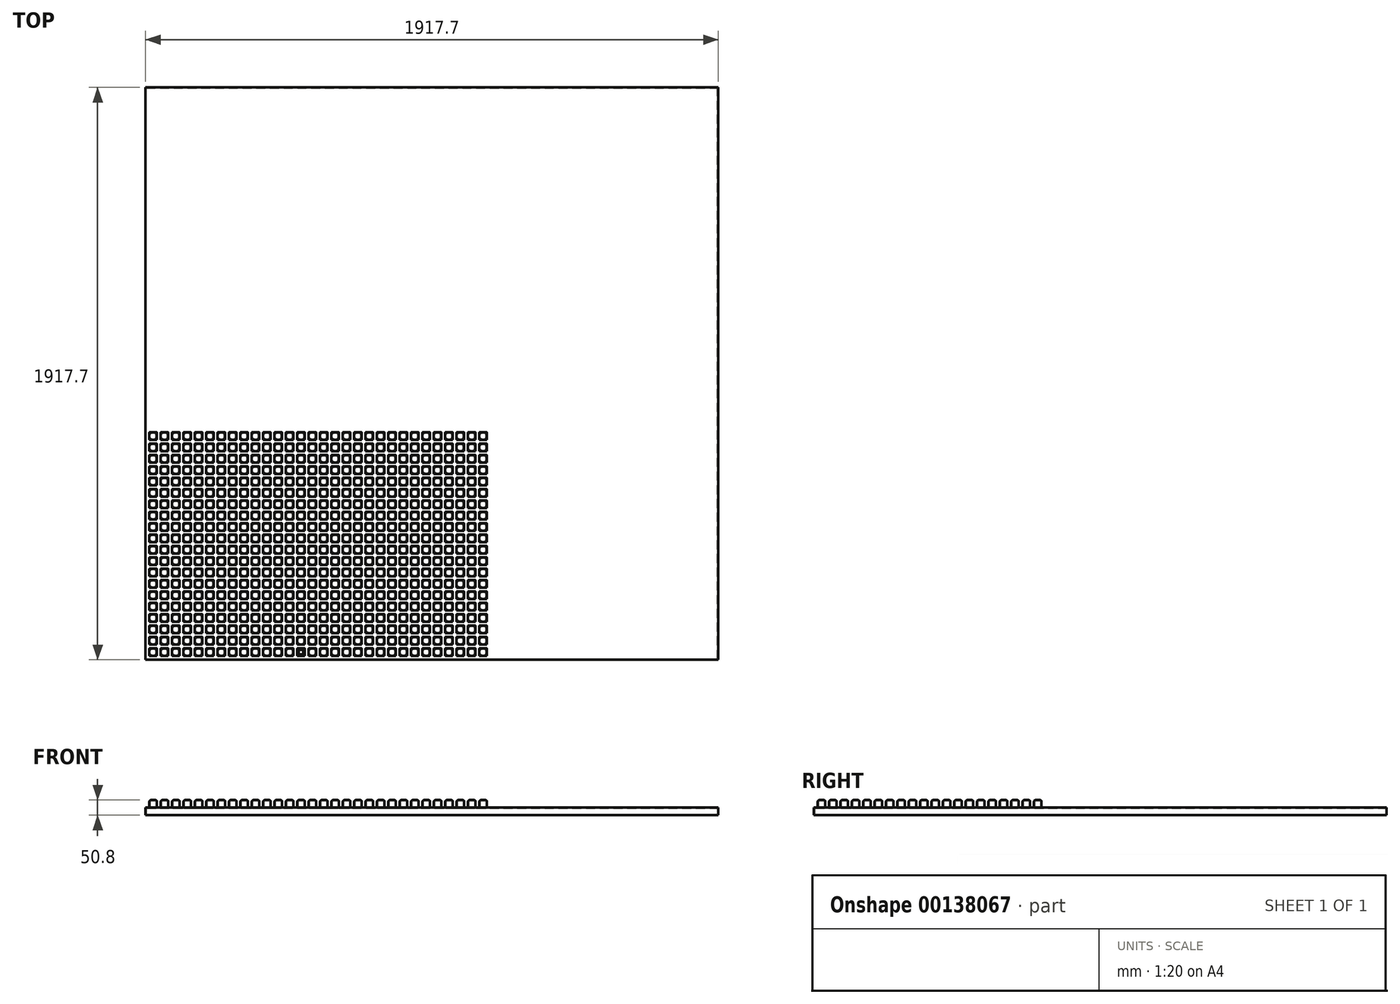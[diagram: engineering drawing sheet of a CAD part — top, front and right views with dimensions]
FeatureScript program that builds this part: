
annotation { "Feature Type Name" : "Feature", "Feature Type Description" : "" }
export const myFeature = defineFeature(function(context is Context, id is Id, definition is map)
    precondition{}
    {
        {
            var Q0;
            Q0=qCreatedBy(makeId("Top.planeOp"),FACE);
            var sketch = newSketch(context, id + "F0", { "sketchPlane" : qUnion([Q0])});
            skLineSegment(sketch, "E0.bottom", {"start": v(0, 0) * mm, "end": v(1917.7, 0) * mm});
            skLineSegment(sketch, "E0.top", {"start": v(0, 1917.7) * mm, "end": v(1917.7, 1917.7) * mm});
            skLineSegment(sketch, "E0.left", {"start": v(0, 0) * mm, "end": v(0, 1917.7) * mm});
            skLineSegment(sketch, "E0.right", {"start": v(1917.7, 0) * mm, "end": v(1917.7, 1917.7) * mm});
            skSolve(sketch);
        }
        {
            var Q0;
            Q0=makeQuery(id+"F0.imprint","IMPRINT",FACE,{"disambiguationData":[TD([[makeQuery(id+"F0.imprint","IMPRINT",EDGE,{"derivedFrom":sQuery(id+"F0.wireOp",EDGE,"E0.bottom")}),1.0]])]});
            extrude(context, id + "F1", {"entities" : qUnion([Q0]), "depth" : 25.4 * mm});
        }
        {
            var Q0;
            Q0=makeQuery(id+"F1.opExtrude","CAP_FACE",FACE,{"disambiguationData":[OSD([sQuery(id+"F0.wireOp",EDGE,"E0.bottom"),sQuery(id+"F0.wireOp",EDGE,"E0.top"),sQuery(id+"F0.wireOp",EDGE,"E0.left"),sQuery(id+"F0.wireOp",EDGE,"E0.right")])],"isStart":false});
            var sketch = newSketch(context, id + "F2", { "sketchPlane" : qUnion([Q0])});
            skLineSegment(sketch, "E1.bottom", {"start": v(12.7, 12.7) * mm, "end": v(38.1, 12.7) * mm});
            skLineSegment(sketch, "E1.top", {"start": v(12.7, 38.1) * mm, "end": v(38.1, 38.1) * mm});
            skLineSegment(sketch, "E1.left", {"start": v(12.7, 12.7) * mm, "end": v(12.7, 38.1) * mm});
            skLineSegment(sketch, "E1.right", {"start": v(38.1, 12.7) * mm, "end": v(38.1, 38.1) * mm});
            skLineSegment(sketch, "E2.0.1.0", {"start": v(38.1, 50.8) * mm, "end": v(38.1, 76.2) * mm});
            skLineSegment(sketch, "E2.0.1.1", {"start": v(12.7, 76.2) * mm, "end": v(38.1, 76.2) * mm});
            skLineSegment(sketch, "E2.0.1.2", {"start": v(12.7, 50.8) * mm, "end": v(38.1, 50.8) * mm});
            skLineSegment(sketch, "E2.0.1.3", {"start": v(12.7, 50.8) * mm, "end": v(12.7, 76.2) * mm});
            skLineSegment(sketch, "E2.0.2.0", {"start": v(38.1, 88.9) * mm, "end": v(38.1, 114.3) * mm});
            skLineSegment(sketch, "E2.0.2.1", {"start": v(12.7, 114.3) * mm, "end": v(38.1, 114.3) * mm});
            skLineSegment(sketch, "E2.0.2.2", {"start": v(12.7, 88.9) * mm, "end": v(38.1, 88.9) * mm});
            skLineSegment(sketch, "E2.0.2.3", {"start": v(12.7, 88.9) * mm, "end": v(12.7, 114.3) * mm});
            skLineSegment(sketch, "E2.0.3.0", {"start": v(38.1, 127) * mm, "end": v(38.1, 152.4) * mm});
            skLineSegment(sketch, "E2.0.3.1", {"start": v(12.7, 152.4) * mm, "end": v(38.1, 152.4) * mm});
            skLineSegment(sketch, "E2.0.3.2", {"start": v(12.7, 127) * mm, "end": v(38.1, 127) * mm});
            skLineSegment(sketch, "E2.0.3.3", {"start": v(12.7, 127) * mm, "end": v(12.7, 152.4) * mm});
            skLineSegment(sketch, "E2.0.4.0", {"start": v(38.1, 165.1) * mm, "end": v(38.1, 190.5) * mm});
            skLineSegment(sketch, "E2.0.4.1", {"start": v(12.7, 190.5) * mm, "end": v(38.1, 190.5) * mm});
            skLineSegment(sketch, "E2.0.4.2", {"start": v(12.7, 165.1) * mm, "end": v(38.1, 165.1) * mm});
            skLineSegment(sketch, "E2.0.4.3", {"start": v(12.7, 165.1) * mm, "end": v(12.7, 190.5) * mm});
            skLineSegment(sketch, "E2.0.5.0", {"start": v(38.1, 203.2) * mm, "end": v(38.1, 228.6) * mm});
            skLineSegment(sketch, "E2.0.5.1", {"start": v(12.7, 228.6) * mm, "end": v(38.1, 228.6) * mm});
            skLineSegment(sketch, "E2.0.5.2", {"start": v(12.7, 203.2) * mm, "end": v(38.1, 203.2) * mm});
            skLineSegment(sketch, "E2.0.5.3", {"start": v(12.7, 203.2) * mm, "end": v(12.7, 228.6) * mm});
            skLineSegment(sketch, "E2.0.6.0", {"start": v(38.1, 241.3) * mm, "end": v(38.1, 266.7) * mm});
            skLineSegment(sketch, "E2.0.6.1", {"start": v(12.7, 266.7) * mm, "end": v(38.1, 266.7) * mm});
            skLineSegment(sketch, "E2.0.6.2", {"start": v(12.7, 241.3) * mm, "end": v(38.1, 241.3) * mm});
            skLineSegment(sketch, "E2.0.6.3", {"start": v(12.7, 241.3) * mm, "end": v(12.7, 266.7) * mm});
            skLineSegment(sketch, "E2.0.7.0", {"start": v(38.1, 279.4) * mm, "end": v(38.1, 304.8) * mm});
            skLineSegment(sketch, "E2.0.7.1", {"start": v(12.7, 304.8) * mm, "end": v(38.1, 304.8) * mm});
            skLineSegment(sketch, "E2.0.7.2", {"start": v(12.7, 279.4) * mm, "end": v(38.1, 279.4) * mm});
            skLineSegment(sketch, "E2.0.7.3", {"start": v(12.7, 279.4) * mm, "end": v(12.7, 304.8) * mm});
            skLineSegment(sketch, "E2.0.8.0", {"start": v(38.1, 317.5) * mm, "end": v(38.1, 342.9) * mm});
            skLineSegment(sketch, "E2.0.8.1", {"start": v(12.7, 342.9) * mm, "end": v(38.1, 342.9) * mm});
            skLineSegment(sketch, "E2.0.8.2", {"start": v(12.7, 317.5) * mm, "end": v(38.1, 317.5) * mm});
            skLineSegment(sketch, "E2.0.8.3", {"start": v(12.7, 317.5) * mm, "end": v(12.7, 342.9) * mm});
            skLineSegment(sketch, "E2.0.9.0", {"start": v(38.1, 355.6) * mm, "end": v(38.1, 381) * mm});
            skLineSegment(sketch, "E2.0.9.1", {"start": v(12.7, 381) * mm, "end": v(38.1, 381) * mm});
            skLineSegment(sketch, "E2.0.9.2", {"start": v(12.7, 355.6) * mm, "end": v(38.1, 355.6) * mm});
            skLineSegment(sketch, "E2.0.9.3", {"start": v(12.7, 355.6) * mm, "end": v(12.7, 381) * mm});
            skLineSegment(sketch, "E2.0.10.0", {"start": v(38.1, 393.7) * mm, "end": v(38.1, 419.1) * mm});
            skLineSegment(sketch, "E2.0.10.1", {"start": v(12.7, 419.1) * mm, "end": v(38.1, 419.1) * mm});
            skLineSegment(sketch, "E2.0.10.2", {"start": v(12.7, 393.7) * mm, "end": v(38.1, 393.7) * mm});
            skLineSegment(sketch, "E2.0.10.3", {"start": v(12.7, 393.7) * mm, "end": v(12.7, 419.1) * mm});
            skLineSegment(sketch, "E2.0.11.0", {"start": v(38.1, 431.8) * mm, "end": v(38.1, 457.2) * mm});
            skLineSegment(sketch, "E2.0.11.1", {"start": v(12.7, 457.2) * mm, "end": v(38.1, 457.2) * mm});
            skLineSegment(sketch, "E2.0.11.2", {"start": v(12.7, 431.8) * mm, "end": v(38.1, 431.8) * mm});
            skLineSegment(sketch, "E2.0.11.3", {"start": v(12.7, 431.8) * mm, "end": v(12.7, 457.2) * mm});
            skLineSegment(sketch, "E2.0.12.0", {"start": v(38.1, 469.9) * mm, "end": v(38.1, 495.3) * mm});
            skLineSegment(sketch, "E2.0.12.1", {"start": v(12.7, 495.3) * mm, "end": v(38.1, 495.3) * mm});
            skLineSegment(sketch, "E2.0.12.2", {"start": v(12.7, 469.9) * mm, "end": v(38.1, 469.9) * mm});
            skLineSegment(sketch, "E2.0.12.3", {"start": v(12.7, 469.9) * mm, "end": v(12.7, 495.3) * mm});
            skLineSegment(sketch, "E2.0.13.0", {"start": v(38.1, 508) * mm, "end": v(38.1, 533.4) * mm});
            skLineSegment(sketch, "E2.0.13.1", {"start": v(12.7, 533.4) * mm, "end": v(38.1, 533.4) * mm});
            skLineSegment(sketch, "E2.0.13.2", {"start": v(12.7, 508) * mm, "end": v(38.1, 508) * mm});
            skLineSegment(sketch, "E2.0.13.3", {"start": v(12.7, 508) * mm, "end": v(12.7, 533.4) * mm});
            skLineSegment(sketch, "E2.0.14.0", {"start": v(38.1, 546.1) * mm, "end": v(38.1, 571.5) * mm});
            skLineSegment(sketch, "E2.0.14.1", {"start": v(12.7, 571.5) * mm, "end": v(38.1, 571.5) * mm});
            skLineSegment(sketch, "E2.0.14.2", {"start": v(12.7, 546.1) * mm, "end": v(38.1, 546.1) * mm});
            skLineSegment(sketch, "E2.0.14.3", {"start": v(12.7, 546.1) * mm, "end": v(12.7, 571.5) * mm});
            skLineSegment(sketch, "E2.0.15.0", {"start": v(38.1, 584.2) * mm, "end": v(38.1, 609.6) * mm});
            skLineSegment(sketch, "E2.0.15.1", {"start": v(12.7, 609.6) * mm, "end": v(38.1, 609.6) * mm});
            skLineSegment(sketch, "E2.0.15.2", {"start": v(12.7, 584.2) * mm, "end": v(38.1, 584.2) * mm});
            skLineSegment(sketch, "E2.0.15.3", {"start": v(12.7, 584.2) * mm, "end": v(12.7, 609.6) * mm});
            skLineSegment(sketch, "E2.0.16.0", {"start": v(38.1, 622.3) * mm, "end": v(38.1, 647.7) * mm});
            skLineSegment(sketch, "E2.0.16.1", {"start": v(12.7, 647.7) * mm, "end": v(38.1, 647.7) * mm});
            skLineSegment(sketch, "E2.0.16.2", {"start": v(12.7, 622.3) * mm, "end": v(38.1, 622.3) * mm});
            skLineSegment(sketch, "E2.0.16.3", {"start": v(12.7, 622.3) * mm, "end": v(12.7, 647.7) * mm});
            skLineSegment(sketch, "E2.0.17.0", {"start": v(38.1, 660.4) * mm, "end": v(38.1, 685.8) * mm});
            skLineSegment(sketch, "E2.0.17.1", {"start": v(12.7, 685.8) * mm, "end": v(38.1, 685.8) * mm});
            skLineSegment(sketch, "E2.0.17.2", {"start": v(12.7, 660.4) * mm, "end": v(38.1, 660.4) * mm});
            skLineSegment(sketch, "E2.0.17.3", {"start": v(12.7, 660.4) * mm, "end": v(12.7, 685.8) * mm});
            skLineSegment(sketch, "E2.0.18.0", {"start": v(38.1, 698.5) * mm, "end": v(38.1, 723.9) * mm});
            skLineSegment(sketch, "E2.0.18.1", {"start": v(12.7, 723.9) * mm, "end": v(38.1, 723.9) * mm});
            skLineSegment(sketch, "E2.0.18.2", {"start": v(12.7, 698.5) * mm, "end": v(38.1, 698.5) * mm});
            skLineSegment(sketch, "E2.0.18.3", {"start": v(12.7, 698.5) * mm, "end": v(12.7, 723.9) * mm});
            skLineSegment(sketch, "E2.0.19.0", {"start": v(38.1, 736.6) * mm, "end": v(38.1, 762) * mm});
            skLineSegment(sketch, "E2.0.19.1", {"start": v(12.7, 762) * mm, "end": v(38.1, 762) * mm});
            skLineSegment(sketch, "E2.0.19.2", {"start": v(12.7, 736.6) * mm, "end": v(38.1, 736.6) * mm});
            skLineSegment(sketch, "E2.0.19.3", {"start": v(12.7, 736.6) * mm, "end": v(12.7, 762) * mm});
            skLineSegment(sketch, "E2.1.0.0", {"start": v(76.2, 12.7) * mm, "end": v(76.2, 38.1) * mm});
            skLineSegment(sketch, "E2.1.0.1", {"start": v(50.8, 38.1) * mm, "end": v(76.2, 38.1) * mm});
            skLineSegment(sketch, "E2.1.0.2", {"start": v(50.8, 12.7) * mm, "end": v(76.2, 12.7) * mm});
            skLineSegment(sketch, "E2.1.0.3", {"start": v(50.8, 12.7) * mm, "end": v(50.8, 38.1) * mm});
            skLineSegment(sketch, "E2.1.1.0", {"start": v(76.2, 50.8) * mm, "end": v(76.2, 76.2) * mm});
            skLineSegment(sketch, "E2.1.1.1", {"start": v(50.8, 76.2) * mm, "end": v(76.2, 76.2) * mm});
            skLineSegment(sketch, "E2.1.1.2", {"start": v(50.8, 50.8) * mm, "end": v(76.2, 50.8) * mm});
            skLineSegment(sketch, "E2.1.1.3", {"start": v(50.8, 50.8) * mm, "end": v(50.8, 76.2) * mm});
            skLineSegment(sketch, "E2.1.2.0", {"start": v(76.2, 88.9) * mm, "end": v(76.2, 114.3) * mm});
            skLineSegment(sketch, "E2.1.2.1", {"start": v(50.8, 114.3) * mm, "end": v(76.2, 114.3) * mm});
            skLineSegment(sketch, "E2.1.2.2", {"start": v(50.8, 88.9) * mm, "end": v(76.2, 88.9) * mm});
            skLineSegment(sketch, "E2.1.2.3", {"start": v(50.8, 88.9) * mm, "end": v(50.8, 114.3) * mm});
            skLineSegment(sketch, "E2.1.3.0", {"start": v(76.2, 127) * mm, "end": v(76.2, 152.4) * mm});
            skLineSegment(sketch, "E2.1.3.1", {"start": v(50.8, 152.4) * mm, "end": v(76.2, 152.4) * mm});
            skLineSegment(sketch, "E2.1.3.2", {"start": v(50.8, 127) * mm, "end": v(76.2, 127) * mm});
            skLineSegment(sketch, "E2.1.3.3", {"start": v(50.8, 127) * mm, "end": v(50.8, 152.4) * mm});
            skLineSegment(sketch, "E2.1.4.0", {"start": v(76.2, 165.1) * mm, "end": v(76.2, 190.5) * mm});
            skLineSegment(sketch, "E2.1.4.1", {"start": v(50.8, 190.5) * mm, "end": v(76.2, 190.5) * mm});
            skLineSegment(sketch, "E2.1.4.2", {"start": v(50.8, 165.1) * mm, "end": v(76.2, 165.1) * mm});
            skLineSegment(sketch, "E2.1.4.3", {"start": v(50.8, 165.1) * mm, "end": v(50.8, 190.5) * mm});
            skLineSegment(sketch, "E2.1.5.0", {"start": v(76.2, 203.2) * mm, "end": v(76.2, 228.6) * mm});
            skLineSegment(sketch, "E2.1.5.1", {"start": v(50.8, 228.6) * mm, "end": v(76.2, 228.6) * mm});
            skLineSegment(sketch, "E2.1.5.2", {"start": v(50.8, 203.2) * mm, "end": v(76.2, 203.2) * mm});
            skLineSegment(sketch, "E2.1.5.3", {"start": v(50.8, 203.2) * mm, "end": v(50.8, 228.6) * mm});
            skLineSegment(sketch, "E2.1.6.0", {"start": v(76.2, 241.3) * mm, "end": v(76.2, 266.7) * mm});
            skLineSegment(sketch, "E2.1.6.1", {"start": v(50.8, 266.7) * mm, "end": v(76.2, 266.7) * mm});
            skLineSegment(sketch, "E2.1.6.2", {"start": v(50.8, 241.3) * mm, "end": v(76.2, 241.3) * mm});
            skLineSegment(sketch, "E2.1.6.3", {"start": v(50.8, 241.3) * mm, "end": v(50.8, 266.7) * mm});
            skLineSegment(sketch, "E2.1.7.0", {"start": v(76.2, 279.4) * mm, "end": v(76.2, 304.8) * mm});
            skLineSegment(sketch, "E2.1.7.1", {"start": v(50.8, 304.8) * mm, "end": v(76.2, 304.8) * mm});
            skLineSegment(sketch, "E2.1.7.2", {"start": v(50.8, 279.4) * mm, "end": v(76.2, 279.4) * mm});
            skLineSegment(sketch, "E2.1.7.3", {"start": v(50.8, 279.4) * mm, "end": v(50.8, 304.8) * mm});
            skLineSegment(sketch, "E2.1.8.0", {"start": v(76.2, 317.5) * mm, "end": v(76.2, 342.9) * mm});
            skLineSegment(sketch, "E2.1.8.1", {"start": v(50.8, 342.9) * mm, "end": v(76.2, 342.9) * mm});
            skLineSegment(sketch, "E2.1.8.2", {"start": v(50.8, 317.5) * mm, "end": v(76.2, 317.5) * mm});
            skLineSegment(sketch, "E2.1.8.3", {"start": v(50.8, 317.5) * mm, "end": v(50.8, 342.9) * mm});
            skLineSegment(sketch, "E2.1.9.0", {"start": v(76.2, 355.6) * mm, "end": v(76.2, 381) * mm});
            skLineSegment(sketch, "E2.1.9.1", {"start": v(50.8, 381) * mm, "end": v(76.2, 381) * mm});
            skLineSegment(sketch, "E2.1.9.2", {"start": v(50.8, 355.6) * mm, "end": v(76.2, 355.6) * mm});
            skLineSegment(sketch, "E2.1.9.3", {"start": v(50.8, 355.6) * mm, "end": v(50.8, 381) * mm});
            skLineSegment(sketch, "E2.1.10.0", {"start": v(76.2, 393.7) * mm, "end": v(76.2, 419.1) * mm});
            skLineSegment(sketch, "E2.1.10.1", {"start": v(50.8, 419.1) * mm, "end": v(76.2, 419.1) * mm});
            skLineSegment(sketch, "E2.1.10.2", {"start": v(50.8, 393.7) * mm, "end": v(76.2, 393.7) * mm});
            skLineSegment(sketch, "E2.1.10.3", {"start": v(50.8, 393.7) * mm, "end": v(50.8, 419.1) * mm});
            skLineSegment(sketch, "E2.1.11.0", {"start": v(76.2, 431.8) * mm, "end": v(76.2, 457.2) * mm});
            skLineSegment(sketch, "E2.1.11.1", {"start": v(50.8, 457.2) * mm, "end": v(76.2, 457.2) * mm});
            skLineSegment(sketch, "E2.1.11.2", {"start": v(50.8, 431.8) * mm, "end": v(76.2, 431.8) * mm});
            skLineSegment(sketch, "E2.1.11.3", {"start": v(50.8, 431.8) * mm, "end": v(50.8, 457.2) * mm});
            skLineSegment(sketch, "E2.1.12.0", {"start": v(76.2, 469.9) * mm, "end": v(76.2, 495.3) * mm});
            skLineSegment(sketch, "E2.1.12.1", {"start": v(50.8, 495.3) * mm, "end": v(76.2, 495.3) * mm});
            skLineSegment(sketch, "E2.1.12.2", {"start": v(50.8, 469.9) * mm, "end": v(76.2, 469.9) * mm});
            skLineSegment(sketch, "E2.1.12.3", {"start": v(50.8, 469.9) * mm, "end": v(50.8, 495.3) * mm});
            skLineSegment(sketch, "E2.1.13.0", {"start": v(76.2, 508) * mm, "end": v(76.2, 533.4) * mm});
            skLineSegment(sketch, "E2.1.13.1", {"start": v(50.8, 533.4) * mm, "end": v(76.2, 533.4) * mm});
            skLineSegment(sketch, "E2.1.13.2", {"start": v(50.8, 508) * mm, "end": v(76.2, 508) * mm});
            skLineSegment(sketch, "E2.1.13.3", {"start": v(50.8, 508) * mm, "end": v(50.8, 533.4) * mm});
            skLineSegment(sketch, "E2.1.14.0", {"start": v(76.2, 546.1) * mm, "end": v(76.2, 571.5) * mm});
            skLineSegment(sketch, "E2.1.14.1", {"start": v(50.8, 571.5) * mm, "end": v(76.2, 571.5) * mm});
            skLineSegment(sketch, "E2.1.14.2", {"start": v(50.8, 546.1) * mm, "end": v(76.2, 546.1) * mm});
            skLineSegment(sketch, "E2.1.14.3", {"start": v(50.8, 546.1) * mm, "end": v(50.8, 571.5) * mm});
            skLineSegment(sketch, "E2.1.15.0", {"start": v(76.2, 584.2) * mm, "end": v(76.2, 609.6) * mm});
            skLineSegment(sketch, "E2.1.15.1", {"start": v(50.8, 609.6) * mm, "end": v(76.2, 609.6) * mm});
            skLineSegment(sketch, "E2.1.15.2", {"start": v(50.8, 584.2) * mm, "end": v(76.2, 584.2) * mm});
            skLineSegment(sketch, "E2.1.15.3", {"start": v(50.8, 584.2) * mm, "end": v(50.8, 609.6) * mm});
            skLineSegment(sketch, "E2.1.16.0", {"start": v(76.2, 622.3) * mm, "end": v(76.2, 647.7) * mm});
            skLineSegment(sketch, "E2.1.16.1", {"start": v(50.8, 647.7) * mm, "end": v(76.2, 647.7) * mm});
            skLineSegment(sketch, "E2.1.16.2", {"start": v(50.8, 622.3) * mm, "end": v(76.2, 622.3) * mm});
            skLineSegment(sketch, "E2.1.16.3", {"start": v(50.8, 622.3) * mm, "end": v(50.8, 647.7) * mm});
            skLineSegment(sketch, "E2.1.17.0", {"start": v(76.2, 660.4) * mm, "end": v(76.2, 685.8) * mm});
            skLineSegment(sketch, "E2.1.17.1", {"start": v(50.8, 685.8) * mm, "end": v(76.2, 685.8) * mm});
            skLineSegment(sketch, "E2.1.17.2", {"start": v(50.8, 660.4) * mm, "end": v(76.2, 660.4) * mm});
            skLineSegment(sketch, "E2.1.17.3", {"start": v(50.8, 660.4) * mm, "end": v(50.8, 685.8) * mm});
            skLineSegment(sketch, "E2.1.18.0", {"start": v(76.2, 698.5) * mm, "end": v(76.2, 723.9) * mm});
            skLineSegment(sketch, "E2.1.18.1", {"start": v(50.8, 723.9) * mm, "end": v(76.2, 723.9) * mm});
            skLineSegment(sketch, "E2.1.18.2", {"start": v(50.8, 698.5) * mm, "end": v(76.2, 698.5) * mm});
            skLineSegment(sketch, "E2.1.18.3", {"start": v(50.8, 698.5) * mm, "end": v(50.8, 723.9) * mm});
            skLineSegment(sketch, "E2.1.19.0", {"start": v(76.2, 736.6) * mm, "end": v(76.2, 762) * mm});
            skLineSegment(sketch, "E2.1.19.1", {"start": v(50.8, 762) * mm, "end": v(76.2, 762) * mm});
            skLineSegment(sketch, "E2.1.19.2", {"start": v(50.8, 736.6) * mm, "end": v(76.2, 736.6) * mm});
            skLineSegment(sketch, "E2.1.19.3", {"start": v(50.8, 736.6) * mm, "end": v(50.8, 762) * mm});
            skLineSegment(sketch, "E2.2.0.0", {"start": v(114.3, 12.7) * mm, "end": v(114.3, 38.1) * mm});
            skLineSegment(sketch, "E2.2.0.1", {"start": v(88.9, 38.1) * mm, "end": v(114.3, 38.1) * mm});
            skLineSegment(sketch, "E2.2.0.2", {"start": v(88.9, 12.7) * mm, "end": v(114.3, 12.7) * mm});
            skLineSegment(sketch, "E2.2.0.3", {"start": v(88.9, 12.7) * mm, "end": v(88.9, 38.1) * mm});
            skLineSegment(sketch, "E2.2.1.0", {"start": v(114.3, 50.8) * mm, "end": v(114.3, 76.2) * mm});
            skLineSegment(sketch, "E2.2.1.1", {"start": v(88.9, 76.2) * mm, "end": v(114.3, 76.2) * mm});
            skLineSegment(sketch, "E2.2.1.2", {"start": v(88.9, 50.8) * mm, "end": v(114.3, 50.8) * mm});
            skLineSegment(sketch, "E2.2.1.3", {"start": v(88.9, 50.8) * mm, "end": v(88.9, 76.2) * mm});
            skLineSegment(sketch, "E2.2.2.0", {"start": v(114.3, 88.9) * mm, "end": v(114.3, 114.3) * mm});
            skLineSegment(sketch, "E2.2.2.1", {"start": v(88.9, 114.3) * mm, "end": v(114.3, 114.3) * mm});
            skLineSegment(sketch, "E2.2.2.2", {"start": v(88.9, 88.9) * mm, "end": v(114.3, 88.9) * mm});
            skLineSegment(sketch, "E2.2.2.3", {"start": v(88.9, 88.9) * mm, "end": v(88.9, 114.3) * mm});
            skLineSegment(sketch, "E2.2.3.0", {"start": v(114.3, 127) * mm, "end": v(114.3, 152.4) * mm});
            skLineSegment(sketch, "E2.2.3.1", {"start": v(88.9, 152.4) * mm, "end": v(114.3, 152.4) * mm});
            skLineSegment(sketch, "E2.2.3.2", {"start": v(88.9, 127) * mm, "end": v(114.3, 127) * mm});
            skLineSegment(sketch, "E2.2.3.3", {"start": v(88.9, 127) * mm, "end": v(88.9, 152.4) * mm});
            skLineSegment(sketch, "E2.2.4.0", {"start": v(114.3, 165.1) * mm, "end": v(114.3, 190.5) * mm});
            skLineSegment(sketch, "E2.2.4.1", {"start": v(88.9, 190.5) * mm, "end": v(114.3, 190.5) * mm});
            skLineSegment(sketch, "E2.2.4.2", {"start": v(88.9, 165.1) * mm, "end": v(114.3, 165.1) * mm});
            skLineSegment(sketch, "E2.2.4.3", {"start": v(88.9, 165.1) * mm, "end": v(88.9, 190.5) * mm});
            skLineSegment(sketch, "E2.2.5.0", {"start": v(114.3, 203.2) * mm, "end": v(114.3, 228.6) * mm});
            skLineSegment(sketch, "E2.2.5.1", {"start": v(88.9, 228.6) * mm, "end": v(114.3, 228.6) * mm});
            skLineSegment(sketch, "E2.2.5.2", {"start": v(88.9, 203.2) * mm, "end": v(114.3, 203.2) * mm});
            skLineSegment(sketch, "E2.2.5.3", {"start": v(88.9, 203.2) * mm, "end": v(88.9, 228.6) * mm});
            skLineSegment(sketch, "E2.2.6.0", {"start": v(114.3, 241.3) * mm, "end": v(114.3, 266.7) * mm});
            skLineSegment(sketch, "E2.2.6.1", {"start": v(88.9, 266.7) * mm, "end": v(114.3, 266.7) * mm});
            skLineSegment(sketch, "E2.2.6.2", {"start": v(88.9, 241.3) * mm, "end": v(114.3, 241.3) * mm});
            skLineSegment(sketch, "E2.2.6.3", {"start": v(88.9, 241.3) * mm, "end": v(88.9, 266.7) * mm});
            skLineSegment(sketch, "E2.2.7.0", {"start": v(114.3, 279.4) * mm, "end": v(114.3, 304.8) * mm});
            skLineSegment(sketch, "E2.2.7.1", {"start": v(88.9, 304.8) * mm, "end": v(114.3, 304.8) * mm});
            skLineSegment(sketch, "E2.2.7.2", {"start": v(88.9, 279.4) * mm, "end": v(114.3, 279.4) * mm});
            skLineSegment(sketch, "E2.2.7.3", {"start": v(88.9, 279.4) * mm, "end": v(88.9, 304.8) * mm});
            skLineSegment(sketch, "E2.2.8.0", {"start": v(114.3, 317.5) * mm, "end": v(114.3, 342.9) * mm});
            skLineSegment(sketch, "E2.2.8.1", {"start": v(88.9, 342.9) * mm, "end": v(114.3, 342.9) * mm});
            skLineSegment(sketch, "E2.2.8.2", {"start": v(88.9, 317.5) * mm, "end": v(114.3, 317.5) * mm});
            skLineSegment(sketch, "E2.2.8.3", {"start": v(88.9, 317.5) * mm, "end": v(88.9, 342.9) * mm});
            skLineSegment(sketch, "E2.2.9.0", {"start": v(114.3, 355.6) * mm, "end": v(114.3, 381) * mm});
            skLineSegment(sketch, "E2.2.9.1", {"start": v(88.9, 381) * mm, "end": v(114.3, 381) * mm});
            skLineSegment(sketch, "E2.2.9.2", {"start": v(88.9, 355.6) * mm, "end": v(114.3, 355.6) * mm});
            skLineSegment(sketch, "E2.2.9.3", {"start": v(88.9, 355.6) * mm, "end": v(88.9, 381) * mm});
            skLineSegment(sketch, "E2.2.10.0", {"start": v(114.3, 393.7) * mm, "end": v(114.3, 419.1) * mm});
            skLineSegment(sketch, "E2.2.10.1", {"start": v(88.9, 419.1) * mm, "end": v(114.3, 419.1) * mm});
            skLineSegment(sketch, "E2.2.10.2", {"start": v(88.9, 393.7) * mm, "end": v(114.3, 393.7) * mm});
            skLineSegment(sketch, "E2.2.10.3", {"start": v(88.9, 393.7) * mm, "end": v(88.9, 419.1) * mm});
            skLineSegment(sketch, "E2.2.11.0", {"start": v(114.3, 431.8) * mm, "end": v(114.3, 457.2) * mm});
            skLineSegment(sketch, "E2.2.11.1", {"start": v(88.9, 457.2) * mm, "end": v(114.3, 457.2) * mm});
            skLineSegment(sketch, "E2.2.11.2", {"start": v(88.9, 431.8) * mm, "end": v(114.3, 431.8) * mm});
            skLineSegment(sketch, "E2.2.11.3", {"start": v(88.9, 431.8) * mm, "end": v(88.9, 457.2) * mm});
            skLineSegment(sketch, "E2.2.12.0", {"start": v(114.3, 469.9) * mm, "end": v(114.3, 495.3) * mm});
            skLineSegment(sketch, "E2.2.12.1", {"start": v(88.9, 495.3) * mm, "end": v(114.3, 495.3) * mm});
            skLineSegment(sketch, "E2.2.12.2", {"start": v(88.9, 469.9) * mm, "end": v(114.3, 469.9) * mm});
            skLineSegment(sketch, "E2.2.12.3", {"start": v(88.9, 469.9) * mm, "end": v(88.9, 495.3) * mm});
            skLineSegment(sketch, "E2.2.13.0", {"start": v(114.3, 508) * mm, "end": v(114.3, 533.4) * mm});
            skLineSegment(sketch, "E2.2.13.1", {"start": v(88.9, 533.4) * mm, "end": v(114.3, 533.4) * mm});
            skLineSegment(sketch, "E2.2.13.2", {"start": v(88.9, 508) * mm, "end": v(114.3, 508) * mm});
            skLineSegment(sketch, "E2.2.13.3", {"start": v(88.9, 508) * mm, "end": v(88.9, 533.4) * mm});
            skLineSegment(sketch, "E2.2.14.0", {"start": v(114.3, 546.1) * mm, "end": v(114.3, 571.5) * mm});
            skLineSegment(sketch, "E2.2.14.1", {"start": v(88.9, 571.5) * mm, "end": v(114.3, 571.5) * mm});
            skLineSegment(sketch, "E2.2.14.2", {"start": v(88.9, 546.1) * mm, "end": v(114.3, 546.1) * mm});
            skLineSegment(sketch, "E2.2.14.3", {"start": v(88.9, 546.1) * mm, "end": v(88.9, 571.5) * mm});
            skLineSegment(sketch, "E2.2.15.0", {"start": v(114.3, 584.2) * mm, "end": v(114.3, 609.6) * mm});
            skLineSegment(sketch, "E2.2.15.1", {"start": v(88.9, 609.6) * mm, "end": v(114.3, 609.6) * mm});
            skLineSegment(sketch, "E2.2.15.2", {"start": v(88.9, 584.2) * mm, "end": v(114.3, 584.2) * mm});
            skLineSegment(sketch, "E2.2.15.3", {"start": v(88.9, 584.2) * mm, "end": v(88.9, 609.6) * mm});
            skLineSegment(sketch, "E2.2.16.0", {"start": v(114.3, 622.3) * mm, "end": v(114.3, 647.7) * mm});
            skLineSegment(sketch, "E2.2.16.1", {"start": v(88.9, 647.7) * mm, "end": v(114.3, 647.7) * mm});
            skLineSegment(sketch, "E2.2.16.2", {"start": v(88.9, 622.3) * mm, "end": v(114.3, 622.3) * mm});
            skLineSegment(sketch, "E2.2.16.3", {"start": v(88.9, 622.3) * mm, "end": v(88.9, 647.7) * mm});
            skLineSegment(sketch, "E2.2.17.0", {"start": v(114.3, 660.4) * mm, "end": v(114.3, 685.8) * mm});
            skLineSegment(sketch, "E2.2.17.1", {"start": v(88.9, 685.8) * mm, "end": v(114.3, 685.8) * mm});
            skLineSegment(sketch, "E2.2.17.2", {"start": v(88.9, 660.4) * mm, "end": v(114.3, 660.4) * mm});
            skLineSegment(sketch, "E2.2.17.3", {"start": v(88.9, 660.4) * mm, "end": v(88.9, 685.8) * mm});
            skLineSegment(sketch, "E2.2.18.0", {"start": v(114.3, 698.5) * mm, "end": v(114.3, 723.9) * mm});
            skLineSegment(sketch, "E2.2.18.1", {"start": v(88.9, 723.9) * mm, "end": v(114.3, 723.9) * mm});
            skLineSegment(sketch, "E2.2.18.2", {"start": v(88.9, 698.5) * mm, "end": v(114.3, 698.5) * mm});
            skLineSegment(sketch, "E2.2.18.3", {"start": v(88.9, 698.5) * mm, "end": v(88.9, 723.9) * mm});
            skLineSegment(sketch, "E2.2.19.0", {"start": v(114.3, 736.6) * mm, "end": v(114.3, 762) * mm});
            skLineSegment(sketch, "E2.2.19.1", {"start": v(88.9, 762) * mm, "end": v(114.3, 762) * mm});
            skLineSegment(sketch, "E2.2.19.2", {"start": v(88.9, 736.6) * mm, "end": v(114.3, 736.6) * mm});
            skLineSegment(sketch, "E2.2.19.3", {"start": v(88.9, 736.6) * mm, "end": v(88.9, 762) * mm});
            skLineSegment(sketch, "E2.3.0.0", {"start": v(152.4, 12.7) * mm, "end": v(152.4, 38.1) * mm});
            skLineSegment(sketch, "E2.3.0.1", {"start": v(127, 38.1) * mm, "end": v(152.4, 38.1) * mm});
            skLineSegment(sketch, "E2.3.0.2", {"start": v(127, 12.7) * mm, "end": v(152.4, 12.7) * mm});
            skLineSegment(sketch, "E2.3.0.3", {"start": v(127, 12.7) * mm, "end": v(127, 38.1) * mm});
            skLineSegment(sketch, "E2.3.1.0", {"start": v(152.4, 50.8) * mm, "end": v(152.4, 76.2) * mm});
            skLineSegment(sketch, "E2.3.1.1", {"start": v(127, 76.2) * mm, "end": v(152.4, 76.2) * mm});
            skLineSegment(sketch, "E2.3.1.2", {"start": v(127, 50.8) * mm, "end": v(152.4, 50.8) * mm});
            skLineSegment(sketch, "E2.3.1.3", {"start": v(127, 50.8) * mm, "end": v(127, 76.2) * mm});
            skLineSegment(sketch, "E2.3.2.0", {"start": v(152.4, 88.9) * mm, "end": v(152.4, 114.3) * mm});
            skLineSegment(sketch, "E2.3.2.1", {"start": v(127, 114.3) * mm, "end": v(152.4, 114.3) * mm});
            skLineSegment(sketch, "E2.3.2.2", {"start": v(127, 88.9) * mm, "end": v(152.4, 88.9) * mm});
            skLineSegment(sketch, "E2.3.2.3", {"start": v(127, 88.9) * mm, "end": v(127, 114.3) * mm});
            skLineSegment(sketch, "E2.3.3.0", {"start": v(152.4, 127) * mm, "end": v(152.4, 152.4) * mm});
            skLineSegment(sketch, "E2.3.3.1", {"start": v(127, 152.4) * mm, "end": v(152.4, 152.4) * mm});
            skLineSegment(sketch, "E2.3.3.2", {"start": v(127, 127) * mm, "end": v(152.4, 127) * mm});
            skLineSegment(sketch, "E2.3.3.3", {"start": v(127, 127) * mm, "end": v(127, 152.4) * mm});
            skLineSegment(sketch, "E2.3.4.0", {"start": v(152.4, 165.1) * mm, "end": v(152.4, 190.5) * mm});
            skLineSegment(sketch, "E2.3.4.1", {"start": v(127, 190.5) * mm, "end": v(152.4, 190.5) * mm});
            skLineSegment(sketch, "E2.3.4.2", {"start": v(127, 165.1) * mm, "end": v(152.4, 165.1) * mm});
            skLineSegment(sketch, "E2.3.4.3", {"start": v(127, 165.1) * mm, "end": v(127, 190.5) * mm});
            skLineSegment(sketch, "E2.3.5.0", {"start": v(152.4, 203.2) * mm, "end": v(152.4, 228.6) * mm});
            skLineSegment(sketch, "E2.3.5.1", {"start": v(127, 228.6) * mm, "end": v(152.4, 228.6) * mm});
            skLineSegment(sketch, "E2.3.5.2", {"start": v(127, 203.2) * mm, "end": v(152.4, 203.2) * mm});
            skLineSegment(sketch, "E2.3.5.3", {"start": v(127, 203.2) * mm, "end": v(127, 228.6) * mm});
            skLineSegment(sketch, "E2.3.6.0", {"start": v(152.4, 241.3) * mm, "end": v(152.4, 266.7) * mm});
            skLineSegment(sketch, "E2.3.6.1", {"start": v(127, 266.7) * mm, "end": v(152.4, 266.7) * mm});
            skLineSegment(sketch, "E2.3.6.2", {"start": v(127, 241.3) * mm, "end": v(152.4, 241.3) * mm});
            skLineSegment(sketch, "E2.3.6.3", {"start": v(127, 241.3) * mm, "end": v(127, 266.7) * mm});
            skLineSegment(sketch, "E2.3.7.0", {"start": v(152.4, 279.4) * mm, "end": v(152.4, 304.8) * mm});
            skLineSegment(sketch, "E2.3.7.1", {"start": v(127, 304.8) * mm, "end": v(152.4, 304.8) * mm});
            skLineSegment(sketch, "E2.3.7.2", {"start": v(127, 279.4) * mm, "end": v(152.4, 279.4) * mm});
            skLineSegment(sketch, "E2.3.7.3", {"start": v(127, 279.4) * mm, "end": v(127, 304.8) * mm});
            skLineSegment(sketch, "E2.3.8.0", {"start": v(152.4, 317.5) * mm, "end": v(152.4, 342.9) * mm});
            skLineSegment(sketch, "E2.3.8.1", {"start": v(127, 342.9) * mm, "end": v(152.4, 342.9) * mm});
            skLineSegment(sketch, "E2.3.8.2", {"start": v(127, 317.5) * mm, "end": v(152.4, 317.5) * mm});
            skLineSegment(sketch, "E2.3.8.3", {"start": v(127, 317.5) * mm, "end": v(127, 342.9) * mm});
            skLineSegment(sketch, "E2.3.9.0", {"start": v(152.4, 355.6) * mm, "end": v(152.4, 381) * mm});
            skLineSegment(sketch, "E2.3.9.1", {"start": v(127, 381) * mm, "end": v(152.4, 381) * mm});
            skLineSegment(sketch, "E2.3.9.2", {"start": v(127, 355.6) * mm, "end": v(152.4, 355.6) * mm});
            skLineSegment(sketch, "E2.3.9.3", {"start": v(127, 355.6) * mm, "end": v(127, 381) * mm});
            skLineSegment(sketch, "E2.3.10.0", {"start": v(152.4, 393.7) * mm, "end": v(152.4, 419.1) * mm});
            skLineSegment(sketch, "E2.3.10.1", {"start": v(127, 419.1) * mm, "end": v(152.4, 419.1) * mm});
            skLineSegment(sketch, "E2.3.10.2", {"start": v(127, 393.7) * mm, "end": v(152.4, 393.7) * mm});
            skLineSegment(sketch, "E2.3.10.3", {"start": v(127, 393.7) * mm, "end": v(127, 419.1) * mm});
            skLineSegment(sketch, "E2.3.11.0", {"start": v(152.4, 431.8) * mm, "end": v(152.4, 457.2) * mm});
            skLineSegment(sketch, "E2.3.11.1", {"start": v(127, 457.2) * mm, "end": v(152.4, 457.2) * mm});
            skLineSegment(sketch, "E2.3.11.2", {"start": v(127, 431.8) * mm, "end": v(152.4, 431.8) * mm});
            skLineSegment(sketch, "E2.3.11.3", {"start": v(127, 431.8) * mm, "end": v(127, 457.2) * mm});
            skLineSegment(sketch, "E2.3.12.0", {"start": v(152.4, 469.9) * mm, "end": v(152.4, 495.3) * mm});
            skLineSegment(sketch, "E2.3.12.1", {"start": v(127, 495.3) * mm, "end": v(152.4, 495.3) * mm});
            skLineSegment(sketch, "E2.3.12.2", {"start": v(127, 469.9) * mm, "end": v(152.4, 469.9) * mm});
            skLineSegment(sketch, "E2.3.12.3", {"start": v(127, 469.9) * mm, "end": v(127, 495.3) * mm});
            skLineSegment(sketch, "E2.3.13.0", {"start": v(152.4, 508) * mm, "end": v(152.4, 533.4) * mm});
            skLineSegment(sketch, "E2.3.13.1", {"start": v(127, 533.4) * mm, "end": v(152.4, 533.4) * mm});
            skLineSegment(sketch, "E2.3.13.2", {"start": v(127, 508) * mm, "end": v(152.4, 508) * mm});
            skLineSegment(sketch, "E2.3.13.3", {"start": v(127, 508) * mm, "end": v(127, 533.4) * mm});
            skLineSegment(sketch, "E2.3.14.0", {"start": v(152.4, 546.1) * mm, "end": v(152.4, 571.5) * mm});
            skLineSegment(sketch, "E2.3.14.1", {"start": v(127, 571.5) * mm, "end": v(152.4, 571.5) * mm});
            skLineSegment(sketch, "E2.3.14.2", {"start": v(127, 546.1) * mm, "end": v(152.4, 546.1) * mm});
            skLineSegment(sketch, "E2.3.14.3", {"start": v(127, 546.1) * mm, "end": v(127, 571.5) * mm});
            skLineSegment(sketch, "E2.3.15.0", {"start": v(152.4, 584.2) * mm, "end": v(152.4, 609.6) * mm});
            skLineSegment(sketch, "E2.3.15.1", {"start": v(127, 609.6) * mm, "end": v(152.4, 609.6) * mm});
            skLineSegment(sketch, "E2.3.15.2", {"start": v(127, 584.2) * mm, "end": v(152.4, 584.2) * mm});
            skLineSegment(sketch, "E2.3.15.3", {"start": v(127, 584.2) * mm, "end": v(127, 609.6) * mm});
            skLineSegment(sketch, "E2.3.16.0", {"start": v(152.4, 622.3) * mm, "end": v(152.4, 647.7) * mm});
            skLineSegment(sketch, "E2.3.16.1", {"start": v(127, 647.7) * mm, "end": v(152.4, 647.7) * mm});
            skLineSegment(sketch, "E2.3.16.2", {"start": v(127, 622.3) * mm, "end": v(152.4, 622.3) * mm});
            skLineSegment(sketch, "E2.3.16.3", {"start": v(127, 622.3) * mm, "end": v(127, 647.7) * mm});
            skLineSegment(sketch, "E2.3.17.0", {"start": v(152.4, 660.4) * mm, "end": v(152.4, 685.8) * mm});
            skLineSegment(sketch, "E2.3.17.1", {"start": v(127, 685.8) * mm, "end": v(152.4, 685.8) * mm});
            skLineSegment(sketch, "E2.3.17.2", {"start": v(127, 660.4) * mm, "end": v(152.4, 660.4) * mm});
            skLineSegment(sketch, "E2.3.17.3", {"start": v(127, 660.4) * mm, "end": v(127, 685.8) * mm});
            skLineSegment(sketch, "E2.3.18.0", {"start": v(152.4, 698.5) * mm, "end": v(152.4, 723.9) * mm});
            skLineSegment(sketch, "E2.3.18.1", {"start": v(127, 723.9) * mm, "end": v(152.4, 723.9) * mm});
            skLineSegment(sketch, "E2.3.18.2", {"start": v(127, 698.5) * mm, "end": v(152.4, 698.5) * mm});
            skLineSegment(sketch, "E2.3.18.3", {"start": v(127, 698.5) * mm, "end": v(127, 723.9) * mm});
            skLineSegment(sketch, "E2.3.19.0", {"start": v(152.4, 736.6) * mm, "end": v(152.4, 762) * mm});
            skLineSegment(sketch, "E2.3.19.1", {"start": v(127, 762) * mm, "end": v(152.4, 762) * mm});
            skLineSegment(sketch, "E2.3.19.2", {"start": v(127, 736.6) * mm, "end": v(152.4, 736.6) * mm});
            skLineSegment(sketch, "E2.3.19.3", {"start": v(127, 736.6) * mm, "end": v(127, 762) * mm});
            skLineSegment(sketch, "E2.4.0.0", {"start": v(190.5, 12.7) * mm, "end": v(190.5, 38.1) * mm});
            skLineSegment(sketch, "E2.4.0.1", {"start": v(165.1, 38.1) * mm, "end": v(190.5, 38.1) * mm});
            skLineSegment(sketch, "E2.4.0.2", {"start": v(165.1, 12.7) * mm, "end": v(190.5, 12.7) * mm});
            skLineSegment(sketch, "E2.4.0.3", {"start": v(165.1, 12.7) * mm, "end": v(165.1, 38.1) * mm});
            skLineSegment(sketch, "E2.4.1.0", {"start": v(190.5, 50.8) * mm, "end": v(190.5, 76.2) * mm});
            skLineSegment(sketch, "E2.4.1.1", {"start": v(165.1, 76.2) * mm, "end": v(190.5, 76.2) * mm});
            skLineSegment(sketch, "E2.4.1.2", {"start": v(165.1, 50.8) * mm, "end": v(190.5, 50.8) * mm});
            skLineSegment(sketch, "E2.4.1.3", {"start": v(165.1, 50.8) * mm, "end": v(165.1, 76.2) * mm});
            skLineSegment(sketch, "E2.4.2.0", {"start": v(190.5, 88.9) * mm, "end": v(190.5, 114.3) * mm});
            skLineSegment(sketch, "E2.4.2.1", {"start": v(165.1, 114.3) * mm, "end": v(190.5, 114.3) * mm});
            skLineSegment(sketch, "E2.4.2.2", {"start": v(165.1, 88.9) * mm, "end": v(190.5, 88.9) * mm});
            skLineSegment(sketch, "E2.4.2.3", {"start": v(165.1, 88.9) * mm, "end": v(165.1, 114.3) * mm});
            skLineSegment(sketch, "E2.4.3.0", {"start": v(190.5, 127) * mm, "end": v(190.5, 152.4) * mm});
            skLineSegment(sketch, "E2.4.3.1", {"start": v(165.1, 152.4) * mm, "end": v(190.5, 152.4) * mm});
            skLineSegment(sketch, "E2.4.3.2", {"start": v(165.1, 127) * mm, "end": v(190.5, 127) * mm});
            skLineSegment(sketch, "E2.4.3.3", {"start": v(165.1, 127) * mm, "end": v(165.1, 152.4) * mm});
            skLineSegment(sketch, "E2.4.4.0", {"start": v(190.5, 165.1) * mm, "end": v(190.5, 190.5) * mm});
            skLineSegment(sketch, "E2.4.4.1", {"start": v(165.1, 190.5) * mm, "end": v(190.5, 190.5) * mm});
            skLineSegment(sketch, "E2.4.4.2", {"start": v(165.1, 165.1) * mm, "end": v(190.5, 165.1) * mm});
            skLineSegment(sketch, "E2.4.4.3", {"start": v(165.1, 165.1) * mm, "end": v(165.1, 190.5) * mm});
            skLineSegment(sketch, "E2.4.5.0", {"start": v(190.5, 203.2) * mm, "end": v(190.5, 228.6) * mm});
            skLineSegment(sketch, "E2.4.5.1", {"start": v(165.1, 228.6) * mm, "end": v(190.5, 228.6) * mm});
            skLineSegment(sketch, "E2.4.5.2", {"start": v(165.1, 203.2) * mm, "end": v(190.5, 203.2) * mm});
            skLineSegment(sketch, "E2.4.5.3", {"start": v(165.1, 203.2) * mm, "end": v(165.1, 228.6) * mm});
            skLineSegment(sketch, "E2.4.6.0", {"start": v(190.5, 241.3) * mm, "end": v(190.5, 266.7) * mm});
            skLineSegment(sketch, "E2.4.6.1", {"start": v(165.1, 266.7) * mm, "end": v(190.5, 266.7) * mm});
            skLineSegment(sketch, "E2.4.6.2", {"start": v(165.1, 241.3) * mm, "end": v(190.5, 241.3) * mm});
            skLineSegment(sketch, "E2.4.6.3", {"start": v(165.1, 241.3) * mm, "end": v(165.1, 266.7) * mm});
            skLineSegment(sketch, "E2.4.7.0", {"start": v(190.5, 279.4) * mm, "end": v(190.5, 304.8) * mm});
            skLineSegment(sketch, "E2.4.7.1", {"start": v(165.1, 304.8) * mm, "end": v(190.5, 304.8) * mm});
            skLineSegment(sketch, "E2.4.7.2", {"start": v(165.1, 279.4) * mm, "end": v(190.5, 279.4) * mm});
            skLineSegment(sketch, "E2.4.7.3", {"start": v(165.1, 279.4) * mm, "end": v(165.1, 304.8) * mm});
            skLineSegment(sketch, "E2.4.8.0", {"start": v(190.5, 317.5) * mm, "end": v(190.5, 342.9) * mm});
            skLineSegment(sketch, "E2.4.8.1", {"start": v(165.1, 342.9) * mm, "end": v(190.5, 342.9) * mm});
            skLineSegment(sketch, "E2.4.8.2", {"start": v(165.1, 317.5) * mm, "end": v(190.5, 317.5) * mm});
            skLineSegment(sketch, "E2.4.8.3", {"start": v(165.1, 317.5) * mm, "end": v(165.1, 342.9) * mm});
            skLineSegment(sketch, "E2.4.9.0", {"start": v(190.5, 355.6) * mm, "end": v(190.5, 381) * mm});
            skLineSegment(sketch, "E2.4.9.1", {"start": v(165.1, 381) * mm, "end": v(190.5, 381) * mm});
            skLineSegment(sketch, "E2.4.9.2", {"start": v(165.1, 355.6) * mm, "end": v(190.5, 355.6) * mm});
            skLineSegment(sketch, "E2.4.9.3", {"start": v(165.1, 355.6) * mm, "end": v(165.1, 381) * mm});
            skLineSegment(sketch, "E2.4.10.0", {"start": v(190.5, 393.7) * mm, "end": v(190.5, 419.1) * mm});
            skLineSegment(sketch, "E2.4.10.1", {"start": v(165.1, 419.1) * mm, "end": v(190.5, 419.1) * mm});
            skLineSegment(sketch, "E2.4.10.2", {"start": v(165.1, 393.7) * mm, "end": v(190.5, 393.7) * mm});
            skLineSegment(sketch, "E2.4.10.3", {"start": v(165.1, 393.7) * mm, "end": v(165.1, 419.1) * mm});
            skLineSegment(sketch, "E2.4.11.0", {"start": v(190.5, 431.8) * mm, "end": v(190.5, 457.2) * mm});
            skLineSegment(sketch, "E2.4.11.1", {"start": v(165.1, 457.2) * mm, "end": v(190.5, 457.2) * mm});
            skLineSegment(sketch, "E2.4.11.2", {"start": v(165.1, 431.8) * mm, "end": v(190.5, 431.8) * mm});
            skLineSegment(sketch, "E2.4.11.3", {"start": v(165.1, 431.8) * mm, "end": v(165.1, 457.2) * mm});
            skLineSegment(sketch, "E2.4.12.0", {"start": v(190.5, 469.9) * mm, "end": v(190.5, 495.3) * mm});
            skLineSegment(sketch, "E2.4.12.1", {"start": v(165.1, 495.3) * mm, "end": v(190.5, 495.3) * mm});
            skLineSegment(sketch, "E2.4.12.2", {"start": v(165.1, 469.9) * mm, "end": v(190.5, 469.9) * mm});
            skLineSegment(sketch, "E2.4.12.3", {"start": v(165.1, 469.9) * mm, "end": v(165.1, 495.3) * mm});
            skLineSegment(sketch, "E2.4.13.0", {"start": v(190.5, 508) * mm, "end": v(190.5, 533.4) * mm});
            skLineSegment(sketch, "E2.4.13.1", {"start": v(165.1, 533.4) * mm, "end": v(190.5, 533.4) * mm});
            skLineSegment(sketch, "E2.4.13.2", {"start": v(165.1, 508) * mm, "end": v(190.5, 508) * mm});
            skLineSegment(sketch, "E2.4.13.3", {"start": v(165.1, 508) * mm, "end": v(165.1, 533.4) * mm});
            skLineSegment(sketch, "E2.4.14.0", {"start": v(190.5, 546.1) * mm, "end": v(190.5, 571.5) * mm});
            skLineSegment(sketch, "E2.4.14.1", {"start": v(165.1, 571.5) * mm, "end": v(190.5, 571.5) * mm});
            skLineSegment(sketch, "E2.4.14.2", {"start": v(165.1, 546.1) * mm, "end": v(190.5, 546.1) * mm});
            skLineSegment(sketch, "E2.4.14.3", {"start": v(165.1, 546.1) * mm, "end": v(165.1, 571.5) * mm});
            skLineSegment(sketch, "E2.4.15.0", {"start": v(190.5, 584.2) * mm, "end": v(190.5, 609.6) * mm});
            skLineSegment(sketch, "E2.4.15.1", {"start": v(165.1, 609.6) * mm, "end": v(190.5, 609.6) * mm});
            skLineSegment(sketch, "E2.4.15.2", {"start": v(165.1, 584.2) * mm, "end": v(190.5, 584.2) * mm});
            skLineSegment(sketch, "E2.4.15.3", {"start": v(165.1, 584.2) * mm, "end": v(165.1, 609.6) * mm});
            skLineSegment(sketch, "E2.4.16.0", {"start": v(190.5, 622.3) * mm, "end": v(190.5, 647.7) * mm});
            skLineSegment(sketch, "E2.4.16.1", {"start": v(165.1, 647.7) * mm, "end": v(190.5, 647.7) * mm});
            skLineSegment(sketch, "E2.4.16.2", {"start": v(165.1, 622.3) * mm, "end": v(190.5, 622.3) * mm});
            skLineSegment(sketch, "E2.4.16.3", {"start": v(165.1, 622.3) * mm, "end": v(165.1, 647.7) * mm});
            skLineSegment(sketch, "E2.4.17.0", {"start": v(190.5, 660.4) * mm, "end": v(190.5, 685.8) * mm});
            skLineSegment(sketch, "E2.4.17.1", {"start": v(165.1, 685.8) * mm, "end": v(190.5, 685.8) * mm});
            skLineSegment(sketch, "E2.4.17.2", {"start": v(165.1, 660.4) * mm, "end": v(190.5, 660.4) * mm});
            skLineSegment(sketch, "E2.4.17.3", {"start": v(165.1, 660.4) * mm, "end": v(165.1, 685.8) * mm});
            skLineSegment(sketch, "E2.4.18.0", {"start": v(190.5, 698.5) * mm, "end": v(190.5, 723.9) * mm});
            skLineSegment(sketch, "E2.4.18.1", {"start": v(165.1, 723.9) * mm, "end": v(190.5, 723.9) * mm});
            skLineSegment(sketch, "E2.4.18.2", {"start": v(165.1, 698.5) * mm, "end": v(190.5, 698.5) * mm});
            skLineSegment(sketch, "E2.4.18.3", {"start": v(165.1, 698.5) * mm, "end": v(165.1, 723.9) * mm});
            skLineSegment(sketch, "E2.4.19.0", {"start": v(190.5, 736.6) * mm, "end": v(190.5, 762) * mm});
            skLineSegment(sketch, "E2.4.19.1", {"start": v(165.1, 762) * mm, "end": v(190.5, 762) * mm});
            skLineSegment(sketch, "E2.4.19.2", {"start": v(165.1, 736.6) * mm, "end": v(190.5, 736.6) * mm});
            skLineSegment(sketch, "E2.4.19.3", {"start": v(165.1, 736.6) * mm, "end": v(165.1, 762) * mm});
            skLineSegment(sketch, "E2.5.0.0", {"start": v(228.6, 12.7) * mm, "end": v(228.6, 38.1) * mm});
            skLineSegment(sketch, "E2.5.0.1", {"start": v(203.2, 38.1) * mm, "end": v(228.6, 38.1) * mm});
            skLineSegment(sketch, "E2.5.0.2", {"start": v(203.2, 12.7) * mm, "end": v(228.6, 12.7) * mm});
            skLineSegment(sketch, "E2.5.0.3", {"start": v(203.2, 12.7) * mm, "end": v(203.2, 38.1) * mm});
            skLineSegment(sketch, "E2.5.1.0", {"start": v(228.6, 50.8) * mm, "end": v(228.6, 76.2) * mm});
            skLineSegment(sketch, "E2.5.1.1", {"start": v(203.2, 76.2) * mm, "end": v(228.6, 76.2) * mm});
            skLineSegment(sketch, "E2.5.1.2", {"start": v(203.2, 50.8) * mm, "end": v(228.6, 50.8) * mm});
            skLineSegment(sketch, "E2.5.1.3", {"start": v(203.2, 50.8) * mm, "end": v(203.2, 76.2) * mm});
            skLineSegment(sketch, "E2.5.2.0", {"start": v(228.6, 88.9) * mm, "end": v(228.6, 114.3) * mm});
            skLineSegment(sketch, "E2.5.2.1", {"start": v(203.2, 114.3) * mm, "end": v(228.6, 114.3) * mm});
            skLineSegment(sketch, "E2.5.2.2", {"start": v(203.2, 88.9) * mm, "end": v(228.6, 88.9) * mm});
            skLineSegment(sketch, "E2.5.2.3", {"start": v(203.2, 88.9) * mm, "end": v(203.2, 114.3) * mm});
            skLineSegment(sketch, "E2.5.3.0", {"start": v(228.6, 127) * mm, "end": v(228.6, 152.4) * mm});
            skLineSegment(sketch, "E2.5.3.1", {"start": v(203.2, 152.4) * mm, "end": v(228.6, 152.4) * mm});
            skLineSegment(sketch, "E2.5.3.2", {"start": v(203.2, 127) * mm, "end": v(228.6, 127) * mm});
            skLineSegment(sketch, "E2.5.3.3", {"start": v(203.2, 127) * mm, "end": v(203.2, 152.4) * mm});
            skLineSegment(sketch, "E2.5.4.0", {"start": v(228.6, 165.1) * mm, "end": v(228.6, 190.5) * mm});
            skLineSegment(sketch, "E2.5.4.1", {"start": v(203.2, 190.5) * mm, "end": v(228.6, 190.5) * mm});
            skLineSegment(sketch, "E2.5.4.2", {"start": v(203.2, 165.1) * mm, "end": v(228.6, 165.1) * mm});
            skLineSegment(sketch, "E2.5.4.3", {"start": v(203.2, 165.1) * mm, "end": v(203.2, 190.5) * mm});
            skLineSegment(sketch, "E2.5.5.0", {"start": v(228.6, 203.2) * mm, "end": v(228.6, 228.6) * mm});
            skLineSegment(sketch, "E2.5.5.1", {"start": v(203.2, 228.6) * mm, "end": v(228.6, 228.6) * mm});
            skLineSegment(sketch, "E2.5.5.2", {"start": v(203.2, 203.2) * mm, "end": v(228.6, 203.2) * mm});
            skLineSegment(sketch, "E2.5.5.3", {"start": v(203.2, 203.2) * mm, "end": v(203.2, 228.6) * mm});
            skLineSegment(sketch, "E2.5.6.0", {"start": v(228.6, 241.3) * mm, "end": v(228.6, 266.7) * mm});
            skLineSegment(sketch, "E2.5.6.1", {"start": v(203.2, 266.7) * mm, "end": v(228.6, 266.7) * mm});
            skLineSegment(sketch, "E2.5.6.2", {"start": v(203.2, 241.3) * mm, "end": v(228.6, 241.3) * mm});
            skLineSegment(sketch, "E2.5.6.3", {"start": v(203.2, 241.3) * mm, "end": v(203.2, 266.7) * mm});
            skLineSegment(sketch, "E2.5.7.0", {"start": v(228.6, 279.4) * mm, "end": v(228.6, 304.8) * mm});
            skLineSegment(sketch, "E2.5.7.1", {"start": v(203.2, 304.8) * mm, "end": v(228.6, 304.8) * mm});
            skLineSegment(sketch, "E2.5.7.2", {"start": v(203.2, 279.4) * mm, "end": v(228.6, 279.4) * mm});
            skLineSegment(sketch, "E2.5.7.3", {"start": v(203.2, 279.4) * mm, "end": v(203.2, 304.8) * mm});
            skLineSegment(sketch, "E2.5.8.0", {"start": v(228.6, 317.5) * mm, "end": v(228.6, 342.9) * mm});
            skLineSegment(sketch, "E2.5.8.1", {"start": v(203.2, 342.9) * mm, "end": v(228.6, 342.9) * mm});
            skLineSegment(sketch, "E2.5.8.2", {"start": v(203.2, 317.5) * mm, "end": v(228.6, 317.5) * mm});
            skLineSegment(sketch, "E2.5.8.3", {"start": v(203.2, 317.5) * mm, "end": v(203.2, 342.9) * mm});
            skLineSegment(sketch, "E2.5.9.0", {"start": v(228.6, 355.6) * mm, "end": v(228.6, 381) * mm});
            skLineSegment(sketch, "E2.5.9.1", {"start": v(203.2, 381) * mm, "end": v(228.6, 381) * mm});
            skLineSegment(sketch, "E2.5.9.2", {"start": v(203.2, 355.6) * mm, "end": v(228.6, 355.6) * mm});
            skLineSegment(sketch, "E2.5.9.3", {"start": v(203.2, 355.6) * mm, "end": v(203.2, 381) * mm});
            skLineSegment(sketch, "E2.5.10.0", {"start": v(228.6, 393.7) * mm, "end": v(228.6, 419.1) * mm});
            skLineSegment(sketch, "E2.5.10.1", {"start": v(203.2, 419.1) * mm, "end": v(228.6, 419.1) * mm});
            skLineSegment(sketch, "E2.5.10.2", {"start": v(203.2, 393.7) * mm, "end": v(228.6, 393.7) * mm});
            skLineSegment(sketch, "E2.5.10.3", {"start": v(203.2, 393.7) * mm, "end": v(203.2, 419.1) * mm});
            skLineSegment(sketch, "E2.5.11.0", {"start": v(228.6, 431.8) * mm, "end": v(228.6, 457.2) * mm});
            skLineSegment(sketch, "E2.5.11.1", {"start": v(203.2, 457.2) * mm, "end": v(228.6, 457.2) * mm});
            skLineSegment(sketch, "E2.5.11.2", {"start": v(203.2, 431.8) * mm, "end": v(228.6, 431.8) * mm});
            skLineSegment(sketch, "E2.5.11.3", {"start": v(203.2, 431.8) * mm, "end": v(203.2, 457.2) * mm});
            skLineSegment(sketch, "E2.5.12.0", {"start": v(228.6, 469.9) * mm, "end": v(228.6, 495.3) * mm});
            skLineSegment(sketch, "E2.5.12.1", {"start": v(203.2, 495.3) * mm, "end": v(228.6, 495.3) * mm});
            skLineSegment(sketch, "E2.5.12.2", {"start": v(203.2, 469.9) * mm, "end": v(228.6, 469.9) * mm});
            skLineSegment(sketch, "E2.5.12.3", {"start": v(203.2, 469.9) * mm, "end": v(203.2, 495.3) * mm});
            skLineSegment(sketch, "E2.5.13.0", {"start": v(228.6, 508) * mm, "end": v(228.6, 533.4) * mm});
            skLineSegment(sketch, "E2.5.13.1", {"start": v(203.2, 533.4) * mm, "end": v(228.6, 533.4) * mm});
            skLineSegment(sketch, "E2.5.13.2", {"start": v(203.2, 508) * mm, "end": v(228.6, 508) * mm});
            skLineSegment(sketch, "E2.5.13.3", {"start": v(203.2, 508) * mm, "end": v(203.2, 533.4) * mm});
            skLineSegment(sketch, "E2.5.14.0", {"start": v(228.6, 546.1) * mm, "end": v(228.6, 571.5) * mm});
            skLineSegment(sketch, "E2.5.14.1", {"start": v(203.2, 571.5) * mm, "end": v(228.6, 571.5) * mm});
            skLineSegment(sketch, "E2.5.14.2", {"start": v(203.2, 546.1) * mm, "end": v(228.6, 546.1) * mm});
            skLineSegment(sketch, "E2.5.14.3", {"start": v(203.2, 546.1) * mm, "end": v(203.2, 571.5) * mm});
            skLineSegment(sketch, "E2.5.15.0", {"start": v(228.6, 584.2) * mm, "end": v(228.6, 609.6) * mm});
            skLineSegment(sketch, "E2.5.15.1", {"start": v(203.2, 609.6) * mm, "end": v(228.6, 609.6) * mm});
            skLineSegment(sketch, "E2.5.15.2", {"start": v(203.2, 584.2) * mm, "end": v(228.6, 584.2) * mm});
            skLineSegment(sketch, "E2.5.15.3", {"start": v(203.2, 584.2) * mm, "end": v(203.2, 609.6) * mm});
            skLineSegment(sketch, "E2.5.16.0", {"start": v(228.6, 622.3) * mm, "end": v(228.6, 647.7) * mm});
            skLineSegment(sketch, "E2.5.16.1", {"start": v(203.2, 647.7) * mm, "end": v(228.6, 647.7) * mm});
            skLineSegment(sketch, "E2.5.16.2", {"start": v(203.2, 622.3) * mm, "end": v(228.6, 622.3) * mm});
            skLineSegment(sketch, "E2.5.16.3", {"start": v(203.2, 622.3) * mm, "end": v(203.2, 647.7) * mm});
            skLineSegment(sketch, "E2.5.17.0", {"start": v(228.6, 660.4) * mm, "end": v(228.6, 685.8) * mm});
            skLineSegment(sketch, "E2.5.17.1", {"start": v(203.2, 685.8) * mm, "end": v(228.6, 685.8) * mm});
            skLineSegment(sketch, "E2.5.17.2", {"start": v(203.2, 660.4) * mm, "end": v(228.6, 660.4) * mm});
            skLineSegment(sketch, "E2.5.17.3", {"start": v(203.2, 660.4) * mm, "end": v(203.2, 685.8) * mm});
            skLineSegment(sketch, "E2.5.18.0", {"start": v(228.6, 698.5) * mm, "end": v(228.6, 723.9) * mm});
            skLineSegment(sketch, "E2.5.18.1", {"start": v(203.2, 723.9) * mm, "end": v(228.6, 723.9) * mm});
            skLineSegment(sketch, "E2.5.18.2", {"start": v(203.2, 698.5) * mm, "end": v(228.6, 698.5) * mm});
            skLineSegment(sketch, "E2.5.18.3", {"start": v(203.2, 698.5) * mm, "end": v(203.2, 723.9) * mm});
            skLineSegment(sketch, "E2.5.19.0", {"start": v(228.6, 736.6) * mm, "end": v(228.6, 762) * mm});
            skLineSegment(sketch, "E2.5.19.1", {"start": v(203.2, 762) * mm, "end": v(228.6, 762) * mm});
            skLineSegment(sketch, "E2.5.19.2", {"start": v(203.2, 736.6) * mm, "end": v(228.6, 736.6) * mm});
            skLineSegment(sketch, "E2.5.19.3", {"start": v(203.2, 736.6) * mm, "end": v(203.2, 762) * mm});
            skLineSegment(sketch, "E2.6.0.0", {"start": v(266.7, 12.7) * mm, "end": v(266.7, 38.1) * mm});
            skLineSegment(sketch, "E2.6.0.1", {"start": v(241.3, 38.1) * mm, "end": v(266.7, 38.1) * mm});
            skLineSegment(sketch, "E2.6.0.2", {"start": v(241.3, 12.7) * mm, "end": v(266.7, 12.7) * mm});
            skLineSegment(sketch, "E2.6.0.3", {"start": v(241.3, 12.7) * mm, "end": v(241.3, 38.1) * mm});
            skLineSegment(sketch, "E2.6.1.0", {"start": v(266.7, 50.8) * mm, "end": v(266.7, 76.2) * mm});
            skLineSegment(sketch, "E2.6.1.1", {"start": v(241.3, 76.2) * mm, "end": v(266.7, 76.2) * mm});
            skLineSegment(sketch, "E2.6.1.2", {"start": v(241.3, 50.8) * mm, "end": v(266.7, 50.8) * mm});
            skLineSegment(sketch, "E2.6.1.3", {"start": v(241.3, 50.8) * mm, "end": v(241.3, 76.2) * mm});
            skLineSegment(sketch, "E2.6.2.0", {"start": v(266.7, 88.9) * mm, "end": v(266.7, 114.3) * mm});
            skLineSegment(sketch, "E2.6.2.1", {"start": v(241.3, 114.3) * mm, "end": v(266.7, 114.3) * mm});
            skLineSegment(sketch, "E2.6.2.2", {"start": v(241.3, 88.9) * mm, "end": v(266.7, 88.9) * mm});
            skLineSegment(sketch, "E2.6.2.3", {"start": v(241.3, 88.9) * mm, "end": v(241.3, 114.3) * mm});
            skLineSegment(sketch, "E2.6.3.0", {"start": v(266.7, 127) * mm, "end": v(266.7, 152.4) * mm});
            skLineSegment(sketch, "E2.6.3.1", {"start": v(241.3, 152.4) * mm, "end": v(266.7, 152.4) * mm});
            skLineSegment(sketch, "E2.6.3.2", {"start": v(241.3, 127) * mm, "end": v(266.7, 127) * mm});
            skLineSegment(sketch, "E2.6.3.3", {"start": v(241.3, 127) * mm, "end": v(241.3, 152.4) * mm});
            skLineSegment(sketch, "E2.6.4.0", {"start": v(266.7, 165.1) * mm, "end": v(266.7, 190.5) * mm});
            skLineSegment(sketch, "E2.6.4.1", {"start": v(241.3, 190.5) * mm, "end": v(266.7, 190.5) * mm});
            skLineSegment(sketch, "E2.6.4.2", {"start": v(241.3, 165.1) * mm, "end": v(266.7, 165.1) * mm});
            skLineSegment(sketch, "E2.6.4.3", {"start": v(241.3, 165.1) * mm, "end": v(241.3, 190.5) * mm});
            skLineSegment(sketch, "E2.6.5.0", {"start": v(266.7, 203.2) * mm, "end": v(266.7, 228.6) * mm});
            skLineSegment(sketch, "E2.6.5.1", {"start": v(241.3, 228.6) * mm, "end": v(266.7, 228.6) * mm});
            skLineSegment(sketch, "E2.6.5.2", {"start": v(241.3, 203.2) * mm, "end": v(266.7, 203.2) * mm});
            skLineSegment(sketch, "E2.6.5.3", {"start": v(241.3, 203.2) * mm, "end": v(241.3, 228.6) * mm});
            skLineSegment(sketch, "E2.6.6.0", {"start": v(266.7, 241.3) * mm, "end": v(266.7, 266.7) * mm});
            skLineSegment(sketch, "E2.6.6.1", {"start": v(241.3, 266.7) * mm, "end": v(266.7, 266.7) * mm});
            skLineSegment(sketch, "E2.6.6.2", {"start": v(241.3, 241.3) * mm, "end": v(266.7, 241.3) * mm});
            skLineSegment(sketch, "E2.6.6.3", {"start": v(241.3, 241.3) * mm, "end": v(241.3, 266.7) * mm});
            skLineSegment(sketch, "E2.6.7.0", {"start": v(266.7, 279.4) * mm, "end": v(266.7, 304.8) * mm});
            skLineSegment(sketch, "E2.6.7.1", {"start": v(241.3, 304.8) * mm, "end": v(266.7, 304.8) * mm});
            skLineSegment(sketch, "E2.6.7.2", {"start": v(241.3, 279.4) * mm, "end": v(266.7, 279.4) * mm});
            skLineSegment(sketch, "E2.6.7.3", {"start": v(241.3, 279.4) * mm, "end": v(241.3, 304.8) * mm});
            skLineSegment(sketch, "E2.6.8.0", {"start": v(266.7, 317.5) * mm, "end": v(266.7, 342.9) * mm});
            skLineSegment(sketch, "E2.6.8.1", {"start": v(241.3, 342.9) * mm, "end": v(266.7, 342.9) * mm});
            skLineSegment(sketch, "E2.6.8.2", {"start": v(241.3, 317.5) * mm, "end": v(266.7, 317.5) * mm});
            skLineSegment(sketch, "E2.6.8.3", {"start": v(241.3, 317.5) * mm, "end": v(241.3, 342.9) * mm});
            skLineSegment(sketch, "E2.6.9.0", {"start": v(266.7, 355.6) * mm, "end": v(266.7, 381) * mm});
            skLineSegment(sketch, "E2.6.9.1", {"start": v(241.3, 381) * mm, "end": v(266.7, 381) * mm});
            skLineSegment(sketch, "E2.6.9.2", {"start": v(241.3, 355.6) * mm, "end": v(266.7, 355.6) * mm});
            skLineSegment(sketch, "E2.6.9.3", {"start": v(241.3, 355.6) * mm, "end": v(241.3, 381) * mm});
            skLineSegment(sketch, "E2.6.10.0", {"start": v(266.7, 393.7) * mm, "end": v(266.7, 419.1) * mm});
            skLineSegment(sketch, "E2.6.10.1", {"start": v(241.3, 419.1) * mm, "end": v(266.7, 419.1) * mm});
            skLineSegment(sketch, "E2.6.10.2", {"start": v(241.3, 393.7) * mm, "end": v(266.7, 393.7) * mm});
            skLineSegment(sketch, "E2.6.10.3", {"start": v(241.3, 393.7) * mm, "end": v(241.3, 419.1) * mm});
            skLineSegment(sketch, "E2.6.11.0", {"start": v(266.7, 431.8) * mm, "end": v(266.7, 457.2) * mm});
            skLineSegment(sketch, "E2.6.11.1", {"start": v(241.3, 457.2) * mm, "end": v(266.7, 457.2) * mm});
            skLineSegment(sketch, "E2.6.11.2", {"start": v(241.3, 431.8) * mm, "end": v(266.7, 431.8) * mm});
            skLineSegment(sketch, "E2.6.11.3", {"start": v(241.3, 431.8) * mm, "end": v(241.3, 457.2) * mm});
            skLineSegment(sketch, "E2.6.12.0", {"start": v(266.7, 469.9) * mm, "end": v(266.7, 495.3) * mm});
            skLineSegment(sketch, "E2.6.12.1", {"start": v(241.3, 495.3) * mm, "end": v(266.7, 495.3) * mm});
            skLineSegment(sketch, "E2.6.12.2", {"start": v(241.3, 469.9) * mm, "end": v(266.7, 469.9) * mm});
            skLineSegment(sketch, "E2.6.12.3", {"start": v(241.3, 469.9) * mm, "end": v(241.3, 495.3) * mm});
            skLineSegment(sketch, "E2.6.13.0", {"start": v(266.7, 508) * mm, "end": v(266.7, 533.4) * mm});
            skLineSegment(sketch, "E2.6.13.1", {"start": v(241.3, 533.4) * mm, "end": v(266.7, 533.4) * mm});
            skLineSegment(sketch, "E2.6.13.2", {"start": v(241.3, 508) * mm, "end": v(266.7, 508) * mm});
            skLineSegment(sketch, "E2.6.13.3", {"start": v(241.3, 508) * mm, "end": v(241.3, 533.4) * mm});
            skLineSegment(sketch, "E2.6.14.0", {"start": v(266.7, 546.1) * mm, "end": v(266.7, 571.5) * mm});
            skLineSegment(sketch, "E2.6.14.1", {"start": v(241.3, 571.5) * mm, "end": v(266.7, 571.5) * mm});
            skLineSegment(sketch, "E2.6.14.2", {"start": v(241.3, 546.1) * mm, "end": v(266.7, 546.1) * mm});
            skLineSegment(sketch, "E2.6.14.3", {"start": v(241.3, 546.1) * mm, "end": v(241.3, 571.5) * mm});
            skLineSegment(sketch, "E2.6.15.0", {"start": v(266.7, 584.2) * mm, "end": v(266.7, 609.6) * mm});
            skLineSegment(sketch, "E2.6.15.1", {"start": v(241.3, 609.6) * mm, "end": v(266.7, 609.6) * mm});
            skLineSegment(sketch, "E2.6.15.2", {"start": v(241.3, 584.2) * mm, "end": v(266.7, 584.2) * mm});
            skLineSegment(sketch, "E2.6.15.3", {"start": v(241.3, 584.2) * mm, "end": v(241.3, 609.6) * mm});
            skLineSegment(sketch, "E2.6.16.0", {"start": v(266.7, 622.3) * mm, "end": v(266.7, 647.7) * mm});
            skLineSegment(sketch, "E2.6.16.1", {"start": v(241.3, 647.7) * mm, "end": v(266.7, 647.7) * mm});
            skLineSegment(sketch, "E2.6.16.2", {"start": v(241.3, 622.3) * mm, "end": v(266.7, 622.3) * mm});
            skLineSegment(sketch, "E2.6.16.3", {"start": v(241.3, 622.3) * mm, "end": v(241.3, 647.7) * mm});
            skLineSegment(sketch, "E2.6.17.0", {"start": v(266.7, 660.4) * mm, "end": v(266.7, 685.8) * mm});
            skLineSegment(sketch, "E2.6.17.1", {"start": v(241.3, 685.8) * mm, "end": v(266.7, 685.8) * mm});
            skLineSegment(sketch, "E2.6.17.2", {"start": v(241.3, 660.4) * mm, "end": v(266.7, 660.4) * mm});
            skLineSegment(sketch, "E2.6.17.3", {"start": v(241.3, 660.4) * mm, "end": v(241.3, 685.8) * mm});
            skLineSegment(sketch, "E2.6.18.0", {"start": v(266.7, 698.5) * mm, "end": v(266.7, 723.9) * mm});
            skLineSegment(sketch, "E2.6.18.1", {"start": v(241.3, 723.9) * mm, "end": v(266.7, 723.9) * mm});
            skLineSegment(sketch, "E2.6.18.2", {"start": v(241.3, 698.5) * mm, "end": v(266.7, 698.5) * mm});
            skLineSegment(sketch, "E2.6.18.3", {"start": v(241.3, 698.5) * mm, "end": v(241.3, 723.9) * mm});
            skLineSegment(sketch, "E2.6.19.0", {"start": v(266.7, 736.6) * mm, "end": v(266.7, 762) * mm});
            skLineSegment(sketch, "E2.6.19.1", {"start": v(241.3, 762) * mm, "end": v(266.7, 762) * mm});
            skLineSegment(sketch, "E2.6.19.2", {"start": v(241.3, 736.6) * mm, "end": v(266.7, 736.6) * mm});
            skLineSegment(sketch, "E2.6.19.3", {"start": v(241.3, 736.6) * mm, "end": v(241.3, 762) * mm});
            skLineSegment(sketch, "E2.7.0.0", {"start": v(304.8, 12.7) * mm, "end": v(304.8, 38.1) * mm});
            skLineSegment(sketch, "E2.7.0.1", {"start": v(279.4, 38.1) * mm, "end": v(304.8, 38.1) * mm});
            skLineSegment(sketch, "E2.7.0.2", {"start": v(279.4, 12.7) * mm, "end": v(304.8, 12.7) * mm});
            skLineSegment(sketch, "E2.7.0.3", {"start": v(279.4, 12.7) * mm, "end": v(279.4, 38.1) * mm});
            skLineSegment(sketch, "E2.7.1.0", {"start": v(304.8, 50.8) * mm, "end": v(304.8, 76.2) * mm});
            skLineSegment(sketch, "E2.7.1.1", {"start": v(279.4, 76.2) * mm, "end": v(304.8, 76.2) * mm});
            skLineSegment(sketch, "E2.7.1.2", {"start": v(279.4, 50.8) * mm, "end": v(304.8, 50.8) * mm});
            skLineSegment(sketch, "E2.7.1.3", {"start": v(279.4, 50.8) * mm, "end": v(279.4, 76.2) * mm});
            skLineSegment(sketch, "E2.7.2.0", {"start": v(304.8, 88.9) * mm, "end": v(304.8, 114.3) * mm});
            skLineSegment(sketch, "E2.7.2.1", {"start": v(279.4, 114.3) * mm, "end": v(304.8, 114.3) * mm});
            skLineSegment(sketch, "E2.7.2.2", {"start": v(279.4, 88.9) * mm, "end": v(304.8, 88.9) * mm});
            skLineSegment(sketch, "E2.7.2.3", {"start": v(279.4, 88.9) * mm, "end": v(279.4, 114.3) * mm});
            skLineSegment(sketch, "E2.7.3.0", {"start": v(304.8, 127) * mm, "end": v(304.8, 152.4) * mm});
            skLineSegment(sketch, "E2.7.3.1", {"start": v(279.4, 152.4) * mm, "end": v(304.8, 152.4) * mm});
            skLineSegment(sketch, "E2.7.3.2", {"start": v(279.4, 127) * mm, "end": v(304.8, 127) * mm});
            skLineSegment(sketch, "E2.7.3.3", {"start": v(279.4, 127) * mm, "end": v(279.4, 152.4) * mm});
            skLineSegment(sketch, "E2.7.4.0", {"start": v(304.8, 165.1) * mm, "end": v(304.8, 190.5) * mm});
            skLineSegment(sketch, "E2.7.4.1", {"start": v(279.4, 190.5) * mm, "end": v(304.8, 190.5) * mm});
            skLineSegment(sketch, "E2.7.4.2", {"start": v(279.4, 165.1) * mm, "end": v(304.8, 165.1) * mm});
            skLineSegment(sketch, "E2.7.4.3", {"start": v(279.4, 165.1) * mm, "end": v(279.4, 190.5) * mm});
            skLineSegment(sketch, "E2.7.5.0", {"start": v(304.8, 203.2) * mm, "end": v(304.8, 228.6) * mm});
            skLineSegment(sketch, "E2.7.5.1", {"start": v(279.4, 228.6) * mm, "end": v(304.8, 228.6) * mm});
            skLineSegment(sketch, "E2.7.5.2", {"start": v(279.4, 203.2) * mm, "end": v(304.8, 203.2) * mm});
            skLineSegment(sketch, "E2.7.5.3", {"start": v(279.4, 203.2) * mm, "end": v(279.4, 228.6) * mm});
            skLineSegment(sketch, "E2.7.6.0", {"start": v(304.8, 241.3) * mm, "end": v(304.8, 266.7) * mm});
            skLineSegment(sketch, "E2.7.6.1", {"start": v(279.4, 266.7) * mm, "end": v(304.8, 266.7) * mm});
            skLineSegment(sketch, "E2.7.6.2", {"start": v(279.4, 241.3) * mm, "end": v(304.8, 241.3) * mm});
            skLineSegment(sketch, "E2.7.6.3", {"start": v(279.4, 241.3) * mm, "end": v(279.4, 266.7) * mm});
            skLineSegment(sketch, "E2.7.7.0", {"start": v(304.8, 279.4) * mm, "end": v(304.8, 304.8) * mm});
            skLineSegment(sketch, "E2.7.7.1", {"start": v(279.4, 304.8) * mm, "end": v(304.8, 304.8) * mm});
            skLineSegment(sketch, "E2.7.7.2", {"start": v(279.4, 279.4) * mm, "end": v(304.8, 279.4) * mm});
            skLineSegment(sketch, "E2.7.7.3", {"start": v(279.4, 279.4) * mm, "end": v(279.4, 304.8) * mm});
            skLineSegment(sketch, "E2.7.8.0", {"start": v(304.8, 317.5) * mm, "end": v(304.8, 342.9) * mm});
            skLineSegment(sketch, "E2.7.8.1", {"start": v(279.4, 342.9) * mm, "end": v(304.8, 342.9) * mm});
            skLineSegment(sketch, "E2.7.8.2", {"start": v(279.4, 317.5) * mm, "end": v(304.8, 317.5) * mm});
            skLineSegment(sketch, "E2.7.8.3", {"start": v(279.4, 317.5) * mm, "end": v(279.4, 342.9) * mm});
            skLineSegment(sketch, "E2.7.9.0", {"start": v(304.8, 355.6) * mm, "end": v(304.8, 381) * mm});
            skLineSegment(sketch, "E2.7.9.1", {"start": v(279.4, 381) * mm, "end": v(304.8, 381) * mm});
            skLineSegment(sketch, "E2.7.9.2", {"start": v(279.4, 355.6) * mm, "end": v(304.8, 355.6) * mm});
            skLineSegment(sketch, "E2.7.9.3", {"start": v(279.4, 355.6) * mm, "end": v(279.4, 381) * mm});
            skLineSegment(sketch, "E2.7.10.0", {"start": v(304.8, 393.7) * mm, "end": v(304.8, 419.1) * mm});
            skLineSegment(sketch, "E2.7.10.1", {"start": v(279.4, 419.1) * mm, "end": v(304.8, 419.1) * mm});
            skLineSegment(sketch, "E2.7.10.2", {"start": v(279.4, 393.7) * mm, "end": v(304.8, 393.7) * mm});
            skLineSegment(sketch, "E2.7.10.3", {"start": v(279.4, 393.7) * mm, "end": v(279.4, 419.1) * mm});
            skLineSegment(sketch, "E2.7.11.0", {"start": v(304.8, 431.8) * mm, "end": v(304.8, 457.2) * mm});
            skLineSegment(sketch, "E2.7.11.1", {"start": v(279.4, 457.2) * mm, "end": v(304.8, 457.2) * mm});
            skLineSegment(sketch, "E2.7.11.2", {"start": v(279.4, 431.8) * mm, "end": v(304.8, 431.8) * mm});
            skLineSegment(sketch, "E2.7.11.3", {"start": v(279.4, 431.8) * mm, "end": v(279.4, 457.2) * mm});
            skLineSegment(sketch, "E2.7.12.0", {"start": v(304.8, 469.9) * mm, "end": v(304.8, 495.3) * mm});
            skLineSegment(sketch, "E2.7.12.1", {"start": v(279.4, 495.3) * mm, "end": v(304.8, 495.3) * mm});
            skLineSegment(sketch, "E2.7.12.2", {"start": v(279.4, 469.9) * mm, "end": v(304.8, 469.9) * mm});
            skLineSegment(sketch, "E2.7.12.3", {"start": v(279.4, 469.9) * mm, "end": v(279.4, 495.3) * mm});
            skLineSegment(sketch, "E2.7.13.0", {"start": v(304.8, 508) * mm, "end": v(304.8, 533.4) * mm});
            skLineSegment(sketch, "E2.7.13.1", {"start": v(279.4, 533.4) * mm, "end": v(304.8, 533.4) * mm});
            skLineSegment(sketch, "E2.7.13.2", {"start": v(279.4, 508) * mm, "end": v(304.8, 508) * mm});
            skLineSegment(sketch, "E2.7.13.3", {"start": v(279.4, 508) * mm, "end": v(279.4, 533.4) * mm});
            skLineSegment(sketch, "E2.7.14.0", {"start": v(304.8, 546.1) * mm, "end": v(304.8, 571.5) * mm});
            skLineSegment(sketch, "E2.7.14.1", {"start": v(279.4, 571.5) * mm, "end": v(304.8, 571.5) * mm});
            skLineSegment(sketch, "E2.7.14.2", {"start": v(279.4, 546.1) * mm, "end": v(304.8, 546.1) * mm});
            skLineSegment(sketch, "E2.7.14.3", {"start": v(279.4, 546.1) * mm, "end": v(279.4, 571.5) * mm});
            skLineSegment(sketch, "E2.7.15.0", {"start": v(304.8, 584.2) * mm, "end": v(304.8, 609.6) * mm});
            skLineSegment(sketch, "E2.7.15.1", {"start": v(279.4, 609.6) * mm, "end": v(304.8, 609.6) * mm});
            skLineSegment(sketch, "E2.7.15.2", {"start": v(279.4, 584.2) * mm, "end": v(304.8, 584.2) * mm});
            skLineSegment(sketch, "E2.7.15.3", {"start": v(279.4, 584.2) * mm, "end": v(279.4, 609.6) * mm});
            skLineSegment(sketch, "E2.7.16.0", {"start": v(304.8, 622.3) * mm, "end": v(304.8, 647.7) * mm});
            skLineSegment(sketch, "E2.7.16.1", {"start": v(279.4, 647.7) * mm, "end": v(304.8, 647.7) * mm});
            skLineSegment(sketch, "E2.7.16.2", {"start": v(279.4, 622.3) * mm, "end": v(304.8, 622.3) * mm});
            skLineSegment(sketch, "E2.7.16.3", {"start": v(279.4, 622.3) * mm, "end": v(279.4, 647.7) * mm});
            skLineSegment(sketch, "E2.7.17.0", {"start": v(304.8, 660.4) * mm, "end": v(304.8, 685.8) * mm});
            skLineSegment(sketch, "E2.7.17.1", {"start": v(279.4, 685.8) * mm, "end": v(304.8, 685.8) * mm});
            skLineSegment(sketch, "E2.7.17.2", {"start": v(279.4, 660.4) * mm, "end": v(304.8, 660.4) * mm});
            skLineSegment(sketch, "E2.7.17.3", {"start": v(279.4, 660.4) * mm, "end": v(279.4, 685.8) * mm});
            skLineSegment(sketch, "E2.7.18.0", {"start": v(304.8, 698.5) * mm, "end": v(304.8, 723.9) * mm});
            skLineSegment(sketch, "E2.7.18.1", {"start": v(279.4, 723.9) * mm, "end": v(304.8, 723.9) * mm});
            skLineSegment(sketch, "E2.7.18.2", {"start": v(279.4, 698.5) * mm, "end": v(304.8, 698.5) * mm});
            skLineSegment(sketch, "E2.7.18.3", {"start": v(279.4, 698.5) * mm, "end": v(279.4, 723.9) * mm});
            skLineSegment(sketch, "E2.7.19.0", {"start": v(304.8, 736.6) * mm, "end": v(304.8, 762) * mm});
            skLineSegment(sketch, "E2.7.19.1", {"start": v(279.4, 762) * mm, "end": v(304.8, 762) * mm});
            skLineSegment(sketch, "E2.7.19.2", {"start": v(279.4, 736.6) * mm, "end": v(304.8, 736.6) * mm});
            skLineSegment(sketch, "E2.7.19.3", {"start": v(279.4, 736.6) * mm, "end": v(279.4, 762) * mm});
            skLineSegment(sketch, "E2.8.0.0", {"start": v(342.9, 12.7) * mm, "end": v(342.9, 38.1) * mm});
            skLineSegment(sketch, "E2.8.0.1", {"start": v(317.5, 38.1) * mm, "end": v(342.9, 38.1) * mm});
            skLineSegment(sketch, "E2.8.0.2", {"start": v(317.5, 12.7) * mm, "end": v(342.9, 12.7) * mm});
            skLineSegment(sketch, "E2.8.0.3", {"start": v(317.5, 12.7) * mm, "end": v(317.5, 38.1) * mm});
            skLineSegment(sketch, "E2.8.1.0", {"start": v(342.9, 50.8) * mm, "end": v(342.9, 76.2) * mm});
            skLineSegment(sketch, "E2.8.1.1", {"start": v(317.5, 76.2) * mm, "end": v(342.9, 76.2) * mm});
            skLineSegment(sketch, "E2.8.1.2", {"start": v(317.5, 50.8) * mm, "end": v(342.9, 50.8) * mm});
            skLineSegment(sketch, "E2.8.1.3", {"start": v(317.5, 50.8) * mm, "end": v(317.5, 76.2) * mm});
            skLineSegment(sketch, "E2.8.2.0", {"start": v(342.9, 88.9) * mm, "end": v(342.9, 114.3) * mm});
            skLineSegment(sketch, "E2.8.2.1", {"start": v(317.5, 114.3) * mm, "end": v(342.9, 114.3) * mm});
            skLineSegment(sketch, "E2.8.2.2", {"start": v(317.5, 88.9) * mm, "end": v(342.9, 88.9) * mm});
            skLineSegment(sketch, "E2.8.2.3", {"start": v(317.5, 88.9) * mm, "end": v(317.5, 114.3) * mm});
            skLineSegment(sketch, "E2.8.3.0", {"start": v(342.9, 127) * mm, "end": v(342.9, 152.4) * mm});
            skLineSegment(sketch, "E2.8.3.1", {"start": v(317.5, 152.4) * mm, "end": v(342.9, 152.4) * mm});
            skLineSegment(sketch, "E2.8.3.2", {"start": v(317.5, 127) * mm, "end": v(342.9, 127) * mm});
            skLineSegment(sketch, "E2.8.3.3", {"start": v(317.5, 127) * mm, "end": v(317.5, 152.4) * mm});
            skLineSegment(sketch, "E2.8.4.0", {"start": v(342.9, 165.1) * mm, "end": v(342.9, 190.5) * mm});
            skLineSegment(sketch, "E2.8.4.1", {"start": v(317.5, 190.5) * mm, "end": v(342.9, 190.5) * mm});
            skLineSegment(sketch, "E2.8.4.2", {"start": v(317.5, 165.1) * mm, "end": v(342.9, 165.1) * mm});
            skLineSegment(sketch, "E2.8.4.3", {"start": v(317.5, 165.1) * mm, "end": v(317.5, 190.5) * mm});
            skLineSegment(sketch, "E2.8.5.0", {"start": v(342.9, 203.2) * mm, "end": v(342.9, 228.6) * mm});
            skLineSegment(sketch, "E2.8.5.1", {"start": v(317.5, 228.6) * mm, "end": v(342.9, 228.6) * mm});
            skLineSegment(sketch, "E2.8.5.2", {"start": v(317.5, 203.2) * mm, "end": v(342.9, 203.2) * mm});
            skLineSegment(sketch, "E2.8.5.3", {"start": v(317.5, 203.2) * mm, "end": v(317.5, 228.6) * mm});
            skLineSegment(sketch, "E2.8.6.0", {"start": v(342.9, 241.3) * mm, "end": v(342.9, 266.7) * mm});
            skLineSegment(sketch, "E2.8.6.1", {"start": v(317.5, 266.7) * mm, "end": v(342.9, 266.7) * mm});
            skLineSegment(sketch, "E2.8.6.2", {"start": v(317.5, 241.3) * mm, "end": v(342.9, 241.3) * mm});
            skLineSegment(sketch, "E2.8.6.3", {"start": v(317.5, 241.3) * mm, "end": v(317.5, 266.7) * mm});
            skLineSegment(sketch, "E2.8.7.0", {"start": v(342.9, 279.4) * mm, "end": v(342.9, 304.8) * mm});
            skLineSegment(sketch, "E2.8.7.1", {"start": v(317.5, 304.8) * mm, "end": v(342.9, 304.8) * mm});
            skLineSegment(sketch, "E2.8.7.2", {"start": v(317.5, 279.4) * mm, "end": v(342.9, 279.4) * mm});
            skLineSegment(sketch, "E2.8.7.3", {"start": v(317.5, 279.4) * mm, "end": v(317.5, 304.8) * mm});
            skLineSegment(sketch, "E2.8.8.0", {"start": v(342.9, 317.5) * mm, "end": v(342.9, 342.9) * mm});
            skLineSegment(sketch, "E2.8.8.1", {"start": v(317.5, 342.9) * mm, "end": v(342.9, 342.9) * mm});
            skLineSegment(sketch, "E2.8.8.2", {"start": v(317.5, 317.5) * mm, "end": v(342.9, 317.5) * mm});
            skLineSegment(sketch, "E2.8.8.3", {"start": v(317.5, 317.5) * mm, "end": v(317.5, 342.9) * mm});
            skLineSegment(sketch, "E2.8.9.0", {"start": v(342.9, 355.6) * mm, "end": v(342.9, 381) * mm});
            skLineSegment(sketch, "E2.8.9.1", {"start": v(317.5, 381) * mm, "end": v(342.9, 381) * mm});
            skLineSegment(sketch, "E2.8.9.2", {"start": v(317.5, 355.6) * mm, "end": v(342.9, 355.6) * mm});
            skLineSegment(sketch, "E2.8.9.3", {"start": v(317.5, 355.6) * mm, "end": v(317.5, 381) * mm});
            skLineSegment(sketch, "E2.8.10.0", {"start": v(342.9, 393.7) * mm, "end": v(342.9, 419.1) * mm});
            skLineSegment(sketch, "E2.8.10.1", {"start": v(317.5, 419.1) * mm, "end": v(342.9, 419.1) * mm});
            skLineSegment(sketch, "E2.8.10.2", {"start": v(317.5, 393.7) * mm, "end": v(342.9, 393.7) * mm});
            skLineSegment(sketch, "E2.8.10.3", {"start": v(317.5, 393.7) * mm, "end": v(317.5, 419.1) * mm});
            skLineSegment(sketch, "E2.8.11.0", {"start": v(342.9, 431.8) * mm, "end": v(342.9, 457.2) * mm});
            skLineSegment(sketch, "E2.8.11.1", {"start": v(317.5, 457.2) * mm, "end": v(342.9, 457.2) * mm});
            skLineSegment(sketch, "E2.8.11.2", {"start": v(317.5, 431.8) * mm, "end": v(342.9, 431.8) * mm});
            skLineSegment(sketch, "E2.8.11.3", {"start": v(317.5, 431.8) * mm, "end": v(317.5, 457.2) * mm});
            skLineSegment(sketch, "E2.8.12.0", {"start": v(342.9, 469.9) * mm, "end": v(342.9, 495.3) * mm});
            skLineSegment(sketch, "E2.8.12.1", {"start": v(317.5, 495.3) * mm, "end": v(342.9, 495.3) * mm});
            skLineSegment(sketch, "E2.8.12.2", {"start": v(317.5, 469.9) * mm, "end": v(342.9, 469.9) * mm});
            skLineSegment(sketch, "E2.8.12.3", {"start": v(317.5, 469.9) * mm, "end": v(317.5, 495.3) * mm});
            skLineSegment(sketch, "E2.8.13.0", {"start": v(342.9, 508) * mm, "end": v(342.9, 533.4) * mm});
            skLineSegment(sketch, "E2.8.13.1", {"start": v(317.5, 533.4) * mm, "end": v(342.9, 533.4) * mm});
            skLineSegment(sketch, "E2.8.13.2", {"start": v(317.5, 508) * mm, "end": v(342.9, 508) * mm});
            skLineSegment(sketch, "E2.8.13.3", {"start": v(317.5, 508) * mm, "end": v(317.5, 533.4) * mm});
            skLineSegment(sketch, "E2.8.14.0", {"start": v(342.9, 546.1) * mm, "end": v(342.9, 571.5) * mm});
            skLineSegment(sketch, "E2.8.14.1", {"start": v(317.5, 571.5) * mm, "end": v(342.9, 571.5) * mm});
            skLineSegment(sketch, "E2.8.14.2", {"start": v(317.5, 546.1) * mm, "end": v(342.9, 546.1) * mm});
            skLineSegment(sketch, "E2.8.14.3", {"start": v(317.5, 546.1) * mm, "end": v(317.5, 571.5) * mm});
            skLineSegment(sketch, "E2.8.15.0", {"start": v(342.9, 584.2) * mm, "end": v(342.9, 609.6) * mm});
            skLineSegment(sketch, "E2.8.15.1", {"start": v(317.5, 609.6) * mm, "end": v(342.9, 609.6) * mm});
            skLineSegment(sketch, "E2.8.15.2", {"start": v(317.5, 584.2) * mm, "end": v(342.9, 584.2) * mm});
            skLineSegment(sketch, "E2.8.15.3", {"start": v(317.5, 584.2) * mm, "end": v(317.5, 609.6) * mm});
            skLineSegment(sketch, "E2.8.16.0", {"start": v(342.9, 622.3) * mm, "end": v(342.9, 647.7) * mm});
            skLineSegment(sketch, "E2.8.16.1", {"start": v(317.5, 647.7) * mm, "end": v(342.9, 647.7) * mm});
            skLineSegment(sketch, "E2.8.16.2", {"start": v(317.5, 622.3) * mm, "end": v(342.9, 622.3) * mm});
            skLineSegment(sketch, "E2.8.16.3", {"start": v(317.5, 622.3) * mm, "end": v(317.5, 647.7) * mm});
            skLineSegment(sketch, "E2.8.17.0", {"start": v(342.9, 660.4) * mm, "end": v(342.9, 685.8) * mm});
            skLineSegment(sketch, "E2.8.17.1", {"start": v(317.5, 685.8) * mm, "end": v(342.9, 685.8) * mm});
            skLineSegment(sketch, "E2.8.17.2", {"start": v(317.5, 660.4) * mm, "end": v(342.9, 660.4) * mm});
            skLineSegment(sketch, "E2.8.17.3", {"start": v(317.5, 660.4) * mm, "end": v(317.5, 685.8) * mm});
            skLineSegment(sketch, "E2.8.18.0", {"start": v(342.9, 698.5) * mm, "end": v(342.9, 723.9) * mm});
            skLineSegment(sketch, "E2.8.18.1", {"start": v(317.5, 723.9) * mm, "end": v(342.9, 723.9) * mm});
            skLineSegment(sketch, "E2.8.18.2", {"start": v(317.5, 698.5) * mm, "end": v(342.9, 698.5) * mm});
            skLineSegment(sketch, "E2.8.18.3", {"start": v(317.5, 698.5) * mm, "end": v(317.5, 723.9) * mm});
            skLineSegment(sketch, "E2.8.19.0", {"start": v(342.9, 736.6) * mm, "end": v(342.9, 762) * mm});
            skLineSegment(sketch, "E2.8.19.1", {"start": v(317.5, 762) * mm, "end": v(342.9, 762) * mm});
            skLineSegment(sketch, "E2.8.19.2", {"start": v(317.5, 736.6) * mm, "end": v(342.9, 736.6) * mm});
            skLineSegment(sketch, "E2.8.19.3", {"start": v(317.5, 736.6) * mm, "end": v(317.5, 762) * mm});
            skLineSegment(sketch, "E2.9.0.0", {"start": v(381, 12.7) * mm, "end": v(381, 38.1) * mm});
            skLineSegment(sketch, "E2.9.0.1", {"start": v(355.6, 38.1) * mm, "end": v(381, 38.1) * mm});
            skLineSegment(sketch, "E2.9.0.2", {"start": v(355.6, 12.7) * mm, "end": v(381, 12.7) * mm});
            skLineSegment(sketch, "E2.9.0.3", {"start": v(355.6, 12.7) * mm, "end": v(355.6, 38.1) * mm});
            skLineSegment(sketch, "E2.9.1.0", {"start": v(381, 50.8) * mm, "end": v(381, 76.2) * mm});
            skLineSegment(sketch, "E2.9.1.1", {"start": v(355.6, 76.2) * mm, "end": v(381, 76.2) * mm});
            skLineSegment(sketch, "E2.9.1.2", {"start": v(355.6, 50.8) * mm, "end": v(381, 50.8) * mm});
            skLineSegment(sketch, "E2.9.1.3", {"start": v(355.6, 50.8) * mm, "end": v(355.6, 76.2) * mm});
            skLineSegment(sketch, "E2.9.2.0", {"start": v(381, 88.9) * mm, "end": v(381, 114.3) * mm});
            skLineSegment(sketch, "E2.9.2.1", {"start": v(355.6, 114.3) * mm, "end": v(381, 114.3) * mm});
            skLineSegment(sketch, "E2.9.2.2", {"start": v(355.6, 88.9) * mm, "end": v(381, 88.9) * mm});
            skLineSegment(sketch, "E2.9.2.3", {"start": v(355.6, 88.9) * mm, "end": v(355.6, 114.3) * mm});
            skLineSegment(sketch, "E2.9.3.0", {"start": v(381, 127) * mm, "end": v(381, 152.4) * mm});
            skLineSegment(sketch, "E2.9.3.1", {"start": v(355.6, 152.4) * mm, "end": v(381, 152.4) * mm});
            skLineSegment(sketch, "E2.9.3.2", {"start": v(355.6, 127) * mm, "end": v(381, 127) * mm});
            skLineSegment(sketch, "E2.9.3.3", {"start": v(355.6, 127) * mm, "end": v(355.6, 152.4) * mm});
            skLineSegment(sketch, "E2.9.4.0", {"start": v(381, 165.1) * mm, "end": v(381, 190.5) * mm});
            skLineSegment(sketch, "E2.9.4.1", {"start": v(355.6, 190.5) * mm, "end": v(381, 190.5) * mm});
            skLineSegment(sketch, "E2.9.4.2", {"start": v(355.6, 165.1) * mm, "end": v(381, 165.1) * mm});
            skLineSegment(sketch, "E2.9.4.3", {"start": v(355.6, 165.1) * mm, "end": v(355.6, 190.5) * mm});
            skLineSegment(sketch, "E2.9.5.0", {"start": v(381, 203.2) * mm, "end": v(381, 228.6) * mm});
            skLineSegment(sketch, "E2.9.5.1", {"start": v(355.6, 228.6) * mm, "end": v(381, 228.6) * mm});
            skLineSegment(sketch, "E2.9.5.2", {"start": v(355.6, 203.2) * mm, "end": v(381, 203.2) * mm});
            skLineSegment(sketch, "E2.9.5.3", {"start": v(355.6, 203.2) * mm, "end": v(355.6, 228.6) * mm});
            skLineSegment(sketch, "E2.9.6.0", {"start": v(381, 241.3) * mm, "end": v(381, 266.7) * mm});
            skLineSegment(sketch, "E2.9.6.1", {"start": v(355.6, 266.7) * mm, "end": v(381, 266.7) * mm});
            skLineSegment(sketch, "E2.9.6.2", {"start": v(355.6, 241.3) * mm, "end": v(381, 241.3) * mm});
            skLineSegment(sketch, "E2.9.6.3", {"start": v(355.6, 241.3) * mm, "end": v(355.6, 266.7) * mm});
            skLineSegment(sketch, "E2.9.7.0", {"start": v(381, 279.4) * mm, "end": v(381, 304.8) * mm});
            skLineSegment(sketch, "E2.9.7.1", {"start": v(355.6, 304.8) * mm, "end": v(381, 304.8) * mm});
            skLineSegment(sketch, "E2.9.7.2", {"start": v(355.6, 279.4) * mm, "end": v(381, 279.4) * mm});
            skLineSegment(sketch, "E2.9.7.3", {"start": v(355.6, 279.4) * mm, "end": v(355.6, 304.8) * mm});
            skLineSegment(sketch, "E2.9.8.0", {"start": v(381, 317.5) * mm, "end": v(381, 342.9) * mm});
            skLineSegment(sketch, "E2.9.8.1", {"start": v(355.6, 342.9) * mm, "end": v(381, 342.9) * mm});
            skLineSegment(sketch, "E2.9.8.2", {"start": v(355.6, 317.5) * mm, "end": v(381, 317.5) * mm});
            skLineSegment(sketch, "E2.9.8.3", {"start": v(355.6, 317.5) * mm, "end": v(355.6, 342.9) * mm});
            skLineSegment(sketch, "E2.9.9.0", {"start": v(381, 355.6) * mm, "end": v(381, 381) * mm});
            skLineSegment(sketch, "E2.9.9.1", {"start": v(355.6, 381) * mm, "end": v(381, 381) * mm});
            skLineSegment(sketch, "E2.9.9.2", {"start": v(355.6, 355.6) * mm, "end": v(381, 355.6) * mm});
            skLineSegment(sketch, "E2.9.9.3", {"start": v(355.6, 355.6) * mm, "end": v(355.6, 381) * mm});
            skLineSegment(sketch, "E2.9.10.0", {"start": v(381, 393.7) * mm, "end": v(381, 419.1) * mm});
            skLineSegment(sketch, "E2.9.10.1", {"start": v(355.6, 419.1) * mm, "end": v(381, 419.1) * mm});
            skLineSegment(sketch, "E2.9.10.2", {"start": v(355.6, 393.7) * mm, "end": v(381, 393.7) * mm});
            skLineSegment(sketch, "E2.9.10.3", {"start": v(355.6, 393.7) * mm, "end": v(355.6, 419.1) * mm});
            skLineSegment(sketch, "E2.9.11.0", {"start": v(381, 431.8) * mm, "end": v(381, 457.2) * mm});
            skLineSegment(sketch, "E2.9.11.1", {"start": v(355.6, 457.2) * mm, "end": v(381, 457.2) * mm});
            skLineSegment(sketch, "E2.9.11.2", {"start": v(355.6, 431.8) * mm, "end": v(381, 431.8) * mm});
            skLineSegment(sketch, "E2.9.11.3", {"start": v(355.6, 431.8) * mm, "end": v(355.6, 457.2) * mm});
            skLineSegment(sketch, "E2.9.12.0", {"start": v(381, 469.9) * mm, "end": v(381, 495.3) * mm});
            skLineSegment(sketch, "E2.9.12.1", {"start": v(355.6, 495.3) * mm, "end": v(381, 495.3) * mm});
            skLineSegment(sketch, "E2.9.12.2", {"start": v(355.6, 469.9) * mm, "end": v(381, 469.9) * mm});
            skLineSegment(sketch, "E2.9.12.3", {"start": v(355.6, 469.9) * mm, "end": v(355.6, 495.3) * mm});
            skLineSegment(sketch, "E2.9.13.0", {"start": v(381, 508) * mm, "end": v(381, 533.4) * mm});
            skLineSegment(sketch, "E2.9.13.1", {"start": v(355.6, 533.4) * mm, "end": v(381, 533.4) * mm});
            skLineSegment(sketch, "E2.9.13.2", {"start": v(355.6, 508) * mm, "end": v(381, 508) * mm});
            skLineSegment(sketch, "E2.9.13.3", {"start": v(355.6, 508) * mm, "end": v(355.6, 533.4) * mm});
            skLineSegment(sketch, "E2.9.14.0", {"start": v(381, 546.1) * mm, "end": v(381, 571.5) * mm});
            skLineSegment(sketch, "E2.9.14.1", {"start": v(355.6, 571.5) * mm, "end": v(381, 571.5) * mm});
            skLineSegment(sketch, "E2.9.14.2", {"start": v(355.6, 546.1) * mm, "end": v(381, 546.1) * mm});
            skLineSegment(sketch, "E2.9.14.3", {"start": v(355.6, 546.1) * mm, "end": v(355.6, 571.5) * mm});
            skLineSegment(sketch, "E2.9.15.0", {"start": v(381, 584.2) * mm, "end": v(381, 609.6) * mm});
            skLineSegment(sketch, "E2.9.15.1", {"start": v(355.6, 609.6) * mm, "end": v(381, 609.6) * mm});
            skLineSegment(sketch, "E2.9.15.2", {"start": v(355.6, 584.2) * mm, "end": v(381, 584.2) * mm});
            skLineSegment(sketch, "E2.9.15.3", {"start": v(355.6, 584.2) * mm, "end": v(355.6, 609.6) * mm});
            skLineSegment(sketch, "E2.9.16.0", {"start": v(381, 622.3) * mm, "end": v(381, 647.7) * mm});
            skLineSegment(sketch, "E2.9.16.1", {"start": v(355.6, 647.7) * mm, "end": v(381, 647.7) * mm});
            skLineSegment(sketch, "E2.9.16.2", {"start": v(355.6, 622.3) * mm, "end": v(381, 622.3) * mm});
            skLineSegment(sketch, "E2.9.16.3", {"start": v(355.6, 622.3) * mm, "end": v(355.6, 647.7) * mm});
            skLineSegment(sketch, "E2.9.17.0", {"start": v(381, 660.4) * mm, "end": v(381, 685.8) * mm});
            skLineSegment(sketch, "E2.9.17.1", {"start": v(355.6, 685.8) * mm, "end": v(381, 685.8) * mm});
            skLineSegment(sketch, "E2.9.17.2", {"start": v(355.6, 660.4) * mm, "end": v(381, 660.4) * mm});
            skLineSegment(sketch, "E2.9.17.3", {"start": v(355.6, 660.4) * mm, "end": v(355.6, 685.8) * mm});
            skLineSegment(sketch, "E2.9.18.0", {"start": v(381, 698.5) * mm, "end": v(381, 723.9) * mm});
            skLineSegment(sketch, "E2.9.18.1", {"start": v(355.6, 723.9) * mm, "end": v(381, 723.9) * mm});
            skLineSegment(sketch, "E2.9.18.2", {"start": v(355.6, 698.5) * mm, "end": v(381, 698.5) * mm});
            skLineSegment(sketch, "E2.9.18.3", {"start": v(355.6, 698.5) * mm, "end": v(355.6, 723.9) * mm});
            skLineSegment(sketch, "E2.9.19.0", {"start": v(381, 736.6) * mm, "end": v(381, 762) * mm});
            skLineSegment(sketch, "E2.9.19.1", {"start": v(355.6, 762) * mm, "end": v(381, 762) * mm});
            skLineSegment(sketch, "E2.9.19.2", {"start": v(355.6, 736.6) * mm, "end": v(381, 736.6) * mm});
            skLineSegment(sketch, "E2.9.19.3", {"start": v(355.6, 736.6) * mm, "end": v(355.6, 762) * mm});
            skLineSegment(sketch, "E2.10.0.0", {"start": v(419.1, 12.7) * mm, "end": v(419.1, 38.1) * mm});
            skLineSegment(sketch, "E2.10.0.1", {"start": v(393.7, 38.1) * mm, "end": v(419.1, 38.1) * mm});
            skLineSegment(sketch, "E2.10.0.2", {"start": v(393.7, 12.7) * mm, "end": v(419.1, 12.7) * mm});
            skLineSegment(sketch, "E2.10.0.3", {"start": v(393.7, 12.7) * mm, "end": v(393.7, 38.1) * mm});
            skLineSegment(sketch, "E2.10.1.0", {"start": v(419.1, 50.8) * mm, "end": v(419.1, 76.2) * mm});
            skLineSegment(sketch, "E2.10.1.1", {"start": v(393.7, 76.2) * mm, "end": v(419.1, 76.2) * mm});
            skLineSegment(sketch, "E2.10.1.2", {"start": v(393.7, 50.8) * mm, "end": v(419.1, 50.8) * mm});
            skLineSegment(sketch, "E2.10.1.3", {"start": v(393.7, 50.8) * mm, "end": v(393.7, 76.2) * mm});
            skLineSegment(sketch, "E2.10.2.0", {"start": v(419.1, 88.9) * mm, "end": v(419.1, 114.3) * mm});
            skLineSegment(sketch, "E2.10.2.1", {"start": v(393.7, 114.3) * mm, "end": v(419.1, 114.3) * mm});
            skLineSegment(sketch, "E2.10.2.2", {"start": v(393.7, 88.9) * mm, "end": v(419.1, 88.9) * mm});
            skLineSegment(sketch, "E2.10.2.3", {"start": v(393.7, 88.9) * mm, "end": v(393.7, 114.3) * mm});
            skLineSegment(sketch, "E2.10.3.0", {"start": v(419.1, 127) * mm, "end": v(419.1, 152.4) * mm});
            skLineSegment(sketch, "E2.10.3.1", {"start": v(393.7, 152.4) * mm, "end": v(419.1, 152.4) * mm});
            skLineSegment(sketch, "E2.10.3.2", {"start": v(393.7, 127) * mm, "end": v(419.1, 127) * mm});
            skLineSegment(sketch, "E2.10.3.3", {"start": v(393.7, 127) * mm, "end": v(393.7, 152.4) * mm});
            skLineSegment(sketch, "E2.10.4.0", {"start": v(419.1, 165.1) * mm, "end": v(419.1, 190.5) * mm});
            skLineSegment(sketch, "E2.10.4.1", {"start": v(393.7, 190.5) * mm, "end": v(419.1, 190.5) * mm});
            skLineSegment(sketch, "E2.10.4.2", {"start": v(393.7, 165.1) * mm, "end": v(419.1, 165.1) * mm});
            skLineSegment(sketch, "E2.10.4.3", {"start": v(393.7, 165.1) * mm, "end": v(393.7, 190.5) * mm});
            skLineSegment(sketch, "E2.10.5.0", {"start": v(419.1, 203.2) * mm, "end": v(419.1, 228.6) * mm});
            skLineSegment(sketch, "E2.10.5.1", {"start": v(393.7, 228.6) * mm, "end": v(419.1, 228.6) * mm});
            skLineSegment(sketch, "E2.10.5.2", {"start": v(393.7, 203.2) * mm, "end": v(419.1, 203.2) * mm});
            skLineSegment(sketch, "E2.10.5.3", {"start": v(393.7, 203.2) * mm, "end": v(393.7, 228.6) * mm});
            skLineSegment(sketch, "E2.10.6.0", {"start": v(419.1, 241.3) * mm, "end": v(419.1, 266.7) * mm});
            skLineSegment(sketch, "E2.10.6.1", {"start": v(393.7, 266.7) * mm, "end": v(419.1, 266.7) * mm});
            skLineSegment(sketch, "E2.10.6.2", {"start": v(393.7, 241.3) * mm, "end": v(419.1, 241.3) * mm});
            skLineSegment(sketch, "E2.10.6.3", {"start": v(393.7, 241.3) * mm, "end": v(393.7, 266.7) * mm});
            skLineSegment(sketch, "E2.10.7.0", {"start": v(419.1, 279.4) * mm, "end": v(419.1, 304.8) * mm});
            skLineSegment(sketch, "E2.10.7.1", {"start": v(393.7, 304.8) * mm, "end": v(419.1, 304.8) * mm});
            skLineSegment(sketch, "E2.10.7.2", {"start": v(393.7, 279.4) * mm, "end": v(419.1, 279.4) * mm});
            skLineSegment(sketch, "E2.10.7.3", {"start": v(393.7, 279.4) * mm, "end": v(393.7, 304.8) * mm});
            skLineSegment(sketch, "E2.10.8.0", {"start": v(419.1, 317.5) * mm, "end": v(419.1, 342.9) * mm});
            skLineSegment(sketch, "E2.10.8.1", {"start": v(393.7, 342.9) * mm, "end": v(419.1, 342.9) * mm});
            skLineSegment(sketch, "E2.10.8.2", {"start": v(393.7, 317.5) * mm, "end": v(419.1, 317.5) * mm});
            skLineSegment(sketch, "E2.10.8.3", {"start": v(393.7, 317.5) * mm, "end": v(393.7, 342.9) * mm});
            skLineSegment(sketch, "E2.10.9.0", {"start": v(419.1, 355.6) * mm, "end": v(419.1, 381) * mm});
            skLineSegment(sketch, "E2.10.9.1", {"start": v(393.7, 381) * mm, "end": v(419.1, 381) * mm});
            skLineSegment(sketch, "E2.10.9.2", {"start": v(393.7, 355.6) * mm, "end": v(419.1, 355.6) * mm});
            skLineSegment(sketch, "E2.10.9.3", {"start": v(393.7, 355.6) * mm, "end": v(393.7, 381) * mm});
            skLineSegment(sketch, "E2.10.10.0", {"start": v(419.1, 393.7) * mm, "end": v(419.1, 419.1) * mm});
            skLineSegment(sketch, "E2.10.10.1", {"start": v(393.7, 419.1) * mm, "end": v(419.1, 419.1) * mm});
            skLineSegment(sketch, "E2.10.10.2", {"start": v(393.7, 393.7) * mm, "end": v(419.1, 393.7) * mm});
            skLineSegment(sketch, "E2.10.10.3", {"start": v(393.7, 393.7) * mm, "end": v(393.7, 419.1) * mm});
            skLineSegment(sketch, "E2.10.11.0", {"start": v(419.1, 431.8) * mm, "end": v(419.1, 457.2) * mm});
            skLineSegment(sketch, "E2.10.11.1", {"start": v(393.7, 457.2) * mm, "end": v(419.1, 457.2) * mm});
            skLineSegment(sketch, "E2.10.11.2", {"start": v(393.7, 431.8) * mm, "end": v(419.1, 431.8) * mm});
            skLineSegment(sketch, "E2.10.11.3", {"start": v(393.7, 431.8) * mm, "end": v(393.7, 457.2) * mm});
            skLineSegment(sketch, "E2.10.12.0", {"start": v(419.1, 469.9) * mm, "end": v(419.1, 495.3) * mm});
            skLineSegment(sketch, "E2.10.12.1", {"start": v(393.7, 495.3) * mm, "end": v(419.1, 495.3) * mm});
            skLineSegment(sketch, "E2.10.12.2", {"start": v(393.7, 469.9) * mm, "end": v(419.1, 469.9) * mm});
            skLineSegment(sketch, "E2.10.12.3", {"start": v(393.7, 469.9) * mm, "end": v(393.7, 495.3) * mm});
            skLineSegment(sketch, "E2.10.13.0", {"start": v(419.1, 508) * mm, "end": v(419.1, 533.4) * mm});
            skLineSegment(sketch, "E2.10.13.1", {"start": v(393.7, 533.4) * mm, "end": v(419.1, 533.4) * mm});
            skLineSegment(sketch, "E2.10.13.2", {"start": v(393.7, 508) * mm, "end": v(419.1, 508) * mm});
            skLineSegment(sketch, "E2.10.13.3", {"start": v(393.7, 508) * mm, "end": v(393.7, 533.4) * mm});
            skLineSegment(sketch, "E2.10.14.0", {"start": v(419.1, 546.1) * mm, "end": v(419.1, 571.5) * mm});
            skLineSegment(sketch, "E2.10.14.1", {"start": v(393.7, 571.5) * mm, "end": v(419.1, 571.5) * mm});
            skLineSegment(sketch, "E2.10.14.2", {"start": v(393.7, 546.1) * mm, "end": v(419.1, 546.1) * mm});
            skLineSegment(sketch, "E2.10.14.3", {"start": v(393.7, 546.1) * mm, "end": v(393.7, 571.5) * mm});
            skLineSegment(sketch, "E2.10.15.0", {"start": v(419.1, 584.2) * mm, "end": v(419.1, 609.6) * mm});
            skLineSegment(sketch, "E2.10.15.1", {"start": v(393.7, 609.6) * mm, "end": v(419.1, 609.6) * mm});
            skLineSegment(sketch, "E2.10.15.2", {"start": v(393.7, 584.2) * mm, "end": v(419.1, 584.2) * mm});
            skLineSegment(sketch, "E2.10.15.3", {"start": v(393.7, 584.2) * mm, "end": v(393.7, 609.6) * mm});
            skLineSegment(sketch, "E2.10.16.0", {"start": v(419.1, 622.3) * mm, "end": v(419.1, 647.7) * mm});
            skLineSegment(sketch, "E2.10.16.1", {"start": v(393.7, 647.7) * mm, "end": v(419.1, 647.7) * mm});
            skLineSegment(sketch, "E2.10.16.2", {"start": v(393.7, 622.3) * mm, "end": v(419.1, 622.3) * mm});
            skLineSegment(sketch, "E2.10.16.3", {"start": v(393.7, 622.3) * mm, "end": v(393.7, 647.7) * mm});
            skLineSegment(sketch, "E2.10.17.0", {"start": v(419.1, 660.4) * mm, "end": v(419.1, 685.8) * mm});
            skLineSegment(sketch, "E2.10.17.1", {"start": v(393.7, 685.8) * mm, "end": v(419.1, 685.8) * mm});
            skLineSegment(sketch, "E2.10.17.2", {"start": v(393.7, 660.4) * mm, "end": v(419.1, 660.4) * mm});
            skLineSegment(sketch, "E2.10.17.3", {"start": v(393.7, 660.4) * mm, "end": v(393.7, 685.8) * mm});
            skLineSegment(sketch, "E2.10.18.0", {"start": v(419.1, 698.5) * mm, "end": v(419.1, 723.9) * mm});
            skLineSegment(sketch, "E2.10.18.1", {"start": v(393.7, 723.9) * mm, "end": v(419.1, 723.9) * mm});
            skLineSegment(sketch, "E2.10.18.2", {"start": v(393.7, 698.5) * mm, "end": v(419.1, 698.5) * mm});
            skLineSegment(sketch, "E2.10.18.3", {"start": v(393.7, 698.5) * mm, "end": v(393.7, 723.9) * mm});
            skLineSegment(sketch, "E2.10.19.0", {"start": v(419.1, 736.6) * mm, "end": v(419.1, 762) * mm});
            skLineSegment(sketch, "E2.10.19.1", {"start": v(393.7, 762) * mm, "end": v(419.1, 762) * mm});
            skLineSegment(sketch, "E2.10.19.2", {"start": v(393.7, 736.6) * mm, "end": v(419.1, 736.6) * mm});
            skLineSegment(sketch, "E2.10.19.3", {"start": v(393.7, 736.6) * mm, "end": v(393.7, 762) * mm});
            skLineSegment(sketch, "E2.11.0.0", {"start": v(457.2, 12.7) * mm, "end": v(457.2, 38.1) * mm});
            skLineSegment(sketch, "E2.11.0.1", {"start": v(431.8, 38.1) * mm, "end": v(457.2, 38.1) * mm});
            skLineSegment(sketch, "E2.11.0.2", {"start": v(431.8, 12.7) * mm, "end": v(457.2, 12.7) * mm});
            skLineSegment(sketch, "E2.11.0.3", {"start": v(431.8, 12.7) * mm, "end": v(431.8, 38.1) * mm});
            skLineSegment(sketch, "E2.11.1.0", {"start": v(457.2, 50.8) * mm, "end": v(457.2, 76.2) * mm});
            skLineSegment(sketch, "E2.11.1.1", {"start": v(431.8, 76.2) * mm, "end": v(457.2, 76.2) * mm});
            skLineSegment(sketch, "E2.11.1.2", {"start": v(431.8, 50.8) * mm, "end": v(457.2, 50.8) * mm});
            skLineSegment(sketch, "E2.11.1.3", {"start": v(431.8, 50.8) * mm, "end": v(431.8, 76.2) * mm});
            skLineSegment(sketch, "E2.11.2.0", {"start": v(457.2, 88.9) * mm, "end": v(457.2, 114.3) * mm});
            skLineSegment(sketch, "E2.11.2.1", {"start": v(431.8, 114.3) * mm, "end": v(457.2, 114.3) * mm});
            skLineSegment(sketch, "E2.11.2.2", {"start": v(431.8, 88.9) * mm, "end": v(457.2, 88.9) * mm});
            skLineSegment(sketch, "E2.11.2.3", {"start": v(431.8, 88.9) * mm, "end": v(431.8, 114.3) * mm});
            skLineSegment(sketch, "E2.11.3.0", {"start": v(457.2, 127) * mm, "end": v(457.2, 152.4) * mm});
            skLineSegment(sketch, "E2.11.3.1", {"start": v(431.8, 152.4) * mm, "end": v(457.2, 152.4) * mm});
            skLineSegment(sketch, "E2.11.3.2", {"start": v(431.8, 127) * mm, "end": v(457.2, 127) * mm});
            skLineSegment(sketch, "E2.11.3.3", {"start": v(431.8, 127) * mm, "end": v(431.8, 152.4) * mm});
            skLineSegment(sketch, "E2.11.4.0", {"start": v(457.2, 165.1) * mm, "end": v(457.2, 190.5) * mm});
            skLineSegment(sketch, "E2.11.4.1", {"start": v(431.8, 190.5) * mm, "end": v(457.2, 190.5) * mm});
            skLineSegment(sketch, "E2.11.4.2", {"start": v(431.8, 165.1) * mm, "end": v(457.2, 165.1) * mm});
            skLineSegment(sketch, "E2.11.4.3", {"start": v(431.8, 165.1) * mm, "end": v(431.8, 190.5) * mm});
            skLineSegment(sketch, "E2.11.5.0", {"start": v(457.2, 203.2) * mm, "end": v(457.2, 228.6) * mm});
            skLineSegment(sketch, "E2.11.5.1", {"start": v(431.8, 228.6) * mm, "end": v(457.2, 228.6) * mm});
            skLineSegment(sketch, "E2.11.5.2", {"start": v(431.8, 203.2) * mm, "end": v(457.2, 203.2) * mm});
            skLineSegment(sketch, "E2.11.5.3", {"start": v(431.8, 203.2) * mm, "end": v(431.8, 228.6) * mm});
            skLineSegment(sketch, "E2.11.6.0", {"start": v(457.2, 241.3) * mm, "end": v(457.2, 266.7) * mm});
            skLineSegment(sketch, "E2.11.6.1", {"start": v(431.8, 266.7) * mm, "end": v(457.2, 266.7) * mm});
            skLineSegment(sketch, "E2.11.6.2", {"start": v(431.8, 241.3) * mm, "end": v(457.2, 241.3) * mm});
            skLineSegment(sketch, "E2.11.6.3", {"start": v(431.8, 241.3) * mm, "end": v(431.8, 266.7) * mm});
            skLineSegment(sketch, "E2.11.7.0", {"start": v(457.2, 279.4) * mm, "end": v(457.2, 304.8) * mm});
            skLineSegment(sketch, "E2.11.7.1", {"start": v(431.8, 304.8) * mm, "end": v(457.2, 304.8) * mm});
            skLineSegment(sketch, "E2.11.7.2", {"start": v(431.8, 279.4) * mm, "end": v(457.2, 279.4) * mm});
            skLineSegment(sketch, "E2.11.7.3", {"start": v(431.8, 279.4) * mm, "end": v(431.8, 304.8) * mm});
            skLineSegment(sketch, "E2.11.8.0", {"start": v(457.2, 317.5) * mm, "end": v(457.2, 342.9) * mm});
            skLineSegment(sketch, "E2.11.8.1", {"start": v(431.8, 342.9) * mm, "end": v(457.2, 342.9) * mm});
            skLineSegment(sketch, "E2.11.8.2", {"start": v(431.8, 317.5) * mm, "end": v(457.2, 317.5) * mm});
            skLineSegment(sketch, "E2.11.8.3", {"start": v(431.8, 317.5) * mm, "end": v(431.8, 342.9) * mm});
            skLineSegment(sketch, "E2.11.9.0", {"start": v(457.2, 355.6) * mm, "end": v(457.2, 381) * mm});
            skLineSegment(sketch, "E2.11.9.1", {"start": v(431.8, 381) * mm, "end": v(457.2, 381) * mm});
            skLineSegment(sketch, "E2.11.9.2", {"start": v(431.8, 355.6) * mm, "end": v(457.2, 355.6) * mm});
            skLineSegment(sketch, "E2.11.9.3", {"start": v(431.8, 355.6) * mm, "end": v(431.8, 381) * mm});
            skLineSegment(sketch, "E2.11.10.0", {"start": v(457.2, 393.7) * mm, "end": v(457.2, 419.1) * mm});
            skLineSegment(sketch, "E2.11.10.1", {"start": v(431.8, 419.1) * mm, "end": v(457.2, 419.1) * mm});
            skLineSegment(sketch, "E2.11.10.2", {"start": v(431.8, 393.7) * mm, "end": v(457.2, 393.7) * mm});
            skLineSegment(sketch, "E2.11.10.3", {"start": v(431.8, 393.7) * mm, "end": v(431.8, 419.1) * mm});
            skLineSegment(sketch, "E2.11.11.0", {"start": v(457.2, 431.8) * mm, "end": v(457.2, 457.2) * mm});
            skLineSegment(sketch, "E2.11.11.1", {"start": v(431.8, 457.2) * mm, "end": v(457.2, 457.2) * mm});
            skLineSegment(sketch, "E2.11.11.2", {"start": v(431.8, 431.8) * mm, "end": v(457.2, 431.8) * mm});
            skLineSegment(sketch, "E2.11.11.3", {"start": v(431.8, 431.8) * mm, "end": v(431.8, 457.2) * mm});
            skLineSegment(sketch, "E2.11.12.0", {"start": v(457.2, 469.9) * mm, "end": v(457.2, 495.3) * mm});
            skLineSegment(sketch, "E2.11.12.1", {"start": v(431.8, 495.3) * mm, "end": v(457.2, 495.3) * mm});
            skLineSegment(sketch, "E2.11.12.2", {"start": v(431.8, 469.9) * mm, "end": v(457.2, 469.9) * mm});
            skLineSegment(sketch, "E2.11.12.3", {"start": v(431.8, 469.9) * mm, "end": v(431.8, 495.3) * mm});
            skLineSegment(sketch, "E2.11.13.0", {"start": v(457.2, 508) * mm, "end": v(457.2, 533.4) * mm});
            skLineSegment(sketch, "E2.11.13.1", {"start": v(431.8, 533.4) * mm, "end": v(457.2, 533.4) * mm});
            skLineSegment(sketch, "E2.11.13.2", {"start": v(431.8, 508) * mm, "end": v(457.2, 508) * mm});
            skLineSegment(sketch, "E2.11.13.3", {"start": v(431.8, 508) * mm, "end": v(431.8, 533.4) * mm});
            skLineSegment(sketch, "E2.11.14.0", {"start": v(457.2, 546.1) * mm, "end": v(457.2, 571.5) * mm});
            skLineSegment(sketch, "E2.11.14.1", {"start": v(431.8, 571.5) * mm, "end": v(457.2, 571.5) * mm});
            skLineSegment(sketch, "E2.11.14.2", {"start": v(431.8, 546.1) * mm, "end": v(457.2, 546.1) * mm});
            skLineSegment(sketch, "E2.11.14.3", {"start": v(431.8, 546.1) * mm, "end": v(431.8, 571.5) * mm});
            skLineSegment(sketch, "E2.11.15.0", {"start": v(457.2, 584.2) * mm, "end": v(457.2, 609.6) * mm});
            skLineSegment(sketch, "E2.11.15.1", {"start": v(431.8, 609.6) * mm, "end": v(457.2, 609.6) * mm});
            skLineSegment(sketch, "E2.11.15.2", {"start": v(431.8, 584.2) * mm, "end": v(457.2, 584.2) * mm});
            skLineSegment(sketch, "E2.11.15.3", {"start": v(431.8, 584.2) * mm, "end": v(431.8, 609.6) * mm});
            skLineSegment(sketch, "E2.11.16.0", {"start": v(457.2, 622.3) * mm, "end": v(457.2, 647.7) * mm});
            skLineSegment(sketch, "E2.11.16.1", {"start": v(431.8, 647.7) * mm, "end": v(457.2, 647.7) * mm});
            skLineSegment(sketch, "E2.11.16.2", {"start": v(431.8, 622.3) * mm, "end": v(457.2, 622.3) * mm});
            skLineSegment(sketch, "E2.11.16.3", {"start": v(431.8, 622.3) * mm, "end": v(431.8, 647.7) * mm});
            skLineSegment(sketch, "E2.11.17.0", {"start": v(457.2, 660.4) * mm, "end": v(457.2, 685.8) * mm});
            skLineSegment(sketch, "E2.11.17.1", {"start": v(431.8, 685.8) * mm, "end": v(457.2, 685.8) * mm});
            skLineSegment(sketch, "E2.11.17.2", {"start": v(431.8, 660.4) * mm, "end": v(457.2, 660.4) * mm});
            skLineSegment(sketch, "E2.11.17.3", {"start": v(431.8, 660.4) * mm, "end": v(431.8, 685.8) * mm});
            skLineSegment(sketch, "E2.11.18.0", {"start": v(457.2, 698.5) * mm, "end": v(457.2, 723.9) * mm});
            skLineSegment(sketch, "E2.11.18.1", {"start": v(431.8, 723.9) * mm, "end": v(457.2, 723.9) * mm});
            skLineSegment(sketch, "E2.11.18.2", {"start": v(431.8, 698.5) * mm, "end": v(457.2, 698.5) * mm});
            skLineSegment(sketch, "E2.11.18.3", {"start": v(431.8, 698.5) * mm, "end": v(431.8, 723.9) * mm});
            skLineSegment(sketch, "E2.11.19.0", {"start": v(457.2, 736.6) * mm, "end": v(457.2, 762) * mm});
            skLineSegment(sketch, "E2.11.19.1", {"start": v(431.8, 762) * mm, "end": v(457.2, 762) * mm});
            skLineSegment(sketch, "E2.11.19.2", {"start": v(431.8, 736.6) * mm, "end": v(457.2, 736.6) * mm});
            skLineSegment(sketch, "E2.11.19.3", {"start": v(431.8, 736.6) * mm, "end": v(431.8, 762) * mm});
            skLineSegment(sketch, "E2.12.0.0", {"start": v(495.3, 12.7) * mm, "end": v(495.3, 38.1) * mm});
            skLineSegment(sketch, "E2.12.0.1", {"start": v(469.9, 38.1) * mm, "end": v(495.3, 38.1) * mm});
            skLineSegment(sketch, "E2.12.0.2", {"start": v(469.9, 12.7) * mm, "end": v(495.3, 12.7) * mm});
            skLineSegment(sketch, "E2.12.0.3", {"start": v(469.9, 12.7) * mm, "end": v(469.9, 38.1) * mm});
            skLineSegment(sketch, "E2.12.1.0", {"start": v(495.3, 50.8) * mm, "end": v(495.3, 76.2) * mm});
            skLineSegment(sketch, "E2.12.1.1", {"start": v(469.9, 76.2) * mm, "end": v(495.3, 76.2) * mm});
            skLineSegment(sketch, "E2.12.1.2", {"start": v(469.9, 50.8) * mm, "end": v(495.3, 50.8) * mm});
            skLineSegment(sketch, "E2.12.1.3", {"start": v(469.9, 50.8) * mm, "end": v(469.9, 76.2) * mm});
            skLineSegment(sketch, "E2.12.2.0", {"start": v(495.3, 88.9) * mm, "end": v(495.3, 114.3) * mm});
            skLineSegment(sketch, "E2.12.2.1", {"start": v(469.9, 114.3) * mm, "end": v(495.3, 114.3) * mm});
            skLineSegment(sketch, "E2.12.2.2", {"start": v(469.9, 88.9) * mm, "end": v(495.3, 88.9) * mm});
            skLineSegment(sketch, "E2.12.2.3", {"start": v(469.9, 88.9) * mm, "end": v(469.9, 114.3) * mm});
            skLineSegment(sketch, "E2.12.3.0", {"start": v(495.3, 127) * mm, "end": v(495.3, 152.4) * mm});
            skLineSegment(sketch, "E2.12.3.1", {"start": v(469.9, 152.4) * mm, "end": v(495.3, 152.4) * mm});
            skLineSegment(sketch, "E2.12.3.2", {"start": v(469.9, 127) * mm, "end": v(495.3, 127) * mm});
            skLineSegment(sketch, "E2.12.3.3", {"start": v(469.9, 127) * mm, "end": v(469.9, 152.4) * mm});
            skLineSegment(sketch, "E2.12.4.0", {"start": v(495.3, 165.1) * mm, "end": v(495.3, 190.5) * mm});
            skLineSegment(sketch, "E2.12.4.1", {"start": v(469.9, 190.5) * mm, "end": v(495.3, 190.5) * mm});
            skLineSegment(sketch, "E2.12.4.2", {"start": v(469.9, 165.1) * mm, "end": v(495.3, 165.1) * mm});
            skLineSegment(sketch, "E2.12.4.3", {"start": v(469.9, 165.1) * mm, "end": v(469.9, 190.5) * mm});
            skLineSegment(sketch, "E2.12.5.0", {"start": v(495.3, 203.2) * mm, "end": v(495.3, 228.6) * mm});
            skLineSegment(sketch, "E2.12.5.1", {"start": v(469.9, 228.6) * mm, "end": v(495.3, 228.6) * mm});
            skLineSegment(sketch, "E2.12.5.2", {"start": v(469.9, 203.2) * mm, "end": v(495.3, 203.2) * mm});
            skLineSegment(sketch, "E2.12.5.3", {"start": v(469.9, 203.2) * mm, "end": v(469.9, 228.6) * mm});
            skLineSegment(sketch, "E2.12.6.0", {"start": v(495.3, 241.3) * mm, "end": v(495.3, 266.7) * mm});
            skLineSegment(sketch, "E2.12.6.1", {"start": v(469.9, 266.7) * mm, "end": v(495.3, 266.7) * mm});
            skLineSegment(sketch, "E2.12.6.2", {"start": v(469.9, 241.3) * mm, "end": v(495.3, 241.3) * mm});
            skLineSegment(sketch, "E2.12.6.3", {"start": v(469.9, 241.3) * mm, "end": v(469.9, 266.7) * mm});
            skLineSegment(sketch, "E2.12.7.0", {"start": v(495.3, 279.4) * mm, "end": v(495.3, 304.8) * mm});
            skLineSegment(sketch, "E2.12.7.1", {"start": v(469.9, 304.8) * mm, "end": v(495.3, 304.8) * mm});
            skLineSegment(sketch, "E2.12.7.2", {"start": v(469.9, 279.4) * mm, "end": v(495.3, 279.4) * mm});
            skLineSegment(sketch, "E2.12.7.3", {"start": v(469.9, 279.4) * mm, "end": v(469.9, 304.8) * mm});
            skLineSegment(sketch, "E2.12.8.0", {"start": v(495.3, 317.5) * mm, "end": v(495.3, 342.9) * mm});
            skLineSegment(sketch, "E2.12.8.1", {"start": v(469.9, 342.9) * mm, "end": v(495.3, 342.9) * mm});
            skLineSegment(sketch, "E2.12.8.2", {"start": v(469.9, 317.5) * mm, "end": v(495.3, 317.5) * mm});
            skLineSegment(sketch, "E2.12.8.3", {"start": v(469.9, 317.5) * mm, "end": v(469.9, 342.9) * mm});
            skLineSegment(sketch, "E2.12.9.0", {"start": v(495.3, 355.6) * mm, "end": v(495.3, 381) * mm});
            skLineSegment(sketch, "E2.12.9.1", {"start": v(469.9, 381) * mm, "end": v(495.3, 381) * mm});
            skLineSegment(sketch, "E2.12.9.2", {"start": v(469.9, 355.6) * mm, "end": v(495.3, 355.6) * mm});
            skLineSegment(sketch, "E2.12.9.3", {"start": v(469.9, 355.6) * mm, "end": v(469.9, 381) * mm});
            skLineSegment(sketch, "E2.12.10.0", {"start": v(495.3, 393.7) * mm, "end": v(495.3, 419.1) * mm});
            skLineSegment(sketch, "E2.12.10.1", {"start": v(469.9, 419.1) * mm, "end": v(495.3, 419.1) * mm});
            skLineSegment(sketch, "E2.12.10.2", {"start": v(469.9, 393.7) * mm, "end": v(495.3, 393.7) * mm});
            skLineSegment(sketch, "E2.12.10.3", {"start": v(469.9, 393.7) * mm, "end": v(469.9, 419.1) * mm});
            skLineSegment(sketch, "E2.12.11.0", {"start": v(495.3, 431.8) * mm, "end": v(495.3, 457.2) * mm});
            skLineSegment(sketch, "E2.12.11.1", {"start": v(469.9, 457.2) * mm, "end": v(495.3, 457.2) * mm});
            skLineSegment(sketch, "E2.12.11.2", {"start": v(469.9, 431.8) * mm, "end": v(495.3, 431.8) * mm});
            skLineSegment(sketch, "E2.12.11.3", {"start": v(469.9, 431.8) * mm, "end": v(469.9, 457.2) * mm});
            skLineSegment(sketch, "E2.12.12.0", {"start": v(495.3, 469.9) * mm, "end": v(495.3, 495.3) * mm});
            skLineSegment(sketch, "E2.12.12.1", {"start": v(469.9, 495.3) * mm, "end": v(495.3, 495.3) * mm});
            skLineSegment(sketch, "E2.12.12.2", {"start": v(469.9, 469.9) * mm, "end": v(495.3, 469.9) * mm});
            skLineSegment(sketch, "E2.12.12.3", {"start": v(469.9, 469.9) * mm, "end": v(469.9, 495.3) * mm});
            skLineSegment(sketch, "E2.12.13.0", {"start": v(495.3, 508) * mm, "end": v(495.3, 533.4) * mm});
            skLineSegment(sketch, "E2.12.13.1", {"start": v(469.9, 533.4) * mm, "end": v(495.3, 533.4) * mm});
            skLineSegment(sketch, "E2.12.13.2", {"start": v(469.9, 508) * mm, "end": v(495.3, 508) * mm});
            skLineSegment(sketch, "E2.12.13.3", {"start": v(469.9, 508) * mm, "end": v(469.9, 533.4) * mm});
            skLineSegment(sketch, "E2.12.14.0", {"start": v(495.3, 546.1) * mm, "end": v(495.3, 571.5) * mm});
            skLineSegment(sketch, "E2.12.14.1", {"start": v(469.9, 571.5) * mm, "end": v(495.3, 571.5) * mm});
            skLineSegment(sketch, "E2.12.14.2", {"start": v(469.9, 546.1) * mm, "end": v(495.3, 546.1) * mm});
            skLineSegment(sketch, "E2.12.14.3", {"start": v(469.9, 546.1) * mm, "end": v(469.9, 571.5) * mm});
            skLineSegment(sketch, "E2.12.15.0", {"start": v(495.3, 584.2) * mm, "end": v(495.3, 609.6) * mm});
            skLineSegment(sketch, "E2.12.15.1", {"start": v(469.9, 609.6) * mm, "end": v(495.3, 609.6) * mm});
            skLineSegment(sketch, "E2.12.15.2", {"start": v(469.9, 584.2) * mm, "end": v(495.3, 584.2) * mm});
            skLineSegment(sketch, "E2.12.15.3", {"start": v(469.9, 584.2) * mm, "end": v(469.9, 609.6) * mm});
            skLineSegment(sketch, "E2.12.16.0", {"start": v(495.3, 622.3) * mm, "end": v(495.3, 647.7) * mm});
            skLineSegment(sketch, "E2.12.16.1", {"start": v(469.9, 647.7) * mm, "end": v(495.3, 647.7) * mm});
            skLineSegment(sketch, "E2.12.16.2", {"start": v(469.9, 622.3) * mm, "end": v(495.3, 622.3) * mm});
            skLineSegment(sketch, "E2.12.16.3", {"start": v(469.9, 622.3) * mm, "end": v(469.9, 647.7) * mm});
            skLineSegment(sketch, "E2.12.17.0", {"start": v(495.3, 660.4) * mm, "end": v(495.3, 685.8) * mm});
            skLineSegment(sketch, "E2.12.17.1", {"start": v(469.9, 685.8) * mm, "end": v(495.3, 685.8) * mm});
            skLineSegment(sketch, "E2.12.17.2", {"start": v(469.9, 660.4) * mm, "end": v(495.3, 660.4) * mm});
            skLineSegment(sketch, "E2.12.17.3", {"start": v(469.9, 660.4) * mm, "end": v(469.9, 685.8) * mm});
            skLineSegment(sketch, "E2.12.18.0", {"start": v(495.3, 698.5) * mm, "end": v(495.3, 723.9) * mm});
            skLineSegment(sketch, "E2.12.18.1", {"start": v(469.9, 723.9) * mm, "end": v(495.3, 723.9) * mm});
            skLineSegment(sketch, "E2.12.18.2", {"start": v(469.9, 698.5) * mm, "end": v(495.3, 698.5) * mm});
            skLineSegment(sketch, "E2.12.18.3", {"start": v(469.9, 698.5) * mm, "end": v(469.9, 723.9) * mm});
            skLineSegment(sketch, "E2.12.19.0", {"start": v(495.3, 736.6) * mm, "end": v(495.3, 762) * mm});
            skLineSegment(sketch, "E2.12.19.1", {"start": v(469.9, 762) * mm, "end": v(495.3, 762) * mm});
            skLineSegment(sketch, "E2.12.19.2", {"start": v(469.9, 736.6) * mm, "end": v(495.3, 736.6) * mm});
            skLineSegment(sketch, "E2.12.19.3", {"start": v(469.9, 736.6) * mm, "end": v(469.9, 762) * mm});
            skLineSegment(sketch, "E2.13.0.0", {"start": v(533.4, 12.7) * mm, "end": v(533.4, 38.1) * mm});
            skLineSegment(sketch, "E2.13.0.1", {"start": v(508, 38.1) * mm, "end": v(533.4, 38.1) * mm});
            skLineSegment(sketch, "E2.13.0.2", {"start": v(508, 12.7) * mm, "end": v(533.4, 12.7) * mm});
            skLineSegment(sketch, "E2.13.0.3", {"start": v(508, 12.7) * mm, "end": v(508, 38.1) * mm});
            skLineSegment(sketch, "E2.13.1.0", {"start": v(533.4, 50.8) * mm, "end": v(533.4, 76.2) * mm});
            skLineSegment(sketch, "E2.13.1.1", {"start": v(508, 76.2) * mm, "end": v(533.4, 76.2) * mm});
            skLineSegment(sketch, "E2.13.1.2", {"start": v(508, 50.8) * mm, "end": v(533.4, 50.8) * mm});
            skLineSegment(sketch, "E2.13.1.3", {"start": v(508, 50.8) * mm, "end": v(508, 76.2) * mm});
            skLineSegment(sketch, "E2.13.2.0", {"start": v(533.4, 88.9) * mm, "end": v(533.4, 114.3) * mm});
            skLineSegment(sketch, "E2.13.2.1", {"start": v(508, 114.3) * mm, "end": v(533.4, 114.3) * mm});
            skLineSegment(sketch, "E2.13.2.2", {"start": v(508, 88.9) * mm, "end": v(533.4, 88.9) * mm});
            skLineSegment(sketch, "E2.13.2.3", {"start": v(508, 88.9) * mm, "end": v(508, 114.3) * mm});
            skLineSegment(sketch, "E2.13.3.0", {"start": v(533.4, 127) * mm, "end": v(533.4, 152.4) * mm});
            skLineSegment(sketch, "E2.13.3.1", {"start": v(508, 152.4) * mm, "end": v(533.4, 152.4) * mm});
            skLineSegment(sketch, "E2.13.3.2", {"start": v(508, 127) * mm, "end": v(533.4, 127) * mm});
            skLineSegment(sketch, "E2.13.3.3", {"start": v(508, 127) * mm, "end": v(508, 152.4) * mm});
            skLineSegment(sketch, "E2.13.4.0", {"start": v(533.4, 165.1) * mm, "end": v(533.4, 190.5) * mm});
            skLineSegment(sketch, "E2.13.4.1", {"start": v(508, 190.5) * mm, "end": v(533.4, 190.5) * mm});
            skLineSegment(sketch, "E2.13.4.2", {"start": v(508, 165.1) * mm, "end": v(533.4, 165.1) * mm});
            skLineSegment(sketch, "E2.13.4.3", {"start": v(508, 165.1) * mm, "end": v(508, 190.5) * mm});
            skLineSegment(sketch, "E2.13.5.0", {"start": v(533.4, 203.2) * mm, "end": v(533.4, 228.6) * mm});
            skLineSegment(sketch, "E2.13.5.1", {"start": v(508, 228.6) * mm, "end": v(533.4, 228.6) * mm});
            skLineSegment(sketch, "E2.13.5.2", {"start": v(508, 203.2) * mm, "end": v(533.4, 203.2) * mm});
            skLineSegment(sketch, "E2.13.5.3", {"start": v(508, 203.2) * mm, "end": v(508, 228.6) * mm});
            skLineSegment(sketch, "E2.13.6.0", {"start": v(533.4, 241.3) * mm, "end": v(533.4, 266.7) * mm});
            skLineSegment(sketch, "E2.13.6.1", {"start": v(508, 266.7) * mm, "end": v(533.4, 266.7) * mm});
            skLineSegment(sketch, "E2.13.6.2", {"start": v(508, 241.3) * mm, "end": v(533.4, 241.3) * mm});
            skLineSegment(sketch, "E2.13.6.3", {"start": v(508, 241.3) * mm, "end": v(508, 266.7) * mm});
            skLineSegment(sketch, "E2.13.7.0", {"start": v(533.4, 279.4) * mm, "end": v(533.4, 304.8) * mm});
            skLineSegment(sketch, "E2.13.7.1", {"start": v(508, 304.8) * mm, "end": v(533.4, 304.8) * mm});
            skLineSegment(sketch, "E2.13.7.2", {"start": v(508, 279.4) * mm, "end": v(533.4, 279.4) * mm});
            skLineSegment(sketch, "E2.13.7.3", {"start": v(508, 279.4) * mm, "end": v(508, 304.8) * mm});
            skLineSegment(sketch, "E2.13.8.0", {"start": v(533.4, 317.5) * mm, "end": v(533.4, 342.9) * mm});
            skLineSegment(sketch, "E2.13.8.1", {"start": v(508, 342.9) * mm, "end": v(533.4, 342.9) * mm});
            skLineSegment(sketch, "E2.13.8.2", {"start": v(508, 317.5) * mm, "end": v(533.4, 317.5) * mm});
            skLineSegment(sketch, "E2.13.8.3", {"start": v(508, 317.5) * mm, "end": v(508, 342.9) * mm});
            skLineSegment(sketch, "E2.13.9.0", {"start": v(533.4, 355.6) * mm, "end": v(533.4, 381) * mm});
            skLineSegment(sketch, "E2.13.9.1", {"start": v(508, 381) * mm, "end": v(533.4, 381) * mm});
            skLineSegment(sketch, "E2.13.9.2", {"start": v(508, 355.6) * mm, "end": v(533.4, 355.6) * mm});
            skLineSegment(sketch, "E2.13.9.3", {"start": v(508, 355.6) * mm, "end": v(508, 381) * mm});
            skLineSegment(sketch, "E2.13.10.0", {"start": v(533.4, 393.7) * mm, "end": v(533.4, 419.1) * mm});
            skLineSegment(sketch, "E2.13.10.1", {"start": v(508, 419.1) * mm, "end": v(533.4, 419.1) * mm});
            skLineSegment(sketch, "E2.13.10.2", {"start": v(508, 393.7) * mm, "end": v(533.4, 393.7) * mm});
            skLineSegment(sketch, "E2.13.10.3", {"start": v(508, 393.7) * mm, "end": v(508, 419.1) * mm});
            skLineSegment(sketch, "E2.13.11.0", {"start": v(533.4, 431.8) * mm, "end": v(533.4, 457.2) * mm});
            skLineSegment(sketch, "E2.13.11.1", {"start": v(508, 457.2) * mm, "end": v(533.4, 457.2) * mm});
            skLineSegment(sketch, "E2.13.11.2", {"start": v(508, 431.8) * mm, "end": v(533.4, 431.8) * mm});
            skLineSegment(sketch, "E2.13.11.3", {"start": v(508, 431.8) * mm, "end": v(508, 457.2) * mm});
            skLineSegment(sketch, "E2.13.12.0", {"start": v(533.4, 469.9) * mm, "end": v(533.4, 495.3) * mm});
            skLineSegment(sketch, "E2.13.12.1", {"start": v(508, 495.3) * mm, "end": v(533.4, 495.3) * mm});
            skLineSegment(sketch, "E2.13.12.2", {"start": v(508, 469.9) * mm, "end": v(533.4, 469.9) * mm});
            skLineSegment(sketch, "E2.13.12.3", {"start": v(508, 469.9) * mm, "end": v(508, 495.3) * mm});
            skLineSegment(sketch, "E2.13.13.0", {"start": v(533.4, 508) * mm, "end": v(533.4, 533.4) * mm});
            skLineSegment(sketch, "E2.13.13.1", {"start": v(508, 533.4) * mm, "end": v(533.4, 533.4) * mm});
            skLineSegment(sketch, "E2.13.13.2", {"start": v(508, 508) * mm, "end": v(533.4, 508) * mm});
            skLineSegment(sketch, "E2.13.13.3", {"start": v(508, 508) * mm, "end": v(508, 533.4) * mm});
            skLineSegment(sketch, "E2.13.14.0", {"start": v(533.4, 546.1) * mm, "end": v(533.4, 571.5) * mm});
            skLineSegment(sketch, "E2.13.14.1", {"start": v(508, 571.5) * mm, "end": v(533.4, 571.5) * mm});
            skLineSegment(sketch, "E2.13.14.2", {"start": v(508, 546.1) * mm, "end": v(533.4, 546.1) * mm});
            skLineSegment(sketch, "E2.13.14.3", {"start": v(508, 546.1) * mm, "end": v(508, 571.5) * mm});
            skLineSegment(sketch, "E2.13.15.0", {"start": v(533.4, 584.2) * mm, "end": v(533.4, 609.6) * mm});
            skLineSegment(sketch, "E2.13.15.1", {"start": v(508, 609.6) * mm, "end": v(533.4, 609.6) * mm});
            skLineSegment(sketch, "E2.13.15.2", {"start": v(508, 584.2) * mm, "end": v(533.4, 584.2) * mm});
            skLineSegment(sketch, "E2.13.15.3", {"start": v(508, 584.2) * mm, "end": v(508, 609.6) * mm});
            skLineSegment(sketch, "E2.13.16.0", {"start": v(533.4, 622.3) * mm, "end": v(533.4, 647.7) * mm});
            skLineSegment(sketch, "E2.13.16.1", {"start": v(508, 647.7) * mm, "end": v(533.4, 647.7) * mm});
            skLineSegment(sketch, "E2.13.16.2", {"start": v(508, 622.3) * mm, "end": v(533.4, 622.3) * mm});
            skLineSegment(sketch, "E2.13.16.3", {"start": v(508, 622.3) * mm, "end": v(508, 647.7) * mm});
            skLineSegment(sketch, "E2.13.17.0", {"start": v(533.4, 660.4) * mm, "end": v(533.4, 685.8) * mm});
            skLineSegment(sketch, "E2.13.17.1", {"start": v(508, 685.8) * mm, "end": v(533.4, 685.8) * mm});
            skLineSegment(sketch, "E2.13.17.2", {"start": v(508, 660.4) * mm, "end": v(533.4, 660.4) * mm});
            skLineSegment(sketch, "E2.13.17.3", {"start": v(508, 660.4) * mm, "end": v(508, 685.8) * mm});
            skLineSegment(sketch, "E2.13.18.0", {"start": v(533.4, 698.5) * mm, "end": v(533.4, 723.9) * mm});
            skLineSegment(sketch, "E2.13.18.1", {"start": v(508, 723.9) * mm, "end": v(533.4, 723.9) * mm});
            skLineSegment(sketch, "E2.13.18.2", {"start": v(508, 698.5) * mm, "end": v(533.4, 698.5) * mm});
            skLineSegment(sketch, "E2.13.18.3", {"start": v(508, 698.5) * mm, "end": v(508, 723.9) * mm});
            skLineSegment(sketch, "E2.13.19.0", {"start": v(533.4, 736.6) * mm, "end": v(533.4, 762) * mm});
            skLineSegment(sketch, "E2.13.19.1", {"start": v(508, 762) * mm, "end": v(533.4, 762) * mm});
            skLineSegment(sketch, "E2.13.19.2", {"start": v(508, 736.6) * mm, "end": v(533.4, 736.6) * mm});
            skLineSegment(sketch, "E2.13.19.3", {"start": v(508, 736.6) * mm, "end": v(508, 762) * mm});
            skLineSegment(sketch, "E2.14.0.0", {"start": v(571.5, 12.7) * mm, "end": v(571.5, 38.1) * mm});
            skLineSegment(sketch, "E2.14.0.1", {"start": v(546.1, 38.1) * mm, "end": v(571.5, 38.1) * mm});
            skLineSegment(sketch, "E2.14.0.2", {"start": v(546.1, 12.7) * mm, "end": v(571.5, 12.7) * mm});
            skLineSegment(sketch, "E2.14.0.3", {"start": v(546.1, 12.7) * mm, "end": v(546.1, 38.1) * mm});
            skLineSegment(sketch, "E2.14.1.0", {"start": v(571.5, 50.8) * mm, "end": v(571.5, 76.2) * mm});
            skLineSegment(sketch, "E2.14.1.1", {"start": v(546.1, 76.2) * mm, "end": v(571.5, 76.2) * mm});
            skLineSegment(sketch, "E2.14.1.2", {"start": v(546.1, 50.8) * mm, "end": v(571.5, 50.8) * mm});
            skLineSegment(sketch, "E2.14.1.3", {"start": v(546.1, 50.8) * mm, "end": v(546.1, 76.2) * mm});
            skLineSegment(sketch, "E2.14.2.0", {"start": v(571.5, 88.9) * mm, "end": v(571.5, 114.3) * mm});
            skLineSegment(sketch, "E2.14.2.1", {"start": v(546.1, 114.3) * mm, "end": v(571.5, 114.3) * mm});
            skLineSegment(sketch, "E2.14.2.2", {"start": v(546.1, 88.9) * mm, "end": v(571.5, 88.9) * mm});
            skLineSegment(sketch, "E2.14.2.3", {"start": v(546.1, 88.9) * mm, "end": v(546.1, 114.3) * mm});
            skLineSegment(sketch, "E2.14.3.0", {"start": v(571.5, 127) * mm, "end": v(571.5, 152.4) * mm});
            skLineSegment(sketch, "E2.14.3.1", {"start": v(546.1, 152.4) * mm, "end": v(571.5, 152.4) * mm});
            skLineSegment(sketch, "E2.14.3.2", {"start": v(546.1, 127) * mm, "end": v(571.5, 127) * mm});
            skLineSegment(sketch, "E2.14.3.3", {"start": v(546.1, 127) * mm, "end": v(546.1, 152.4) * mm});
            skLineSegment(sketch, "E2.14.4.0", {"start": v(571.5, 165.1) * mm, "end": v(571.5, 190.5) * mm});
            skLineSegment(sketch, "E2.14.4.1", {"start": v(546.1, 190.5) * mm, "end": v(571.5, 190.5) * mm});
            skLineSegment(sketch, "E2.14.4.2", {"start": v(546.1, 165.1) * mm, "end": v(571.5, 165.1) * mm});
            skLineSegment(sketch, "E2.14.4.3", {"start": v(546.1, 165.1) * mm, "end": v(546.1, 190.5) * mm});
            skLineSegment(sketch, "E2.14.5.0", {"start": v(571.5, 203.2) * mm, "end": v(571.5, 228.6) * mm});
            skLineSegment(sketch, "E2.14.5.1", {"start": v(546.1, 228.6) * mm, "end": v(571.5, 228.6) * mm});
            skLineSegment(sketch, "E2.14.5.2", {"start": v(546.1, 203.2) * mm, "end": v(571.5, 203.2) * mm});
            skLineSegment(sketch, "E2.14.5.3", {"start": v(546.1, 203.2) * mm, "end": v(546.1, 228.6) * mm});
            skLineSegment(sketch, "E2.14.6.0", {"start": v(571.5, 241.3) * mm, "end": v(571.5, 266.7) * mm});
            skLineSegment(sketch, "E2.14.6.1", {"start": v(546.1, 266.7) * mm, "end": v(571.5, 266.7) * mm});
            skLineSegment(sketch, "E2.14.6.2", {"start": v(546.1, 241.3) * mm, "end": v(571.5, 241.3) * mm});
            skLineSegment(sketch, "E2.14.6.3", {"start": v(546.1, 241.3) * mm, "end": v(546.1, 266.7) * mm});
            skLineSegment(sketch, "E2.14.7.0", {"start": v(571.5, 279.4) * mm, "end": v(571.5, 304.8) * mm});
            skLineSegment(sketch, "E2.14.7.1", {"start": v(546.1, 304.8) * mm, "end": v(571.5, 304.8) * mm});
            skLineSegment(sketch, "E2.14.7.2", {"start": v(546.1, 279.4) * mm, "end": v(571.5, 279.4) * mm});
            skLineSegment(sketch, "E2.14.7.3", {"start": v(546.1, 279.4) * mm, "end": v(546.1, 304.8) * mm});
            skLineSegment(sketch, "E2.14.8.0", {"start": v(571.5, 317.5) * mm, "end": v(571.5, 342.9) * mm});
            skLineSegment(sketch, "E2.14.8.1", {"start": v(546.1, 342.9) * mm, "end": v(571.5, 342.9) * mm});
            skLineSegment(sketch, "E2.14.8.2", {"start": v(546.1, 317.5) * mm, "end": v(571.5, 317.5) * mm});
            skLineSegment(sketch, "E2.14.8.3", {"start": v(546.1, 317.5) * mm, "end": v(546.1, 342.9) * mm});
            skLineSegment(sketch, "E2.14.9.0", {"start": v(571.5, 355.6) * mm, "end": v(571.5, 381) * mm});
            skLineSegment(sketch, "E2.14.9.1", {"start": v(546.1, 381) * mm, "end": v(571.5, 381) * mm});
            skLineSegment(sketch, "E2.14.9.2", {"start": v(546.1, 355.6) * mm, "end": v(571.5, 355.6) * mm});
            skLineSegment(sketch, "E2.14.9.3", {"start": v(546.1, 355.6) * mm, "end": v(546.1, 381) * mm});
            skLineSegment(sketch, "E2.14.10.0", {"start": v(571.5, 393.7) * mm, "end": v(571.5, 419.1) * mm});
            skLineSegment(sketch, "E2.14.10.1", {"start": v(546.1, 419.1) * mm, "end": v(571.5, 419.1) * mm});
            skLineSegment(sketch, "E2.14.10.2", {"start": v(546.1, 393.7) * mm, "end": v(571.5, 393.7) * mm});
            skLineSegment(sketch, "E2.14.10.3", {"start": v(546.1, 393.7) * mm, "end": v(546.1, 419.1) * mm});
            skLineSegment(sketch, "E2.14.11.0", {"start": v(571.5, 431.8) * mm, "end": v(571.5, 457.2) * mm});
            skLineSegment(sketch, "E2.14.11.1", {"start": v(546.1, 457.2) * mm, "end": v(571.5, 457.2) * mm});
            skLineSegment(sketch, "E2.14.11.2", {"start": v(546.1, 431.8) * mm, "end": v(571.5, 431.8) * mm});
            skLineSegment(sketch, "E2.14.11.3", {"start": v(546.1, 431.8) * mm, "end": v(546.1, 457.2) * mm});
            skLineSegment(sketch, "E2.14.12.0", {"start": v(571.5, 469.9) * mm, "end": v(571.5, 495.3) * mm});
            skLineSegment(sketch, "E2.14.12.1", {"start": v(546.1, 495.3) * mm, "end": v(571.5, 495.3) * mm});
            skLineSegment(sketch, "E2.14.12.2", {"start": v(546.1, 469.9) * mm, "end": v(571.5, 469.9) * mm});
            skLineSegment(sketch, "E2.14.12.3", {"start": v(546.1, 469.9) * mm, "end": v(546.1, 495.3) * mm});
            skLineSegment(sketch, "E2.14.13.0", {"start": v(571.5, 508) * mm, "end": v(571.5, 533.4) * mm});
            skLineSegment(sketch, "E2.14.13.1", {"start": v(546.1, 533.4) * mm, "end": v(571.5, 533.4) * mm});
            skLineSegment(sketch, "E2.14.13.2", {"start": v(546.1, 508) * mm, "end": v(571.5, 508) * mm});
            skLineSegment(sketch, "E2.14.13.3", {"start": v(546.1, 508) * mm, "end": v(546.1, 533.4) * mm});
            skLineSegment(sketch, "E2.14.14.0", {"start": v(571.5, 546.1) * mm, "end": v(571.5, 571.5) * mm});
            skLineSegment(sketch, "E2.14.14.1", {"start": v(546.1, 571.5) * mm, "end": v(571.5, 571.5) * mm});
            skLineSegment(sketch, "E2.14.14.2", {"start": v(546.1, 546.1) * mm, "end": v(571.5, 546.1) * mm});
            skLineSegment(sketch, "E2.14.14.3", {"start": v(546.1, 546.1) * mm, "end": v(546.1, 571.5) * mm});
            skLineSegment(sketch, "E2.14.15.0", {"start": v(571.5, 584.2) * mm, "end": v(571.5, 609.6) * mm});
            skLineSegment(sketch, "E2.14.15.1", {"start": v(546.1, 609.6) * mm, "end": v(571.5, 609.6) * mm});
            skLineSegment(sketch, "E2.14.15.2", {"start": v(546.1, 584.2) * mm, "end": v(571.5, 584.2) * mm});
            skLineSegment(sketch, "E2.14.15.3", {"start": v(546.1, 584.2) * mm, "end": v(546.1, 609.6) * mm});
            skLineSegment(sketch, "E2.14.16.0", {"start": v(571.5, 622.3) * mm, "end": v(571.5, 647.7) * mm});
            skLineSegment(sketch, "E2.14.16.1", {"start": v(546.1, 647.7) * mm, "end": v(571.5, 647.7) * mm});
            skLineSegment(sketch, "E2.14.16.2", {"start": v(546.1, 622.3) * mm, "end": v(571.5, 622.3) * mm});
            skLineSegment(sketch, "E2.14.16.3", {"start": v(546.1, 622.3) * mm, "end": v(546.1, 647.7) * mm});
            skLineSegment(sketch, "E2.14.17.0", {"start": v(571.5, 660.4) * mm, "end": v(571.5, 685.8) * mm});
            skLineSegment(sketch, "E2.14.17.1", {"start": v(546.1, 685.8) * mm, "end": v(571.5, 685.8) * mm});
            skLineSegment(sketch, "E2.14.17.2", {"start": v(546.1, 660.4) * mm, "end": v(571.5, 660.4) * mm});
            skLineSegment(sketch, "E2.14.17.3", {"start": v(546.1, 660.4) * mm, "end": v(546.1, 685.8) * mm});
            skLineSegment(sketch, "E2.14.18.0", {"start": v(571.5, 698.5) * mm, "end": v(571.5, 723.9) * mm});
            skLineSegment(sketch, "E2.14.18.1", {"start": v(546.1, 723.9) * mm, "end": v(571.5, 723.9) * mm});
            skLineSegment(sketch, "E2.14.18.2", {"start": v(546.1, 698.5) * mm, "end": v(571.5, 698.5) * mm});
            skLineSegment(sketch, "E2.14.18.3", {"start": v(546.1, 698.5) * mm, "end": v(546.1, 723.9) * mm});
            skLineSegment(sketch, "E2.14.19.0", {"start": v(571.5, 736.6) * mm, "end": v(571.5, 762) * mm});
            skLineSegment(sketch, "E2.14.19.1", {"start": v(546.1, 762) * mm, "end": v(571.5, 762) * mm});
            skLineSegment(sketch, "E2.14.19.2", {"start": v(546.1, 736.6) * mm, "end": v(571.5, 736.6) * mm});
            skLineSegment(sketch, "E2.14.19.3", {"start": v(546.1, 736.6) * mm, "end": v(546.1, 762) * mm});
            skLineSegment(sketch, "E2.15.0.0", {"start": v(609.6, 12.7) * mm, "end": v(609.6, 38.1) * mm});
            skLineSegment(sketch, "E2.15.0.1", {"start": v(584.2, 38.1) * mm, "end": v(609.6, 38.1) * mm});
            skLineSegment(sketch, "E2.15.0.2", {"start": v(584.2, 12.7) * mm, "end": v(609.6, 12.7) * mm});
            skLineSegment(sketch, "E2.15.0.3", {"start": v(584.2, 12.7) * mm, "end": v(584.2, 38.1) * mm});
            skLineSegment(sketch, "E2.15.1.0", {"start": v(609.6, 50.8) * mm, "end": v(609.6, 76.2) * mm});
            skLineSegment(sketch, "E2.15.1.1", {"start": v(584.2, 76.2) * mm, "end": v(609.6, 76.2) * mm});
            skLineSegment(sketch, "E2.15.1.2", {"start": v(584.2, 50.8) * mm, "end": v(609.6, 50.8) * mm});
            skLineSegment(sketch, "E2.15.1.3", {"start": v(584.2, 50.8) * mm, "end": v(584.2, 76.2) * mm});
            skLineSegment(sketch, "E2.15.2.0", {"start": v(609.6, 88.9) * mm, "end": v(609.6, 114.3) * mm});
            skLineSegment(sketch, "E2.15.2.1", {"start": v(584.2, 114.3) * mm, "end": v(609.6, 114.3) * mm});
            skLineSegment(sketch, "E2.15.2.2", {"start": v(584.2, 88.9) * mm, "end": v(609.6, 88.9) * mm});
            skLineSegment(sketch, "E2.15.2.3", {"start": v(584.2, 88.9) * mm, "end": v(584.2, 114.3) * mm});
            skLineSegment(sketch, "E2.15.3.0", {"start": v(609.6, 127) * mm, "end": v(609.6, 152.4) * mm});
            skLineSegment(sketch, "E2.15.3.1", {"start": v(584.2, 152.4) * mm, "end": v(609.6, 152.4) * mm});
            skLineSegment(sketch, "E2.15.3.2", {"start": v(584.2, 127) * mm, "end": v(609.6, 127) * mm});
            skLineSegment(sketch, "E2.15.3.3", {"start": v(584.2, 127) * mm, "end": v(584.2, 152.4) * mm});
            skLineSegment(sketch, "E2.15.4.0", {"start": v(609.6, 165.1) * mm, "end": v(609.6, 190.5) * mm});
            skLineSegment(sketch, "E2.15.4.1", {"start": v(584.2, 190.5) * mm, "end": v(609.6, 190.5) * mm});
            skLineSegment(sketch, "E2.15.4.2", {"start": v(584.2, 165.1) * mm, "end": v(609.6, 165.1) * mm});
            skLineSegment(sketch, "E2.15.4.3", {"start": v(584.2, 165.1) * mm, "end": v(584.2, 190.5) * mm});
            skLineSegment(sketch, "E2.15.5.0", {"start": v(609.6, 203.2) * mm, "end": v(609.6, 228.6) * mm});
            skLineSegment(sketch, "E2.15.5.1", {"start": v(584.2, 228.6) * mm, "end": v(609.6, 228.6) * mm});
            skLineSegment(sketch, "E2.15.5.2", {"start": v(584.2, 203.2) * mm, "end": v(609.6, 203.2) * mm});
            skLineSegment(sketch, "E2.15.5.3", {"start": v(584.2, 203.2) * mm, "end": v(584.2, 228.6) * mm});
            skLineSegment(sketch, "E2.15.6.0", {"start": v(609.6, 241.3) * mm, "end": v(609.6, 266.7) * mm});
            skLineSegment(sketch, "E2.15.6.1", {"start": v(584.2, 266.7) * mm, "end": v(609.6, 266.7) * mm});
            skLineSegment(sketch, "E2.15.6.2", {"start": v(584.2, 241.3) * mm, "end": v(609.6, 241.3) * mm});
            skLineSegment(sketch, "E2.15.6.3", {"start": v(584.2, 241.3) * mm, "end": v(584.2, 266.7) * mm});
            skLineSegment(sketch, "E2.15.7.0", {"start": v(609.6, 279.4) * mm, "end": v(609.6, 304.8) * mm});
            skLineSegment(sketch, "E2.15.7.1", {"start": v(584.2, 304.8) * mm, "end": v(609.6, 304.8) * mm});
            skLineSegment(sketch, "E2.15.7.2", {"start": v(584.2, 279.4) * mm, "end": v(609.6, 279.4) * mm});
            skLineSegment(sketch, "E2.15.7.3", {"start": v(584.2, 279.4) * mm, "end": v(584.2, 304.8) * mm});
            skLineSegment(sketch, "E2.15.8.0", {"start": v(609.6, 317.5) * mm, "end": v(609.6, 342.9) * mm});
            skLineSegment(sketch, "E2.15.8.1", {"start": v(584.2, 342.9) * mm, "end": v(609.6, 342.9) * mm});
            skLineSegment(sketch, "E2.15.8.2", {"start": v(584.2, 317.5) * mm, "end": v(609.6, 317.5) * mm});
            skLineSegment(sketch, "E2.15.8.3", {"start": v(584.2, 317.5) * mm, "end": v(584.2, 342.9) * mm});
            skLineSegment(sketch, "E2.15.9.0", {"start": v(609.6, 355.6) * mm, "end": v(609.6, 381) * mm});
            skLineSegment(sketch, "E2.15.9.1", {"start": v(584.2, 381) * mm, "end": v(609.6, 381) * mm});
            skLineSegment(sketch, "E2.15.9.2", {"start": v(584.2, 355.6) * mm, "end": v(609.6, 355.6) * mm});
            skLineSegment(sketch, "E2.15.9.3", {"start": v(584.2, 355.6) * mm, "end": v(584.2, 381) * mm});
            skLineSegment(sketch, "E2.15.10.0", {"start": v(609.6, 393.7) * mm, "end": v(609.6, 419.1) * mm});
            skLineSegment(sketch, "E2.15.10.1", {"start": v(584.2, 419.1) * mm, "end": v(609.6, 419.1) * mm});
            skLineSegment(sketch, "E2.15.10.2", {"start": v(584.2, 393.7) * mm, "end": v(609.6, 393.7) * mm});
            skLineSegment(sketch, "E2.15.10.3", {"start": v(584.2, 393.7) * mm, "end": v(584.2, 419.1) * mm});
            skLineSegment(sketch, "E2.15.11.0", {"start": v(609.6, 431.8) * mm, "end": v(609.6, 457.2) * mm});
            skLineSegment(sketch, "E2.15.11.1", {"start": v(584.2, 457.2) * mm, "end": v(609.6, 457.2) * mm});
            skLineSegment(sketch, "E2.15.11.2", {"start": v(584.2, 431.8) * mm, "end": v(609.6, 431.8) * mm});
            skLineSegment(sketch, "E2.15.11.3", {"start": v(584.2, 431.8) * mm, "end": v(584.2, 457.2) * mm});
            skLineSegment(sketch, "E2.15.12.0", {"start": v(609.6, 469.9) * mm, "end": v(609.6, 495.3) * mm});
            skLineSegment(sketch, "E2.15.12.1", {"start": v(584.2, 495.3) * mm, "end": v(609.6, 495.3) * mm});
            skLineSegment(sketch, "E2.15.12.2", {"start": v(584.2, 469.9) * mm, "end": v(609.6, 469.9) * mm});
            skLineSegment(sketch, "E2.15.12.3", {"start": v(584.2, 469.9) * mm, "end": v(584.2, 495.3) * mm});
            skLineSegment(sketch, "E2.15.13.0", {"start": v(609.6, 508) * mm, "end": v(609.6, 533.4) * mm});
            skLineSegment(sketch, "E2.15.13.1", {"start": v(584.2, 533.4) * mm, "end": v(609.6, 533.4) * mm});
            skLineSegment(sketch, "E2.15.13.2", {"start": v(584.2, 508) * mm, "end": v(609.6, 508) * mm});
            skLineSegment(sketch, "E2.15.13.3", {"start": v(584.2, 508) * mm, "end": v(584.2, 533.4) * mm});
            skLineSegment(sketch, "E2.15.14.0", {"start": v(609.6, 546.1) * mm, "end": v(609.6, 571.5) * mm});
            skLineSegment(sketch, "E2.15.14.1", {"start": v(584.2, 571.5) * mm, "end": v(609.6, 571.5) * mm});
            skLineSegment(sketch, "E2.15.14.2", {"start": v(584.2, 546.1) * mm, "end": v(609.6, 546.1) * mm});
            skLineSegment(sketch, "E2.15.14.3", {"start": v(584.2, 546.1) * mm, "end": v(584.2, 571.5) * mm});
            skLineSegment(sketch, "E2.15.15.0", {"start": v(609.6, 584.2) * mm, "end": v(609.6, 609.6) * mm});
            skLineSegment(sketch, "E2.15.15.1", {"start": v(584.2, 609.6) * mm, "end": v(609.6, 609.6) * mm});
            skLineSegment(sketch, "E2.15.15.2", {"start": v(584.2, 584.2) * mm, "end": v(609.6, 584.2) * mm});
            skLineSegment(sketch, "E2.15.15.3", {"start": v(584.2, 584.2) * mm, "end": v(584.2, 609.6) * mm});
            skLineSegment(sketch, "E2.15.16.0", {"start": v(609.6, 622.3) * mm, "end": v(609.6, 647.7) * mm});
            skLineSegment(sketch, "E2.15.16.1", {"start": v(584.2, 647.7) * mm, "end": v(609.6, 647.7) * mm});
            skLineSegment(sketch, "E2.15.16.2", {"start": v(584.2, 622.3) * mm, "end": v(609.6, 622.3) * mm});
            skLineSegment(sketch, "E2.15.16.3", {"start": v(584.2, 622.3) * mm, "end": v(584.2, 647.7) * mm});
            skLineSegment(sketch, "E2.15.17.0", {"start": v(609.6, 660.4) * mm, "end": v(609.6, 685.8) * mm});
            skLineSegment(sketch, "E2.15.17.1", {"start": v(584.2, 685.8) * mm, "end": v(609.6, 685.8) * mm});
            skLineSegment(sketch, "E2.15.17.2", {"start": v(584.2, 660.4) * mm, "end": v(609.6, 660.4) * mm});
            skLineSegment(sketch, "E2.15.17.3", {"start": v(584.2, 660.4) * mm, "end": v(584.2, 685.8) * mm});
            skLineSegment(sketch, "E2.15.18.0", {"start": v(609.6, 698.5) * mm, "end": v(609.6, 723.9) * mm});
            skLineSegment(sketch, "E2.15.18.1", {"start": v(584.2, 723.9) * mm, "end": v(609.6, 723.9) * mm});
            skLineSegment(sketch, "E2.15.18.2", {"start": v(584.2, 698.5) * mm, "end": v(609.6, 698.5) * mm});
            skLineSegment(sketch, "E2.15.18.3", {"start": v(584.2, 698.5) * mm, "end": v(584.2, 723.9) * mm});
            skLineSegment(sketch, "E2.15.19.0", {"start": v(609.6, 736.6) * mm, "end": v(609.6, 762) * mm});
            skLineSegment(sketch, "E2.15.19.1", {"start": v(584.2, 762) * mm, "end": v(609.6, 762) * mm});
            skLineSegment(sketch, "E2.15.19.2", {"start": v(584.2, 736.6) * mm, "end": v(609.6, 736.6) * mm});
            skLineSegment(sketch, "E2.15.19.3", {"start": v(584.2, 736.6) * mm, "end": v(584.2, 762) * mm});
            skLineSegment(sketch, "E2.16.0.0", {"start": v(647.7, 12.7) * mm, "end": v(647.7, 38.1) * mm});
            skLineSegment(sketch, "E2.16.0.1", {"start": v(622.3, 38.1) * mm, "end": v(647.7, 38.1) * mm});
            skLineSegment(sketch, "E2.16.0.2", {"start": v(622.3, 12.7) * mm, "end": v(647.7, 12.7) * mm});
            skLineSegment(sketch, "E2.16.0.3", {"start": v(622.3, 12.7) * mm, "end": v(622.3, 38.1) * mm});
            skLineSegment(sketch, "E2.16.1.0", {"start": v(647.7, 50.8) * mm, "end": v(647.7, 76.2) * mm});
            skLineSegment(sketch, "E2.16.1.1", {"start": v(622.3, 76.2) * mm, "end": v(647.7, 76.2) * mm});
            skLineSegment(sketch, "E2.16.1.2", {"start": v(622.3, 50.8) * mm, "end": v(647.7, 50.8) * mm});
            skLineSegment(sketch, "E2.16.1.3", {"start": v(622.3, 50.8) * mm, "end": v(622.3, 76.2) * mm});
            skLineSegment(sketch, "E2.16.2.0", {"start": v(647.7, 88.9) * mm, "end": v(647.7, 114.3) * mm});
            skLineSegment(sketch, "E2.16.2.1", {"start": v(622.3, 114.3) * mm, "end": v(647.7, 114.3) * mm});
            skLineSegment(sketch, "E2.16.2.2", {"start": v(622.3, 88.9) * mm, "end": v(647.7, 88.9) * mm});
            skLineSegment(sketch, "E2.16.2.3", {"start": v(622.3, 88.9) * mm, "end": v(622.3, 114.3) * mm});
            skLineSegment(sketch, "E2.16.3.0", {"start": v(647.7, 127) * mm, "end": v(647.7, 152.4) * mm});
            skLineSegment(sketch, "E2.16.3.1", {"start": v(622.3, 152.4) * mm, "end": v(647.7, 152.4) * mm});
            skLineSegment(sketch, "E2.16.3.2", {"start": v(622.3, 127) * mm, "end": v(647.7, 127) * mm});
            skLineSegment(sketch, "E2.16.3.3", {"start": v(622.3, 127) * mm, "end": v(622.3, 152.4) * mm});
            skLineSegment(sketch, "E2.16.4.0", {"start": v(647.7, 165.1) * mm, "end": v(647.7, 190.5) * mm});
            skLineSegment(sketch, "E2.16.4.1", {"start": v(622.3, 190.5) * mm, "end": v(647.7, 190.5) * mm});
            skLineSegment(sketch, "E2.16.4.2", {"start": v(622.3, 165.1) * mm, "end": v(647.7, 165.1) * mm});
            skLineSegment(sketch, "E2.16.4.3", {"start": v(622.3, 165.1) * mm, "end": v(622.3, 190.5) * mm});
            skLineSegment(sketch, "E2.16.5.0", {"start": v(647.7, 203.2) * mm, "end": v(647.7, 228.6) * mm});
            skLineSegment(sketch, "E2.16.5.1", {"start": v(622.3, 228.6) * mm, "end": v(647.7, 228.6) * mm});
            skLineSegment(sketch, "E2.16.5.2", {"start": v(622.3, 203.2) * mm, "end": v(647.7, 203.2) * mm});
            skLineSegment(sketch, "E2.16.5.3", {"start": v(622.3, 203.2) * mm, "end": v(622.3, 228.6) * mm});
            skLineSegment(sketch, "E2.16.6.0", {"start": v(647.7, 241.3) * mm, "end": v(647.7, 266.7) * mm});
            skLineSegment(sketch, "E2.16.6.1", {"start": v(622.3, 266.7) * mm, "end": v(647.7, 266.7) * mm});
            skLineSegment(sketch, "E2.16.6.2", {"start": v(622.3, 241.3) * mm, "end": v(647.7, 241.3) * mm});
            skLineSegment(sketch, "E2.16.6.3", {"start": v(622.3, 241.3) * mm, "end": v(622.3, 266.7) * mm});
            skLineSegment(sketch, "E2.16.7.0", {"start": v(647.7, 279.4) * mm, "end": v(647.7, 304.8) * mm});
            skLineSegment(sketch, "E2.16.7.1", {"start": v(622.3, 304.8) * mm, "end": v(647.7, 304.8) * mm});
            skLineSegment(sketch, "E2.16.7.2", {"start": v(622.3, 279.4) * mm, "end": v(647.7, 279.4) * mm});
            skLineSegment(sketch, "E2.16.7.3", {"start": v(622.3, 279.4) * mm, "end": v(622.3, 304.8) * mm});
            skLineSegment(sketch, "E2.16.8.0", {"start": v(647.7, 317.5) * mm, "end": v(647.7, 342.9) * mm});
            skLineSegment(sketch, "E2.16.8.1", {"start": v(622.3, 342.9) * mm, "end": v(647.7, 342.9) * mm});
            skLineSegment(sketch, "E2.16.8.2", {"start": v(622.3, 317.5) * mm, "end": v(647.7, 317.5) * mm});
            skLineSegment(sketch, "E2.16.8.3", {"start": v(622.3, 317.5) * mm, "end": v(622.3, 342.9) * mm});
            skLineSegment(sketch, "E2.16.9.0", {"start": v(647.7, 355.6) * mm, "end": v(647.7, 381) * mm});
            skLineSegment(sketch, "E2.16.9.1", {"start": v(622.3, 381) * mm, "end": v(647.7, 381) * mm});
            skLineSegment(sketch, "E2.16.9.2", {"start": v(622.3, 355.6) * mm, "end": v(647.7, 355.6) * mm});
            skLineSegment(sketch, "E2.16.9.3", {"start": v(622.3, 355.6) * mm, "end": v(622.3, 381) * mm});
            skLineSegment(sketch, "E2.16.10.0", {"start": v(647.7, 393.7) * mm, "end": v(647.7, 419.1) * mm});
            skLineSegment(sketch, "E2.16.10.1", {"start": v(622.3, 419.1) * mm, "end": v(647.7, 419.1) * mm});
            skLineSegment(sketch, "E2.16.10.2", {"start": v(622.3, 393.7) * mm, "end": v(647.7, 393.7) * mm});
            skLineSegment(sketch, "E2.16.10.3", {"start": v(622.3, 393.7) * mm, "end": v(622.3, 419.1) * mm});
            skLineSegment(sketch, "E2.16.11.0", {"start": v(647.7, 431.8) * mm, "end": v(647.7, 457.2) * mm});
            skLineSegment(sketch, "E2.16.11.1", {"start": v(622.3, 457.2) * mm, "end": v(647.7, 457.2) * mm});
            skLineSegment(sketch, "E2.16.11.2", {"start": v(622.3, 431.8) * mm, "end": v(647.7, 431.8) * mm});
            skLineSegment(sketch, "E2.16.11.3", {"start": v(622.3, 431.8) * mm, "end": v(622.3, 457.2) * mm});
            skLineSegment(sketch, "E2.16.12.0", {"start": v(647.7, 469.9) * mm, "end": v(647.7, 495.3) * mm});
            skLineSegment(sketch, "E2.16.12.1", {"start": v(622.3, 495.3) * mm, "end": v(647.7, 495.3) * mm});
            skLineSegment(sketch, "E2.16.12.2", {"start": v(622.3, 469.9) * mm, "end": v(647.7, 469.9) * mm});
            skLineSegment(sketch, "E2.16.12.3", {"start": v(622.3, 469.9) * mm, "end": v(622.3, 495.3) * mm});
            skLineSegment(sketch, "E2.16.13.0", {"start": v(647.7, 508) * mm, "end": v(647.7, 533.4) * mm});
            skLineSegment(sketch, "E2.16.13.1", {"start": v(622.3, 533.4) * mm, "end": v(647.7, 533.4) * mm});
            skLineSegment(sketch, "E2.16.13.2", {"start": v(622.3, 508) * mm, "end": v(647.7, 508) * mm});
            skLineSegment(sketch, "E2.16.13.3", {"start": v(622.3, 508) * mm, "end": v(622.3, 533.4) * mm});
            skLineSegment(sketch, "E2.16.14.0", {"start": v(647.7, 546.1) * mm, "end": v(647.7, 571.5) * mm});
            skLineSegment(sketch, "E2.16.14.1", {"start": v(622.3, 571.5) * mm, "end": v(647.7, 571.5) * mm});
            skLineSegment(sketch, "E2.16.14.2", {"start": v(622.3, 546.1) * mm, "end": v(647.7, 546.1) * mm});
            skLineSegment(sketch, "E2.16.14.3", {"start": v(622.3, 546.1) * mm, "end": v(622.3, 571.5) * mm});
            skLineSegment(sketch, "E2.16.15.0", {"start": v(647.7, 584.2) * mm, "end": v(647.7, 609.6) * mm});
            skLineSegment(sketch, "E2.16.15.1", {"start": v(622.3, 609.6) * mm, "end": v(647.7, 609.6) * mm});
            skLineSegment(sketch, "E2.16.15.2", {"start": v(622.3, 584.2) * mm, "end": v(647.7, 584.2) * mm});
            skLineSegment(sketch, "E2.16.15.3", {"start": v(622.3, 584.2) * mm, "end": v(622.3, 609.6) * mm});
            skLineSegment(sketch, "E2.16.16.0", {"start": v(647.7, 622.3) * mm, "end": v(647.7, 647.7) * mm});
            skLineSegment(sketch, "E2.16.16.1", {"start": v(622.3, 647.7) * mm, "end": v(647.7, 647.7) * mm});
            skLineSegment(sketch, "E2.16.16.2", {"start": v(622.3, 622.3) * mm, "end": v(647.7, 622.3) * mm});
            skLineSegment(sketch, "E2.16.16.3", {"start": v(622.3, 622.3) * mm, "end": v(622.3, 647.7) * mm});
            skLineSegment(sketch, "E2.16.17.0", {"start": v(647.7, 660.4) * mm, "end": v(647.7, 685.8) * mm});
            skLineSegment(sketch, "E2.16.17.1", {"start": v(622.3, 685.8) * mm, "end": v(647.7, 685.8) * mm});
            skLineSegment(sketch, "E2.16.17.2", {"start": v(622.3, 660.4) * mm, "end": v(647.7, 660.4) * mm});
            skLineSegment(sketch, "E2.16.17.3", {"start": v(622.3, 660.4) * mm, "end": v(622.3, 685.8) * mm});
            skLineSegment(sketch, "E2.16.18.0", {"start": v(647.7, 698.5) * mm, "end": v(647.7, 723.9) * mm});
            skLineSegment(sketch, "E2.16.18.1", {"start": v(622.3, 723.9) * mm, "end": v(647.7, 723.9) * mm});
            skLineSegment(sketch, "E2.16.18.2", {"start": v(622.3, 698.5) * mm, "end": v(647.7, 698.5) * mm});
            skLineSegment(sketch, "E2.16.18.3", {"start": v(622.3, 698.5) * mm, "end": v(622.3, 723.9) * mm});
            skLineSegment(sketch, "E2.16.19.0", {"start": v(647.7, 736.6) * mm, "end": v(647.7, 762) * mm});
            skLineSegment(sketch, "E2.16.19.1", {"start": v(622.3, 762) * mm, "end": v(647.7, 762) * mm});
            skLineSegment(sketch, "E2.16.19.2", {"start": v(622.3, 736.6) * mm, "end": v(647.7, 736.6) * mm});
            skLineSegment(sketch, "E2.16.19.3", {"start": v(622.3, 736.6) * mm, "end": v(622.3, 762) * mm});
            skLineSegment(sketch, "E2.17.0.0", {"start": v(685.8, 12.7) * mm, "end": v(685.8, 38.1) * mm});
            skLineSegment(sketch, "E2.17.0.1", {"start": v(660.4, 38.1) * mm, "end": v(685.8, 38.1) * mm});
            skLineSegment(sketch, "E2.17.0.2", {"start": v(660.4, 12.7) * mm, "end": v(685.8, 12.7) * mm});
            skLineSegment(sketch, "E2.17.0.3", {"start": v(660.4, 12.7) * mm, "end": v(660.4, 38.1) * mm});
            skLineSegment(sketch, "E2.17.1.0", {"start": v(685.8, 50.8) * mm, "end": v(685.8, 76.2) * mm});
            skLineSegment(sketch, "E2.17.1.1", {"start": v(660.4, 76.2) * mm, "end": v(685.8, 76.2) * mm});
            skLineSegment(sketch, "E2.17.1.2", {"start": v(660.4, 50.8) * mm, "end": v(685.8, 50.8) * mm});
            skLineSegment(sketch, "E2.17.1.3", {"start": v(660.4, 50.8) * mm, "end": v(660.4, 76.2) * mm});
            skLineSegment(sketch, "E2.17.2.0", {"start": v(685.8, 88.9) * mm, "end": v(685.8, 114.3) * mm});
            skLineSegment(sketch, "E2.17.2.1", {"start": v(660.4, 114.3) * mm, "end": v(685.8, 114.3) * mm});
            skLineSegment(sketch, "E2.17.2.2", {"start": v(660.4, 88.9) * mm, "end": v(685.8, 88.9) * mm});
            skLineSegment(sketch, "E2.17.2.3", {"start": v(660.4, 88.9) * mm, "end": v(660.4, 114.3) * mm});
            skLineSegment(sketch, "E2.17.3.0", {"start": v(685.8, 127) * mm, "end": v(685.8, 152.4) * mm});
            skLineSegment(sketch, "E2.17.3.1", {"start": v(660.4, 152.4) * mm, "end": v(685.8, 152.4) * mm});
            skLineSegment(sketch, "E2.17.3.2", {"start": v(660.4, 127) * mm, "end": v(685.8, 127) * mm});
            skLineSegment(sketch, "E2.17.3.3", {"start": v(660.4, 127) * mm, "end": v(660.4, 152.4) * mm});
            skLineSegment(sketch, "E2.17.4.0", {"start": v(685.8, 165.1) * mm, "end": v(685.8, 190.5) * mm});
            skLineSegment(sketch, "E2.17.4.1", {"start": v(660.4, 190.5) * mm, "end": v(685.8, 190.5) * mm});
            skLineSegment(sketch, "E2.17.4.2", {"start": v(660.4, 165.1) * mm, "end": v(685.8, 165.1) * mm});
            skLineSegment(sketch, "E2.17.4.3", {"start": v(660.4, 165.1) * mm, "end": v(660.4, 190.5) * mm});
            skLineSegment(sketch, "E2.17.5.0", {"start": v(685.8, 203.2) * mm, "end": v(685.8, 228.6) * mm});
            skLineSegment(sketch, "E2.17.5.1", {"start": v(660.4, 228.6) * mm, "end": v(685.8, 228.6) * mm});
            skLineSegment(sketch, "E2.17.5.2", {"start": v(660.4, 203.2) * mm, "end": v(685.8, 203.2) * mm});
            skLineSegment(sketch, "E2.17.5.3", {"start": v(660.4, 203.2) * mm, "end": v(660.4, 228.6) * mm});
            skLineSegment(sketch, "E2.17.6.0", {"start": v(685.8, 241.3) * mm, "end": v(685.8, 266.7) * mm});
            skLineSegment(sketch, "E2.17.6.1", {"start": v(660.4, 266.7) * mm, "end": v(685.8, 266.7) * mm});
            skLineSegment(sketch, "E2.17.6.2", {"start": v(660.4, 241.3) * mm, "end": v(685.8, 241.3) * mm});
            skLineSegment(sketch, "E2.17.6.3", {"start": v(660.4, 241.3) * mm, "end": v(660.4, 266.7) * mm});
            skLineSegment(sketch, "E2.17.7.0", {"start": v(685.8, 279.4) * mm, "end": v(685.8, 304.8) * mm});
            skLineSegment(sketch, "E2.17.7.1", {"start": v(660.4, 304.8) * mm, "end": v(685.8, 304.8) * mm});
            skLineSegment(sketch, "E2.17.7.2", {"start": v(660.4, 279.4) * mm, "end": v(685.8, 279.4) * mm});
            skLineSegment(sketch, "E2.17.7.3", {"start": v(660.4, 279.4) * mm, "end": v(660.4, 304.8) * mm});
            skLineSegment(sketch, "E2.17.8.0", {"start": v(685.8, 317.5) * mm, "end": v(685.8, 342.9) * mm});
            skLineSegment(sketch, "E2.17.8.1", {"start": v(660.4, 342.9) * mm, "end": v(685.8, 342.9) * mm});
            skLineSegment(sketch, "E2.17.8.2", {"start": v(660.4, 317.5) * mm, "end": v(685.8, 317.5) * mm});
            skLineSegment(sketch, "E2.17.8.3", {"start": v(660.4, 317.5) * mm, "end": v(660.4, 342.9) * mm});
            skLineSegment(sketch, "E2.17.9.0", {"start": v(685.8, 355.6) * mm, "end": v(685.8, 381) * mm});
            skLineSegment(sketch, "E2.17.9.1", {"start": v(660.4, 381) * mm, "end": v(685.8, 381) * mm});
            skLineSegment(sketch, "E2.17.9.2", {"start": v(660.4, 355.6) * mm, "end": v(685.8, 355.6) * mm});
            skLineSegment(sketch, "E2.17.9.3", {"start": v(660.4, 355.6) * mm, "end": v(660.4, 381) * mm});
            skLineSegment(sketch, "E2.17.10.0", {"start": v(685.8, 393.7) * mm, "end": v(685.8, 419.1) * mm});
            skLineSegment(sketch, "E2.17.10.1", {"start": v(660.4, 419.1) * mm, "end": v(685.8, 419.1) * mm});
            skLineSegment(sketch, "E2.17.10.2", {"start": v(660.4, 393.7) * mm, "end": v(685.8, 393.7) * mm});
            skLineSegment(sketch, "E2.17.10.3", {"start": v(660.4, 393.7) * mm, "end": v(660.4, 419.1) * mm});
            skLineSegment(sketch, "E2.17.11.0", {"start": v(685.8, 431.8) * mm, "end": v(685.8, 457.2) * mm});
            skLineSegment(sketch, "E2.17.11.1", {"start": v(660.4, 457.2) * mm, "end": v(685.8, 457.2) * mm});
            skLineSegment(sketch, "E2.17.11.2", {"start": v(660.4, 431.8) * mm, "end": v(685.8, 431.8) * mm});
            skLineSegment(sketch, "E2.17.11.3", {"start": v(660.4, 431.8) * mm, "end": v(660.4, 457.2) * mm});
            skLineSegment(sketch, "E2.17.12.0", {"start": v(685.8, 469.9) * mm, "end": v(685.8, 495.3) * mm});
            skLineSegment(sketch, "E2.17.12.1", {"start": v(660.4, 495.3) * mm, "end": v(685.8, 495.3) * mm});
            skLineSegment(sketch, "E2.17.12.2", {"start": v(660.4, 469.9) * mm, "end": v(685.8, 469.9) * mm});
            skLineSegment(sketch, "E2.17.12.3", {"start": v(660.4, 469.9) * mm, "end": v(660.4, 495.3) * mm});
            skLineSegment(sketch, "E2.17.13.0", {"start": v(685.8, 508) * mm, "end": v(685.8, 533.4) * mm});
            skLineSegment(sketch, "E2.17.13.1", {"start": v(660.4, 533.4) * mm, "end": v(685.8, 533.4) * mm});
            skLineSegment(sketch, "E2.17.13.2", {"start": v(660.4, 508) * mm, "end": v(685.8, 508) * mm});
            skLineSegment(sketch, "E2.17.13.3", {"start": v(660.4, 508) * mm, "end": v(660.4, 533.4) * mm});
            skLineSegment(sketch, "E2.17.14.0", {"start": v(685.8, 546.1) * mm, "end": v(685.8, 571.5) * mm});
            skLineSegment(sketch, "E2.17.14.1", {"start": v(660.4, 571.5) * mm, "end": v(685.8, 571.5) * mm});
            skLineSegment(sketch, "E2.17.14.2", {"start": v(660.4, 546.1) * mm, "end": v(685.8, 546.1) * mm});
            skLineSegment(sketch, "E2.17.14.3", {"start": v(660.4, 546.1) * mm, "end": v(660.4, 571.5) * mm});
            skLineSegment(sketch, "E2.17.15.0", {"start": v(685.8, 584.2) * mm, "end": v(685.8, 609.6) * mm});
            skLineSegment(sketch, "E2.17.15.1", {"start": v(660.4, 609.6) * mm, "end": v(685.8, 609.6) * mm});
            skLineSegment(sketch, "E2.17.15.2", {"start": v(660.4, 584.2) * mm, "end": v(685.8, 584.2) * mm});
            skLineSegment(sketch, "E2.17.15.3", {"start": v(660.4, 584.2) * mm, "end": v(660.4, 609.6) * mm});
            skLineSegment(sketch, "E2.17.16.0", {"start": v(685.8, 622.3) * mm, "end": v(685.8, 647.7) * mm});
            skLineSegment(sketch, "E2.17.16.1", {"start": v(660.4, 647.7) * mm, "end": v(685.8, 647.7) * mm});
            skLineSegment(sketch, "E2.17.16.2", {"start": v(660.4, 622.3) * mm, "end": v(685.8, 622.3) * mm});
            skLineSegment(sketch, "E2.17.16.3", {"start": v(660.4, 622.3) * mm, "end": v(660.4, 647.7) * mm});
            skLineSegment(sketch, "E2.17.17.0", {"start": v(685.8, 660.4) * mm, "end": v(685.8, 685.8) * mm});
            skLineSegment(sketch, "E2.17.17.1", {"start": v(660.4, 685.8) * mm, "end": v(685.8, 685.8) * mm});
            skLineSegment(sketch, "E2.17.17.2", {"start": v(660.4, 660.4) * mm, "end": v(685.8, 660.4) * mm});
            skLineSegment(sketch, "E2.17.17.3", {"start": v(660.4, 660.4) * mm, "end": v(660.4, 685.8) * mm});
            skLineSegment(sketch, "E2.17.18.0", {"start": v(685.8, 698.5) * mm, "end": v(685.8, 723.9) * mm});
            skLineSegment(sketch, "E2.17.18.1", {"start": v(660.4, 723.9) * mm, "end": v(685.8, 723.9) * mm});
            skLineSegment(sketch, "E2.17.18.2", {"start": v(660.4, 698.5) * mm, "end": v(685.8, 698.5) * mm});
            skLineSegment(sketch, "E2.17.18.3", {"start": v(660.4, 698.5) * mm, "end": v(660.4, 723.9) * mm});
            skLineSegment(sketch, "E2.17.19.0", {"start": v(685.8, 736.6) * mm, "end": v(685.8, 762) * mm});
            skLineSegment(sketch, "E2.17.19.1", {"start": v(660.4, 762) * mm, "end": v(685.8, 762) * mm});
            skLineSegment(sketch, "E2.17.19.2", {"start": v(660.4, 736.6) * mm, "end": v(685.8, 736.6) * mm});
            skLineSegment(sketch, "E2.17.19.3", {"start": v(660.4, 736.6) * mm, "end": v(660.4, 762) * mm});
            skLineSegment(sketch, "E2.18.0.0", {"start": v(723.9, 12.7) * mm, "end": v(723.9, 38.1) * mm});
            skLineSegment(sketch, "E2.18.0.1", {"start": v(698.5, 38.1) * mm, "end": v(723.9, 38.1) * mm});
            skLineSegment(sketch, "E2.18.0.2", {"start": v(698.5, 12.7) * mm, "end": v(723.9, 12.7) * mm});
            skLineSegment(sketch, "E2.18.0.3", {"start": v(698.5, 12.7) * mm, "end": v(698.5, 38.1) * mm});
            skLineSegment(sketch, "E2.18.1.0", {"start": v(723.9, 50.8) * mm, "end": v(723.9, 76.2) * mm});
            skLineSegment(sketch, "E2.18.1.1", {"start": v(698.5, 76.2) * mm, "end": v(723.9, 76.2) * mm});
            skLineSegment(sketch, "E2.18.1.2", {"start": v(698.5, 50.8) * mm, "end": v(723.9, 50.8) * mm});
            skLineSegment(sketch, "E2.18.1.3", {"start": v(698.5, 50.8) * mm, "end": v(698.5, 76.2) * mm});
            skLineSegment(sketch, "E2.18.2.0", {"start": v(723.9, 88.9) * mm, "end": v(723.9, 114.3) * mm});
            skLineSegment(sketch, "E2.18.2.1", {"start": v(698.5, 114.3) * mm, "end": v(723.9, 114.3) * mm});
            skLineSegment(sketch, "E2.18.2.2", {"start": v(698.5, 88.9) * mm, "end": v(723.9, 88.9) * mm});
            skLineSegment(sketch, "E2.18.2.3", {"start": v(698.5, 88.9) * mm, "end": v(698.5, 114.3) * mm});
            skLineSegment(sketch, "E2.18.3.0", {"start": v(723.9, 127) * mm, "end": v(723.9, 152.4) * mm});
            skLineSegment(sketch, "E2.18.3.1", {"start": v(698.5, 152.4) * mm, "end": v(723.9, 152.4) * mm});
            skLineSegment(sketch, "E2.18.3.2", {"start": v(698.5, 127) * mm, "end": v(723.9, 127) * mm});
            skLineSegment(sketch, "E2.18.3.3", {"start": v(698.5, 127) * mm, "end": v(698.5, 152.4) * mm});
            skLineSegment(sketch, "E2.18.4.0", {"start": v(723.9, 165.1) * mm, "end": v(723.9, 190.5) * mm});
            skLineSegment(sketch, "E2.18.4.1", {"start": v(698.5, 190.5) * mm, "end": v(723.9, 190.5) * mm});
            skLineSegment(sketch, "E2.18.4.2", {"start": v(698.5, 165.1) * mm, "end": v(723.9, 165.1) * mm});
            skLineSegment(sketch, "E2.18.4.3", {"start": v(698.5, 165.1) * mm, "end": v(698.5, 190.5) * mm});
            skLineSegment(sketch, "E2.18.5.0", {"start": v(723.9, 203.2) * mm, "end": v(723.9, 228.6) * mm});
            skLineSegment(sketch, "E2.18.5.1", {"start": v(698.5, 228.6) * mm, "end": v(723.9, 228.6) * mm});
            skLineSegment(sketch, "E2.18.5.2", {"start": v(698.5, 203.2) * mm, "end": v(723.9, 203.2) * mm});
            skLineSegment(sketch, "E2.18.5.3", {"start": v(698.5, 203.2) * mm, "end": v(698.5, 228.6) * mm});
            skLineSegment(sketch, "E2.18.6.0", {"start": v(723.9, 241.3) * mm, "end": v(723.9, 266.7) * mm});
            skLineSegment(sketch, "E2.18.6.1", {"start": v(698.5, 266.7) * mm, "end": v(723.9, 266.7) * mm});
            skLineSegment(sketch, "E2.18.6.2", {"start": v(698.5, 241.3) * mm, "end": v(723.9, 241.3) * mm});
            skLineSegment(sketch, "E2.18.6.3", {"start": v(698.5, 241.3) * mm, "end": v(698.5, 266.7) * mm});
            skLineSegment(sketch, "E2.18.7.0", {"start": v(723.9, 279.4) * mm, "end": v(723.9, 304.8) * mm});
            skLineSegment(sketch, "E2.18.7.1", {"start": v(698.5, 304.8) * mm, "end": v(723.9, 304.8) * mm});
            skLineSegment(sketch, "E2.18.7.2", {"start": v(698.5, 279.4) * mm, "end": v(723.9, 279.4) * mm});
            skLineSegment(sketch, "E2.18.7.3", {"start": v(698.5, 279.4) * mm, "end": v(698.5, 304.8) * mm});
            skLineSegment(sketch, "E2.18.8.0", {"start": v(723.9, 317.5) * mm, "end": v(723.9, 342.9) * mm});
            skLineSegment(sketch, "E2.18.8.1", {"start": v(698.5, 342.9) * mm, "end": v(723.9, 342.9) * mm});
            skLineSegment(sketch, "E2.18.8.2", {"start": v(698.5, 317.5) * mm, "end": v(723.9, 317.5) * mm});
            skLineSegment(sketch, "E2.18.8.3", {"start": v(698.5, 317.5) * mm, "end": v(698.5, 342.9) * mm});
            skLineSegment(sketch, "E2.18.9.0", {"start": v(723.9, 355.6) * mm, "end": v(723.9, 381) * mm});
            skLineSegment(sketch, "E2.18.9.1", {"start": v(698.5, 381) * mm, "end": v(723.9, 381) * mm});
            skLineSegment(sketch, "E2.18.9.2", {"start": v(698.5, 355.6) * mm, "end": v(723.9, 355.6) * mm});
            skLineSegment(sketch, "E2.18.9.3", {"start": v(698.5, 355.6) * mm, "end": v(698.5, 381) * mm});
            skLineSegment(sketch, "E2.18.10.0", {"start": v(723.9, 393.7) * mm, "end": v(723.9, 419.1) * mm});
            skLineSegment(sketch, "E2.18.10.1", {"start": v(698.5, 419.1) * mm, "end": v(723.9, 419.1) * mm});
            skLineSegment(sketch, "E2.18.10.2", {"start": v(698.5, 393.7) * mm, "end": v(723.9, 393.7) * mm});
            skLineSegment(sketch, "E2.18.10.3", {"start": v(698.5, 393.7) * mm, "end": v(698.5, 419.1) * mm});
            skLineSegment(sketch, "E2.18.11.0", {"start": v(723.9, 431.8) * mm, "end": v(723.9, 457.2) * mm});
            skLineSegment(sketch, "E2.18.11.1", {"start": v(698.5, 457.2) * mm, "end": v(723.9, 457.2) * mm});
            skLineSegment(sketch, "E2.18.11.2", {"start": v(698.5, 431.8) * mm, "end": v(723.9, 431.8) * mm});
            skLineSegment(sketch, "E2.18.11.3", {"start": v(698.5, 431.8) * mm, "end": v(698.5, 457.2) * mm});
            skLineSegment(sketch, "E2.18.12.0", {"start": v(723.9, 469.9) * mm, "end": v(723.9, 495.3) * mm});
            skLineSegment(sketch, "E2.18.12.1", {"start": v(698.5, 495.3) * mm, "end": v(723.9, 495.3) * mm});
            skLineSegment(sketch, "E2.18.12.2", {"start": v(698.5, 469.9) * mm, "end": v(723.9, 469.9) * mm});
            skLineSegment(sketch, "E2.18.12.3", {"start": v(698.5, 469.9) * mm, "end": v(698.5, 495.3) * mm});
            skLineSegment(sketch, "E2.18.13.0", {"start": v(723.9, 508) * mm, "end": v(723.9, 533.4) * mm});
            skLineSegment(sketch, "E2.18.13.1", {"start": v(698.5, 533.4) * mm, "end": v(723.9, 533.4) * mm});
            skLineSegment(sketch, "E2.18.13.2", {"start": v(698.5, 508) * mm, "end": v(723.9, 508) * mm});
            skLineSegment(sketch, "E2.18.13.3", {"start": v(698.5, 508) * mm, "end": v(698.5, 533.4) * mm});
            skLineSegment(sketch, "E2.18.14.0", {"start": v(723.9, 546.1) * mm, "end": v(723.9, 571.5) * mm});
            skLineSegment(sketch, "E2.18.14.1", {"start": v(698.5, 571.5) * mm, "end": v(723.9, 571.5) * mm});
            skLineSegment(sketch, "E2.18.14.2", {"start": v(698.5, 546.1) * mm, "end": v(723.9, 546.1) * mm});
            skLineSegment(sketch, "E2.18.14.3", {"start": v(698.5, 546.1) * mm, "end": v(698.5, 571.5) * mm});
            skLineSegment(sketch, "E2.18.15.0", {"start": v(723.9, 584.2) * mm, "end": v(723.9, 609.6) * mm});
            skLineSegment(sketch, "E2.18.15.1", {"start": v(698.5, 609.6) * mm, "end": v(723.9, 609.6) * mm});
            skLineSegment(sketch, "E2.18.15.2", {"start": v(698.5, 584.2) * mm, "end": v(723.9, 584.2) * mm});
            skLineSegment(sketch, "E2.18.15.3", {"start": v(698.5, 584.2) * mm, "end": v(698.5, 609.6) * mm});
            skLineSegment(sketch, "E2.18.16.0", {"start": v(723.9, 622.3) * mm, "end": v(723.9, 647.7) * mm});
            skLineSegment(sketch, "E2.18.16.1", {"start": v(698.5, 647.7) * mm, "end": v(723.9, 647.7) * mm});
            skLineSegment(sketch, "E2.18.16.2", {"start": v(698.5, 622.3) * mm, "end": v(723.9, 622.3) * mm});
            skLineSegment(sketch, "E2.18.16.3", {"start": v(698.5, 622.3) * mm, "end": v(698.5, 647.7) * mm});
            skLineSegment(sketch, "E2.18.17.0", {"start": v(723.9, 660.4) * mm, "end": v(723.9, 685.8) * mm});
            skLineSegment(sketch, "E2.18.17.1", {"start": v(698.5, 685.8) * mm, "end": v(723.9, 685.8) * mm});
            skLineSegment(sketch, "E2.18.17.2", {"start": v(698.5, 660.4) * mm, "end": v(723.9, 660.4) * mm});
            skLineSegment(sketch, "E2.18.17.3", {"start": v(698.5, 660.4) * mm, "end": v(698.5, 685.8) * mm});
            skLineSegment(sketch, "E2.18.18.0", {"start": v(723.9, 698.5) * mm, "end": v(723.9, 723.9) * mm});
            skLineSegment(sketch, "E2.18.18.1", {"start": v(698.5, 723.9) * mm, "end": v(723.9, 723.9) * mm});
            skLineSegment(sketch, "E2.18.18.2", {"start": v(698.5, 698.5) * mm, "end": v(723.9, 698.5) * mm});
            skLineSegment(sketch, "E2.18.18.3", {"start": v(698.5, 698.5) * mm, "end": v(698.5, 723.9) * mm});
            skLineSegment(sketch, "E2.18.19.0", {"start": v(723.9, 736.6) * mm, "end": v(723.9, 762) * mm});
            skLineSegment(sketch, "E2.18.19.1", {"start": v(698.5, 762) * mm, "end": v(723.9, 762) * mm});
            skLineSegment(sketch, "E2.18.19.2", {"start": v(698.5, 736.6) * mm, "end": v(723.9, 736.6) * mm});
            skLineSegment(sketch, "E2.18.19.3", {"start": v(698.5, 736.6) * mm, "end": v(698.5, 762) * mm});
            skLineSegment(sketch, "E2.19.0.0", {"start": v(762, 12.7) * mm, "end": v(762, 38.1) * mm});
            skLineSegment(sketch, "E2.19.0.1", {"start": v(736.6, 38.1) * mm, "end": v(762, 38.1) * mm});
            skLineSegment(sketch, "E2.19.0.2", {"start": v(736.6, 12.7) * mm, "end": v(762, 12.7) * mm});
            skLineSegment(sketch, "E2.19.0.3", {"start": v(736.6, 12.7) * mm, "end": v(736.6, 38.1) * mm});
            skLineSegment(sketch, "E2.19.1.0", {"start": v(762, 50.8) * mm, "end": v(762, 76.2) * mm});
            skLineSegment(sketch, "E2.19.1.1", {"start": v(736.6, 76.2) * mm, "end": v(762, 76.2) * mm});
            skLineSegment(sketch, "E2.19.1.2", {"start": v(736.6, 50.8) * mm, "end": v(762, 50.8) * mm});
            skLineSegment(sketch, "E2.19.1.3", {"start": v(736.6, 50.8) * mm, "end": v(736.6, 76.2) * mm});
            skLineSegment(sketch, "E2.19.2.0", {"start": v(762, 88.9) * mm, "end": v(762, 114.3) * mm});
            skLineSegment(sketch, "E2.19.2.1", {"start": v(736.6, 114.3) * mm, "end": v(762, 114.3) * mm});
            skLineSegment(sketch, "E2.19.2.2", {"start": v(736.6, 88.9) * mm, "end": v(762, 88.9) * mm});
            skLineSegment(sketch, "E2.19.2.3", {"start": v(736.6, 88.9) * mm, "end": v(736.6, 114.3) * mm});
            skLineSegment(sketch, "E2.19.3.0", {"start": v(762, 127) * mm, "end": v(762, 152.4) * mm});
            skLineSegment(sketch, "E2.19.3.1", {"start": v(736.6, 152.4) * mm, "end": v(762, 152.4) * mm});
            skLineSegment(sketch, "E2.19.3.2", {"start": v(736.6, 127) * mm, "end": v(762, 127) * mm});
            skLineSegment(sketch, "E2.19.3.3", {"start": v(736.6, 127) * mm, "end": v(736.6, 152.4) * mm});
            skLineSegment(sketch, "E2.19.4.0", {"start": v(762, 165.1) * mm, "end": v(762, 190.5) * mm});
            skLineSegment(sketch, "E2.19.4.1", {"start": v(736.6, 190.5) * mm, "end": v(762, 190.5) * mm});
            skLineSegment(sketch, "E2.19.4.2", {"start": v(736.6, 165.1) * mm, "end": v(762, 165.1) * mm});
            skLineSegment(sketch, "E2.19.4.3", {"start": v(736.6, 165.1) * mm, "end": v(736.6, 190.5) * mm});
            skLineSegment(sketch, "E2.19.5.0", {"start": v(762, 203.2) * mm, "end": v(762, 228.6) * mm});
            skLineSegment(sketch, "E2.19.5.1", {"start": v(736.6, 228.6) * mm, "end": v(762, 228.6) * mm});
            skLineSegment(sketch, "E2.19.5.2", {"start": v(736.6, 203.2) * mm, "end": v(762, 203.2) * mm});
            skLineSegment(sketch, "E2.19.5.3", {"start": v(736.6, 203.2) * mm, "end": v(736.6, 228.6) * mm});
            skLineSegment(sketch, "E2.19.6.0", {"start": v(762, 241.3) * mm, "end": v(762, 266.7) * mm});
            skLineSegment(sketch, "E2.19.6.1", {"start": v(736.6, 266.7) * mm, "end": v(762, 266.7) * mm});
            skLineSegment(sketch, "E2.19.6.2", {"start": v(736.6, 241.3) * mm, "end": v(762, 241.3) * mm});
            skLineSegment(sketch, "E2.19.6.3", {"start": v(736.6, 241.3) * mm, "end": v(736.6, 266.7) * mm});
            skLineSegment(sketch, "E2.19.7.0", {"start": v(762, 279.4) * mm, "end": v(762, 304.8) * mm});
            skLineSegment(sketch, "E2.19.7.1", {"start": v(736.6, 304.8) * mm, "end": v(762, 304.8) * mm});
            skLineSegment(sketch, "E2.19.7.2", {"start": v(736.6, 279.4) * mm, "end": v(762, 279.4) * mm});
            skLineSegment(sketch, "E2.19.7.3", {"start": v(736.6, 279.4) * mm, "end": v(736.6, 304.8) * mm});
            skLineSegment(sketch, "E2.19.8.0", {"start": v(762, 317.5) * mm, "end": v(762, 342.9) * mm});
            skLineSegment(sketch, "E2.19.8.1", {"start": v(736.6, 342.9) * mm, "end": v(762, 342.9) * mm});
            skLineSegment(sketch, "E2.19.8.2", {"start": v(736.6, 317.5) * mm, "end": v(762, 317.5) * mm});
            skLineSegment(sketch, "E2.19.8.3", {"start": v(736.6, 317.5) * mm, "end": v(736.6, 342.9) * mm});
            skLineSegment(sketch, "E2.19.9.0", {"start": v(762, 355.6) * mm, "end": v(762, 381) * mm});
            skLineSegment(sketch, "E2.19.9.1", {"start": v(736.6, 381) * mm, "end": v(762, 381) * mm});
            skLineSegment(sketch, "E2.19.9.2", {"start": v(736.6, 355.6) * mm, "end": v(762, 355.6) * mm});
            skLineSegment(sketch, "E2.19.9.3", {"start": v(736.6, 355.6) * mm, "end": v(736.6, 381) * mm});
            skLineSegment(sketch, "E2.19.10.0", {"start": v(762, 393.7) * mm, "end": v(762, 419.1) * mm});
            skLineSegment(sketch, "E2.19.10.1", {"start": v(736.6, 419.1) * mm, "end": v(762, 419.1) * mm});
            skLineSegment(sketch, "E2.19.10.2", {"start": v(736.6, 393.7) * mm, "end": v(762, 393.7) * mm});
            skLineSegment(sketch, "E2.19.10.3", {"start": v(736.6, 393.7) * mm, "end": v(736.6, 419.1) * mm});
            skLineSegment(sketch, "E2.19.11.0", {"start": v(762, 431.8) * mm, "end": v(762, 457.2) * mm});
            skLineSegment(sketch, "E2.19.11.1", {"start": v(736.6, 457.2) * mm, "end": v(762, 457.2) * mm});
            skLineSegment(sketch, "E2.19.11.2", {"start": v(736.6, 431.8) * mm, "end": v(762, 431.8) * mm});
            skLineSegment(sketch, "E2.19.11.3", {"start": v(736.6, 431.8) * mm, "end": v(736.6, 457.2) * mm});
            skLineSegment(sketch, "E2.19.12.0", {"start": v(762, 469.9) * mm, "end": v(762, 495.3) * mm});
            skLineSegment(sketch, "E2.19.12.1", {"start": v(736.6, 495.3) * mm, "end": v(762, 495.3) * mm});
            skLineSegment(sketch, "E2.19.12.2", {"start": v(736.6, 469.9) * mm, "end": v(762, 469.9) * mm});
            skLineSegment(sketch, "E2.19.12.3", {"start": v(736.6, 469.9) * mm, "end": v(736.6, 495.3) * mm});
            skLineSegment(sketch, "E2.19.13.0", {"start": v(762, 508) * mm, "end": v(762, 533.4) * mm});
            skLineSegment(sketch, "E2.19.13.1", {"start": v(736.6, 533.4) * mm, "end": v(762, 533.4) * mm});
            skLineSegment(sketch, "E2.19.13.2", {"start": v(736.6, 508) * mm, "end": v(762, 508) * mm});
            skLineSegment(sketch, "E2.19.13.3", {"start": v(736.6, 508) * mm, "end": v(736.6, 533.4) * mm});
            skLineSegment(sketch, "E2.19.14.0", {"start": v(762, 546.1) * mm, "end": v(762, 571.5) * mm});
            skLineSegment(sketch, "E2.19.14.1", {"start": v(736.6, 571.5) * mm, "end": v(762, 571.5) * mm});
            skLineSegment(sketch, "E2.19.14.2", {"start": v(736.6, 546.1) * mm, "end": v(762, 546.1) * mm});
            skLineSegment(sketch, "E2.19.14.3", {"start": v(736.6, 546.1) * mm, "end": v(736.6, 571.5) * mm});
            skLineSegment(sketch, "E2.19.15.0", {"start": v(762, 584.2) * mm, "end": v(762, 609.6) * mm});
            skLineSegment(sketch, "E2.19.15.1", {"start": v(736.6, 609.6) * mm, "end": v(762, 609.6) * mm});
            skLineSegment(sketch, "E2.19.15.2", {"start": v(736.6, 584.2) * mm, "end": v(762, 584.2) * mm});
            skLineSegment(sketch, "E2.19.15.3", {"start": v(736.6, 584.2) * mm, "end": v(736.6, 609.6) * mm});
            skLineSegment(sketch, "E2.19.16.0", {"start": v(762, 622.3) * mm, "end": v(762, 647.7) * mm});
            skLineSegment(sketch, "E2.19.16.1", {"start": v(736.6, 647.7) * mm, "end": v(762, 647.7) * mm});
            skLineSegment(sketch, "E2.19.16.2", {"start": v(736.6, 622.3) * mm, "end": v(762, 622.3) * mm});
            skLineSegment(sketch, "E2.19.16.3", {"start": v(736.6, 622.3) * mm, "end": v(736.6, 647.7) * mm});
            skLineSegment(sketch, "E2.19.17.0", {"start": v(762, 660.4) * mm, "end": v(762, 685.8) * mm});
            skLineSegment(sketch, "E2.19.17.1", {"start": v(736.6, 685.8) * mm, "end": v(762, 685.8) * mm});
            skLineSegment(sketch, "E2.19.17.2", {"start": v(736.6, 660.4) * mm, "end": v(762, 660.4) * mm});
            skLineSegment(sketch, "E2.19.17.3", {"start": v(736.6, 660.4) * mm, "end": v(736.6, 685.8) * mm});
            skLineSegment(sketch, "E2.19.18.0", {"start": v(762, 698.5) * mm, "end": v(762, 723.9) * mm});
            skLineSegment(sketch, "E2.19.18.1", {"start": v(736.6, 723.9) * mm, "end": v(762, 723.9) * mm});
            skLineSegment(sketch, "E2.19.18.2", {"start": v(736.6, 698.5) * mm, "end": v(762, 698.5) * mm});
            skLineSegment(sketch, "E2.19.18.3", {"start": v(736.6, 698.5) * mm, "end": v(736.6, 723.9) * mm});
            skLineSegment(sketch, "E2.19.19.0", {"start": v(762, 736.6) * mm, "end": v(762, 762) * mm});
            skLineSegment(sketch, "E2.19.19.1", {"start": v(736.6, 762) * mm, "end": v(762, 762) * mm});
            skLineSegment(sketch, "E2.19.19.2", {"start": v(736.6, 736.6) * mm, "end": v(762, 736.6) * mm});
            skLineSegment(sketch, "E2.19.19.3", {"start": v(736.6, 736.6) * mm, "end": v(736.6, 762) * mm});
            skLineSegment(sketch, "E2.direction1", {"start": v(12.7, 12.7) * mm, "end": v(50.8, 12.7) * mm, "construction": true});
            skLineSegment(sketch, "E2.direction2", {"start": v(12.7, 12.7) * mm, "end": v(12.7, 50.8) * mm, "construction": true});
            skLineSegment(sketch, "E3.0.20.0", {"start": v(800.1, 12.7) * mm, "end": v(800.1, 38.1) * mm});
            skLineSegment(sketch, "E3.3.20.0", {"start": v(774.7, 38.1) * mm, "end": v(800.1, 38.1) * mm});
            skLineSegment(sketch, "E3.6.20.0", {"start": v(774.7, 12.7) * mm, "end": v(800.1, 12.7) * mm});
            skLineSegment(sketch, "E3.9.20.0", {"start": v(774.7, 12.7) * mm, "end": v(774.7, 38.1) * mm});
            skLineSegment(sketch, "E3.0.20.1", {"start": v(800.1, 50.8) * mm, "end": v(800.1, 76.2) * mm});
            skLineSegment(sketch, "E3.3.20.1", {"start": v(774.7, 76.2) * mm, "end": v(800.1, 76.2) * mm});
            skLineSegment(sketch, "E3.6.20.1", {"start": v(774.7, 50.8) * mm, "end": v(800.1, 50.8) * mm});
            skLineSegment(sketch, "E3.9.20.1", {"start": v(774.7, 50.8) * mm, "end": v(774.7, 76.2) * mm});
            skLineSegment(sketch, "E3.0.20.2", {"start": v(800.1, 88.9) * mm, "end": v(800.1, 114.3) * mm});
            skLineSegment(sketch, "E3.3.20.2", {"start": v(774.7, 114.3) * mm, "end": v(800.1, 114.3) * mm});
            skLineSegment(sketch, "E3.6.20.2", {"start": v(774.7, 88.9) * mm, "end": v(800.1, 88.9) * mm});
            skLineSegment(sketch, "E3.9.20.2", {"start": v(774.7, 88.9) * mm, "end": v(774.7, 114.3) * mm});
            skLineSegment(sketch, "E3.0.20.3", {"start": v(800.1, 127) * mm, "end": v(800.1, 152.4) * mm});
            skLineSegment(sketch, "E3.3.20.3", {"start": v(774.7, 152.4) * mm, "end": v(800.1, 152.4) * mm});
            skLineSegment(sketch, "E3.6.20.3", {"start": v(774.7, 127) * mm, "end": v(800.1, 127) * mm});
            skLineSegment(sketch, "E3.9.20.3", {"start": v(774.7, 127) * mm, "end": v(774.7, 152.4) * mm});
            skLineSegment(sketch, "E3.0.20.4", {"start": v(800.1, 165.1) * mm, "end": v(800.1, 190.5) * mm});
            skLineSegment(sketch, "E3.3.20.4", {"start": v(774.7, 190.5) * mm, "end": v(800.1, 190.5) * mm});
            skLineSegment(sketch, "E3.6.20.4", {"start": v(774.7, 165.1) * mm, "end": v(800.1, 165.1) * mm});
            skLineSegment(sketch, "E3.9.20.4", {"start": v(774.7, 165.1) * mm, "end": v(774.7, 190.5) * mm});
            skLineSegment(sketch, "E3.0.20.5", {"start": v(800.1, 203.2) * mm, "end": v(800.1, 228.6) * mm});
            skLineSegment(sketch, "E3.3.20.5", {"start": v(774.7, 228.6) * mm, "end": v(800.1, 228.6) * mm});
            skLineSegment(sketch, "E3.6.20.5", {"start": v(774.7, 203.2) * mm, "end": v(800.1, 203.2) * mm});
            skLineSegment(sketch, "E3.9.20.5", {"start": v(774.7, 203.2) * mm, "end": v(774.7, 228.6) * mm});
            skLineSegment(sketch, "E3.0.20.6", {"start": v(800.1, 241.3) * mm, "end": v(800.1, 266.7) * mm});
            skLineSegment(sketch, "E3.3.20.6", {"start": v(774.7, 266.7) * mm, "end": v(800.1, 266.7) * mm});
            skLineSegment(sketch, "E3.6.20.6", {"start": v(774.7, 241.3) * mm, "end": v(800.1, 241.3) * mm});
            skLineSegment(sketch, "E3.9.20.6", {"start": v(774.7, 241.3) * mm, "end": v(774.7, 266.7) * mm});
            skLineSegment(sketch, "E3.0.20.7", {"start": v(800.1, 279.4) * mm, "end": v(800.1, 304.8) * mm});
            skLineSegment(sketch, "E3.3.20.7", {"start": v(774.7, 304.8) * mm, "end": v(800.1, 304.8) * mm});
            skLineSegment(sketch, "E3.6.20.7", {"start": v(774.7, 279.4) * mm, "end": v(800.1, 279.4) * mm});
            skLineSegment(sketch, "E3.9.20.7", {"start": v(774.7, 279.4) * mm, "end": v(774.7, 304.8) * mm});
            skLineSegment(sketch, "E3.0.20.8", {"start": v(800.1, 317.5) * mm, "end": v(800.1, 342.9) * mm});
            skLineSegment(sketch, "E3.3.20.8", {"start": v(774.7, 342.9) * mm, "end": v(800.1, 342.9) * mm});
            skLineSegment(sketch, "E3.6.20.8", {"start": v(774.7, 317.5) * mm, "end": v(800.1, 317.5) * mm});
            skLineSegment(sketch, "E3.9.20.8", {"start": v(774.7, 317.5) * mm, "end": v(774.7, 342.9) * mm});
            skLineSegment(sketch, "E3.0.20.9", {"start": v(800.1, 355.6) * mm, "end": v(800.1, 381) * mm});
            skLineSegment(sketch, "E3.3.20.9", {"start": v(774.7, 381) * mm, "end": v(800.1, 381) * mm});
            skLineSegment(sketch, "E3.6.20.9", {"start": v(774.7, 355.6) * mm, "end": v(800.1, 355.6) * mm});
            skLineSegment(sketch, "E3.9.20.9", {"start": v(774.7, 355.6) * mm, "end": v(774.7, 381) * mm});
            skLineSegment(sketch, "E3.0.20.10", {"start": v(800.1, 393.7) * mm, "end": v(800.1, 419.1) * mm});
            skLineSegment(sketch, "E3.3.20.10", {"start": v(774.7, 419.1) * mm, "end": v(800.1, 419.1) * mm});
            skLineSegment(sketch, "E3.6.20.10", {"start": v(774.7, 393.7) * mm, "end": v(800.1, 393.7) * mm});
            skLineSegment(sketch, "E3.9.20.10", {"start": v(774.7, 393.7) * mm, "end": v(774.7, 419.1) * mm});
            skLineSegment(sketch, "E3.0.20.11", {"start": v(800.1, 431.8) * mm, "end": v(800.1, 457.2) * mm});
            skLineSegment(sketch, "E3.3.20.11", {"start": v(774.7, 457.2) * mm, "end": v(800.1, 457.2) * mm});
            skLineSegment(sketch, "E3.6.20.11", {"start": v(774.7, 431.8) * mm, "end": v(800.1, 431.8) * mm});
            skLineSegment(sketch, "E3.9.20.11", {"start": v(774.7, 431.8) * mm, "end": v(774.7, 457.2) * mm});
            skLineSegment(sketch, "E3.0.20.12", {"start": v(800.1, 469.9) * mm, "end": v(800.1, 495.3) * mm});
            skLineSegment(sketch, "E3.3.20.12", {"start": v(774.7, 495.3) * mm, "end": v(800.1, 495.3) * mm});
            skLineSegment(sketch, "E3.6.20.12", {"start": v(774.7, 469.9) * mm, "end": v(800.1, 469.9) * mm});
            skLineSegment(sketch, "E3.9.20.12", {"start": v(774.7, 469.9) * mm, "end": v(774.7, 495.3) * mm});
            skLineSegment(sketch, "E3.0.20.13", {"start": v(800.1, 508) * mm, "end": v(800.1, 533.4) * mm});
            skLineSegment(sketch, "E3.3.20.13", {"start": v(774.7, 533.4) * mm, "end": v(800.1, 533.4) * mm});
            skLineSegment(sketch, "E3.6.20.13", {"start": v(774.7, 508) * mm, "end": v(800.1, 508) * mm});
            skLineSegment(sketch, "E3.9.20.13", {"start": v(774.7, 508) * mm, "end": v(774.7, 533.4) * mm});
            skLineSegment(sketch, "E3.0.20.14", {"start": v(800.1, 546.1) * mm, "end": v(800.1, 571.5) * mm});
            skLineSegment(sketch, "E3.3.20.14", {"start": v(774.7, 571.5) * mm, "end": v(800.1, 571.5) * mm});
            skLineSegment(sketch, "E3.6.20.14", {"start": v(774.7, 546.1) * mm, "end": v(800.1, 546.1) * mm});
            skLineSegment(sketch, "E3.9.20.14", {"start": v(774.7, 546.1) * mm, "end": v(774.7, 571.5) * mm});
            skLineSegment(sketch, "E3.0.20.15", {"start": v(800.1, 584.2) * mm, "end": v(800.1, 609.6) * mm});
            skLineSegment(sketch, "E3.3.20.15", {"start": v(774.7, 609.6) * mm, "end": v(800.1, 609.6) * mm});
            skLineSegment(sketch, "E3.6.20.15", {"start": v(774.7, 584.2) * mm, "end": v(800.1, 584.2) * mm});
            skLineSegment(sketch, "E3.9.20.15", {"start": v(774.7, 584.2) * mm, "end": v(774.7, 609.6) * mm});
            skLineSegment(sketch, "E3.0.20.16", {"start": v(800.1, 622.3) * mm, "end": v(800.1, 647.7) * mm});
            skLineSegment(sketch, "E3.3.20.16", {"start": v(774.7, 647.7) * mm, "end": v(800.1, 647.7) * mm});
            skLineSegment(sketch, "E3.6.20.16", {"start": v(774.7, 622.3) * mm, "end": v(800.1, 622.3) * mm});
            skLineSegment(sketch, "E3.9.20.16", {"start": v(774.7, 622.3) * mm, "end": v(774.7, 647.7) * mm});
            skLineSegment(sketch, "E3.0.20.17", {"start": v(800.1, 660.4) * mm, "end": v(800.1, 685.8) * mm});
            skLineSegment(sketch, "E3.3.20.17", {"start": v(774.7, 685.8) * mm, "end": v(800.1, 685.8) * mm});
            skLineSegment(sketch, "E3.6.20.17", {"start": v(774.7, 660.4) * mm, "end": v(800.1, 660.4) * mm});
            skLineSegment(sketch, "E3.9.20.17", {"start": v(774.7, 660.4) * mm, "end": v(774.7, 685.8) * mm});
            skLineSegment(sketch, "E3.0.20.18", {"start": v(800.1, 698.5) * mm, "end": v(800.1, 723.9) * mm});
            skLineSegment(sketch, "E3.3.20.18", {"start": v(774.7, 723.9) * mm, "end": v(800.1, 723.9) * mm});
            skLineSegment(sketch, "E3.6.20.18", {"start": v(774.7, 698.5) * mm, "end": v(800.1, 698.5) * mm});
            skLineSegment(sketch, "E3.9.20.18", {"start": v(774.7, 698.5) * mm, "end": v(774.7, 723.9) * mm});
            skLineSegment(sketch, "E3.0.20.19", {"start": v(800.1, 736.6) * mm, "end": v(800.1, 762) * mm});
            skLineSegment(sketch, "E3.3.20.19", {"start": v(774.7, 762) * mm, "end": v(800.1, 762) * mm});
            skLineSegment(sketch, "E3.6.20.19", {"start": v(774.7, 736.6) * mm, "end": v(800.1, 736.6) * mm});
            skLineSegment(sketch, "E3.9.20.19", {"start": v(774.7, 736.6) * mm, "end": v(774.7, 762) * mm});
            skLineSegment(sketch, "E3.0.21.0", {"start": v(838.2, 12.7) * mm, "end": v(838.2, 38.1) * mm});
            skLineSegment(sketch, "E3.3.21.0", {"start": v(812.8, 38.1) * mm, "end": v(838.2, 38.1) * mm});
            skLineSegment(sketch, "E3.6.21.0", {"start": v(812.8, 12.7) * mm, "end": v(838.2, 12.7) * mm});
            skLineSegment(sketch, "E3.9.21.0", {"start": v(812.8, 12.7) * mm, "end": v(812.8, 38.1) * mm});
            skLineSegment(sketch, "E3.0.21.1", {"start": v(838.2, 50.8) * mm, "end": v(838.2, 76.2) * mm});
            skLineSegment(sketch, "E3.3.21.1", {"start": v(812.8, 76.2) * mm, "end": v(838.2, 76.2) * mm});
            skLineSegment(sketch, "E3.6.21.1", {"start": v(812.8, 50.8) * mm, "end": v(838.2, 50.8) * mm});
            skLineSegment(sketch, "E3.9.21.1", {"start": v(812.8, 50.8) * mm, "end": v(812.8, 76.2) * mm});
            skLineSegment(sketch, "E3.0.21.2", {"start": v(838.2, 88.9) * mm, "end": v(838.2, 114.3) * mm});
            skLineSegment(sketch, "E3.3.21.2", {"start": v(812.8, 114.3) * mm, "end": v(838.2, 114.3) * mm});
            skLineSegment(sketch, "E3.6.21.2", {"start": v(812.8, 88.9) * mm, "end": v(838.2, 88.9) * mm});
            skLineSegment(sketch, "E3.9.21.2", {"start": v(812.8, 88.9) * mm, "end": v(812.8, 114.3) * mm});
            skLineSegment(sketch, "E3.0.21.3", {"start": v(838.2, 127) * mm, "end": v(838.2, 152.4) * mm});
            skLineSegment(sketch, "E3.3.21.3", {"start": v(812.8, 152.4) * mm, "end": v(838.2, 152.4) * mm});
            skLineSegment(sketch, "E3.6.21.3", {"start": v(812.8, 127) * mm, "end": v(838.2, 127) * mm});
            skLineSegment(sketch, "E3.9.21.3", {"start": v(812.8, 127) * mm, "end": v(812.8, 152.4) * mm});
            skLineSegment(sketch, "E3.0.21.4", {"start": v(838.2, 165.1) * mm, "end": v(838.2, 190.5) * mm});
            skLineSegment(sketch, "E3.3.21.4", {"start": v(812.8, 190.5) * mm, "end": v(838.2, 190.5) * mm});
            skLineSegment(sketch, "E3.6.21.4", {"start": v(812.8, 165.1) * mm, "end": v(838.2, 165.1) * mm});
            skLineSegment(sketch, "E3.9.21.4", {"start": v(812.8, 165.1) * mm, "end": v(812.8, 190.5) * mm});
            skLineSegment(sketch, "E3.0.21.5", {"start": v(838.2, 203.2) * mm, "end": v(838.2, 228.6) * mm});
            skLineSegment(sketch, "E3.3.21.5", {"start": v(812.8, 228.6) * mm, "end": v(838.2, 228.6) * mm});
            skLineSegment(sketch, "E3.6.21.5", {"start": v(812.8, 203.2) * mm, "end": v(838.2, 203.2) * mm});
            skLineSegment(sketch, "E3.9.21.5", {"start": v(812.8, 203.2) * mm, "end": v(812.8, 228.6) * mm});
            skLineSegment(sketch, "E3.0.21.6", {"start": v(838.2, 241.3) * mm, "end": v(838.2, 266.7) * mm});
            skLineSegment(sketch, "E3.3.21.6", {"start": v(812.8, 266.7) * mm, "end": v(838.2, 266.7) * mm});
            skLineSegment(sketch, "E3.6.21.6", {"start": v(812.8, 241.3) * mm, "end": v(838.2, 241.3) * mm});
            skLineSegment(sketch, "E3.9.21.6", {"start": v(812.8, 241.3) * mm, "end": v(812.8, 266.7) * mm});
            skLineSegment(sketch, "E3.0.21.7", {"start": v(838.2, 279.4) * mm, "end": v(838.2, 304.8) * mm});
            skLineSegment(sketch, "E3.3.21.7", {"start": v(812.8, 304.8) * mm, "end": v(838.2, 304.8) * mm});
            skLineSegment(sketch, "E3.6.21.7", {"start": v(812.8, 279.4) * mm, "end": v(838.2, 279.4) * mm});
            skLineSegment(sketch, "E3.9.21.7", {"start": v(812.8, 279.4) * mm, "end": v(812.8, 304.8) * mm});
            skLineSegment(sketch, "E3.0.21.8", {"start": v(838.2, 317.5) * mm, "end": v(838.2, 342.9) * mm});
            skLineSegment(sketch, "E3.3.21.8", {"start": v(812.8, 342.9) * mm, "end": v(838.2, 342.9) * mm});
            skLineSegment(sketch, "E3.6.21.8", {"start": v(812.8, 317.5) * mm, "end": v(838.2, 317.5) * mm});
            skLineSegment(sketch, "E3.9.21.8", {"start": v(812.8, 317.5) * mm, "end": v(812.8, 342.9) * mm});
            skLineSegment(sketch, "E3.0.21.9", {"start": v(838.2, 355.6) * mm, "end": v(838.2, 381) * mm});
            skLineSegment(sketch, "E3.3.21.9", {"start": v(812.8, 381) * mm, "end": v(838.2, 381) * mm});
            skLineSegment(sketch, "E3.6.21.9", {"start": v(812.8, 355.6) * mm, "end": v(838.2, 355.6) * mm});
            skLineSegment(sketch, "E3.9.21.9", {"start": v(812.8, 355.6) * mm, "end": v(812.8, 381) * mm});
            skLineSegment(sketch, "E3.0.21.10", {"start": v(838.2, 393.7) * mm, "end": v(838.2, 419.1) * mm});
            skLineSegment(sketch, "E3.3.21.10", {"start": v(812.8, 419.1) * mm, "end": v(838.2, 419.1) * mm});
            skLineSegment(sketch, "E3.6.21.10", {"start": v(812.8, 393.7) * mm, "end": v(838.2, 393.7) * mm});
            skLineSegment(sketch, "E3.9.21.10", {"start": v(812.8, 393.7) * mm, "end": v(812.8, 419.1) * mm});
            skLineSegment(sketch, "E3.0.21.11", {"start": v(838.2, 431.8) * mm, "end": v(838.2, 457.2) * mm});
            skLineSegment(sketch, "E3.3.21.11", {"start": v(812.8, 457.2) * mm, "end": v(838.2, 457.2) * mm});
            skLineSegment(sketch, "E3.6.21.11", {"start": v(812.8, 431.8) * mm, "end": v(838.2, 431.8) * mm});
            skLineSegment(sketch, "E3.9.21.11", {"start": v(812.8, 431.8) * mm, "end": v(812.8, 457.2) * mm});
            skLineSegment(sketch, "E3.0.21.12", {"start": v(838.2, 469.9) * mm, "end": v(838.2, 495.3) * mm});
            skLineSegment(sketch, "E3.3.21.12", {"start": v(812.8, 495.3) * mm, "end": v(838.2, 495.3) * mm});
            skLineSegment(sketch, "E3.6.21.12", {"start": v(812.8, 469.9) * mm, "end": v(838.2, 469.9) * mm});
            skLineSegment(sketch, "E3.9.21.12", {"start": v(812.8, 469.9) * mm, "end": v(812.8, 495.3) * mm});
            skLineSegment(sketch, "E3.0.21.13", {"start": v(838.2, 508) * mm, "end": v(838.2, 533.4) * mm});
            skLineSegment(sketch, "E3.3.21.13", {"start": v(812.8, 533.4) * mm, "end": v(838.2, 533.4) * mm});
            skLineSegment(sketch, "E3.6.21.13", {"start": v(812.8, 508) * mm, "end": v(838.2, 508) * mm});
            skLineSegment(sketch, "E3.9.21.13", {"start": v(812.8, 508) * mm, "end": v(812.8, 533.4) * mm});
            skLineSegment(sketch, "E3.0.21.14", {"start": v(838.2, 546.1) * mm, "end": v(838.2, 571.5) * mm});
            skLineSegment(sketch, "E3.3.21.14", {"start": v(812.8, 571.5) * mm, "end": v(838.2, 571.5) * mm});
            skLineSegment(sketch, "E3.6.21.14", {"start": v(812.8, 546.1) * mm, "end": v(838.2, 546.1) * mm});
            skLineSegment(sketch, "E3.9.21.14", {"start": v(812.8, 546.1) * mm, "end": v(812.8, 571.5) * mm});
            skLineSegment(sketch, "E3.0.21.15", {"start": v(838.2, 584.2) * mm, "end": v(838.2, 609.6) * mm});
            skLineSegment(sketch, "E3.3.21.15", {"start": v(812.8, 609.6) * mm, "end": v(838.2, 609.6) * mm});
            skLineSegment(sketch, "E3.6.21.15", {"start": v(812.8, 584.2) * mm, "end": v(838.2, 584.2) * mm});
            skLineSegment(sketch, "E3.9.21.15", {"start": v(812.8, 584.2) * mm, "end": v(812.8, 609.6) * mm});
            skLineSegment(sketch, "E3.0.21.16", {"start": v(838.2, 622.3) * mm, "end": v(838.2, 647.7) * mm});
            skLineSegment(sketch, "E3.3.21.16", {"start": v(812.8, 647.7) * mm, "end": v(838.2, 647.7) * mm});
            skLineSegment(sketch, "E3.6.21.16", {"start": v(812.8, 622.3) * mm, "end": v(838.2, 622.3) * mm});
            skLineSegment(sketch, "E3.9.21.16", {"start": v(812.8, 622.3) * mm, "end": v(812.8, 647.7) * mm});
            skLineSegment(sketch, "E3.0.21.17", {"start": v(838.2, 660.4) * mm, "end": v(838.2, 685.8) * mm});
            skLineSegment(sketch, "E3.3.21.17", {"start": v(812.8, 685.8) * mm, "end": v(838.2, 685.8) * mm});
            skLineSegment(sketch, "E3.6.21.17", {"start": v(812.8, 660.4) * mm, "end": v(838.2, 660.4) * mm});
            skLineSegment(sketch, "E3.9.21.17", {"start": v(812.8, 660.4) * mm, "end": v(812.8, 685.8) * mm});
            skLineSegment(sketch, "E3.0.21.18", {"start": v(838.2, 698.5) * mm, "end": v(838.2, 723.9) * mm});
            skLineSegment(sketch, "E3.3.21.18", {"start": v(812.8, 723.9) * mm, "end": v(838.2, 723.9) * mm});
            skLineSegment(sketch, "E3.6.21.18", {"start": v(812.8, 698.5) * mm, "end": v(838.2, 698.5) * mm});
            skLineSegment(sketch, "E3.9.21.18", {"start": v(812.8, 698.5) * mm, "end": v(812.8, 723.9) * mm});
            skLineSegment(sketch, "E3.0.21.19", {"start": v(838.2, 736.6) * mm, "end": v(838.2, 762) * mm});
            skLineSegment(sketch, "E3.3.21.19", {"start": v(812.8, 762) * mm, "end": v(838.2, 762) * mm});
            skLineSegment(sketch, "E3.6.21.19", {"start": v(812.8, 736.6) * mm, "end": v(838.2, 736.6) * mm});
            skLineSegment(sketch, "E3.9.21.19", {"start": v(812.8, 736.6) * mm, "end": v(812.8, 762) * mm});
            skLineSegment(sketch, "E3.0.22.0", {"start": v(876.3, 12.7) * mm, "end": v(876.3, 38.1) * mm});
            skLineSegment(sketch, "E3.3.22.0", {"start": v(850.9, 38.1) * mm, "end": v(876.3, 38.1) * mm});
            skLineSegment(sketch, "E3.6.22.0", {"start": v(850.9, 12.7) * mm, "end": v(876.3, 12.7) * mm});
            skLineSegment(sketch, "E3.9.22.0", {"start": v(850.9, 12.7) * mm, "end": v(850.9, 38.1) * mm});
            skLineSegment(sketch, "E3.0.22.1", {"start": v(876.3, 50.8) * mm, "end": v(876.3, 76.2) * mm});
            skLineSegment(sketch, "E3.3.22.1", {"start": v(850.9, 76.2) * mm, "end": v(876.3, 76.2) * mm});
            skLineSegment(sketch, "E3.6.22.1", {"start": v(850.9, 50.8) * mm, "end": v(876.3, 50.8) * mm});
            skLineSegment(sketch, "E3.9.22.1", {"start": v(850.9, 50.8) * mm, "end": v(850.9, 76.2) * mm});
            skLineSegment(sketch, "E3.0.22.2", {"start": v(876.3, 88.9) * mm, "end": v(876.3, 114.3) * mm});
            skLineSegment(sketch, "E3.3.22.2", {"start": v(850.9, 114.3) * mm, "end": v(876.3, 114.3) * mm});
            skLineSegment(sketch, "E3.6.22.2", {"start": v(850.9, 88.9) * mm, "end": v(876.3, 88.9) * mm});
            skLineSegment(sketch, "E3.9.22.2", {"start": v(850.9, 88.9) * mm, "end": v(850.9, 114.3) * mm});
            skLineSegment(sketch, "E3.0.22.3", {"start": v(876.3, 127) * mm, "end": v(876.3, 152.4) * mm});
            skLineSegment(sketch, "E3.3.22.3", {"start": v(850.9, 152.4) * mm, "end": v(876.3, 152.4) * mm});
            skLineSegment(sketch, "E3.6.22.3", {"start": v(850.9, 127) * mm, "end": v(876.3, 127) * mm});
            skLineSegment(sketch, "E3.9.22.3", {"start": v(850.9, 127) * mm, "end": v(850.9, 152.4) * mm});
            skLineSegment(sketch, "E3.0.22.4", {"start": v(876.3, 165.1) * mm, "end": v(876.3, 190.5) * mm});
            skLineSegment(sketch, "E3.3.22.4", {"start": v(850.9, 190.5) * mm, "end": v(876.3, 190.5) * mm});
            skLineSegment(sketch, "E3.6.22.4", {"start": v(850.9, 165.1) * mm, "end": v(876.3, 165.1) * mm});
            skLineSegment(sketch, "E3.9.22.4", {"start": v(850.9, 165.1) * mm, "end": v(850.9, 190.5) * mm});
            skLineSegment(sketch, "E3.0.22.5", {"start": v(876.3, 203.2) * mm, "end": v(876.3, 228.6) * mm});
            skLineSegment(sketch, "E3.3.22.5", {"start": v(850.9, 228.6) * mm, "end": v(876.3, 228.6) * mm});
            skLineSegment(sketch, "E3.6.22.5", {"start": v(850.9, 203.2) * mm, "end": v(876.3, 203.2) * mm});
            skLineSegment(sketch, "E3.9.22.5", {"start": v(850.9, 203.2) * mm, "end": v(850.9, 228.6) * mm});
            skLineSegment(sketch, "E3.0.22.6", {"start": v(876.3, 241.3) * mm, "end": v(876.3, 266.7) * mm});
            skLineSegment(sketch, "E3.3.22.6", {"start": v(850.9, 266.7) * mm, "end": v(876.3, 266.7) * mm});
            skLineSegment(sketch, "E3.6.22.6", {"start": v(850.9, 241.3) * mm, "end": v(876.3, 241.3) * mm});
            skLineSegment(sketch, "E3.9.22.6", {"start": v(850.9, 241.3) * mm, "end": v(850.9, 266.7) * mm});
            skLineSegment(sketch, "E3.0.22.7", {"start": v(876.3, 279.4) * mm, "end": v(876.3, 304.8) * mm});
            skLineSegment(sketch, "E3.3.22.7", {"start": v(850.9, 304.8) * mm, "end": v(876.3, 304.8) * mm});
            skLineSegment(sketch, "E3.6.22.7", {"start": v(850.9, 279.4) * mm, "end": v(876.3, 279.4) * mm});
            skLineSegment(sketch, "E3.9.22.7", {"start": v(850.9, 279.4) * mm, "end": v(850.9, 304.8) * mm});
            skLineSegment(sketch, "E3.0.22.8", {"start": v(876.3, 317.5) * mm, "end": v(876.3, 342.9) * mm});
            skLineSegment(sketch, "E3.3.22.8", {"start": v(850.9, 342.9) * mm, "end": v(876.3, 342.9) * mm});
            skLineSegment(sketch, "E3.6.22.8", {"start": v(850.9, 317.5) * mm, "end": v(876.3, 317.5) * mm});
            skLineSegment(sketch, "E3.9.22.8", {"start": v(850.9, 317.5) * mm, "end": v(850.9, 342.9) * mm});
            skLineSegment(sketch, "E3.0.22.9", {"start": v(876.3, 355.6) * mm, "end": v(876.3, 381) * mm});
            skLineSegment(sketch, "E3.3.22.9", {"start": v(850.9, 381) * mm, "end": v(876.3, 381) * mm});
            skLineSegment(sketch, "E3.6.22.9", {"start": v(850.9, 355.6) * mm, "end": v(876.3, 355.6) * mm});
            skLineSegment(sketch, "E3.9.22.9", {"start": v(850.9, 355.6) * mm, "end": v(850.9, 381) * mm});
            skLineSegment(sketch, "E3.0.22.10", {"start": v(876.3, 393.7) * mm, "end": v(876.3, 419.1) * mm});
            skLineSegment(sketch, "E3.3.22.10", {"start": v(850.9, 419.1) * mm, "end": v(876.3, 419.1) * mm});
            skLineSegment(sketch, "E3.6.22.10", {"start": v(850.9, 393.7) * mm, "end": v(876.3, 393.7) * mm});
            skLineSegment(sketch, "E3.9.22.10", {"start": v(850.9, 393.7) * mm, "end": v(850.9, 419.1) * mm});
            skLineSegment(sketch, "E3.0.22.11", {"start": v(876.3, 431.8) * mm, "end": v(876.3, 457.2) * mm});
            skLineSegment(sketch, "E3.3.22.11", {"start": v(850.9, 457.2) * mm, "end": v(876.3, 457.2) * mm});
            skLineSegment(sketch, "E3.6.22.11", {"start": v(850.9, 431.8) * mm, "end": v(876.3, 431.8) * mm});
            skLineSegment(sketch, "E3.9.22.11", {"start": v(850.9, 431.8) * mm, "end": v(850.9, 457.2) * mm});
            skLineSegment(sketch, "E3.0.22.12", {"start": v(876.3, 469.9) * mm, "end": v(876.3, 495.3) * mm});
            skLineSegment(sketch, "E3.3.22.12", {"start": v(850.9, 495.3) * mm, "end": v(876.3, 495.3) * mm});
            skLineSegment(sketch, "E3.6.22.12", {"start": v(850.9, 469.9) * mm, "end": v(876.3, 469.9) * mm});
            skLineSegment(sketch, "E3.9.22.12", {"start": v(850.9, 469.9) * mm, "end": v(850.9, 495.3) * mm});
            skLineSegment(sketch, "E3.0.22.13", {"start": v(876.3, 508) * mm, "end": v(876.3, 533.4) * mm});
            skLineSegment(sketch, "E3.3.22.13", {"start": v(850.9, 533.4) * mm, "end": v(876.3, 533.4) * mm});
            skLineSegment(sketch, "E3.6.22.13", {"start": v(850.9, 508) * mm, "end": v(876.3, 508) * mm});
            skLineSegment(sketch, "E3.9.22.13", {"start": v(850.9, 508) * mm, "end": v(850.9, 533.4) * mm});
            skLineSegment(sketch, "E3.0.22.14", {"start": v(876.3, 546.1) * mm, "end": v(876.3, 571.5) * mm});
            skLineSegment(sketch, "E3.3.22.14", {"start": v(850.9, 571.5) * mm, "end": v(876.3, 571.5) * mm});
            skLineSegment(sketch, "E3.6.22.14", {"start": v(850.9, 546.1) * mm, "end": v(876.3, 546.1) * mm});
            skLineSegment(sketch, "E3.9.22.14", {"start": v(850.9, 546.1) * mm, "end": v(850.9, 571.5) * mm});
            skLineSegment(sketch, "E3.0.22.15", {"start": v(876.3, 584.2) * mm, "end": v(876.3, 609.6) * mm});
            skLineSegment(sketch, "E3.3.22.15", {"start": v(850.9, 609.6) * mm, "end": v(876.3, 609.6) * mm});
            skLineSegment(sketch, "E3.6.22.15", {"start": v(850.9, 584.2) * mm, "end": v(876.3, 584.2) * mm});
            skLineSegment(sketch, "E3.9.22.15", {"start": v(850.9, 584.2) * mm, "end": v(850.9, 609.6) * mm});
            skLineSegment(sketch, "E3.0.22.16", {"start": v(876.3, 622.3) * mm, "end": v(876.3, 647.7) * mm});
            skLineSegment(sketch, "E3.3.22.16", {"start": v(850.9, 647.7) * mm, "end": v(876.3, 647.7) * mm});
            skLineSegment(sketch, "E3.6.22.16", {"start": v(850.9, 622.3) * mm, "end": v(876.3, 622.3) * mm});
            skLineSegment(sketch, "E3.9.22.16", {"start": v(850.9, 622.3) * mm, "end": v(850.9, 647.7) * mm});
            skLineSegment(sketch, "E3.0.22.17", {"start": v(876.3, 660.4) * mm, "end": v(876.3, 685.8) * mm});
            skLineSegment(sketch, "E3.3.22.17", {"start": v(850.9, 685.8) * mm, "end": v(876.3, 685.8) * mm});
            skLineSegment(sketch, "E3.6.22.17", {"start": v(850.9, 660.4) * mm, "end": v(876.3, 660.4) * mm});
            skLineSegment(sketch, "E3.9.22.17", {"start": v(850.9, 660.4) * mm, "end": v(850.9, 685.8) * mm});
            skLineSegment(sketch, "E3.0.22.18", {"start": v(876.3, 698.5) * mm, "end": v(876.3, 723.9) * mm});
            skLineSegment(sketch, "E3.3.22.18", {"start": v(850.9, 723.9) * mm, "end": v(876.3, 723.9) * mm});
            skLineSegment(sketch, "E3.6.22.18", {"start": v(850.9, 698.5) * mm, "end": v(876.3, 698.5) * mm});
            skLineSegment(sketch, "E3.9.22.18", {"start": v(850.9, 698.5) * mm, "end": v(850.9, 723.9) * mm});
            skLineSegment(sketch, "E3.0.22.19", {"start": v(876.3, 736.6) * mm, "end": v(876.3, 762) * mm});
            skLineSegment(sketch, "E3.3.22.19", {"start": v(850.9, 762) * mm, "end": v(876.3, 762) * mm});
            skLineSegment(sketch, "E3.6.22.19", {"start": v(850.9, 736.6) * mm, "end": v(876.3, 736.6) * mm});
            skLineSegment(sketch, "E3.9.22.19", {"start": v(850.9, 736.6) * mm, "end": v(850.9, 762) * mm});
            skLineSegment(sketch, "E3.0.23.0", {"start": v(914.4, 12.7) * mm, "end": v(914.4, 38.1) * mm});
            skLineSegment(sketch, "E3.3.23.0", {"start": v(889, 38.1) * mm, "end": v(914.4, 38.1) * mm});
            skLineSegment(sketch, "E3.6.23.0", {"start": v(889, 12.7) * mm, "end": v(914.4, 12.7) * mm});
            skLineSegment(sketch, "E3.9.23.0", {"start": v(889, 12.7) * mm, "end": v(889, 38.1) * mm});
            skLineSegment(sketch, "E3.0.23.1", {"start": v(914.4, 50.8) * mm, "end": v(914.4, 76.2) * mm});
            skLineSegment(sketch, "E3.3.23.1", {"start": v(889, 76.2) * mm, "end": v(914.4, 76.2) * mm});
            skLineSegment(sketch, "E3.6.23.1", {"start": v(889, 50.8) * mm, "end": v(914.4, 50.8) * mm});
            skLineSegment(sketch, "E3.9.23.1", {"start": v(889, 50.8) * mm, "end": v(889, 76.2) * mm});
            skLineSegment(sketch, "E3.0.23.2", {"start": v(914.4, 88.9) * mm, "end": v(914.4, 114.3) * mm});
            skLineSegment(sketch, "E3.3.23.2", {"start": v(889, 114.3) * mm, "end": v(914.4, 114.3) * mm});
            skLineSegment(sketch, "E3.6.23.2", {"start": v(889, 88.9) * mm, "end": v(914.4, 88.9) * mm});
            skLineSegment(sketch, "E3.9.23.2", {"start": v(889, 88.9) * mm, "end": v(889, 114.3) * mm});
            skLineSegment(sketch, "E3.0.23.3", {"start": v(914.4, 127) * mm, "end": v(914.4, 152.4) * mm});
            skLineSegment(sketch, "E3.3.23.3", {"start": v(889, 152.4) * mm, "end": v(914.4, 152.4) * mm});
            skLineSegment(sketch, "E3.6.23.3", {"start": v(889, 127) * mm, "end": v(914.4, 127) * mm});
            skLineSegment(sketch, "E3.9.23.3", {"start": v(889, 127) * mm, "end": v(889, 152.4) * mm});
            skLineSegment(sketch, "E3.0.23.4", {"start": v(914.4, 165.1) * mm, "end": v(914.4, 190.5) * mm});
            skLineSegment(sketch, "E3.3.23.4", {"start": v(889, 190.5) * mm, "end": v(914.4, 190.5) * mm});
            skLineSegment(sketch, "E3.6.23.4", {"start": v(889, 165.1) * mm, "end": v(914.4, 165.1) * mm});
            skLineSegment(sketch, "E3.9.23.4", {"start": v(889, 165.1) * mm, "end": v(889, 190.5) * mm});
            skLineSegment(sketch, "E3.0.23.5", {"start": v(914.4, 203.2) * mm, "end": v(914.4, 228.6) * mm});
            skLineSegment(sketch, "E3.3.23.5", {"start": v(889, 228.6) * mm, "end": v(914.4, 228.6) * mm});
            skLineSegment(sketch, "E3.6.23.5", {"start": v(889, 203.2) * mm, "end": v(914.4, 203.2) * mm});
            skLineSegment(sketch, "E3.9.23.5", {"start": v(889, 203.2) * mm, "end": v(889, 228.6) * mm});
            skLineSegment(sketch, "E3.0.23.6", {"start": v(914.4, 241.3) * mm, "end": v(914.4, 266.7) * mm});
            skLineSegment(sketch, "E3.3.23.6", {"start": v(889, 266.7) * mm, "end": v(914.4, 266.7) * mm});
            skLineSegment(sketch, "E3.6.23.6", {"start": v(889, 241.3) * mm, "end": v(914.4, 241.3) * mm});
            skLineSegment(sketch, "E3.9.23.6", {"start": v(889, 241.3) * mm, "end": v(889, 266.7) * mm});
            skLineSegment(sketch, "E3.0.23.7", {"start": v(914.4, 279.4) * mm, "end": v(914.4, 304.8) * mm});
            skLineSegment(sketch, "E3.3.23.7", {"start": v(889, 304.8) * mm, "end": v(914.4, 304.8) * mm});
            skLineSegment(sketch, "E3.6.23.7", {"start": v(889, 279.4) * mm, "end": v(914.4, 279.4) * mm});
            skLineSegment(sketch, "E3.9.23.7", {"start": v(889, 279.4) * mm, "end": v(889, 304.8) * mm});
            skLineSegment(sketch, "E3.0.23.8", {"start": v(914.4, 317.5) * mm, "end": v(914.4, 342.9) * mm});
            skLineSegment(sketch, "E3.3.23.8", {"start": v(889, 342.9) * mm, "end": v(914.4, 342.9) * mm});
            skLineSegment(sketch, "E3.6.23.8", {"start": v(889, 317.5) * mm, "end": v(914.4, 317.5) * mm});
            skLineSegment(sketch, "E3.9.23.8", {"start": v(889, 317.5) * mm, "end": v(889, 342.9) * mm});
            skLineSegment(sketch, "E3.0.23.9", {"start": v(914.4, 355.6) * mm, "end": v(914.4, 381) * mm});
            skLineSegment(sketch, "E3.3.23.9", {"start": v(889, 381) * mm, "end": v(914.4, 381) * mm});
            skLineSegment(sketch, "E3.6.23.9", {"start": v(889, 355.6) * mm, "end": v(914.4, 355.6) * mm});
            skLineSegment(sketch, "E3.9.23.9", {"start": v(889, 355.6) * mm, "end": v(889, 381) * mm});
            skLineSegment(sketch, "E3.0.23.10", {"start": v(914.4, 393.7) * mm, "end": v(914.4, 419.1) * mm});
            skLineSegment(sketch, "E3.3.23.10", {"start": v(889, 419.1) * mm, "end": v(914.4, 419.1) * mm});
            skLineSegment(sketch, "E3.6.23.10", {"start": v(889, 393.7) * mm, "end": v(914.4, 393.7) * mm});
            skLineSegment(sketch, "E3.9.23.10", {"start": v(889, 393.7) * mm, "end": v(889, 419.1) * mm});
            skLineSegment(sketch, "E3.0.23.11", {"start": v(914.4, 431.8) * mm, "end": v(914.4, 457.2) * mm});
            skLineSegment(sketch, "E3.3.23.11", {"start": v(889, 457.2) * mm, "end": v(914.4, 457.2) * mm});
            skLineSegment(sketch, "E3.6.23.11", {"start": v(889, 431.8) * mm, "end": v(914.4, 431.8) * mm});
            skLineSegment(sketch, "E3.9.23.11", {"start": v(889, 431.8) * mm, "end": v(889, 457.2) * mm});
            skLineSegment(sketch, "E3.0.23.12", {"start": v(914.4, 469.9) * mm, "end": v(914.4, 495.3) * mm});
            skLineSegment(sketch, "E3.3.23.12", {"start": v(889, 495.3) * mm, "end": v(914.4, 495.3) * mm});
            skLineSegment(sketch, "E3.6.23.12", {"start": v(889, 469.9) * mm, "end": v(914.4, 469.9) * mm});
            skLineSegment(sketch, "E3.9.23.12", {"start": v(889, 469.9) * mm, "end": v(889, 495.3) * mm});
            skLineSegment(sketch, "E3.0.23.13", {"start": v(914.4, 508) * mm, "end": v(914.4, 533.4) * mm});
            skLineSegment(sketch, "E3.3.23.13", {"start": v(889, 533.4) * mm, "end": v(914.4, 533.4) * mm});
            skLineSegment(sketch, "E3.6.23.13", {"start": v(889, 508) * mm, "end": v(914.4, 508) * mm});
            skLineSegment(sketch, "E3.9.23.13", {"start": v(889, 508) * mm, "end": v(889, 533.4) * mm});
            skLineSegment(sketch, "E3.0.23.14", {"start": v(914.4, 546.1) * mm, "end": v(914.4, 571.5) * mm});
            skLineSegment(sketch, "E3.3.23.14", {"start": v(889, 571.5) * mm, "end": v(914.4, 571.5) * mm});
            skLineSegment(sketch, "E3.6.23.14", {"start": v(889, 546.1) * mm, "end": v(914.4, 546.1) * mm});
            skLineSegment(sketch, "E3.9.23.14", {"start": v(889, 546.1) * mm, "end": v(889, 571.5) * mm});
            skLineSegment(sketch, "E3.0.23.15", {"start": v(914.4, 584.2) * mm, "end": v(914.4, 609.6) * mm});
            skLineSegment(sketch, "E3.3.23.15", {"start": v(889, 609.6) * mm, "end": v(914.4, 609.6) * mm});
            skLineSegment(sketch, "E3.6.23.15", {"start": v(889, 584.2) * mm, "end": v(914.4, 584.2) * mm});
            skLineSegment(sketch, "E3.9.23.15", {"start": v(889, 584.2) * mm, "end": v(889, 609.6) * mm});
            skLineSegment(sketch, "E3.0.23.16", {"start": v(914.4, 622.3) * mm, "end": v(914.4, 647.7) * mm});
            skLineSegment(sketch, "E3.3.23.16", {"start": v(889, 647.7) * mm, "end": v(914.4, 647.7) * mm});
            skLineSegment(sketch, "E3.6.23.16", {"start": v(889, 622.3) * mm, "end": v(914.4, 622.3) * mm});
            skLineSegment(sketch, "E3.9.23.16", {"start": v(889, 622.3) * mm, "end": v(889, 647.7) * mm});
            skLineSegment(sketch, "E3.0.23.17", {"start": v(914.4, 660.4) * mm, "end": v(914.4, 685.8) * mm});
            skLineSegment(sketch, "E3.3.23.17", {"start": v(889, 685.8) * mm, "end": v(914.4, 685.8) * mm});
            skLineSegment(sketch, "E3.6.23.17", {"start": v(889, 660.4) * mm, "end": v(914.4, 660.4) * mm});
            skLineSegment(sketch, "E3.9.23.17", {"start": v(889, 660.4) * mm, "end": v(889, 685.8) * mm});
            skLineSegment(sketch, "E3.0.23.18", {"start": v(914.4, 698.5) * mm, "end": v(914.4, 723.9) * mm});
            skLineSegment(sketch, "E3.3.23.18", {"start": v(889, 723.9) * mm, "end": v(914.4, 723.9) * mm});
            skLineSegment(sketch, "E3.6.23.18", {"start": v(889, 698.5) * mm, "end": v(914.4, 698.5) * mm});
            skLineSegment(sketch, "E3.9.23.18", {"start": v(889, 698.5) * mm, "end": v(889, 723.9) * mm});
            skLineSegment(sketch, "E3.0.23.19", {"start": v(914.4, 736.6) * mm, "end": v(914.4, 762) * mm});
            skLineSegment(sketch, "E3.3.23.19", {"start": v(889, 762) * mm, "end": v(914.4, 762) * mm});
            skLineSegment(sketch, "E3.6.23.19", {"start": v(889, 736.6) * mm, "end": v(914.4, 736.6) * mm});
            skLineSegment(sketch, "E3.9.23.19", {"start": v(889, 736.6) * mm, "end": v(889, 762) * mm});
            skLineSegment(sketch, "E3.0.24.0", {"start": v(952.5, 12.7) * mm, "end": v(952.5, 38.1) * mm});
            skLineSegment(sketch, "E3.3.24.0", {"start": v(927.1, 38.1) * mm, "end": v(952.5, 38.1) * mm});
            skLineSegment(sketch, "E3.6.24.0", {"start": v(927.1, 12.7) * mm, "end": v(952.5, 12.7) * mm});
            skLineSegment(sketch, "E3.9.24.0", {"start": v(927.1, 12.7) * mm, "end": v(927.1, 38.1) * mm});
            skLineSegment(sketch, "E3.0.24.1", {"start": v(952.5, 50.8) * mm, "end": v(952.5, 76.2) * mm});
            skLineSegment(sketch, "E3.3.24.1", {"start": v(927.1, 76.2) * mm, "end": v(952.5, 76.2) * mm});
            skLineSegment(sketch, "E3.6.24.1", {"start": v(927.1, 50.8) * mm, "end": v(952.5, 50.8) * mm});
            skLineSegment(sketch, "E3.9.24.1", {"start": v(927.1, 50.8) * mm, "end": v(927.1, 76.2) * mm});
            skLineSegment(sketch, "E3.0.24.2", {"start": v(952.5, 88.9) * mm, "end": v(952.5, 114.3) * mm});
            skLineSegment(sketch, "E3.3.24.2", {"start": v(927.1, 114.3) * mm, "end": v(952.5, 114.3) * mm});
            skLineSegment(sketch, "E3.6.24.2", {"start": v(927.1, 88.9) * mm, "end": v(952.5, 88.9) * mm});
            skLineSegment(sketch, "E3.9.24.2", {"start": v(927.1, 88.9) * mm, "end": v(927.1, 114.3) * mm});
            skLineSegment(sketch, "E3.0.24.3", {"start": v(952.5, 127) * mm, "end": v(952.5, 152.4) * mm});
            skLineSegment(sketch, "E3.3.24.3", {"start": v(927.1, 152.4) * mm, "end": v(952.5, 152.4) * mm});
            skLineSegment(sketch, "E3.6.24.3", {"start": v(927.1, 127) * mm, "end": v(952.5, 127) * mm});
            skLineSegment(sketch, "E3.9.24.3", {"start": v(927.1, 127) * mm, "end": v(927.1, 152.4) * mm});
            skLineSegment(sketch, "E3.0.24.4", {"start": v(952.5, 165.1) * mm, "end": v(952.5, 190.5) * mm});
            skLineSegment(sketch, "E3.3.24.4", {"start": v(927.1, 190.5) * mm, "end": v(952.5, 190.5) * mm});
            skLineSegment(sketch, "E3.6.24.4", {"start": v(927.1, 165.1) * mm, "end": v(952.5, 165.1) * mm});
            skLineSegment(sketch, "E3.9.24.4", {"start": v(927.1, 165.1) * mm, "end": v(927.1, 190.5) * mm});
            skLineSegment(sketch, "E3.0.24.5", {"start": v(952.5, 203.2) * mm, "end": v(952.5, 228.6) * mm});
            skLineSegment(sketch, "E3.3.24.5", {"start": v(927.1, 228.6) * mm, "end": v(952.5, 228.6) * mm});
            skLineSegment(sketch, "E3.6.24.5", {"start": v(927.1, 203.2) * mm, "end": v(952.5, 203.2) * mm});
            skLineSegment(sketch, "E3.9.24.5", {"start": v(927.1, 203.2) * mm, "end": v(927.1, 228.6) * mm});
            skLineSegment(sketch, "E3.0.24.6", {"start": v(952.5, 241.3) * mm, "end": v(952.5, 266.7) * mm});
            skLineSegment(sketch, "E3.3.24.6", {"start": v(927.1, 266.7) * mm, "end": v(952.5, 266.7) * mm});
            skLineSegment(sketch, "E3.6.24.6", {"start": v(927.1, 241.3) * mm, "end": v(952.5, 241.3) * mm});
            skLineSegment(sketch, "E3.9.24.6", {"start": v(927.1, 241.3) * mm, "end": v(927.1, 266.7) * mm});
            skLineSegment(sketch, "E3.0.24.7", {"start": v(952.5, 279.4) * mm, "end": v(952.5, 304.8) * mm});
            skLineSegment(sketch, "E3.3.24.7", {"start": v(927.1, 304.8) * mm, "end": v(952.5, 304.8) * mm});
            skLineSegment(sketch, "E3.6.24.7", {"start": v(927.1, 279.4) * mm, "end": v(952.5, 279.4) * mm});
            skLineSegment(sketch, "E3.9.24.7", {"start": v(927.1, 279.4) * mm, "end": v(927.1, 304.8) * mm});
            skLineSegment(sketch, "E3.0.24.8", {"start": v(952.5, 317.5) * mm, "end": v(952.5, 342.9) * mm});
            skLineSegment(sketch, "E3.3.24.8", {"start": v(927.1, 342.9) * mm, "end": v(952.5, 342.9) * mm});
            skLineSegment(sketch, "E3.6.24.8", {"start": v(927.1, 317.5) * mm, "end": v(952.5, 317.5) * mm});
            skLineSegment(sketch, "E3.9.24.8", {"start": v(927.1, 317.5) * mm, "end": v(927.1, 342.9) * mm});
            skLineSegment(sketch, "E3.0.24.9", {"start": v(952.5, 355.6) * mm, "end": v(952.5, 381) * mm});
            skLineSegment(sketch, "E3.3.24.9", {"start": v(927.1, 381) * mm, "end": v(952.5, 381) * mm});
            skLineSegment(sketch, "E3.6.24.9", {"start": v(927.1, 355.6) * mm, "end": v(952.5, 355.6) * mm});
            skLineSegment(sketch, "E3.9.24.9", {"start": v(927.1, 355.6) * mm, "end": v(927.1, 381) * mm});
            skLineSegment(sketch, "E3.0.24.10", {"start": v(952.5, 393.7) * mm, "end": v(952.5, 419.1) * mm});
            skLineSegment(sketch, "E3.3.24.10", {"start": v(927.1, 419.1) * mm, "end": v(952.5, 419.1) * mm});
            skLineSegment(sketch, "E3.6.24.10", {"start": v(927.1, 393.7) * mm, "end": v(952.5, 393.7) * mm});
            skLineSegment(sketch, "E3.9.24.10", {"start": v(927.1, 393.7) * mm, "end": v(927.1, 419.1) * mm});
            skLineSegment(sketch, "E3.0.24.11", {"start": v(952.5, 431.8) * mm, "end": v(952.5, 457.2) * mm});
            skLineSegment(sketch, "E3.3.24.11", {"start": v(927.1, 457.2) * mm, "end": v(952.5, 457.2) * mm});
            skLineSegment(sketch, "E3.6.24.11", {"start": v(927.1, 431.8) * mm, "end": v(952.5, 431.8) * mm});
            skLineSegment(sketch, "E3.9.24.11", {"start": v(927.1, 431.8) * mm, "end": v(927.1, 457.2) * mm});
            skLineSegment(sketch, "E3.0.24.12", {"start": v(952.5, 469.9) * mm, "end": v(952.5, 495.3) * mm});
            skLineSegment(sketch, "E3.3.24.12", {"start": v(927.1, 495.3) * mm, "end": v(952.5, 495.3) * mm});
            skLineSegment(sketch, "E3.6.24.12", {"start": v(927.1, 469.9) * mm, "end": v(952.5, 469.9) * mm});
            skLineSegment(sketch, "E3.9.24.12", {"start": v(927.1, 469.9) * mm, "end": v(927.1, 495.3) * mm});
            skLineSegment(sketch, "E3.0.24.13", {"start": v(952.5, 508) * mm, "end": v(952.5, 533.4) * mm});
            skLineSegment(sketch, "E3.3.24.13", {"start": v(927.1, 533.4) * mm, "end": v(952.5, 533.4) * mm});
            skLineSegment(sketch, "E3.6.24.13", {"start": v(927.1, 508) * mm, "end": v(952.5, 508) * mm});
            skLineSegment(sketch, "E3.9.24.13", {"start": v(927.1, 508) * mm, "end": v(927.1, 533.4) * mm});
            skLineSegment(sketch, "E3.0.24.14", {"start": v(952.5, 546.1) * mm, "end": v(952.5, 571.5) * mm});
            skLineSegment(sketch, "E3.3.24.14", {"start": v(927.1, 571.5) * mm, "end": v(952.5, 571.5) * mm});
            skLineSegment(sketch, "E3.6.24.14", {"start": v(927.1, 546.1) * mm, "end": v(952.5, 546.1) * mm});
            skLineSegment(sketch, "E3.9.24.14", {"start": v(927.1, 546.1) * mm, "end": v(927.1, 571.5) * mm});
            skLineSegment(sketch, "E3.0.24.15", {"start": v(952.5, 584.2) * mm, "end": v(952.5, 609.6) * mm});
            skLineSegment(sketch, "E3.3.24.15", {"start": v(927.1, 609.6) * mm, "end": v(952.5, 609.6) * mm});
            skLineSegment(sketch, "E3.6.24.15", {"start": v(927.1, 584.2) * mm, "end": v(952.5, 584.2) * mm});
            skLineSegment(sketch, "E3.9.24.15", {"start": v(927.1, 584.2) * mm, "end": v(927.1, 609.6) * mm});
            skLineSegment(sketch, "E3.0.24.16", {"start": v(952.5, 622.3) * mm, "end": v(952.5, 647.7) * mm});
            skLineSegment(sketch, "E3.3.24.16", {"start": v(927.1, 647.7) * mm, "end": v(952.5, 647.7) * mm});
            skLineSegment(sketch, "E3.6.24.16", {"start": v(927.1, 622.3) * mm, "end": v(952.5, 622.3) * mm});
            skLineSegment(sketch, "E3.9.24.16", {"start": v(927.1, 622.3) * mm, "end": v(927.1, 647.7) * mm});
            skLineSegment(sketch, "E3.0.24.17", {"start": v(952.5, 660.4) * mm, "end": v(952.5, 685.8) * mm});
            skLineSegment(sketch, "E3.3.24.17", {"start": v(927.1, 685.8) * mm, "end": v(952.5, 685.8) * mm});
            skLineSegment(sketch, "E3.6.24.17", {"start": v(927.1, 660.4) * mm, "end": v(952.5, 660.4) * mm});
            skLineSegment(sketch, "E3.9.24.17", {"start": v(927.1, 660.4) * mm, "end": v(927.1, 685.8) * mm});
            skLineSegment(sketch, "E3.0.24.18", {"start": v(952.5, 698.5) * mm, "end": v(952.5, 723.9) * mm});
            skLineSegment(sketch, "E3.3.24.18", {"start": v(927.1, 723.9) * mm, "end": v(952.5, 723.9) * mm});
            skLineSegment(sketch, "E3.6.24.18", {"start": v(927.1, 698.5) * mm, "end": v(952.5, 698.5) * mm});
            skLineSegment(sketch, "E3.9.24.18", {"start": v(927.1, 698.5) * mm, "end": v(927.1, 723.9) * mm});
            skLineSegment(sketch, "E3.0.24.19", {"start": v(952.5, 736.6) * mm, "end": v(952.5, 762) * mm});
            skLineSegment(sketch, "E3.3.24.19", {"start": v(927.1, 762) * mm, "end": v(952.5, 762) * mm});
            skLineSegment(sketch, "E3.6.24.19", {"start": v(927.1, 736.6) * mm, "end": v(952.5, 736.6) * mm});
            skLineSegment(sketch, "E3.9.24.19", {"start": v(927.1, 736.6) * mm, "end": v(927.1, 762) * mm});
            skLineSegment(sketch, "E3.0.25.0", {"start": v(990.6, 12.7) * mm, "end": v(990.6, 38.1) * mm});
            skLineSegment(sketch, "E3.3.25.0", {"start": v(965.2, 38.1) * mm, "end": v(990.6, 38.1) * mm});
            skLineSegment(sketch, "E3.6.25.0", {"start": v(965.2, 12.7) * mm, "end": v(990.6, 12.7) * mm});
            skLineSegment(sketch, "E3.9.25.0", {"start": v(965.2, 12.7) * mm, "end": v(965.2, 38.1) * mm});
            skLineSegment(sketch, "E3.0.25.1", {"start": v(990.6, 50.8) * mm, "end": v(990.6, 76.2) * mm});
            skLineSegment(sketch, "E3.3.25.1", {"start": v(965.2, 76.2) * mm, "end": v(990.6, 76.2) * mm});
            skLineSegment(sketch, "E3.6.25.1", {"start": v(965.2, 50.8) * mm, "end": v(990.6, 50.8) * mm});
            skLineSegment(sketch, "E3.9.25.1", {"start": v(965.2, 50.8) * mm, "end": v(965.2, 76.2) * mm});
            skLineSegment(sketch, "E3.0.25.2", {"start": v(990.6, 88.9) * mm, "end": v(990.6, 114.3) * mm});
            skLineSegment(sketch, "E3.3.25.2", {"start": v(965.2, 114.3) * mm, "end": v(990.6, 114.3) * mm});
            skLineSegment(sketch, "E3.6.25.2", {"start": v(965.2, 88.9) * mm, "end": v(990.6, 88.9) * mm});
            skLineSegment(sketch, "E3.9.25.2", {"start": v(965.2, 88.9) * mm, "end": v(965.2, 114.3) * mm});
            skLineSegment(sketch, "E3.0.25.3", {"start": v(990.6, 127) * mm, "end": v(990.6, 152.4) * mm});
            skLineSegment(sketch, "E3.3.25.3", {"start": v(965.2, 152.4) * mm, "end": v(990.6, 152.4) * mm});
            skLineSegment(sketch, "E3.6.25.3", {"start": v(965.2, 127) * mm, "end": v(990.6, 127) * mm});
            skLineSegment(sketch, "E3.9.25.3", {"start": v(965.2, 127) * mm, "end": v(965.2, 152.4) * mm});
            skLineSegment(sketch, "E3.0.25.4", {"start": v(990.6, 165.1) * mm, "end": v(990.6, 190.5) * mm});
            skLineSegment(sketch, "E3.3.25.4", {"start": v(965.2, 190.5) * mm, "end": v(990.6, 190.5) * mm});
            skLineSegment(sketch, "E3.6.25.4", {"start": v(965.2, 165.1) * mm, "end": v(990.6, 165.1) * mm});
            skLineSegment(sketch, "E3.9.25.4", {"start": v(965.2, 165.1) * mm, "end": v(965.2, 190.5) * mm});
            skLineSegment(sketch, "E3.0.25.5", {"start": v(990.6, 203.2) * mm, "end": v(990.6, 228.6) * mm});
            skLineSegment(sketch, "E3.3.25.5", {"start": v(965.2, 228.6) * mm, "end": v(990.6, 228.6) * mm});
            skLineSegment(sketch, "E3.6.25.5", {"start": v(965.2, 203.2) * mm, "end": v(990.6, 203.2) * mm});
            skLineSegment(sketch, "E3.9.25.5", {"start": v(965.2, 203.2) * mm, "end": v(965.2, 228.6) * mm});
            skLineSegment(sketch, "E3.0.25.6", {"start": v(990.6, 241.3) * mm, "end": v(990.6, 266.7) * mm});
            skLineSegment(sketch, "E3.3.25.6", {"start": v(965.2, 266.7) * mm, "end": v(990.6, 266.7) * mm});
            skLineSegment(sketch, "E3.6.25.6", {"start": v(965.2, 241.3) * mm, "end": v(990.6, 241.3) * mm});
            skLineSegment(sketch, "E3.9.25.6", {"start": v(965.2, 241.3) * mm, "end": v(965.2, 266.7) * mm});
            skLineSegment(sketch, "E3.0.25.7", {"start": v(990.6, 279.4) * mm, "end": v(990.6, 304.8) * mm});
            skLineSegment(sketch, "E3.3.25.7", {"start": v(965.2, 304.8) * mm, "end": v(990.6, 304.8) * mm});
            skLineSegment(sketch, "E3.6.25.7", {"start": v(965.2, 279.4) * mm, "end": v(990.6, 279.4) * mm});
            skLineSegment(sketch, "E3.9.25.7", {"start": v(965.2, 279.4) * mm, "end": v(965.2, 304.8) * mm});
            skLineSegment(sketch, "E3.0.25.8", {"start": v(990.6, 317.5) * mm, "end": v(990.6, 342.9) * mm});
            skLineSegment(sketch, "E3.3.25.8", {"start": v(965.2, 342.9) * mm, "end": v(990.6, 342.9) * mm});
            skLineSegment(sketch, "E3.6.25.8", {"start": v(965.2, 317.5) * mm, "end": v(990.6, 317.5) * mm});
            skLineSegment(sketch, "E3.9.25.8", {"start": v(965.2, 317.5) * mm, "end": v(965.2, 342.9) * mm});
            skLineSegment(sketch, "E3.0.25.9", {"start": v(990.6, 355.6) * mm, "end": v(990.6, 381) * mm});
            skLineSegment(sketch, "E3.3.25.9", {"start": v(965.2, 381) * mm, "end": v(990.6, 381) * mm});
            skLineSegment(sketch, "E3.6.25.9", {"start": v(965.2, 355.6) * mm, "end": v(990.6, 355.6) * mm});
            skLineSegment(sketch, "E3.9.25.9", {"start": v(965.2, 355.6) * mm, "end": v(965.2, 381) * mm});
            skLineSegment(sketch, "E3.0.25.10", {"start": v(990.6, 393.7) * mm, "end": v(990.6, 419.1) * mm});
            skLineSegment(sketch, "E3.3.25.10", {"start": v(965.2, 419.1) * mm, "end": v(990.6, 419.1) * mm});
            skLineSegment(sketch, "E3.6.25.10", {"start": v(965.2, 393.7) * mm, "end": v(990.6, 393.7) * mm});
            skLineSegment(sketch, "E3.9.25.10", {"start": v(965.2, 393.7) * mm, "end": v(965.2, 419.1) * mm});
            skLineSegment(sketch, "E3.0.25.11", {"start": v(990.6, 431.8) * mm, "end": v(990.6, 457.2) * mm});
            skLineSegment(sketch, "E3.3.25.11", {"start": v(965.2, 457.2) * mm, "end": v(990.6, 457.2) * mm});
            skLineSegment(sketch, "E3.6.25.11", {"start": v(965.2, 431.8) * mm, "end": v(990.6, 431.8) * mm});
            skLineSegment(sketch, "E3.9.25.11", {"start": v(965.2, 431.8) * mm, "end": v(965.2, 457.2) * mm});
            skLineSegment(sketch, "E3.0.25.12", {"start": v(990.6, 469.9) * mm, "end": v(990.6, 495.3) * mm});
            skLineSegment(sketch, "E3.3.25.12", {"start": v(965.2, 495.3) * mm, "end": v(990.6, 495.3) * mm});
            skLineSegment(sketch, "E3.6.25.12", {"start": v(965.2, 469.9) * mm, "end": v(990.6, 469.9) * mm});
            skLineSegment(sketch, "E3.9.25.12", {"start": v(965.2, 469.9) * mm, "end": v(965.2, 495.3) * mm});
            skLineSegment(sketch, "E3.0.25.13", {"start": v(990.6, 508) * mm, "end": v(990.6, 533.4) * mm});
            skLineSegment(sketch, "E3.3.25.13", {"start": v(965.2, 533.4) * mm, "end": v(990.6, 533.4) * mm});
            skLineSegment(sketch, "E3.6.25.13", {"start": v(965.2, 508) * mm, "end": v(990.6, 508) * mm});
            skLineSegment(sketch, "E3.9.25.13", {"start": v(965.2, 508) * mm, "end": v(965.2, 533.4) * mm});
            skLineSegment(sketch, "E3.0.25.14", {"start": v(990.6, 546.1) * mm, "end": v(990.6, 571.5) * mm});
            skLineSegment(sketch, "E3.3.25.14", {"start": v(965.2, 571.5) * mm, "end": v(990.6, 571.5) * mm});
            skLineSegment(sketch, "E3.6.25.14", {"start": v(965.2, 546.1) * mm, "end": v(990.6, 546.1) * mm});
            skLineSegment(sketch, "E3.9.25.14", {"start": v(965.2, 546.1) * mm, "end": v(965.2, 571.5) * mm});
            skLineSegment(sketch, "E3.0.25.15", {"start": v(990.6, 584.2) * mm, "end": v(990.6, 609.6) * mm});
            skLineSegment(sketch, "E3.3.25.15", {"start": v(965.2, 609.6) * mm, "end": v(990.6, 609.6) * mm});
            skLineSegment(sketch, "E3.6.25.15", {"start": v(965.2, 584.2) * mm, "end": v(990.6, 584.2) * mm});
            skLineSegment(sketch, "E3.9.25.15", {"start": v(965.2, 584.2) * mm, "end": v(965.2, 609.6) * mm});
            skLineSegment(sketch, "E3.0.25.16", {"start": v(990.6, 622.3) * mm, "end": v(990.6, 647.7) * mm});
            skLineSegment(sketch, "E3.3.25.16", {"start": v(965.2, 647.7) * mm, "end": v(990.6, 647.7) * mm});
            skLineSegment(sketch, "E3.6.25.16", {"start": v(965.2, 622.3) * mm, "end": v(990.6, 622.3) * mm});
            skLineSegment(sketch, "E3.9.25.16", {"start": v(965.2, 622.3) * mm, "end": v(965.2, 647.7) * mm});
            skLineSegment(sketch, "E3.0.25.17", {"start": v(990.6, 660.4) * mm, "end": v(990.6, 685.8) * mm});
            skLineSegment(sketch, "E3.3.25.17", {"start": v(965.2, 685.8) * mm, "end": v(990.6, 685.8) * mm});
            skLineSegment(sketch, "E3.6.25.17", {"start": v(965.2, 660.4) * mm, "end": v(990.6, 660.4) * mm});
            skLineSegment(sketch, "E3.9.25.17", {"start": v(965.2, 660.4) * mm, "end": v(965.2, 685.8) * mm});
            skLineSegment(sketch, "E3.0.25.18", {"start": v(990.6, 698.5) * mm, "end": v(990.6, 723.9) * mm});
            skLineSegment(sketch, "E3.3.25.18", {"start": v(965.2, 723.9) * mm, "end": v(990.6, 723.9) * mm});
            skLineSegment(sketch, "E3.6.25.18", {"start": v(965.2, 698.5) * mm, "end": v(990.6, 698.5) * mm});
            skLineSegment(sketch, "E3.9.25.18", {"start": v(965.2, 698.5) * mm, "end": v(965.2, 723.9) * mm});
            skLineSegment(sketch, "E3.0.25.19", {"start": v(990.6, 736.6) * mm, "end": v(990.6, 762) * mm});
            skLineSegment(sketch, "E3.3.25.19", {"start": v(965.2, 762) * mm, "end": v(990.6, 762) * mm});
            skLineSegment(sketch, "E3.6.25.19", {"start": v(965.2, 736.6) * mm, "end": v(990.6, 736.6) * mm});
            skLineSegment(sketch, "E3.9.25.19", {"start": v(965.2, 736.6) * mm, "end": v(965.2, 762) * mm});
            skLineSegment(sketch, "E3.0.26.0", {"start": v(1028.7, 12.7) * mm, "end": v(1028.7, 38.1) * mm});
            skLineSegment(sketch, "E3.3.26.0", {"start": v(1003.3, 38.1) * mm, "end": v(1028.7, 38.1) * mm});
            skLineSegment(sketch, "E3.6.26.0", {"start": v(1003.3, 12.7) * mm, "end": v(1028.7, 12.7) * mm});
            skLineSegment(sketch, "E3.9.26.0", {"start": v(1003.3, 12.7) * mm, "end": v(1003.3, 38.1) * mm});
            skLineSegment(sketch, "E3.0.26.1", {"start": v(1028.7, 50.8) * mm, "end": v(1028.7, 76.2) * mm});
            skLineSegment(sketch, "E3.3.26.1", {"start": v(1003.3, 76.2) * mm, "end": v(1028.7, 76.2) * mm});
            skLineSegment(sketch, "E3.6.26.1", {"start": v(1003.3, 50.8) * mm, "end": v(1028.7, 50.8) * mm});
            skLineSegment(sketch, "E3.9.26.1", {"start": v(1003.3, 50.8) * mm, "end": v(1003.3, 76.2) * mm});
            skLineSegment(sketch, "E3.0.26.2", {"start": v(1028.7, 88.9) * mm, "end": v(1028.7, 114.3) * mm});
            skLineSegment(sketch, "E3.3.26.2", {"start": v(1003.3, 114.3) * mm, "end": v(1028.7, 114.3) * mm});
            skLineSegment(sketch, "E3.6.26.2", {"start": v(1003.3, 88.9) * mm, "end": v(1028.7, 88.9) * mm});
            skLineSegment(sketch, "E3.9.26.2", {"start": v(1003.3, 88.9) * mm, "end": v(1003.3, 114.3) * mm});
            skLineSegment(sketch, "E3.0.26.3", {"start": v(1028.7, 127) * mm, "end": v(1028.7, 152.4) * mm});
            skLineSegment(sketch, "E3.3.26.3", {"start": v(1003.3, 152.4) * mm, "end": v(1028.7, 152.4) * mm});
            skLineSegment(sketch, "E3.6.26.3", {"start": v(1003.3, 127) * mm, "end": v(1028.7, 127) * mm});
            skLineSegment(sketch, "E3.9.26.3", {"start": v(1003.3, 127) * mm, "end": v(1003.3, 152.4) * mm});
            skLineSegment(sketch, "E3.0.26.4", {"start": v(1028.7, 165.1) * mm, "end": v(1028.7, 190.5) * mm});
            skLineSegment(sketch, "E3.3.26.4", {"start": v(1003.3, 190.5) * mm, "end": v(1028.7, 190.5) * mm});
            skLineSegment(sketch, "E3.6.26.4", {"start": v(1003.3, 165.1) * mm, "end": v(1028.7, 165.1) * mm});
            skLineSegment(sketch, "E3.9.26.4", {"start": v(1003.3, 165.1) * mm, "end": v(1003.3, 190.5) * mm});
            skLineSegment(sketch, "E3.0.26.5", {"start": v(1028.7, 203.2) * mm, "end": v(1028.7, 228.6) * mm});
            skLineSegment(sketch, "E3.3.26.5", {"start": v(1003.3, 228.6) * mm, "end": v(1028.7, 228.6) * mm});
            skLineSegment(sketch, "E3.6.26.5", {"start": v(1003.3, 203.2) * mm, "end": v(1028.7, 203.2) * mm});
            skLineSegment(sketch, "E3.9.26.5", {"start": v(1003.3, 203.2) * mm, "end": v(1003.3, 228.6) * mm});
            skLineSegment(sketch, "E3.0.26.6", {"start": v(1028.7, 241.3) * mm, "end": v(1028.7, 266.7) * mm});
            skLineSegment(sketch, "E3.3.26.6", {"start": v(1003.3, 266.7) * mm, "end": v(1028.7, 266.7) * mm});
            skLineSegment(sketch, "E3.6.26.6", {"start": v(1003.3, 241.3) * mm, "end": v(1028.7, 241.3) * mm});
            skLineSegment(sketch, "E3.9.26.6", {"start": v(1003.3, 241.3) * mm, "end": v(1003.3, 266.7) * mm});
            skLineSegment(sketch, "E3.0.26.7", {"start": v(1028.7, 279.4) * mm, "end": v(1028.7, 304.8) * mm});
            skLineSegment(sketch, "E3.3.26.7", {"start": v(1003.3, 304.8) * mm, "end": v(1028.7, 304.8) * mm});
            skLineSegment(sketch, "E3.6.26.7", {"start": v(1003.3, 279.4) * mm, "end": v(1028.7, 279.4) * mm});
            skLineSegment(sketch, "E3.9.26.7", {"start": v(1003.3, 279.4) * mm, "end": v(1003.3, 304.8) * mm});
            skLineSegment(sketch, "E3.0.26.8", {"start": v(1028.7, 317.5) * mm, "end": v(1028.7, 342.9) * mm});
            skLineSegment(sketch, "E3.3.26.8", {"start": v(1003.3, 342.9) * mm, "end": v(1028.7, 342.9) * mm});
            skLineSegment(sketch, "E3.6.26.8", {"start": v(1003.3, 317.5) * mm, "end": v(1028.7, 317.5) * mm});
            skLineSegment(sketch, "E3.9.26.8", {"start": v(1003.3, 317.5) * mm, "end": v(1003.3, 342.9) * mm});
            skLineSegment(sketch, "E3.0.26.9", {"start": v(1028.7, 355.6) * mm, "end": v(1028.7, 381) * mm});
            skLineSegment(sketch, "E3.3.26.9", {"start": v(1003.3, 381) * mm, "end": v(1028.7, 381) * mm});
            skLineSegment(sketch, "E3.6.26.9", {"start": v(1003.3, 355.6) * mm, "end": v(1028.7, 355.6) * mm});
            skLineSegment(sketch, "E3.9.26.9", {"start": v(1003.3, 355.6) * mm, "end": v(1003.3, 381) * mm});
            skLineSegment(sketch, "E3.0.26.10", {"start": v(1028.7, 393.7) * mm, "end": v(1028.7, 419.1) * mm});
            skLineSegment(sketch, "E3.3.26.10", {"start": v(1003.3, 419.1) * mm, "end": v(1028.7, 419.1) * mm});
            skLineSegment(sketch, "E3.6.26.10", {"start": v(1003.3, 393.7) * mm, "end": v(1028.7, 393.7) * mm});
            skLineSegment(sketch, "E3.9.26.10", {"start": v(1003.3, 393.7) * mm, "end": v(1003.3, 419.1) * mm});
            skLineSegment(sketch, "E3.0.26.11", {"start": v(1028.7, 431.8) * mm, "end": v(1028.7, 457.2) * mm});
            skLineSegment(sketch, "E3.3.26.11", {"start": v(1003.3, 457.2) * mm, "end": v(1028.7, 457.2) * mm});
            skLineSegment(sketch, "E3.6.26.11", {"start": v(1003.3, 431.8) * mm, "end": v(1028.7, 431.8) * mm});
            skLineSegment(sketch, "E3.9.26.11", {"start": v(1003.3, 431.8) * mm, "end": v(1003.3, 457.2) * mm});
            skLineSegment(sketch, "E3.0.26.12", {"start": v(1028.7, 469.9) * mm, "end": v(1028.7, 495.3) * mm});
            skLineSegment(sketch, "E3.3.26.12", {"start": v(1003.3, 495.3) * mm, "end": v(1028.7, 495.3) * mm});
            skLineSegment(sketch, "E3.6.26.12", {"start": v(1003.3, 469.9) * mm, "end": v(1028.7, 469.9) * mm});
            skLineSegment(sketch, "E3.9.26.12", {"start": v(1003.3, 469.9) * mm, "end": v(1003.3, 495.3) * mm});
            skLineSegment(sketch, "E3.0.26.13", {"start": v(1028.7, 508) * mm, "end": v(1028.7, 533.4) * mm});
            skLineSegment(sketch, "E3.3.26.13", {"start": v(1003.3, 533.4) * mm, "end": v(1028.7, 533.4) * mm});
            skLineSegment(sketch, "E3.6.26.13", {"start": v(1003.3, 508) * mm, "end": v(1028.7, 508) * mm});
            skLineSegment(sketch, "E3.9.26.13", {"start": v(1003.3, 508) * mm, "end": v(1003.3, 533.4) * mm});
            skLineSegment(sketch, "E3.0.26.14", {"start": v(1028.7, 546.1) * mm, "end": v(1028.7, 571.5) * mm});
            skLineSegment(sketch, "E3.3.26.14", {"start": v(1003.3, 571.5) * mm, "end": v(1028.7, 571.5) * mm});
            skLineSegment(sketch, "E3.6.26.14", {"start": v(1003.3, 546.1) * mm, "end": v(1028.7, 546.1) * mm});
            skLineSegment(sketch, "E3.9.26.14", {"start": v(1003.3, 546.1) * mm, "end": v(1003.3, 571.5) * mm});
            skLineSegment(sketch, "E3.0.26.15", {"start": v(1028.7, 584.2) * mm, "end": v(1028.7, 609.6) * mm});
            skLineSegment(sketch, "E3.3.26.15", {"start": v(1003.3, 609.6) * mm, "end": v(1028.7, 609.6) * mm});
            skLineSegment(sketch, "E3.6.26.15", {"start": v(1003.3, 584.2) * mm, "end": v(1028.7, 584.2) * mm});
            skLineSegment(sketch, "E3.9.26.15", {"start": v(1003.3, 584.2) * mm, "end": v(1003.3, 609.6) * mm});
            skLineSegment(sketch, "E3.0.26.16", {"start": v(1028.7, 622.3) * mm, "end": v(1028.7, 647.7) * mm});
            skLineSegment(sketch, "E3.3.26.16", {"start": v(1003.3, 647.7) * mm, "end": v(1028.7, 647.7) * mm});
            skLineSegment(sketch, "E3.6.26.16", {"start": v(1003.3, 622.3) * mm, "end": v(1028.7, 622.3) * mm});
            skLineSegment(sketch, "E3.9.26.16", {"start": v(1003.3, 622.3) * mm, "end": v(1003.3, 647.7) * mm});
            skLineSegment(sketch, "E3.0.26.17", {"start": v(1028.7, 660.4) * mm, "end": v(1028.7, 685.8) * mm});
            skLineSegment(sketch, "E3.3.26.17", {"start": v(1003.3, 685.8) * mm, "end": v(1028.7, 685.8) * mm});
            skLineSegment(sketch, "E3.6.26.17", {"start": v(1003.3, 660.4) * mm, "end": v(1028.7, 660.4) * mm});
            skLineSegment(sketch, "E3.9.26.17", {"start": v(1003.3, 660.4) * mm, "end": v(1003.3, 685.8) * mm});
            skLineSegment(sketch, "E3.0.26.18", {"start": v(1028.7, 698.5) * mm, "end": v(1028.7, 723.9) * mm});
            skLineSegment(sketch, "E3.3.26.18", {"start": v(1003.3, 723.9) * mm, "end": v(1028.7, 723.9) * mm});
            skLineSegment(sketch, "E3.6.26.18", {"start": v(1003.3, 698.5) * mm, "end": v(1028.7, 698.5) * mm});
            skLineSegment(sketch, "E3.9.26.18", {"start": v(1003.3, 698.5) * mm, "end": v(1003.3, 723.9) * mm});
            skLineSegment(sketch, "E3.0.26.19", {"start": v(1028.7, 736.6) * mm, "end": v(1028.7, 762) * mm});
            skLineSegment(sketch, "E3.3.26.19", {"start": v(1003.3, 762) * mm, "end": v(1028.7, 762) * mm});
            skLineSegment(sketch, "E3.6.26.19", {"start": v(1003.3, 736.6) * mm, "end": v(1028.7, 736.6) * mm});
            skLineSegment(sketch, "E3.9.26.19", {"start": v(1003.3, 736.6) * mm, "end": v(1003.3, 762) * mm});
            skLineSegment(sketch, "E3.0.27.0", {"start": v(1066.8, 12.7) * mm, "end": v(1066.8, 38.1) * mm});
            skLineSegment(sketch, "E3.3.27.0", {"start": v(1041.4, 38.1) * mm, "end": v(1066.8, 38.1) * mm});
            skLineSegment(sketch, "E3.6.27.0", {"start": v(1041.4, 12.7) * mm, "end": v(1066.8, 12.7) * mm});
            skLineSegment(sketch, "E3.9.27.0", {"start": v(1041.4, 12.7) * mm, "end": v(1041.4, 38.1) * mm});
            skLineSegment(sketch, "E3.0.27.1", {"start": v(1066.8, 50.8) * mm, "end": v(1066.8, 76.2) * mm});
            skLineSegment(sketch, "E3.3.27.1", {"start": v(1041.4, 76.2) * mm, "end": v(1066.8, 76.2) * mm});
            skLineSegment(sketch, "E3.6.27.1", {"start": v(1041.4, 50.8) * mm, "end": v(1066.8, 50.8) * mm});
            skLineSegment(sketch, "E3.9.27.1", {"start": v(1041.4, 50.8) * mm, "end": v(1041.4, 76.2) * mm});
            skLineSegment(sketch, "E3.0.27.2", {"start": v(1066.8, 88.9) * mm, "end": v(1066.8, 114.3) * mm});
            skLineSegment(sketch, "E3.3.27.2", {"start": v(1041.4, 114.3) * mm, "end": v(1066.8, 114.3) * mm});
            skLineSegment(sketch, "E3.6.27.2", {"start": v(1041.4, 88.9) * mm, "end": v(1066.8, 88.9) * mm});
            skLineSegment(sketch, "E3.9.27.2", {"start": v(1041.4, 88.9) * mm, "end": v(1041.4, 114.3) * mm});
            skLineSegment(sketch, "E3.0.27.3", {"start": v(1066.8, 127) * mm, "end": v(1066.8, 152.4) * mm});
            skLineSegment(sketch, "E3.3.27.3", {"start": v(1041.4, 152.4) * mm, "end": v(1066.8, 152.4) * mm});
            skLineSegment(sketch, "E3.6.27.3", {"start": v(1041.4, 127) * mm, "end": v(1066.8, 127) * mm});
            skLineSegment(sketch, "E3.9.27.3", {"start": v(1041.4, 127) * mm, "end": v(1041.4, 152.4) * mm});
            skLineSegment(sketch, "E3.0.27.4", {"start": v(1066.8, 165.1) * mm, "end": v(1066.8, 190.5) * mm});
            skLineSegment(sketch, "E3.3.27.4", {"start": v(1041.4, 190.5) * mm, "end": v(1066.8, 190.5) * mm});
            skLineSegment(sketch, "E3.6.27.4", {"start": v(1041.4, 165.1) * mm, "end": v(1066.8, 165.1) * mm});
            skLineSegment(sketch, "E3.9.27.4", {"start": v(1041.4, 165.1) * mm, "end": v(1041.4, 190.5) * mm});
            skLineSegment(sketch, "E3.0.27.5", {"start": v(1066.8, 203.2) * mm, "end": v(1066.8, 228.6) * mm});
            skLineSegment(sketch, "E3.3.27.5", {"start": v(1041.4, 228.6) * mm, "end": v(1066.8, 228.6) * mm});
            skLineSegment(sketch, "E3.6.27.5", {"start": v(1041.4, 203.2) * mm, "end": v(1066.8, 203.2) * mm});
            skLineSegment(sketch, "E3.9.27.5", {"start": v(1041.4, 203.2) * mm, "end": v(1041.4, 228.6) * mm});
            skLineSegment(sketch, "E3.0.27.6", {"start": v(1066.8, 241.3) * mm, "end": v(1066.8, 266.7) * mm});
            skLineSegment(sketch, "E3.3.27.6", {"start": v(1041.4, 266.7) * mm, "end": v(1066.8, 266.7) * mm});
            skLineSegment(sketch, "E3.6.27.6", {"start": v(1041.4, 241.3) * mm, "end": v(1066.8, 241.3) * mm});
            skLineSegment(sketch, "E3.9.27.6", {"start": v(1041.4, 241.3) * mm, "end": v(1041.4, 266.7) * mm});
            skLineSegment(sketch, "E3.0.27.7", {"start": v(1066.8, 279.4) * mm, "end": v(1066.8, 304.8) * mm});
            skLineSegment(sketch, "E3.3.27.7", {"start": v(1041.4, 304.8) * mm, "end": v(1066.8, 304.8) * mm});
            skLineSegment(sketch, "E3.6.27.7", {"start": v(1041.4, 279.4) * mm, "end": v(1066.8, 279.4) * mm});
            skLineSegment(sketch, "E3.9.27.7", {"start": v(1041.4, 279.4) * mm, "end": v(1041.4, 304.8) * mm});
            skLineSegment(sketch, "E3.0.27.8", {"start": v(1066.8, 317.5) * mm, "end": v(1066.8, 342.9) * mm});
            skLineSegment(sketch, "E3.3.27.8", {"start": v(1041.4, 342.9) * mm, "end": v(1066.8, 342.9) * mm});
            skLineSegment(sketch, "E3.6.27.8", {"start": v(1041.4, 317.5) * mm, "end": v(1066.8, 317.5) * mm});
            skLineSegment(sketch, "E3.9.27.8", {"start": v(1041.4, 317.5) * mm, "end": v(1041.4, 342.9) * mm});
            skLineSegment(sketch, "E3.0.27.9", {"start": v(1066.8, 355.6) * mm, "end": v(1066.8, 381) * mm});
            skLineSegment(sketch, "E3.3.27.9", {"start": v(1041.4, 381) * mm, "end": v(1066.8, 381) * mm});
            skLineSegment(sketch, "E3.6.27.9", {"start": v(1041.4, 355.6) * mm, "end": v(1066.8, 355.6) * mm});
            skLineSegment(sketch, "E3.9.27.9", {"start": v(1041.4, 355.6) * mm, "end": v(1041.4, 381) * mm});
            skLineSegment(sketch, "E3.0.27.10", {"start": v(1066.8, 393.7) * mm, "end": v(1066.8, 419.1) * mm});
            skLineSegment(sketch, "E3.3.27.10", {"start": v(1041.4, 419.1) * mm, "end": v(1066.8, 419.1) * mm});
            skLineSegment(sketch, "E3.6.27.10", {"start": v(1041.4, 393.7) * mm, "end": v(1066.8, 393.7) * mm});
            skLineSegment(sketch, "E3.9.27.10", {"start": v(1041.4, 393.7) * mm, "end": v(1041.4, 419.1) * mm});
            skLineSegment(sketch, "E3.0.27.11", {"start": v(1066.8, 431.8) * mm, "end": v(1066.8, 457.2) * mm});
            skLineSegment(sketch, "E3.3.27.11", {"start": v(1041.4, 457.2) * mm, "end": v(1066.8, 457.2) * mm});
            skLineSegment(sketch, "E3.6.27.11", {"start": v(1041.4, 431.8) * mm, "end": v(1066.8, 431.8) * mm});
            skLineSegment(sketch, "E3.9.27.11", {"start": v(1041.4, 431.8) * mm, "end": v(1041.4, 457.2) * mm});
            skLineSegment(sketch, "E3.0.27.12", {"start": v(1066.8, 469.9) * mm, "end": v(1066.8, 495.3) * mm});
            skLineSegment(sketch, "E3.3.27.12", {"start": v(1041.4, 495.3) * mm, "end": v(1066.8, 495.3) * mm});
            skLineSegment(sketch, "E3.6.27.12", {"start": v(1041.4, 469.9) * mm, "end": v(1066.8, 469.9) * mm});
            skLineSegment(sketch, "E3.9.27.12", {"start": v(1041.4, 469.9) * mm, "end": v(1041.4, 495.3) * mm});
            skLineSegment(sketch, "E3.0.27.13", {"start": v(1066.8, 508) * mm, "end": v(1066.8, 533.4) * mm});
            skLineSegment(sketch, "E3.3.27.13", {"start": v(1041.4, 533.4) * mm, "end": v(1066.8, 533.4) * mm});
            skLineSegment(sketch, "E3.6.27.13", {"start": v(1041.4, 508) * mm, "end": v(1066.8, 508) * mm});
            skLineSegment(sketch, "E3.9.27.13", {"start": v(1041.4, 508) * mm, "end": v(1041.4, 533.4) * mm});
            skLineSegment(sketch, "E3.0.27.14", {"start": v(1066.8, 546.1) * mm, "end": v(1066.8, 571.5) * mm});
            skLineSegment(sketch, "E3.3.27.14", {"start": v(1041.4, 571.5) * mm, "end": v(1066.8, 571.5) * mm});
            skLineSegment(sketch, "E3.6.27.14", {"start": v(1041.4, 546.1) * mm, "end": v(1066.8, 546.1) * mm});
            skLineSegment(sketch, "E3.9.27.14", {"start": v(1041.4, 546.1) * mm, "end": v(1041.4, 571.5) * mm});
            skLineSegment(sketch, "E3.0.27.15", {"start": v(1066.8, 584.2) * mm, "end": v(1066.8, 609.6) * mm});
            skLineSegment(sketch, "E3.3.27.15", {"start": v(1041.4, 609.6) * mm, "end": v(1066.8, 609.6) * mm});
            skLineSegment(sketch, "E3.6.27.15", {"start": v(1041.4, 584.2) * mm, "end": v(1066.8, 584.2) * mm});
            skLineSegment(sketch, "E3.9.27.15", {"start": v(1041.4, 584.2) * mm, "end": v(1041.4, 609.6) * mm});
            skLineSegment(sketch, "E3.0.27.16", {"start": v(1066.8, 622.3) * mm, "end": v(1066.8, 647.7) * mm});
            skLineSegment(sketch, "E3.3.27.16", {"start": v(1041.4, 647.7) * mm, "end": v(1066.8, 647.7) * mm});
            skLineSegment(sketch, "E3.6.27.16", {"start": v(1041.4, 622.3) * mm, "end": v(1066.8, 622.3) * mm});
            skLineSegment(sketch, "E3.9.27.16", {"start": v(1041.4, 622.3) * mm, "end": v(1041.4, 647.7) * mm});
            skLineSegment(sketch, "E3.0.27.17", {"start": v(1066.8, 660.4) * mm, "end": v(1066.8, 685.8) * mm});
            skLineSegment(sketch, "E3.3.27.17", {"start": v(1041.4, 685.8) * mm, "end": v(1066.8, 685.8) * mm});
            skLineSegment(sketch, "E3.6.27.17", {"start": v(1041.4, 660.4) * mm, "end": v(1066.8, 660.4) * mm});
            skLineSegment(sketch, "E3.9.27.17", {"start": v(1041.4, 660.4) * mm, "end": v(1041.4, 685.8) * mm});
            skLineSegment(sketch, "E3.0.27.18", {"start": v(1066.8, 698.5) * mm, "end": v(1066.8, 723.9) * mm});
            skLineSegment(sketch, "E3.3.27.18", {"start": v(1041.4, 723.9) * mm, "end": v(1066.8, 723.9) * mm});
            skLineSegment(sketch, "E3.6.27.18", {"start": v(1041.4, 698.5) * mm, "end": v(1066.8, 698.5) * mm});
            skLineSegment(sketch, "E3.9.27.18", {"start": v(1041.4, 698.5) * mm, "end": v(1041.4, 723.9) * mm});
            skLineSegment(sketch, "E3.0.27.19", {"start": v(1066.8, 736.6) * mm, "end": v(1066.8, 762) * mm});
            skLineSegment(sketch, "E3.3.27.19", {"start": v(1041.4, 762) * mm, "end": v(1066.8, 762) * mm});
            skLineSegment(sketch, "E3.6.27.19", {"start": v(1041.4, 736.6) * mm, "end": v(1066.8, 736.6) * mm});
            skLineSegment(sketch, "E3.9.27.19", {"start": v(1041.4, 736.6) * mm, "end": v(1041.4, 762) * mm});
            skLineSegment(sketch, "E3.0.28.0", {"start": v(1104.9, 12.7) * mm, "end": v(1104.9, 38.1) * mm});
            skLineSegment(sketch, "E3.3.28.0", {"start": v(1079.5, 38.1) * mm, "end": v(1104.9, 38.1) * mm});
            skLineSegment(sketch, "E3.6.28.0", {"start": v(1079.5, 12.7) * mm, "end": v(1104.9, 12.7) * mm});
            skLineSegment(sketch, "E3.9.28.0", {"start": v(1079.5, 12.7) * mm, "end": v(1079.5, 38.1) * mm});
            skLineSegment(sketch, "E3.0.28.1", {"start": v(1104.9, 50.8) * mm, "end": v(1104.9, 76.2) * mm});
            skLineSegment(sketch, "E3.3.28.1", {"start": v(1079.5, 76.2) * mm, "end": v(1104.9, 76.2) * mm});
            skLineSegment(sketch, "E3.6.28.1", {"start": v(1079.5, 50.8) * mm, "end": v(1104.9, 50.8) * mm});
            skLineSegment(sketch, "E3.9.28.1", {"start": v(1079.5, 50.8) * mm, "end": v(1079.5, 76.2) * mm});
            skLineSegment(sketch, "E3.0.28.2", {"start": v(1104.9, 88.9) * mm, "end": v(1104.9, 114.3) * mm});
            skLineSegment(sketch, "E3.3.28.2", {"start": v(1079.5, 114.3) * mm, "end": v(1104.9, 114.3) * mm});
            skLineSegment(sketch, "E3.6.28.2", {"start": v(1079.5, 88.9) * mm, "end": v(1104.9, 88.9) * mm});
            skLineSegment(sketch, "E3.9.28.2", {"start": v(1079.5, 88.9) * mm, "end": v(1079.5, 114.3) * mm});
            skLineSegment(sketch, "E3.0.28.3", {"start": v(1104.9, 127) * mm, "end": v(1104.9, 152.4) * mm});
            skLineSegment(sketch, "E3.3.28.3", {"start": v(1079.5, 152.4) * mm, "end": v(1104.9, 152.4) * mm});
            skLineSegment(sketch, "E3.6.28.3", {"start": v(1079.5, 127) * mm, "end": v(1104.9, 127) * mm});
            skLineSegment(sketch, "E3.9.28.3", {"start": v(1079.5, 127) * mm, "end": v(1079.5, 152.4) * mm});
            skLineSegment(sketch, "E3.0.28.4", {"start": v(1104.9, 165.1) * mm, "end": v(1104.9, 190.5) * mm});
            skLineSegment(sketch, "E3.3.28.4", {"start": v(1079.5, 190.5) * mm, "end": v(1104.9, 190.5) * mm});
            skLineSegment(sketch, "E3.6.28.4", {"start": v(1079.5, 165.1) * mm, "end": v(1104.9, 165.1) * mm});
            skLineSegment(sketch, "E3.9.28.4", {"start": v(1079.5, 165.1) * mm, "end": v(1079.5, 190.5) * mm});
            skLineSegment(sketch, "E3.0.28.5", {"start": v(1104.9, 203.2) * mm, "end": v(1104.9, 228.6) * mm});
            skLineSegment(sketch, "E3.3.28.5", {"start": v(1079.5, 228.6) * mm, "end": v(1104.9, 228.6) * mm});
            skLineSegment(sketch, "E3.6.28.5", {"start": v(1079.5, 203.2) * mm, "end": v(1104.9, 203.2) * mm});
            skLineSegment(sketch, "E3.9.28.5", {"start": v(1079.5, 203.2) * mm, "end": v(1079.5, 228.6) * mm});
            skLineSegment(sketch, "E3.0.28.6", {"start": v(1104.9, 241.3) * mm, "end": v(1104.9, 266.7) * mm});
            skLineSegment(sketch, "E3.3.28.6", {"start": v(1079.5, 266.7) * mm, "end": v(1104.9, 266.7) * mm});
            skLineSegment(sketch, "E3.6.28.6", {"start": v(1079.5, 241.3) * mm, "end": v(1104.9, 241.3) * mm});
            skLineSegment(sketch, "E3.9.28.6", {"start": v(1079.5, 241.3) * mm, "end": v(1079.5, 266.7) * mm});
            skLineSegment(sketch, "E3.0.28.7", {"start": v(1104.9, 279.4) * mm, "end": v(1104.9, 304.8) * mm});
            skLineSegment(sketch, "E3.3.28.7", {"start": v(1079.5, 304.8) * mm, "end": v(1104.9, 304.8) * mm});
            skLineSegment(sketch, "E3.6.28.7", {"start": v(1079.5, 279.4) * mm, "end": v(1104.9, 279.4) * mm});
            skLineSegment(sketch, "E3.9.28.7", {"start": v(1079.5, 279.4) * mm, "end": v(1079.5, 304.8) * mm});
            skLineSegment(sketch, "E3.0.28.8", {"start": v(1104.9, 317.5) * mm, "end": v(1104.9, 342.9) * mm});
            skLineSegment(sketch, "E3.3.28.8", {"start": v(1079.5, 342.9) * mm, "end": v(1104.9, 342.9) * mm});
            skLineSegment(sketch, "E3.6.28.8", {"start": v(1079.5, 317.5) * mm, "end": v(1104.9, 317.5) * mm});
            skLineSegment(sketch, "E3.9.28.8", {"start": v(1079.5, 317.5) * mm, "end": v(1079.5, 342.9) * mm});
            skLineSegment(sketch, "E3.0.28.9", {"start": v(1104.9, 355.6) * mm, "end": v(1104.9, 381) * mm});
            skLineSegment(sketch, "E3.3.28.9", {"start": v(1079.5, 381) * mm, "end": v(1104.9, 381) * mm});
            skLineSegment(sketch, "E3.6.28.9", {"start": v(1079.5, 355.6) * mm, "end": v(1104.9, 355.6) * mm});
            skLineSegment(sketch, "E3.9.28.9", {"start": v(1079.5, 355.6) * mm, "end": v(1079.5, 381) * mm});
            skLineSegment(sketch, "E3.0.28.10", {"start": v(1104.9, 393.7) * mm, "end": v(1104.9, 419.1) * mm});
            skLineSegment(sketch, "E3.3.28.10", {"start": v(1079.5, 419.1) * mm, "end": v(1104.9, 419.1) * mm});
            skLineSegment(sketch, "E3.6.28.10", {"start": v(1079.5, 393.7) * mm, "end": v(1104.9, 393.7) * mm});
            skLineSegment(sketch, "E3.9.28.10", {"start": v(1079.5, 393.7) * mm, "end": v(1079.5, 419.1) * mm});
            skLineSegment(sketch, "E3.0.28.11", {"start": v(1104.9, 431.8) * mm, "end": v(1104.9, 457.2) * mm});
            skLineSegment(sketch, "E3.3.28.11", {"start": v(1079.5, 457.2) * mm, "end": v(1104.9, 457.2) * mm});
            skLineSegment(sketch, "E3.6.28.11", {"start": v(1079.5, 431.8) * mm, "end": v(1104.9, 431.8) * mm});
            skLineSegment(sketch, "E3.9.28.11", {"start": v(1079.5, 431.8) * mm, "end": v(1079.5, 457.2) * mm});
            skLineSegment(sketch, "E3.0.28.12", {"start": v(1104.9, 469.9) * mm, "end": v(1104.9, 495.3) * mm});
            skLineSegment(sketch, "E3.3.28.12", {"start": v(1079.5, 495.3) * mm, "end": v(1104.9, 495.3) * mm});
            skLineSegment(sketch, "E3.6.28.12", {"start": v(1079.5, 469.9) * mm, "end": v(1104.9, 469.9) * mm});
            skLineSegment(sketch, "E3.9.28.12", {"start": v(1079.5, 469.9) * mm, "end": v(1079.5, 495.3) * mm});
            skLineSegment(sketch, "E3.0.28.13", {"start": v(1104.9, 508) * mm, "end": v(1104.9, 533.4) * mm});
            skLineSegment(sketch, "E3.3.28.13", {"start": v(1079.5, 533.4) * mm, "end": v(1104.9, 533.4) * mm});
            skLineSegment(sketch, "E3.6.28.13", {"start": v(1079.5, 508) * mm, "end": v(1104.9, 508) * mm});
            skLineSegment(sketch, "E3.9.28.13", {"start": v(1079.5, 508) * mm, "end": v(1079.5, 533.4) * mm});
            skLineSegment(sketch, "E3.0.28.14", {"start": v(1104.9, 546.1) * mm, "end": v(1104.9, 571.5) * mm});
            skLineSegment(sketch, "E3.3.28.14", {"start": v(1079.5, 571.5) * mm, "end": v(1104.9, 571.5) * mm});
            skLineSegment(sketch, "E3.6.28.14", {"start": v(1079.5, 546.1) * mm, "end": v(1104.9, 546.1) * mm});
            skLineSegment(sketch, "E3.9.28.14", {"start": v(1079.5, 546.1) * mm, "end": v(1079.5, 571.5) * mm});
            skLineSegment(sketch, "E3.0.28.15", {"start": v(1104.9, 584.2) * mm, "end": v(1104.9, 609.6) * mm});
            skLineSegment(sketch, "E3.3.28.15", {"start": v(1079.5, 609.6) * mm, "end": v(1104.9, 609.6) * mm});
            skLineSegment(sketch, "E3.6.28.15", {"start": v(1079.5, 584.2) * mm, "end": v(1104.9, 584.2) * mm});
            skLineSegment(sketch, "E3.9.28.15", {"start": v(1079.5, 584.2) * mm, "end": v(1079.5, 609.6) * mm});
            skLineSegment(sketch, "E3.0.28.16", {"start": v(1104.9, 622.3) * mm, "end": v(1104.9, 647.7) * mm});
            skLineSegment(sketch, "E3.3.28.16", {"start": v(1079.5, 647.7) * mm, "end": v(1104.9, 647.7) * mm});
            skLineSegment(sketch, "E3.6.28.16", {"start": v(1079.5, 622.3) * mm, "end": v(1104.9, 622.3) * mm});
            skLineSegment(sketch, "E3.9.28.16", {"start": v(1079.5, 622.3) * mm, "end": v(1079.5, 647.7) * mm});
            skLineSegment(sketch, "E3.0.28.17", {"start": v(1104.9, 660.4) * mm, "end": v(1104.9, 685.8) * mm});
            skLineSegment(sketch, "E3.3.28.17", {"start": v(1079.5, 685.8) * mm, "end": v(1104.9, 685.8) * mm});
            skLineSegment(sketch, "E3.6.28.17", {"start": v(1079.5, 660.4) * mm, "end": v(1104.9, 660.4) * mm});
            skLineSegment(sketch, "E3.9.28.17", {"start": v(1079.5, 660.4) * mm, "end": v(1079.5, 685.8) * mm});
            skLineSegment(sketch, "E3.0.28.18", {"start": v(1104.9, 698.5) * mm, "end": v(1104.9, 723.9) * mm});
            skLineSegment(sketch, "E3.3.28.18", {"start": v(1079.5, 723.9) * mm, "end": v(1104.9, 723.9) * mm});
            skLineSegment(sketch, "E3.6.28.18", {"start": v(1079.5, 698.5) * mm, "end": v(1104.9, 698.5) * mm});
            skLineSegment(sketch, "E3.9.28.18", {"start": v(1079.5, 698.5) * mm, "end": v(1079.5, 723.9) * mm});
            skLineSegment(sketch, "E3.0.28.19", {"start": v(1104.9, 736.6) * mm, "end": v(1104.9, 762) * mm});
            skLineSegment(sketch, "E3.3.28.19", {"start": v(1079.5, 762) * mm, "end": v(1104.9, 762) * mm});
            skLineSegment(sketch, "E3.6.28.19", {"start": v(1079.5, 736.6) * mm, "end": v(1104.9, 736.6) * mm});
            skLineSegment(sketch, "E3.9.28.19", {"start": v(1079.5, 736.6) * mm, "end": v(1079.5, 762) * mm});
            skLineSegment(sketch, "E3.0.29.0", {"start": v(1143, 12.7) * mm, "end": v(1143, 38.1) * mm});
            skLineSegment(sketch, "E3.3.29.0", {"start": v(1117.6, 38.1) * mm, "end": v(1143, 38.1) * mm});
            skLineSegment(sketch, "E3.6.29.0", {"start": v(1117.6, 12.7) * mm, "end": v(1143, 12.7) * mm});
            skLineSegment(sketch, "E3.9.29.0", {"start": v(1117.6, 12.7) * mm, "end": v(1117.6, 38.1) * mm});
            skLineSegment(sketch, "E3.0.29.1", {"start": v(1143, 50.8) * mm, "end": v(1143, 76.2) * mm});
            skLineSegment(sketch, "E3.3.29.1", {"start": v(1117.6, 76.2) * mm, "end": v(1143, 76.2) * mm});
            skLineSegment(sketch, "E3.6.29.1", {"start": v(1117.6, 50.8) * mm, "end": v(1143, 50.8) * mm});
            skLineSegment(sketch, "E3.9.29.1", {"start": v(1117.6, 50.8) * mm, "end": v(1117.6, 76.2) * mm});
            skLineSegment(sketch, "E3.0.29.2", {"start": v(1143, 88.9) * mm, "end": v(1143, 114.3) * mm});
            skLineSegment(sketch, "E3.3.29.2", {"start": v(1117.6, 114.3) * mm, "end": v(1143, 114.3) * mm});
            skLineSegment(sketch, "E3.6.29.2", {"start": v(1117.6, 88.9) * mm, "end": v(1143, 88.9) * mm});
            skLineSegment(sketch, "E3.9.29.2", {"start": v(1117.6, 88.9) * mm, "end": v(1117.6, 114.3) * mm});
            skLineSegment(sketch, "E3.0.29.3", {"start": v(1143, 127) * mm, "end": v(1143, 152.4) * mm});
            skLineSegment(sketch, "E3.3.29.3", {"start": v(1117.6, 152.4) * mm, "end": v(1143, 152.4) * mm});
            skLineSegment(sketch, "E3.6.29.3", {"start": v(1117.6, 127) * mm, "end": v(1143, 127) * mm});
            skLineSegment(sketch, "E3.9.29.3", {"start": v(1117.6, 127) * mm, "end": v(1117.6, 152.4) * mm});
            skLineSegment(sketch, "E3.0.29.4", {"start": v(1143, 165.1) * mm, "end": v(1143, 190.5) * mm});
            skLineSegment(sketch, "E3.3.29.4", {"start": v(1117.6, 190.5) * mm, "end": v(1143, 190.5) * mm});
            skLineSegment(sketch, "E3.6.29.4", {"start": v(1117.6, 165.1) * mm, "end": v(1143, 165.1) * mm});
            skLineSegment(sketch, "E3.9.29.4", {"start": v(1117.6, 165.1) * mm, "end": v(1117.6, 190.5) * mm});
            skLineSegment(sketch, "E3.0.29.5", {"start": v(1143, 203.2) * mm, "end": v(1143, 228.6) * mm});
            skLineSegment(sketch, "E3.3.29.5", {"start": v(1117.6, 228.6) * mm, "end": v(1143, 228.6) * mm});
            skLineSegment(sketch, "E3.6.29.5", {"start": v(1117.6, 203.2) * mm, "end": v(1143, 203.2) * mm});
            skLineSegment(sketch, "E3.9.29.5", {"start": v(1117.6, 203.2) * mm, "end": v(1117.6, 228.6) * mm});
            skLineSegment(sketch, "E3.0.29.6", {"start": v(1143, 241.3) * mm, "end": v(1143, 266.7) * mm});
            skLineSegment(sketch, "E3.3.29.6", {"start": v(1117.6, 266.7) * mm, "end": v(1143, 266.7) * mm});
            skLineSegment(sketch, "E3.6.29.6", {"start": v(1117.6, 241.3) * mm, "end": v(1143, 241.3) * mm});
            skLineSegment(sketch, "E3.9.29.6", {"start": v(1117.6, 241.3) * mm, "end": v(1117.6, 266.7) * mm});
            skLineSegment(sketch, "E3.0.29.7", {"start": v(1143, 279.4) * mm, "end": v(1143, 304.8) * mm});
            skLineSegment(sketch, "E3.3.29.7", {"start": v(1117.6, 304.8) * mm, "end": v(1143, 304.8) * mm});
            skLineSegment(sketch, "E3.6.29.7", {"start": v(1117.6, 279.4) * mm, "end": v(1143, 279.4) * mm});
            skLineSegment(sketch, "E3.9.29.7", {"start": v(1117.6, 279.4) * mm, "end": v(1117.6, 304.8) * mm});
            skLineSegment(sketch, "E3.0.29.8", {"start": v(1143, 317.5) * mm, "end": v(1143, 342.9) * mm});
            skLineSegment(sketch, "E3.3.29.8", {"start": v(1117.6, 342.9) * mm, "end": v(1143, 342.9) * mm});
            skLineSegment(sketch, "E3.6.29.8", {"start": v(1117.6, 317.5) * mm, "end": v(1143, 317.5) * mm});
            skLineSegment(sketch, "E3.9.29.8", {"start": v(1117.6, 317.5) * mm, "end": v(1117.6, 342.9) * mm});
            skLineSegment(sketch, "E3.0.29.9", {"start": v(1143, 355.6) * mm, "end": v(1143, 381) * mm});
            skLineSegment(sketch, "E3.3.29.9", {"start": v(1117.6, 381) * mm, "end": v(1143, 381) * mm});
            skLineSegment(sketch, "E3.6.29.9", {"start": v(1117.6, 355.6) * mm, "end": v(1143, 355.6) * mm});
            skLineSegment(sketch, "E3.9.29.9", {"start": v(1117.6, 355.6) * mm, "end": v(1117.6, 381) * mm});
            skLineSegment(sketch, "E3.0.29.10", {"start": v(1143, 393.7) * mm, "end": v(1143, 419.1) * mm});
            skLineSegment(sketch, "E3.3.29.10", {"start": v(1117.6, 419.1) * mm, "end": v(1143, 419.1) * mm});
            skLineSegment(sketch, "E3.6.29.10", {"start": v(1117.6, 393.7) * mm, "end": v(1143, 393.7) * mm});
            skLineSegment(sketch, "E3.9.29.10", {"start": v(1117.6, 393.7) * mm, "end": v(1117.6, 419.1) * mm});
            skLineSegment(sketch, "E3.0.29.11", {"start": v(1143, 431.8) * mm, "end": v(1143, 457.2) * mm});
            skLineSegment(sketch, "E3.3.29.11", {"start": v(1117.6, 457.2) * mm, "end": v(1143, 457.2) * mm});
            skLineSegment(sketch, "E3.6.29.11", {"start": v(1117.6, 431.8) * mm, "end": v(1143, 431.8) * mm});
            skLineSegment(sketch, "E3.9.29.11", {"start": v(1117.6, 431.8) * mm, "end": v(1117.6, 457.2) * mm});
            skLineSegment(sketch, "E3.0.29.12", {"start": v(1143, 469.9) * mm, "end": v(1143, 495.3) * mm});
            skLineSegment(sketch, "E3.3.29.12", {"start": v(1117.6, 495.3) * mm, "end": v(1143, 495.3) * mm});
            skLineSegment(sketch, "E3.6.29.12", {"start": v(1117.6, 469.9) * mm, "end": v(1143, 469.9) * mm});
            skLineSegment(sketch, "E3.9.29.12", {"start": v(1117.6, 469.9) * mm, "end": v(1117.6, 495.3) * mm});
            skLineSegment(sketch, "E3.0.29.13", {"start": v(1143, 508) * mm, "end": v(1143, 533.4) * mm});
            skLineSegment(sketch, "E3.3.29.13", {"start": v(1117.6, 533.4) * mm, "end": v(1143, 533.4) * mm});
            skLineSegment(sketch, "E3.6.29.13", {"start": v(1117.6, 508) * mm, "end": v(1143, 508) * mm});
            skLineSegment(sketch, "E3.9.29.13", {"start": v(1117.6, 508) * mm, "end": v(1117.6, 533.4) * mm});
            skLineSegment(sketch, "E3.0.29.14", {"start": v(1143, 546.1) * mm, "end": v(1143, 571.5) * mm});
            skLineSegment(sketch, "E3.3.29.14", {"start": v(1117.6, 571.5) * mm, "end": v(1143, 571.5) * mm});
            skLineSegment(sketch, "E3.6.29.14", {"start": v(1117.6, 546.1) * mm, "end": v(1143, 546.1) * mm});
            skLineSegment(sketch, "E3.9.29.14", {"start": v(1117.6, 546.1) * mm, "end": v(1117.6, 571.5) * mm});
            skLineSegment(sketch, "E3.0.29.15", {"start": v(1143, 584.2) * mm, "end": v(1143, 609.6) * mm});
            skLineSegment(sketch, "E3.3.29.15", {"start": v(1117.6, 609.6) * mm, "end": v(1143, 609.6) * mm});
            skLineSegment(sketch, "E3.6.29.15", {"start": v(1117.6, 584.2) * mm, "end": v(1143, 584.2) * mm});
            skLineSegment(sketch, "E3.9.29.15", {"start": v(1117.6, 584.2) * mm, "end": v(1117.6, 609.6) * mm});
            skLineSegment(sketch, "E3.0.29.16", {"start": v(1143, 622.3) * mm, "end": v(1143, 647.7) * mm});
            skLineSegment(sketch, "E3.3.29.16", {"start": v(1117.6, 647.7) * mm, "end": v(1143, 647.7) * mm});
            skLineSegment(sketch, "E3.6.29.16", {"start": v(1117.6, 622.3) * mm, "end": v(1143, 622.3) * mm});
            skLineSegment(sketch, "E3.9.29.16", {"start": v(1117.6, 622.3) * mm, "end": v(1117.6, 647.7) * mm});
            skLineSegment(sketch, "E3.0.29.17", {"start": v(1143, 660.4) * mm, "end": v(1143, 685.8) * mm});
            skLineSegment(sketch, "E3.3.29.17", {"start": v(1117.6, 685.8) * mm, "end": v(1143, 685.8) * mm});
            skLineSegment(sketch, "E3.6.29.17", {"start": v(1117.6, 660.4) * mm, "end": v(1143, 660.4) * mm});
            skLineSegment(sketch, "E3.9.29.17", {"start": v(1117.6, 660.4) * mm, "end": v(1117.6, 685.8) * mm});
            skLineSegment(sketch, "E3.0.29.18", {"start": v(1143, 698.5) * mm, "end": v(1143, 723.9) * mm});
            skLineSegment(sketch, "E3.3.29.18", {"start": v(1117.6, 723.9) * mm, "end": v(1143, 723.9) * mm});
            skLineSegment(sketch, "E3.6.29.18", {"start": v(1117.6, 698.5) * mm, "end": v(1143, 698.5) * mm});
            skLineSegment(sketch, "E3.9.29.18", {"start": v(1117.6, 698.5) * mm, "end": v(1117.6, 723.9) * mm});
            skLineSegment(sketch, "E3.0.29.19", {"start": v(1143, 736.6) * mm, "end": v(1143, 762) * mm});
            skLineSegment(sketch, "E3.3.29.19", {"start": v(1117.6, 762) * mm, "end": v(1143, 762) * mm});
            skLineSegment(sketch, "E3.6.29.19", {"start": v(1117.6, 736.6) * mm, "end": v(1143, 736.6) * mm});
            skLineSegment(sketch, "E3.9.29.19", {"start": v(1117.6, 736.6) * mm, "end": v(1117.6, 762) * mm});
            skSolve(sketch);
        }
        {
            var Q0;
            Q0=qSketchRegion(id+"F2",true);
            extrude(context, id + "F3", {"entities" : qUnion([Q0]), "operationType" : NewBodyOperationType.ADD, "depth" : 25.4 * mm});
        }
        {
            var Q0;
            Q0=makeQuery(id+"F3.opExtrude","CAP_EDGE",EDGE,{"disambiguationData":[OSD([sQuery(id+"F2.wireOp",EDGE,"E1.bottom")])],"isStart":false});
            var Q1;
            Q1=makeQuery(id+"F3.opExtrude","CAP_EDGE",EDGE,{"disambiguationData":[OSD([sQuery(id+"F2.wireOp",EDGE,"E2.4.0.3")])],"isStart":false});
            var Q2;
            Q2=makeQuery(id+"F3.opExtrude","CAP_EDGE",EDGE,{"disambiguationData":[OSD([sQuery(id+"F2.wireOp",EDGE,"E2.16.0.3")])],"isStart":false});
            var Q3;
            Q3=makeQuery(id+"F3.opExtrude","CAP_EDGE",EDGE,{"disambiguationData":[OSD([sQuery(id+"F2.wireOp",EDGE,"E2.3.0.3")])],"isStart":false});
            var Q4;
            Q4=makeQuery(id+"F3.opExtrude","CAP_EDGE",EDGE,{"disambiguationData":[OSD([sQuery(id+"F2.wireOp",EDGE,"E1.right")])],"isStart":false});
            var Q5;
            Q5=makeQuery(id+"F3.opExtrude","CAP_EDGE",EDGE,{"disambiguationData":[OSD([sQuery(id+"F2.wireOp",EDGE,"E2.19.0.3")])],"isStart":false});
            var Q6;
            Q6=makeQuery(id+"F3.opExtrude","CAP_EDGE",EDGE,{"disambiguationData":[OSD([sQuery(id+"F2.wireOp",EDGE,"E2.13.0.3")])],"isStart":false});
            var Q7;
            Q7=makeQuery(id+"F3.opExtrude","CAP_EDGE",EDGE,{"disambiguationData":[OSD([sQuery(id+"F2.wireOp",EDGE,"E2.7.0.3")])],"isStart":false});
            var Q8;
            Q8=makeQuery(id+"F3.opExtrude","CAP_EDGE",EDGE,{"disambiguationData":[OSD([sQuery(id+"F2.wireOp",EDGE,"E3.9.26.0")])],"isStart":false});
            var Q9;
            Q9=makeQuery(id+"F3.opExtrude","CAP_EDGE",EDGE,{"disambiguationData":[OSD([sQuery(id+"F2.wireOp",EDGE,"E2.1.0.3")])],"isStart":false});
            var Q10;
            Q10=makeQuery(id+"F3.opExtrude","CAP_EDGE",EDGE,{"disambiguationData":[OSD([sQuery(id+"F2.wireOp",EDGE,"E3.9.20.0")])],"isStart":false});
            var Q11;
            Q11=makeQuery(id+"F3.opExtrude","CAP_EDGE",EDGE,{"disambiguationData":[OSD([sQuery(id+"F2.wireOp",EDGE,"E3.9.27.0")])],"isStart":false});
            var Q12;
            Q12=makeQuery(id+"F3.opExtrude","CAP_EDGE",EDGE,{"disambiguationData":[OSD([sQuery(id+"F2.wireOp",EDGE,"E2.8.0.3")])],"isStart":false});
            var Q13;
            Q13=makeQuery(id+"F3.opExtrude","CAP_EDGE",EDGE,{"disambiguationData":[OSD([sQuery(id+"F2.wireOp",EDGE,"E2.14.0.3")])],"isStart":false});
            var Q14;
            Q14=makeQuery(id+"F3.opExtrude","CAP_EDGE",EDGE,{"disambiguationData":[OSD([sQuery(id+"F2.wireOp",EDGE,"E2.2.0.3")])],"isStart":false});
            var Q15;
            Q15=makeQuery(id+"F3.opExtrude","CAP_EDGE",EDGE,{"disambiguationData":[OSD([sQuery(id+"F2.wireOp",EDGE,"E3.9.21.0")])],"isStart":false});
            var Q16;
            Q16=makeQuery(id+"F3.opExtrude","CAP_EDGE",EDGE,{"disambiguationData":[OSD([sQuery(id+"F2.wireOp",EDGE,"E3.9.28.0")])],"isStart":false});
            var Q17;
            Q17=makeQuery(id+"F3.opExtrude","CAP_EDGE",EDGE,{"disambiguationData":[OSD([sQuery(id+"F2.wireOp",EDGE,"E2.15.0.3")])],"isStart":false});
            var Q18;
            Q18=makeQuery(id+"F3.opExtrude","CAP_EDGE",EDGE,{"disambiguationData":[OSD([sQuery(id+"F2.wireOp",EDGE,"E2.10.0.3")])],"isStart":false});
            var Q19;
            Q19=makeQuery(id+"F3.opExtrude","CAP_EDGE",EDGE,{"disambiguationData":[OSD([sQuery(id+"F2.wireOp",EDGE,"E3.9.29.0")])],"isStart":false});
            var Q20;
            Q20=makeQuery(id+"F3.opExtrude","CAP_EDGE",EDGE,{"disambiguationData":[OSD([sQuery(id+"F2.wireOp",EDGE,"E3.9.23.0")])],"isStart":false});
            var Q21;
            Q21=makeQuery(id+"F3.opExtrude","CAP_EDGE",EDGE,{"disambiguationData":[OSD([sQuery(id+"F2.wireOp",EDGE,"E2.17.0.3")])],"isStart":false});
            var Q22;
            Q22=makeQuery(id+"F3.opExtrude","CAP_EDGE",EDGE,{"disambiguationData":[OSD([sQuery(id+"F2.wireOp",EDGE,"E3.9.24.0")])],"isStart":false});
            var Q23;
            Q23=makeQuery(id+"F3.opExtrude","CAP_EDGE",EDGE,{"disambiguationData":[OSD([sQuery(id+"F2.wireOp",EDGE,"E2.11.0.3")])],"isStart":false});
            var Q24;
            Q24=makeQuery(id+"F3.opExtrude","CAP_EDGE",EDGE,{"disambiguationData":[OSD([sQuery(id+"F2.wireOp",EDGE,"E2.18.0.3")])],"isStart":false});
            var Q25;
            Q25=makeQuery(id+"F3.opExtrude","CAP_EDGE",EDGE,{"disambiguationData":[OSD([sQuery(id+"F2.wireOp",EDGE,"E2.5.0.3")])],"isStart":false});
            var Q26;
            Q26=makeQuery(id+"F3.opExtrude","CAP_EDGE",EDGE,{"disambiguationData":[OSD([sQuery(id+"F2.wireOp",EDGE,"E2.12.0.3")])],"isStart":false});
            var Q27;
            Q27=makeQuery(id+"F3.opExtrude","CAP_EDGE",EDGE,{"disambiguationData":[OSD([sQuery(id+"F2.wireOp",EDGE,"E2.6.0.3")])],"isStart":false});
            var Q28;
            Q28=makeQuery(id+"F3.opExtrude","CAP_EDGE",EDGE,{"disambiguationData":[OSD([sQuery(id+"F2.wireOp",EDGE,"E3.9.25.0")])],"isStart":false});
            var Q29;
            Q29=makeQuery(id+"F3.opExtrude","CAP_EDGE",EDGE,{"disambiguationData":[OSD([sQuery(id+"F2.wireOp",EDGE,"E2.4.0.0")])],"isStart":false});
            var Q30;
            Q30=makeQuery(id+"F3.opExtrude","CAP_EDGE",EDGE,{"disambiguationData":[OSD([sQuery(id+"F2.wireOp",EDGE,"E2.3.0.0")])],"isStart":false});
            var Q31;
            Q31=makeQuery(id+"F3.opExtrude","CAP_EDGE",EDGE,{"disambiguationData":[OSD([sQuery(id+"F2.wireOp",EDGE,"E3.0.29.0")])],"isStart":false});
            var Q32;
            Q32=makeQuery(id+"F3.opExtrude","CAP_EDGE",EDGE,{"disambiguationData":[OSD([sQuery(id+"F2.wireOp",EDGE,"E2.16.0.0")])],"isStart":false});
            var Q33;
            Q33=makeQuery(id+"F3.opExtrude","CAP_EDGE",EDGE,{"disambiguationData":[OSD([sQuery(id+"F2.wireOp",EDGE,"E3.0.23.0")])],"isStart":false});
            var Q34;
            Q34=makeQuery(id+"F3.opExtrude","CAP_EDGE",EDGE,{"disambiguationData":[OSD([sQuery(id+"F2.wireOp",EDGE,"E2.10.0.0")])],"isStart":false});
            var Q35;
            Q35=makeQuery(id+"F3.opExtrude","CAP_EDGE",EDGE,{"disambiguationData":[OSD([sQuery(id+"F2.wireOp",EDGE,"E3.9.22.0")])],"isStart":false});
            var Q36;
            Q36=makeQuery(id+"F3.opExtrude","CAP_EDGE",EDGE,{"disambiguationData":[OSD([sQuery(id+"F2.wireOp",EDGE,"E2.9.0.3")])],"isStart":false});
            var Q37;
            Q37=makeQuery(id+"F3.opExtrude","CAP_EDGE",EDGE,{"disambiguationData":[OSD([sQuery(id+"F2.wireOp",EDGE,"E3.0.26.0")])],"isStart":false});
            var Q38;
            Q38=makeQuery(id+"F3.opExtrude","CAP_EDGE",EDGE,{"disambiguationData":[OSD([sQuery(id+"F2.wireOp",EDGE,"E3.0.20.0")])],"isStart":false});
            var Q39;
            Q39=makeQuery(id+"F3.opExtrude","CAP_EDGE",EDGE,{"disambiguationData":[OSD([sQuery(id+"F2.wireOp",EDGE,"E2.7.0.0")])],"isStart":false});
            var Q40;
            Q40=makeQuery(id+"F3.opExtrude","CAP_EDGE",EDGE,{"disambiguationData":[OSD([sQuery(id+"F2.wireOp",EDGE,"E2.14.0.0")])],"isStart":false});
            var Q41;
            Q41=makeQuery(id+"F3.opExtrude","CAP_EDGE",EDGE,{"disambiguationData":[OSD([sQuery(id+"F2.wireOp",EDGE,"E2.1.0.0")])],"isStart":false});
            var Q42;
            Q42=makeQuery(id+"F3.opExtrude","CAP_EDGE",EDGE,{"disambiguationData":[OSD([sQuery(id+"F2.wireOp",EDGE,"E2.8.0.0")])],"isStart":false});
            var Q43;
            Q43=makeQuery(id+"F3.opExtrude","CAP_EDGE",EDGE,{"disambiguationData":[OSD([sQuery(id+"F2.wireOp",EDGE,"E3.0.27.0")])],"isStart":false});
            var Q44;
            Q44=makeQuery(id+"F3.opExtrude","CAP_EDGE",EDGE,{"disambiguationData":[OSD([sQuery(id+"F2.wireOp",EDGE,"E2.2.0.0")])],"isStart":false});
            var Q45;
            Q45=makeQuery(id+"F3.opExtrude","CAP_EDGE",EDGE,{"disambiguationData":[OSD([sQuery(id+"F2.wireOp",EDGE,"E3.0.21.0")])],"isStart":false});
            var Q46;
            Q46=makeQuery(id+"F3.opExtrude","CAP_EDGE",EDGE,{"disambiguationData":[OSD([sQuery(id+"F2.wireOp",EDGE,"E3.0.28.0")])],"isStart":false});
            var Q47;
            Q47=makeQuery(id+"F3.opExtrude","CAP_EDGE",EDGE,{"disambiguationData":[OSD([sQuery(id+"F2.wireOp",EDGE,"E2.15.0.0")])],"isStart":false});
            var Q48;
            Q48=makeQuery(id+"F3.opExtrude","CAP_EDGE",EDGE,{"disambiguationData":[OSD([sQuery(id+"F2.wireOp",EDGE,"E3.0.22.0")])],"isStart":false});
            var Q49;
            Q49=makeQuery(id+"F3.opExtrude","CAP_EDGE",EDGE,{"disambiguationData":[OSD([sQuery(id+"F2.wireOp",EDGE,"E2.9.0.0")])],"isStart":false});
            var Q50;
            Q50=makeQuery(id+"F3.opExtrude","CAP_EDGE",EDGE,{"disambiguationData":[OSD([sQuery(id+"F2.wireOp",EDGE,"E2.17.0.0")])],"isStart":false});
            var Q51;
            Q51=makeQuery(id+"F3.opExtrude","CAP_EDGE",EDGE,{"disambiguationData":[OSD([sQuery(id+"F2.wireOp",EDGE,"E3.0.24.0")])],"isStart":false});
            var Q52;
            Q52=makeQuery(id+"F3.opExtrude","CAP_EDGE",EDGE,{"disambiguationData":[OSD([sQuery(id+"F2.wireOp",EDGE,"E2.11.0.0")])],"isStart":false});
            var Q53;
            Q53=makeQuery(id+"F3.opExtrude","CAP_EDGE",EDGE,{"disambiguationData":[OSD([sQuery(id+"F2.wireOp",EDGE,"E2.18.0.0")])],"isStart":false});
            var Q54;
            Q54=makeQuery(id+"F3.opExtrude","CAP_EDGE",EDGE,{"disambiguationData":[OSD([sQuery(id+"F2.wireOp",EDGE,"E2.5.0.0")])],"isStart":false});
            var Q55;
            Q55=makeQuery(id+"F3.opExtrude","CAP_EDGE",EDGE,{"disambiguationData":[OSD([sQuery(id+"F2.wireOp",EDGE,"E3.0.25.0")])],"isStart":false});
            var Q56;
            Q56=makeQuery(id+"F3.opExtrude","CAP_EDGE",EDGE,{"disambiguationData":[OSD([sQuery(id+"F2.wireOp",EDGE,"E2.12.0.0")])],"isStart":false});
            var Q57;
            Q57=makeQuery(id+"F3.opExtrude","CAP_EDGE",EDGE,{"disambiguationData":[OSD([sQuery(id+"F2.wireOp",EDGE,"E2.19.0.0")])],"isStart":false});
            var Q58;
            Q58=makeQuery(id+"F3.opExtrude","CAP_EDGE",EDGE,{"disambiguationData":[OSD([sQuery(id+"F2.wireOp",EDGE,"E2.6.0.0")])],"isStart":false});
            var Q59;
            Q59=makeQuery(id+"F3.opExtrude","CAP_EDGE",EDGE,{"disambiguationData":[OSD([sQuery(id+"F2.wireOp",EDGE,"E2.13.0.0")])],"isStart":false});
            var Q60;
            Q60=makeQuery(id+"F3.opExtrude","CAP_EDGE",EDGE,{"disambiguationData":[OSD([sQuery(id+"F2.wireOp",EDGE,"E1.top")])],"isStart":false});
            var Q61;
            Q61=makeQuery(id+"F3.opExtrude","CAP_EDGE",EDGE,{"disambiguationData":[OSD([sQuery(id+"F2.wireOp",EDGE,"E3.6.23.0")])],"isStart":false});
            var Q62;
            Q62=makeQuery(id+"F3.opExtrude","CAP_EDGE",EDGE,{"disambiguationData":[OSD([sQuery(id+"F2.wireOp",EDGE,"E2.17.0.2")])],"isStart":false});
            var Q63;
            Q63=makeQuery(id+"F3.opExtrude","CAP_EDGE",EDGE,{"disambiguationData":[OSD([sQuery(id+"F2.wireOp",EDGE,"E3.6.24.0")])],"isStart":false});
            var Q64;
            Q64=makeQuery(id+"F3.opExtrude","CAP_EDGE",EDGE,{"disambiguationData":[OSD([sQuery(id+"F2.wireOp",EDGE,"E2.11.0.2")])],"isStart":false});
            var Q65;
            Q65=makeQuery(id+"F3.opExtrude","CAP_EDGE",EDGE,{"disambiguationData":[OSD([sQuery(id+"F2.wireOp",EDGE,"E2.18.0.2")])],"isStart":false});
            var Q66;
            Q66=makeQuery(id+"F3.opExtrude","CAP_EDGE",EDGE,{"disambiguationData":[OSD([sQuery(id+"F2.wireOp",EDGE,"E2.5.0.2")])],"isStart":false});
            var Q67;
            Q67=makeQuery(id+"F3.opExtrude","CAP_EDGE",EDGE,{"disambiguationData":[OSD([sQuery(id+"F2.wireOp",EDGE,"E2.12.0.2")])],"isStart":false});
            var Q68;
            Q68=makeQuery(id+"F3.opExtrude","CAP_EDGE",EDGE,{"disambiguationData":[OSD([sQuery(id+"F2.wireOp",EDGE,"E2.6.0.2")])],"isStart":false});
            var Q69;
            Q69=makeQuery(id+"F3.opExtrude","CAP_EDGE",EDGE,{"disambiguationData":[OSD([sQuery(id+"F2.wireOp",EDGE,"E3.6.25.0")])],"isStart":false});
            var Q70;
            Q70=makeQuery(id+"F3.opExtrude","CAP_EDGE",EDGE,{"disambiguationData":[OSD([sQuery(id+"F2.wireOp",EDGE,"E1.left")])],"isStart":false});
            var Q71;
            Q71=makeQuery(id+"F3.opExtrude","CAP_EDGE",EDGE,{"disambiguationData":[OSD([sQuery(id+"F2.wireOp",EDGE,"E2.19.0.2")])],"isStart":false});
            var Q72;
            Q72=makeQuery(id+"F3.opExtrude","CAP_EDGE",EDGE,{"disambiguationData":[OSD([sQuery(id+"F2.wireOp",EDGE,"E2.4.0.2")])],"isStart":false});
            var Q73;
            Q73=makeQuery(id+"F3.opExtrude","CAP_EDGE",EDGE,{"disambiguationData":[OSD([sQuery(id+"F2.wireOp",EDGE,"E2.16.0.2")])],"isStart":false});
            var Q74;
            Q74=makeQuery(id+"F3.opExtrude","CAP_EDGE",EDGE,{"disambiguationData":[OSD([sQuery(id+"F2.wireOp",EDGE,"E2.3.0.2")])],"isStart":false});
            var Q75;
            Q75=makeQuery(id+"F3.opExtrude","CAP_EDGE",EDGE,{"disambiguationData":[OSD([sQuery(id+"F2.wireOp",EDGE,"E2.10.0.2")])],"isStart":false});
            var Q76;
            Q76=makeQuery(id+"F3.opExtrude","CAP_EDGE",EDGE,{"disambiguationData":[OSD([sQuery(id+"F2.wireOp",EDGE,"E3.6.29.0")])],"isStart":false});
            var Q77;
            Q77=makeQuery(id+"F3.opExtrude","CAP_EDGE",EDGE,{"disambiguationData":[OSD([sQuery(id+"F2.wireOp",EDGE,"E2.13.0.2")])],"isStart":false});
            var Q78;
            Q78=makeQuery(id+"F3.opExtrude","CAP_EDGE",EDGE,{"disambiguationData":[OSD([sQuery(id+"F2.wireOp",EDGE,"E3.6.26.0")])],"isStart":false});
            var Q79;
            Q79=makeQuery(id+"F3.opExtrude","CAP_EDGE",EDGE,{"disambiguationData":[OSD([sQuery(id+"F2.wireOp",EDGE,"E3.6.20.0")])],"isStart":false});
            var Q80;
            Q80=makeQuery(id+"F3.opExtrude","CAP_EDGE",EDGE,{"disambiguationData":[OSD([sQuery(id+"F2.wireOp",EDGE,"E2.7.0.2")])],"isStart":false});
            var Q81;
            Q81=makeQuery(id+"F3.opExtrude","CAP_EDGE",EDGE,{"disambiguationData":[OSD([sQuery(id+"F2.wireOp",EDGE,"E2.14.0.2")])],"isStart":false});
            var Q82;
            Q82=makeQuery(id+"F3.opExtrude","CAP_EDGE",EDGE,{"disambiguationData":[OSD([sQuery(id+"F2.wireOp",EDGE,"E2.1.0.2")])],"isStart":false});
            var Q83;
            Q83=makeQuery(id+"F3.opExtrude","CAP_EDGE",EDGE,{"disambiguationData":[OSD([sQuery(id+"F2.wireOp",EDGE,"E2.8.0.2")])],"isStart":false});
            var Q84;
            Q84=makeQuery(id+"F3.opExtrude","CAP_EDGE",EDGE,{"disambiguationData":[OSD([sQuery(id+"F2.wireOp",EDGE,"E3.6.27.0")])],"isStart":false});
            var Q85;
            Q85=makeQuery(id+"F3.opExtrude","CAP_EDGE",EDGE,{"disambiguationData":[OSD([sQuery(id+"F2.wireOp",EDGE,"E2.2.0.2")])],"isStart":false});
            var Q86;
            Q86=makeQuery(id+"F3.opExtrude","CAP_EDGE",EDGE,{"disambiguationData":[OSD([sQuery(id+"F2.wireOp",EDGE,"E3.6.21.0")])],"isStart":false});
            var Q87;
            Q87=makeQuery(id+"F3.opExtrude","CAP_EDGE",EDGE,{"disambiguationData":[OSD([sQuery(id+"F2.wireOp",EDGE,"E3.6.28.0")])],"isStart":false});
            var Q88;
            Q88=makeQuery(id+"F3.opExtrude","CAP_EDGE",EDGE,{"disambiguationData":[OSD([sQuery(id+"F2.wireOp",EDGE,"E2.15.0.2")])],"isStart":false});
            var Q89;
            Q89=makeQuery(id+"F3.opExtrude","CAP_EDGE",EDGE,{"disambiguationData":[OSD([sQuery(id+"F2.wireOp",EDGE,"E3.6.22.0")])],"isStart":false});
            var Q90;
            Q90=makeQuery(id+"F3.opExtrude","CAP_EDGE",EDGE,{"disambiguationData":[OSD([sQuery(id+"F2.wireOp",EDGE,"E2.9.0.2")])],"isStart":false});
            var Q91;
            Q91=makeQuery(id+"F3.opExtrude","CAP_EDGE",EDGE,{"disambiguationData":[OSD([sQuery(id+"F2.wireOp",EDGE,"E2.4.0.1")])],"isStart":false});
            var Q92;
            Q92=makeQuery(id+"F3.opExtrude","CAP_EDGE",EDGE,{"disambiguationData":[OSD([sQuery(id+"F2.wireOp",EDGE,"E2.16.0.1")])],"isStart":false});
            var Q93;
            Q93=makeQuery(id+"F3.opExtrude","CAP_EDGE",EDGE,{"disambiguationData":[OSD([sQuery(id+"F2.wireOp",EDGE,"E2.3.0.1")])],"isStart":false});
            var Q94;
            Q94=makeQuery(id+"F3.opExtrude","CAP_EDGE",EDGE,{"disambiguationData":[OSD([sQuery(id+"F2.wireOp",EDGE,"E3.3.23.0")])],"isStart":false});
            var Q95;
            Q95=makeQuery(id+"F3.opExtrude","CAP_EDGE",EDGE,{"disambiguationData":[OSD([sQuery(id+"F2.wireOp",EDGE,"E3.3.29.0")])],"isStart":false});
            var Q96;
            Q96=makeQuery(id+"F3.opExtrude","CAP_EDGE",EDGE,{"disambiguationData":[OSD([sQuery(id+"F2.wireOp",EDGE,"E2.10.0.1")])],"isStart":false});
            var Q97;
            Q97=makeQuery(id+"F3.opExtrude","CAP_EDGE",EDGE,{"disambiguationData":[OSD([sQuery(id+"F2.wireOp",EDGE,"E2.17.0.1")])],"isStart":false});
            var Q98;
            Q98=makeQuery(id+"F3.opExtrude","CAP_EDGE",EDGE,{"disambiguationData":[OSD([sQuery(id+"F2.wireOp",EDGE,"E3.3.24.0")])],"isStart":false});
            var Q99;
            Q99=makeQuery(id+"F3.opExtrude","CAP_EDGE",EDGE,{"disambiguationData":[OSD([sQuery(id+"F2.wireOp",EDGE,"E2.11.0.1")])],"isStart":false});
            var Q100;
            Q100=makeQuery(id+"F3.opExtrude","CAP_EDGE",EDGE,{"disambiguationData":[OSD([sQuery(id+"F2.wireOp",EDGE,"E2.8.0.1")])],"isStart":false});
            var Q101;
            Q101=makeQuery(id+"F3.opExtrude","CAP_EDGE",EDGE,{"disambiguationData":[OSD([sQuery(id+"F2.wireOp",EDGE,"E3.3.27.0")])],"isStart":false});
            var Q102;
            Q102=makeQuery(id+"F3.opExtrude","CAP_EDGE",EDGE,{"disambiguationData":[OSD([sQuery(id+"F2.wireOp",EDGE,"E2.2.0.1")])],"isStart":false});
            var Q103;
            Q103=makeQuery(id+"F3.opExtrude","CAP_EDGE",EDGE,{"disambiguationData":[OSD([sQuery(id+"F2.wireOp",EDGE,"E3.3.21.0")])],"isStart":false});
            var Q104;
            Q104=makeQuery(id+"F3.opExtrude","CAP_EDGE",EDGE,{"disambiguationData":[OSD([sQuery(id+"F2.wireOp",EDGE,"E3.3.28.0")])],"isStart":false});
            var Q105;
            Q105=makeQuery(id+"F3.opExtrude","CAP_EDGE",EDGE,{"disambiguationData":[OSD([sQuery(id+"F2.wireOp",EDGE,"E2.15.0.1")])],"isStart":false});
            var Q106;
            Q106=makeQuery(id+"F3.opExtrude","CAP_EDGE",EDGE,{"disambiguationData":[OSD([sQuery(id+"F2.wireOp",EDGE,"E3.3.22.0")])],"isStart":false});
            var Q107;
            Q107=makeQuery(id+"F3.opExtrude","CAP_EDGE",EDGE,{"disambiguationData":[OSD([sQuery(id+"F2.wireOp",EDGE,"E2.9.0.1")])],"isStart":false});
            var Q108;
            Q108=makeQuery(id+"F3.opExtrude","CAP_EDGE",EDGE,{"disambiguationData":[OSD([sQuery(id+"F2.wireOp",EDGE,"E2.18.0.1")])],"isStart":false});
            var Q109;
            Q109=makeQuery(id+"F3.opExtrude","CAP_EDGE",EDGE,{"disambiguationData":[OSD([sQuery(id+"F2.wireOp",EDGE,"E2.5.0.1")])],"isStart":false});
            var Q110;
            Q110=makeQuery(id+"F3.opExtrude","CAP_EDGE",EDGE,{"disambiguationData":[OSD([sQuery(id+"F2.wireOp",EDGE,"E2.12.0.1")])],"isStart":false});
            var Q111;
            Q111=makeQuery(id+"F3.opExtrude","CAP_EDGE",EDGE,{"disambiguationData":[OSD([sQuery(id+"F2.wireOp",EDGE,"E2.6.0.1")])],"isStart":false});
            var Q112;
            Q112=makeQuery(id+"F3.opExtrude","CAP_EDGE",EDGE,{"disambiguationData":[OSD([sQuery(id+"F2.wireOp",EDGE,"E3.3.25.0")])],"isStart":false});
            var Q113;
            Q113=makeQuery(id+"F3.opExtrude","CAP_EDGE",EDGE,{"disambiguationData":[OSD([sQuery(id+"F2.wireOp",EDGE,"E2.13.0.1")])],"isStart":false});
            var Q114;
            Q114=makeQuery(id+"F3.opExtrude","CAP_EDGE",EDGE,{"disambiguationData":[OSD([sQuery(id+"F2.wireOp",EDGE,"E2.19.0.1")])],"isStart":false});
            var Q115;
            Q115=makeQuery(id+"F3.opExtrude","CAP_EDGE",EDGE,{"disambiguationData":[OSD([sQuery(id+"F2.wireOp",EDGE,"E3.3.26.0")])],"isStart":false});
            var Q116;
            Q116=makeQuery(id+"F3.opExtrude","CAP_EDGE",EDGE,{"disambiguationData":[OSD([sQuery(id+"F2.wireOp",EDGE,"E3.3.20.0")])],"isStart":false});
            var Q117;
            Q117=makeQuery(id+"F3.opExtrude","CAP_EDGE",EDGE,{"disambiguationData":[OSD([sQuery(id+"F2.wireOp",EDGE,"E2.7.0.1")])],"isStart":false});
            var Q118;
            Q118=makeQuery(id+"F3.opExtrude","CAP_EDGE",EDGE,{"disambiguationData":[OSD([sQuery(id+"F2.wireOp",EDGE,"E2.14.0.1")])],"isStart":false});
            var Q119;
            Q119=makeQuery(id+"F3.opExtrude","CAP_EDGE",EDGE,{"disambiguationData":[OSD([sQuery(id+"F2.wireOp",EDGE,"E2.1.0.1")])],"isStart":false});
            var Q120;
            Q120=makeQuery(id+"F3.opExtrude","CAP_EDGE",EDGE,{"disambiguationData":[OSD([sQuery(id+"F2.wireOp",EDGE,"E2.0.1.0")])],"isStart":false});
            var Q121;
            Q121=makeQuery(id+"F3.opExtrude","CAP_EDGE",EDGE,{"disambiguationData":[OSD([sQuery(id+"F2.wireOp",EDGE,"E2.0.1.2")])],"isStart":false});
            var Q122;
            Q122=makeQuery(id+"F3.opExtrude","CAP_EDGE",EDGE,{"disambiguationData":[OSD([sQuery(id+"F2.wireOp",EDGE,"E2.4.1.0")])],"isStart":false});
            var Q123;
            Q123=makeQuery(id+"F3.opExtrude","CAP_EDGE",EDGE,{"disambiguationData":[OSD([sQuery(id+"F2.wireOp",EDGE,"E2.16.1.0")])],"isStart":false});
            var Q124;
            Q124=makeQuery(id+"F3.opExtrude","CAP_EDGE",EDGE,{"disambiguationData":[OSD([sQuery(id+"F2.wireOp",EDGE,"E2.3.1.0")])],"isStart":false});
            var Q125;
            Q125=makeQuery(id+"F3.opExtrude","CAP_EDGE",EDGE,{"disambiguationData":[OSD([sQuery(id+"F2.wireOp",EDGE,"E2.10.1.0")])],"isStart":false});
            var Q126;
            Q126=makeQuery(id+"F3.opExtrude","CAP_EDGE",EDGE,{"disambiguationData":[OSD([sQuery(id+"F2.wireOp",EDGE,"E3.0.29.1")])],"isStart":false});
            var Q127;
            Q127=makeQuery(id+"F3.opExtrude","CAP_EDGE",EDGE,{"disambiguationData":[OSD([sQuery(id+"F2.wireOp",EDGE,"E3.0.23.1")])],"isStart":false});
            var Q128;
            Q128=makeQuery(id+"F3.opExtrude","CAP_EDGE",EDGE,{"disambiguationData":[OSD([sQuery(id+"F2.wireOp",EDGE,"E2.17.1.0")])],"isStart":false});
            var Q129;
            Q129=makeQuery(id+"F3.opExtrude","CAP_EDGE",EDGE,{"disambiguationData":[OSD([sQuery(id+"F2.wireOp",EDGE,"E2.1.1.0")])],"isStart":false});
            var Q130;
            Q130=makeQuery(id+"F3.opExtrude","CAP_EDGE",EDGE,{"disambiguationData":[OSD([sQuery(id+"F2.wireOp",EDGE,"E3.0.20.1")])],"isStart":false});
            var Q131;
            Q131=makeQuery(id+"F3.opExtrude","CAP_EDGE",EDGE,{"disambiguationData":[OSD([sQuery(id+"F2.wireOp",EDGE,"E3.0.27.1")])],"isStart":false});
            var Q132;
            Q132=makeQuery(id+"F3.opExtrude","CAP_EDGE",EDGE,{"disambiguationData":[OSD([sQuery(id+"F2.wireOp",EDGE,"E2.14.1.0")])],"isStart":false});
            var Q133;
            Q133=makeQuery(id+"F3.opExtrude","CAP_EDGE",EDGE,{"disambiguationData":[OSD([sQuery(id+"F2.wireOp",EDGE,"E3.0.21.1")])],"isStart":false});
            var Q134;
            Q134=makeQuery(id+"F3.opExtrude","CAP_EDGE",EDGE,{"disambiguationData":[OSD([sQuery(id+"F2.wireOp",EDGE,"E2.2.1.0")])],"isStart":false});
            var Q135;
            Q135=makeQuery(id+"F3.opExtrude","CAP_EDGE",EDGE,{"disambiguationData":[OSD([sQuery(id+"F2.wireOp",EDGE,"E2.8.1.0")])],"isStart":false});
            var Q136;
            Q136=makeQuery(id+"F3.opExtrude","CAP_EDGE",EDGE,{"disambiguationData":[OSD([sQuery(id+"F2.wireOp",EDGE,"E3.0.28.1")])],"isStart":false});
            var Q137;
            Q137=makeQuery(id+"F3.opExtrude","CAP_EDGE",EDGE,{"disambiguationData":[OSD([sQuery(id+"F2.wireOp",EDGE,"E2.15.1.0")])],"isStart":false});
            var Q138;
            Q138=makeQuery(id+"F3.opExtrude","CAP_EDGE",EDGE,{"disambiguationData":[OSD([sQuery(id+"F2.wireOp",EDGE,"E3.0.22.1")])],"isStart":false});
            var Q139;
            Q139=makeQuery(id+"F3.opExtrude","CAP_EDGE",EDGE,{"disambiguationData":[OSD([sQuery(id+"F2.wireOp",EDGE,"E2.9.1.0")])],"isStart":false});
            var Q140;
            Q140=makeQuery(id+"F3.opExtrude","CAP_EDGE",EDGE,{"disambiguationData":[OSD([sQuery(id+"F2.wireOp",EDGE,"E3.0.24.1")])],"isStart":false});
            var Q141;
            Q141=makeQuery(id+"F3.opExtrude","CAP_EDGE",EDGE,{"disambiguationData":[OSD([sQuery(id+"F2.wireOp",EDGE,"E2.11.1.0")])],"isStart":false});
            var Q142;
            Q142=makeQuery(id+"F3.opExtrude","CAP_EDGE",EDGE,{"disambiguationData":[OSD([sQuery(id+"F2.wireOp",EDGE,"E2.18.1.0")])],"isStart":false});
            var Q143;
            Q143=makeQuery(id+"F3.opExtrude","CAP_EDGE",EDGE,{"disambiguationData":[OSD([sQuery(id+"F2.wireOp",EDGE,"E2.5.1.0")])],"isStart":false});
            var Q144;
            Q144=makeQuery(id+"F3.opExtrude","CAP_EDGE",EDGE,{"disambiguationData":[OSD([sQuery(id+"F2.wireOp",EDGE,"E2.12.1.0")])],"isStart":false});
            var Q145;
            Q145=makeQuery(id+"F3.opExtrude","CAP_EDGE",EDGE,{"disambiguationData":[OSD([sQuery(id+"F2.wireOp",EDGE,"E2.6.1.0")])],"isStart":false});
            var Q146;
            Q146=makeQuery(id+"F3.opExtrude","CAP_EDGE",EDGE,{"disambiguationData":[OSD([sQuery(id+"F2.wireOp",EDGE,"E3.0.25.1")])],"isStart":false});
            var Q147;
            Q147=makeQuery(id+"F3.opExtrude","CAP_EDGE",EDGE,{"disambiguationData":[OSD([sQuery(id+"F2.wireOp",EDGE,"E2.19.1.0")])],"isStart":false});
            var Q148;
            Q148=makeQuery(id+"F3.opExtrude","CAP_EDGE",EDGE,{"disambiguationData":[OSD([sQuery(id+"F2.wireOp",EDGE,"E2.13.1.0")])],"isStart":false});
            var Q149;
            Q149=makeQuery(id+"F3.opExtrude","CAP_EDGE",EDGE,{"disambiguationData":[OSD([sQuery(id+"F2.wireOp",EDGE,"E2.7.1.0")])],"isStart":false});
            var Q150;
            Q150=makeQuery(id+"F3.opExtrude","CAP_EDGE",EDGE,{"disambiguationData":[OSD([sQuery(id+"F2.wireOp",EDGE,"E3.0.26.1")])],"isStart":false});
            var Q151;
            Q151=makeQuery(id+"F3.opExtrude","CAP_EDGE",EDGE,{"disambiguationData":[OSD([sQuery(id+"F2.wireOp",EDGE,"E2.4.1.2")])],"isStart":false});
            var Q152;
            Q152=makeQuery(id+"F3.opExtrude","CAP_EDGE",EDGE,{"disambiguationData":[OSD([sQuery(id+"F2.wireOp",EDGE,"E2.6.1.2")])],"isStart":false});
            var Q153;
            Q153=makeQuery(id+"F3.opExtrude","CAP_EDGE",EDGE,{"disambiguationData":[OSD([sQuery(id+"F2.wireOp",EDGE,"E3.6.25.1")])],"isStart":false});
            var Q154;
            Q154=makeQuery(id+"F3.opExtrude","CAP_EDGE",EDGE,{"disambiguationData":[OSD([sQuery(id+"F2.wireOp",EDGE,"E2.19.1.2")])],"isStart":false});
            var Q155;
            Q155=makeQuery(id+"F3.opExtrude","CAP_EDGE",EDGE,{"disambiguationData":[OSD([sQuery(id+"F2.wireOp",EDGE,"E2.13.1.2")])],"isStart":false});
            var Q156;
            Q156=makeQuery(id+"F3.opExtrude","CAP_EDGE",EDGE,{"disambiguationData":[OSD([sQuery(id+"F2.wireOp",EDGE,"E2.7.1.2")])],"isStart":false});
            var Q157;
            Q157=makeQuery(id+"F3.opExtrude","CAP_EDGE",EDGE,{"disambiguationData":[OSD([sQuery(id+"F2.wireOp",EDGE,"E3.6.26.1")])],"isStart":false});
            var Q158;
            Q158=makeQuery(id+"F3.opExtrude","CAP_EDGE",EDGE,{"disambiguationData":[OSD([sQuery(id+"F2.wireOp",EDGE,"E2.1.1.2")])],"isStart":false});
            var Q159;
            Q159=makeQuery(id+"F3.opExtrude","CAP_EDGE",EDGE,{"disambiguationData":[OSD([sQuery(id+"F2.wireOp",EDGE,"E3.6.20.1")])],"isStart":false});
            var Q160;
            Q160=makeQuery(id+"F3.opExtrude","CAP_EDGE",EDGE,{"disambiguationData":[OSD([sQuery(id+"F2.wireOp",EDGE,"E3.6.27.1")])],"isStart":false});
            var Q161;
            Q161=makeQuery(id+"F3.opExtrude","CAP_EDGE",EDGE,{"disambiguationData":[OSD([sQuery(id+"F2.wireOp",EDGE,"E2.14.1.2")])],"isStart":false});
            var Q162;
            Q162=makeQuery(id+"F3.opExtrude","CAP_EDGE",EDGE,{"disambiguationData":[OSD([sQuery(id+"F2.wireOp",EDGE,"E3.6.21.1")])],"isStart":false});
            var Q163;
            Q163=makeQuery(id+"F3.opExtrude","CAP_EDGE",EDGE,{"disambiguationData":[OSD([sQuery(id+"F2.wireOp",EDGE,"E2.8.1.2")])],"isStart":false});
            var Q164;
            Q164=makeQuery(id+"F3.opExtrude","CAP_EDGE",EDGE,{"disambiguationData":[OSD([sQuery(id+"F2.wireOp",EDGE,"E2.0.1.1")])],"isStart":false});
            var Q165;
            Q165=makeQuery(id+"F3.opExtrude","CAP_EDGE",EDGE,{"disambiguationData":[OSD([sQuery(id+"F2.wireOp",EDGE,"E2.16.1.2")])],"isStart":false});
            var Q166;
            Q166=makeQuery(id+"F3.opExtrude","CAP_EDGE",EDGE,{"disambiguationData":[OSD([sQuery(id+"F2.wireOp",EDGE,"E2.3.1.2")])],"isStart":false});
            var Q167;
            Q167=makeQuery(id+"F3.opExtrude","CAP_EDGE",EDGE,{"disambiguationData":[OSD([sQuery(id+"F2.wireOp",EDGE,"E2.10.1.2")])],"isStart":false});
            var Q168;
            Q168=makeQuery(id+"F3.opExtrude","CAP_EDGE",EDGE,{"disambiguationData":[OSD([sQuery(id+"F2.wireOp",EDGE,"E3.6.29.1")])],"isStart":false});
            var Q169;
            Q169=makeQuery(id+"F3.opExtrude","CAP_EDGE",EDGE,{"disambiguationData":[OSD([sQuery(id+"F2.wireOp",EDGE,"E3.6.23.1")])],"isStart":false});
            var Q170;
            Q170=makeQuery(id+"F3.opExtrude","CAP_EDGE",EDGE,{"disambiguationData":[OSD([sQuery(id+"F2.wireOp",EDGE,"E2.17.1.2")])],"isStart":false});
            var Q171;
            Q171=makeQuery(id+"F3.opExtrude","CAP_EDGE",EDGE,{"disambiguationData":[OSD([sQuery(id+"F2.wireOp",EDGE,"E3.6.24.1")])],"isStart":false});
            var Q172;
            Q172=makeQuery(id+"F3.opExtrude","CAP_EDGE",EDGE,{"disambiguationData":[OSD([sQuery(id+"F2.wireOp",EDGE,"E2.11.1.2")])],"isStart":false});
            var Q173;
            Q173=makeQuery(id+"F3.opExtrude","CAP_EDGE",EDGE,{"disambiguationData":[OSD([sQuery(id+"F2.wireOp",EDGE,"E2.18.1.2")])],"isStart":false});
            var Q174;
            Q174=makeQuery(id+"F3.opExtrude","CAP_EDGE",EDGE,{"disambiguationData":[OSD([sQuery(id+"F2.wireOp",EDGE,"E2.5.1.2")])],"isStart":false});
            var Q175;
            Q175=makeQuery(id+"F3.opExtrude","CAP_EDGE",EDGE,{"disambiguationData":[OSD([sQuery(id+"F2.wireOp",EDGE,"E2.12.1.2")])],"isStart":false});
            var Q176;
            Q176=makeQuery(id+"F3.opExtrude","CAP_EDGE",EDGE,{"disambiguationData":[OSD([sQuery(id+"F2.wireOp",EDGE,"E2.15.1.2")])],"isStart":false});
            var Q177;
            Q177=makeQuery(id+"F3.opExtrude","CAP_EDGE",EDGE,{"disambiguationData":[OSD([sQuery(id+"F2.wireOp",EDGE,"E2.2.1.2")])],"isStart":false});
            var Q178;
            Q178=makeQuery(id+"F3.opExtrude","CAP_EDGE",EDGE,{"disambiguationData":[OSD([sQuery(id+"F2.wireOp",EDGE,"E3.6.22.1")])],"isStart":false});
            var Q179;
            Q179=makeQuery(id+"F3.opExtrude","CAP_EDGE",EDGE,{"disambiguationData":[OSD([sQuery(id+"F2.wireOp",EDGE,"E3.6.28.1")])],"isStart":false});
            var Q180;
            Q180=makeQuery(id+"F3.opExtrude","CAP_EDGE",EDGE,{"disambiguationData":[OSD([sQuery(id+"F2.wireOp",EDGE,"E2.9.1.2")])],"isStart":false});
            var Q181;
            Q181=makeQuery(id+"F3.opExtrude","CAP_EDGE",EDGE,{"disambiguationData":[OSD([sQuery(id+"F2.wireOp",EDGE,"E2.0.1.3")])],"isStart":false});
            var Q182;
            Q182=makeQuery(id+"F3.opExtrude","CAP_EDGE",EDGE,{"disambiguationData":[OSD([sQuery(id+"F2.wireOp",EDGE,"E2.10.1.1")])],"isStart":false});
            var Q183;
            Q183=makeQuery(id+"F3.opExtrude","CAP_EDGE",EDGE,{"disambiguationData":[OSD([sQuery(id+"F2.wireOp",EDGE,"E3.3.29.1")])],"isStart":false});
            var Q184;
            Q184=makeQuery(id+"F3.opExtrude","CAP_EDGE",EDGE,{"disambiguationData":[OSD([sQuery(id+"F2.wireOp",EDGE,"E3.3.23.1")])],"isStart":false});
            var Q185;
            Q185=makeQuery(id+"F3.opExtrude","CAP_EDGE",EDGE,{"disambiguationData":[OSD([sQuery(id+"F2.wireOp",EDGE,"E2.17.1.1")])],"isStart":false});
            var Q186;
            Q186=makeQuery(id+"F3.opExtrude","CAP_EDGE",EDGE,{"disambiguationData":[OSD([sQuery(id+"F2.wireOp",EDGE,"E3.3.24.1")])],"isStart":false});
            var Q187;
            Q187=makeQuery(id+"F3.opExtrude","CAP_EDGE",EDGE,{"disambiguationData":[OSD([sQuery(id+"F2.wireOp",EDGE,"E2.11.1.1")])],"isStart":false});
            var Q188;
            Q188=makeQuery(id+"F3.opExtrude","CAP_EDGE",EDGE,{"disambiguationData":[OSD([sQuery(id+"F2.wireOp",EDGE,"E2.18.1.1")])],"isStart":false});
            var Q189;
            Q189=makeQuery(id+"F3.opExtrude","CAP_EDGE",EDGE,{"disambiguationData":[OSD([sQuery(id+"F2.wireOp",EDGE,"E2.5.1.1")])],"isStart":false});
            var Q190;
            Q190=makeQuery(id+"F3.opExtrude","CAP_EDGE",EDGE,{"disambiguationData":[OSD([sQuery(id+"F2.wireOp",EDGE,"E2.12.1.1")])],"isStart":false});
            var Q191;
            Q191=makeQuery(id+"F3.opExtrude","CAP_EDGE",EDGE,{"disambiguationData":[OSD([sQuery(id+"F2.wireOp",EDGE,"E2.6.1.1")])],"isStart":false});
            var Q192;
            Q192=makeQuery(id+"F3.opExtrude","CAP_EDGE",EDGE,{"disambiguationData":[OSD([sQuery(id+"F2.wireOp",EDGE,"E3.3.25.1")])],"isStart":false});
            var Q193;
            Q193=makeQuery(id+"F3.opExtrude","CAP_EDGE",EDGE,{"disambiguationData":[OSD([sQuery(id+"F2.wireOp",EDGE,"E2.4.1.1")])],"isStart":false});
            var Q194;
            Q194=makeQuery(id+"F3.opExtrude","CAP_EDGE",EDGE,{"disambiguationData":[OSD([sQuery(id+"F2.wireOp",EDGE,"E2.16.1.1")])],"isStart":false});
            var Q195;
            Q195=makeQuery(id+"F3.opExtrude","CAP_EDGE",EDGE,{"disambiguationData":[OSD([sQuery(id+"F2.wireOp",EDGE,"E2.3.1.1")])],"isStart":false});
            var Q196;
            Q196=makeQuery(id+"F3.opExtrude","CAP_EDGE",EDGE,{"disambiguationData":[OSD([sQuery(id+"F2.wireOp",EDGE,"E2.9.1.1")])],"isStart":false});
            var Q197;
            Q197=makeQuery(id+"F3.opExtrude","CAP_EDGE",EDGE,{"disambiguationData":[OSD([sQuery(id+"F2.wireOp",EDGE,"E3.3.28.1")])],"isStart":false});
            var Q198;
            Q198=makeQuery(id+"F3.opExtrude","CAP_EDGE",EDGE,{"disambiguationData":[OSD([sQuery(id+"F2.wireOp",EDGE,"E3.3.22.1")])],"isStart":false});
            var Q199;
            Q199=makeQuery(id+"F3.opExtrude","CAP_EDGE",EDGE,{"disambiguationData":[OSD([sQuery(id+"F2.wireOp",EDGE,"E2.19.1.1")])],"isStart":false});
            var Q200;
            Q200=makeQuery(id+"F3.opExtrude","CAP_EDGE",EDGE,{"disambiguationData":[OSD([sQuery(id+"F2.wireOp",EDGE,"E2.13.1.1")])],"isStart":false});
            var Q201;
            Q201=makeQuery(id+"F3.opExtrude","CAP_EDGE",EDGE,{"disambiguationData":[OSD([sQuery(id+"F2.wireOp",EDGE,"E2.7.1.1")])],"isStart":false});
            var Q202;
            Q202=makeQuery(id+"F3.opExtrude","CAP_EDGE",EDGE,{"disambiguationData":[OSD([sQuery(id+"F2.wireOp",EDGE,"E3.3.26.1")])],"isStart":false});
            var Q203;
            Q203=makeQuery(id+"F3.opExtrude","CAP_EDGE",EDGE,{"disambiguationData":[OSD([sQuery(id+"F2.wireOp",EDGE,"E2.1.1.1")])],"isStart":false});
            var Q204;
            Q204=makeQuery(id+"F3.opExtrude","CAP_EDGE",EDGE,{"disambiguationData":[OSD([sQuery(id+"F2.wireOp",EDGE,"E3.3.20.1")])],"isStart":false});
            var Q205;
            Q205=makeQuery(id+"F3.opExtrude","CAP_EDGE",EDGE,{"disambiguationData":[OSD([sQuery(id+"F2.wireOp",EDGE,"E3.3.27.1")])],"isStart":false});
            var Q206;
            Q206=makeQuery(id+"F3.opExtrude","CAP_EDGE",EDGE,{"disambiguationData":[OSD([sQuery(id+"F2.wireOp",EDGE,"E2.14.1.1")])],"isStart":false});
            var Q207;
            Q207=makeQuery(id+"F3.opExtrude","CAP_EDGE",EDGE,{"disambiguationData":[OSD([sQuery(id+"F2.wireOp",EDGE,"E3.3.21.1")])],"isStart":false});
            var Q208;
            Q208=makeQuery(id+"F3.opExtrude","CAP_EDGE",EDGE,{"disambiguationData":[OSD([sQuery(id+"F2.wireOp",EDGE,"E2.8.1.1")])],"isStart":false});
            var Q209;
            Q209=makeQuery(id+"F3.opExtrude","CAP_EDGE",EDGE,{"disambiguationData":[OSD([sQuery(id+"F2.wireOp",EDGE,"E2.15.1.1")])],"isStart":false});
            var Q210;
            Q210=makeQuery(id+"F3.opExtrude","CAP_EDGE",EDGE,{"disambiguationData":[OSD([sQuery(id+"F2.wireOp",EDGE,"E2.2.1.1")])],"isStart":false});
            var Q211;
            Q211=makeQuery(id+"F3.opExtrude","CAP_EDGE",EDGE,{"disambiguationData":[OSD([sQuery(id+"F2.wireOp",EDGE,"E2.4.1.3")])],"isStart":false});
            var Q212;
            Q212=makeQuery(id+"F3.opExtrude","CAP_EDGE",EDGE,{"disambiguationData":[OSD([sQuery(id+"F2.wireOp",EDGE,"E2.16.1.3")])],"isStart":false});
            var Q213;
            Q213=makeQuery(id+"F3.opExtrude","CAP_EDGE",EDGE,{"disambiguationData":[OSD([sQuery(id+"F2.wireOp",EDGE,"E2.3.1.3")])],"isStart":false});
            var Q214;
            Q214=makeQuery(id+"F3.opExtrude","CAP_EDGE",EDGE,{"disambiguationData":[OSD([sQuery(id+"F2.wireOp",EDGE,"E2.10.1.3")])],"isStart":false});
            var Q215;
            Q215=makeQuery(id+"F3.opExtrude","CAP_EDGE",EDGE,{"disambiguationData":[OSD([sQuery(id+"F2.wireOp",EDGE,"E3.9.29.1")])],"isStart":false});
            var Q216;
            Q216=makeQuery(id+"F3.opExtrude","CAP_EDGE",EDGE,{"disambiguationData":[OSD([sQuery(id+"F2.wireOp",EDGE,"E3.9.23.1")])],"isStart":false});
            var Q217;
            Q217=makeQuery(id+"F3.opExtrude","CAP_EDGE",EDGE,{"disambiguationData":[OSD([sQuery(id+"F2.wireOp",EDGE,"E2.7.1.3")])],"isStart":false});
            var Q218;
            Q218=makeQuery(id+"F3.opExtrude","CAP_EDGE",EDGE,{"disambiguationData":[OSD([sQuery(id+"F2.wireOp",EDGE,"E3.9.26.1")])],"isStart":false});
            var Q219;
            Q219=makeQuery(id+"F3.opExtrude","CAP_EDGE",EDGE,{"disambiguationData":[OSD([sQuery(id+"F2.wireOp",EDGE,"E2.1.1.3")])],"isStart":false});
            var Q220;
            Q220=makeQuery(id+"F3.opExtrude","CAP_EDGE",EDGE,{"disambiguationData":[OSD([sQuery(id+"F2.wireOp",EDGE,"E3.9.20.1")])],"isStart":false});
            var Q221;
            Q221=makeQuery(id+"F3.opExtrude","CAP_EDGE",EDGE,{"disambiguationData":[OSD([sQuery(id+"F2.wireOp",EDGE,"E3.9.27.1")])],"isStart":false});
            var Q222;
            Q222=makeQuery(id+"F3.opExtrude","CAP_EDGE",EDGE,{"disambiguationData":[OSD([sQuery(id+"F2.wireOp",EDGE,"E2.14.1.3")])],"isStart":false});
            var Q223;
            Q223=makeQuery(id+"F3.opExtrude","CAP_EDGE",EDGE,{"disambiguationData":[OSD([sQuery(id+"F2.wireOp",EDGE,"E3.9.21.1")])],"isStart":false});
            var Q224;
            Q224=makeQuery(id+"F3.opExtrude","CAP_EDGE",EDGE,{"disambiguationData":[OSD([sQuery(id+"F2.wireOp",EDGE,"E2.8.1.3")])],"isStart":false});
            var Q225;
            Q225=makeQuery(id+"F3.opExtrude","CAP_EDGE",EDGE,{"disambiguationData":[OSD([sQuery(id+"F2.wireOp",EDGE,"E2.15.1.3")])],"isStart":false});
            var Q226;
            Q226=makeQuery(id+"F3.opExtrude","CAP_EDGE",EDGE,{"disambiguationData":[OSD([sQuery(id+"F2.wireOp",EDGE,"E2.2.1.3")])],"isStart":false});
            var Q227;
            Q227=makeQuery(id+"F3.opExtrude","CAP_EDGE",EDGE,{"disambiguationData":[OSD([sQuery(id+"F2.wireOp",EDGE,"E2.9.1.3")])],"isStart":false});
            var Q228;
            Q228=makeQuery(id+"F3.opExtrude","CAP_EDGE",EDGE,{"disambiguationData":[OSD([sQuery(id+"F2.wireOp",EDGE,"E3.9.28.1")])],"isStart":false});
            var Q229;
            Q229=makeQuery(id+"F3.opExtrude","CAP_EDGE",EDGE,{"disambiguationData":[OSD([sQuery(id+"F2.wireOp",EDGE,"E3.9.22.1")])],"isStart":false});
            var Q230;
            Q230=makeQuery(id+"F3.opExtrude","CAP_EDGE",EDGE,{"disambiguationData":[OSD([sQuery(id+"F2.wireOp",EDGE,"E2.17.1.3")])],"isStart":false});
            var Q231;
            Q231=makeQuery(id+"F3.opExtrude","CAP_EDGE",EDGE,{"disambiguationData":[OSD([sQuery(id+"F2.wireOp",EDGE,"E3.9.24.1")])],"isStart":false});
            var Q232;
            Q232=makeQuery(id+"F3.opExtrude","CAP_EDGE",EDGE,{"disambiguationData":[OSD([sQuery(id+"F2.wireOp",EDGE,"E2.11.1.3")])],"isStart":false});
            var Q233;
            Q233=makeQuery(id+"F3.opExtrude","CAP_EDGE",EDGE,{"disambiguationData":[OSD([sQuery(id+"F2.wireOp",EDGE,"E2.18.1.3")])],"isStart":false});
            var Q234;
            Q234=makeQuery(id+"F3.opExtrude","CAP_EDGE",EDGE,{"disambiguationData":[OSD([sQuery(id+"F2.wireOp",EDGE,"E2.5.1.3")])],"isStart":false});
            var Q235;
            Q235=makeQuery(id+"F3.opExtrude","CAP_EDGE",EDGE,{"disambiguationData":[OSD([sQuery(id+"F2.wireOp",EDGE,"E2.12.1.3")])],"isStart":false});
            var Q236;
            Q236=makeQuery(id+"F3.opExtrude","CAP_EDGE",EDGE,{"disambiguationData":[OSD([sQuery(id+"F2.wireOp",EDGE,"E2.6.1.3")])],"isStart":false});
            var Q237;
            Q237=makeQuery(id+"F3.opExtrude","CAP_EDGE",EDGE,{"disambiguationData":[OSD([sQuery(id+"F2.wireOp",EDGE,"E3.9.25.1")])],"isStart":false});
            var Q238;
            Q238=makeQuery(id+"F3.opExtrude","CAP_EDGE",EDGE,{"disambiguationData":[OSD([sQuery(id+"F2.wireOp",EDGE,"E2.19.1.3")])],"isStart":false});
            var Q239;
            Q239=makeQuery(id+"F3.opExtrude","CAP_EDGE",EDGE,{"disambiguationData":[OSD([sQuery(id+"F2.wireOp",EDGE,"E2.13.1.3")])],"isStart":false});
            var Q240;
            Q240=makeQuery(id+"F3.opExtrude","CAP_EDGE",EDGE,{"disambiguationData":[OSD([sQuery(id+"F2.wireOp",EDGE,"E2.0.2.3")])],"isStart":false});
            var Q241;
            Q241=makeQuery(id+"F3.opExtrude","CAP_EDGE",EDGE,{"disambiguationData":[OSD([sQuery(id+"F2.wireOp",EDGE,"E2.0.2.0")])],"isStart":false});
            var Q242;
            Q242=makeQuery(id+"F3.opExtrude","CAP_EDGE",EDGE,{"disambiguationData":[OSD([sQuery(id+"F2.wireOp",EDGE,"E2.0.2.2")])],"isStart":false});
            var Q243;
            Q243=makeQuery(id+"F3.opExtrude","CAP_EDGE",EDGE,{"disambiguationData":[OSD([sQuery(id+"F2.wireOp",EDGE,"E2.4.2.3")])],"isStart":false});
            var Q244;
            Q244=makeQuery(id+"F3.opExtrude","CAP_EDGE",EDGE,{"disambiguationData":[OSD([sQuery(id+"F2.wireOp",EDGE,"E2.16.2.3")])],"isStart":false});
            var Q245;
            Q245=makeQuery(id+"F3.opExtrude","CAP_EDGE",EDGE,{"disambiguationData":[OSD([sQuery(id+"F2.wireOp",EDGE,"E2.3.2.3")])],"isStart":false});
            var Q246;
            Q246=makeQuery(id+"F3.opExtrude","CAP_EDGE",EDGE,{"disambiguationData":[OSD([sQuery(id+"F2.wireOp",EDGE,"E2.19.2.3")])],"isStart":false});
            var Q247;
            Q247=makeQuery(id+"F3.opExtrude","CAP_EDGE",EDGE,{"disambiguationData":[OSD([sQuery(id+"F2.wireOp",EDGE,"E2.13.2.3")])],"isStart":false});
            var Q248;
            Q248=makeQuery(id+"F3.opExtrude","CAP_EDGE",EDGE,{"disambiguationData":[OSD([sQuery(id+"F2.wireOp",EDGE,"E2.7.2.3")])],"isStart":false});
            var Q249;
            Q249=makeQuery(id+"F3.opExtrude","CAP_EDGE",EDGE,{"disambiguationData":[OSD([sQuery(id+"F2.wireOp",EDGE,"E3.9.26.2")])],"isStart":false});
            var Q250;
            Q250=makeQuery(id+"F3.opExtrude","CAP_EDGE",EDGE,{"disambiguationData":[OSD([sQuery(id+"F2.wireOp",EDGE,"E2.1.2.3")])],"isStart":false});
            var Q251;
            Q251=makeQuery(id+"F3.opExtrude","CAP_EDGE",EDGE,{"disambiguationData":[OSD([sQuery(id+"F2.wireOp",EDGE,"E3.9.20.2")])],"isStart":false});
            var Q252;
            Q252=makeQuery(id+"F3.opExtrude","CAP_EDGE",EDGE,{"disambiguationData":[OSD([sQuery(id+"F2.wireOp",EDGE,"E3.9.27.2")])],"isStart":false});
            var Q253;
            Q253=makeQuery(id+"F3.opExtrude","CAP_EDGE",EDGE,{"disambiguationData":[OSD([sQuery(id+"F2.wireOp",EDGE,"E2.14.2.3")])],"isStart":false});
            var Q254;
            Q254=makeQuery(id+"F3.opExtrude","CAP_EDGE",EDGE,{"disambiguationData":[OSD([sQuery(id+"F2.wireOp",EDGE,"E3.9.21.2")])],"isStart":false});
            var Q255;
            Q255=makeQuery(id+"F3.opExtrude","CAP_EDGE",EDGE,{"disambiguationData":[OSD([sQuery(id+"F2.wireOp",EDGE,"E2.8.2.3")])],"isStart":false});
            var Q256;
            Q256=makeQuery(id+"F3.opExtrude","CAP_EDGE",EDGE,{"disambiguationData":[OSD([sQuery(id+"F2.wireOp",EDGE,"E2.15.2.3")])],"isStart":false});
            var Q257;
            Q257=makeQuery(id+"F3.opExtrude","CAP_EDGE",EDGE,{"disambiguationData":[OSD([sQuery(id+"F2.wireOp",EDGE,"E2.2.2.3")])],"isStart":false});
            var Q258;
            Q258=makeQuery(id+"F3.opExtrude","CAP_EDGE",EDGE,{"disambiguationData":[OSD([sQuery(id+"F2.wireOp",EDGE,"E2.10.2.3")])],"isStart":false});
            var Q259;
            Q259=makeQuery(id+"F3.opExtrude","CAP_EDGE",EDGE,{"disambiguationData":[OSD([sQuery(id+"F2.wireOp",EDGE,"E3.9.29.2")])],"isStart":false});
            var Q260;
            Q260=makeQuery(id+"F3.opExtrude","CAP_EDGE",EDGE,{"disambiguationData":[OSD([sQuery(id+"F2.wireOp",EDGE,"E3.9.23.2")])],"isStart":false});
            var Q261;
            Q261=makeQuery(id+"F3.opExtrude","CAP_EDGE",EDGE,{"disambiguationData":[OSD([sQuery(id+"F2.wireOp",EDGE,"E2.17.2.3")])],"isStart":false});
            var Q262;
            Q262=makeQuery(id+"F3.opExtrude","CAP_EDGE",EDGE,{"disambiguationData":[OSD([sQuery(id+"F2.wireOp",EDGE,"E2.11.2.3")])],"isStart":false});
            var Q263;
            Q263=makeQuery(id+"F3.opExtrude","CAP_EDGE",EDGE,{"disambiguationData":[OSD([sQuery(id+"F2.wireOp",EDGE,"E2.18.2.3")])],"isStart":false});
            var Q264;
            Q264=makeQuery(id+"F3.opExtrude","CAP_EDGE",EDGE,{"disambiguationData":[OSD([sQuery(id+"F2.wireOp",EDGE,"E3.9.24.2")])],"isStart":false});
            var Q265;
            Q265=makeQuery(id+"F3.opExtrude","CAP_EDGE",EDGE,{"disambiguationData":[OSD([sQuery(id+"F2.wireOp",EDGE,"E2.5.2.3")])],"isStart":false});
            var Q266;
            Q266=makeQuery(id+"F3.opExtrude","CAP_EDGE",EDGE,{"disambiguationData":[OSD([sQuery(id+"F2.wireOp",EDGE,"E2.12.2.3")])],"isStart":false});
            var Q267;
            Q267=makeQuery(id+"F3.opExtrude","CAP_EDGE",EDGE,{"disambiguationData":[OSD([sQuery(id+"F2.wireOp",EDGE,"E2.6.2.3")])],"isStart":false});
            var Q268;
            Q268=makeQuery(id+"F3.opExtrude","CAP_EDGE",EDGE,{"disambiguationData":[OSD([sQuery(id+"F2.wireOp",EDGE,"E3.9.25.2")])],"isStart":false});
            var Q269;
            Q269=makeQuery(id+"F3.opExtrude","CAP_EDGE",EDGE,{"disambiguationData":[OSD([sQuery(id+"F2.wireOp",EDGE,"E2.4.2.0")])],"isStart":false});
            var Q270;
            Q270=makeQuery(id+"F3.opExtrude","CAP_EDGE",EDGE,{"disambiguationData":[OSD([sQuery(id+"F2.wireOp",EDGE,"E2.16.2.0")])],"isStart":false});
            var Q271;
            Q271=makeQuery(id+"F3.opExtrude","CAP_EDGE",EDGE,{"disambiguationData":[OSD([sQuery(id+"F2.wireOp",EDGE,"E2.3.2.0")])],"isStart":false});
            var Q272;
            Q272=makeQuery(id+"F3.opExtrude","CAP_EDGE",EDGE,{"disambiguationData":[OSD([sQuery(id+"F2.wireOp",EDGE,"E2.10.2.0")])],"isStart":false});
            var Q273;
            Q273=makeQuery(id+"F3.opExtrude","CAP_EDGE",EDGE,{"disambiguationData":[OSD([sQuery(id+"F2.wireOp",EDGE,"E3.0.29.2")])],"isStart":false});
            var Q274;
            Q274=makeQuery(id+"F3.opExtrude","CAP_EDGE",EDGE,{"disambiguationData":[OSD([sQuery(id+"F2.wireOp",EDGE,"E2.9.2.3")])],"isStart":false});
            var Q275;
            Q275=makeQuery(id+"F3.opExtrude","CAP_EDGE",EDGE,{"disambiguationData":[OSD([sQuery(id+"F2.wireOp",EDGE,"E3.9.28.2")])],"isStart":false});
            var Q276;
            Q276=makeQuery(id+"F3.opExtrude","CAP_EDGE",EDGE,{"disambiguationData":[OSD([sQuery(id+"F2.wireOp",EDGE,"E3.9.22.2")])],"isStart":false});
            var Q277;
            Q277=makeQuery(id+"F3.opExtrude","CAP_EDGE",EDGE,{"disambiguationData":[OSD([sQuery(id+"F2.wireOp",EDGE,"E2.13.2.0")])],"isStart":false});
            var Q278;
            Q278=makeQuery(id+"F3.opExtrude","CAP_EDGE",EDGE,{"disambiguationData":[OSD([sQuery(id+"F2.wireOp",EDGE,"E2.7.2.0")])],"isStart":false});
            var Q279;
            Q279=makeQuery(id+"F3.opExtrude","CAP_EDGE",EDGE,{"disambiguationData":[OSD([sQuery(id+"F2.wireOp",EDGE,"E3.0.26.2")])],"isStart":false});
            var Q280;
            Q280=makeQuery(id+"F3.opExtrude","CAP_EDGE",EDGE,{"disambiguationData":[OSD([sQuery(id+"F2.wireOp",EDGE,"E2.1.2.0")])],"isStart":false});
            var Q281;
            Q281=makeQuery(id+"F3.opExtrude","CAP_EDGE",EDGE,{"disambiguationData":[OSD([sQuery(id+"F2.wireOp",EDGE,"E3.0.20.2")])],"isStart":false});
            var Q282;
            Q282=makeQuery(id+"F3.opExtrude","CAP_EDGE",EDGE,{"disambiguationData":[OSD([sQuery(id+"F2.wireOp",EDGE,"E3.0.27.2")])],"isStart":false});
            var Q283;
            Q283=makeQuery(id+"F3.opExtrude","CAP_EDGE",EDGE,{"disambiguationData":[OSD([sQuery(id+"F2.wireOp",EDGE,"E2.8.2.0")])],"isStart":false});
            var Q284;
            Q284=makeQuery(id+"F3.opExtrude","CAP_EDGE",EDGE,{"disambiguationData":[OSD([sQuery(id+"F2.wireOp",EDGE,"E2.14.2.0")])],"isStart":false});
            var Q285;
            Q285=makeQuery(id+"F3.opExtrude","CAP_EDGE",EDGE,{"disambiguationData":[OSD([sQuery(id+"F2.wireOp",EDGE,"E2.2.2.0")])],"isStart":false});
            var Q286;
            Q286=makeQuery(id+"F3.opExtrude","CAP_EDGE",EDGE,{"disambiguationData":[OSD([sQuery(id+"F2.wireOp",EDGE,"E3.0.21.2")])],"isStart":false});
            var Q287;
            Q287=makeQuery(id+"F3.opExtrude","CAP_EDGE",EDGE,{"disambiguationData":[OSD([sQuery(id+"F2.wireOp",EDGE,"E3.0.28.2")])],"isStart":false});
            var Q288;
            Q288=makeQuery(id+"F3.opExtrude","CAP_EDGE",EDGE,{"disambiguationData":[OSD([sQuery(id+"F2.wireOp",EDGE,"E2.15.2.0")])],"isStart":false});
            var Q289;
            Q289=makeQuery(id+"F3.opExtrude","CAP_EDGE",EDGE,{"disambiguationData":[OSD([sQuery(id+"F2.wireOp",EDGE,"E3.0.22.2")])],"isStart":false});
            var Q290;
            Q290=makeQuery(id+"F3.opExtrude","CAP_EDGE",EDGE,{"disambiguationData":[OSD([sQuery(id+"F2.wireOp",EDGE,"E2.9.2.0")])],"isStart":false});
            var Q291;
            Q291=makeQuery(id+"F3.opExtrude","CAP_EDGE",EDGE,{"disambiguationData":[OSD([sQuery(id+"F2.wireOp",EDGE,"E3.0.23.2")])],"isStart":false});
            var Q292;
            Q292=makeQuery(id+"F3.opExtrude","CAP_EDGE",EDGE,{"disambiguationData":[OSD([sQuery(id+"F2.wireOp",EDGE,"E2.17.2.0")])],"isStart":false});
            var Q293;
            Q293=makeQuery(id+"F3.opExtrude","CAP_EDGE",EDGE,{"disambiguationData":[OSD([sQuery(id+"F2.wireOp",EDGE,"E3.0.24.2")])],"isStart":false});
            var Q294;
            Q294=makeQuery(id+"F3.opExtrude","CAP_EDGE",EDGE,{"disambiguationData":[OSD([sQuery(id+"F2.wireOp",EDGE,"E2.11.2.0")])],"isStart":false});
            var Q295;
            Q295=makeQuery(id+"F3.opExtrude","CAP_EDGE",EDGE,{"disambiguationData":[OSD([sQuery(id+"F2.wireOp",EDGE,"E2.18.2.0")])],"isStart":false});
            var Q296;
            Q296=makeQuery(id+"F3.opExtrude","CAP_EDGE",EDGE,{"disambiguationData":[OSD([sQuery(id+"F2.wireOp",EDGE,"E2.5.2.0")])],"isStart":false});
            var Q297;
            Q297=makeQuery(id+"F3.opExtrude","CAP_EDGE",EDGE,{"disambiguationData":[OSD([sQuery(id+"F2.wireOp",EDGE,"E2.12.2.0")])],"isStart":false});
            var Q298;
            Q298=makeQuery(id+"F3.opExtrude","CAP_EDGE",EDGE,{"disambiguationData":[OSD([sQuery(id+"F2.wireOp",EDGE,"E2.6.2.0")])],"isStart":false});
            var Q299;
            Q299=makeQuery(id+"F3.opExtrude","CAP_EDGE",EDGE,{"disambiguationData":[OSD([sQuery(id+"F2.wireOp",EDGE,"E3.0.25.2")])],"isStart":false});
            var Q300;
            Q300=makeQuery(id+"F3.opExtrude","CAP_EDGE",EDGE,{"disambiguationData":[OSD([sQuery(id+"F2.wireOp",EDGE,"E2.19.2.0")])],"isStart":false});
            var Q301;
            Q301=makeQuery(id+"F3.opExtrude","CAP_EDGE",EDGE,{"disambiguationData":[OSD([sQuery(id+"F2.wireOp",EDGE,"E2.0.2.1")])],"isStart":false});
            var Q302;
            Q302=makeQuery(id+"F3.opExtrude","CAP_EDGE",EDGE,{"disambiguationData":[OSD([sQuery(id+"F2.wireOp",EDGE,"E3.6.23.2")])],"isStart":false});
            var Q303;
            Q303=makeQuery(id+"F3.opExtrude","CAP_EDGE",EDGE,{"disambiguationData":[OSD([sQuery(id+"F2.wireOp",EDGE,"E2.17.2.2")])],"isStart":false});
            var Q304;
            Q304=makeQuery(id+"F3.opExtrude","CAP_EDGE",EDGE,{"disambiguationData":[OSD([sQuery(id+"F2.wireOp",EDGE,"E3.6.24.2")])],"isStart":false});
            var Q305;
            Q305=makeQuery(id+"F3.opExtrude","CAP_EDGE",EDGE,{"disambiguationData":[OSD([sQuery(id+"F2.wireOp",EDGE,"E2.11.2.2")])],"isStart":false});
            var Q306;
            Q306=makeQuery(id+"F3.opExtrude","CAP_EDGE",EDGE,{"disambiguationData":[OSD([sQuery(id+"F2.wireOp",EDGE,"E2.18.2.2")])],"isStart":false});
            var Q307;
            Q307=makeQuery(id+"F3.opExtrude","CAP_EDGE",EDGE,{"disambiguationData":[OSD([sQuery(id+"F2.wireOp",EDGE,"E2.5.2.2")])],"isStart":false});
            var Q308;
            Q308=makeQuery(id+"F3.opExtrude","CAP_EDGE",EDGE,{"disambiguationData":[OSD([sQuery(id+"F2.wireOp",EDGE,"E2.12.2.2")])],"isStart":false});
            var Q309;
            Q309=makeQuery(id+"F3.opExtrude","CAP_EDGE",EDGE,{"disambiguationData":[OSD([sQuery(id+"F2.wireOp",EDGE,"E2.6.2.2")])],"isStart":false});
            var Q310;
            Q310=makeQuery(id+"F3.opExtrude","CAP_EDGE",EDGE,{"disambiguationData":[OSD([sQuery(id+"F2.wireOp",EDGE,"E3.6.25.2")])],"isStart":false});
            var Q311;
            Q311=makeQuery(id+"F3.opExtrude","CAP_EDGE",EDGE,{"disambiguationData":[OSD([sQuery(id+"F2.wireOp",EDGE,"E2.19.2.2")])],"isStart":false});
            var Q312;
            Q312=makeQuery(id+"F3.opExtrude","CAP_EDGE",EDGE,{"disambiguationData":[OSD([sQuery(id+"F2.wireOp",EDGE,"E2.4.2.2")])],"isStart":false});
            var Q313;
            Q313=makeQuery(id+"F3.opExtrude","CAP_EDGE",EDGE,{"disambiguationData":[OSD([sQuery(id+"F2.wireOp",EDGE,"E2.16.2.2")])],"isStart":false});
            var Q314;
            Q314=makeQuery(id+"F3.opExtrude","CAP_EDGE",EDGE,{"disambiguationData":[OSD([sQuery(id+"F2.wireOp",EDGE,"E2.3.2.2")])],"isStart":false});
            var Q315;
            Q315=makeQuery(id+"F3.opExtrude","CAP_EDGE",EDGE,{"disambiguationData":[OSD([sQuery(id+"F2.wireOp",EDGE,"E2.10.2.2")])],"isStart":false});
            var Q316;
            Q316=makeQuery(id+"F3.opExtrude","CAP_EDGE",EDGE,{"disambiguationData":[OSD([sQuery(id+"F2.wireOp",EDGE,"E3.6.29.2")])],"isStart":false});
            var Q317;
            Q317=makeQuery(id+"F3.opExtrude","CAP_EDGE",EDGE,{"disambiguationData":[OSD([sQuery(id+"F2.wireOp",EDGE,"E3.6.22.2")])],"isStart":false});
            var Q318;
            Q318=makeQuery(id+"F3.opExtrude","CAP_EDGE",EDGE,{"disambiguationData":[OSD([sQuery(id+"F2.wireOp",EDGE,"E2.13.2.2")])],"isStart":false});
            var Q319;
            Q319=makeQuery(id+"F3.opExtrude","CAP_EDGE",EDGE,{"disambiguationData":[OSD([sQuery(id+"F2.wireOp",EDGE,"E2.7.2.2")])],"isStart":false});
            var Q320;
            Q320=makeQuery(id+"F3.opExtrude","CAP_EDGE",EDGE,{"disambiguationData":[OSD([sQuery(id+"F2.wireOp",EDGE,"E3.6.26.2")])],"isStart":false});
            var Q321;
            Q321=makeQuery(id+"F3.opExtrude","CAP_EDGE",EDGE,{"disambiguationData":[OSD([sQuery(id+"F2.wireOp",EDGE,"E2.1.2.2")])],"isStart":false});
            var Q322;
            Q322=makeQuery(id+"F3.opExtrude","CAP_EDGE",EDGE,{"disambiguationData":[OSD([sQuery(id+"F2.wireOp",EDGE,"E3.6.20.2")])],"isStart":false});
            var Q323;
            Q323=makeQuery(id+"F3.opExtrude","CAP_EDGE",EDGE,{"disambiguationData":[OSD([sQuery(id+"F2.wireOp",EDGE,"E3.6.27.2")])],"isStart":false});
            var Q324;
            Q324=makeQuery(id+"F3.opExtrude","CAP_EDGE",EDGE,{"disambiguationData":[OSD([sQuery(id+"F2.wireOp",EDGE,"E2.14.2.2")])],"isStart":false});
            var Q325;
            Q325=makeQuery(id+"F3.opExtrude","CAP_EDGE",EDGE,{"disambiguationData":[OSD([sQuery(id+"F2.wireOp",EDGE,"E3.6.21.2")])],"isStart":false});
            var Q326;
            Q326=makeQuery(id+"F3.opExtrude","CAP_EDGE",EDGE,{"disambiguationData":[OSD([sQuery(id+"F2.wireOp",EDGE,"E2.8.2.2")])],"isStart":false});
            var Q327;
            Q327=makeQuery(id+"F3.opExtrude","CAP_EDGE",EDGE,{"disambiguationData":[OSD([sQuery(id+"F2.wireOp",EDGE,"E2.15.2.2")])],"isStart":false});
            var Q328;
            Q328=makeQuery(id+"F3.opExtrude","CAP_EDGE",EDGE,{"disambiguationData":[OSD([sQuery(id+"F2.wireOp",EDGE,"E2.2.2.2")])],"isStart":false});
            var Q329;
            Q329=makeQuery(id+"F3.opExtrude","CAP_EDGE",EDGE,{"disambiguationData":[OSD([sQuery(id+"F2.wireOp",EDGE,"E2.9.2.2")])],"isStart":false});
            var Q330;
            Q330=makeQuery(id+"F3.opExtrude","CAP_EDGE",EDGE,{"disambiguationData":[OSD([sQuery(id+"F2.wireOp",EDGE,"E3.6.28.2")])],"isStart":false});
            var Q331;
            Q331=makeQuery(id+"F3.opExtrude","CAP_EDGE",EDGE,{"disambiguationData":[OSD([sQuery(id+"F2.wireOp",EDGE,"E2.4.2.1")])],"isStart":false});
            var Q332;
            Q332=makeQuery(id+"F3.opExtrude","CAP_EDGE",EDGE,{"disambiguationData":[OSD([sQuery(id+"F2.wireOp",EDGE,"E2.16.2.1")])],"isStart":false});
            var Q333;
            Q333=makeQuery(id+"F3.opExtrude","CAP_EDGE",EDGE,{"disambiguationData":[OSD([sQuery(id+"F2.wireOp",EDGE,"E2.3.2.1")])],"isStart":false});
            var Q334;
            Q334=makeQuery(id+"F3.opExtrude","CAP_EDGE",EDGE,{"disambiguationData":[OSD([sQuery(id+"F2.wireOp",EDGE,"E2.10.2.1")])],"isStart":false});
            var Q335;
            Q335=makeQuery(id+"F3.opExtrude","CAP_EDGE",EDGE,{"disambiguationData":[OSD([sQuery(id+"F2.wireOp",EDGE,"E3.3.29.2")])],"isStart":false});
            var Q336;
            Q336=makeQuery(id+"F3.opExtrude","CAP_EDGE",EDGE,{"disambiguationData":[OSD([sQuery(id+"F2.wireOp",EDGE,"E3.3.23.2")])],"isStart":false});
            var Q337;
            Q337=makeQuery(id+"F3.opExtrude","CAP_EDGE",EDGE,{"disambiguationData":[OSD([sQuery(id+"F2.wireOp",EDGE,"E2.17.2.1")])],"isStart":false});
            var Q338;
            Q338=makeQuery(id+"F3.opExtrude","CAP_EDGE",EDGE,{"disambiguationData":[OSD([sQuery(id+"F2.wireOp",EDGE,"E3.3.24.2")])],"isStart":false});
            var Q339;
            Q339=makeQuery(id+"F3.opExtrude","CAP_EDGE",EDGE,{"disambiguationData":[OSD([sQuery(id+"F2.wireOp",EDGE,"E2.11.2.1")])],"isStart":false});
            var Q340;
            Q340=makeQuery(id+"F3.opExtrude","CAP_EDGE",EDGE,{"disambiguationData":[OSD([sQuery(id+"F2.wireOp",EDGE,"E3.3.27.2")])],"isStart":false});
            var Q341;
            Q341=makeQuery(id+"F3.opExtrude","CAP_EDGE",EDGE,{"disambiguationData":[OSD([sQuery(id+"F2.wireOp",EDGE,"E2.14.2.1")])],"isStart":false});
            var Q342;
            Q342=makeQuery(id+"F3.opExtrude","CAP_EDGE",EDGE,{"disambiguationData":[OSD([sQuery(id+"F2.wireOp",EDGE,"E3.3.21.2")])],"isStart":false});
            var Q343;
            Q343=makeQuery(id+"F3.opExtrude","CAP_EDGE",EDGE,{"disambiguationData":[OSD([sQuery(id+"F2.wireOp",EDGE,"E2.8.2.1")])],"isStart":false});
            var Q344;
            Q344=makeQuery(id+"F3.opExtrude","CAP_EDGE",EDGE,{"disambiguationData":[OSD([sQuery(id+"F2.wireOp",EDGE,"E2.15.2.1")])],"isStart":false});
            var Q345;
            Q345=makeQuery(id+"F3.opExtrude","CAP_EDGE",EDGE,{"disambiguationData":[OSD([sQuery(id+"F2.wireOp",EDGE,"E2.2.2.1")])],"isStart":false});
            var Q346;
            Q346=makeQuery(id+"F3.opExtrude","CAP_EDGE",EDGE,{"disambiguationData":[OSD([sQuery(id+"F2.wireOp",EDGE,"E3.3.22.2")])],"isStart":false});
            var Q347;
            Q347=makeQuery(id+"F3.opExtrude","CAP_EDGE",EDGE,{"disambiguationData":[OSD([sQuery(id+"F2.wireOp",EDGE,"E3.3.28.2")])],"isStart":false});
            var Q348;
            Q348=makeQuery(id+"F3.opExtrude","CAP_EDGE",EDGE,{"disambiguationData":[OSD([sQuery(id+"F2.wireOp",EDGE,"E2.9.2.1")])],"isStart":false});
            var Q349;
            Q349=makeQuery(id+"F3.opExtrude","CAP_EDGE",EDGE,{"disambiguationData":[OSD([sQuery(id+"F2.wireOp",EDGE,"E2.18.2.1")])],"isStart":false});
            var Q350;
            Q350=makeQuery(id+"F3.opExtrude","CAP_EDGE",EDGE,{"disambiguationData":[OSD([sQuery(id+"F2.wireOp",EDGE,"E2.5.2.1")])],"isStart":false});
            var Q351;
            Q351=makeQuery(id+"F3.opExtrude","CAP_EDGE",EDGE,{"disambiguationData":[OSD([sQuery(id+"F2.wireOp",EDGE,"E2.12.2.1")])],"isStart":false});
            var Q352;
            Q352=makeQuery(id+"F3.opExtrude","CAP_EDGE",EDGE,{"disambiguationData":[OSD([sQuery(id+"F2.wireOp",EDGE,"E2.6.2.1")])],"isStart":false});
            var Q353;
            Q353=makeQuery(id+"F3.opExtrude","CAP_EDGE",EDGE,{"disambiguationData":[OSD([sQuery(id+"F2.wireOp",EDGE,"E3.3.25.2")])],"isStart":false});
            var Q354;
            Q354=makeQuery(id+"F3.opExtrude","CAP_EDGE",EDGE,{"disambiguationData":[OSD([sQuery(id+"F2.wireOp",EDGE,"E2.19.2.1")])],"isStart":false});
            var Q355;
            Q355=makeQuery(id+"F3.opExtrude","CAP_EDGE",EDGE,{"disambiguationData":[OSD([sQuery(id+"F2.wireOp",EDGE,"E2.13.2.1")])],"isStart":false});
            var Q356;
            Q356=makeQuery(id+"F3.opExtrude","CAP_EDGE",EDGE,{"disambiguationData":[OSD([sQuery(id+"F2.wireOp",EDGE,"E2.7.2.1")])],"isStart":false});
            var Q357;
            Q357=makeQuery(id+"F3.opExtrude","CAP_EDGE",EDGE,{"disambiguationData":[OSD([sQuery(id+"F2.wireOp",EDGE,"E3.3.26.2")])],"isStart":false});
            var Q358;
            Q358=makeQuery(id+"F3.opExtrude","CAP_EDGE",EDGE,{"disambiguationData":[OSD([sQuery(id+"F2.wireOp",EDGE,"E2.1.2.1")])],"isStart":false});
            var Q359;
            Q359=makeQuery(id+"F3.opExtrude","CAP_EDGE",EDGE,{"disambiguationData":[OSD([sQuery(id+"F2.wireOp",EDGE,"E3.3.20.2")])],"isStart":false});
            var Q360;
            Q360=makeQuery(id+"F3.opExtrude","CAP_EDGE",EDGE,{"disambiguationData":[OSD([sQuery(id+"F2.wireOp",EDGE,"E2.0.3.0")])],"isStart":false});
            var Q361;
            Q361=makeQuery(id+"F3.opExtrude","CAP_EDGE",EDGE,{"disambiguationData":[OSD([sQuery(id+"F2.wireOp",EDGE,"E2.0.3.2")])],"isStart":false});
            var Q362;
            Q362=makeQuery(id+"F3.opExtrude","CAP_EDGE",EDGE,{"disambiguationData":[OSD([sQuery(id+"F2.wireOp",EDGE,"E2.16.3.0")])],"isStart":false});
            var Q363;
            Q363=makeQuery(id+"F3.opExtrude","CAP_EDGE",EDGE,{"disambiguationData":[OSD([sQuery(id+"F2.wireOp",EDGE,"E2.4.3.0")])],"isStart":false});
            var Q364;
            Q364=makeQuery(id+"F3.opExtrude","CAP_EDGE",EDGE,{"disambiguationData":[OSD([sQuery(id+"F2.wireOp",EDGE,"E2.3.3.0")])],"isStart":false});
            var Q365;
            Q365=makeQuery(id+"F3.opExtrude","CAP_EDGE",EDGE,{"disambiguationData":[OSD([sQuery(id+"F2.wireOp",EDGE,"E2.10.3.0")])],"isStart":false});
            var Q366;
            Q366=makeQuery(id+"F3.opExtrude","CAP_EDGE",EDGE,{"disambiguationData":[OSD([sQuery(id+"F2.wireOp",EDGE,"E3.0.29.3")])],"isStart":false});
            var Q367;
            Q367=makeQuery(id+"F3.opExtrude","CAP_EDGE",EDGE,{"disambiguationData":[OSD([sQuery(id+"F2.wireOp",EDGE,"E3.0.23.3")])],"isStart":false});
            var Q368;
            Q368=makeQuery(id+"F3.opExtrude","CAP_EDGE",EDGE,{"disambiguationData":[OSD([sQuery(id+"F2.wireOp",EDGE,"E2.17.3.0")])],"isStart":false});
            var Q369;
            Q369=makeQuery(id+"F3.opExtrude","CAP_EDGE",EDGE,{"disambiguationData":[OSD([sQuery(id+"F2.wireOp",EDGE,"E2.1.3.0")])],"isStart":false});
            var Q370;
            Q370=makeQuery(id+"F3.opExtrude","CAP_EDGE",EDGE,{"disambiguationData":[OSD([sQuery(id+"F2.wireOp",EDGE,"E3.0.20.3")])],"isStart":false});
            var Q371;
            Q371=makeQuery(id+"F3.opExtrude","CAP_EDGE",EDGE,{"disambiguationData":[OSD([sQuery(id+"F2.wireOp",EDGE,"E3.0.27.3")])],"isStart":false});
            var Q372;
            Q372=makeQuery(id+"F3.opExtrude","CAP_EDGE",EDGE,{"disambiguationData":[OSD([sQuery(id+"F2.wireOp",EDGE,"E2.14.3.0")])],"isStart":false});
            var Q373;
            Q373=makeQuery(id+"F3.opExtrude","CAP_EDGE",EDGE,{"disambiguationData":[OSD([sQuery(id+"F2.wireOp",EDGE,"E3.0.21.3")])],"isStart":false});
            var Q374;
            Q374=makeQuery(id+"F3.opExtrude","CAP_EDGE",EDGE,{"disambiguationData":[OSD([sQuery(id+"F2.wireOp",EDGE,"E2.8.3.0")])],"isStart":false});
            var Q375;
            Q375=makeQuery(id+"F3.opExtrude","CAP_EDGE",EDGE,{"disambiguationData":[OSD([sQuery(id+"F2.wireOp",EDGE,"E2.15.3.0")])],"isStart":false});
            var Q376;
            Q376=makeQuery(id+"F3.opExtrude","CAP_EDGE",EDGE,{"disambiguationData":[OSD([sQuery(id+"F2.wireOp",EDGE,"E2.2.3.0")])],"isStart":false});
            var Q377;
            Q377=makeQuery(id+"F3.opExtrude","CAP_EDGE",EDGE,{"disambiguationData":[OSD([sQuery(id+"F2.wireOp",EDGE,"E2.9.3.0")])],"isStart":false});
            var Q378;
            Q378=makeQuery(id+"F3.opExtrude","CAP_EDGE",EDGE,{"disambiguationData":[OSD([sQuery(id+"F2.wireOp",EDGE,"E3.0.28.3")])],"isStart":false});
            var Q379;
            Q379=makeQuery(id+"F3.opExtrude","CAP_EDGE",EDGE,{"disambiguationData":[OSD([sQuery(id+"F2.wireOp",EDGE,"E3.0.22.3")])],"isStart":false});
            var Q380;
            Q380=makeQuery(id+"F3.opExtrude","CAP_EDGE",EDGE,{"disambiguationData":[OSD([sQuery(id+"F2.wireOp",EDGE,"E2.11.3.0")])],"isStart":false});
            var Q381;
            Q381=makeQuery(id+"F3.opExtrude","CAP_EDGE",EDGE,{"disambiguationData":[OSD([sQuery(id+"F2.wireOp",EDGE,"E2.5.3.0")])],"isStart":false});
            var Q382;
            Q382=makeQuery(id+"F3.opExtrude","CAP_EDGE",EDGE,{"disambiguationData":[OSD([sQuery(id+"F2.wireOp",EDGE,"E3.0.24.3")])],"isStart":false});
            var Q383;
            Q383=makeQuery(id+"F3.opExtrude","CAP_EDGE",EDGE,{"disambiguationData":[OSD([sQuery(id+"F2.wireOp",EDGE,"E2.18.3.0")])],"isStart":false});
            var Q384;
            Q384=makeQuery(id+"F3.opExtrude","CAP_EDGE",EDGE,{"disambiguationData":[OSD([sQuery(id+"F2.wireOp",EDGE,"E3.0.25.3")])],"isStart":false});
            var Q385;
            Q385=makeQuery(id+"F3.opExtrude","CAP_EDGE",EDGE,{"disambiguationData":[OSD([sQuery(id+"F2.wireOp",EDGE,"E2.6.3.0")])],"isStart":false});
            var Q386;
            Q386=makeQuery(id+"F3.opExtrude","CAP_EDGE",EDGE,{"disambiguationData":[OSD([sQuery(id+"F2.wireOp",EDGE,"E2.12.3.0")])],"isStart":false});
            var Q387;
            Q387=makeQuery(id+"F3.opExtrude","CAP_EDGE",EDGE,{"disambiguationData":[OSD([sQuery(id+"F2.wireOp",EDGE,"E2.19.3.0")])],"isStart":false});
            var Q388;
            Q388=makeQuery(id+"F3.opExtrude","CAP_EDGE",EDGE,{"disambiguationData":[OSD([sQuery(id+"F2.wireOp",EDGE,"E2.13.3.0")])],"isStart":false});
            var Q389;
            Q389=makeQuery(id+"F3.opExtrude","CAP_EDGE",EDGE,{"disambiguationData":[OSD([sQuery(id+"F2.wireOp",EDGE,"E2.7.3.0")])],"isStart":false});
            var Q390;
            Q390=makeQuery(id+"F3.opExtrude","CAP_EDGE",EDGE,{"disambiguationData":[OSD([sQuery(id+"F2.wireOp",EDGE,"E3.0.26.3")])],"isStart":false});
            var Q391;
            Q391=makeQuery(id+"F3.opExtrude","CAP_EDGE",EDGE,{"disambiguationData":[OSD([sQuery(id+"F2.wireOp",EDGE,"E3.6.25.3")])],"isStart":false});
            var Q392;
            Q392=makeQuery(id+"F3.opExtrude","CAP_EDGE",EDGE,{"disambiguationData":[OSD([sQuery(id+"F2.wireOp",EDGE,"E2.12.3.2")])],"isStart":false});
            var Q393;
            Q393=makeQuery(id+"F3.opExtrude","CAP_EDGE",EDGE,{"disambiguationData":[OSD([sQuery(id+"F2.wireOp",EDGE,"E2.19.3.2")])],"isStart":false});
            var Q394;
            Q394=makeQuery(id+"F3.opExtrude","CAP_EDGE",EDGE,{"disambiguationData":[OSD([sQuery(id+"F2.wireOp",EDGE,"E2.6.3.2")])],"isStart":false});
            var Q395;
            Q395=makeQuery(id+"F3.opExtrude","CAP_EDGE",EDGE,{"disambiguationData":[OSD([sQuery(id+"F2.wireOp",EDGE,"E2.13.3.2")])],"isStart":false});
            var Q396;
            Q396=makeQuery(id+"F3.opExtrude","CAP_EDGE",EDGE,{"disambiguationData":[OSD([sQuery(id+"F2.wireOp",EDGE,"E2.7.3.2")])],"isStart":false});
            var Q397;
            Q397=makeQuery(id+"F3.opExtrude","CAP_EDGE",EDGE,{"disambiguationData":[OSD([sQuery(id+"F2.wireOp",EDGE,"E3.6.26.3")])],"isStart":false});
            var Q398;
            Q398=makeQuery(id+"F3.opExtrude","CAP_EDGE",EDGE,{"disambiguationData":[OSD([sQuery(id+"F2.wireOp",EDGE,"E2.1.3.2")])],"isStart":false});
            var Q399;
            Q399=makeQuery(id+"F3.opExtrude","CAP_EDGE",EDGE,{"disambiguationData":[OSD([sQuery(id+"F2.wireOp",EDGE,"E3.6.20.3")])],"isStart":false});
            var Q400;
            Q400=makeQuery(id+"F3.opExtrude","CAP_EDGE",EDGE,{"disambiguationData":[OSD([sQuery(id+"F2.wireOp",EDGE,"E3.6.27.3")])],"isStart":false});
            var Q401;
            Q401=makeQuery(id+"F3.opExtrude","CAP_EDGE",EDGE,{"disambiguationData":[OSD([sQuery(id+"F2.wireOp",EDGE,"E2.14.3.2")])],"isStart":false});
            var Q402;
            Q402=makeQuery(id+"F3.opExtrude","CAP_EDGE",EDGE,{"disambiguationData":[OSD([sQuery(id+"F2.wireOp",EDGE,"E3.6.21.3")])],"isStart":false});
            var Q403;
            Q403=makeQuery(id+"F3.opExtrude","CAP_EDGE",EDGE,{"disambiguationData":[OSD([sQuery(id+"F2.wireOp",EDGE,"E2.8.3.2")])],"isStart":false});
            var Q404;
            Q404=makeQuery(id+"F3.opExtrude","CAP_EDGE",EDGE,{"disambiguationData":[OSD([sQuery(id+"F2.wireOp",EDGE,"E2.3.3.2")])],"isStart":false});
            var Q405;
            Q405=makeQuery(id+"F3.opExtrude","CAP_EDGE",EDGE,{"disambiguationData":[OSD([sQuery(id+"F2.wireOp",EDGE,"E2.4.3.2")])],"isStart":false});
            var Q406;
            Q406=makeQuery(id+"F3.opExtrude","CAP_EDGE",EDGE,{"disambiguationData":[OSD([sQuery(id+"F2.wireOp",EDGE,"E3.6.29.3")])],"isStart":false});
            var Q407;
            Q407=makeQuery(id+"F3.opExtrude","CAP_EDGE",EDGE,{"disambiguationData":[OSD([sQuery(id+"F2.wireOp",EDGE,"E2.10.3.2")])],"isStart":false});
            var Q408;
            Q408=makeQuery(id+"F3.opExtrude","CAP_EDGE",EDGE,{"disambiguationData":[OSD([sQuery(id+"F2.wireOp",EDGE,"E2.0.3.1")])],"isStart":false});
            var Q409;
            Q409=makeQuery(id+"F3.opExtrude","CAP_EDGE",EDGE,{"disambiguationData":[OSD([sQuery(id+"F2.wireOp",EDGE,"E2.16.3.2")])],"isStart":false});
            var Q410;
            Q410=makeQuery(id+"F3.opExtrude","CAP_EDGE",EDGE,{"disambiguationData":[OSD([sQuery(id+"F2.wireOp",EDGE,"E3.6.23.3")])],"isStart":false});
            var Q411;
            Q411=makeQuery(id+"F3.opExtrude","CAP_EDGE",EDGE,{"disambiguationData":[OSD([sQuery(id+"F2.wireOp",EDGE,"E2.17.3.2")])],"isStart":false});
            var Q412;
            Q412=makeQuery(id+"F3.opExtrude","CAP_EDGE",EDGE,{"disambiguationData":[OSD([sQuery(id+"F2.wireOp",EDGE,"E2.11.3.2")])],"isStart":false});
            var Q413;
            Q413=makeQuery(id+"F3.opExtrude","CAP_EDGE",EDGE,{"disambiguationData":[OSD([sQuery(id+"F2.wireOp",EDGE,"E2.5.3.2")])],"isStart":false});
            var Q414;
            Q414=makeQuery(id+"F3.opExtrude","CAP_EDGE",EDGE,{"disambiguationData":[OSD([sQuery(id+"F2.wireOp",EDGE,"E3.6.24.3")])],"isStart":false});
            var Q415;
            Q415=makeQuery(id+"F3.opExtrude","CAP_EDGE",EDGE,{"disambiguationData":[OSD([sQuery(id+"F2.wireOp",EDGE,"E2.18.3.2")])],"isStart":false});
            var Q416;
            Q416=makeQuery(id+"F3.opExtrude","CAP_EDGE",EDGE,{"disambiguationData":[OSD([sQuery(id+"F2.wireOp",EDGE,"E2.15.3.2")])],"isStart":false});
            var Q417;
            Q417=makeQuery(id+"F3.opExtrude","CAP_EDGE",EDGE,{"disambiguationData":[OSD([sQuery(id+"F2.wireOp",EDGE,"E2.2.3.2")])],"isStart":false});
            var Q418;
            Q418=makeQuery(id+"F3.opExtrude","CAP_EDGE",EDGE,{"disambiguationData":[OSD([sQuery(id+"F2.wireOp",EDGE,"E2.9.3.2")])],"isStart":false});
            var Q419;
            Q419=makeQuery(id+"F3.opExtrude","CAP_EDGE",EDGE,{"disambiguationData":[OSD([sQuery(id+"F2.wireOp",EDGE,"E3.6.28.3")])],"isStart":false});
            var Q420;
            Q420=makeQuery(id+"F3.opExtrude","CAP_EDGE",EDGE,{"disambiguationData":[OSD([sQuery(id+"F2.wireOp",EDGE,"E3.6.22.3")])],"isStart":false});
            var Q421;
            Q421=makeQuery(id+"F3.opExtrude","CAP_EDGE",EDGE,{"disambiguationData":[OSD([sQuery(id+"F2.wireOp",EDGE,"E2.0.3.3")])],"isStart":false});
            var Q422;
            Q422=makeQuery(id+"F3.opExtrude","CAP_EDGE",EDGE,{"disambiguationData":[OSD([sQuery(id+"F2.wireOp",EDGE,"E3.3.29.3")])],"isStart":false});
            var Q423;
            Q423=makeQuery(id+"F3.opExtrude","CAP_EDGE",EDGE,{"disambiguationData":[OSD([sQuery(id+"F2.wireOp",EDGE,"E2.16.3.1")])],"isStart":false});
            var Q424;
            Q424=makeQuery(id+"F3.opExtrude","CAP_EDGE",EDGE,{"disambiguationData":[OSD([sQuery(id+"F2.wireOp",EDGE,"E3.3.23.3")])],"isStart":false});
            var Q425;
            Q425=makeQuery(id+"F3.opExtrude","CAP_EDGE",EDGE,{"disambiguationData":[OSD([sQuery(id+"F2.wireOp",EDGE,"E2.10.3.1")])],"isStart":false});
            var Q426;
            Q426=makeQuery(id+"F3.opExtrude","CAP_EDGE",EDGE,{"disambiguationData":[OSD([sQuery(id+"F2.wireOp",EDGE,"E2.17.3.1")])],"isStart":false});
            var Q427;
            Q427=makeQuery(id+"F3.opExtrude","CAP_EDGE",EDGE,{"disambiguationData":[OSD([sQuery(id+"F2.wireOp",EDGE,"E2.11.3.1")])],"isStart":false});
            var Q428;
            Q428=makeQuery(id+"F3.opExtrude","CAP_EDGE",EDGE,{"disambiguationData":[OSD([sQuery(id+"F2.wireOp",EDGE,"E2.5.3.1")])],"isStart":false});
            var Q429;
            Q429=makeQuery(id+"F3.opExtrude","CAP_EDGE",EDGE,{"disambiguationData":[OSD([sQuery(id+"F2.wireOp",EDGE,"E3.3.24.3")])],"isStart":false});
            var Q430;
            Q430=makeQuery(id+"F3.opExtrude","CAP_EDGE",EDGE,{"disambiguationData":[OSD([sQuery(id+"F2.wireOp",EDGE,"E2.18.3.1")])],"isStart":false});
            var Q431;
            Q431=makeQuery(id+"F3.opExtrude","CAP_EDGE",EDGE,{"disambiguationData":[OSD([sQuery(id+"F2.wireOp",EDGE,"E3.3.25.3")])],"isStart":false});
            var Q432;
            Q432=makeQuery(id+"F3.opExtrude","CAP_EDGE",EDGE,{"disambiguationData":[OSD([sQuery(id+"F2.wireOp",EDGE,"E2.12.3.1")])],"isStart":false});
            var Q433;
            Q433=makeQuery(id+"F3.opExtrude","CAP_EDGE",EDGE,{"disambiguationData":[OSD([sQuery(id+"F2.wireOp",EDGE,"E2.3.3.1")])],"isStart":false});
            var Q434;
            Q434=makeQuery(id+"F3.opExtrude","CAP_EDGE",EDGE,{"disambiguationData":[OSD([sQuery(id+"F2.wireOp",EDGE,"E2.4.3.1")])],"isStart":false});
            var Q435;
            Q435=makeQuery(id+"F3.opExtrude","CAP_EDGE",EDGE,{"disambiguationData":[OSD([sQuery(id+"F2.wireOp",EDGE,"E2.9.3.1")])],"isStart":false});
            var Q436;
            Q436=makeQuery(id+"F3.opExtrude","CAP_EDGE",EDGE,{"disambiguationData":[OSD([sQuery(id+"F2.wireOp",EDGE,"E3.3.28.3")])],"isStart":false});
            var Q437;
            Q437=makeQuery(id+"F3.opExtrude","CAP_EDGE",EDGE,{"disambiguationData":[OSD([sQuery(id+"F2.wireOp",EDGE,"E3.3.22.3")])],"isStart":false});
            var Q438;
            Q438=makeQuery(id+"F3.opExtrude","CAP_EDGE",EDGE,{"disambiguationData":[OSD([sQuery(id+"F2.wireOp",EDGE,"E2.19.3.1")])],"isStart":false});
            var Q439;
            Q439=makeQuery(id+"F3.opExtrude","CAP_EDGE",EDGE,{"disambiguationData":[OSD([sQuery(id+"F2.wireOp",EDGE,"E2.6.3.1")])],"isStart":false});
            var Q440;
            Q440=makeQuery(id+"F3.opExtrude","CAP_EDGE",EDGE,{"disambiguationData":[OSD([sQuery(id+"F2.wireOp",EDGE,"E2.13.3.1")])],"isStart":false});
            var Q441;
            Q441=makeQuery(id+"F3.opExtrude","CAP_EDGE",EDGE,{"disambiguationData":[OSD([sQuery(id+"F2.wireOp",EDGE,"E2.7.3.1")])],"isStart":false});
            var Q442;
            Q442=makeQuery(id+"F3.opExtrude","CAP_EDGE",EDGE,{"disambiguationData":[OSD([sQuery(id+"F2.wireOp",EDGE,"E3.3.26.3")])],"isStart":false});
            var Q443;
            Q443=makeQuery(id+"F3.opExtrude","CAP_EDGE",EDGE,{"disambiguationData":[OSD([sQuery(id+"F2.wireOp",EDGE,"E2.1.3.1")])],"isStart":false});
            var Q444;
            Q444=makeQuery(id+"F3.opExtrude","CAP_EDGE",EDGE,{"disambiguationData":[OSD([sQuery(id+"F2.wireOp",EDGE,"E3.3.20.3")])],"isStart":false});
            var Q445;
            Q445=makeQuery(id+"F3.opExtrude","CAP_EDGE",EDGE,{"disambiguationData":[OSD([sQuery(id+"F2.wireOp",EDGE,"E3.3.27.3")])],"isStart":false});
            var Q446;
            Q446=makeQuery(id+"F3.opExtrude","CAP_EDGE",EDGE,{"disambiguationData":[OSD([sQuery(id+"F2.wireOp",EDGE,"E2.14.3.1")])],"isStart":false});
            var Q447;
            Q447=makeQuery(id+"F3.opExtrude","CAP_EDGE",EDGE,{"disambiguationData":[OSD([sQuery(id+"F2.wireOp",EDGE,"E3.3.21.3")])],"isStart":false});
            var Q448;
            Q448=makeQuery(id+"F3.opExtrude","CAP_EDGE",EDGE,{"disambiguationData":[OSD([sQuery(id+"F2.wireOp",EDGE,"E2.8.3.1")])],"isStart":false});
            var Q449;
            Q449=makeQuery(id+"F3.opExtrude","CAP_EDGE",EDGE,{"disambiguationData":[OSD([sQuery(id+"F2.wireOp",EDGE,"E2.15.3.1")])],"isStart":false});
            var Q450;
            Q450=makeQuery(id+"F3.opExtrude","CAP_EDGE",EDGE,{"disambiguationData":[OSD([sQuery(id+"F2.wireOp",EDGE,"E2.2.3.1")])],"isStart":false});
            var Q451;
            Q451=makeQuery(id+"F3.opExtrude","CAP_EDGE",EDGE,{"disambiguationData":[OSD([sQuery(id+"F2.wireOp",EDGE,"E2.3.3.3")])],"isStart":false});
            var Q452;
            Q452=makeQuery(id+"F3.opExtrude","CAP_EDGE",EDGE,{"disambiguationData":[OSD([sQuery(id+"F2.wireOp",EDGE,"E2.4.3.3")])],"isStart":false});
            var Q453;
            Q453=makeQuery(id+"F3.opExtrude","CAP_EDGE",EDGE,{"disambiguationData":[OSD([sQuery(id+"F2.wireOp",EDGE,"E3.9.29.3")])],"isStart":false});
            var Q454;
            Q454=makeQuery(id+"F3.opExtrude","CAP_EDGE",EDGE,{"disambiguationData":[OSD([sQuery(id+"F2.wireOp",EDGE,"E2.16.3.3")])],"isStart":false});
            var Q455;
            Q455=makeQuery(id+"F3.opExtrude","CAP_EDGE",EDGE,{"disambiguationData":[OSD([sQuery(id+"F2.wireOp",EDGE,"E3.9.23.3")])],"isStart":false});
            var Q456;
            Q456=makeQuery(id+"F3.opExtrude","CAP_EDGE",EDGE,{"disambiguationData":[OSD([sQuery(id+"F2.wireOp",EDGE,"E2.10.3.3")])],"isStart":false});
            var Q457;
            Q457=makeQuery(id+"F3.opExtrude","CAP_EDGE",EDGE,{"disambiguationData":[OSD([sQuery(id+"F2.wireOp",EDGE,"E2.7.3.3")])],"isStart":false});
            var Q458;
            Q458=makeQuery(id+"F3.opExtrude","CAP_EDGE",EDGE,{"disambiguationData":[OSD([sQuery(id+"F2.wireOp",EDGE,"E3.9.26.3")])],"isStart":false});
            var Q459;
            Q459=makeQuery(id+"F3.opExtrude","CAP_EDGE",EDGE,{"disambiguationData":[OSD([sQuery(id+"F2.wireOp",EDGE,"E2.1.3.3")])],"isStart":false});
            var Q460;
            Q460=makeQuery(id+"F3.opExtrude","CAP_EDGE",EDGE,{"disambiguationData":[OSD([sQuery(id+"F2.wireOp",EDGE,"E3.9.20.3")])],"isStart":false});
            var Q461;
            Q461=makeQuery(id+"F3.opExtrude","CAP_EDGE",EDGE,{"disambiguationData":[OSD([sQuery(id+"F2.wireOp",EDGE,"E3.9.27.3")])],"isStart":false});
            var Q462;
            Q462=makeQuery(id+"F3.opExtrude","CAP_EDGE",EDGE,{"disambiguationData":[OSD([sQuery(id+"F2.wireOp",EDGE,"E2.14.3.3")])],"isStart":false});
            var Q463;
            Q463=makeQuery(id+"F3.opExtrude","CAP_EDGE",EDGE,{"disambiguationData":[OSD([sQuery(id+"F2.wireOp",EDGE,"E3.9.21.3")])],"isStart":false});
            var Q464;
            Q464=makeQuery(id+"F3.opExtrude","CAP_EDGE",EDGE,{"disambiguationData":[OSD([sQuery(id+"F2.wireOp",EDGE,"E2.8.3.3")])],"isStart":false});
            var Q465;
            Q465=makeQuery(id+"F3.opExtrude","CAP_EDGE",EDGE,{"disambiguationData":[OSD([sQuery(id+"F2.wireOp",EDGE,"E2.15.3.3")])],"isStart":false});
            var Q466;
            Q466=makeQuery(id+"F3.opExtrude","CAP_EDGE",EDGE,{"disambiguationData":[OSD([sQuery(id+"F2.wireOp",EDGE,"E2.2.3.3")])],"isStart":false});
            var Q467;
            Q467=makeQuery(id+"F3.opExtrude","CAP_EDGE",EDGE,{"disambiguationData":[OSD([sQuery(id+"F2.wireOp",EDGE,"E2.9.3.3")])],"isStart":false});
            var Q468;
            Q468=makeQuery(id+"F3.opExtrude","CAP_EDGE",EDGE,{"disambiguationData":[OSD([sQuery(id+"F2.wireOp",EDGE,"E3.9.28.3")])],"isStart":false});
            var Q469;
            Q469=makeQuery(id+"F3.opExtrude","CAP_EDGE",EDGE,{"disambiguationData":[OSD([sQuery(id+"F2.wireOp",EDGE,"E3.9.22.3")])],"isStart":false});
            var Q470;
            Q470=makeQuery(id+"F3.opExtrude","CAP_EDGE",EDGE,{"disambiguationData":[OSD([sQuery(id+"F2.wireOp",EDGE,"E2.17.3.3")])],"isStart":false});
            var Q471;
            Q471=makeQuery(id+"F3.opExtrude","CAP_EDGE",EDGE,{"disambiguationData":[OSD([sQuery(id+"F2.wireOp",EDGE,"E2.11.3.3")])],"isStart":false});
            var Q472;
            Q472=makeQuery(id+"F3.opExtrude","CAP_EDGE",EDGE,{"disambiguationData":[OSD([sQuery(id+"F2.wireOp",EDGE,"E2.5.3.3")])],"isStart":false});
            var Q473;
            Q473=makeQuery(id+"F3.opExtrude","CAP_EDGE",EDGE,{"disambiguationData":[OSD([sQuery(id+"F2.wireOp",EDGE,"E3.9.24.3")])],"isStart":false});
            var Q474;
            Q474=makeQuery(id+"F3.opExtrude","CAP_EDGE",EDGE,{"disambiguationData":[OSD([sQuery(id+"F2.wireOp",EDGE,"E2.18.3.3")])],"isStart":false});
            var Q475;
            Q475=makeQuery(id+"F3.opExtrude","CAP_EDGE",EDGE,{"disambiguationData":[OSD([sQuery(id+"F2.wireOp",EDGE,"E3.9.25.3")])],"isStart":false});
            var Q476;
            Q476=makeQuery(id+"F3.opExtrude","CAP_EDGE",EDGE,{"disambiguationData":[OSD([sQuery(id+"F2.wireOp",EDGE,"E2.12.3.3")])],"isStart":false});
            var Q477;
            Q477=makeQuery(id+"F3.opExtrude","CAP_EDGE",EDGE,{"disambiguationData":[OSD([sQuery(id+"F2.wireOp",EDGE,"E2.19.3.3")])],"isStart":false});
            var Q478;
            Q478=makeQuery(id+"F3.opExtrude","CAP_EDGE",EDGE,{"disambiguationData":[OSD([sQuery(id+"F2.wireOp",EDGE,"E2.6.3.3")])],"isStart":false});
            var Q479;
            Q479=makeQuery(id+"F3.opExtrude","CAP_EDGE",EDGE,{"disambiguationData":[OSD([sQuery(id+"F2.wireOp",EDGE,"E2.13.3.3")])],"isStart":false});
            var Q480;
            Q480=makeQuery(id+"F3.opExtrude","CAP_EDGE",EDGE,{"disambiguationData":[OSD([sQuery(id+"F2.wireOp",EDGE,"E2.0.4.3")])],"isStart":false});
            var Q481;
            Q481=makeQuery(id+"F3.opExtrude","CAP_EDGE",EDGE,{"disambiguationData":[OSD([sQuery(id+"F2.wireOp",EDGE,"E2.0.4.0")])],"isStart":false});
            var Q482;
            Q482=makeQuery(id+"F3.opExtrude","CAP_EDGE",EDGE,{"disambiguationData":[OSD([sQuery(id+"F2.wireOp",EDGE,"E2.0.4.2")])],"isStart":false});
            var Q483;
            Q483=makeQuery(id+"F3.opExtrude","CAP_EDGE",EDGE,{"disambiguationData":[OSD([sQuery(id+"F2.wireOp",EDGE,"E3.9.23.4")])],"isStart":false});
            var Q484;
            Q484=makeQuery(id+"F3.opExtrude","CAP_EDGE",EDGE,{"disambiguationData":[OSD([sQuery(id+"F2.wireOp",EDGE,"E2.3.4.3")])],"isStart":false});
            var Q485;
            Q485=makeQuery(id+"F3.opExtrude","CAP_EDGE",EDGE,{"disambiguationData":[OSD([sQuery(id+"F2.wireOp",EDGE,"E3.9.22.4")])],"isStart":false});
            var Q486;
            Q486=makeQuery(id+"F3.opExtrude","CAP_EDGE",EDGE,{"disambiguationData":[OSD([sQuery(id+"F2.wireOp",EDGE,"E2.19.4.3")])],"isStart":false});
            var Q487;
            Q487=makeQuery(id+"F3.opExtrude","CAP_EDGE",EDGE,{"disambiguationData":[OSD([sQuery(id+"F2.wireOp",EDGE,"E2.6.4.3")])],"isStart":false});
            var Q488;
            Q488=makeQuery(id+"F3.opExtrude","CAP_EDGE",EDGE,{"disambiguationData":[OSD([sQuery(id+"F2.wireOp",EDGE,"E3.9.26.4")])],"isStart":false});
            var Q489;
            Q489=makeQuery(id+"F3.opExtrude","CAP_EDGE",EDGE,{"disambiguationData":[OSD([sQuery(id+"F2.wireOp",EDGE,"E2.13.4.3")])],"isStart":false});
            var Q490;
            Q490=makeQuery(id+"F3.opExtrude","CAP_EDGE",EDGE,{"disambiguationData":[OSD([sQuery(id+"F2.wireOp",EDGE,"E3.9.20.4")])],"isStart":false});
            var Q491;
            Q491=makeQuery(id+"F3.opExtrude","CAP_EDGE",EDGE,{"disambiguationData":[OSD([sQuery(id+"F2.wireOp",EDGE,"E2.1.4.3")])],"isStart":false});
            var Q492;
            Q492=makeQuery(id+"F3.opExtrude","CAP_EDGE",EDGE,{"disambiguationData":[OSD([sQuery(id+"F2.wireOp",EDGE,"E2.7.4.3")])],"isStart":false});
            var Q493;
            Q493=makeQuery(id+"F3.opExtrude","CAP_EDGE",EDGE,{"disambiguationData":[OSD([sQuery(id+"F2.wireOp",EDGE,"E3.9.27.4")])],"isStart":false});
            var Q494;
            Q494=makeQuery(id+"F3.opExtrude","CAP_EDGE",EDGE,{"disambiguationData":[OSD([sQuery(id+"F2.wireOp",EDGE,"E2.14.4.3")])],"isStart":false});
            var Q495;
            Q495=makeQuery(id+"F3.opExtrude","CAP_EDGE",EDGE,{"disambiguationData":[OSD([sQuery(id+"F2.wireOp",EDGE,"E3.9.21.4")])],"isStart":false});
            var Q496;
            Q496=makeQuery(id+"F3.opExtrude","CAP_EDGE",EDGE,{"disambiguationData":[OSD([sQuery(id+"F2.wireOp",EDGE,"E2.8.4.3")])],"isStart":false});
            var Q497;
            Q497=makeQuery(id+"F3.opExtrude","CAP_EDGE",EDGE,{"disambiguationData":[OSD([sQuery(id+"F2.wireOp",EDGE,"E2.15.4.3")])],"isStart":false});
            var Q498;
            Q498=makeQuery(id+"F3.opExtrude","CAP_EDGE",EDGE,{"disambiguationData":[OSD([sQuery(id+"F2.wireOp",EDGE,"E2.2.4.3")])],"isStart":false});
            var Q499;
            Q499=makeQuery(id+"F3.opExtrude","CAP_EDGE",EDGE,{"disambiguationData":[OSD([sQuery(id+"F2.wireOp",EDGE,"E3.9.29.4")])],"isStart":false});
            var Q500;
            Q500=makeQuery(id+"F3.opExtrude","CAP_EDGE",EDGE,{"disambiguationData":[OSD([sQuery(id+"F2.wireOp",EDGE,"E2.16.4.3")])],"isStart":false});
            var Q501;
            Q501=makeQuery(id+"F3.opExtrude","CAP_EDGE",EDGE,{"disambiguationData":[OSD([sQuery(id+"F2.wireOp",EDGE,"E2.10.4.3")])],"isStart":false});
            var Q502;
            Q502=makeQuery(id+"F3.opExtrude","CAP_EDGE",EDGE,{"disambiguationData":[OSD([sQuery(id+"F2.wireOp",EDGE,"E2.17.4.3")])],"isStart":false});
            var Q503;
            Q503=makeQuery(id+"F3.opExtrude","CAP_EDGE",EDGE,{"disambiguationData":[OSD([sQuery(id+"F2.wireOp",EDGE,"E2.4.4.3")])],"isStart":false});
            var Q504;
            Q504=makeQuery(id+"F3.opExtrude","CAP_EDGE",EDGE,{"disambiguationData":[OSD([sQuery(id+"F2.wireOp",EDGE,"E2.11.4.3")])],"isStart":false});
            var Q505;
            Q505=makeQuery(id+"F3.opExtrude","CAP_EDGE",EDGE,{"disambiguationData":[OSD([sQuery(id+"F2.wireOp",EDGE,"E2.5.4.3")])],"isStart":false});
            var Q506;
            Q506=makeQuery(id+"F3.opExtrude","CAP_EDGE",EDGE,{"disambiguationData":[OSD([sQuery(id+"F2.wireOp",EDGE,"E3.9.24.4")])],"isStart":false});
            var Q507;
            Q507=makeQuery(id+"F3.opExtrude","CAP_EDGE",EDGE,{"disambiguationData":[OSD([sQuery(id+"F2.wireOp",EDGE,"E2.18.4.3")])],"isStart":false});
            var Q508;
            Q508=makeQuery(id+"F3.opExtrude","CAP_EDGE",EDGE,{"disambiguationData":[OSD([sQuery(id+"F2.wireOp",EDGE,"E3.9.25.4")])],"isStart":false});
            var Q509;
            Q509=makeQuery(id+"F3.opExtrude","CAP_EDGE",EDGE,{"disambiguationData":[OSD([sQuery(id+"F2.wireOp",EDGE,"E2.12.4.3")])],"isStart":false});
            var Q510;
            Q510=makeQuery(id+"F3.opExtrude","CAP_EDGE",EDGE,{"disambiguationData":[OSD([sQuery(id+"F2.wireOp",EDGE,"E3.0.23.4")])],"isStart":false});
            var Q511;
            Q511=makeQuery(id+"F3.opExtrude","CAP_EDGE",EDGE,{"disambiguationData":[OSD([sQuery(id+"F2.wireOp",EDGE,"E3.0.22.4")])],"isStart":false});
            var Q512;
            Q512=makeQuery(id+"F3.opExtrude","CAP_EDGE",EDGE,{"disambiguationData":[OSD([sQuery(id+"F2.wireOp",EDGE,"E2.16.4.0")])],"isStart":false});
            var Q513;
            Q513=makeQuery(id+"F3.opExtrude","CAP_EDGE",EDGE,{"disambiguationData":[OSD([sQuery(id+"F2.wireOp",EDGE,"E2.3.4.0")])],"isStart":false});
            var Q514;
            Q514=makeQuery(id+"F3.opExtrude","CAP_EDGE",EDGE,{"disambiguationData":[OSD([sQuery(id+"F2.wireOp",EDGE,"E2.10.4.0")])],"isStart":false});
            var Q515;
            Q515=makeQuery(id+"F3.opExtrude","CAP_EDGE",EDGE,{"disambiguationData":[OSD([sQuery(id+"F2.wireOp",EDGE,"E3.0.29.4")])],"isStart":false});
            var Q516;
            Q516=makeQuery(id+"F3.opExtrude","CAP_EDGE",EDGE,{"disambiguationData":[OSD([sQuery(id+"F2.wireOp",EDGE,"E2.9.4.3")])],"isStart":false});
            var Q517;
            Q517=makeQuery(id+"F3.opExtrude","CAP_EDGE",EDGE,{"disambiguationData":[OSD([sQuery(id+"F2.wireOp",EDGE,"E3.9.28.4")])],"isStart":false});
            var Q518;
            Q518=makeQuery(id+"F3.opExtrude","CAP_EDGE",EDGE,{"disambiguationData":[OSD([sQuery(id+"F2.wireOp",EDGE,"E2.13.4.0")])],"isStart":false});
            var Q519;
            Q519=makeQuery(id+"F3.opExtrude","CAP_EDGE",EDGE,{"disambiguationData":[OSD([sQuery(id+"F2.wireOp",EDGE,"E2.7.4.0")])],"isStart":false});
            var Q520;
            Q520=makeQuery(id+"F3.opExtrude","CAP_EDGE",EDGE,{"disambiguationData":[OSD([sQuery(id+"F2.wireOp",EDGE,"E3.0.26.4")])],"isStart":false});
            var Q521;
            Q521=makeQuery(id+"F3.opExtrude","CAP_EDGE",EDGE,{"disambiguationData":[OSD([sQuery(id+"F2.wireOp",EDGE,"E2.1.4.0")])],"isStart":false});
            var Q522;
            Q522=makeQuery(id+"F3.opExtrude","CAP_EDGE",EDGE,{"disambiguationData":[OSD([sQuery(id+"F2.wireOp",EDGE,"E3.0.20.4")])],"isStart":false});
            var Q523;
            Q523=makeQuery(id+"F3.opExtrude","CAP_EDGE",EDGE,{"disambiguationData":[OSD([sQuery(id+"F2.wireOp",EDGE,"E3.0.27.4")])],"isStart":false});
            var Q524;
            Q524=makeQuery(id+"F3.opExtrude","CAP_EDGE",EDGE,{"disambiguationData":[OSD([sQuery(id+"F2.wireOp",EDGE,"E2.14.4.0")])],"isStart":false});
            var Q525;
            Q525=makeQuery(id+"F3.opExtrude","CAP_EDGE",EDGE,{"disambiguationData":[OSD([sQuery(id+"F2.wireOp",EDGE,"E3.0.21.4")])],"isStart":false});
            var Q526;
            Q526=makeQuery(id+"F3.opExtrude","CAP_EDGE",EDGE,{"disambiguationData":[OSD([sQuery(id+"F2.wireOp",EDGE,"E2.8.4.0")])],"isStart":false});
            var Q527;
            Q527=makeQuery(id+"F3.opExtrude","CAP_EDGE",EDGE,{"disambiguationData":[OSD([sQuery(id+"F2.wireOp",EDGE,"E2.15.4.0")])],"isStart":false});
            var Q528;
            Q528=makeQuery(id+"F3.opExtrude","CAP_EDGE",EDGE,{"disambiguationData":[OSD([sQuery(id+"F2.wireOp",EDGE,"E2.2.4.0")])],"isStart":false});
            var Q529;
            Q529=makeQuery(id+"F3.opExtrude","CAP_EDGE",EDGE,{"disambiguationData":[OSD([sQuery(id+"F2.wireOp",EDGE,"E2.9.4.0")])],"isStart":false});
            var Q530;
            Q530=makeQuery(id+"F3.opExtrude","CAP_EDGE",EDGE,{"disambiguationData":[OSD([sQuery(id+"F2.wireOp",EDGE,"E3.0.28.4")])],"isStart":false});
            var Q531;
            Q531=makeQuery(id+"F3.opExtrude","CAP_EDGE",EDGE,{"disambiguationData":[OSD([sQuery(id+"F2.wireOp",EDGE,"E2.17.4.0")])],"isStart":false});
            var Q532;
            Q532=makeQuery(id+"F3.opExtrude","CAP_EDGE",EDGE,{"disambiguationData":[OSD([sQuery(id+"F2.wireOp",EDGE,"E2.4.4.0")])],"isStart":false});
            var Q533;
            Q533=makeQuery(id+"F3.opExtrude","CAP_EDGE",EDGE,{"disambiguationData":[OSD([sQuery(id+"F2.wireOp",EDGE,"E2.11.4.0")])],"isStart":false});
            var Q534;
            Q534=makeQuery(id+"F3.opExtrude","CAP_EDGE",EDGE,{"disambiguationData":[OSD([sQuery(id+"F2.wireOp",EDGE,"E2.5.4.0")])],"isStart":false});
            var Q535;
            Q535=makeQuery(id+"F3.opExtrude","CAP_EDGE",EDGE,{"disambiguationData":[OSD([sQuery(id+"F2.wireOp",EDGE,"E3.0.24.4")])],"isStart":false});
            var Q536;
            Q536=makeQuery(id+"F3.opExtrude","CAP_EDGE",EDGE,{"disambiguationData":[OSD([sQuery(id+"F2.wireOp",EDGE,"E2.12.4.0")])],"isStart":false});
            var Q537;
            Q537=makeQuery(id+"F3.opExtrude","CAP_EDGE",EDGE,{"disambiguationData":[OSD([sQuery(id+"F2.wireOp",EDGE,"E2.18.4.0")])],"isStart":false});
            var Q538;
            Q538=makeQuery(id+"F3.opExtrude","CAP_EDGE",EDGE,{"disambiguationData":[OSD([sQuery(id+"F2.wireOp",EDGE,"E2.6.4.0")])],"isStart":false});
            var Q539;
            Q539=makeQuery(id+"F3.opExtrude","CAP_EDGE",EDGE,{"disambiguationData":[OSD([sQuery(id+"F2.wireOp",EDGE,"E3.0.25.4")])],"isStart":false});
            var Q540;
            Q540=makeQuery(id+"F3.opExtrude","CAP_EDGE",EDGE,{"disambiguationData":[OSD([sQuery(id+"F2.wireOp",EDGE,"E2.19.4.0")])],"isStart":false});
            var Q541;
            Q541=makeQuery(id+"F3.opExtrude","CAP_EDGE",EDGE,{"disambiguationData":[OSD([sQuery(id+"F2.wireOp",EDGE,"E2.0.4.1")])],"isStart":false});
            var Q542;
            Q542=makeQuery(id+"F3.opExtrude","CAP_EDGE",EDGE,{"disambiguationData":[OSD([sQuery(id+"F2.wireOp",EDGE,"E2.10.4.2")])],"isStart":false});
            var Q543;
            Q543=makeQuery(id+"F3.opExtrude","CAP_EDGE",EDGE,{"disambiguationData":[OSD([sQuery(id+"F2.wireOp",EDGE,"E2.17.4.2")])],"isStart":false});
            var Q544;
            Q544=makeQuery(id+"F3.opExtrude","CAP_EDGE",EDGE,{"disambiguationData":[OSD([sQuery(id+"F2.wireOp",EDGE,"E2.4.4.2")])],"isStart":false});
            var Q545;
            Q545=makeQuery(id+"F3.opExtrude","CAP_EDGE",EDGE,{"disambiguationData":[OSD([sQuery(id+"F2.wireOp",EDGE,"E2.11.4.2")])],"isStart":false});
            var Q546;
            Q546=makeQuery(id+"F3.opExtrude","CAP_EDGE",EDGE,{"disambiguationData":[OSD([sQuery(id+"F2.wireOp",EDGE,"E2.5.4.2")])],"isStart":false});
            var Q547;
            Q547=makeQuery(id+"F3.opExtrude","CAP_EDGE",EDGE,{"disambiguationData":[OSD([sQuery(id+"F2.wireOp",EDGE,"E3.6.24.4")])],"isStart":false});
            var Q548;
            Q548=makeQuery(id+"F3.opExtrude","CAP_EDGE",EDGE,{"disambiguationData":[OSD([sQuery(id+"F2.wireOp",EDGE,"E2.18.4.2")])],"isStart":false});
            var Q549;
            Q549=makeQuery(id+"F3.opExtrude","CAP_EDGE",EDGE,{"disambiguationData":[OSD([sQuery(id+"F2.wireOp",EDGE,"E3.6.25.4")])],"isStart":false});
            var Q550;
            Q550=makeQuery(id+"F3.opExtrude","CAP_EDGE",EDGE,{"disambiguationData":[OSD([sQuery(id+"F2.wireOp",EDGE,"E2.12.4.2")])],"isStart":false});
            var Q551;
            Q551=makeQuery(id+"F3.opExtrude","CAP_EDGE",EDGE,{"disambiguationData":[OSD([sQuery(id+"F2.wireOp",EDGE,"E2.19.4.2")])],"isStart":false});
            var Q552;
            Q552=makeQuery(id+"F3.opExtrude","CAP_EDGE",EDGE,{"disambiguationData":[OSD([sQuery(id+"F2.wireOp",EDGE,"E2.6.4.2")])],"isStart":false});
            var Q553;
            Q553=makeQuery(id+"F3.opExtrude","CAP_EDGE",EDGE,{"disambiguationData":[OSD([sQuery(id+"F2.wireOp",EDGE,"E3.6.23.4")])],"isStart":false});
            var Q554;
            Q554=makeQuery(id+"F3.opExtrude","CAP_EDGE",EDGE,{"disambiguationData":[OSD([sQuery(id+"F2.wireOp",EDGE,"E2.3.4.2")])],"isStart":false});
            var Q555;
            Q555=makeQuery(id+"F3.opExtrude","CAP_EDGE",EDGE,{"disambiguationData":[OSD([sQuery(id+"F2.wireOp",EDGE,"E3.6.22.4")])],"isStart":false});
            var Q556;
            Q556=makeQuery(id+"F3.opExtrude","CAP_EDGE",EDGE,{"disambiguationData":[OSD([sQuery(id+"F2.wireOp",EDGE,"E3.6.29.4")])],"isStart":false});
            var Q557;
            Q557=makeQuery(id+"F3.opExtrude","CAP_EDGE",EDGE,{"disambiguationData":[OSD([sQuery(id+"F2.wireOp",EDGE,"E2.16.4.2")])],"isStart":false});
            var Q558;
            Q558=makeQuery(id+"F3.opExtrude","CAP_EDGE",EDGE,{"disambiguationData":[OSD([sQuery(id+"F2.wireOp",EDGE,"E2.13.4.2")])],"isStart":false});
            var Q559;
            Q559=makeQuery(id+"F3.opExtrude","CAP_EDGE",EDGE,{"disambiguationData":[OSD([sQuery(id+"F2.wireOp",EDGE,"E2.7.4.2")])],"isStart":false});
            var Q560;
            Q560=makeQuery(id+"F3.opExtrude","CAP_EDGE",EDGE,{"disambiguationData":[OSD([sQuery(id+"F2.wireOp",EDGE,"E3.6.26.4")])],"isStart":false});
            var Q561;
            Q561=makeQuery(id+"F3.opExtrude","CAP_EDGE",EDGE,{"disambiguationData":[OSD([sQuery(id+"F2.wireOp",EDGE,"E2.1.4.2")])],"isStart":false});
            var Q562;
            Q562=makeQuery(id+"F3.opExtrude","CAP_EDGE",EDGE,{"disambiguationData":[OSD([sQuery(id+"F2.wireOp",EDGE,"E3.6.20.4")])],"isStart":false});
            var Q563;
            Q563=makeQuery(id+"F3.opExtrude","CAP_EDGE",EDGE,{"disambiguationData":[OSD([sQuery(id+"F2.wireOp",EDGE,"E3.6.27.4")])],"isStart":false});
            var Q564;
            Q564=makeQuery(id+"F3.opExtrude","CAP_EDGE",EDGE,{"disambiguationData":[OSD([sQuery(id+"F2.wireOp",EDGE,"E2.14.4.2")])],"isStart":false});
            var Q565;
            Q565=makeQuery(id+"F3.opExtrude","CAP_EDGE",EDGE,{"disambiguationData":[OSD([sQuery(id+"F2.wireOp",EDGE,"E3.6.21.4")])],"isStart":false});
            var Q566;
            Q566=makeQuery(id+"F3.opExtrude","CAP_EDGE",EDGE,{"disambiguationData":[OSD([sQuery(id+"F2.wireOp",EDGE,"E2.8.4.2")])],"isStart":false});
            var Q567;
            Q567=makeQuery(id+"F3.opExtrude","CAP_EDGE",EDGE,{"disambiguationData":[OSD([sQuery(id+"F2.wireOp",EDGE,"E2.15.4.2")])],"isStart":false});
            var Q568;
            Q568=makeQuery(id+"F3.opExtrude","CAP_EDGE",EDGE,{"disambiguationData":[OSD([sQuery(id+"F2.wireOp",EDGE,"E2.2.4.2")])],"isStart":false});
            var Q569;
            Q569=makeQuery(id+"F3.opExtrude","CAP_EDGE",EDGE,{"disambiguationData":[OSD([sQuery(id+"F2.wireOp",EDGE,"E2.9.4.2")])],"isStart":false});
            var Q570;
            Q570=makeQuery(id+"F3.opExtrude","CAP_EDGE",EDGE,{"disambiguationData":[OSD([sQuery(id+"F2.wireOp",EDGE,"E3.6.28.4")])],"isStart":false});
            var Q571;
            Q571=makeQuery(id+"F3.opExtrude","CAP_EDGE",EDGE,{"disambiguationData":[OSD([sQuery(id+"F2.wireOp",EDGE,"E3.3.23.4")])],"isStart":false});
            var Q572;
            Q572=makeQuery(id+"F3.opExtrude","CAP_EDGE",EDGE,{"disambiguationData":[OSD([sQuery(id+"F2.wireOp",EDGE,"E2.3.4.1")])],"isStart":false});
            var Q573;
            Q573=makeQuery(id+"F3.opExtrude","CAP_EDGE",EDGE,{"disambiguationData":[OSD([sQuery(id+"F2.wireOp",EDGE,"E3.3.22.4")])],"isStart":false});
            var Q574;
            Q574=makeQuery(id+"F3.opExtrude","CAP_EDGE",EDGE,{"disambiguationData":[OSD([sQuery(id+"F2.wireOp",EDGE,"E3.3.29.4")])],"isStart":false});
            var Q575;
            Q575=makeQuery(id+"F3.opExtrude","CAP_EDGE",EDGE,{"disambiguationData":[OSD([sQuery(id+"F2.wireOp",EDGE,"E2.10.4.1")])],"isStart":false});
            var Q576;
            Q576=makeQuery(id+"F3.opExtrude","CAP_EDGE",EDGE,{"disambiguationData":[OSD([sQuery(id+"F2.wireOp",EDGE,"E2.16.4.1")])],"isStart":false});
            var Q577;
            Q577=makeQuery(id+"F3.opExtrude","CAP_EDGE",EDGE,{"disambiguationData":[OSD([sQuery(id+"F2.wireOp",EDGE,"E2.17.4.1")])],"isStart":false});
            var Q578;
            Q578=makeQuery(id+"F3.opExtrude","CAP_EDGE",EDGE,{"disambiguationData":[OSD([sQuery(id+"F2.wireOp",EDGE,"E2.4.4.1")])],"isStart":false});
            var Q579;
            Q579=makeQuery(id+"F3.opExtrude","CAP_EDGE",EDGE,{"disambiguationData":[OSD([sQuery(id+"F2.wireOp",EDGE,"E2.11.4.1")])],"isStart":false});
            var Q580;
            Q580=makeQuery(id+"F3.opExtrude","CAP_EDGE",EDGE,{"disambiguationData":[OSD([sQuery(id+"F2.wireOp",EDGE,"E3.3.27.4")])],"isStart":false});
            var Q581;
            Q581=makeQuery(id+"F3.opExtrude","CAP_EDGE",EDGE,{"disambiguationData":[OSD([sQuery(id+"F2.wireOp",EDGE,"E2.14.4.1")])],"isStart":false});
            var Q582;
            Q582=makeQuery(id+"F3.opExtrude","CAP_EDGE",EDGE,{"disambiguationData":[OSD([sQuery(id+"F2.wireOp",EDGE,"E3.3.21.4")])],"isStart":false});
            var Q583;
            Q583=makeQuery(id+"F3.opExtrude","CAP_EDGE",EDGE,{"disambiguationData":[OSD([sQuery(id+"F2.wireOp",EDGE,"E2.8.4.1")])],"isStart":false});
            var Q584;
            Q584=makeQuery(id+"F3.opExtrude","CAP_EDGE",EDGE,{"disambiguationData":[OSD([sQuery(id+"F2.wireOp",EDGE,"E2.15.4.1")])],"isStart":false});
            var Q585;
            Q585=makeQuery(id+"F3.opExtrude","CAP_EDGE",EDGE,{"disambiguationData":[OSD([sQuery(id+"F2.wireOp",EDGE,"E2.2.4.1")])],"isStart":false});
            var Q586;
            Q586=makeQuery(id+"F3.opExtrude","CAP_EDGE",EDGE,{"disambiguationData":[OSD([sQuery(id+"F2.wireOp",EDGE,"E2.9.4.1")])],"isStart":false});
            var Q587;
            Q587=makeQuery(id+"F3.opExtrude","CAP_EDGE",EDGE,{"disambiguationData":[OSD([sQuery(id+"F2.wireOp",EDGE,"E3.3.28.4")])],"isStart":false});
            var Q588;
            Q588=makeQuery(id+"F3.opExtrude","CAP_EDGE",EDGE,{"disambiguationData":[OSD([sQuery(id+"F2.wireOp",EDGE,"E2.5.4.1")])],"isStart":false});
            var Q589;
            Q589=makeQuery(id+"F3.opExtrude","CAP_EDGE",EDGE,{"disambiguationData":[OSD([sQuery(id+"F2.wireOp",EDGE,"E3.3.24.4")])],"isStart":false});
            var Q590;
            Q590=makeQuery(id+"F3.opExtrude","CAP_EDGE",EDGE,{"disambiguationData":[OSD([sQuery(id+"F2.wireOp",EDGE,"E2.18.4.1")])],"isStart":false});
            var Q591;
            Q591=makeQuery(id+"F3.opExtrude","CAP_EDGE",EDGE,{"disambiguationData":[OSD([sQuery(id+"F2.wireOp",EDGE,"E3.3.25.4")])],"isStart":false});
            var Q592;
            Q592=makeQuery(id+"F3.opExtrude","CAP_EDGE",EDGE,{"disambiguationData":[OSD([sQuery(id+"F2.wireOp",EDGE,"E2.6.4.1")])],"isStart":false});
            var Q593;
            Q593=makeQuery(id+"F3.opExtrude","CAP_EDGE",EDGE,{"disambiguationData":[OSD([sQuery(id+"F2.wireOp",EDGE,"E2.12.4.1")])],"isStart":false});
            var Q594;
            Q594=makeQuery(id+"F3.opExtrude","CAP_EDGE",EDGE,{"disambiguationData":[OSD([sQuery(id+"F2.wireOp",EDGE,"E2.19.4.1")])],"isStart":false});
            var Q595;
            Q595=makeQuery(id+"F3.opExtrude","CAP_EDGE",EDGE,{"disambiguationData":[OSD([sQuery(id+"F2.wireOp",EDGE,"E2.13.4.1")])],"isStart":false});
            var Q596;
            Q596=makeQuery(id+"F3.opExtrude","CAP_EDGE",EDGE,{"disambiguationData":[OSD([sQuery(id+"F2.wireOp",EDGE,"E2.7.4.1")])],"isStart":false});
            var Q597;
            Q597=makeQuery(id+"F3.opExtrude","CAP_EDGE",EDGE,{"disambiguationData":[OSD([sQuery(id+"F2.wireOp",EDGE,"E3.3.26.4")])],"isStart":false});
            var Q598;
            Q598=makeQuery(id+"F3.opExtrude","CAP_EDGE",EDGE,{"disambiguationData":[OSD([sQuery(id+"F2.wireOp",EDGE,"E2.1.4.1")])],"isStart":false});
            var Q599;
            Q599=makeQuery(id+"F3.opExtrude","CAP_EDGE",EDGE,{"disambiguationData":[OSD([sQuery(id+"F2.wireOp",EDGE,"E3.3.20.4")])],"isStart":false});
            var Q600;
            Q600=makeQuery(id+"F3.opExtrude","CAP_EDGE",EDGE,{"disambiguationData":[OSD([sQuery(id+"F2.wireOp",EDGE,"E2.0.5.0")])],"isStart":false});
            var Q601;
            Q601=makeQuery(id+"F3.opExtrude","CAP_EDGE",EDGE,{"disambiguationData":[OSD([sQuery(id+"F2.wireOp",EDGE,"E2.0.5.2")])],"isStart":false});
            var Q602;
            Q602=makeQuery(id+"F3.opExtrude","CAP_EDGE",EDGE,{"disambiguationData":[OSD([sQuery(id+"F2.wireOp",EDGE,"E3.0.23.5")])],"isStart":false});
            var Q603;
            Q603=makeQuery(id+"F3.opExtrude","CAP_EDGE",EDGE,{"disambiguationData":[OSD([sQuery(id+"F2.wireOp",EDGE,"E2.3.5.0")])],"isStart":false});
            var Q604;
            Q604=makeQuery(id+"F3.opExtrude","CAP_EDGE",EDGE,{"disambiguationData":[OSD([sQuery(id+"F2.wireOp",EDGE,"E3.0.22.5")])],"isStart":false});
            var Q605;
            Q605=makeQuery(id+"F3.opExtrude","CAP_EDGE",EDGE,{"disambiguationData":[OSD([sQuery(id+"F2.wireOp",EDGE,"E3.0.29.5")])],"isStart":false});
            var Q606;
            Q606=makeQuery(id+"F3.opExtrude","CAP_EDGE",EDGE,{"disambiguationData":[OSD([sQuery(id+"F2.wireOp",EDGE,"E2.16.5.0")])],"isStart":false});
            var Q607;
            Q607=makeQuery(id+"F3.opExtrude","CAP_EDGE",EDGE,{"disambiguationData":[OSD([sQuery(id+"F2.wireOp",EDGE,"E2.10.5.0")])],"isStart":false});
            var Q608;
            Q608=makeQuery(id+"F3.opExtrude","CAP_EDGE",EDGE,{"disambiguationData":[OSD([sQuery(id+"F2.wireOp",EDGE,"E2.17.5.0")])],"isStart":false});
            var Q609;
            Q609=makeQuery(id+"F3.opExtrude","CAP_EDGE",EDGE,{"disambiguationData":[OSD([sQuery(id+"F2.wireOp",EDGE,"E2.4.5.0")])],"isStart":false});
            var Q610;
            Q610=makeQuery(id+"F3.opExtrude","CAP_EDGE",EDGE,{"disambiguationData":[OSD([sQuery(id+"F2.wireOp",EDGE,"E3.0.20.5")])],"isStart":false});
            var Q611;
            Q611=makeQuery(id+"F3.opExtrude","CAP_EDGE",EDGE,{"disambiguationData":[OSD([sQuery(id+"F2.wireOp",EDGE,"E2.7.5.0")])],"isStart":false});
            var Q612;
            Q612=makeQuery(id+"F3.opExtrude","CAP_EDGE",EDGE,{"disambiguationData":[OSD([sQuery(id+"F2.wireOp",EDGE,"E2.14.5.0")])],"isStart":false});
            var Q613;
            Q613=makeQuery(id+"F3.opExtrude","CAP_EDGE",EDGE,{"disambiguationData":[OSD([sQuery(id+"F2.wireOp",EDGE,"E2.1.5.0")])],"isStart":false});
            var Q614;
            Q614=makeQuery(id+"F3.opExtrude","CAP_EDGE",EDGE,{"disambiguationData":[OSD([sQuery(id+"F2.wireOp",EDGE,"E2.8.5.0")])],"isStart":false});
            var Q615;
            Q615=makeQuery(id+"F3.opExtrude","CAP_EDGE",EDGE,{"disambiguationData":[OSD([sQuery(id+"F2.wireOp",EDGE,"E3.0.27.5")])],"isStart":false});
            var Q616;
            Q616=makeQuery(id+"F3.opExtrude","CAP_EDGE",EDGE,{"disambiguationData":[OSD([sQuery(id+"F2.wireOp",EDGE,"E2.15.5.0")])],"isStart":false});
            var Q617;
            Q617=makeQuery(id+"F3.opExtrude","CAP_EDGE",EDGE,{"disambiguationData":[OSD([sQuery(id+"F2.wireOp",EDGE,"E3.0.21.5")])],"isStart":false});
            var Q618;
            Q618=makeQuery(id+"F3.opExtrude","CAP_EDGE",EDGE,{"disambiguationData":[OSD([sQuery(id+"F2.wireOp",EDGE,"E2.2.5.0")])],"isStart":false});
            var Q619;
            Q619=makeQuery(id+"F3.opExtrude","CAP_EDGE",EDGE,{"disambiguationData":[OSD([sQuery(id+"F2.wireOp",EDGE,"E2.9.5.0")])],"isStart":false});
            var Q620;
            Q620=makeQuery(id+"F3.opExtrude","CAP_EDGE",EDGE,{"disambiguationData":[OSD([sQuery(id+"F2.wireOp",EDGE,"E3.0.28.5")])],"isStart":false});
            var Q621;
            Q621=makeQuery(id+"F3.opExtrude","CAP_EDGE",EDGE,{"disambiguationData":[OSD([sQuery(id+"F2.wireOp",EDGE,"E2.11.5.0")])],"isStart":false});
            var Q622;
            Q622=makeQuery(id+"F3.opExtrude","CAP_EDGE",EDGE,{"disambiguationData":[OSD([sQuery(id+"F2.wireOp",EDGE,"E2.5.5.0")])],"isStart":false});
            var Q623;
            Q623=makeQuery(id+"F3.opExtrude","CAP_EDGE",EDGE,{"disambiguationData":[OSD([sQuery(id+"F2.wireOp",EDGE,"E3.0.24.5")])],"isStart":false});
            var Q624;
            Q624=makeQuery(id+"F3.opExtrude","CAP_EDGE",EDGE,{"disambiguationData":[OSD([sQuery(id+"F2.wireOp",EDGE,"E2.18.5.0")])],"isStart":false});
            var Q625;
            Q625=makeQuery(id+"F3.opExtrude","CAP_EDGE",EDGE,{"disambiguationData":[OSD([sQuery(id+"F2.wireOp",EDGE,"E3.0.25.5")])],"isStart":false});
            var Q626;
            Q626=makeQuery(id+"F3.opExtrude","CAP_EDGE",EDGE,{"disambiguationData":[OSD([sQuery(id+"F2.wireOp",EDGE,"E2.12.5.0")])],"isStart":false});
            var Q627;
            Q627=makeQuery(id+"F3.opExtrude","CAP_EDGE",EDGE,{"disambiguationData":[OSD([sQuery(id+"F2.wireOp",EDGE,"E2.19.5.0")])],"isStart":false});
            var Q628;
            Q628=makeQuery(id+"F3.opExtrude","CAP_EDGE",EDGE,{"disambiguationData":[OSD([sQuery(id+"F2.wireOp",EDGE,"E2.6.5.0")])],"isStart":false});
            var Q629;
            Q629=makeQuery(id+"F3.opExtrude","CAP_EDGE",EDGE,{"disambiguationData":[OSD([sQuery(id+"F2.wireOp",EDGE,"E3.0.26.5")])],"isStart":false});
            var Q630;
            Q630=makeQuery(id+"F3.opExtrude","CAP_EDGE",EDGE,{"disambiguationData":[OSD([sQuery(id+"F2.wireOp",EDGE,"E2.13.5.0")])],"isStart":false});
            var Q631;
            Q631=makeQuery(id+"F3.opExtrude","CAP_EDGE",EDGE,{"disambiguationData":[OSD([sQuery(id+"F2.wireOp",EDGE,"E3.6.23.5")])],"isStart":false});
            var Q632;
            Q632=makeQuery(id+"F3.opExtrude","CAP_EDGE",EDGE,{"disambiguationData":[OSD([sQuery(id+"F2.wireOp",EDGE,"E3.6.25.5")])],"isStart":false});
            var Q633;
            Q633=makeQuery(id+"F3.opExtrude","CAP_EDGE",EDGE,{"disambiguationData":[OSD([sQuery(id+"F2.wireOp",EDGE,"E2.12.5.2")])],"isStart":false});
            var Q634;
            Q634=makeQuery(id+"F3.opExtrude","CAP_EDGE",EDGE,{"disambiguationData":[OSD([sQuery(id+"F2.wireOp",EDGE,"E2.19.5.2")])],"isStart":false});
            var Q635;
            Q635=makeQuery(id+"F3.opExtrude","CAP_EDGE",EDGE,{"disambiguationData":[OSD([sQuery(id+"F2.wireOp",EDGE,"E2.6.5.2")])],"isStart":false});
            var Q636;
            Q636=makeQuery(id+"F3.opExtrude","CAP_EDGE",EDGE,{"disambiguationData":[OSD([sQuery(id+"F2.wireOp",EDGE,"E3.6.26.5")])],"isStart":false});
            var Q637;
            Q637=makeQuery(id+"F3.opExtrude","CAP_EDGE",EDGE,{"disambiguationData":[OSD([sQuery(id+"F2.wireOp",EDGE,"E2.13.5.2")])],"isStart":false});
            var Q638;
            Q638=makeQuery(id+"F3.opExtrude","CAP_EDGE",EDGE,{"disambiguationData":[OSD([sQuery(id+"F2.wireOp",EDGE,"E3.6.20.5")])],"isStart":false});
            var Q639;
            Q639=makeQuery(id+"F3.opExtrude","CAP_EDGE",EDGE,{"disambiguationData":[OSD([sQuery(id+"F2.wireOp",EDGE,"E2.7.5.2")])],"isStart":false});
            var Q640;
            Q640=makeQuery(id+"F3.opExtrude","CAP_EDGE",EDGE,{"disambiguationData":[OSD([sQuery(id+"F2.wireOp",EDGE,"E2.14.5.2")])],"isStart":false});
            var Q641;
            Q641=makeQuery(id+"F3.opExtrude","CAP_EDGE",EDGE,{"disambiguationData":[OSD([sQuery(id+"F2.wireOp",EDGE,"E2.1.5.2")])],"isStart":false});
            var Q642;
            Q642=makeQuery(id+"F3.opExtrude","CAP_EDGE",EDGE,{"disambiguationData":[OSD([sQuery(id+"F2.wireOp",EDGE,"E2.8.5.2")])],"isStart":false});
            var Q643;
            Q643=makeQuery(id+"F3.opExtrude","CAP_EDGE",EDGE,{"disambiguationData":[OSD([sQuery(id+"F2.wireOp",EDGE,"E3.6.27.5")])],"isStart":false});
            var Q644;
            Q644=makeQuery(id+"F3.opExtrude","CAP_EDGE",EDGE,{"disambiguationData":[OSD([sQuery(id+"F2.wireOp",EDGE,"E2.3.5.2")])],"isStart":false});
            var Q645;
            Q645=makeQuery(id+"F3.opExtrude","CAP_EDGE",EDGE,{"disambiguationData":[OSD([sQuery(id+"F2.wireOp",EDGE,"E3.6.22.5")])],"isStart":false});
            var Q646;
            Q646=makeQuery(id+"F3.opExtrude","CAP_EDGE",EDGE,{"disambiguationData":[OSD([sQuery(id+"F2.wireOp",EDGE,"E3.6.29.5")])],"isStart":false});
            var Q647;
            Q647=makeQuery(id+"F3.opExtrude","CAP_EDGE",EDGE,{"disambiguationData":[OSD([sQuery(id+"F2.wireOp",EDGE,"E2.0.5.1")])],"isStart":false});
            var Q648;
            Q648=makeQuery(id+"F3.opExtrude","CAP_EDGE",EDGE,{"disambiguationData":[OSD([sQuery(id+"F2.wireOp",EDGE,"E2.16.5.2")])],"isStart":false});
            var Q649;
            Q649=makeQuery(id+"F3.opExtrude","CAP_EDGE",EDGE,{"disambiguationData":[OSD([sQuery(id+"F2.wireOp",EDGE,"E2.10.5.2")])],"isStart":false});
            var Q650;
            Q650=makeQuery(id+"F3.opExtrude","CAP_EDGE",EDGE,{"disambiguationData":[OSD([sQuery(id+"F2.wireOp",EDGE,"E2.17.5.2")])],"isStart":false});
            var Q651;
            Q651=makeQuery(id+"F3.opExtrude","CAP_EDGE",EDGE,{"disambiguationData":[OSD([sQuery(id+"F2.wireOp",EDGE,"E2.4.5.2")])],"isStart":false});
            var Q652;
            Q652=makeQuery(id+"F3.opExtrude","CAP_EDGE",EDGE,{"disambiguationData":[OSD([sQuery(id+"F2.wireOp",EDGE,"E2.11.5.2")])],"isStart":false});
            var Q653;
            Q653=makeQuery(id+"F3.opExtrude","CAP_EDGE",EDGE,{"disambiguationData":[OSD([sQuery(id+"F2.wireOp",EDGE,"E2.5.5.2")])],"isStart":false});
            var Q654;
            Q654=makeQuery(id+"F3.opExtrude","CAP_EDGE",EDGE,{"disambiguationData":[OSD([sQuery(id+"F2.wireOp",EDGE,"E3.6.24.5")])],"isStart":false});
            var Q655;
            Q655=makeQuery(id+"F3.opExtrude","CAP_EDGE",EDGE,{"disambiguationData":[OSD([sQuery(id+"F2.wireOp",EDGE,"E2.18.5.2")])],"isStart":false});
            var Q656;
            Q656=makeQuery(id+"F3.opExtrude","CAP_EDGE",EDGE,{"disambiguationData":[OSD([sQuery(id+"F2.wireOp",EDGE,"E2.2.5.2")])],"isStart":false});
            var Q657;
            Q657=makeQuery(id+"F3.opExtrude","CAP_EDGE",EDGE,{"disambiguationData":[OSD([sQuery(id+"F2.wireOp",EDGE,"E3.6.21.5")])],"isStart":false});
            var Q658;
            Q658=makeQuery(id+"F3.opExtrude","CAP_EDGE",EDGE,{"disambiguationData":[OSD([sQuery(id+"F2.wireOp",EDGE,"E3.6.28.5")])],"isStart":false});
            var Q659;
            Q659=makeQuery(id+"F3.opExtrude","CAP_EDGE",EDGE,{"disambiguationData":[OSD([sQuery(id+"F2.wireOp",EDGE,"E2.9.5.2")])],"isStart":false});
            var Q660;
            Q660=makeQuery(id+"F3.opExtrude","CAP_EDGE",EDGE,{"disambiguationData":[OSD([sQuery(id+"F2.wireOp",EDGE,"E2.15.5.2")])],"isStart":false});
            var Q661;
            Q661=makeQuery(id+"F3.opExtrude","CAP_EDGE",EDGE,{"disambiguationData":[OSD([sQuery(id+"F2.wireOp",EDGE,"E2.0.5.3")])],"isStart":false});
            var Q662;
            Q662=makeQuery(id+"F3.opExtrude","CAP_EDGE",EDGE,{"disambiguationData":[OSD([sQuery(id+"F2.wireOp",EDGE,"E3.3.29.5")])],"isStart":false});
            var Q663;
            Q663=makeQuery(id+"F3.opExtrude","CAP_EDGE",EDGE,{"disambiguationData":[OSD([sQuery(id+"F2.wireOp",EDGE,"E2.16.5.1")])],"isStart":false});
            var Q664;
            Q664=makeQuery(id+"F3.opExtrude","CAP_EDGE",EDGE,{"disambiguationData":[OSD([sQuery(id+"F2.wireOp",EDGE,"E2.10.5.1")])],"isStart":false});
            var Q665;
            Q665=makeQuery(id+"F3.opExtrude","CAP_EDGE",EDGE,{"disambiguationData":[OSD([sQuery(id+"F2.wireOp",EDGE,"E2.17.5.1")])],"isStart":false});
            var Q666;
            Q666=makeQuery(id+"F3.opExtrude","CAP_EDGE",EDGE,{"disambiguationData":[OSD([sQuery(id+"F2.wireOp",EDGE,"E2.4.5.1")])],"isStart":false});
            var Q667;
            Q667=makeQuery(id+"F3.opExtrude","CAP_EDGE",EDGE,{"disambiguationData":[OSD([sQuery(id+"F2.wireOp",EDGE,"E2.11.5.1")])],"isStart":false});
            var Q668;
            Q668=makeQuery(id+"F3.opExtrude","CAP_EDGE",EDGE,{"disambiguationData":[OSD([sQuery(id+"F2.wireOp",EDGE,"E2.5.5.1")])],"isStart":false});
            var Q669;
            Q669=makeQuery(id+"F3.opExtrude","CAP_EDGE",EDGE,{"disambiguationData":[OSD([sQuery(id+"F2.wireOp",EDGE,"E3.3.24.5")])],"isStart":false});
            var Q670;
            Q670=makeQuery(id+"F3.opExtrude","CAP_EDGE",EDGE,{"disambiguationData":[OSD([sQuery(id+"F2.wireOp",EDGE,"E2.18.5.1")])],"isStart":false});
            var Q671;
            Q671=makeQuery(id+"F3.opExtrude","CAP_EDGE",EDGE,{"disambiguationData":[OSD([sQuery(id+"F2.wireOp",EDGE,"E3.3.25.5")])],"isStart":false});
            var Q672;
            Q672=makeQuery(id+"F3.opExtrude","CAP_EDGE",EDGE,{"disambiguationData":[OSD([sQuery(id+"F2.wireOp",EDGE,"E2.12.5.1")])],"isStart":false});
            var Q673;
            Q673=makeQuery(id+"F3.opExtrude","CAP_EDGE",EDGE,{"disambiguationData":[OSD([sQuery(id+"F2.wireOp",EDGE,"E3.3.23.5")])],"isStart":false});
            var Q674;
            Q674=makeQuery(id+"F3.opExtrude","CAP_EDGE",EDGE,{"disambiguationData":[OSD([sQuery(id+"F2.wireOp",EDGE,"E2.3.5.1")])],"isStart":false});
            var Q675;
            Q675=makeQuery(id+"F3.opExtrude","CAP_EDGE",EDGE,{"disambiguationData":[OSD([sQuery(id+"F2.wireOp",EDGE,"E3.3.22.5")])],"isStart":false});
            var Q676;
            Q676=makeQuery(id+"F3.opExtrude","CAP_EDGE",EDGE,{"disambiguationData":[OSD([sQuery(id+"F2.wireOp",EDGE,"E3.3.28.5")])],"isStart":false});
            var Q677;
            Q677=makeQuery(id+"F3.opExtrude","CAP_EDGE",EDGE,{"disambiguationData":[OSD([sQuery(id+"F2.wireOp",EDGE,"E2.15.5.1")])],"isStart":false});
            var Q678;
            Q678=makeQuery(id+"F3.opExtrude","CAP_EDGE",EDGE,{"disambiguationData":[OSD([sQuery(id+"F2.wireOp",EDGE,"E2.9.5.1")])],"isStart":false});
            var Q679;
            Q679=makeQuery(id+"F3.opExtrude","CAP_EDGE",EDGE,{"disambiguationData":[OSD([sQuery(id+"F2.wireOp",EDGE,"E2.19.5.1")])],"isStart":false});
            var Q680;
            Q680=makeQuery(id+"F3.opExtrude","CAP_EDGE",EDGE,{"disambiguationData":[OSD([sQuery(id+"F2.wireOp",EDGE,"E2.6.5.1")])],"isStart":false});
            var Q681;
            Q681=makeQuery(id+"F3.opExtrude","CAP_EDGE",EDGE,{"disambiguationData":[OSD([sQuery(id+"F2.wireOp",EDGE,"E3.3.26.5")])],"isStart":false});
            var Q682;
            Q682=makeQuery(id+"F3.opExtrude","CAP_EDGE",EDGE,{"disambiguationData":[OSD([sQuery(id+"F2.wireOp",EDGE,"E2.13.5.1")])],"isStart":false});
            var Q683;
            Q683=makeQuery(id+"F3.opExtrude","CAP_EDGE",EDGE,{"disambiguationData":[OSD([sQuery(id+"F2.wireOp",EDGE,"E3.3.20.5")])],"isStart":false});
            var Q684;
            Q684=makeQuery(id+"F3.opExtrude","CAP_EDGE",EDGE,{"disambiguationData":[OSD([sQuery(id+"F2.wireOp",EDGE,"E2.7.5.1")])],"isStart":false});
            var Q685;
            Q685=makeQuery(id+"F3.opExtrude","CAP_EDGE",EDGE,{"disambiguationData":[OSD([sQuery(id+"F2.wireOp",EDGE,"E2.14.5.1")])],"isStart":false});
            var Q686;
            Q686=makeQuery(id+"F3.opExtrude","CAP_EDGE",EDGE,{"disambiguationData":[OSD([sQuery(id+"F2.wireOp",EDGE,"E2.1.5.1")])],"isStart":false});
            var Q687;
            Q687=makeQuery(id+"F3.opExtrude","CAP_EDGE",EDGE,{"disambiguationData":[OSD([sQuery(id+"F2.wireOp",EDGE,"E2.8.5.1")])],"isStart":false});
            var Q688;
            Q688=makeQuery(id+"F3.opExtrude","CAP_EDGE",EDGE,{"disambiguationData":[OSD([sQuery(id+"F2.wireOp",EDGE,"E3.3.27.5")])],"isStart":false});
            var Q689;
            Q689=makeQuery(id+"F3.opExtrude","CAP_EDGE",EDGE,{"disambiguationData":[OSD([sQuery(id+"F2.wireOp",EDGE,"E2.2.5.1")])],"isStart":false});
            var Q690;
            Q690=makeQuery(id+"F3.opExtrude","CAP_EDGE",EDGE,{"disambiguationData":[OSD([sQuery(id+"F2.wireOp",EDGE,"E3.3.21.5")])],"isStart":false});
            var Q691;
            Q691=makeQuery(id+"F3.opExtrude","CAP_EDGE",EDGE,{"disambiguationData":[OSD([sQuery(id+"F2.wireOp",EDGE,"E3.9.23.5")])],"isStart":false});
            var Q692;
            Q692=makeQuery(id+"F3.opExtrude","CAP_EDGE",EDGE,{"disambiguationData":[OSD([sQuery(id+"F2.wireOp",EDGE,"E2.3.5.3")])],"isStart":false});
            var Q693;
            Q693=makeQuery(id+"F3.opExtrude","CAP_EDGE",EDGE,{"disambiguationData":[OSD([sQuery(id+"F2.wireOp",EDGE,"E3.9.22.5")])],"isStart":false});
            var Q694;
            Q694=makeQuery(id+"F3.opExtrude","CAP_EDGE",EDGE,{"disambiguationData":[OSD([sQuery(id+"F2.wireOp",EDGE,"E3.9.29.5")])],"isStart":false});
            var Q695;
            Q695=makeQuery(id+"F3.opExtrude","CAP_EDGE",EDGE,{"disambiguationData":[OSD([sQuery(id+"F2.wireOp",EDGE,"E2.16.5.3")])],"isStart":false});
            var Q696;
            Q696=makeQuery(id+"F3.opExtrude","CAP_EDGE",EDGE,{"disambiguationData":[OSD([sQuery(id+"F2.wireOp",EDGE,"E2.10.5.3")])],"isStart":false});
            var Q697;
            Q697=makeQuery(id+"F3.opExtrude","CAP_EDGE",EDGE,{"disambiguationData":[OSD([sQuery(id+"F2.wireOp",EDGE,"E3.9.26.5")])],"isStart":false});
            var Q698;
            Q698=makeQuery(id+"F3.opExtrude","CAP_EDGE",EDGE,{"disambiguationData":[OSD([sQuery(id+"F2.wireOp",EDGE,"E2.13.5.3")])],"isStart":false});
            var Q699;
            Q699=makeQuery(id+"F3.opExtrude","CAP_EDGE",EDGE,{"disambiguationData":[OSD([sQuery(id+"F2.wireOp",EDGE,"E3.9.20.5")])],"isStart":false});
            var Q700;
            Q700=makeQuery(id+"F3.opExtrude","CAP_EDGE",EDGE,{"disambiguationData":[OSD([sQuery(id+"F2.wireOp",EDGE,"E2.7.5.3")])],"isStart":false});
            var Q701;
            Q701=makeQuery(id+"F3.opExtrude","CAP_EDGE",EDGE,{"disambiguationData":[OSD([sQuery(id+"F2.wireOp",EDGE,"E2.14.5.3")])],"isStart":false});
            var Q702;
            Q702=makeQuery(id+"F3.opExtrude","CAP_EDGE",EDGE,{"disambiguationData":[OSD([sQuery(id+"F2.wireOp",EDGE,"E2.1.5.3")])],"isStart":false});
            var Q703;
            Q703=makeQuery(id+"F3.opExtrude","CAP_EDGE",EDGE,{"disambiguationData":[OSD([sQuery(id+"F2.wireOp",EDGE,"E2.8.5.3")])],"isStart":false});
            var Q704;
            Q704=makeQuery(id+"F3.opExtrude","CAP_EDGE",EDGE,{"disambiguationData":[OSD([sQuery(id+"F2.wireOp",EDGE,"E3.9.27.5")])],"isStart":false});
            var Q705;
            Q705=makeQuery(id+"F3.opExtrude","CAP_EDGE",EDGE,{"disambiguationData":[OSD([sQuery(id+"F2.wireOp",EDGE,"E2.2.5.3")])],"isStart":false});
            var Q706;
            Q706=makeQuery(id+"F3.opExtrude","CAP_EDGE",EDGE,{"disambiguationData":[OSD([sQuery(id+"F2.wireOp",EDGE,"E3.9.21.5")])],"isStart":false});
            var Q707;
            Q707=makeQuery(id+"F3.opExtrude","CAP_EDGE",EDGE,{"disambiguationData":[OSD([sQuery(id+"F2.wireOp",EDGE,"E3.9.28.5")])],"isStart":false});
            var Q708;
            Q708=makeQuery(id+"F3.opExtrude","CAP_EDGE",EDGE,{"disambiguationData":[OSD([sQuery(id+"F2.wireOp",EDGE,"E2.15.5.3")])],"isStart":false});
            var Q709;
            Q709=makeQuery(id+"F3.opExtrude","CAP_EDGE",EDGE,{"disambiguationData":[OSD([sQuery(id+"F2.wireOp",EDGE,"E2.9.5.3")])],"isStart":false});
            var Q710;
            Q710=makeQuery(id+"F3.opExtrude","CAP_EDGE",EDGE,{"disambiguationData":[OSD([sQuery(id+"F2.wireOp",EDGE,"E2.17.5.3")])],"isStart":false});
            var Q711;
            Q711=makeQuery(id+"F3.opExtrude","CAP_EDGE",EDGE,{"disambiguationData":[OSD([sQuery(id+"F2.wireOp",EDGE,"E2.4.5.3")])],"isStart":false});
            var Q712;
            Q712=makeQuery(id+"F3.opExtrude","CAP_EDGE",EDGE,{"disambiguationData":[OSD([sQuery(id+"F2.wireOp",EDGE,"E2.11.5.3")])],"isStart":false});
            var Q713;
            Q713=makeQuery(id+"F3.opExtrude","CAP_EDGE",EDGE,{"disambiguationData":[OSD([sQuery(id+"F2.wireOp",EDGE,"E2.5.5.3")])],"isStart":false});
            var Q714;
            Q714=makeQuery(id+"F3.opExtrude","CAP_EDGE",EDGE,{"disambiguationData":[OSD([sQuery(id+"F2.wireOp",EDGE,"E3.9.24.5")])],"isStart":false});
            var Q715;
            Q715=makeQuery(id+"F3.opExtrude","CAP_EDGE",EDGE,{"disambiguationData":[OSD([sQuery(id+"F2.wireOp",EDGE,"E2.18.5.3")])],"isStart":false});
            var Q716;
            Q716=makeQuery(id+"F3.opExtrude","CAP_EDGE",EDGE,{"disambiguationData":[OSD([sQuery(id+"F2.wireOp",EDGE,"E3.9.25.5")])],"isStart":false});
            var Q717;
            Q717=makeQuery(id+"F3.opExtrude","CAP_EDGE",EDGE,{"disambiguationData":[OSD([sQuery(id+"F2.wireOp",EDGE,"E2.12.5.3")])],"isStart":false});
            var Q718;
            Q718=makeQuery(id+"F3.opExtrude","CAP_EDGE",EDGE,{"disambiguationData":[OSD([sQuery(id+"F2.wireOp",EDGE,"E2.19.5.3")])],"isStart":false});
            var Q719;
            Q719=makeQuery(id+"F3.opExtrude","CAP_EDGE",EDGE,{"disambiguationData":[OSD([sQuery(id+"F2.wireOp",EDGE,"E2.6.5.3")])],"isStart":false});
            var Q720;
            Q720=makeQuery(id+"F3.opExtrude","CAP_EDGE",EDGE,{"disambiguationData":[OSD([sQuery(id+"F2.wireOp",EDGE,"E2.0.6.3")])],"isStart":false});
            var Q721;
            Q721=makeQuery(id+"F3.opExtrude","CAP_EDGE",EDGE,{"disambiguationData":[OSD([sQuery(id+"F2.wireOp",EDGE,"E2.0.6.0")])],"isStart":false});
            var Q722;
            Q722=makeQuery(id+"F3.opExtrude","CAP_EDGE",EDGE,{"disambiguationData":[OSD([sQuery(id+"F2.wireOp",EDGE,"E2.0.6.2")])],"isStart":false});
            var Q723;
            Q723=makeQuery(id+"F3.opExtrude","CAP_EDGE",EDGE,{"disambiguationData":[OSD([sQuery(id+"F2.wireOp",EDGE,"E3.9.23.6")])],"isStart":false});
            var Q724;
            Q724=makeQuery(id+"F3.opExtrude","CAP_EDGE",EDGE,{"disambiguationData":[OSD([sQuery(id+"F2.wireOp",EDGE,"E2.3.6.3")])],"isStart":false});
            var Q725;
            Q725=makeQuery(id+"F3.opExtrude","CAP_EDGE",EDGE,{"disambiguationData":[OSD([sQuery(id+"F2.wireOp",EDGE,"E3.9.22.6")])],"isStart":false});
            var Q726;
            Q726=makeQuery(id+"F3.opExtrude","CAP_EDGE",EDGE,{"disambiguationData":[OSD([sQuery(id+"F2.wireOp",EDGE,"E2.19.6.3")])],"isStart":false});
            var Q727;
            Q727=makeQuery(id+"F3.opExtrude","CAP_EDGE",EDGE,{"disambiguationData":[OSD([sQuery(id+"F2.wireOp",EDGE,"E2.6.6.3")])],"isStart":false});
            var Q728;
            Q728=makeQuery(id+"F3.opExtrude","CAP_EDGE",EDGE,{"disambiguationData":[OSD([sQuery(id+"F2.wireOp",EDGE,"E3.9.26.6")])],"isStart":false});
            var Q729;
            Q729=makeQuery(id+"F3.opExtrude","CAP_EDGE",EDGE,{"disambiguationData":[OSD([sQuery(id+"F2.wireOp",EDGE,"E2.13.6.3")])],"isStart":false});
            var Q730;
            Q730=makeQuery(id+"F3.opExtrude","CAP_EDGE",EDGE,{"disambiguationData":[OSD([sQuery(id+"F2.wireOp",EDGE,"E3.9.20.6")])],"isStart":false});
            var Q731;
            Q731=makeQuery(id+"F3.opExtrude","CAP_EDGE",EDGE,{"disambiguationData":[OSD([sQuery(id+"F2.wireOp",EDGE,"E2.7.6.3")])],"isStart":false});
            var Q732;
            Q732=makeQuery(id+"F3.opExtrude","CAP_EDGE",EDGE,{"disambiguationData":[OSD([sQuery(id+"F2.wireOp",EDGE,"E2.14.6.3")])],"isStart":false});
            var Q733;
            Q733=makeQuery(id+"F3.opExtrude","CAP_EDGE",EDGE,{"disambiguationData":[OSD([sQuery(id+"F2.wireOp",EDGE,"E2.1.6.3")])],"isStart":false});
            var Q734;
            Q734=makeQuery(id+"F3.opExtrude","CAP_EDGE",EDGE,{"disambiguationData":[OSD([sQuery(id+"F2.wireOp",EDGE,"E2.8.6.3")])],"isStart":false});
            var Q735;
            Q735=makeQuery(id+"F3.opExtrude","CAP_EDGE",EDGE,{"disambiguationData":[OSD([sQuery(id+"F2.wireOp",EDGE,"E3.9.27.6")])],"isStart":false});
            var Q736;
            Q736=makeQuery(id+"F3.opExtrude","CAP_EDGE",EDGE,{"disambiguationData":[OSD([sQuery(id+"F2.wireOp",EDGE,"E2.2.6.3")])],"isStart":false});
            var Q737;
            Q737=makeQuery(id+"F3.opExtrude","CAP_EDGE",EDGE,{"disambiguationData":[OSD([sQuery(id+"F2.wireOp",EDGE,"E3.9.21.6")])],"isStart":false});
            var Q738;
            Q738=makeQuery(id+"F3.opExtrude","CAP_EDGE",EDGE,{"disambiguationData":[OSD([sQuery(id+"F2.wireOp",EDGE,"E3.9.29.6")])],"isStart":false});
            var Q739;
            Q739=makeQuery(id+"F3.opExtrude","CAP_EDGE",EDGE,{"disambiguationData":[OSD([sQuery(id+"F2.wireOp",EDGE,"E2.16.6.3")])],"isStart":false});
            var Q740;
            Q740=makeQuery(id+"F3.opExtrude","CAP_EDGE",EDGE,{"disambiguationData":[OSD([sQuery(id+"F2.wireOp",EDGE,"E2.10.6.3")])],"isStart":false});
            var Q741;
            Q741=makeQuery(id+"F3.opExtrude","CAP_EDGE",EDGE,{"disambiguationData":[OSD([sQuery(id+"F2.wireOp",EDGE,"E2.4.6.3")])],"isStart":false});
            var Q742;
            Q742=makeQuery(id+"F3.opExtrude","CAP_EDGE",EDGE,{"disambiguationData":[OSD([sQuery(id+"F2.wireOp",EDGE,"E2.17.6.3")])],"isStart":false});
            var Q743;
            Q743=makeQuery(id+"F3.opExtrude","CAP_EDGE",EDGE,{"disambiguationData":[OSD([sQuery(id+"F2.wireOp",EDGE,"E3.9.24.6")])],"isStart":false});
            var Q744;
            Q744=makeQuery(id+"F3.opExtrude","CAP_EDGE",EDGE,{"disambiguationData":[OSD([sQuery(id+"F2.wireOp",EDGE,"E2.5.6.3")])],"isStart":false});
            var Q745;
            Q745=makeQuery(id+"F3.opExtrude","CAP_EDGE",EDGE,{"disambiguationData":[OSD([sQuery(id+"F2.wireOp",EDGE,"E2.11.6.3")])],"isStart":false});
            var Q746;
            Q746=makeQuery(id+"F3.opExtrude","CAP_EDGE",EDGE,{"disambiguationData":[OSD([sQuery(id+"F2.wireOp",EDGE,"E2.18.6.3")])],"isStart":false});
            var Q747;
            Q747=makeQuery(id+"F3.opExtrude","CAP_EDGE",EDGE,{"disambiguationData":[OSD([sQuery(id+"F2.wireOp",EDGE,"E3.9.25.6")])],"isStart":false});
            var Q748;
            Q748=makeQuery(id+"F3.opExtrude","CAP_EDGE",EDGE,{"disambiguationData":[OSD([sQuery(id+"F2.wireOp",EDGE,"E2.12.6.3")])],"isStart":false});
            var Q749;
            Q749=makeQuery(id+"F3.opExtrude","CAP_EDGE",EDGE,{"disambiguationData":[OSD([sQuery(id+"F2.wireOp",EDGE,"E3.0.23.6")])],"isStart":false});
            var Q750;
            Q750=makeQuery(id+"F3.opExtrude","CAP_EDGE",EDGE,{"disambiguationData":[OSD([sQuery(id+"F2.wireOp",EDGE,"E2.3.6.0")])],"isStart":false});
            var Q751;
            Q751=makeQuery(id+"F3.opExtrude","CAP_EDGE",EDGE,{"disambiguationData":[OSD([sQuery(id+"F2.wireOp",EDGE,"E3.0.22.6")])],"isStart":false});
            var Q752;
            Q752=makeQuery(id+"F3.opExtrude","CAP_EDGE",EDGE,{"disambiguationData":[OSD([sQuery(id+"F2.wireOp",EDGE,"E3.0.29.6")])],"isStart":false});
            var Q753;
            Q753=makeQuery(id+"F3.opExtrude","CAP_EDGE",EDGE,{"disambiguationData":[OSD([sQuery(id+"F2.wireOp",EDGE,"E2.16.6.0")])],"isStart":false});
            var Q754;
            Q754=makeQuery(id+"F3.opExtrude","CAP_EDGE",EDGE,{"disambiguationData":[OSD([sQuery(id+"F2.wireOp",EDGE,"E3.9.28.6")])],"isStart":false});
            var Q755;
            Q755=makeQuery(id+"F3.opExtrude","CAP_EDGE",EDGE,{"disambiguationData":[OSD([sQuery(id+"F2.wireOp",EDGE,"E2.15.6.3")])],"isStart":false});
            var Q756;
            Q756=makeQuery(id+"F3.opExtrude","CAP_EDGE",EDGE,{"disambiguationData":[OSD([sQuery(id+"F2.wireOp",EDGE,"E2.9.6.3")])],"isStart":false});
            var Q757;
            Q757=makeQuery(id+"F3.opExtrude","CAP_EDGE",EDGE,{"disambiguationData":[OSD([sQuery(id+"F2.wireOp",EDGE,"E3.0.26.6")])],"isStart":false});
            var Q758;
            Q758=makeQuery(id+"F3.opExtrude","CAP_EDGE",EDGE,{"disambiguationData":[OSD([sQuery(id+"F2.wireOp",EDGE,"E2.13.6.0")])],"isStart":false});
            var Q759;
            Q759=makeQuery(id+"F3.opExtrude","CAP_EDGE",EDGE,{"disambiguationData":[OSD([sQuery(id+"F2.wireOp",EDGE,"E3.0.20.6")])],"isStart":false});
            var Q760;
            Q760=makeQuery(id+"F3.opExtrude","CAP_EDGE",EDGE,{"disambiguationData":[OSD([sQuery(id+"F2.wireOp",EDGE,"E2.7.6.0")])],"isStart":false});
            var Q761;
            Q761=makeQuery(id+"F3.opExtrude","CAP_EDGE",EDGE,{"disambiguationData":[OSD([sQuery(id+"F2.wireOp",EDGE,"E2.14.6.0")])],"isStart":false});
            var Q762;
            Q762=makeQuery(id+"F3.opExtrude","CAP_EDGE",EDGE,{"disambiguationData":[OSD([sQuery(id+"F2.wireOp",EDGE,"E2.1.6.0")])],"isStart":false});
            var Q763;
            Q763=makeQuery(id+"F3.opExtrude","CAP_EDGE",EDGE,{"disambiguationData":[OSD([sQuery(id+"F2.wireOp",EDGE,"E3.0.21.6")])],"isStart":false});
            var Q764;
            Q764=makeQuery(id+"F3.opExtrude","CAP_EDGE",EDGE,{"disambiguationData":[OSD([sQuery(id+"F2.wireOp",EDGE,"E3.0.27.6")])],"isStart":false});
            var Q765;
            Q765=makeQuery(id+"F3.opExtrude","CAP_EDGE",EDGE,{"disambiguationData":[OSD([sQuery(id+"F2.wireOp",EDGE,"E2.8.6.0")])],"isStart":false});
            var Q766;
            Q766=makeQuery(id+"F3.opExtrude","CAP_EDGE",EDGE,{"disambiguationData":[OSD([sQuery(id+"F2.wireOp",EDGE,"E2.15.6.0")])],"isStart":false});
            var Q767;
            Q767=makeQuery(id+"F3.opExtrude","CAP_EDGE",EDGE,{"disambiguationData":[OSD([sQuery(id+"F2.wireOp",EDGE,"E2.2.6.0")])],"isStart":false});
            var Q768;
            Q768=makeQuery(id+"F3.opExtrude","CAP_EDGE",EDGE,{"disambiguationData":[OSD([sQuery(id+"F2.wireOp",EDGE,"E2.9.6.0")])],"isStart":false});
            var Q769;
            Q769=makeQuery(id+"F3.opExtrude","CAP_EDGE",EDGE,{"disambiguationData":[OSD([sQuery(id+"F2.wireOp",EDGE,"E3.0.28.6")])],"isStart":false});
            var Q770;
            Q770=makeQuery(id+"F3.opExtrude","CAP_EDGE",EDGE,{"disambiguationData":[OSD([sQuery(id+"F2.wireOp",EDGE,"E2.10.6.0")])],"isStart":false});
            var Q771;
            Q771=makeQuery(id+"F3.opExtrude","CAP_EDGE",EDGE,{"disambiguationData":[OSD([sQuery(id+"F2.wireOp",EDGE,"E2.17.6.0")])],"isStart":false});
            var Q772;
            Q772=makeQuery(id+"F3.opExtrude","CAP_EDGE",EDGE,{"disambiguationData":[OSD([sQuery(id+"F2.wireOp",EDGE,"E2.4.6.0")])],"isStart":false});
            var Q773;
            Q773=makeQuery(id+"F3.opExtrude","CAP_EDGE",EDGE,{"disambiguationData":[OSD([sQuery(id+"F2.wireOp",EDGE,"E2.11.6.0")])],"isStart":false});
            var Q774;
            Q774=makeQuery(id+"F3.opExtrude","CAP_EDGE",EDGE,{"disambiguationData":[OSD([sQuery(id+"F2.wireOp",EDGE,"E2.5.6.0")])],"isStart":false});
            var Q775;
            Q775=makeQuery(id+"F3.opExtrude","CAP_EDGE",EDGE,{"disambiguationData":[OSD([sQuery(id+"F2.wireOp",EDGE,"E3.0.24.6")])],"isStart":false});
            var Q776;
            Q776=makeQuery(id+"F3.opExtrude","CAP_EDGE",EDGE,{"disambiguationData":[OSD([sQuery(id+"F2.wireOp",EDGE,"E2.18.6.0")])],"isStart":false});
            var Q777;
            Q777=makeQuery(id+"F3.opExtrude","CAP_EDGE",EDGE,{"disambiguationData":[OSD([sQuery(id+"F2.wireOp",EDGE,"E3.0.25.6")])],"isStart":false});
            var Q778;
            Q778=makeQuery(id+"F3.opExtrude","CAP_EDGE",EDGE,{"disambiguationData":[OSD([sQuery(id+"F2.wireOp",EDGE,"E2.12.6.0")])],"isStart":false});
            var Q779;
            Q779=makeQuery(id+"F3.opExtrude","CAP_EDGE",EDGE,{"disambiguationData":[OSD([sQuery(id+"F2.wireOp",EDGE,"E2.19.6.0")])],"isStart":false});
            var Q780;
            Q780=makeQuery(id+"F3.opExtrude","CAP_EDGE",EDGE,{"disambiguationData":[OSD([sQuery(id+"F2.wireOp",EDGE,"E2.6.6.0")])],"isStart":false});
            var Q781;
            Q781=makeQuery(id+"F3.opExtrude","CAP_EDGE",EDGE,{"disambiguationData":[OSD([sQuery(id+"F2.wireOp",EDGE,"E2.0.6.1")])],"isStart":false});
            var Q782;
            Q782=makeQuery(id+"F3.opExtrude","CAP_EDGE",EDGE,{"disambiguationData":[OSD([sQuery(id+"F2.wireOp",EDGE,"E2.10.6.2")])],"isStart":false});
            var Q783;
            Q783=makeQuery(id+"F3.opExtrude","CAP_EDGE",EDGE,{"disambiguationData":[OSD([sQuery(id+"F2.wireOp",EDGE,"E2.17.6.2")])],"isStart":false});
            var Q784;
            Q784=makeQuery(id+"F3.opExtrude","CAP_EDGE",EDGE,{"disambiguationData":[OSD([sQuery(id+"F2.wireOp",EDGE,"E2.4.6.2")])],"isStart":false});
            var Q785;
            Q785=makeQuery(id+"F3.opExtrude","CAP_EDGE",EDGE,{"disambiguationData":[OSD([sQuery(id+"F2.wireOp",EDGE,"E2.11.6.2")])],"isStart":false});
            var Q786;
            Q786=makeQuery(id+"F3.opExtrude","CAP_EDGE",EDGE,{"disambiguationData":[OSD([sQuery(id+"F2.wireOp",EDGE,"E2.5.6.2")])],"isStart":false});
            var Q787;
            Q787=makeQuery(id+"F3.opExtrude","CAP_EDGE",EDGE,{"disambiguationData":[OSD([sQuery(id+"F2.wireOp",EDGE,"E3.6.24.6")])],"isStart":false});
            var Q788;
            Q788=makeQuery(id+"F3.opExtrude","CAP_EDGE",EDGE,{"disambiguationData":[OSD([sQuery(id+"F2.wireOp",EDGE,"E2.18.6.2")])],"isStart":false});
            var Q789;
            Q789=makeQuery(id+"F3.opExtrude","CAP_EDGE",EDGE,{"disambiguationData":[OSD([sQuery(id+"F2.wireOp",EDGE,"E3.6.25.6")])],"isStart":false});
            var Q790;
            Q790=makeQuery(id+"F3.opExtrude","CAP_EDGE",EDGE,{"disambiguationData":[OSD([sQuery(id+"F2.wireOp",EDGE,"E2.12.6.2")])],"isStart":false});
            var Q791;
            Q791=makeQuery(id+"F3.opExtrude","CAP_EDGE",EDGE,{"disambiguationData":[OSD([sQuery(id+"F2.wireOp",EDGE,"E2.19.6.2")])],"isStart":false});
            var Q792;
            Q792=makeQuery(id+"F3.opExtrude","CAP_EDGE",EDGE,{"disambiguationData":[OSD([sQuery(id+"F2.wireOp",EDGE,"E2.6.6.2")])],"isStart":false});
            var Q793;
            Q793=makeQuery(id+"F3.opExtrude","CAP_EDGE",EDGE,{"disambiguationData":[OSD([sQuery(id+"F2.wireOp",EDGE,"E3.6.23.6")])],"isStart":false});
            var Q794;
            Q794=makeQuery(id+"F3.opExtrude","CAP_EDGE",EDGE,{"disambiguationData":[OSD([sQuery(id+"F2.wireOp",EDGE,"E2.3.6.2")])],"isStart":false});
            var Q795;
            Q795=makeQuery(id+"F3.opExtrude","CAP_EDGE",EDGE,{"disambiguationData":[OSD([sQuery(id+"F2.wireOp",EDGE,"E3.6.22.6")])],"isStart":false});
            var Q796;
            Q796=makeQuery(id+"F3.opExtrude","CAP_EDGE",EDGE,{"disambiguationData":[OSD([sQuery(id+"F2.wireOp",EDGE,"E3.6.29.6")])],"isStart":false});
            var Q797;
            Q797=makeQuery(id+"F3.opExtrude","CAP_EDGE",EDGE,{"disambiguationData":[OSD([sQuery(id+"F2.wireOp",EDGE,"E2.16.6.2")])],"isStart":false});
            var Q798;
            Q798=makeQuery(id+"F3.opExtrude","CAP_EDGE",EDGE,{"disambiguationData":[OSD([sQuery(id+"F2.wireOp",EDGE,"E2.9.6.2")])],"isStart":false});
            var Q799;
            Q799=makeQuery(id+"F3.opExtrude","CAP_EDGE",EDGE,{"disambiguationData":[OSD([sQuery(id+"F2.wireOp",EDGE,"E3.6.26.6")])],"isStart":false});
            var Q800;
            Q800=makeQuery(id+"F3.opExtrude","CAP_EDGE",EDGE,{"disambiguationData":[OSD([sQuery(id+"F2.wireOp",EDGE,"E2.13.6.2")])],"isStart":false});
            var Q801;
            Q801=makeQuery(id+"F3.opExtrude","CAP_EDGE",EDGE,{"disambiguationData":[OSD([sQuery(id+"F2.wireOp",EDGE,"E3.6.20.6")])],"isStart":false});
            var Q802;
            Q802=makeQuery(id+"F3.opExtrude","CAP_EDGE",EDGE,{"disambiguationData":[OSD([sQuery(id+"F2.wireOp",EDGE,"E2.7.6.2")])],"isStart":false});
            var Q803;
            Q803=makeQuery(id+"F3.opExtrude","CAP_EDGE",EDGE,{"disambiguationData":[OSD([sQuery(id+"F2.wireOp",EDGE,"E2.14.6.2")])],"isStart":false});
            var Q804;
            Q804=makeQuery(id+"F3.opExtrude","CAP_EDGE",EDGE,{"disambiguationData":[OSD([sQuery(id+"F2.wireOp",EDGE,"E2.1.6.2")])],"isStart":false});
            var Q805;
            Q805=makeQuery(id+"F3.opExtrude","CAP_EDGE",EDGE,{"disambiguationData":[OSD([sQuery(id+"F2.wireOp",EDGE,"E2.8.6.2")])],"isStart":false});
            var Q806;
            Q806=makeQuery(id+"F3.opExtrude","CAP_EDGE",EDGE,{"disambiguationData":[OSD([sQuery(id+"F2.wireOp",EDGE,"E3.6.27.6")])],"isStart":false});
            var Q807;
            Q807=makeQuery(id+"F3.opExtrude","CAP_EDGE",EDGE,{"disambiguationData":[OSD([sQuery(id+"F2.wireOp",EDGE,"E2.2.6.2")])],"isStart":false});
            var Q808;
            Q808=makeQuery(id+"F3.opExtrude","CAP_EDGE",EDGE,{"disambiguationData":[OSD([sQuery(id+"F2.wireOp",EDGE,"E3.6.21.6")])],"isStart":false});
            var Q809;
            Q809=makeQuery(id+"F3.opExtrude","CAP_EDGE",EDGE,{"disambiguationData":[OSD([sQuery(id+"F2.wireOp",EDGE,"E3.6.28.6")])],"isStart":false});
            var Q810;
            Q810=makeQuery(id+"F3.opExtrude","CAP_EDGE",EDGE,{"disambiguationData":[OSD([sQuery(id+"F2.wireOp",EDGE,"E2.15.6.2")])],"isStart":false});
            var Q811;
            Q811=makeQuery(id+"F3.opExtrude","CAP_EDGE",EDGE,{"disambiguationData":[OSD([sQuery(id+"F2.wireOp",EDGE,"E3.3.23.6")])],"isStart":false});
            var Q812;
            Q812=makeQuery(id+"F3.opExtrude","CAP_EDGE",EDGE,{"disambiguationData":[OSD([sQuery(id+"F2.wireOp",EDGE,"E2.3.6.1")])],"isStart":false});
            var Q813;
            Q813=makeQuery(id+"F3.opExtrude","CAP_EDGE",EDGE,{"disambiguationData":[OSD([sQuery(id+"F2.wireOp",EDGE,"E3.3.22.6")])],"isStart":false});
            var Q814;
            Q814=makeQuery(id+"F3.opExtrude","CAP_EDGE",EDGE,{"disambiguationData":[OSD([sQuery(id+"F2.wireOp",EDGE,"E3.3.29.6")])],"isStart":false});
            var Q815;
            Q815=makeQuery(id+"F3.opExtrude","CAP_EDGE",EDGE,{"disambiguationData":[OSD([sQuery(id+"F2.wireOp",EDGE,"E2.16.6.1")])],"isStart":false});
            var Q816;
            Q816=makeQuery(id+"F3.opExtrude","CAP_EDGE",EDGE,{"disambiguationData":[OSD([sQuery(id+"F2.wireOp",EDGE,"E2.10.6.1")])],"isStart":false});
            var Q817;
            Q817=makeQuery(id+"F3.opExtrude","CAP_EDGE",EDGE,{"disambiguationData":[OSD([sQuery(id+"F2.wireOp",EDGE,"E2.17.6.1")])],"isStart":false});
            var Q818;
            Q818=makeQuery(id+"F3.opExtrude","CAP_EDGE",EDGE,{"disambiguationData":[OSD([sQuery(id+"F2.wireOp",EDGE,"E2.4.6.1")])],"isStart":false});
            var Q819;
            Q819=makeQuery(id+"F3.opExtrude","CAP_EDGE",EDGE,{"disambiguationData":[OSD([sQuery(id+"F2.wireOp",EDGE,"E2.11.6.1")])],"isStart":false});
            var Q820;
            Q820=makeQuery(id+"F3.opExtrude","CAP_EDGE",EDGE,{"disambiguationData":[OSD([sQuery(id+"F2.wireOp",EDGE,"E2.14.6.1")])],"isStart":false});
            var Q821;
            Q821=makeQuery(id+"F3.opExtrude","CAP_EDGE",EDGE,{"disambiguationData":[OSD([sQuery(id+"F2.wireOp",EDGE,"E2.1.6.1")])],"isStart":false});
            var Q822;
            Q822=makeQuery(id+"F3.opExtrude","CAP_EDGE",EDGE,{"disambiguationData":[OSD([sQuery(id+"F2.wireOp",EDGE,"E2.8.6.1")])],"isStart":false});
            var Q823;
            Q823=makeQuery(id+"F3.opExtrude","CAP_EDGE",EDGE,{"disambiguationData":[OSD([sQuery(id+"F2.wireOp",EDGE,"E3.3.27.6")])],"isStart":false});
            var Q824;
            Q824=makeQuery(id+"F3.opExtrude","CAP_EDGE",EDGE,{"disambiguationData":[OSD([sQuery(id+"F2.wireOp",EDGE,"E2.15.6.1")])],"isStart":false});
            var Q825;
            Q825=makeQuery(id+"F3.opExtrude","CAP_EDGE",EDGE,{"disambiguationData":[OSD([sQuery(id+"F2.wireOp",EDGE,"E3.3.21.6")])],"isStart":false});
            var Q826;
            Q826=makeQuery(id+"F3.opExtrude","CAP_EDGE",EDGE,{"disambiguationData":[OSD([sQuery(id+"F2.wireOp",EDGE,"E2.2.6.1")])],"isStart":false});
            var Q827;
            Q827=makeQuery(id+"F3.opExtrude","CAP_EDGE",EDGE,{"disambiguationData":[OSD([sQuery(id+"F2.wireOp",EDGE,"E2.9.6.1")])],"isStart":false});
            var Q828;
            Q828=makeQuery(id+"F3.opExtrude","CAP_EDGE",EDGE,{"disambiguationData":[OSD([sQuery(id+"F2.wireOp",EDGE,"E3.3.28.6")])],"isStart":false});
            var Q829;
            Q829=makeQuery(id+"F3.opExtrude","CAP_EDGE",EDGE,{"disambiguationData":[OSD([sQuery(id+"F2.wireOp",EDGE,"E2.5.6.1")])],"isStart":false});
            var Q830;
            Q830=makeQuery(id+"F3.opExtrude","CAP_EDGE",EDGE,{"disambiguationData":[OSD([sQuery(id+"F2.wireOp",EDGE,"E3.3.24.6")])],"isStart":false});
            var Q831;
            Q831=makeQuery(id+"F3.opExtrude","CAP_EDGE",EDGE,{"disambiguationData":[OSD([sQuery(id+"F2.wireOp",EDGE,"E2.18.6.1")])],"isStart":false});
            var Q832;
            Q832=makeQuery(id+"F3.opExtrude","CAP_EDGE",EDGE,{"disambiguationData":[OSD([sQuery(id+"F2.wireOp",EDGE,"E3.3.25.6")])],"isStart":false});
            var Q833;
            Q833=makeQuery(id+"F3.opExtrude","CAP_EDGE",EDGE,{"disambiguationData":[OSD([sQuery(id+"F2.wireOp",EDGE,"E2.12.6.1")])],"isStart":false});
            var Q834;
            Q834=makeQuery(id+"F3.opExtrude","CAP_EDGE",EDGE,{"disambiguationData":[OSD([sQuery(id+"F2.wireOp",EDGE,"E2.19.6.1")])],"isStart":false});
            var Q835;
            Q835=makeQuery(id+"F3.opExtrude","CAP_EDGE",EDGE,{"disambiguationData":[OSD([sQuery(id+"F2.wireOp",EDGE,"E2.6.6.1")])],"isStart":false});
            var Q836;
            Q836=makeQuery(id+"F3.opExtrude","CAP_EDGE",EDGE,{"disambiguationData":[OSD([sQuery(id+"F2.wireOp",EDGE,"E3.3.26.6")])],"isStart":false});
            var Q837;
            Q837=makeQuery(id+"F3.opExtrude","CAP_EDGE",EDGE,{"disambiguationData":[OSD([sQuery(id+"F2.wireOp",EDGE,"E2.13.6.1")])],"isStart":false});
            var Q838;
            Q838=makeQuery(id+"F3.opExtrude","CAP_EDGE",EDGE,{"disambiguationData":[OSD([sQuery(id+"F2.wireOp",EDGE,"E3.3.20.6")])],"isStart":false});
            var Q839;
            Q839=makeQuery(id+"F3.opExtrude","CAP_EDGE",EDGE,{"disambiguationData":[OSD([sQuery(id+"F2.wireOp",EDGE,"E2.7.6.1")])],"isStart":false});
            var Q840;
            Q840=makeQuery(id+"F3.opExtrude","CAP_EDGE",EDGE,{"disambiguationData":[OSD([sQuery(id+"F2.wireOp",EDGE,"E2.0.7.0")])],"isStart":false});
            var Q841;
            Q841=makeQuery(id+"F3.opExtrude","CAP_EDGE",EDGE,{"disambiguationData":[OSD([sQuery(id+"F2.wireOp",EDGE,"E2.0.7.2")])],"isStart":false});
            var Q842;
            Q842=makeQuery(id+"F3.opExtrude","CAP_EDGE",EDGE,{"disambiguationData":[OSD([sQuery(id+"F2.wireOp",EDGE,"E3.0.22.7")])],"isStart":false});
            var Q843;
            Q843=makeQuery(id+"F3.opExtrude","CAP_EDGE",EDGE,{"disambiguationData":[OSD([sQuery(id+"F2.wireOp",EDGE,"E2.3.7.0")])],"isStart":false});
            var Q844;
            Q844=makeQuery(id+"F3.opExtrude","CAP_EDGE",EDGE,{"disambiguationData":[OSD([sQuery(id+"F2.wireOp",EDGE,"E3.0.23.7")])],"isStart":false});
            var Q845;
            Q845=makeQuery(id+"F3.opExtrude","CAP_EDGE",EDGE,{"disambiguationData":[OSD([sQuery(id+"F2.wireOp",EDGE,"E3.0.29.7")])],"isStart":false});
            var Q846;
            Q846=makeQuery(id+"F3.opExtrude","CAP_EDGE",EDGE,{"disambiguationData":[OSD([sQuery(id+"F2.wireOp",EDGE,"E2.16.7.0")])],"isStart":false});
            var Q847;
            Q847=makeQuery(id+"F3.opExtrude","CAP_EDGE",EDGE,{"disambiguationData":[OSD([sQuery(id+"F2.wireOp",EDGE,"E2.10.7.0")])],"isStart":false});
            var Q848;
            Q848=makeQuery(id+"F3.opExtrude","CAP_EDGE",EDGE,{"disambiguationData":[OSD([sQuery(id+"F2.wireOp",EDGE,"E2.4.7.0")])],"isStart":false});
            var Q849;
            Q849=makeQuery(id+"F3.opExtrude","CAP_EDGE",EDGE,{"disambiguationData":[OSD([sQuery(id+"F2.wireOp",EDGE,"E3.0.20.7")])],"isStart":false});
            var Q850;
            Q850=makeQuery(id+"F3.opExtrude","CAP_EDGE",EDGE,{"disambiguationData":[OSD([sQuery(id+"F2.wireOp",EDGE,"E2.7.7.0")])],"isStart":false});
            var Q851;
            Q851=makeQuery(id+"F3.opExtrude","CAP_EDGE",EDGE,{"disambiguationData":[OSD([sQuery(id+"F2.wireOp",EDGE,"E2.14.7.0")])],"isStart":false});
            var Q852;
            Q852=makeQuery(id+"F3.opExtrude","CAP_EDGE",EDGE,{"disambiguationData":[OSD([sQuery(id+"F2.wireOp",EDGE,"E2.1.7.0")])],"isStart":false});
            var Q853;
            Q853=makeQuery(id+"F3.opExtrude","CAP_EDGE",EDGE,{"disambiguationData":[OSD([sQuery(id+"F2.wireOp",EDGE,"E2.8.7.0")])],"isStart":false});
            var Q854;
            Q854=makeQuery(id+"F3.opExtrude","CAP_EDGE",EDGE,{"disambiguationData":[OSD([sQuery(id+"F2.wireOp",EDGE,"E3.0.27.7")])],"isStart":false});
            var Q855;
            Q855=makeQuery(id+"F3.opExtrude","CAP_EDGE",EDGE,{"disambiguationData":[OSD([sQuery(id+"F2.wireOp",EDGE,"E2.2.7.0")])],"isStart":false});
            var Q856;
            Q856=makeQuery(id+"F3.opExtrude","CAP_EDGE",EDGE,{"disambiguationData":[OSD([sQuery(id+"F2.wireOp",EDGE,"E3.0.21.7")])],"isStart":false});
            var Q857;
            Q857=makeQuery(id+"F3.opExtrude","CAP_EDGE",EDGE,{"disambiguationData":[OSD([sQuery(id+"F2.wireOp",EDGE,"E3.0.28.7")])],"isStart":false});
            var Q858;
            Q858=makeQuery(id+"F3.opExtrude","CAP_EDGE",EDGE,{"disambiguationData":[OSD([sQuery(id+"F2.wireOp",EDGE,"E2.15.7.0")])],"isStart":false});
            var Q859;
            Q859=makeQuery(id+"F3.opExtrude","CAP_EDGE",EDGE,{"disambiguationData":[OSD([sQuery(id+"F2.wireOp",EDGE,"E2.9.7.0")])],"isStart":false});
            var Q860;
            Q860=makeQuery(id+"F3.opExtrude","CAP_EDGE",EDGE,{"disambiguationData":[OSD([sQuery(id+"F2.wireOp",EDGE,"E2.17.7.0")])],"isStart":false});
            var Q861;
            Q861=makeQuery(id+"F3.opExtrude","CAP_EDGE",EDGE,{"disambiguationData":[OSD([sQuery(id+"F2.wireOp",EDGE,"E3.0.24.7")])],"isStart":false});
            var Q862;
            Q862=makeQuery(id+"F3.opExtrude","CAP_EDGE",EDGE,{"disambiguationData":[OSD([sQuery(id+"F2.wireOp",EDGE,"E2.11.7.0")])],"isStart":false});
            var Q863;
            Q863=makeQuery(id+"F3.opExtrude","CAP_EDGE",EDGE,{"disambiguationData":[OSD([sQuery(id+"F2.wireOp",EDGE,"E2.18.7.0")])],"isStart":false});
            var Q864;
            Q864=makeQuery(id+"F3.opExtrude","CAP_EDGE",EDGE,{"disambiguationData":[OSD([sQuery(id+"F2.wireOp",EDGE,"E2.5.7.0")])],"isStart":false});
            var Q865;
            Q865=makeQuery(id+"F3.opExtrude","CAP_EDGE",EDGE,{"disambiguationData":[OSD([sQuery(id+"F2.wireOp",EDGE,"E2.12.7.0")])],"isStart":false});
            var Q866;
            Q866=makeQuery(id+"F3.opExtrude","CAP_EDGE",EDGE,{"disambiguationData":[OSD([sQuery(id+"F2.wireOp",EDGE,"E2.19.7.0")])],"isStart":false});
            var Q867;
            Q867=makeQuery(id+"F3.opExtrude","CAP_EDGE",EDGE,{"disambiguationData":[OSD([sQuery(id+"F2.wireOp",EDGE,"E3.0.25.7")])],"isStart":false});
            var Q868;
            Q868=makeQuery(id+"F3.opExtrude","CAP_EDGE",EDGE,{"disambiguationData":[OSD([sQuery(id+"F2.wireOp",EDGE,"E2.6.7.0")])],"isStart":false});
            var Q869;
            Q869=makeQuery(id+"F3.opExtrude","CAP_EDGE",EDGE,{"disambiguationData":[OSD([sQuery(id+"F2.wireOp",EDGE,"E3.0.26.7")])],"isStart":false});
            var Q870;
            Q870=makeQuery(id+"F3.opExtrude","CAP_EDGE",EDGE,{"disambiguationData":[OSD([sQuery(id+"F2.wireOp",EDGE,"E2.13.7.0")])],"isStart":false});
            var Q871;
            Q871=makeQuery(id+"F3.opExtrude","CAP_EDGE",EDGE,{"disambiguationData":[OSD([sQuery(id+"F2.wireOp",EDGE,"E2.12.7.2")])],"isStart":false});
            var Q872;
            Q872=makeQuery(id+"F3.opExtrude","CAP_EDGE",EDGE,{"disambiguationData":[OSD([sQuery(id+"F2.wireOp",EDGE,"E2.6.7.2")])],"isStart":false});
            var Q873;
            Q873=makeQuery(id+"F3.opExtrude","CAP_EDGE",EDGE,{"disambiguationData":[OSD([sQuery(id+"F2.wireOp",EDGE,"E3.6.25.7")])],"isStart":false});
            var Q874;
            Q874=makeQuery(id+"F3.opExtrude","CAP_EDGE",EDGE,{"disambiguationData":[OSD([sQuery(id+"F2.wireOp",EDGE,"E2.19.7.2")])],"isStart":false});
            var Q875;
            Q875=makeQuery(id+"F3.opExtrude","CAP_EDGE",EDGE,{"disambiguationData":[OSD([sQuery(id+"F2.wireOp",EDGE,"E3.6.26.7")])],"isStart":false});
            var Q876;
            Q876=makeQuery(id+"F3.opExtrude","CAP_EDGE",EDGE,{"disambiguationData":[OSD([sQuery(id+"F2.wireOp",EDGE,"E2.13.7.2")])],"isStart":false});
            var Q877;
            Q877=makeQuery(id+"F3.opExtrude","CAP_EDGE",EDGE,{"disambiguationData":[OSD([sQuery(id+"F2.wireOp",EDGE,"E3.6.20.7")])],"isStart":false});
            var Q878;
            Q878=makeQuery(id+"F3.opExtrude","CAP_EDGE",EDGE,{"disambiguationData":[OSD([sQuery(id+"F2.wireOp",EDGE,"E2.7.7.2")])],"isStart":false});
            var Q879;
            Q879=makeQuery(id+"F3.opExtrude","CAP_EDGE",EDGE,{"disambiguationData":[OSD([sQuery(id+"F2.wireOp",EDGE,"E2.14.7.2")])],"isStart":false});
            var Q880;
            Q880=makeQuery(id+"F3.opExtrude","CAP_EDGE",EDGE,{"disambiguationData":[OSD([sQuery(id+"F2.wireOp",EDGE,"E2.1.7.2")])],"isStart":false});
            var Q881;
            Q881=makeQuery(id+"F3.opExtrude","CAP_EDGE",EDGE,{"disambiguationData":[OSD([sQuery(id+"F2.wireOp",EDGE,"E2.8.7.2")])],"isStart":false});
            var Q882;
            Q882=makeQuery(id+"F3.opExtrude","CAP_EDGE",EDGE,{"disambiguationData":[OSD([sQuery(id+"F2.wireOp",EDGE,"E3.6.27.7")])],"isStart":false});
            var Q883;
            Q883=makeQuery(id+"F3.opExtrude","CAP_EDGE",EDGE,{"disambiguationData":[OSD([sQuery(id+"F2.wireOp",EDGE,"E3.6.22.7")])],"isStart":false});
            var Q884;
            Q884=makeQuery(id+"F3.opExtrude","CAP_EDGE",EDGE,{"disambiguationData":[OSD([sQuery(id+"F2.wireOp",EDGE,"E3.6.23.7")])],"isStart":false});
            var Q885;
            Q885=makeQuery(id+"F3.opExtrude","CAP_EDGE",EDGE,{"disambiguationData":[OSD([sQuery(id+"F2.wireOp",EDGE,"E2.16.7.2")])],"isStart":false});
            var Q886;
            Q886=makeQuery(id+"F3.opExtrude","CAP_EDGE",EDGE,{"disambiguationData":[OSD([sQuery(id+"F2.wireOp",EDGE,"E2.3.7.2")])],"isStart":false});
            var Q887;
            Q887=makeQuery(id+"F3.opExtrude","CAP_EDGE",EDGE,{"disambiguationData":[OSD([sQuery(id+"F2.wireOp",EDGE,"E2.0.7.1")])],"isStart":false});
            var Q888;
            Q888=makeQuery(id+"F3.opExtrude","CAP_EDGE",EDGE,{"disambiguationData":[OSD([sQuery(id+"F2.wireOp",EDGE,"E3.6.29.7")])],"isStart":false});
            var Q889;
            Q889=makeQuery(id+"F3.opExtrude","CAP_EDGE",EDGE,{"disambiguationData":[OSD([sQuery(id+"F2.wireOp",EDGE,"E2.10.7.2")])],"isStart":false});
            var Q890;
            Q890=makeQuery(id+"F3.opExtrude","CAP_EDGE",EDGE,{"disambiguationData":[OSD([sQuery(id+"F2.wireOp",EDGE,"E2.4.7.2")])],"isStart":false});
            var Q891;
            Q891=makeQuery(id+"F3.opExtrude","CAP_EDGE",EDGE,{"disambiguationData":[OSD([sQuery(id+"F2.wireOp",EDGE,"E2.17.7.2")])],"isStart":false});
            var Q892;
            Q892=makeQuery(id+"F3.opExtrude","CAP_EDGE",EDGE,{"disambiguationData":[OSD([sQuery(id+"F2.wireOp",EDGE,"E3.6.24.7")])],"isStart":false});
            var Q893;
            Q893=makeQuery(id+"F3.opExtrude","CAP_EDGE",EDGE,{"disambiguationData":[OSD([sQuery(id+"F2.wireOp",EDGE,"E2.11.7.2")])],"isStart":false});
            var Q894;
            Q894=makeQuery(id+"F3.opExtrude","CAP_EDGE",EDGE,{"disambiguationData":[OSD([sQuery(id+"F2.wireOp",EDGE,"E2.18.7.2")])],"isStart":false});
            var Q895;
            Q895=makeQuery(id+"F3.opExtrude","CAP_EDGE",EDGE,{"disambiguationData":[OSD([sQuery(id+"F2.wireOp",EDGE,"E2.5.7.2")])],"isStart":false});
            var Q896;
            Q896=makeQuery(id+"F3.opExtrude","CAP_EDGE",EDGE,{"disambiguationData":[OSD([sQuery(id+"F2.wireOp",EDGE,"E2.2.7.2")])],"isStart":false});
            var Q897;
            Q897=makeQuery(id+"F3.opExtrude","CAP_EDGE",EDGE,{"disambiguationData":[OSD([sQuery(id+"F2.wireOp",EDGE,"E3.6.21.7")])],"isStart":false});
            var Q898;
            Q898=makeQuery(id+"F3.opExtrude","CAP_EDGE",EDGE,{"disambiguationData":[OSD([sQuery(id+"F2.wireOp",EDGE,"E3.6.28.7")])],"isStart":false});
            var Q899;
            Q899=makeQuery(id+"F3.opExtrude","CAP_EDGE",EDGE,{"disambiguationData":[OSD([sQuery(id+"F2.wireOp",EDGE,"E2.15.7.2")])],"isStart":false});
            var Q900;
            Q900=makeQuery(id+"F3.opExtrude","CAP_EDGE",EDGE,{"disambiguationData":[OSD([sQuery(id+"F2.wireOp",EDGE,"E2.9.7.2")])],"isStart":false});
            var Q901;
            Q901=makeQuery(id+"F3.opExtrude","CAP_EDGE",EDGE,{"disambiguationData":[OSD([sQuery(id+"F2.wireOp",EDGE,"E2.0.7.3")])],"isStart":false});
            var Q902;
            Q902=makeQuery(id+"F3.opExtrude","CAP_EDGE",EDGE,{"disambiguationData":[OSD([sQuery(id+"F2.wireOp",EDGE,"E2.16.7.1")])],"isStart":false});
            var Q903;
            Q903=makeQuery(id+"F3.opExtrude","CAP_EDGE",EDGE,{"disambiguationData":[OSD([sQuery(id+"F2.wireOp",EDGE,"E2.3.7.1")])],"isStart":false});
            var Q904;
            Q904=makeQuery(id+"F3.opExtrude","CAP_EDGE",EDGE,{"disambiguationData":[OSD([sQuery(id+"F2.wireOp",EDGE,"E2.10.7.1")])],"isStart":false});
            var Q905;
            Q905=makeQuery(id+"F3.opExtrude","CAP_EDGE",EDGE,{"disambiguationData":[OSD([sQuery(id+"F2.wireOp",EDGE,"E3.3.29.7")])],"isStart":false});
            var Q906;
            Q906=makeQuery(id+"F3.opExtrude","CAP_EDGE",EDGE,{"disambiguationData":[OSD([sQuery(id+"F2.wireOp",EDGE,"E2.4.7.1")])],"isStart":false});
            var Q907;
            Q907=makeQuery(id+"F3.opExtrude","CAP_EDGE",EDGE,{"disambiguationData":[OSD([sQuery(id+"F2.wireOp",EDGE,"E2.17.7.1")])],"isStart":false});
            var Q908;
            Q908=makeQuery(id+"F3.opExtrude","CAP_EDGE",EDGE,{"disambiguationData":[OSD([sQuery(id+"F2.wireOp",EDGE,"E3.3.24.7")])],"isStart":false});
            var Q909;
            Q909=makeQuery(id+"F3.opExtrude","CAP_EDGE",EDGE,{"disambiguationData":[OSD([sQuery(id+"F2.wireOp",EDGE,"E2.11.7.1")])],"isStart":false});
            var Q910;
            Q910=makeQuery(id+"F3.opExtrude","CAP_EDGE",EDGE,{"disambiguationData":[OSD([sQuery(id+"F2.wireOp",EDGE,"E2.18.7.1")])],"isStart":false});
            var Q911;
            Q911=makeQuery(id+"F3.opExtrude","CAP_EDGE",EDGE,{"disambiguationData":[OSD([sQuery(id+"F2.wireOp",EDGE,"E2.5.7.1")])],"isStart":false});
            var Q912;
            Q912=makeQuery(id+"F3.opExtrude","CAP_EDGE",EDGE,{"disambiguationData":[OSD([sQuery(id+"F2.wireOp",EDGE,"E2.12.7.1")])],"isStart":false});
            var Q913;
            Q913=makeQuery(id+"F3.opExtrude","CAP_EDGE",EDGE,{"disambiguationData":[OSD([sQuery(id+"F2.wireOp",EDGE,"E3.3.22.7")])],"isStart":false});
            var Q914;
            Q914=makeQuery(id+"F3.opExtrude","CAP_EDGE",EDGE,{"disambiguationData":[OSD([sQuery(id+"F2.wireOp",EDGE,"E3.3.23.7")])],"isStart":false});
            var Q915;
            Q915=makeQuery(id+"F3.opExtrude","CAP_EDGE",EDGE,{"disambiguationData":[OSD([sQuery(id+"F2.wireOp",EDGE,"E3.3.28.7")])],"isStart":false});
            var Q916;
            Q916=makeQuery(id+"F3.opExtrude","CAP_EDGE",EDGE,{"disambiguationData":[OSD([sQuery(id+"F2.wireOp",EDGE,"E2.15.7.1")])],"isStart":false});
            var Q917;
            Q917=makeQuery(id+"F3.opExtrude","CAP_EDGE",EDGE,{"disambiguationData":[OSD([sQuery(id+"F2.wireOp",EDGE,"E2.9.7.1")])],"isStart":false});
            var Q918;
            Q918=makeQuery(id+"F3.opExtrude","CAP_EDGE",EDGE,{"disambiguationData":[OSD([sQuery(id+"F2.wireOp",EDGE,"E2.6.7.1")])],"isStart":false});
            var Q919;
            Q919=makeQuery(id+"F3.opExtrude","CAP_EDGE",EDGE,{"disambiguationData":[OSD([sQuery(id+"F2.wireOp",EDGE,"E3.3.25.7")])],"isStart":false});
            var Q920;
            Q920=makeQuery(id+"F3.opExtrude","CAP_EDGE",EDGE,{"disambiguationData":[OSD([sQuery(id+"F2.wireOp",EDGE,"E2.19.7.1")])],"isStart":false});
            var Q921;
            Q921=makeQuery(id+"F3.opExtrude","CAP_EDGE",EDGE,{"disambiguationData":[OSD([sQuery(id+"F2.wireOp",EDGE,"E3.3.26.7")])],"isStart":false});
            var Q922;
            Q922=makeQuery(id+"F3.opExtrude","CAP_EDGE",EDGE,{"disambiguationData":[OSD([sQuery(id+"F2.wireOp",EDGE,"E2.13.7.1")])],"isStart":false});
            var Q923;
            Q923=makeQuery(id+"F3.opExtrude","CAP_EDGE",EDGE,{"disambiguationData":[OSD([sQuery(id+"F2.wireOp",EDGE,"E3.3.20.7")])],"isStart":false});
            var Q924;
            Q924=makeQuery(id+"F3.opExtrude","CAP_EDGE",EDGE,{"disambiguationData":[OSD([sQuery(id+"F2.wireOp",EDGE,"E2.7.7.1")])],"isStart":false});
            var Q925;
            Q925=makeQuery(id+"F3.opExtrude","CAP_EDGE",EDGE,{"disambiguationData":[OSD([sQuery(id+"F2.wireOp",EDGE,"E2.14.7.1")])],"isStart":false});
            var Q926;
            Q926=makeQuery(id+"F3.opExtrude","CAP_EDGE",EDGE,{"disambiguationData":[OSD([sQuery(id+"F2.wireOp",EDGE,"E2.1.7.1")])],"isStart":false});
            var Q927;
            Q927=makeQuery(id+"F3.opExtrude","CAP_EDGE",EDGE,{"disambiguationData":[OSD([sQuery(id+"F2.wireOp",EDGE,"E2.8.7.1")])],"isStart":false});
            var Q928;
            Q928=makeQuery(id+"F3.opExtrude","CAP_EDGE",EDGE,{"disambiguationData":[OSD([sQuery(id+"F2.wireOp",EDGE,"E3.3.27.7")])],"isStart":false});
            var Q929;
            Q929=makeQuery(id+"F3.opExtrude","CAP_EDGE",EDGE,{"disambiguationData":[OSD([sQuery(id+"F2.wireOp",EDGE,"E2.2.7.1")])],"isStart":false});
            var Q930;
            Q930=makeQuery(id+"F3.opExtrude","CAP_EDGE",EDGE,{"disambiguationData":[OSD([sQuery(id+"F2.wireOp",EDGE,"E3.3.21.7")])],"isStart":false});
            var Q931;
            Q931=makeQuery(id+"F3.opExtrude","CAP_EDGE",EDGE,{"disambiguationData":[OSD([sQuery(id+"F2.wireOp",EDGE,"E3.9.22.7")])],"isStart":false});
            var Q932;
            Q932=makeQuery(id+"F3.opExtrude","CAP_EDGE",EDGE,{"disambiguationData":[OSD([sQuery(id+"F2.wireOp",EDGE,"E3.9.23.7")])],"isStart":false});
            var Q933;
            Q933=makeQuery(id+"F3.opExtrude","CAP_EDGE",EDGE,{"disambiguationData":[OSD([sQuery(id+"F2.wireOp",EDGE,"E2.16.7.3")])],"isStart":false});
            var Q934;
            Q934=makeQuery(id+"F3.opExtrude","CAP_EDGE",EDGE,{"disambiguationData":[OSD([sQuery(id+"F2.wireOp",EDGE,"E2.3.7.3")])],"isStart":false});
            var Q935;
            Q935=makeQuery(id+"F3.opExtrude","CAP_EDGE",EDGE,{"disambiguationData":[OSD([sQuery(id+"F2.wireOp",EDGE,"E2.10.7.3")])],"isStart":false});
            var Q936;
            Q936=makeQuery(id+"F3.opExtrude","CAP_EDGE",EDGE,{"disambiguationData":[OSD([sQuery(id+"F2.wireOp",EDGE,"E3.9.29.7")])],"isStart":false});
            var Q937;
            Q937=makeQuery(id+"F3.opExtrude","CAP_EDGE",EDGE,{"disambiguationData":[OSD([sQuery(id+"F2.wireOp",EDGE,"E3.9.26.7")])],"isStart":false});
            var Q938;
            Q938=makeQuery(id+"F3.opExtrude","CAP_EDGE",EDGE,{"disambiguationData":[OSD([sQuery(id+"F2.wireOp",EDGE,"E2.13.7.3")])],"isStart":false});
            var Q939;
            Q939=makeQuery(id+"F3.opExtrude","CAP_EDGE",EDGE,{"disambiguationData":[OSD([sQuery(id+"F2.wireOp",EDGE,"E3.9.20.7")])],"isStart":false});
            var Q940;
            Q940=makeQuery(id+"F3.opExtrude","CAP_EDGE",EDGE,{"disambiguationData":[OSD([sQuery(id+"F2.wireOp",EDGE,"E2.7.7.3")])],"isStart":false});
            var Q941;
            Q941=makeQuery(id+"F3.opExtrude","CAP_EDGE",EDGE,{"disambiguationData":[OSD([sQuery(id+"F2.wireOp",EDGE,"E2.14.7.3")])],"isStart":false});
            var Q942;
            Q942=makeQuery(id+"F3.opExtrude","CAP_EDGE",EDGE,{"disambiguationData":[OSD([sQuery(id+"F2.wireOp",EDGE,"E2.1.7.3")])],"isStart":false});
            var Q943;
            Q943=makeQuery(id+"F3.opExtrude","CAP_EDGE",EDGE,{"disambiguationData":[OSD([sQuery(id+"F2.wireOp",EDGE,"E2.8.7.3")])],"isStart":false});
            var Q944;
            Q944=makeQuery(id+"F3.opExtrude","CAP_EDGE",EDGE,{"disambiguationData":[OSD([sQuery(id+"F2.wireOp",EDGE,"E3.9.27.7")])],"isStart":false});
            var Q945;
            Q945=makeQuery(id+"F3.opExtrude","CAP_EDGE",EDGE,{"disambiguationData":[OSD([sQuery(id+"F2.wireOp",EDGE,"E2.2.7.3")])],"isStart":false});
            var Q946;
            Q946=makeQuery(id+"F3.opExtrude","CAP_EDGE",EDGE,{"disambiguationData":[OSD([sQuery(id+"F2.wireOp",EDGE,"E3.9.21.7")])],"isStart":false});
            var Q947;
            Q947=makeQuery(id+"F3.opExtrude","CAP_EDGE",EDGE,{"disambiguationData":[OSD([sQuery(id+"F2.wireOp",EDGE,"E3.9.28.7")])],"isStart":false});
            var Q948;
            Q948=makeQuery(id+"F3.opExtrude","CAP_EDGE",EDGE,{"disambiguationData":[OSD([sQuery(id+"F2.wireOp",EDGE,"E2.15.7.3")])],"isStart":false});
            var Q949;
            Q949=makeQuery(id+"F3.opExtrude","CAP_EDGE",EDGE,{"disambiguationData":[OSD([sQuery(id+"F2.wireOp",EDGE,"E2.9.7.3")])],"isStart":false});
            var Q950;
            Q950=makeQuery(id+"F3.opExtrude","CAP_EDGE",EDGE,{"disambiguationData":[OSD([sQuery(id+"F2.wireOp",EDGE,"E2.4.7.3")])],"isStart":false});
            var Q951;
            Q951=makeQuery(id+"F3.opExtrude","CAP_EDGE",EDGE,{"disambiguationData":[OSD([sQuery(id+"F2.wireOp",EDGE,"E2.17.7.3")])],"isStart":false});
            var Q952;
            Q952=makeQuery(id+"F3.opExtrude","CAP_EDGE",EDGE,{"disambiguationData":[OSD([sQuery(id+"F2.wireOp",EDGE,"E3.9.24.7")])],"isStart":false});
            var Q953;
            Q953=makeQuery(id+"F3.opExtrude","CAP_EDGE",EDGE,{"disambiguationData":[OSD([sQuery(id+"F2.wireOp",EDGE,"E2.11.7.3")])],"isStart":false});
            var Q954;
            Q954=makeQuery(id+"F3.opExtrude","CAP_EDGE",EDGE,{"disambiguationData":[OSD([sQuery(id+"F2.wireOp",EDGE,"E2.18.7.3")])],"isStart":false});
            var Q955;
            Q955=makeQuery(id+"F3.opExtrude","CAP_EDGE",EDGE,{"disambiguationData":[OSD([sQuery(id+"F2.wireOp",EDGE,"E2.5.7.3")])],"isStart":false});
            var Q956;
            Q956=makeQuery(id+"F3.opExtrude","CAP_EDGE",EDGE,{"disambiguationData":[OSD([sQuery(id+"F2.wireOp",EDGE,"E2.12.7.3")])],"isStart":false});
            var Q957;
            Q957=makeQuery(id+"F3.opExtrude","CAP_EDGE",EDGE,{"disambiguationData":[OSD([sQuery(id+"F2.wireOp",EDGE,"E2.6.7.3")])],"isStart":false});
            var Q958;
            Q958=makeQuery(id+"F3.opExtrude","CAP_EDGE",EDGE,{"disambiguationData":[OSD([sQuery(id+"F2.wireOp",EDGE,"E3.9.25.7")])],"isStart":false});
            var Q959;
            Q959=makeQuery(id+"F3.opExtrude","CAP_EDGE",EDGE,{"disambiguationData":[OSD([sQuery(id+"F2.wireOp",EDGE,"E2.19.7.3")])],"isStart":false});
            var Q960;
            Q960=makeQuery(id+"F3.opExtrude","CAP_EDGE",EDGE,{"disambiguationData":[OSD([sQuery(id+"F2.wireOp",EDGE,"E2.0.8.3")])],"isStart":false});
            var Q961;
            Q961=makeQuery(id+"F3.opExtrude","CAP_EDGE",EDGE,{"disambiguationData":[OSD([sQuery(id+"F2.wireOp",EDGE,"E2.0.8.0")])],"isStart":false});
            var Q962;
            Q962=makeQuery(id+"F3.opExtrude","CAP_EDGE",EDGE,{"disambiguationData":[OSD([sQuery(id+"F2.wireOp",EDGE,"E2.0.8.2")])],"isStart":false});
            var Q963;
            Q963=makeQuery(id+"F3.opExtrude","CAP_EDGE",EDGE,{"disambiguationData":[OSD([sQuery(id+"F2.wireOp",EDGE,"E2.10.8.3")])],"isStart":false});
            var Q964;
            Q964=makeQuery(id+"F3.opExtrude","CAP_EDGE",EDGE,{"disambiguationData":[OSD([sQuery(id+"F2.wireOp",EDGE,"E3.9.22.8")])],"isStart":false});
            var Q965;
            Q965=makeQuery(id+"F3.opExtrude","CAP_EDGE",EDGE,{"disambiguationData":[OSD([sQuery(id+"F2.wireOp",EDGE,"E2.9.8.3")])],"isStart":false});
            var Q966;
            Q966=makeQuery(id+"F3.opExtrude","CAP_EDGE",EDGE,{"disambiguationData":[OSD([sQuery(id+"F2.wireOp",EDGE,"E2.6.8.3")])],"isStart":false});
            var Q967;
            Q967=makeQuery(id+"F3.opExtrude","CAP_EDGE",EDGE,{"disambiguationData":[OSD([sQuery(id+"F2.wireOp",EDGE,"E3.9.25.8")])],"isStart":false});
            var Q968;
            Q968=makeQuery(id+"F3.opExtrude","CAP_EDGE",EDGE,{"disambiguationData":[OSD([sQuery(id+"F2.wireOp",EDGE,"E2.19.8.3")])],"isStart":false});
            var Q969;
            Q969=makeQuery(id+"F3.opExtrude","CAP_EDGE",EDGE,{"disambiguationData":[OSD([sQuery(id+"F2.wireOp",EDGE,"E2.13.8.3")])],"isStart":false});
            var Q970;
            Q970=makeQuery(id+"F3.opExtrude","CAP_EDGE",EDGE,{"disambiguationData":[OSD([sQuery(id+"F2.wireOp",EDGE,"E2.7.8.3")])],"isStart":false});
            var Q971;
            Q971=makeQuery(id+"F3.opExtrude","CAP_EDGE",EDGE,{"disambiguationData":[OSD([sQuery(id+"F2.wireOp",EDGE,"E3.9.26.8")])],"isStart":false});
            var Q972;
            Q972=makeQuery(id+"F3.opExtrude","CAP_EDGE",EDGE,{"disambiguationData":[OSD([sQuery(id+"F2.wireOp",EDGE,"E2.14.8.3")])],"isStart":false});
            var Q973;
            Q973=makeQuery(id+"F3.opExtrude","CAP_EDGE",EDGE,{"disambiguationData":[OSD([sQuery(id+"F2.wireOp",EDGE,"E3.9.20.8")])],"isStart":false});
            var Q974;
            Q974=makeQuery(id+"F3.opExtrude","CAP_EDGE",EDGE,{"disambiguationData":[OSD([sQuery(id+"F2.wireOp",EDGE,"E2.1.8.3")])],"isStart":false});
            var Q975;
            Q975=makeQuery(id+"F3.opExtrude","CAP_EDGE",EDGE,{"disambiguationData":[OSD([sQuery(id+"F2.wireOp",EDGE,"E2.8.8.3")])],"isStart":false});
            var Q976;
            Q976=makeQuery(id+"F3.opExtrude","CAP_EDGE",EDGE,{"disambiguationData":[OSD([sQuery(id+"F2.wireOp",EDGE,"E3.9.27.8")])],"isStart":false});
            var Q977;
            Q977=makeQuery(id+"F3.opExtrude","CAP_EDGE",EDGE,{"disambiguationData":[OSD([sQuery(id+"F2.wireOp",EDGE,"E2.2.8.3")])],"isStart":false});
            var Q978;
            Q978=makeQuery(id+"F3.opExtrude","CAP_EDGE",EDGE,{"disambiguationData":[OSD([sQuery(id+"F2.wireOp",EDGE,"E3.9.21.8")])],"isStart":false});
            var Q979;
            Q979=makeQuery(id+"F3.opExtrude","CAP_EDGE",EDGE,{"disambiguationData":[OSD([sQuery(id+"F2.wireOp",EDGE,"E2.16.8.3")])],"isStart":false});
            var Q980;
            Q980=makeQuery(id+"F3.opExtrude","CAP_EDGE",EDGE,{"disambiguationData":[OSD([sQuery(id+"F2.wireOp",EDGE,"E2.3.8.3")])],"isStart":false});
            var Q981;
            Q981=makeQuery(id+"F3.opExtrude","CAP_EDGE",EDGE,{"disambiguationData":[OSD([sQuery(id+"F2.wireOp",EDGE,"E3.9.29.8")])],"isStart":false});
            var Q982;
            Q982=makeQuery(id+"F3.opExtrude","CAP_EDGE",EDGE,{"disambiguationData":[OSD([sQuery(id+"F2.wireOp",EDGE,"E2.4.8.3")])],"isStart":false});
            var Q983;
            Q983=makeQuery(id+"F3.opExtrude","CAP_EDGE",EDGE,{"disambiguationData":[OSD([sQuery(id+"F2.wireOp",EDGE,"E3.9.23.8")])],"isStart":false});
            var Q984;
            Q984=makeQuery(id+"F3.opExtrude","CAP_EDGE",EDGE,{"disambiguationData":[OSD([sQuery(id+"F2.wireOp",EDGE,"E2.17.8.3")])],"isStart":false});
            var Q985;
            Q985=makeQuery(id+"F3.opExtrude","CAP_EDGE",EDGE,{"disambiguationData":[OSD([sQuery(id+"F2.wireOp",EDGE,"E3.9.24.8")])],"isStart":false});
            var Q986;
            Q986=makeQuery(id+"F3.opExtrude","CAP_EDGE",EDGE,{"disambiguationData":[OSD([sQuery(id+"F2.wireOp",EDGE,"E2.11.8.3")])],"isStart":false});
            var Q987;
            Q987=makeQuery(id+"F3.opExtrude","CAP_EDGE",EDGE,{"disambiguationData":[OSD([sQuery(id+"F2.wireOp",EDGE,"E2.18.8.3")])],"isStart":false});
            var Q988;
            Q988=makeQuery(id+"F3.opExtrude","CAP_EDGE",EDGE,{"disambiguationData":[OSD([sQuery(id+"F2.wireOp",EDGE,"E2.5.8.3")])],"isStart":false});
            var Q989;
            Q989=makeQuery(id+"F3.opExtrude","CAP_EDGE",EDGE,{"disambiguationData":[OSD([sQuery(id+"F2.wireOp",EDGE,"E2.12.8.3")])],"isStart":false});
            var Q990;
            Q990=makeQuery(id+"F3.opExtrude","CAP_EDGE",EDGE,{"disambiguationData":[OSD([sQuery(id+"F2.wireOp",EDGE,"E2.10.8.0")])],"isStart":false});
            var Q991;
            Q991=makeQuery(id+"F3.opExtrude","CAP_EDGE",EDGE,{"disambiguationData":[OSD([sQuery(id+"F2.wireOp",EDGE,"E2.9.8.0")])],"isStart":false});
            var Q992;
            Q992=makeQuery(id+"F3.opExtrude","CAP_EDGE",EDGE,{"disambiguationData":[OSD([sQuery(id+"F2.wireOp",EDGE,"E2.3.8.0")])],"isStart":false});
            var Q993;
            Q993=makeQuery(id+"F3.opExtrude","CAP_EDGE",EDGE,{"disambiguationData":[OSD([sQuery(id+"F2.wireOp",EDGE,"E3.0.22.8")])],"isStart":false});
            var Q994;
            Q994=makeQuery(id+"F3.opExtrude","CAP_EDGE",EDGE,{"disambiguationData":[OSD([sQuery(id+"F2.wireOp",EDGE,"E3.0.29.8")])],"isStart":false});
            var Q995;
            Q995=makeQuery(id+"F3.opExtrude","CAP_EDGE",EDGE,{"disambiguationData":[OSD([sQuery(id+"F2.wireOp",EDGE,"E2.16.8.0")])],"isStart":false});
            var Q996;
            Q996=makeQuery(id+"F3.opExtrude","CAP_EDGE",EDGE,{"disambiguationData":[OSD([sQuery(id+"F2.wireOp",EDGE,"E3.9.28.8")])],"isStart":false});
            var Q997;
            Q997=makeQuery(id+"F3.opExtrude","CAP_EDGE",EDGE,{"disambiguationData":[OSD([sQuery(id+"F2.wireOp",EDGE,"E2.15.8.3")])],"isStart":false});
            var Q998;
            Q998=makeQuery(id+"F3.opExtrude","CAP_EDGE",EDGE,{"disambiguationData":[OSD([sQuery(id+"F2.wireOp",EDGE,"E3.0.26.8")])],"isStart":false});
            var Q999;
            Q999=makeQuery(id+"F3.opExtrude","CAP_EDGE",EDGE,{"disambiguationData":[OSD([sQuery(id+"F2.wireOp",EDGE,"E2.13.8.0")])],"isStart":false});
            var Q1000;
            Q1000=makeQuery(id+"F3.opExtrude","CAP_EDGE",EDGE,{"disambiguationData":[OSD([sQuery(id+"F2.wireOp",EDGE,"E3.0.20.8")])],"isStart":false});
            var Q1001;
            Q1001=makeQuery(id+"F3.opExtrude","CAP_EDGE",EDGE,{"disambiguationData":[OSD([sQuery(id+"F2.wireOp",EDGE,"E2.7.8.0")])],"isStart":false});
            var Q1002;
            Q1002=makeQuery(id+"F3.opExtrude","CAP_EDGE",EDGE,{"disambiguationData":[OSD([sQuery(id+"F2.wireOp",EDGE,"E2.14.8.0")])],"isStart":false});
            var Q1003;
            Q1003=makeQuery(id+"F3.opExtrude","CAP_EDGE",EDGE,{"disambiguationData":[OSD([sQuery(id+"F2.wireOp",EDGE,"E2.1.8.0")])],"isStart":false});
            var Q1004;
            Q1004=makeQuery(id+"F3.opExtrude","CAP_EDGE",EDGE,{"disambiguationData":[OSD([sQuery(id+"F2.wireOp",EDGE,"E2.8.8.0")])],"isStart":false});
            var Q1005;
            Q1005=makeQuery(id+"F3.opExtrude","CAP_EDGE",EDGE,{"disambiguationData":[OSD([sQuery(id+"F2.wireOp",EDGE,"E3.0.27.8")])],"isStart":false});
            var Q1006;
            Q1006=makeQuery(id+"F3.opExtrude","CAP_EDGE",EDGE,{"disambiguationData":[OSD([sQuery(id+"F2.wireOp",EDGE,"E2.2.8.0")])],"isStart":false});
            var Q1007;
            Q1007=makeQuery(id+"F3.opExtrude","CAP_EDGE",EDGE,{"disambiguationData":[OSD([sQuery(id+"F2.wireOp",EDGE,"E3.0.21.8")])],"isStart":false});
            var Q1008;
            Q1008=makeQuery(id+"F3.opExtrude","CAP_EDGE",EDGE,{"disambiguationData":[OSD([sQuery(id+"F2.wireOp",EDGE,"E3.0.28.8")])],"isStart":false});
            var Q1009;
            Q1009=makeQuery(id+"F3.opExtrude","CAP_EDGE",EDGE,{"disambiguationData":[OSD([sQuery(id+"F2.wireOp",EDGE,"E2.15.8.0")])],"isStart":false});
            var Q1010;
            Q1010=makeQuery(id+"F3.opExtrude","CAP_EDGE",EDGE,{"disambiguationData":[OSD([sQuery(id+"F2.wireOp",EDGE,"E2.4.8.0")])],"isStart":false});
            var Q1011;
            Q1011=makeQuery(id+"F3.opExtrude","CAP_EDGE",EDGE,{"disambiguationData":[OSD([sQuery(id+"F2.wireOp",EDGE,"E3.0.23.8")])],"isStart":false});
            var Q1012;
            Q1012=makeQuery(id+"F3.opExtrude","CAP_EDGE",EDGE,{"disambiguationData":[OSD([sQuery(id+"F2.wireOp",EDGE,"E2.17.8.0")])],"isStart":false});
            var Q1013;
            Q1013=makeQuery(id+"F3.opExtrude","CAP_EDGE",EDGE,{"disambiguationData":[OSD([sQuery(id+"F2.wireOp",EDGE,"E3.0.24.8")])],"isStart":false});
            var Q1014;
            Q1014=makeQuery(id+"F3.opExtrude","CAP_EDGE",EDGE,{"disambiguationData":[OSD([sQuery(id+"F2.wireOp",EDGE,"E2.5.8.0")])],"isStart":false});
            var Q1015;
            Q1015=makeQuery(id+"F3.opExtrude","CAP_EDGE",EDGE,{"disambiguationData":[OSD([sQuery(id+"F2.wireOp",EDGE,"E2.11.8.0")])],"isStart":false});
            var Q1016;
            Q1016=makeQuery(id+"F3.opExtrude","CAP_EDGE",EDGE,{"disambiguationData":[OSD([sQuery(id+"F2.wireOp",EDGE,"E2.18.8.0")])],"isStart":false});
            var Q1017;
            Q1017=makeQuery(id+"F3.opExtrude","CAP_EDGE",EDGE,{"disambiguationData":[OSD([sQuery(id+"F2.wireOp",EDGE,"E3.0.25.8")])],"isStart":false});
            var Q1018;
            Q1018=makeQuery(id+"F3.opExtrude","CAP_EDGE",EDGE,{"disambiguationData":[OSD([sQuery(id+"F2.wireOp",EDGE,"E2.12.8.0")])],"isStart":false});
            var Q1019;
            Q1019=makeQuery(id+"F3.opExtrude","CAP_EDGE",EDGE,{"disambiguationData":[OSD([sQuery(id+"F2.wireOp",EDGE,"E2.19.8.0")])],"isStart":false});
            var Q1020;
            Q1020=makeQuery(id+"F3.opExtrude","CAP_EDGE",EDGE,{"disambiguationData":[OSD([sQuery(id+"F2.wireOp",EDGE,"E2.6.8.0")])],"isStart":false});
            var Q1021;
            Q1021=makeQuery(id+"F3.opExtrude","CAP_EDGE",EDGE,{"disambiguationData":[OSD([sQuery(id+"F2.wireOp",EDGE,"E2.0.8.1")])],"isStart":false});
            var Q1022;
            Q1022=makeQuery(id+"F3.opExtrude","CAP_EDGE",EDGE,{"disambiguationData":[OSD([sQuery(id+"F2.wireOp",EDGE,"E3.6.29.8")])],"isStart":false});
            var Q1023;
            Q1023=makeQuery(id+"F3.opExtrude","CAP_EDGE",EDGE,{"disambiguationData":[OSD([sQuery(id+"F2.wireOp",EDGE,"E2.4.8.2")])],"isStart":false});
            var Q1024;
            Q1024=makeQuery(id+"F3.opExtrude","CAP_EDGE",EDGE,{"disambiguationData":[OSD([sQuery(id+"F2.wireOp",EDGE,"E3.6.23.8")])],"isStart":false});
            var Q1025;
            Q1025=makeQuery(id+"F3.opExtrude","CAP_EDGE",EDGE,{"disambiguationData":[OSD([sQuery(id+"F2.wireOp",EDGE,"E2.17.8.2")])],"isStart":false});
            var Q1026;
            Q1026=makeQuery(id+"F3.opExtrude","CAP_EDGE",EDGE,{"disambiguationData":[OSD([sQuery(id+"F2.wireOp",EDGE,"E3.6.24.8")])],"isStart":false});
            var Q1027;
            Q1027=makeQuery(id+"F3.opExtrude","CAP_EDGE",EDGE,{"disambiguationData":[OSD([sQuery(id+"F2.wireOp",EDGE,"E2.11.8.2")])],"isStart":false});
            var Q1028;
            Q1028=makeQuery(id+"F3.opExtrude","CAP_EDGE",EDGE,{"disambiguationData":[OSD([sQuery(id+"F2.wireOp",EDGE,"E2.18.8.2")])],"isStart":false});
            var Q1029;
            Q1029=makeQuery(id+"F3.opExtrude","CAP_EDGE",EDGE,{"disambiguationData":[OSD([sQuery(id+"F2.wireOp",EDGE,"E2.5.8.2")])],"isStart":false});
            var Q1030;
            Q1030=makeQuery(id+"F3.opExtrude","CAP_EDGE",EDGE,{"disambiguationData":[OSD([sQuery(id+"F2.wireOp",EDGE,"E2.12.8.2")])],"isStart":false});
            var Q1031;
            Q1031=makeQuery(id+"F3.opExtrude","CAP_EDGE",EDGE,{"disambiguationData":[OSD([sQuery(id+"F2.wireOp",EDGE,"E2.6.8.2")])],"isStart":false});
            var Q1032;
            Q1032=makeQuery(id+"F3.opExtrude","CAP_EDGE",EDGE,{"disambiguationData":[OSD([sQuery(id+"F2.wireOp",EDGE,"E3.6.25.8")])],"isStart":false});
            var Q1033;
            Q1033=makeQuery(id+"F3.opExtrude","CAP_EDGE",EDGE,{"disambiguationData":[OSD([sQuery(id+"F2.wireOp",EDGE,"E2.10.8.2")])],"isStart":false});
            var Q1034;
            Q1034=makeQuery(id+"F3.opExtrude","CAP_EDGE",EDGE,{"disambiguationData":[OSD([sQuery(id+"F2.wireOp",EDGE,"E3.6.22.8")])],"isStart":false});
            var Q1035;
            Q1035=makeQuery(id+"F3.opExtrude","CAP_EDGE",EDGE,{"disambiguationData":[OSD([sQuery(id+"F2.wireOp",EDGE,"E2.9.8.2")])],"isStart":false});
            var Q1036;
            Q1036=makeQuery(id+"F3.opExtrude","CAP_EDGE",EDGE,{"disambiguationData":[OSD([sQuery(id+"F2.wireOp",EDGE,"E2.16.8.2")])],"isStart":false});
            var Q1037;
            Q1037=makeQuery(id+"F3.opExtrude","CAP_EDGE",EDGE,{"disambiguationData":[OSD([sQuery(id+"F2.wireOp",EDGE,"E2.3.8.2")])],"isStart":false});
            var Q1038;
            Q1038=makeQuery(id+"F3.opExtrude","CAP_EDGE",EDGE,{"disambiguationData":[OSD([sQuery(id+"F2.wireOp",EDGE,"E2.19.8.2")])],"isStart":false});
            var Q1039;
            Q1039=makeQuery(id+"F3.opExtrude","CAP_EDGE",EDGE,{"disambiguationData":[OSD([sQuery(id+"F2.wireOp",EDGE,"E3.6.26.8")])],"isStart":false});
            var Q1040;
            Q1040=makeQuery(id+"F3.opExtrude","CAP_EDGE",EDGE,{"disambiguationData":[OSD([sQuery(id+"F2.wireOp",EDGE,"E2.13.8.2")])],"isStart":false});
            var Q1041;
            Q1041=makeQuery(id+"F3.opExtrude","CAP_EDGE",EDGE,{"disambiguationData":[OSD([sQuery(id+"F2.wireOp",EDGE,"E3.6.20.8")])],"isStart":false});
            var Q1042;
            Q1042=makeQuery(id+"F3.opExtrude","CAP_EDGE",EDGE,{"disambiguationData":[OSD([sQuery(id+"F2.wireOp",EDGE,"E2.7.8.2")])],"isStart":false});
            var Q1043;
            Q1043=makeQuery(id+"F3.opExtrude","CAP_EDGE",EDGE,{"disambiguationData":[OSD([sQuery(id+"F2.wireOp",EDGE,"E2.14.8.2")])],"isStart":false});
            var Q1044;
            Q1044=makeQuery(id+"F3.opExtrude","CAP_EDGE",EDGE,{"disambiguationData":[OSD([sQuery(id+"F2.wireOp",EDGE,"E2.1.8.2")])],"isStart":false});
            var Q1045;
            Q1045=makeQuery(id+"F3.opExtrude","CAP_EDGE",EDGE,{"disambiguationData":[OSD([sQuery(id+"F2.wireOp",EDGE,"E2.8.8.2")])],"isStart":false});
            var Q1046;
            Q1046=makeQuery(id+"F3.opExtrude","CAP_EDGE",EDGE,{"disambiguationData":[OSD([sQuery(id+"F2.wireOp",EDGE,"E3.6.27.8")])],"isStart":false});
            var Q1047;
            Q1047=makeQuery(id+"F3.opExtrude","CAP_EDGE",EDGE,{"disambiguationData":[OSD([sQuery(id+"F2.wireOp",EDGE,"E2.2.8.2")])],"isStart":false});
            var Q1048;
            Q1048=makeQuery(id+"F3.opExtrude","CAP_EDGE",EDGE,{"disambiguationData":[OSD([sQuery(id+"F2.wireOp",EDGE,"E3.6.21.8")])],"isStart":false});
            var Q1049;
            Q1049=makeQuery(id+"F3.opExtrude","CAP_EDGE",EDGE,{"disambiguationData":[OSD([sQuery(id+"F2.wireOp",EDGE,"E3.6.28.8")])],"isStart":false});
            var Q1050;
            Q1050=makeQuery(id+"F3.opExtrude","CAP_EDGE",EDGE,{"disambiguationData":[OSD([sQuery(id+"F2.wireOp",EDGE,"E2.15.8.2")])],"isStart":false});
            var Q1051;
            Q1051=makeQuery(id+"F3.opExtrude","CAP_EDGE",EDGE,{"disambiguationData":[OSD([sQuery(id+"F2.wireOp",EDGE,"E2.10.8.1")])],"isStart":false});
            var Q1052;
            Q1052=makeQuery(id+"F3.opExtrude","CAP_EDGE",EDGE,{"disambiguationData":[OSD([sQuery(id+"F2.wireOp",EDGE,"E3.3.22.8")])],"isStart":false});
            var Q1053;
            Q1053=makeQuery(id+"F3.opExtrude","CAP_EDGE",EDGE,{"disambiguationData":[OSD([sQuery(id+"F2.wireOp",EDGE,"E2.3.8.1")])],"isStart":false});
            var Q1054;
            Q1054=makeQuery(id+"F3.opExtrude","CAP_EDGE",EDGE,{"disambiguationData":[OSD([sQuery(id+"F2.wireOp",EDGE,"E2.9.8.1")])],"isStart":false});
            var Q1055;
            Q1055=makeQuery(id+"F3.opExtrude","CAP_EDGE",EDGE,{"disambiguationData":[OSD([sQuery(id+"F2.wireOp",EDGE,"E3.3.29.8")])],"isStart":false});
            var Q1056;
            Q1056=makeQuery(id+"F3.opExtrude","CAP_EDGE",EDGE,{"disambiguationData":[OSD([sQuery(id+"F2.wireOp",EDGE,"E2.16.8.1")])],"isStart":false});
            var Q1057;
            Q1057=makeQuery(id+"F3.opExtrude","CAP_EDGE",EDGE,{"disambiguationData":[OSD([sQuery(id+"F2.wireOp",EDGE,"E2.4.8.1")])],"isStart":false});
            var Q1058;
            Q1058=makeQuery(id+"F3.opExtrude","CAP_EDGE",EDGE,{"disambiguationData":[OSD([sQuery(id+"F2.wireOp",EDGE,"E3.3.23.8")])],"isStart":false});
            var Q1059;
            Q1059=makeQuery(id+"F3.opExtrude","CAP_EDGE",EDGE,{"disambiguationData":[OSD([sQuery(id+"F2.wireOp",EDGE,"E2.17.8.1")])],"isStart":false});
            var Q1060;
            Q1060=makeQuery(id+"F3.opExtrude","CAP_EDGE",EDGE,{"disambiguationData":[OSD([sQuery(id+"F2.wireOp",EDGE,"E2.14.8.1")])],"isStart":false});
            var Q1061;
            Q1061=makeQuery(id+"F3.opExtrude","CAP_EDGE",EDGE,{"disambiguationData":[OSD([sQuery(id+"F2.wireOp",EDGE,"E2.1.8.1")])],"isStart":false});
            var Q1062;
            Q1062=makeQuery(id+"F3.opExtrude","CAP_EDGE",EDGE,{"disambiguationData":[OSD([sQuery(id+"F2.wireOp",EDGE,"E2.8.8.1")])],"isStart":false});
            var Q1063;
            Q1063=makeQuery(id+"F3.opExtrude","CAP_EDGE",EDGE,{"disambiguationData":[OSD([sQuery(id+"F2.wireOp",EDGE,"E3.3.27.8")])],"isStart":false});
            var Q1064;
            Q1064=makeQuery(id+"F3.opExtrude","CAP_EDGE",EDGE,{"disambiguationData":[OSD([sQuery(id+"F2.wireOp",EDGE,"E2.2.8.1")])],"isStart":false});
            var Q1065;
            Q1065=makeQuery(id+"F3.opExtrude","CAP_EDGE",EDGE,{"disambiguationData":[OSD([sQuery(id+"F2.wireOp",EDGE,"E3.3.21.8")])],"isStart":false});
            var Q1066;
            Q1066=makeQuery(id+"F3.opExtrude","CAP_EDGE",EDGE,{"disambiguationData":[OSD([sQuery(id+"F2.wireOp",EDGE,"E3.3.28.8")])],"isStart":false});
            var Q1067;
            Q1067=makeQuery(id+"F3.opExtrude","CAP_EDGE",EDGE,{"disambiguationData":[OSD([sQuery(id+"F2.wireOp",EDGE,"E2.15.8.1")])],"isStart":false});
            var Q1068;
            Q1068=makeQuery(id+"F3.opExtrude","CAP_EDGE",EDGE,{"disambiguationData":[OSD([sQuery(id+"F2.wireOp",EDGE,"E3.3.24.8")])],"isStart":false});
            var Q1069;
            Q1069=makeQuery(id+"F3.opExtrude","CAP_EDGE",EDGE,{"disambiguationData":[OSD([sQuery(id+"F2.wireOp",EDGE,"E2.11.8.1")])],"isStart":false});
            var Q1070;
            Q1070=makeQuery(id+"F3.opExtrude","CAP_EDGE",EDGE,{"disambiguationData":[OSD([sQuery(id+"F2.wireOp",EDGE,"E2.18.8.1")])],"isStart":false});
            var Q1071;
            Q1071=makeQuery(id+"F3.opExtrude","CAP_EDGE",EDGE,{"disambiguationData":[OSD([sQuery(id+"F2.wireOp",EDGE,"E2.5.8.1")])],"isStart":false});
            var Q1072;
            Q1072=makeQuery(id+"F3.opExtrude","CAP_EDGE",EDGE,{"disambiguationData":[OSD([sQuery(id+"F2.wireOp",EDGE,"E2.12.8.1")])],"isStart":false});
            var Q1073;
            Q1073=makeQuery(id+"F3.opExtrude","CAP_EDGE",EDGE,{"disambiguationData":[OSD([sQuery(id+"F2.wireOp",EDGE,"E2.19.8.1")])],"isStart":false});
            var Q1074;
            Q1074=makeQuery(id+"F3.opExtrude","CAP_EDGE",EDGE,{"disambiguationData":[OSD([sQuery(id+"F2.wireOp",EDGE,"E3.3.25.8")])],"isStart":false});
            var Q1075;
            Q1075=makeQuery(id+"F3.opExtrude","CAP_EDGE",EDGE,{"disambiguationData":[OSD([sQuery(id+"F2.wireOp",EDGE,"E2.6.8.1")])],"isStart":false});
            var Q1076;
            Q1076=makeQuery(id+"F3.opExtrude","CAP_EDGE",EDGE,{"disambiguationData":[OSD([sQuery(id+"F2.wireOp",EDGE,"E3.3.26.8")])],"isStart":false});
            var Q1077;
            Q1077=makeQuery(id+"F3.opExtrude","CAP_EDGE",EDGE,{"disambiguationData":[OSD([sQuery(id+"F2.wireOp",EDGE,"E2.13.8.1")])],"isStart":false});
            var Q1078;
            Q1078=makeQuery(id+"F3.opExtrude","CAP_EDGE",EDGE,{"disambiguationData":[OSD([sQuery(id+"F2.wireOp",EDGE,"E3.3.20.8")])],"isStart":false});
            var Q1079;
            Q1079=makeQuery(id+"F3.opExtrude","CAP_EDGE",EDGE,{"disambiguationData":[OSD([sQuery(id+"F2.wireOp",EDGE,"E2.7.8.1")])],"isStart":false});
            var Q1080;
            Q1080=makeQuery(id+"F3.opExtrude","CAP_EDGE",EDGE,{"disambiguationData":[OSD([sQuery(id+"F2.wireOp",EDGE,"E2.0.9.0")])],"isStart":false});
            var Q1081;
            Q1081=makeQuery(id+"F3.opExtrude","CAP_EDGE",EDGE,{"disambiguationData":[OSD([sQuery(id+"F2.wireOp",EDGE,"E2.0.9.2")])],"isStart":false});
            var Q1082;
            Q1082=makeQuery(id+"F3.opExtrude","CAP_EDGE",EDGE,{"disambiguationData":[OSD([sQuery(id+"F2.wireOp",EDGE,"E2.10.9.0")])],"isStart":false});
            var Q1083;
            Q1083=makeQuery(id+"F3.opExtrude","CAP_EDGE",EDGE,{"disambiguationData":[OSD([sQuery(id+"F2.wireOp",EDGE,"E3.0.22.9")])],"isStart":false});
            var Q1084;
            Q1084=makeQuery(id+"F3.opExtrude","CAP_EDGE",EDGE,{"disambiguationData":[OSD([sQuery(id+"F2.wireOp",EDGE,"E2.9.9.0")])],"isStart":false});
            var Q1085;
            Q1085=makeQuery(id+"F3.opExtrude","CAP_EDGE",EDGE,{"disambiguationData":[OSD([sQuery(id+"F2.wireOp",EDGE,"E2.16.9.0")])],"isStart":false});
            var Q1086;
            Q1086=makeQuery(id+"F3.opExtrude","CAP_EDGE",EDGE,{"disambiguationData":[OSD([sQuery(id+"F2.wireOp",EDGE,"E2.3.9.0")])],"isStart":false});
            var Q1087;
            Q1087=makeQuery(id+"F3.opExtrude","CAP_EDGE",EDGE,{"disambiguationData":[OSD([sQuery(id+"F2.wireOp",EDGE,"E3.0.29.9")])],"isStart":false});
            var Q1088;
            Q1088=makeQuery(id+"F3.opExtrude","CAP_EDGE",EDGE,{"disambiguationData":[OSD([sQuery(id+"F2.wireOp",EDGE,"E2.4.9.0")])],"isStart":false});
            var Q1089;
            Q1089=makeQuery(id+"F3.opExtrude","CAP_EDGE",EDGE,{"disambiguationData":[OSD([sQuery(id+"F2.wireOp",EDGE,"E3.0.23.9")])],"isStart":false});
            var Q1090;
            Q1090=makeQuery(id+"F3.opExtrude","CAP_EDGE",EDGE,{"disambiguationData":[OSD([sQuery(id+"F2.wireOp",EDGE,"E2.7.9.0")])],"isStart":false});
            var Q1091;
            Q1091=makeQuery(id+"F3.opExtrude","CAP_EDGE",EDGE,{"disambiguationData":[OSD([sQuery(id+"F2.wireOp",EDGE,"E3.0.26.9")])],"isStart":false});
            var Q1092;
            Q1092=makeQuery(id+"F3.opExtrude","CAP_EDGE",EDGE,{"disambiguationData":[OSD([sQuery(id+"F2.wireOp",EDGE,"E2.1.9.0")])],"isStart":false});
            var Q1093;
            Q1093=makeQuery(id+"F3.opExtrude","CAP_EDGE",EDGE,{"disambiguationData":[OSD([sQuery(id+"F2.wireOp",EDGE,"E3.0.20.9")])],"isStart":false});
            var Q1094;
            Q1094=makeQuery(id+"F3.opExtrude","CAP_EDGE",EDGE,{"disambiguationData":[OSD([sQuery(id+"F2.wireOp",EDGE,"E3.0.27.9")])],"isStart":false});
            var Q1095;
            Q1095=makeQuery(id+"F3.opExtrude","CAP_EDGE",EDGE,{"disambiguationData":[OSD([sQuery(id+"F2.wireOp",EDGE,"E2.14.9.0")])],"isStart":false});
            var Q1096;
            Q1096=makeQuery(id+"F3.opExtrude","CAP_EDGE",EDGE,{"disambiguationData":[OSD([sQuery(id+"F2.wireOp",EDGE,"E3.0.21.9")])],"isStart":false});
            var Q1097;
            Q1097=makeQuery(id+"F3.opExtrude","CAP_EDGE",EDGE,{"disambiguationData":[OSD([sQuery(id+"F2.wireOp",EDGE,"E2.2.9.0")])],"isStart":false});
            var Q1098;
            Q1098=makeQuery(id+"F3.opExtrude","CAP_EDGE",EDGE,{"disambiguationData":[OSD([sQuery(id+"F2.wireOp",EDGE,"E2.8.9.0")])],"isStart":false});
            var Q1099;
            Q1099=makeQuery(id+"F3.opExtrude","CAP_EDGE",EDGE,{"disambiguationData":[OSD([sQuery(id+"F2.wireOp",EDGE,"E3.0.28.9")])],"isStart":false});
            var Q1100;
            Q1100=makeQuery(id+"F3.opExtrude","CAP_EDGE",EDGE,{"disambiguationData":[OSD([sQuery(id+"F2.wireOp",EDGE,"E2.15.9.0")])],"isStart":false});
            var Q1101;
            Q1101=makeQuery(id+"F3.opExtrude","CAP_EDGE",EDGE,{"disambiguationData":[OSD([sQuery(id+"F2.wireOp",EDGE,"E2.17.9.0")])],"isStart":false});
            var Q1102;
            Q1102=makeQuery(id+"F3.opExtrude","CAP_EDGE",EDGE,{"disambiguationData":[OSD([sQuery(id+"F2.wireOp",EDGE,"E3.0.24.9")])],"isStart":false});
            var Q1103;
            Q1103=makeQuery(id+"F3.opExtrude","CAP_EDGE",EDGE,{"disambiguationData":[OSD([sQuery(id+"F2.wireOp",EDGE,"E2.11.9.0")])],"isStart":false});
            var Q1104;
            Q1104=makeQuery(id+"F3.opExtrude","CAP_EDGE",EDGE,{"disambiguationData":[OSD([sQuery(id+"F2.wireOp",EDGE,"E2.18.9.0")])],"isStart":false});
            var Q1105;
            Q1105=makeQuery(id+"F3.opExtrude","CAP_EDGE",EDGE,{"disambiguationData":[OSD([sQuery(id+"F2.wireOp",EDGE,"E2.5.9.0")])],"isStart":false});
            var Q1106;
            Q1106=makeQuery(id+"F3.opExtrude","CAP_EDGE",EDGE,{"disambiguationData":[OSD([sQuery(id+"F2.wireOp",EDGE,"E2.12.9.0")])],"isStart":false});
            var Q1107;
            Q1107=makeQuery(id+"F3.opExtrude","CAP_EDGE",EDGE,{"disambiguationData":[OSD([sQuery(id+"F2.wireOp",EDGE,"E2.6.9.0")])],"isStart":false});
            var Q1108;
            Q1108=makeQuery(id+"F3.opExtrude","CAP_EDGE",EDGE,{"disambiguationData":[OSD([sQuery(id+"F2.wireOp",EDGE,"E3.0.25.9")])],"isStart":false});
            var Q1109;
            Q1109=makeQuery(id+"F3.opExtrude","CAP_EDGE",EDGE,{"disambiguationData":[OSD([sQuery(id+"F2.wireOp",EDGE,"E2.19.9.0")])],"isStart":false});
            var Q1110;
            Q1110=makeQuery(id+"F3.opExtrude","CAP_EDGE",EDGE,{"disambiguationData":[OSD([sQuery(id+"F2.wireOp",EDGE,"E2.13.9.0")])],"isStart":false});
            var Q1111;
            Q1111=makeQuery(id+"F3.opExtrude","CAP_EDGE",EDGE,{"disambiguationData":[OSD([sQuery(id+"F2.wireOp",EDGE,"E2.10.9.2")])],"isStart":false});
            var Q1112;
            Q1112=makeQuery(id+"F3.opExtrude","CAP_EDGE",EDGE,{"disambiguationData":[OSD([sQuery(id+"F2.wireOp",EDGE,"E2.12.9.2")])],"isStart":false});
            var Q1113;
            Q1113=makeQuery(id+"F3.opExtrude","CAP_EDGE",EDGE,{"disambiguationData":[OSD([sQuery(id+"F2.wireOp",EDGE,"E2.6.9.2")])],"isStart":false});
            var Q1114;
            Q1114=makeQuery(id+"F3.opExtrude","CAP_EDGE",EDGE,{"disambiguationData":[OSD([sQuery(id+"F2.wireOp",EDGE,"E3.6.25.9")])],"isStart":false});
            var Q1115;
            Q1115=makeQuery(id+"F3.opExtrude","CAP_EDGE",EDGE,{"disambiguationData":[OSD([sQuery(id+"F2.wireOp",EDGE,"E2.19.9.2")])],"isStart":false});
            var Q1116;
            Q1116=makeQuery(id+"F3.opExtrude","CAP_EDGE",EDGE,{"disambiguationData":[OSD([sQuery(id+"F2.wireOp",EDGE,"E2.13.9.2")])],"isStart":false});
            var Q1117;
            Q1117=makeQuery(id+"F3.opExtrude","CAP_EDGE",EDGE,{"disambiguationData":[OSD([sQuery(id+"F2.wireOp",EDGE,"E2.7.9.2")])],"isStart":false});
            var Q1118;
            Q1118=makeQuery(id+"F3.opExtrude","CAP_EDGE",EDGE,{"disambiguationData":[OSD([sQuery(id+"F2.wireOp",EDGE,"E3.6.26.9")])],"isStart":false});
            var Q1119;
            Q1119=makeQuery(id+"F3.opExtrude","CAP_EDGE",EDGE,{"disambiguationData":[OSD([sQuery(id+"F2.wireOp",EDGE,"E2.1.9.2")])],"isStart":false});
            var Q1120;
            Q1120=makeQuery(id+"F3.opExtrude","CAP_EDGE",EDGE,{"disambiguationData":[OSD([sQuery(id+"F2.wireOp",EDGE,"E3.6.20.9")])],"isStart":false});
            var Q1121;
            Q1121=makeQuery(id+"F3.opExtrude","CAP_EDGE",EDGE,{"disambiguationData":[OSD([sQuery(id+"F2.wireOp",EDGE,"E3.6.27.9")])],"isStart":false});
            var Q1122;
            Q1122=makeQuery(id+"F3.opExtrude","CAP_EDGE",EDGE,{"disambiguationData":[OSD([sQuery(id+"F2.wireOp",EDGE,"E2.14.9.2")])],"isStart":false});
            var Q1123;
            Q1123=makeQuery(id+"F3.opExtrude","CAP_EDGE",EDGE,{"disambiguationData":[OSD([sQuery(id+"F2.wireOp",EDGE,"E3.6.22.9")])],"isStart":false});
            var Q1124;
            Q1124=makeQuery(id+"F3.opExtrude","CAP_EDGE",EDGE,{"disambiguationData":[OSD([sQuery(id+"F2.wireOp",EDGE,"E2.9.9.2")])],"isStart":false});
            var Q1125;
            Q1125=makeQuery(id+"F3.opExtrude","CAP_EDGE",EDGE,{"disambiguationData":[OSD([sQuery(id+"F2.wireOp",EDGE,"E2.16.9.2")])],"isStart":false});
            var Q1126;
            Q1126=makeQuery(id+"F3.opExtrude","CAP_EDGE",EDGE,{"disambiguationData":[OSD([sQuery(id+"F2.wireOp",EDGE,"E2.3.9.2")])],"isStart":false});
            var Q1127;
            Q1127=makeQuery(id+"F3.opExtrude","CAP_EDGE",EDGE,{"disambiguationData":[OSD([sQuery(id+"F2.wireOp",EDGE,"E3.6.29.9")])],"isStart":false});
            var Q1128;
            Q1128=makeQuery(id+"F3.opExtrude","CAP_EDGE",EDGE,{"disambiguationData":[OSD([sQuery(id+"F2.wireOp",EDGE,"E2.0.9.1")])],"isStart":false});
            var Q1129;
            Q1129=makeQuery(id+"F3.opExtrude","CAP_EDGE",EDGE,{"disambiguationData":[OSD([sQuery(id+"F2.wireOp",EDGE,"E2.4.9.2")])],"isStart":false});
            var Q1130;
            Q1130=makeQuery(id+"F3.opExtrude","CAP_EDGE",EDGE,{"disambiguationData":[OSD([sQuery(id+"F2.wireOp",EDGE,"E3.6.23.9")])],"isStart":false});
            var Q1131;
            Q1131=makeQuery(id+"F3.opExtrude","CAP_EDGE",EDGE,{"disambiguationData":[OSD([sQuery(id+"F2.wireOp",EDGE,"E2.17.9.2")])],"isStart":false});
            var Q1132;
            Q1132=makeQuery(id+"F3.opExtrude","CAP_EDGE",EDGE,{"disambiguationData":[OSD([sQuery(id+"F2.wireOp",EDGE,"E3.6.24.9")])],"isStart":false});
            var Q1133;
            Q1133=makeQuery(id+"F3.opExtrude","CAP_EDGE",EDGE,{"disambiguationData":[OSD([sQuery(id+"F2.wireOp",EDGE,"E2.11.9.2")])],"isStart":false});
            var Q1134;
            Q1134=makeQuery(id+"F3.opExtrude","CAP_EDGE",EDGE,{"disambiguationData":[OSD([sQuery(id+"F2.wireOp",EDGE,"E2.18.9.2")])],"isStart":false});
            var Q1135;
            Q1135=makeQuery(id+"F3.opExtrude","CAP_EDGE",EDGE,{"disambiguationData":[OSD([sQuery(id+"F2.wireOp",EDGE,"E2.5.9.2")])],"isStart":false});
            var Q1136;
            Q1136=makeQuery(id+"F3.opExtrude","CAP_EDGE",EDGE,{"disambiguationData":[OSD([sQuery(id+"F2.wireOp",EDGE,"E3.6.21.9")])],"isStart":false});
            var Q1137;
            Q1137=makeQuery(id+"F3.opExtrude","CAP_EDGE",EDGE,{"disambiguationData":[OSD([sQuery(id+"F2.wireOp",EDGE,"E2.8.9.2")])],"isStart":false});
            var Q1138;
            Q1138=makeQuery(id+"F3.opExtrude","CAP_EDGE",EDGE,{"disambiguationData":[OSD([sQuery(id+"F2.wireOp",EDGE,"E2.15.9.2")])],"isStart":false});
            var Q1139;
            Q1139=makeQuery(id+"F3.opExtrude","CAP_EDGE",EDGE,{"disambiguationData":[OSD([sQuery(id+"F2.wireOp",EDGE,"E2.2.9.2")])],"isStart":false});
            var Q1140;
            Q1140=makeQuery(id+"F3.opExtrude","CAP_EDGE",EDGE,{"disambiguationData":[OSD([sQuery(id+"F2.wireOp",EDGE,"E3.6.28.9")])],"isStart":false});
            var Q1141;
            Q1141=makeQuery(id+"F3.opExtrude","CAP_EDGE",EDGE,{"disambiguationData":[OSD([sQuery(id+"F2.wireOp",EDGE,"E2.0.9.3")])],"isStart":false});
            var Q1142;
            Q1142=makeQuery(id+"F3.opExtrude","CAP_EDGE",EDGE,{"disambiguationData":[OSD([sQuery(id+"F2.wireOp",EDGE,"E2.16.9.1")])],"isStart":false});
            var Q1143;
            Q1143=makeQuery(id+"F3.opExtrude","CAP_EDGE",EDGE,{"disambiguationData":[OSD([sQuery(id+"F2.wireOp",EDGE,"E2.3.9.1")])],"isStart":false});
            var Q1144;
            Q1144=makeQuery(id+"F3.opExtrude","CAP_EDGE",EDGE,{"disambiguationData":[OSD([sQuery(id+"F2.wireOp",EDGE,"E3.3.29.9")])],"isStart":false});
            var Q1145;
            Q1145=makeQuery(id+"F3.opExtrude","CAP_EDGE",EDGE,{"disambiguationData":[OSD([sQuery(id+"F2.wireOp",EDGE,"E2.4.9.1")])],"isStart":false});
            var Q1146;
            Q1146=makeQuery(id+"F3.opExtrude","CAP_EDGE",EDGE,{"disambiguationData":[OSD([sQuery(id+"F2.wireOp",EDGE,"E3.3.23.9")])],"isStart":false});
            var Q1147;
            Q1147=makeQuery(id+"F3.opExtrude","CAP_EDGE",EDGE,{"disambiguationData":[OSD([sQuery(id+"F2.wireOp",EDGE,"E2.17.9.1")])],"isStart":false});
            var Q1148;
            Q1148=makeQuery(id+"F3.opExtrude","CAP_EDGE",EDGE,{"disambiguationData":[OSD([sQuery(id+"F2.wireOp",EDGE,"E3.3.24.9")])],"isStart":false});
            var Q1149;
            Q1149=makeQuery(id+"F3.opExtrude","CAP_EDGE",EDGE,{"disambiguationData":[OSD([sQuery(id+"F2.wireOp",EDGE,"E2.11.9.1")])],"isStart":false});
            var Q1150;
            Q1150=makeQuery(id+"F3.opExtrude","CAP_EDGE",EDGE,{"disambiguationData":[OSD([sQuery(id+"F2.wireOp",EDGE,"E2.18.9.1")])],"isStart":false});
            var Q1151;
            Q1151=makeQuery(id+"F3.opExtrude","CAP_EDGE",EDGE,{"disambiguationData":[OSD([sQuery(id+"F2.wireOp",EDGE,"E2.5.9.1")])],"isStart":false});
            var Q1152;
            Q1152=makeQuery(id+"F3.opExtrude","CAP_EDGE",EDGE,{"disambiguationData":[OSD([sQuery(id+"F2.wireOp",EDGE,"E2.12.9.1")])],"isStart":false});
            var Q1153;
            Q1153=makeQuery(id+"F3.opExtrude","CAP_EDGE",EDGE,{"disambiguationData":[OSD([sQuery(id+"F2.wireOp",EDGE,"E2.10.9.1")])],"isStart":false});
            var Q1154;
            Q1154=makeQuery(id+"F3.opExtrude","CAP_EDGE",EDGE,{"disambiguationData":[OSD([sQuery(id+"F2.wireOp",EDGE,"E3.3.22.9")])],"isStart":false});
            var Q1155;
            Q1155=makeQuery(id+"F3.opExtrude","CAP_EDGE",EDGE,{"disambiguationData":[OSD([sQuery(id+"F2.wireOp",EDGE,"E2.9.9.1")])],"isStart":false});
            var Q1156;
            Q1156=makeQuery(id+"F3.opExtrude","CAP_EDGE",EDGE,{"disambiguationData":[OSD([sQuery(id+"F2.wireOp",EDGE,"E2.15.9.1")])],"isStart":false});
            var Q1157;
            Q1157=makeQuery(id+"F3.opExtrude","CAP_EDGE",EDGE,{"disambiguationData":[OSD([sQuery(id+"F2.wireOp",EDGE,"E2.2.9.1")])],"isStart":false});
            var Q1158;
            Q1158=makeQuery(id+"F3.opExtrude","CAP_EDGE",EDGE,{"disambiguationData":[OSD([sQuery(id+"F2.wireOp",EDGE,"E3.3.28.9")])],"isStart":false});
            var Q1159;
            Q1159=makeQuery(id+"F3.opExtrude","CAP_EDGE",EDGE,{"disambiguationData":[OSD([sQuery(id+"F2.wireOp",EDGE,"E2.6.9.1")])],"isStart":false});
            var Q1160;
            Q1160=makeQuery(id+"F3.opExtrude","CAP_EDGE",EDGE,{"disambiguationData":[OSD([sQuery(id+"F2.wireOp",EDGE,"E3.3.25.9")])],"isStart":false});
            var Q1161;
            Q1161=makeQuery(id+"F3.opExtrude","CAP_EDGE",EDGE,{"disambiguationData":[OSD([sQuery(id+"F2.wireOp",EDGE,"E2.19.9.1")])],"isStart":false});
            var Q1162;
            Q1162=makeQuery(id+"F3.opExtrude","CAP_EDGE",EDGE,{"disambiguationData":[OSD([sQuery(id+"F2.wireOp",EDGE,"E2.13.9.1")])],"isStart":false});
            var Q1163;
            Q1163=makeQuery(id+"F3.opExtrude","CAP_EDGE",EDGE,{"disambiguationData":[OSD([sQuery(id+"F2.wireOp",EDGE,"E2.7.9.1")])],"isStart":false});
            var Q1164;
            Q1164=makeQuery(id+"F3.opExtrude","CAP_EDGE",EDGE,{"disambiguationData":[OSD([sQuery(id+"F2.wireOp",EDGE,"E3.3.26.9")])],"isStart":false});
            var Q1165;
            Q1165=makeQuery(id+"F3.opExtrude","CAP_EDGE",EDGE,{"disambiguationData":[OSD([sQuery(id+"F2.wireOp",EDGE,"E2.1.9.1")])],"isStart":false});
            var Q1166;
            Q1166=makeQuery(id+"F3.opExtrude","CAP_EDGE",EDGE,{"disambiguationData":[OSD([sQuery(id+"F2.wireOp",EDGE,"E3.3.20.9")])],"isStart":false});
            var Q1167;
            Q1167=makeQuery(id+"F3.opExtrude","CAP_EDGE",EDGE,{"disambiguationData":[OSD([sQuery(id+"F2.wireOp",EDGE,"E3.3.27.9")])],"isStart":false});
            var Q1168;
            Q1168=makeQuery(id+"F3.opExtrude","CAP_EDGE",EDGE,{"disambiguationData":[OSD([sQuery(id+"F2.wireOp",EDGE,"E2.14.9.1")])],"isStart":false});
            var Q1169;
            Q1169=makeQuery(id+"F3.opExtrude","CAP_EDGE",EDGE,{"disambiguationData":[OSD([sQuery(id+"F2.wireOp",EDGE,"E3.3.21.9")])],"isStart":false});
            var Q1170;
            Q1170=makeQuery(id+"F3.opExtrude","CAP_EDGE",EDGE,{"disambiguationData":[OSD([sQuery(id+"F2.wireOp",EDGE,"E2.8.9.1")])],"isStart":false});
            var Q1171;
            Q1171=makeQuery(id+"F3.opExtrude","CAP_EDGE",EDGE,{"disambiguationData":[OSD([sQuery(id+"F2.wireOp",EDGE,"E2.10.9.3")])],"isStart":false});
            var Q1172;
            Q1172=makeQuery(id+"F3.opExtrude","CAP_EDGE",EDGE,{"disambiguationData":[OSD([sQuery(id+"F2.wireOp",EDGE,"E3.9.22.9")])],"isStart":false});
            var Q1173;
            Q1173=makeQuery(id+"F3.opExtrude","CAP_EDGE",EDGE,{"disambiguationData":[OSD([sQuery(id+"F2.wireOp",EDGE,"E2.9.9.3")])],"isStart":false});
            var Q1174;
            Q1174=makeQuery(id+"F3.opExtrude","CAP_EDGE",EDGE,{"disambiguationData":[OSD([sQuery(id+"F2.wireOp",EDGE,"E2.16.9.3")])],"isStart":false});
            var Q1175;
            Q1175=makeQuery(id+"F3.opExtrude","CAP_EDGE",EDGE,{"disambiguationData":[OSD([sQuery(id+"F2.wireOp",EDGE,"E2.3.9.3")])],"isStart":false});
            var Q1176;
            Q1176=makeQuery(id+"F3.opExtrude","CAP_EDGE",EDGE,{"disambiguationData":[OSD([sQuery(id+"F2.wireOp",EDGE,"E3.9.29.9")])],"isStart":false});
            var Q1177;
            Q1177=makeQuery(id+"F3.opExtrude","CAP_EDGE",EDGE,{"disambiguationData":[OSD([sQuery(id+"F2.wireOp",EDGE,"E2.13.9.3")])],"isStart":false});
            var Q1178;
            Q1178=makeQuery(id+"F3.opExtrude","CAP_EDGE",EDGE,{"disambiguationData":[OSD([sQuery(id+"F2.wireOp",EDGE,"E2.7.9.3")])],"isStart":false});
            var Q1179;
            Q1179=makeQuery(id+"F3.opExtrude","CAP_EDGE",EDGE,{"disambiguationData":[OSD([sQuery(id+"F2.wireOp",EDGE,"E3.9.26.9")])],"isStart":false});
            var Q1180;
            Q1180=makeQuery(id+"F3.opExtrude","CAP_EDGE",EDGE,{"disambiguationData":[OSD([sQuery(id+"F2.wireOp",EDGE,"E2.1.9.3")])],"isStart":false});
            var Q1181;
            Q1181=makeQuery(id+"F3.opExtrude","CAP_EDGE",EDGE,{"disambiguationData":[OSD([sQuery(id+"F2.wireOp",EDGE,"E3.9.20.9")])],"isStart":false});
            var Q1182;
            Q1182=makeQuery(id+"F3.opExtrude","CAP_EDGE",EDGE,{"disambiguationData":[OSD([sQuery(id+"F2.wireOp",EDGE,"E3.9.27.9")])],"isStart":false});
            var Q1183;
            Q1183=makeQuery(id+"F3.opExtrude","CAP_EDGE",EDGE,{"disambiguationData":[OSD([sQuery(id+"F2.wireOp",EDGE,"E2.14.9.3")])],"isStart":false});
            var Q1184;
            Q1184=makeQuery(id+"F3.opExtrude","CAP_EDGE",EDGE,{"disambiguationData":[OSD([sQuery(id+"F2.wireOp",EDGE,"E3.9.21.9")])],"isStart":false});
            var Q1185;
            Q1185=makeQuery(id+"F3.opExtrude","CAP_EDGE",EDGE,{"disambiguationData":[OSD([sQuery(id+"F2.wireOp",EDGE,"E2.8.9.3")])],"isStart":false});
            var Q1186;
            Q1186=makeQuery(id+"F3.opExtrude","CAP_EDGE",EDGE,{"disambiguationData":[OSD([sQuery(id+"F2.wireOp",EDGE,"E2.15.9.3")])],"isStart":false});
            var Q1187;
            Q1187=makeQuery(id+"F3.opExtrude","CAP_EDGE",EDGE,{"disambiguationData":[OSD([sQuery(id+"F2.wireOp",EDGE,"E2.2.9.3")])],"isStart":false});
            var Q1188;
            Q1188=makeQuery(id+"F3.opExtrude","CAP_EDGE",EDGE,{"disambiguationData":[OSD([sQuery(id+"F2.wireOp",EDGE,"E3.9.28.9")])],"isStart":false});
            var Q1189;
            Q1189=makeQuery(id+"F3.opExtrude","CAP_EDGE",EDGE,{"disambiguationData":[OSD([sQuery(id+"F2.wireOp",EDGE,"E3.9.23.9")])],"isStart":false});
            var Q1190;
            Q1190=makeQuery(id+"F3.opExtrude","CAP_EDGE",EDGE,{"disambiguationData":[OSD([sQuery(id+"F2.wireOp",EDGE,"E2.4.9.3")])],"isStart":false});
            var Q1191;
            Q1191=makeQuery(id+"F3.opExtrude","CAP_EDGE",EDGE,{"disambiguationData":[OSD([sQuery(id+"F2.wireOp",EDGE,"E2.17.9.3")])],"isStart":false});
            var Q1192;
            Q1192=makeQuery(id+"F3.opExtrude","CAP_EDGE",EDGE,{"disambiguationData":[OSD([sQuery(id+"F2.wireOp",EDGE,"E3.9.24.9")])],"isStart":false});
            var Q1193;
            Q1193=makeQuery(id+"F3.opExtrude","CAP_EDGE",EDGE,{"disambiguationData":[OSD([sQuery(id+"F2.wireOp",EDGE,"E2.11.9.3")])],"isStart":false});
            var Q1194;
            Q1194=makeQuery(id+"F3.opExtrude","CAP_EDGE",EDGE,{"disambiguationData":[OSD([sQuery(id+"F2.wireOp",EDGE,"E2.18.9.3")])],"isStart":false});
            var Q1195;
            Q1195=makeQuery(id+"F3.opExtrude","CAP_EDGE",EDGE,{"disambiguationData":[OSD([sQuery(id+"F2.wireOp",EDGE,"E2.5.9.3")])],"isStart":false});
            var Q1196;
            Q1196=makeQuery(id+"F3.opExtrude","CAP_EDGE",EDGE,{"disambiguationData":[OSD([sQuery(id+"F2.wireOp",EDGE,"E2.12.9.3")])],"isStart":false});
            var Q1197;
            Q1197=makeQuery(id+"F3.opExtrude","CAP_EDGE",EDGE,{"disambiguationData":[OSD([sQuery(id+"F2.wireOp",EDGE,"E2.6.9.3")])],"isStart":false});
            var Q1198;
            Q1198=makeQuery(id+"F3.opExtrude","CAP_EDGE",EDGE,{"disambiguationData":[OSD([sQuery(id+"F2.wireOp",EDGE,"E3.9.25.9")])],"isStart":false});
            var Q1199;
            Q1199=makeQuery(id+"F3.opExtrude","CAP_EDGE",EDGE,{"disambiguationData":[OSD([sQuery(id+"F2.wireOp",EDGE,"E2.19.9.3")])],"isStart":false});
            var Q1200;
            Q1200=makeQuery(id+"F3.opExtrude","CAP_EDGE",EDGE,{"disambiguationData":[OSD([sQuery(id+"F2.wireOp",EDGE,"E2.0.10.3")])],"isStart":false});
            var Q1201;
            Q1201=makeQuery(id+"F3.opExtrude","CAP_EDGE",EDGE,{"disambiguationData":[OSD([sQuery(id+"F2.wireOp",EDGE,"E2.0.10.0")])],"isStart":false});
            var Q1202;
            Q1202=makeQuery(id+"F3.opExtrude","CAP_EDGE",EDGE,{"disambiguationData":[OSD([sQuery(id+"F2.wireOp",EDGE,"E2.0.10.2")])],"isStart":false});
            var Q1203;
            Q1203=makeQuery(id+"F3.opExtrude","CAP_EDGE",EDGE,{"disambiguationData":[OSD([sQuery(id+"F2.wireOp",EDGE,"E2.10.10.3")])],"isStart":false});
            var Q1204;
            Q1204=makeQuery(id+"F3.opExtrude","CAP_EDGE",EDGE,{"disambiguationData":[OSD([sQuery(id+"F2.wireOp",EDGE,"E3.9.22.10")])],"isStart":false});
            var Q1205;
            Q1205=makeQuery(id+"F3.opExtrude","CAP_EDGE",EDGE,{"disambiguationData":[OSD([sQuery(id+"F2.wireOp",EDGE,"E2.9.10.3")])],"isStart":false});
            var Q1206;
            Q1206=makeQuery(id+"F3.opExtrude","CAP_EDGE",EDGE,{"disambiguationData":[OSD([sQuery(id+"F2.wireOp",EDGE,"E2.6.10.3")])],"isStart":false});
            var Q1207;
            Q1207=makeQuery(id+"F3.opExtrude","CAP_EDGE",EDGE,{"disambiguationData":[OSD([sQuery(id+"F2.wireOp",EDGE,"E3.9.25.10")])],"isStart":false});
            var Q1208;
            Q1208=makeQuery(id+"F3.opExtrude","CAP_EDGE",EDGE,{"disambiguationData":[OSD([sQuery(id+"F2.wireOp",EDGE,"E2.19.10.3")])],"isStart":false});
            var Q1209;
            Q1209=makeQuery(id+"F3.opExtrude","CAP_EDGE",EDGE,{"disambiguationData":[OSD([sQuery(id+"F2.wireOp",EDGE,"E2.13.10.3")])],"isStart":false});
            var Q1210;
            Q1210=makeQuery(id+"F3.opExtrude","CAP_EDGE",EDGE,{"disambiguationData":[OSD([sQuery(id+"F2.wireOp",EDGE,"E2.7.10.3")])],"isStart":false});
            var Q1211;
            Q1211=makeQuery(id+"F3.opExtrude","CAP_EDGE",EDGE,{"disambiguationData":[OSD([sQuery(id+"F2.wireOp",EDGE,"E3.9.26.10")])],"isStart":false});
            var Q1212;
            Q1212=makeQuery(id+"F3.opExtrude","CAP_EDGE",EDGE,{"disambiguationData":[OSD([sQuery(id+"F2.wireOp",EDGE,"E2.1.10.3")])],"isStart":false});
            var Q1213;
            Q1213=makeQuery(id+"F3.opExtrude","CAP_EDGE",EDGE,{"disambiguationData":[OSD([sQuery(id+"F2.wireOp",EDGE,"E3.9.20.10")])],"isStart":false});
            var Q1214;
            Q1214=makeQuery(id+"F3.opExtrude","CAP_EDGE",EDGE,{"disambiguationData":[OSD([sQuery(id+"F2.wireOp",EDGE,"E3.9.27.10")])],"isStart":false});
            var Q1215;
            Q1215=makeQuery(id+"F3.opExtrude","CAP_EDGE",EDGE,{"disambiguationData":[OSD([sQuery(id+"F2.wireOp",EDGE,"E2.14.10.3")])],"isStart":false});
            var Q1216;
            Q1216=makeQuery(id+"F3.opExtrude","CAP_EDGE",EDGE,{"disambiguationData":[OSD([sQuery(id+"F2.wireOp",EDGE,"E3.9.21.10")])],"isStart":false});
            var Q1217;
            Q1217=makeQuery(id+"F3.opExtrude","CAP_EDGE",EDGE,{"disambiguationData":[OSD([sQuery(id+"F2.wireOp",EDGE,"E2.8.10.3")])],"isStart":false});
            var Q1218;
            Q1218=makeQuery(id+"F3.opExtrude","CAP_EDGE",EDGE,{"disambiguationData":[OSD([sQuery(id+"F2.wireOp",EDGE,"E2.16.10.3")])],"isStart":false});
            var Q1219;
            Q1219=makeQuery(id+"F3.opExtrude","CAP_EDGE",EDGE,{"disambiguationData":[OSD([sQuery(id+"F2.wireOp",EDGE,"E2.3.10.3")])],"isStart":false});
            var Q1220;
            Q1220=makeQuery(id+"F3.opExtrude","CAP_EDGE",EDGE,{"disambiguationData":[OSD([sQuery(id+"F2.wireOp",EDGE,"E3.9.29.10")])],"isStart":false});
            var Q1221;
            Q1221=makeQuery(id+"F3.opExtrude","CAP_EDGE",EDGE,{"disambiguationData":[OSD([sQuery(id+"F2.wireOp",EDGE,"E3.9.23.10")])],"isStart":false});
            var Q1222;
            Q1222=makeQuery(id+"F3.opExtrude","CAP_EDGE",EDGE,{"disambiguationData":[OSD([sQuery(id+"F2.wireOp",EDGE,"E2.17.10.3")])],"isStart":false});
            var Q1223;
            Q1223=makeQuery(id+"F3.opExtrude","CAP_EDGE",EDGE,{"disambiguationData":[OSD([sQuery(id+"F2.wireOp",EDGE,"E2.4.10.3")])],"isStart":false});
            var Q1224;
            Q1224=makeQuery(id+"F3.opExtrude","CAP_EDGE",EDGE,{"disambiguationData":[OSD([sQuery(id+"F2.wireOp",EDGE,"E2.11.10.3")])],"isStart":false});
            var Q1225;
            Q1225=makeQuery(id+"F3.opExtrude","CAP_EDGE",EDGE,{"disambiguationData":[OSD([sQuery(id+"F2.wireOp",EDGE,"E2.18.10.3")])],"isStart":false});
            var Q1226;
            Q1226=makeQuery(id+"F3.opExtrude","CAP_EDGE",EDGE,{"disambiguationData":[OSD([sQuery(id+"F2.wireOp",EDGE,"E3.9.24.10")])],"isStart":false});
            var Q1227;
            Q1227=makeQuery(id+"F3.opExtrude","CAP_EDGE",EDGE,{"disambiguationData":[OSD([sQuery(id+"F2.wireOp",EDGE,"E2.5.10.3")])],"isStart":false});
            var Q1228;
            Q1228=makeQuery(id+"F3.opExtrude","CAP_EDGE",EDGE,{"disambiguationData":[OSD([sQuery(id+"F2.wireOp",EDGE,"E2.12.10.3")])],"isStart":false});
            var Q1229;
            Q1229=makeQuery(id+"F3.opExtrude","CAP_EDGE",EDGE,{"disambiguationData":[OSD([sQuery(id+"F2.wireOp",EDGE,"E2.10.10.0")])],"isStart":false});
            var Q1230;
            Q1230=makeQuery(id+"F3.opExtrude","CAP_EDGE",EDGE,{"disambiguationData":[OSD([sQuery(id+"F2.wireOp",EDGE,"E3.0.22.10")])],"isStart":false});
            var Q1231;
            Q1231=makeQuery(id+"F3.opExtrude","CAP_EDGE",EDGE,{"disambiguationData":[OSD([sQuery(id+"F2.wireOp",EDGE,"E2.9.10.0")])],"isStart":false});
            var Q1232;
            Q1232=makeQuery(id+"F3.opExtrude","CAP_EDGE",EDGE,{"disambiguationData":[OSD([sQuery(id+"F2.wireOp",EDGE,"E2.16.10.0")])],"isStart":false});
            var Q1233;
            Q1233=makeQuery(id+"F3.opExtrude","CAP_EDGE",EDGE,{"disambiguationData":[OSD([sQuery(id+"F2.wireOp",EDGE,"E2.3.10.0")])],"isStart":false});
            var Q1234;
            Q1234=makeQuery(id+"F3.opExtrude","CAP_EDGE",EDGE,{"disambiguationData":[OSD([sQuery(id+"F2.wireOp",EDGE,"E2.15.10.3")])],"isStart":false});
            var Q1235;
            Q1235=makeQuery(id+"F3.opExtrude","CAP_EDGE",EDGE,{"disambiguationData":[OSD([sQuery(id+"F2.wireOp",EDGE,"E2.2.10.3")])],"isStart":false});
            var Q1236;
            Q1236=makeQuery(id+"F3.opExtrude","CAP_EDGE",EDGE,{"disambiguationData":[OSD([sQuery(id+"F2.wireOp",EDGE,"E3.9.28.10")])],"isStart":false});
            var Q1237;
            Q1237=makeQuery(id+"F3.opExtrude","CAP_EDGE",EDGE,{"disambiguationData":[OSD([sQuery(id+"F2.wireOp",EDGE,"E2.19.10.0")])],"isStart":false});
            var Q1238;
            Q1238=makeQuery(id+"F3.opExtrude","CAP_EDGE",EDGE,{"disambiguationData":[OSD([sQuery(id+"F2.wireOp",EDGE,"E2.13.10.0")])],"isStart":false});
            var Q1239;
            Q1239=makeQuery(id+"F3.opExtrude","CAP_EDGE",EDGE,{"disambiguationData":[OSD([sQuery(id+"F2.wireOp",EDGE,"E2.7.10.0")])],"isStart":false});
            var Q1240;
            Q1240=makeQuery(id+"F3.opExtrude","CAP_EDGE",EDGE,{"disambiguationData":[OSD([sQuery(id+"F2.wireOp",EDGE,"E3.0.26.10")])],"isStart":false});
            var Q1241;
            Q1241=makeQuery(id+"F3.opExtrude","CAP_EDGE",EDGE,{"disambiguationData":[OSD([sQuery(id+"F2.wireOp",EDGE,"E2.14.10.0")])],"isStart":false});
            var Q1242;
            Q1242=makeQuery(id+"F3.opExtrude","CAP_EDGE",EDGE,{"disambiguationData":[OSD([sQuery(id+"F2.wireOp",EDGE,"E3.0.20.10")])],"isStart":false});
            var Q1243;
            Q1243=makeQuery(id+"F3.opExtrude","CAP_EDGE",EDGE,{"disambiguationData":[OSD([sQuery(id+"F2.wireOp",EDGE,"E2.1.10.0")])],"isStart":false});
            var Q1244;
            Q1244=makeQuery(id+"F3.opExtrude","CAP_EDGE",EDGE,{"disambiguationData":[OSD([sQuery(id+"F2.wireOp",EDGE,"E2.8.10.0")])],"isStart":false});
            var Q1245;
            Q1245=makeQuery(id+"F3.opExtrude","CAP_EDGE",EDGE,{"disambiguationData":[OSD([sQuery(id+"F2.wireOp",EDGE,"E3.0.27.10")])],"isStart":false});
            var Q1246;
            Q1246=makeQuery(id+"F3.opExtrude","CAP_EDGE",EDGE,{"disambiguationData":[OSD([sQuery(id+"F2.wireOp",EDGE,"E2.2.10.0")])],"isStart":false});
            var Q1247;
            Q1247=makeQuery(id+"F3.opExtrude","CAP_EDGE",EDGE,{"disambiguationData":[OSD([sQuery(id+"F2.wireOp",EDGE,"E3.0.21.10")])],"isStart":false});
            var Q1248;
            Q1248=makeQuery(id+"F3.opExtrude","CAP_EDGE",EDGE,{"disambiguationData":[OSD([sQuery(id+"F2.wireOp",EDGE,"E3.0.28.10")])],"isStart":false});
            var Q1249;
            Q1249=makeQuery(id+"F3.opExtrude","CAP_EDGE",EDGE,{"disambiguationData":[OSD([sQuery(id+"F2.wireOp",EDGE,"E2.15.10.0")])],"isStart":false});
            var Q1250;
            Q1250=makeQuery(id+"F3.opExtrude","CAP_EDGE",EDGE,{"disambiguationData":[OSD([sQuery(id+"F2.wireOp",EDGE,"E3.0.29.10")])],"isStart":false});
            var Q1251;
            Q1251=makeQuery(id+"F3.opExtrude","CAP_EDGE",EDGE,{"disambiguationData":[OSD([sQuery(id+"F2.wireOp",EDGE,"E2.4.10.0")])],"isStart":false});
            var Q1252;
            Q1252=makeQuery(id+"F3.opExtrude","CAP_EDGE",EDGE,{"disambiguationData":[OSD([sQuery(id+"F2.wireOp",EDGE,"E3.0.23.10")])],"isStart":false});
            var Q1253;
            Q1253=makeQuery(id+"F3.opExtrude","CAP_EDGE",EDGE,{"disambiguationData":[OSD([sQuery(id+"F2.wireOp",EDGE,"E2.17.10.0")])],"isStart":false});
            var Q1254;
            Q1254=makeQuery(id+"F3.opExtrude","CAP_EDGE",EDGE,{"disambiguationData":[OSD([sQuery(id+"F2.wireOp",EDGE,"E3.0.24.10")])],"isStart":false});
            var Q1255;
            Q1255=makeQuery(id+"F3.opExtrude","CAP_EDGE",EDGE,{"disambiguationData":[OSD([sQuery(id+"F2.wireOp",EDGE,"E2.11.10.0")])],"isStart":false});
            var Q1256;
            Q1256=makeQuery(id+"F3.opExtrude","CAP_EDGE",EDGE,{"disambiguationData":[OSD([sQuery(id+"F2.wireOp",EDGE,"E2.18.10.0")])],"isStart":false});
            var Q1257;
            Q1257=makeQuery(id+"F3.opExtrude","CAP_EDGE",EDGE,{"disambiguationData":[OSD([sQuery(id+"F2.wireOp",EDGE,"E2.5.10.0")])],"isStart":false});
            var Q1258;
            Q1258=makeQuery(id+"F3.opExtrude","CAP_EDGE",EDGE,{"disambiguationData":[OSD([sQuery(id+"F2.wireOp",EDGE,"E2.12.10.0")])],"isStart":false});
            var Q1259;
            Q1259=makeQuery(id+"F3.opExtrude","CAP_EDGE",EDGE,{"disambiguationData":[OSD([sQuery(id+"F2.wireOp",EDGE,"E2.6.10.0")])],"isStart":false});
            var Q1260;
            Q1260=makeQuery(id+"F3.opExtrude","CAP_EDGE",EDGE,{"disambiguationData":[OSD([sQuery(id+"F2.wireOp",EDGE,"E3.0.25.10")])],"isStart":false});
            var Q1261;
            Q1261=makeQuery(id+"F3.opExtrude","CAP_EDGE",EDGE,{"disambiguationData":[OSD([sQuery(id+"F2.wireOp",EDGE,"E2.0.10.1")])],"isStart":false});
            var Q1262;
            Q1262=makeQuery(id+"F3.opExtrude","CAP_EDGE",EDGE,{"disambiguationData":[OSD([sQuery(id+"F2.wireOp",EDGE,"E3.6.29.10")])],"isStart":false});
            var Q1263;
            Q1263=makeQuery(id+"F3.opExtrude","CAP_EDGE",EDGE,{"disambiguationData":[OSD([sQuery(id+"F2.wireOp",EDGE,"E2.4.10.2")])],"isStart":false});
            var Q1264;
            Q1264=makeQuery(id+"F3.opExtrude","CAP_EDGE",EDGE,{"disambiguationData":[OSD([sQuery(id+"F2.wireOp",EDGE,"E3.6.23.10")])],"isStart":false});
            var Q1265;
            Q1265=makeQuery(id+"F3.opExtrude","CAP_EDGE",EDGE,{"disambiguationData":[OSD([sQuery(id+"F2.wireOp",EDGE,"E2.17.10.2")])],"isStart":false});
            var Q1266;
            Q1266=makeQuery(id+"F3.opExtrude","CAP_EDGE",EDGE,{"disambiguationData":[OSD([sQuery(id+"F2.wireOp",EDGE,"E3.6.24.10")])],"isStart":false});
            var Q1267;
            Q1267=makeQuery(id+"F3.opExtrude","CAP_EDGE",EDGE,{"disambiguationData":[OSD([sQuery(id+"F2.wireOp",EDGE,"E2.11.10.2")])],"isStart":false});
            var Q1268;
            Q1268=makeQuery(id+"F3.opExtrude","CAP_EDGE",EDGE,{"disambiguationData":[OSD([sQuery(id+"F2.wireOp",EDGE,"E2.18.10.2")])],"isStart":false});
            var Q1269;
            Q1269=makeQuery(id+"F3.opExtrude","CAP_EDGE",EDGE,{"disambiguationData":[OSD([sQuery(id+"F2.wireOp",EDGE,"E2.5.10.2")])],"isStart":false});
            var Q1270;
            Q1270=makeQuery(id+"F3.opExtrude","CAP_EDGE",EDGE,{"disambiguationData":[OSD([sQuery(id+"F2.wireOp",EDGE,"E2.12.10.2")])],"isStart":false});
            var Q1271;
            Q1271=makeQuery(id+"F3.opExtrude","CAP_EDGE",EDGE,{"disambiguationData":[OSD([sQuery(id+"F2.wireOp",EDGE,"E2.6.10.2")])],"isStart":false});
            var Q1272;
            Q1272=makeQuery(id+"F3.opExtrude","CAP_EDGE",EDGE,{"disambiguationData":[OSD([sQuery(id+"F2.wireOp",EDGE,"E3.6.25.10")])],"isStart":false});
            var Q1273;
            Q1273=makeQuery(id+"F3.opExtrude","CAP_EDGE",EDGE,{"disambiguationData":[OSD([sQuery(id+"F2.wireOp",EDGE,"E2.10.10.2")])],"isStart":false});
            var Q1274;
            Q1274=makeQuery(id+"F3.opExtrude","CAP_EDGE",EDGE,{"disambiguationData":[OSD([sQuery(id+"F2.wireOp",EDGE,"E3.6.22.10")])],"isStart":false});
            var Q1275;
            Q1275=makeQuery(id+"F3.opExtrude","CAP_EDGE",EDGE,{"disambiguationData":[OSD([sQuery(id+"F2.wireOp",EDGE,"E2.9.10.2")])],"isStart":false});
            var Q1276;
            Q1276=makeQuery(id+"F3.opExtrude","CAP_EDGE",EDGE,{"disambiguationData":[OSD([sQuery(id+"F2.wireOp",EDGE,"E2.16.10.2")])],"isStart":false});
            var Q1277;
            Q1277=makeQuery(id+"F3.opExtrude","CAP_EDGE",EDGE,{"disambiguationData":[OSD([sQuery(id+"F2.wireOp",EDGE,"E2.3.10.2")])],"isStart":false});
            var Q1278;
            Q1278=makeQuery(id+"F3.opExtrude","CAP_EDGE",EDGE,{"disambiguationData":[OSD([sQuery(id+"F2.wireOp",EDGE,"E3.6.28.10")])],"isStart":false});
            var Q1279;
            Q1279=makeQuery(id+"F3.opExtrude","CAP_EDGE",EDGE,{"disambiguationData":[OSD([sQuery(id+"F2.wireOp",EDGE,"E2.19.10.2")])],"isStart":false});
            var Q1280;
            Q1280=makeQuery(id+"F3.opExtrude","CAP_EDGE",EDGE,{"disambiguationData":[OSD([sQuery(id+"F2.wireOp",EDGE,"E2.13.10.2")])],"isStart":false});
            var Q1281;
            Q1281=makeQuery(id+"F3.opExtrude","CAP_EDGE",EDGE,{"disambiguationData":[OSD([sQuery(id+"F2.wireOp",EDGE,"E2.7.10.2")])],"isStart":false});
            var Q1282;
            Q1282=makeQuery(id+"F3.opExtrude","CAP_EDGE",EDGE,{"disambiguationData":[OSD([sQuery(id+"F2.wireOp",EDGE,"E3.6.26.10")])],"isStart":false});
            var Q1283;
            Q1283=makeQuery(id+"F3.opExtrude","CAP_EDGE",EDGE,{"disambiguationData":[OSD([sQuery(id+"F2.wireOp",EDGE,"E2.1.10.2")])],"isStart":false});
            var Q1284;
            Q1284=makeQuery(id+"F3.opExtrude","CAP_EDGE",EDGE,{"disambiguationData":[OSD([sQuery(id+"F2.wireOp",EDGE,"E3.6.20.10")])],"isStart":false});
            var Q1285;
            Q1285=makeQuery(id+"F3.opExtrude","CAP_EDGE",EDGE,{"disambiguationData":[OSD([sQuery(id+"F2.wireOp",EDGE,"E3.6.27.10")])],"isStart":false});
            var Q1286;
            Q1286=makeQuery(id+"F3.opExtrude","CAP_EDGE",EDGE,{"disambiguationData":[OSD([sQuery(id+"F2.wireOp",EDGE,"E2.14.10.2")])],"isStart":false});
            var Q1287;
            Q1287=makeQuery(id+"F3.opExtrude","CAP_EDGE",EDGE,{"disambiguationData":[OSD([sQuery(id+"F2.wireOp",EDGE,"E3.6.21.10")])],"isStart":false});
            var Q1288;
            Q1288=makeQuery(id+"F3.opExtrude","CAP_EDGE",EDGE,{"disambiguationData":[OSD([sQuery(id+"F2.wireOp",EDGE,"E2.8.10.2")])],"isStart":false});
            var Q1289;
            Q1289=makeQuery(id+"F3.opExtrude","CAP_EDGE",EDGE,{"disambiguationData":[OSD([sQuery(id+"F2.wireOp",EDGE,"E2.15.10.2")])],"isStart":false});
            var Q1290;
            Q1290=makeQuery(id+"F3.opExtrude","CAP_EDGE",EDGE,{"disambiguationData":[OSD([sQuery(id+"F2.wireOp",EDGE,"E2.2.10.2")])],"isStart":false});
            var Q1291;
            Q1291=makeQuery(id+"F3.opExtrude","CAP_EDGE",EDGE,{"disambiguationData":[OSD([sQuery(id+"F2.wireOp",EDGE,"E2.10.10.1")])],"isStart":false});
            var Q1292;
            Q1292=makeQuery(id+"F3.opExtrude","CAP_EDGE",EDGE,{"disambiguationData":[OSD([sQuery(id+"F2.wireOp",EDGE,"E3.3.22.10")])],"isStart":false});
            var Q1293;
            Q1293=makeQuery(id+"F3.opExtrude","CAP_EDGE",EDGE,{"disambiguationData":[OSD([sQuery(id+"F2.wireOp",EDGE,"E2.9.10.1")])],"isStart":false});
            var Q1294;
            Q1294=makeQuery(id+"F3.opExtrude","CAP_EDGE",EDGE,{"disambiguationData":[OSD([sQuery(id+"F2.wireOp",EDGE,"E2.16.10.1")])],"isStart":false});
            var Q1295;
            Q1295=makeQuery(id+"F3.opExtrude","CAP_EDGE",EDGE,{"disambiguationData":[OSD([sQuery(id+"F2.wireOp",EDGE,"E2.3.10.1")])],"isStart":false});
            var Q1296;
            Q1296=makeQuery(id+"F3.opExtrude","CAP_EDGE",EDGE,{"disambiguationData":[OSD([sQuery(id+"F2.wireOp",EDGE,"E3.3.29.10")])],"isStart":false});
            var Q1297;
            Q1297=makeQuery(id+"F3.opExtrude","CAP_EDGE",EDGE,{"disambiguationData":[OSD([sQuery(id+"F2.wireOp",EDGE,"E2.4.10.1")])],"isStart":false});
            var Q1298;
            Q1298=makeQuery(id+"F3.opExtrude","CAP_EDGE",EDGE,{"disambiguationData":[OSD([sQuery(id+"F2.wireOp",EDGE,"E3.3.23.10")])],"isStart":false});
            var Q1299;
            Q1299=makeQuery(id+"F3.opExtrude","CAP_EDGE",EDGE,{"disambiguationData":[OSD([sQuery(id+"F2.wireOp",EDGE,"E2.17.10.1")])],"isStart":false});
            var Q1300;
            Q1300=makeQuery(id+"F3.opExtrude","CAP_EDGE",EDGE,{"disambiguationData":[OSD([sQuery(id+"F2.wireOp",EDGE,"E2.1.10.1")])],"isStart":false});
            var Q1301;
            Q1301=makeQuery(id+"F3.opExtrude","CAP_EDGE",EDGE,{"disambiguationData":[OSD([sQuery(id+"F2.wireOp",EDGE,"E3.3.20.10")])],"isStart":false});
            var Q1302;
            Q1302=makeQuery(id+"F3.opExtrude","CAP_EDGE",EDGE,{"disambiguationData":[OSD([sQuery(id+"F2.wireOp",EDGE,"E3.3.27.10")])],"isStart":false});
            var Q1303;
            Q1303=makeQuery(id+"F3.opExtrude","CAP_EDGE",EDGE,{"disambiguationData":[OSD([sQuery(id+"F2.wireOp",EDGE,"E2.14.10.1")])],"isStart":false});
            var Q1304;
            Q1304=makeQuery(id+"F3.opExtrude","CAP_EDGE",EDGE,{"disambiguationData":[OSD([sQuery(id+"F2.wireOp",EDGE,"E3.3.21.10")])],"isStart":false});
            var Q1305;
            Q1305=makeQuery(id+"F3.opExtrude","CAP_EDGE",EDGE,{"disambiguationData":[OSD([sQuery(id+"F2.wireOp",EDGE,"E2.2.10.1")])],"isStart":false});
            var Q1306;
            Q1306=makeQuery(id+"F3.opExtrude","CAP_EDGE",EDGE,{"disambiguationData":[OSD([sQuery(id+"F2.wireOp",EDGE,"E2.8.10.1")])],"isStart":false});
            var Q1307;
            Q1307=makeQuery(id+"F3.opExtrude","CAP_EDGE",EDGE,{"disambiguationData":[OSD([sQuery(id+"F2.wireOp",EDGE,"E3.3.28.10")])],"isStart":false});
            var Q1308;
            Q1308=makeQuery(id+"F3.opExtrude","CAP_EDGE",EDGE,{"disambiguationData":[OSD([sQuery(id+"F2.wireOp",EDGE,"E2.15.10.1")])],"isStart":false});
            var Q1309;
            Q1309=makeQuery(id+"F3.opExtrude","CAP_EDGE",EDGE,{"disambiguationData":[OSD([sQuery(id+"F2.wireOp",EDGE,"E3.3.24.10")])],"isStart":false});
            var Q1310;
            Q1310=makeQuery(id+"F3.opExtrude","CAP_EDGE",EDGE,{"disambiguationData":[OSD([sQuery(id+"F2.wireOp",EDGE,"E2.11.10.1")])],"isStart":false});
            var Q1311;
            Q1311=makeQuery(id+"F3.opExtrude","CAP_EDGE",EDGE,{"disambiguationData":[OSD([sQuery(id+"F2.wireOp",EDGE,"E2.18.10.1")])],"isStart":false});
            var Q1312;
            Q1312=makeQuery(id+"F3.opExtrude","CAP_EDGE",EDGE,{"disambiguationData":[OSD([sQuery(id+"F2.wireOp",EDGE,"E2.5.10.1")])],"isStart":false});
            var Q1313;
            Q1313=makeQuery(id+"F3.opExtrude","CAP_EDGE",EDGE,{"disambiguationData":[OSD([sQuery(id+"F2.wireOp",EDGE,"E2.12.10.1")])],"isStart":false});
            var Q1314;
            Q1314=makeQuery(id+"F3.opExtrude","CAP_EDGE",EDGE,{"disambiguationData":[OSD([sQuery(id+"F2.wireOp",EDGE,"E2.6.10.1")])],"isStart":false});
            var Q1315;
            Q1315=makeQuery(id+"F3.opExtrude","CAP_EDGE",EDGE,{"disambiguationData":[OSD([sQuery(id+"F2.wireOp",EDGE,"E3.3.25.10")])],"isStart":false});
            var Q1316;
            Q1316=makeQuery(id+"F3.opExtrude","CAP_EDGE",EDGE,{"disambiguationData":[OSD([sQuery(id+"F2.wireOp",EDGE,"E2.19.10.1")])],"isStart":false});
            var Q1317;
            Q1317=makeQuery(id+"F3.opExtrude","CAP_EDGE",EDGE,{"disambiguationData":[OSD([sQuery(id+"F2.wireOp",EDGE,"E2.13.10.1")])],"isStart":false});
            var Q1318;
            Q1318=makeQuery(id+"F3.opExtrude","CAP_EDGE",EDGE,{"disambiguationData":[OSD([sQuery(id+"F2.wireOp",EDGE,"E2.7.10.1")])],"isStart":false});
            var Q1319;
            Q1319=makeQuery(id+"F3.opExtrude","CAP_EDGE",EDGE,{"disambiguationData":[OSD([sQuery(id+"F2.wireOp",EDGE,"E3.3.26.10")])],"isStart":false});
            var Q1320;
            Q1320=makeQuery(id+"F3.opExtrude","CAP_EDGE",EDGE,{"disambiguationData":[OSD([sQuery(id+"F2.wireOp",EDGE,"E2.0.11.0")])],"isStart":false});
            var Q1321;
            Q1321=makeQuery(id+"F3.opExtrude","CAP_EDGE",EDGE,{"disambiguationData":[OSD([sQuery(id+"F2.wireOp",EDGE,"E2.0.11.2")])],"isStart":false});
            var Q1322;
            Q1322=makeQuery(id+"F3.opExtrude","CAP_EDGE",EDGE,{"disambiguationData":[OSD([sQuery(id+"F2.wireOp",EDGE,"E2.9.11.0")])],"isStart":false});
            var Q1323;
            Q1323=makeQuery(id+"F3.opExtrude","CAP_EDGE",EDGE,{"disambiguationData":[OSD([sQuery(id+"F2.wireOp",EDGE,"E2.10.11.0")])],"isStart":false});
            var Q1324;
            Q1324=makeQuery(id+"F3.opExtrude","CAP_EDGE",EDGE,{"disambiguationData":[OSD([sQuery(id+"F2.wireOp",EDGE,"E2.16.11.0")])],"isStart":false});
            var Q1325;
            Q1325=makeQuery(id+"F3.opExtrude","CAP_EDGE",EDGE,{"disambiguationData":[OSD([sQuery(id+"F2.wireOp",EDGE,"E3.0.22.11")])],"isStart":false});
            var Q1326;
            Q1326=makeQuery(id+"F3.opExtrude","CAP_EDGE",EDGE,{"disambiguationData":[OSD([sQuery(id+"F2.wireOp",EDGE,"E2.3.11.0")])],"isStart":false});
            var Q1327;
            Q1327=makeQuery(id+"F3.opExtrude","CAP_EDGE",EDGE,{"disambiguationData":[OSD([sQuery(id+"F2.wireOp",EDGE,"E3.0.29.11")])],"isStart":false});
            var Q1328;
            Q1328=makeQuery(id+"F3.opExtrude","CAP_EDGE",EDGE,{"disambiguationData":[OSD([sQuery(id+"F2.wireOp",EDGE,"E3.0.23.11")])],"isStart":false});
            var Q1329;
            Q1329=makeQuery(id+"F3.opExtrude","CAP_EDGE",EDGE,{"disambiguationData":[OSD([sQuery(id+"F2.wireOp",EDGE,"E2.7.11.0")])],"isStart":false});
            var Q1330;
            Q1330=makeQuery(id+"F3.opExtrude","CAP_EDGE",EDGE,{"disambiguationData":[OSD([sQuery(id+"F2.wireOp",EDGE,"E3.0.26.11")])],"isStart":false});
            var Q1331;
            Q1331=makeQuery(id+"F3.opExtrude","CAP_EDGE",EDGE,{"disambiguationData":[OSD([sQuery(id+"F2.wireOp",EDGE,"E2.1.11.0")])],"isStart":false});
            var Q1332;
            Q1332=makeQuery(id+"F3.opExtrude","CAP_EDGE",EDGE,{"disambiguationData":[OSD([sQuery(id+"F2.wireOp",EDGE,"E3.0.20.11")])],"isStart":false});
            var Q1333;
            Q1333=makeQuery(id+"F3.opExtrude","CAP_EDGE",EDGE,{"disambiguationData":[OSD([sQuery(id+"F2.wireOp",EDGE,"E3.0.27.11")])],"isStart":false});
            var Q1334;
            Q1334=makeQuery(id+"F3.opExtrude","CAP_EDGE",EDGE,{"disambiguationData":[OSD([sQuery(id+"F2.wireOp",EDGE,"E2.14.11.0")])],"isStart":false});
            var Q1335;
            Q1335=makeQuery(id+"F3.opExtrude","CAP_EDGE",EDGE,{"disambiguationData":[OSD([sQuery(id+"F2.wireOp",EDGE,"E3.0.21.11")])],"isStart":false});
            var Q1336;
            Q1336=makeQuery(id+"F3.opExtrude","CAP_EDGE",EDGE,{"disambiguationData":[OSD([sQuery(id+"F2.wireOp",EDGE,"E2.8.11.0")])],"isStart":false});
            var Q1337;
            Q1337=makeQuery(id+"F3.opExtrude","CAP_EDGE",EDGE,{"disambiguationData":[OSD([sQuery(id+"F2.wireOp",EDGE,"E2.15.11.0")])],"isStart":false});
            var Q1338;
            Q1338=makeQuery(id+"F3.opExtrude","CAP_EDGE",EDGE,{"disambiguationData":[OSD([sQuery(id+"F2.wireOp",EDGE,"E2.2.11.0")])],"isStart":false});
            var Q1339;
            Q1339=makeQuery(id+"F3.opExtrude","CAP_EDGE",EDGE,{"disambiguationData":[OSD([sQuery(id+"F2.wireOp",EDGE,"E3.0.28.11")])],"isStart":false});
            var Q1340;
            Q1340=makeQuery(id+"F3.opExtrude","CAP_EDGE",EDGE,{"disambiguationData":[OSD([sQuery(id+"F2.wireOp",EDGE,"E2.17.11.0")])],"isStart":false});
            var Q1341;
            Q1341=makeQuery(id+"F3.opExtrude","CAP_EDGE",EDGE,{"disambiguationData":[OSD([sQuery(id+"F2.wireOp",EDGE,"E2.4.11.0")])],"isStart":false});
            var Q1342;
            Q1342=makeQuery(id+"F3.opExtrude","CAP_EDGE",EDGE,{"disambiguationData":[OSD([sQuery(id+"F2.wireOp",EDGE,"E2.11.11.0")])],"isStart":false});
            var Q1343;
            Q1343=makeQuery(id+"F3.opExtrude","CAP_EDGE",EDGE,{"disambiguationData":[OSD([sQuery(id+"F2.wireOp",EDGE,"E2.5.11.0")])],"isStart":false});
            var Q1344;
            Q1344=makeQuery(id+"F3.opExtrude","CAP_EDGE",EDGE,{"disambiguationData":[OSD([sQuery(id+"F2.wireOp",EDGE,"E3.0.24.11")])],"isStart":false});
            var Q1345;
            Q1345=makeQuery(id+"F3.opExtrude","CAP_EDGE",EDGE,{"disambiguationData":[OSD([sQuery(id+"F2.wireOp",EDGE,"E2.12.11.0")])],"isStart":false});
            var Q1346;
            Q1346=makeQuery(id+"F3.opExtrude","CAP_EDGE",EDGE,{"disambiguationData":[OSD([sQuery(id+"F2.wireOp",EDGE,"E2.18.11.0")])],"isStart":false});
            var Q1347;
            Q1347=makeQuery(id+"F3.opExtrude","CAP_EDGE",EDGE,{"disambiguationData":[OSD([sQuery(id+"F2.wireOp",EDGE,"E2.6.11.0")])],"isStart":false});
            var Q1348;
            Q1348=makeQuery(id+"F3.opExtrude","CAP_EDGE",EDGE,{"disambiguationData":[OSD([sQuery(id+"F2.wireOp",EDGE,"E3.0.25.11")])],"isStart":false});
            var Q1349;
            Q1349=makeQuery(id+"F3.opExtrude","CAP_EDGE",EDGE,{"disambiguationData":[OSD([sQuery(id+"F2.wireOp",EDGE,"E2.19.11.0")])],"isStart":false});
            var Q1350;
            Q1350=makeQuery(id+"F3.opExtrude","CAP_EDGE",EDGE,{"disambiguationData":[OSD([sQuery(id+"F2.wireOp",EDGE,"E2.13.11.0")])],"isStart":false});
            var Q1351;
            Q1351=makeQuery(id+"F3.opExtrude","CAP_EDGE",EDGE,{"disambiguationData":[OSD([sQuery(id+"F2.wireOp",EDGE,"E2.18.11.2")])],"isStart":false});
            var Q1352;
            Q1352=makeQuery(id+"F3.opExtrude","CAP_EDGE",EDGE,{"disambiguationData":[OSD([sQuery(id+"F2.wireOp",EDGE,"E3.6.25.11")])],"isStart":false});
            var Q1353;
            Q1353=makeQuery(id+"F3.opExtrude","CAP_EDGE",EDGE,{"disambiguationData":[OSD([sQuery(id+"F2.wireOp",EDGE,"E2.6.11.2")])],"isStart":false});
            var Q1354;
            Q1354=makeQuery(id+"F3.opExtrude","CAP_EDGE",EDGE,{"disambiguationData":[OSD([sQuery(id+"F2.wireOp",EDGE,"E2.12.11.2")])],"isStart":false});
            var Q1355;
            Q1355=makeQuery(id+"F3.opExtrude","CAP_EDGE",EDGE,{"disambiguationData":[OSD([sQuery(id+"F2.wireOp",EDGE,"E2.19.11.2")])],"isStart":false});
            var Q1356;
            Q1356=makeQuery(id+"F3.opExtrude","CAP_EDGE",EDGE,{"disambiguationData":[OSD([sQuery(id+"F2.wireOp",EDGE,"E2.13.11.2")])],"isStart":false});
            var Q1357;
            Q1357=makeQuery(id+"F3.opExtrude","CAP_EDGE",EDGE,{"disambiguationData":[OSD([sQuery(id+"F2.wireOp",EDGE,"E2.7.11.2")])],"isStart":false});
            var Q1358;
            Q1358=makeQuery(id+"F3.opExtrude","CAP_EDGE",EDGE,{"disambiguationData":[OSD([sQuery(id+"F2.wireOp",EDGE,"E3.6.26.11")])],"isStart":false});
            var Q1359;
            Q1359=makeQuery(id+"F3.opExtrude","CAP_EDGE",EDGE,{"disambiguationData":[OSD([sQuery(id+"F2.wireOp",EDGE,"E2.1.11.2")])],"isStart":false});
            var Q1360;
            Q1360=makeQuery(id+"F3.opExtrude","CAP_EDGE",EDGE,{"disambiguationData":[OSD([sQuery(id+"F2.wireOp",EDGE,"E3.6.20.11")])],"isStart":false});
            var Q1361;
            Q1361=makeQuery(id+"F3.opExtrude","CAP_EDGE",EDGE,{"disambiguationData":[OSD([sQuery(id+"F2.wireOp",EDGE,"E3.6.27.11")])],"isStart":false});
            var Q1362;
            Q1362=makeQuery(id+"F3.opExtrude","CAP_EDGE",EDGE,{"disambiguationData":[OSD([sQuery(id+"F2.wireOp",EDGE,"E2.14.11.2")])],"isStart":false});
            var Q1363;
            Q1363=makeQuery(id+"F3.opExtrude","CAP_EDGE",EDGE,{"disambiguationData":[OSD([sQuery(id+"F2.wireOp",EDGE,"E2.9.11.2")])],"isStart":false});
            var Q1364;
            Q1364=makeQuery(id+"F3.opExtrude","CAP_EDGE",EDGE,{"disambiguationData":[OSD([sQuery(id+"F2.wireOp",EDGE,"E2.10.11.2")])],"isStart":false});
            var Q1365;
            Q1365=makeQuery(id+"F3.opExtrude","CAP_EDGE",EDGE,{"disambiguationData":[OSD([sQuery(id+"F2.wireOp",EDGE,"E2.3.11.2")])],"isStart":false});
            var Q1366;
            Q1366=makeQuery(id+"F3.opExtrude","CAP_EDGE",EDGE,{"disambiguationData":[OSD([sQuery(id+"F2.wireOp",EDGE,"E3.6.22.11")])],"isStart":false});
            var Q1367;
            Q1367=makeQuery(id+"F3.opExtrude","CAP_EDGE",EDGE,{"disambiguationData":[OSD([sQuery(id+"F2.wireOp",EDGE,"E3.6.29.11")])],"isStart":false});
            var Q1368;
            Q1368=makeQuery(id+"F3.opExtrude","CAP_EDGE",EDGE,{"disambiguationData":[OSD([sQuery(id+"F2.wireOp",EDGE,"E2.16.11.2")])],"isStart":false});
            var Q1369;
            Q1369=makeQuery(id+"F3.opExtrude","CAP_EDGE",EDGE,{"disambiguationData":[OSD([sQuery(id+"F2.wireOp",EDGE,"E2.0.11.1")])],"isStart":false});
            var Q1370;
            Q1370=makeQuery(id+"F3.opExtrude","CAP_EDGE",EDGE,{"disambiguationData":[OSD([sQuery(id+"F2.wireOp",EDGE,"E3.6.23.11")])],"isStart":false});
            var Q1371;
            Q1371=makeQuery(id+"F3.opExtrude","CAP_EDGE",EDGE,{"disambiguationData":[OSD([sQuery(id+"F2.wireOp",EDGE,"E2.17.11.2")])],"isStart":false});
            var Q1372;
            Q1372=makeQuery(id+"F3.opExtrude","CAP_EDGE",EDGE,{"disambiguationData":[OSD([sQuery(id+"F2.wireOp",EDGE,"E2.4.11.2")])],"isStart":false});
            var Q1373;
            Q1373=makeQuery(id+"F3.opExtrude","CAP_EDGE",EDGE,{"disambiguationData":[OSD([sQuery(id+"F2.wireOp",EDGE,"E2.11.11.2")])],"isStart":false});
            var Q1374;
            Q1374=makeQuery(id+"F3.opExtrude","CAP_EDGE",EDGE,{"disambiguationData":[OSD([sQuery(id+"F2.wireOp",EDGE,"E2.5.11.2")])],"isStart":false});
            var Q1375;
            Q1375=makeQuery(id+"F3.opExtrude","CAP_EDGE",EDGE,{"disambiguationData":[OSD([sQuery(id+"F2.wireOp",EDGE,"E3.6.24.11")])],"isStart":false});
            var Q1376;
            Q1376=makeQuery(id+"F3.opExtrude","CAP_EDGE",EDGE,{"disambiguationData":[OSD([sQuery(id+"F2.wireOp",EDGE,"E3.6.21.11")])],"isStart":false});
            var Q1377;
            Q1377=makeQuery(id+"F3.opExtrude","CAP_EDGE",EDGE,{"disambiguationData":[OSD([sQuery(id+"F2.wireOp",EDGE,"E2.8.11.2")])],"isStart":false});
            var Q1378;
            Q1378=makeQuery(id+"F3.opExtrude","CAP_EDGE",EDGE,{"disambiguationData":[OSD([sQuery(id+"F2.wireOp",EDGE,"E2.15.11.2")])],"isStart":false});
            var Q1379;
            Q1379=makeQuery(id+"F3.opExtrude","CAP_EDGE",EDGE,{"disambiguationData":[OSD([sQuery(id+"F2.wireOp",EDGE,"E2.2.11.2")])],"isStart":false});
            var Q1380;
            Q1380=makeQuery(id+"F3.opExtrude","CAP_EDGE",EDGE,{"disambiguationData":[OSD([sQuery(id+"F2.wireOp",EDGE,"E3.6.28.11")])],"isStart":false});
            var Q1381;
            Q1381=makeQuery(id+"F3.opExtrude","CAP_EDGE",EDGE,{"disambiguationData":[OSD([sQuery(id+"F2.wireOp",EDGE,"E2.0.11.3")])],"isStart":false});
            var Q1382;
            Q1382=makeQuery(id+"F3.opExtrude","CAP_EDGE",EDGE,{"disambiguationData":[OSD([sQuery(id+"F2.wireOp",EDGE,"E2.3.11.1")])],"isStart":false});
            var Q1383;
            Q1383=makeQuery(id+"F3.opExtrude","CAP_EDGE",EDGE,{"disambiguationData":[OSD([sQuery(id+"F2.wireOp",EDGE,"E3.3.22.11")])],"isStart":false});
            var Q1384;
            Q1384=makeQuery(id+"F3.opExtrude","CAP_EDGE",EDGE,{"disambiguationData":[OSD([sQuery(id+"F2.wireOp",EDGE,"E3.3.29.11")])],"isStart":false});
            var Q1385;
            Q1385=makeQuery(id+"F3.opExtrude","CAP_EDGE",EDGE,{"disambiguationData":[OSD([sQuery(id+"F2.wireOp",EDGE,"E2.16.11.1")])],"isStart":false});
            var Q1386;
            Q1386=makeQuery(id+"F3.opExtrude","CAP_EDGE",EDGE,{"disambiguationData":[OSD([sQuery(id+"F2.wireOp",EDGE,"E3.3.23.11")])],"isStart":false});
            var Q1387;
            Q1387=makeQuery(id+"F3.opExtrude","CAP_EDGE",EDGE,{"disambiguationData":[OSD([sQuery(id+"F2.wireOp",EDGE,"E2.17.11.1")])],"isStart":false});
            var Q1388;
            Q1388=makeQuery(id+"F3.opExtrude","CAP_EDGE",EDGE,{"disambiguationData":[OSD([sQuery(id+"F2.wireOp",EDGE,"E2.4.11.1")])],"isStart":false});
            var Q1389;
            Q1389=makeQuery(id+"F3.opExtrude","CAP_EDGE",EDGE,{"disambiguationData":[OSD([sQuery(id+"F2.wireOp",EDGE,"E2.11.11.1")])],"isStart":false});
            var Q1390;
            Q1390=makeQuery(id+"F3.opExtrude","CAP_EDGE",EDGE,{"disambiguationData":[OSD([sQuery(id+"F2.wireOp",EDGE,"E2.5.11.1")])],"isStart":false});
            var Q1391;
            Q1391=makeQuery(id+"F3.opExtrude","CAP_EDGE",EDGE,{"disambiguationData":[OSD([sQuery(id+"F2.wireOp",EDGE,"E3.3.24.11")])],"isStart":false});
            var Q1392;
            Q1392=makeQuery(id+"F3.opExtrude","CAP_EDGE",EDGE,{"disambiguationData":[OSD([sQuery(id+"F2.wireOp",EDGE,"E2.18.11.1")])],"isStart":false});
            var Q1393;
            Q1393=makeQuery(id+"F3.opExtrude","CAP_EDGE",EDGE,{"disambiguationData":[OSD([sQuery(id+"F2.wireOp",EDGE,"E2.9.11.1")])],"isStart":false});
            var Q1394;
            Q1394=makeQuery(id+"F3.opExtrude","CAP_EDGE",EDGE,{"disambiguationData":[OSD([sQuery(id+"F2.wireOp",EDGE,"E2.10.11.1")])],"isStart":false});
            var Q1395;
            Q1395=makeQuery(id+"F3.opExtrude","CAP_EDGE",EDGE,{"disambiguationData":[OSD([sQuery(id+"F2.wireOp",EDGE,"E2.15.11.1")])],"isStart":false});
            var Q1396;
            Q1396=makeQuery(id+"F3.opExtrude","CAP_EDGE",EDGE,{"disambiguationData":[OSD([sQuery(id+"F2.wireOp",EDGE,"E2.2.11.1")])],"isStart":false});
            var Q1397;
            Q1397=makeQuery(id+"F3.opExtrude","CAP_EDGE",EDGE,{"disambiguationData":[OSD([sQuery(id+"F2.wireOp",EDGE,"E3.3.28.11")])],"isStart":false});
            var Q1398;
            Q1398=makeQuery(id+"F3.opExtrude","CAP_EDGE",EDGE,{"disambiguationData":[OSD([sQuery(id+"F2.wireOp",EDGE,"E3.3.25.11")])],"isStart":false});
            var Q1399;
            Q1399=makeQuery(id+"F3.opExtrude","CAP_EDGE",EDGE,{"disambiguationData":[OSD([sQuery(id+"F2.wireOp",EDGE,"E2.12.11.1")])],"isStart":false});
            var Q1400;
            Q1400=makeQuery(id+"F3.opExtrude","CAP_EDGE",EDGE,{"disambiguationData":[OSD([sQuery(id+"F2.wireOp",EDGE,"E2.19.11.1")])],"isStart":false});
            var Q1401;
            Q1401=makeQuery(id+"F3.opExtrude","CAP_EDGE",EDGE,{"disambiguationData":[OSD([sQuery(id+"F2.wireOp",EDGE,"E2.6.11.1")])],"isStart":false});
            var Q1402;
            Q1402=makeQuery(id+"F3.opExtrude","CAP_EDGE",EDGE,{"disambiguationData":[OSD([sQuery(id+"F2.wireOp",EDGE,"E2.13.11.1")])],"isStart":false});
            var Q1403;
            Q1403=makeQuery(id+"F3.opExtrude","CAP_EDGE",EDGE,{"disambiguationData":[OSD([sQuery(id+"F2.wireOp",EDGE,"E2.7.11.1")])],"isStart":false});
            var Q1404;
            Q1404=makeQuery(id+"F3.opExtrude","CAP_EDGE",EDGE,{"disambiguationData":[OSD([sQuery(id+"F2.wireOp",EDGE,"E3.3.26.11")])],"isStart":false});
            var Q1405;
            Q1405=makeQuery(id+"F3.opExtrude","CAP_EDGE",EDGE,{"disambiguationData":[OSD([sQuery(id+"F2.wireOp",EDGE,"E2.1.11.1")])],"isStart":false});
            var Q1406;
            Q1406=makeQuery(id+"F3.opExtrude","CAP_EDGE",EDGE,{"disambiguationData":[OSD([sQuery(id+"F2.wireOp",EDGE,"E3.3.20.11")])],"isStart":false});
            var Q1407;
            Q1407=makeQuery(id+"F3.opExtrude","CAP_EDGE",EDGE,{"disambiguationData":[OSD([sQuery(id+"F2.wireOp",EDGE,"E3.3.27.11")])],"isStart":false});
            var Q1408;
            Q1408=makeQuery(id+"F3.opExtrude","CAP_EDGE",EDGE,{"disambiguationData":[OSD([sQuery(id+"F2.wireOp",EDGE,"E2.14.11.1")])],"isStart":false});
            var Q1409;
            Q1409=makeQuery(id+"F3.opExtrude","CAP_EDGE",EDGE,{"disambiguationData":[OSD([sQuery(id+"F2.wireOp",EDGE,"E3.3.21.11")])],"isStart":false});
            var Q1410;
            Q1410=makeQuery(id+"F3.opExtrude","CAP_EDGE",EDGE,{"disambiguationData":[OSD([sQuery(id+"F2.wireOp",EDGE,"E2.8.11.1")])],"isStart":false});
            var Q1411;
            Q1411=makeQuery(id+"F3.opExtrude","CAP_EDGE",EDGE,{"disambiguationData":[OSD([sQuery(id+"F2.wireOp",EDGE,"E2.9.11.3")])],"isStart":false});
            var Q1412;
            Q1412=makeQuery(id+"F3.opExtrude","CAP_EDGE",EDGE,{"disambiguationData":[OSD([sQuery(id+"F2.wireOp",EDGE,"E2.10.11.3")])],"isStart":false});
            var Q1413;
            Q1413=makeQuery(id+"F3.opExtrude","CAP_EDGE",EDGE,{"disambiguationData":[OSD([sQuery(id+"F2.wireOp",EDGE,"E2.3.11.3")])],"isStart":false});
            var Q1414;
            Q1414=makeQuery(id+"F3.opExtrude","CAP_EDGE",EDGE,{"disambiguationData":[OSD([sQuery(id+"F2.wireOp",EDGE,"E3.9.22.11")])],"isStart":false});
            var Q1415;
            Q1415=makeQuery(id+"F3.opExtrude","CAP_EDGE",EDGE,{"disambiguationData":[OSD([sQuery(id+"F2.wireOp",EDGE,"E3.9.29.11")])],"isStart":false});
            var Q1416;
            Q1416=makeQuery(id+"F3.opExtrude","CAP_EDGE",EDGE,{"disambiguationData":[OSD([sQuery(id+"F2.wireOp",EDGE,"E2.16.11.3")])],"isStart":false});
            var Q1417;
            Q1417=makeQuery(id+"F3.opExtrude","CAP_EDGE",EDGE,{"disambiguationData":[OSD([sQuery(id+"F2.wireOp",EDGE,"E2.13.11.3")])],"isStart":false});
            var Q1418;
            Q1418=makeQuery(id+"F3.opExtrude","CAP_EDGE",EDGE,{"disambiguationData":[OSD([sQuery(id+"F2.wireOp",EDGE,"E2.7.11.3")])],"isStart":false});
            var Q1419;
            Q1419=makeQuery(id+"F3.opExtrude","CAP_EDGE",EDGE,{"disambiguationData":[OSD([sQuery(id+"F2.wireOp",EDGE,"E3.9.26.11")])],"isStart":false});
            var Q1420;
            Q1420=makeQuery(id+"F3.opExtrude","CAP_EDGE",EDGE,{"disambiguationData":[OSD([sQuery(id+"F2.wireOp",EDGE,"E2.1.11.3")])],"isStart":false});
            var Q1421;
            Q1421=makeQuery(id+"F3.opExtrude","CAP_EDGE",EDGE,{"disambiguationData":[OSD([sQuery(id+"F2.wireOp",EDGE,"E3.9.20.11")])],"isStart":false});
            var Q1422;
            Q1422=makeQuery(id+"F3.opExtrude","CAP_EDGE",EDGE,{"disambiguationData":[OSD([sQuery(id+"F2.wireOp",EDGE,"E3.9.27.11")])],"isStart":false});
            var Q1423;
            Q1423=makeQuery(id+"F3.opExtrude","CAP_EDGE",EDGE,{"disambiguationData":[OSD([sQuery(id+"F2.wireOp",EDGE,"E2.14.11.3")])],"isStart":false});
            var Q1424;
            Q1424=makeQuery(id+"F3.opExtrude","CAP_EDGE",EDGE,{"disambiguationData":[OSD([sQuery(id+"F2.wireOp",EDGE,"E3.9.21.11")])],"isStart":false});
            var Q1425;
            Q1425=makeQuery(id+"F3.opExtrude","CAP_EDGE",EDGE,{"disambiguationData":[OSD([sQuery(id+"F2.wireOp",EDGE,"E2.8.11.3")])],"isStart":false});
            var Q1426;
            Q1426=makeQuery(id+"F3.opExtrude","CAP_EDGE",EDGE,{"disambiguationData":[OSD([sQuery(id+"F2.wireOp",EDGE,"E2.15.11.3")])],"isStart":false});
            var Q1427;
            Q1427=makeQuery(id+"F3.opExtrude","CAP_EDGE",EDGE,{"disambiguationData":[OSD([sQuery(id+"F2.wireOp",EDGE,"E2.2.11.3")])],"isStart":false});
            var Q1428;
            Q1428=makeQuery(id+"F3.opExtrude","CAP_EDGE",EDGE,{"disambiguationData":[OSD([sQuery(id+"F2.wireOp",EDGE,"E3.9.28.11")])],"isStart":false});
            var Q1429;
            Q1429=makeQuery(id+"F3.opExtrude","CAP_EDGE",EDGE,{"disambiguationData":[OSD([sQuery(id+"F2.wireOp",EDGE,"E3.9.23.11")])],"isStart":false});
            var Q1430;
            Q1430=makeQuery(id+"F3.opExtrude","CAP_EDGE",EDGE,{"disambiguationData":[OSD([sQuery(id+"F2.wireOp",EDGE,"E2.17.11.3")])],"isStart":false});
            var Q1431;
            Q1431=makeQuery(id+"F3.opExtrude","CAP_EDGE",EDGE,{"disambiguationData":[OSD([sQuery(id+"F2.wireOp",EDGE,"E2.4.11.3")])],"isStart":false});
            var Q1432;
            Q1432=makeQuery(id+"F3.opExtrude","CAP_EDGE",EDGE,{"disambiguationData":[OSD([sQuery(id+"F2.wireOp",EDGE,"E2.11.11.3")])],"isStart":false});
            var Q1433;
            Q1433=makeQuery(id+"F3.opExtrude","CAP_EDGE",EDGE,{"disambiguationData":[OSD([sQuery(id+"F2.wireOp",EDGE,"E2.5.11.3")])],"isStart":false});
            var Q1434;
            Q1434=makeQuery(id+"F3.opExtrude","CAP_EDGE",EDGE,{"disambiguationData":[OSD([sQuery(id+"F2.wireOp",EDGE,"E3.9.24.11")])],"isStart":false});
            var Q1435;
            Q1435=makeQuery(id+"F3.opExtrude","CAP_EDGE",EDGE,{"disambiguationData":[OSD([sQuery(id+"F2.wireOp",EDGE,"E2.18.11.3")])],"isStart":false});
            var Q1436;
            Q1436=makeQuery(id+"F3.opExtrude","CAP_EDGE",EDGE,{"disambiguationData":[OSD([sQuery(id+"F2.wireOp",EDGE,"E3.9.25.11")])],"isStart":false});
            var Q1437;
            Q1437=makeQuery(id+"F3.opExtrude","CAP_EDGE",EDGE,{"disambiguationData":[OSD([sQuery(id+"F2.wireOp",EDGE,"E2.12.11.3")])],"isStart":false});
            var Q1438;
            Q1438=makeQuery(id+"F3.opExtrude","CAP_EDGE",EDGE,{"disambiguationData":[OSD([sQuery(id+"F2.wireOp",EDGE,"E2.19.11.3")])],"isStart":false});
            var Q1439;
            Q1439=makeQuery(id+"F3.opExtrude","CAP_EDGE",EDGE,{"disambiguationData":[OSD([sQuery(id+"F2.wireOp",EDGE,"E2.6.11.3")])],"isStart":false});
            var Q1440;
            Q1440=makeQuery(id+"F3.opExtrude","CAP_EDGE",EDGE,{"disambiguationData":[OSD([sQuery(id+"F2.wireOp",EDGE,"E2.0.12.3")])],"isStart":false});
            var Q1441;
            Q1441=makeQuery(id+"F3.opExtrude","CAP_EDGE",EDGE,{"disambiguationData":[OSD([sQuery(id+"F2.wireOp",EDGE,"E2.0.12.0")])],"isStart":false});
            var Q1442;
            Q1442=makeQuery(id+"F3.opExtrude","CAP_EDGE",EDGE,{"disambiguationData":[OSD([sQuery(id+"F2.wireOp",EDGE,"E2.0.12.2")])],"isStart":false});
            var Q1443;
            Q1443=makeQuery(id+"F3.opExtrude","CAP_EDGE",EDGE,{"disambiguationData":[OSD([sQuery(id+"F2.wireOp",EDGE,"E3.9.29.12")])],"isStart":false});
            var Q1444;
            Q1444=makeQuery(id+"F3.opExtrude","CAP_EDGE",EDGE,{"disambiguationData":[OSD([sQuery(id+"F2.wireOp",EDGE,"E2.9.12.3")])],"isStart":false});
            var Q1445;
            Q1445=makeQuery(id+"F3.opExtrude","CAP_EDGE",EDGE,{"disambiguationData":[OSD([sQuery(id+"F2.wireOp",EDGE,"E3.9.28.12")])],"isStart":false});
            var Q1446;
            Q1446=makeQuery(id+"F3.opExtrude","CAP_EDGE",EDGE,{"disambiguationData":[OSD([sQuery(id+"F2.wireOp",EDGE,"E3.9.25.12")])],"isStart":false});
            var Q1447;
            Q1447=makeQuery(id+"F3.opExtrude","CAP_EDGE",EDGE,{"disambiguationData":[OSD([sQuery(id+"F2.wireOp",EDGE,"E2.12.12.3")])],"isStart":false});
            var Q1448;
            Q1448=makeQuery(id+"F3.opExtrude","CAP_EDGE",EDGE,{"disambiguationData":[OSD([sQuery(id+"F2.wireOp",EDGE,"E2.6.12.3")])],"isStart":false});
            var Q1449;
            Q1449=makeQuery(id+"F3.opExtrude","CAP_EDGE",EDGE,{"disambiguationData":[OSD([sQuery(id+"F2.wireOp",EDGE,"E2.19.12.3")])],"isStart":false});
            var Q1450;
            Q1450=makeQuery(id+"F3.opExtrude","CAP_EDGE",EDGE,{"disambiguationData":[OSD([sQuery(id+"F2.wireOp",EDGE,"E3.9.26.12")])],"isStart":false});
            var Q1451;
            Q1451=makeQuery(id+"F3.opExtrude","CAP_EDGE",EDGE,{"disambiguationData":[OSD([sQuery(id+"F2.wireOp",EDGE,"E2.13.12.3")])],"isStart":false});
            var Q1452;
            Q1452=makeQuery(id+"F3.opExtrude","CAP_EDGE",EDGE,{"disambiguationData":[OSD([sQuery(id+"F2.wireOp",EDGE,"E3.9.20.12")])],"isStart":false});
            var Q1453;
            Q1453=makeQuery(id+"F3.opExtrude","CAP_EDGE",EDGE,{"disambiguationData":[OSD([sQuery(id+"F2.wireOp",EDGE,"E2.1.12.3")])],"isStart":false});
            var Q1454;
            Q1454=makeQuery(id+"F3.opExtrude","CAP_EDGE",EDGE,{"disambiguationData":[OSD([sQuery(id+"F2.wireOp",EDGE,"E2.7.12.3")])],"isStart":false});
            var Q1455;
            Q1455=makeQuery(id+"F3.opExtrude","CAP_EDGE",EDGE,{"disambiguationData":[OSD([sQuery(id+"F2.wireOp",EDGE,"E3.9.27.12")])],"isStart":false});
            var Q1456;
            Q1456=makeQuery(id+"F3.opExtrude","CAP_EDGE",EDGE,{"disambiguationData":[OSD([sQuery(id+"F2.wireOp",EDGE,"E2.14.12.3")])],"isStart":false});
            var Q1457;
            Q1457=makeQuery(id+"F3.opExtrude","CAP_EDGE",EDGE,{"disambiguationData":[OSD([sQuery(id+"F2.wireOp",EDGE,"E3.9.21.12")])],"isStart":false});
            var Q1458;
            Q1458=makeQuery(id+"F3.opExtrude","CAP_EDGE",EDGE,{"disambiguationData":[OSD([sQuery(id+"F2.wireOp",EDGE,"E2.8.12.3")])],"isStart":false});
            var Q1459;
            Q1459=makeQuery(id+"F3.opExtrude","CAP_EDGE",EDGE,{"disambiguationData":[OSD([sQuery(id+"F2.wireOp",EDGE,"E2.3.12.3")])],"isStart":false});
            var Q1460;
            Q1460=makeQuery(id+"F3.opExtrude","CAP_EDGE",EDGE,{"disambiguationData":[OSD([sQuery(id+"F2.wireOp",EDGE,"E3.9.22.12")])],"isStart":false});
            var Q1461;
            Q1461=makeQuery(id+"F3.opExtrude","CAP_EDGE",EDGE,{"disambiguationData":[OSD([sQuery(id+"F2.wireOp",EDGE,"E2.16.12.3")])],"isStart":false});
            var Q1462;
            Q1462=makeQuery(id+"F3.opExtrude","CAP_EDGE",EDGE,{"disambiguationData":[OSD([sQuery(id+"F2.wireOp",EDGE,"E3.9.23.12")])],"isStart":false});
            var Q1463;
            Q1463=makeQuery(id+"F3.opExtrude","CAP_EDGE",EDGE,{"disambiguationData":[OSD([sQuery(id+"F2.wireOp",EDGE,"E2.10.12.3")])],"isStart":false});
            var Q1464;
            Q1464=makeQuery(id+"F3.opExtrude","CAP_EDGE",EDGE,{"disambiguationData":[OSD([sQuery(id+"F2.wireOp",EDGE,"E2.17.12.3")])],"isStart":false});
            var Q1465;
            Q1465=makeQuery(id+"F3.opExtrude","CAP_EDGE",EDGE,{"disambiguationData":[OSD([sQuery(id+"F2.wireOp",EDGE,"E2.4.12.3")])],"isStart":false});
            var Q1466;
            Q1466=makeQuery(id+"F3.opExtrude","CAP_EDGE",EDGE,{"disambiguationData":[OSD([sQuery(id+"F2.wireOp",EDGE,"E2.11.12.3")])],"isStart":false});
            var Q1467;
            Q1467=makeQuery(id+"F3.opExtrude","CAP_EDGE",EDGE,{"disambiguationData":[OSD([sQuery(id+"F2.wireOp",EDGE,"E2.5.12.3")])],"isStart":false});
            var Q1468;
            Q1468=makeQuery(id+"F3.opExtrude","CAP_EDGE",EDGE,{"disambiguationData":[OSD([sQuery(id+"F2.wireOp",EDGE,"E3.9.24.12")])],"isStart":false});
            var Q1469;
            Q1469=makeQuery(id+"F3.opExtrude","CAP_EDGE",EDGE,{"disambiguationData":[OSD([sQuery(id+"F2.wireOp",EDGE,"E2.18.12.3")])],"isStart":false});
            var Q1470;
            Q1470=makeQuery(id+"F3.opExtrude","CAP_EDGE",EDGE,{"disambiguationData":[OSD([sQuery(id+"F2.wireOp",EDGE,"E3.0.29.12")])],"isStart":false});
            var Q1471;
            Q1471=makeQuery(id+"F3.opExtrude","CAP_EDGE",EDGE,{"disambiguationData":[OSD([sQuery(id+"F2.wireOp",EDGE,"E3.0.28.12")])],"isStart":false});
            var Q1472;
            Q1472=makeQuery(id+"F3.opExtrude","CAP_EDGE",EDGE,{"disambiguationData":[OSD([sQuery(id+"F2.wireOp",EDGE,"E3.0.22.12")])],"isStart":false});
            var Q1473;
            Q1473=makeQuery(id+"F3.opExtrude","CAP_EDGE",EDGE,{"disambiguationData":[OSD([sQuery(id+"F2.wireOp",EDGE,"E2.9.12.0")])],"isStart":false});
            var Q1474;
            Q1474=makeQuery(id+"F3.opExtrude","CAP_EDGE",EDGE,{"disambiguationData":[OSD([sQuery(id+"F2.wireOp",EDGE,"E2.16.12.0")])],"isStart":false});
            var Q1475;
            Q1475=makeQuery(id+"F3.opExtrude","CAP_EDGE",EDGE,{"disambiguationData":[OSD([sQuery(id+"F2.wireOp",EDGE,"E2.3.12.0")])],"isStart":false});
            var Q1476;
            Q1476=makeQuery(id+"F3.opExtrude","CAP_EDGE",EDGE,{"disambiguationData":[OSD([sQuery(id+"F2.wireOp",EDGE,"E2.15.12.3")])],"isStart":false});
            var Q1477;
            Q1477=makeQuery(id+"F3.opExtrude","CAP_EDGE",EDGE,{"disambiguationData":[OSD([sQuery(id+"F2.wireOp",EDGE,"E2.2.12.3")])],"isStart":false});
            var Q1478;
            Q1478=makeQuery(id+"F3.opExtrude","CAP_EDGE",EDGE,{"disambiguationData":[OSD([sQuery(id+"F2.wireOp",EDGE,"E2.19.12.0")])],"isStart":false});
            var Q1479;
            Q1479=makeQuery(id+"F3.opExtrude","CAP_EDGE",EDGE,{"disambiguationData":[OSD([sQuery(id+"F2.wireOp",EDGE,"E2.13.12.0")])],"isStart":false});
            var Q1480;
            Q1480=makeQuery(id+"F3.opExtrude","CAP_EDGE",EDGE,{"disambiguationData":[OSD([sQuery(id+"F2.wireOp",EDGE,"E2.7.12.0")])],"isStart":false});
            var Q1481;
            Q1481=makeQuery(id+"F3.opExtrude","CAP_EDGE",EDGE,{"disambiguationData":[OSD([sQuery(id+"F2.wireOp",EDGE,"E3.0.26.12")])],"isStart":false});
            var Q1482;
            Q1482=makeQuery(id+"F3.opExtrude","CAP_EDGE",EDGE,{"disambiguationData":[OSD([sQuery(id+"F2.wireOp",EDGE,"E2.1.12.0")])],"isStart":false});
            var Q1483;
            Q1483=makeQuery(id+"F3.opExtrude","CAP_EDGE",EDGE,{"disambiguationData":[OSD([sQuery(id+"F2.wireOp",EDGE,"E3.0.20.12")])],"isStart":false});
            var Q1484;
            Q1484=makeQuery(id+"F3.opExtrude","CAP_EDGE",EDGE,{"disambiguationData":[OSD([sQuery(id+"F2.wireOp",EDGE,"E3.0.27.12")])],"isStart":false});
            var Q1485;
            Q1485=makeQuery(id+"F3.opExtrude","CAP_EDGE",EDGE,{"disambiguationData":[OSD([sQuery(id+"F2.wireOp",EDGE,"E2.14.12.0")])],"isStart":false});
            var Q1486;
            Q1486=makeQuery(id+"F3.opExtrude","CAP_EDGE",EDGE,{"disambiguationData":[OSD([sQuery(id+"F2.wireOp",EDGE,"E3.0.21.12")])],"isStart":false});
            var Q1487;
            Q1487=makeQuery(id+"F3.opExtrude","CAP_EDGE",EDGE,{"disambiguationData":[OSD([sQuery(id+"F2.wireOp",EDGE,"E2.8.12.0")])],"isStart":false});
            var Q1488;
            Q1488=makeQuery(id+"F3.opExtrude","CAP_EDGE",EDGE,{"disambiguationData":[OSD([sQuery(id+"F2.wireOp",EDGE,"E2.15.12.0")])],"isStart":false});
            var Q1489;
            Q1489=makeQuery(id+"F3.opExtrude","CAP_EDGE",EDGE,{"disambiguationData":[OSD([sQuery(id+"F2.wireOp",EDGE,"E2.2.12.0")])],"isStart":false});
            var Q1490;
            Q1490=makeQuery(id+"F3.opExtrude","CAP_EDGE",EDGE,{"disambiguationData":[OSD([sQuery(id+"F2.wireOp",EDGE,"E3.0.23.12")])],"isStart":false});
            var Q1491;
            Q1491=makeQuery(id+"F3.opExtrude","CAP_EDGE",EDGE,{"disambiguationData":[OSD([sQuery(id+"F2.wireOp",EDGE,"E2.10.12.0")])],"isStart":false});
            var Q1492;
            Q1492=makeQuery(id+"F3.opExtrude","CAP_EDGE",EDGE,{"disambiguationData":[OSD([sQuery(id+"F2.wireOp",EDGE,"E2.17.12.0")])],"isStart":false});
            var Q1493;
            Q1493=makeQuery(id+"F3.opExtrude","CAP_EDGE",EDGE,{"disambiguationData":[OSD([sQuery(id+"F2.wireOp",EDGE,"E2.4.12.0")])],"isStart":false});
            var Q1494;
            Q1494=makeQuery(id+"F3.opExtrude","CAP_EDGE",EDGE,{"disambiguationData":[OSD([sQuery(id+"F2.wireOp",EDGE,"E2.11.12.0")])],"isStart":false});
            var Q1495;
            Q1495=makeQuery(id+"F3.opExtrude","CAP_EDGE",EDGE,{"disambiguationData":[OSD([sQuery(id+"F2.wireOp",EDGE,"E2.18.12.0")])],"isStart":false});
            var Q1496;
            Q1496=makeQuery(id+"F3.opExtrude","CAP_EDGE",EDGE,{"disambiguationData":[OSD([sQuery(id+"F2.wireOp",EDGE,"E3.0.24.12")])],"isStart":false});
            var Q1497;
            Q1497=makeQuery(id+"F3.opExtrude","CAP_EDGE",EDGE,{"disambiguationData":[OSD([sQuery(id+"F2.wireOp",EDGE,"E2.5.12.0")])],"isStart":false});
            var Q1498;
            Q1498=makeQuery(id+"F3.opExtrude","CAP_EDGE",EDGE,{"disambiguationData":[OSD([sQuery(id+"F2.wireOp",EDGE,"E2.12.12.0")])],"isStart":false});
            var Q1499;
            Q1499=makeQuery(id+"F3.opExtrude","CAP_EDGE",EDGE,{"disambiguationData":[OSD([sQuery(id+"F2.wireOp",EDGE,"E2.6.12.0")])],"isStart":false});
            var Q1500;
            Q1500=makeQuery(id+"F3.opExtrude","CAP_EDGE",EDGE,{"disambiguationData":[OSD([sQuery(id+"F2.wireOp",EDGE,"E3.0.25.12")])],"isStart":false});
            var Q1501;
            Q1501=makeQuery(id+"F3.opExtrude","CAP_EDGE",EDGE,{"disambiguationData":[OSD([sQuery(id+"F2.wireOp",EDGE,"E2.0.12.1")])],"isStart":false});
            var Q1502;
            Q1502=makeQuery(id+"F3.opExtrude","CAP_EDGE",EDGE,{"disambiguationData":[OSD([sQuery(id+"F2.wireOp",EDGE,"E2.16.12.2")])],"isStart":false});
            var Q1503;
            Q1503=makeQuery(id+"F3.opExtrude","CAP_EDGE",EDGE,{"disambiguationData":[OSD([sQuery(id+"F2.wireOp",EDGE,"E3.6.23.12")])],"isStart":false});
            var Q1504;
            Q1504=makeQuery(id+"F3.opExtrude","CAP_EDGE",EDGE,{"disambiguationData":[OSD([sQuery(id+"F2.wireOp",EDGE,"E2.10.12.2")])],"isStart":false});
            var Q1505;
            Q1505=makeQuery(id+"F3.opExtrude","CAP_EDGE",EDGE,{"disambiguationData":[OSD([sQuery(id+"F2.wireOp",EDGE,"E2.17.12.2")])],"isStart":false});
            var Q1506;
            Q1506=makeQuery(id+"F3.opExtrude","CAP_EDGE",EDGE,{"disambiguationData":[OSD([sQuery(id+"F2.wireOp",EDGE,"E2.4.12.2")])],"isStart":false});
            var Q1507;
            Q1507=makeQuery(id+"F3.opExtrude","CAP_EDGE",EDGE,{"disambiguationData":[OSD([sQuery(id+"F2.wireOp",EDGE,"E2.11.12.2")])],"isStart":false});
            var Q1508;
            Q1508=makeQuery(id+"F3.opExtrude","CAP_EDGE",EDGE,{"disambiguationData":[OSD([sQuery(id+"F2.wireOp",EDGE,"E2.5.12.2")])],"isStart":false});
            var Q1509;
            Q1509=makeQuery(id+"F3.opExtrude","CAP_EDGE",EDGE,{"disambiguationData":[OSD([sQuery(id+"F2.wireOp",EDGE,"E3.6.24.12")])],"isStart":false});
            var Q1510;
            Q1510=makeQuery(id+"F3.opExtrude","CAP_EDGE",EDGE,{"disambiguationData":[OSD([sQuery(id+"F2.wireOp",EDGE,"E2.18.12.2")])],"isStart":false});
            var Q1511;
            Q1511=makeQuery(id+"F3.opExtrude","CAP_EDGE",EDGE,{"disambiguationData":[OSD([sQuery(id+"F2.wireOp",EDGE,"E3.6.25.12")])],"isStart":false});
            var Q1512;
            Q1512=makeQuery(id+"F3.opExtrude","CAP_EDGE",EDGE,{"disambiguationData":[OSD([sQuery(id+"F2.wireOp",EDGE,"E2.12.12.2")])],"isStart":false});
            var Q1513;
            Q1513=makeQuery(id+"F3.opExtrude","CAP_EDGE",EDGE,{"disambiguationData":[OSD([sQuery(id+"F2.wireOp",EDGE,"E3.6.29.12")])],"isStart":false});
            var Q1514;
            Q1514=makeQuery(id+"F3.opExtrude","CAP_EDGE",EDGE,{"disambiguationData":[OSD([sQuery(id+"F2.wireOp",EDGE,"E2.9.12.2")])],"isStart":false});
            var Q1515;
            Q1515=makeQuery(id+"F3.opExtrude","CAP_EDGE",EDGE,{"disambiguationData":[OSD([sQuery(id+"F2.wireOp",EDGE,"E3.6.28.12")])],"isStart":false});
            var Q1516;
            Q1516=makeQuery(id+"F3.opExtrude","CAP_EDGE",EDGE,{"disambiguationData":[OSD([sQuery(id+"F2.wireOp",EDGE,"E2.3.12.2")])],"isStart":false});
            var Q1517;
            Q1517=makeQuery(id+"F3.opExtrude","CAP_EDGE",EDGE,{"disambiguationData":[OSD([sQuery(id+"F2.wireOp",EDGE,"E3.6.22.12")])],"isStart":false});
            var Q1518;
            Q1518=makeQuery(id+"F3.opExtrude","CAP_EDGE",EDGE,{"disambiguationData":[OSD([sQuery(id+"F2.wireOp",EDGE,"E2.6.12.2")])],"isStart":false});
            var Q1519;
            Q1519=makeQuery(id+"F3.opExtrude","CAP_EDGE",EDGE,{"disambiguationData":[OSD([sQuery(id+"F2.wireOp",EDGE,"E2.19.12.2")])],"isStart":false});
            var Q1520;
            Q1520=makeQuery(id+"F3.opExtrude","CAP_EDGE",EDGE,{"disambiguationData":[OSD([sQuery(id+"F2.wireOp",EDGE,"E2.13.12.2")])],"isStart":false});
            var Q1521;
            Q1521=makeQuery(id+"F3.opExtrude","CAP_EDGE",EDGE,{"disambiguationData":[OSD([sQuery(id+"F2.wireOp",EDGE,"E2.7.12.2")])],"isStart":false});
            var Q1522;
            Q1522=makeQuery(id+"F3.opExtrude","CAP_EDGE",EDGE,{"disambiguationData":[OSD([sQuery(id+"F2.wireOp",EDGE,"E3.6.26.12")])],"isStart":false});
            var Q1523;
            Q1523=makeQuery(id+"F3.opExtrude","CAP_EDGE",EDGE,{"disambiguationData":[OSD([sQuery(id+"F2.wireOp",EDGE,"E2.1.12.2")])],"isStart":false});
            var Q1524;
            Q1524=makeQuery(id+"F3.opExtrude","CAP_EDGE",EDGE,{"disambiguationData":[OSD([sQuery(id+"F2.wireOp",EDGE,"E3.6.20.12")])],"isStart":false});
            var Q1525;
            Q1525=makeQuery(id+"F3.opExtrude","CAP_EDGE",EDGE,{"disambiguationData":[OSD([sQuery(id+"F2.wireOp",EDGE,"E3.6.27.12")])],"isStart":false});
            var Q1526;
            Q1526=makeQuery(id+"F3.opExtrude","CAP_EDGE",EDGE,{"disambiguationData":[OSD([sQuery(id+"F2.wireOp",EDGE,"E2.14.12.2")])],"isStart":false});
            var Q1527;
            Q1527=makeQuery(id+"F3.opExtrude","CAP_EDGE",EDGE,{"disambiguationData":[OSD([sQuery(id+"F2.wireOp",EDGE,"E3.6.21.12")])],"isStart":false});
            var Q1528;
            Q1528=makeQuery(id+"F3.opExtrude","CAP_EDGE",EDGE,{"disambiguationData":[OSD([sQuery(id+"F2.wireOp",EDGE,"E2.8.12.2")])],"isStart":false});
            var Q1529;
            Q1529=makeQuery(id+"F3.opExtrude","CAP_EDGE",EDGE,{"disambiguationData":[OSD([sQuery(id+"F2.wireOp",EDGE,"E2.15.12.2")])],"isStart":false});
            var Q1530;
            Q1530=makeQuery(id+"F3.opExtrude","CAP_EDGE",EDGE,{"disambiguationData":[OSD([sQuery(id+"F2.wireOp",EDGE,"E2.2.12.2")])],"isStart":false});
            var Q1531;
            Q1531=makeQuery(id+"F3.opExtrude","CAP_EDGE",EDGE,{"disambiguationData":[OSD([sQuery(id+"F2.wireOp",EDGE,"E3.3.29.12")])],"isStart":false});
            var Q1532;
            Q1532=makeQuery(id+"F3.opExtrude","CAP_EDGE",EDGE,{"disambiguationData":[OSD([sQuery(id+"F2.wireOp",EDGE,"E2.9.12.1")])],"isStart":false});
            var Q1533;
            Q1533=makeQuery(id+"F3.opExtrude","CAP_EDGE",EDGE,{"disambiguationData":[OSD([sQuery(id+"F2.wireOp",EDGE,"E3.3.28.12")])],"isStart":false});
            var Q1534;
            Q1534=makeQuery(id+"F3.opExtrude","CAP_EDGE",EDGE,{"disambiguationData":[OSD([sQuery(id+"F2.wireOp",EDGE,"E2.16.12.1")])],"isStart":false});
            var Q1535;
            Q1535=makeQuery(id+"F3.opExtrude","CAP_EDGE",EDGE,{"disambiguationData":[OSD([sQuery(id+"F2.wireOp",EDGE,"E3.3.22.12")])],"isStart":false});
            var Q1536;
            Q1536=makeQuery(id+"F3.opExtrude","CAP_EDGE",EDGE,{"disambiguationData":[OSD([sQuery(id+"F2.wireOp",EDGE,"E2.3.12.1")])],"isStart":false});
            var Q1537;
            Q1537=makeQuery(id+"F3.opExtrude","CAP_EDGE",EDGE,{"disambiguationData":[OSD([sQuery(id+"F2.wireOp",EDGE,"E3.3.23.12")])],"isStart":false});
            var Q1538;
            Q1538=makeQuery(id+"F3.opExtrude","CAP_EDGE",EDGE,{"disambiguationData":[OSD([sQuery(id+"F2.wireOp",EDGE,"E2.10.12.1")])],"isStart":false});
            var Q1539;
            Q1539=makeQuery(id+"F3.opExtrude","CAP_EDGE",EDGE,{"disambiguationData":[OSD([sQuery(id+"F2.wireOp",EDGE,"E2.17.12.1")])],"isStart":false});
            var Q1540;
            Q1540=makeQuery(id+"F3.opExtrude","CAP_EDGE",EDGE,{"disambiguationData":[OSD([sQuery(id+"F2.wireOp",EDGE,"E2.4.12.1")])],"isStart":false});
            var Q1541;
            Q1541=makeQuery(id+"F3.opExtrude","CAP_EDGE",EDGE,{"disambiguationData":[OSD([sQuery(id+"F2.wireOp",EDGE,"E2.1.12.1")])],"isStart":false});
            var Q1542;
            Q1542=makeQuery(id+"F3.opExtrude","CAP_EDGE",EDGE,{"disambiguationData":[OSD([sQuery(id+"F2.wireOp",EDGE,"E3.3.20.12")])],"isStart":false});
            var Q1543;
            Q1543=makeQuery(id+"F3.opExtrude","CAP_EDGE",EDGE,{"disambiguationData":[OSD([sQuery(id+"F2.wireOp",EDGE,"E3.3.27.12")])],"isStart":false});
            var Q1544;
            Q1544=makeQuery(id+"F3.opExtrude","CAP_EDGE",EDGE,{"disambiguationData":[OSD([sQuery(id+"F2.wireOp",EDGE,"E2.14.12.1")])],"isStart":false});
            var Q1545;
            Q1545=makeQuery(id+"F3.opExtrude","CAP_EDGE",EDGE,{"disambiguationData":[OSD([sQuery(id+"F2.wireOp",EDGE,"E3.3.21.12")])],"isStart":false});
            var Q1546;
            Q1546=makeQuery(id+"F3.opExtrude","CAP_EDGE",EDGE,{"disambiguationData":[OSD([sQuery(id+"F2.wireOp",EDGE,"E2.8.12.1")])],"isStart":false});
            var Q1547;
            Q1547=makeQuery(id+"F3.opExtrude","CAP_EDGE",EDGE,{"disambiguationData":[OSD([sQuery(id+"F2.wireOp",EDGE,"E2.15.12.1")])],"isStart":false});
            var Q1548;
            Q1548=makeQuery(id+"F3.opExtrude","CAP_EDGE",EDGE,{"disambiguationData":[OSD([sQuery(id+"F2.wireOp",EDGE,"E2.2.12.1")])],"isStart":false});
            var Q1549;
            Q1549=makeQuery(id+"F3.opExtrude","CAP_EDGE",EDGE,{"disambiguationData":[OSD([sQuery(id+"F2.wireOp",EDGE,"E2.11.12.1")])],"isStart":false});
            var Q1550;
            Q1550=makeQuery(id+"F3.opExtrude","CAP_EDGE",EDGE,{"disambiguationData":[OSD([sQuery(id+"F2.wireOp",EDGE,"E2.5.12.1")])],"isStart":false});
            var Q1551;
            Q1551=makeQuery(id+"F3.opExtrude","CAP_EDGE",EDGE,{"disambiguationData":[OSD([sQuery(id+"F2.wireOp",EDGE,"E3.3.24.12")])],"isStart":false});
            var Q1552;
            Q1552=makeQuery(id+"F3.opExtrude","CAP_EDGE",EDGE,{"disambiguationData":[OSD([sQuery(id+"F2.wireOp",EDGE,"E2.12.12.1")])],"isStart":false});
            var Q1553;
            Q1553=makeQuery(id+"F3.opExtrude","CAP_EDGE",EDGE,{"disambiguationData":[OSD([sQuery(id+"F2.wireOp",EDGE,"E2.18.12.1")])],"isStart":false});
            var Q1554;
            Q1554=makeQuery(id+"F3.opExtrude","CAP_EDGE",EDGE,{"disambiguationData":[OSD([sQuery(id+"F2.wireOp",EDGE,"E2.6.12.1")])],"isStart":false});
            var Q1555;
            Q1555=makeQuery(id+"F3.opExtrude","CAP_EDGE",EDGE,{"disambiguationData":[OSD([sQuery(id+"F2.wireOp",EDGE,"E3.3.25.12")])],"isStart":false});
            var Q1556;
            Q1556=makeQuery(id+"F3.opExtrude","CAP_EDGE",EDGE,{"disambiguationData":[OSD([sQuery(id+"F2.wireOp",EDGE,"E2.19.12.1")])],"isStart":false});
            var Q1557;
            Q1557=makeQuery(id+"F3.opExtrude","CAP_EDGE",EDGE,{"disambiguationData":[OSD([sQuery(id+"F2.wireOp",EDGE,"E2.13.12.1")])],"isStart":false});
            var Q1558;
            Q1558=makeQuery(id+"F3.opExtrude","CAP_EDGE",EDGE,{"disambiguationData":[OSD([sQuery(id+"F2.wireOp",EDGE,"E2.7.12.1")])],"isStart":false});
            var Q1559;
            Q1559=makeQuery(id+"F3.opExtrude","CAP_EDGE",EDGE,{"disambiguationData":[OSD([sQuery(id+"F2.wireOp",EDGE,"E3.3.26.12")])],"isStart":false});
            var Q1560;
            Q1560=makeQuery(id+"F3.opExtrude","CAP_EDGE",EDGE,{"disambiguationData":[OSD([sQuery(id+"F2.wireOp",EDGE,"E2.0.13.0")])],"isStart":false});
            var Q1561;
            Q1561=makeQuery(id+"F3.opExtrude","CAP_EDGE",EDGE,{"disambiguationData":[OSD([sQuery(id+"F2.wireOp",EDGE,"E2.0.13.2")])],"isStart":false});
            var Q1562;
            Q1562=makeQuery(id+"F3.opExtrude","CAP_EDGE",EDGE,{"disambiguationData":[OSD([sQuery(id+"F2.wireOp",EDGE,"E3.0.29.13")])],"isStart":false});
            var Q1563;
            Q1563=makeQuery(id+"F3.opExtrude","CAP_EDGE",EDGE,{"disambiguationData":[OSD([sQuery(id+"F2.wireOp",EDGE,"E2.9.13.0")])],"isStart":false});
            var Q1564;
            Q1564=makeQuery(id+"F3.opExtrude","CAP_EDGE",EDGE,{"disambiguationData":[OSD([sQuery(id+"F2.wireOp",EDGE,"E3.0.28.13")])],"isStart":false});
            var Q1565;
            Q1565=makeQuery(id+"F3.opExtrude","CAP_EDGE",EDGE,{"disambiguationData":[OSD([sQuery(id+"F2.wireOp",EDGE,"E2.3.13.0")])],"isStart":false});
            var Q1566;
            Q1566=makeQuery(id+"F3.opExtrude","CAP_EDGE",EDGE,{"disambiguationData":[OSD([sQuery(id+"F2.wireOp",EDGE,"E3.0.22.13")])],"isStart":false});
            var Q1567;
            Q1567=makeQuery(id+"F3.opExtrude","CAP_EDGE",EDGE,{"disambiguationData":[OSD([sQuery(id+"F2.wireOp",EDGE,"E2.16.13.0")])],"isStart":false});
            var Q1568;
            Q1568=makeQuery(id+"F3.opExtrude","CAP_EDGE",EDGE,{"disambiguationData":[OSD([sQuery(id+"F2.wireOp",EDGE,"E3.0.23.13")])],"isStart":false});
            var Q1569;
            Q1569=makeQuery(id+"F3.opExtrude","CAP_EDGE",EDGE,{"disambiguationData":[OSD([sQuery(id+"F2.wireOp",EDGE,"E2.10.13.0")])],"isStart":false});
            var Q1570;
            Q1570=makeQuery(id+"F3.opExtrude","CAP_EDGE",EDGE,{"disambiguationData":[OSD([sQuery(id+"F2.wireOp",EDGE,"E3.0.26.13")])],"isStart":false});
            var Q1571;
            Q1571=makeQuery(id+"F3.opExtrude","CAP_EDGE",EDGE,{"disambiguationData":[OSD([sQuery(id+"F2.wireOp",EDGE,"E2.13.13.0")])],"isStart":false});
            var Q1572;
            Q1572=makeQuery(id+"F3.opExtrude","CAP_EDGE",EDGE,{"disambiguationData":[OSD([sQuery(id+"F2.wireOp",EDGE,"E3.0.20.13")])],"isStart":false});
            var Q1573;
            Q1573=makeQuery(id+"F3.opExtrude","CAP_EDGE",EDGE,{"disambiguationData":[OSD([sQuery(id+"F2.wireOp",EDGE,"E2.7.13.0")])],"isStart":false});
            var Q1574;
            Q1574=makeQuery(id+"F3.opExtrude","CAP_EDGE",EDGE,{"disambiguationData":[OSD([sQuery(id+"F2.wireOp",EDGE,"E2.14.13.0")])],"isStart":false});
            var Q1575;
            Q1575=makeQuery(id+"F3.opExtrude","CAP_EDGE",EDGE,{"disambiguationData":[OSD([sQuery(id+"F2.wireOp",EDGE,"E2.1.13.0")])],"isStart":false});
            var Q1576;
            Q1576=makeQuery(id+"F3.opExtrude","CAP_EDGE",EDGE,{"disambiguationData":[OSD([sQuery(id+"F2.wireOp",EDGE,"E3.0.21.13")])],"isStart":false});
            var Q1577;
            Q1577=makeQuery(id+"F3.opExtrude","CAP_EDGE",EDGE,{"disambiguationData":[OSD([sQuery(id+"F2.wireOp",EDGE,"E3.0.27.13")])],"isStart":false});
            var Q1578;
            Q1578=makeQuery(id+"F3.opExtrude","CAP_EDGE",EDGE,{"disambiguationData":[OSD([sQuery(id+"F2.wireOp",EDGE,"E2.8.13.0")])],"isStart":false});
            var Q1579;
            Q1579=makeQuery(id+"F3.opExtrude","CAP_EDGE",EDGE,{"disambiguationData":[OSD([sQuery(id+"F2.wireOp",EDGE,"E2.15.13.0")])],"isStart":false});
            var Q1580;
            Q1580=makeQuery(id+"F3.opExtrude","CAP_EDGE",EDGE,{"disambiguationData":[OSD([sQuery(id+"F2.wireOp",EDGE,"E2.2.13.0")])],"isStart":false});
            var Q1581;
            Q1581=makeQuery(id+"F3.opExtrude","CAP_EDGE",EDGE,{"disambiguationData":[OSD([sQuery(id+"F2.wireOp",EDGE,"E2.17.13.0")])],"isStart":false});
            var Q1582;
            Q1582=makeQuery(id+"F3.opExtrude","CAP_EDGE",EDGE,{"disambiguationData":[OSD([sQuery(id+"F2.wireOp",EDGE,"E2.4.13.0")])],"isStart":false});
            var Q1583;
            Q1583=makeQuery(id+"F3.opExtrude","CAP_EDGE",EDGE,{"disambiguationData":[OSD([sQuery(id+"F2.wireOp",EDGE,"E2.11.13.0")])],"isStart":false});
            var Q1584;
            Q1584=makeQuery(id+"F3.opExtrude","CAP_EDGE",EDGE,{"disambiguationData":[OSD([sQuery(id+"F2.wireOp",EDGE,"E2.5.13.0")])],"isStart":false});
            var Q1585;
            Q1585=makeQuery(id+"F3.opExtrude","CAP_EDGE",EDGE,{"disambiguationData":[OSD([sQuery(id+"F2.wireOp",EDGE,"E3.0.24.13")])],"isStart":false});
            var Q1586;
            Q1586=makeQuery(id+"F3.opExtrude","CAP_EDGE",EDGE,{"disambiguationData":[OSD([sQuery(id+"F2.wireOp",EDGE,"E2.18.13.0")])],"isStart":false});
            var Q1587;
            Q1587=makeQuery(id+"F3.opExtrude","CAP_EDGE",EDGE,{"disambiguationData":[OSD([sQuery(id+"F2.wireOp",EDGE,"E3.0.25.13")])],"isStart":false});
            var Q1588;
            Q1588=makeQuery(id+"F3.opExtrude","CAP_EDGE",EDGE,{"disambiguationData":[OSD([sQuery(id+"F2.wireOp",EDGE,"E2.12.13.0")])],"isStart":false});
            var Q1589;
            Q1589=makeQuery(id+"F3.opExtrude","CAP_EDGE",EDGE,{"disambiguationData":[OSD([sQuery(id+"F2.wireOp",EDGE,"E2.6.13.0")])],"isStart":false});
            var Q1590;
            Q1590=makeQuery(id+"F3.opExtrude","CAP_EDGE",EDGE,{"disambiguationData":[OSD([sQuery(id+"F2.wireOp",EDGE,"E2.19.13.0")])],"isStart":false});
            var Q1591;
            Q1591=makeQuery(id+"F3.opExtrude","CAP_EDGE",EDGE,{"disambiguationData":[OSD([sQuery(id+"F2.wireOp",EDGE,"E3.6.29.13")])],"isStart":false});
            var Q1592;
            Q1592=makeQuery(id+"F3.opExtrude","CAP_EDGE",EDGE,{"disambiguationData":[OSD([sQuery(id+"F2.wireOp",EDGE,"E2.18.13.2")])],"isStart":false});
            var Q1593;
            Q1593=makeQuery(id+"F3.opExtrude","CAP_EDGE",EDGE,{"disambiguationData":[OSD([sQuery(id+"F2.wireOp",EDGE,"E3.6.25.13")])],"isStart":false});
            var Q1594;
            Q1594=makeQuery(id+"F3.opExtrude","CAP_EDGE",EDGE,{"disambiguationData":[OSD([sQuery(id+"F2.wireOp",EDGE,"E2.12.13.2")])],"isStart":false});
            var Q1595;
            Q1595=makeQuery(id+"F3.opExtrude","CAP_EDGE",EDGE,{"disambiguationData":[OSD([sQuery(id+"F2.wireOp",EDGE,"E2.6.13.2")])],"isStart":false});
            var Q1596;
            Q1596=makeQuery(id+"F3.opExtrude","CAP_EDGE",EDGE,{"disambiguationData":[OSD([sQuery(id+"F2.wireOp",EDGE,"E2.19.13.2")])],"isStart":false});
            var Q1597;
            Q1597=makeQuery(id+"F3.opExtrude","CAP_EDGE",EDGE,{"disambiguationData":[OSD([sQuery(id+"F2.wireOp",EDGE,"E3.6.26.13")])],"isStart":false});
            var Q1598;
            Q1598=makeQuery(id+"F3.opExtrude","CAP_EDGE",EDGE,{"disambiguationData":[OSD([sQuery(id+"F2.wireOp",EDGE,"E2.13.13.2")])],"isStart":false});
            var Q1599;
            Q1599=makeQuery(id+"F3.opExtrude","CAP_EDGE",EDGE,{"disambiguationData":[OSD([sQuery(id+"F2.wireOp",EDGE,"E3.6.20.13")])],"isStart":false});
            var Q1600;
            Q1600=makeQuery(id+"F3.opExtrude","CAP_EDGE",EDGE,{"disambiguationData":[OSD([sQuery(id+"F2.wireOp",EDGE,"E2.7.13.2")])],"isStart":false});
            var Q1601;
            Q1601=makeQuery(id+"F3.opExtrude","CAP_EDGE",EDGE,{"disambiguationData":[OSD([sQuery(id+"F2.wireOp",EDGE,"E2.14.13.2")])],"isStart":false});
            var Q1602;
            Q1602=makeQuery(id+"F3.opExtrude","CAP_EDGE",EDGE,{"disambiguationData":[OSD([sQuery(id+"F2.wireOp",EDGE,"E2.1.13.2")])],"isStart":false});
            var Q1603;
            Q1603=makeQuery(id+"F3.opExtrude","CAP_EDGE",EDGE,{"disambiguationData":[OSD([sQuery(id+"F2.wireOp",EDGE,"E2.9.13.2")])],"isStart":false});
            var Q1604;
            Q1604=makeQuery(id+"F3.opExtrude","CAP_EDGE",EDGE,{"disambiguationData":[OSD([sQuery(id+"F2.wireOp",EDGE,"E3.6.28.13")])],"isStart":false});
            var Q1605;
            Q1605=makeQuery(id+"F3.opExtrude","CAP_EDGE",EDGE,{"disambiguationData":[OSD([sQuery(id+"F2.wireOp",EDGE,"E2.3.13.2")])],"isStart":false});
            var Q1606;
            Q1606=makeQuery(id+"F3.opExtrude","CAP_EDGE",EDGE,{"disambiguationData":[OSD([sQuery(id+"F2.wireOp",EDGE,"E3.6.22.13")])],"isStart":false});
            var Q1607;
            Q1607=makeQuery(id+"F3.opExtrude","CAP_EDGE",EDGE,{"disambiguationData":[OSD([sQuery(id+"F2.wireOp",EDGE,"E2.16.13.2")])],"isStart":false});
            var Q1608;
            Q1608=makeQuery(id+"F3.opExtrude","CAP_EDGE",EDGE,{"disambiguationData":[OSD([sQuery(id+"F2.wireOp",EDGE,"E2.0.13.1")])],"isStart":false});
            var Q1609;
            Q1609=makeQuery(id+"F3.opExtrude","CAP_EDGE",EDGE,{"disambiguationData":[OSD([sQuery(id+"F2.wireOp",EDGE,"E3.6.23.13")])],"isStart":false});
            var Q1610;
            Q1610=makeQuery(id+"F3.opExtrude","CAP_EDGE",EDGE,{"disambiguationData":[OSD([sQuery(id+"F2.wireOp",EDGE,"E2.10.13.2")])],"isStart":false});
            var Q1611;
            Q1611=makeQuery(id+"F3.opExtrude","CAP_EDGE",EDGE,{"disambiguationData":[OSD([sQuery(id+"F2.wireOp",EDGE,"E2.17.13.2")])],"isStart":false});
            var Q1612;
            Q1612=makeQuery(id+"F3.opExtrude","CAP_EDGE",EDGE,{"disambiguationData":[OSD([sQuery(id+"F2.wireOp",EDGE,"E2.4.13.2")])],"isStart":false});
            var Q1613;
            Q1613=makeQuery(id+"F3.opExtrude","CAP_EDGE",EDGE,{"disambiguationData":[OSD([sQuery(id+"F2.wireOp",EDGE,"E2.11.13.2")])],"isStart":false});
            var Q1614;
            Q1614=makeQuery(id+"F3.opExtrude","CAP_EDGE",EDGE,{"disambiguationData":[OSD([sQuery(id+"F2.wireOp",EDGE,"E2.5.13.2")])],"isStart":false});
            var Q1615;
            Q1615=makeQuery(id+"F3.opExtrude","CAP_EDGE",EDGE,{"disambiguationData":[OSD([sQuery(id+"F2.wireOp",EDGE,"E3.6.24.13")])],"isStart":false});
            var Q1616;
            Q1616=makeQuery(id+"F3.opExtrude","CAP_EDGE",EDGE,{"disambiguationData":[OSD([sQuery(id+"F2.wireOp",EDGE,"E2.8.13.2")])],"isStart":false});
            var Q1617;
            Q1617=makeQuery(id+"F3.opExtrude","CAP_EDGE",EDGE,{"disambiguationData":[OSD([sQuery(id+"F2.wireOp",EDGE,"E3.6.27.13")])],"isStart":false});
            var Q1618;
            Q1618=makeQuery(id+"F3.opExtrude","CAP_EDGE",EDGE,{"disambiguationData":[OSD([sQuery(id+"F2.wireOp",EDGE,"E2.15.13.2")])],"isStart":false});
            var Q1619;
            Q1619=makeQuery(id+"F3.opExtrude","CAP_EDGE",EDGE,{"disambiguationData":[OSD([sQuery(id+"F2.wireOp",EDGE,"E3.6.21.13")])],"isStart":false});
            var Q1620;
            Q1620=makeQuery(id+"F3.opExtrude","CAP_EDGE",EDGE,{"disambiguationData":[OSD([sQuery(id+"F2.wireOp",EDGE,"E2.2.13.2")])],"isStart":false});
            var Q1621;
            Q1621=makeQuery(id+"F3.opExtrude","CAP_EDGE",EDGE,{"disambiguationData":[OSD([sQuery(id+"F2.wireOp",EDGE,"E2.0.13.3")])],"isStart":false});
            var Q1622;
            Q1622=makeQuery(id+"F3.opExtrude","CAP_EDGE",EDGE,{"disambiguationData":[OSD([sQuery(id+"F2.wireOp",EDGE,"E2.3.13.1")])],"isStart":false});
            var Q1623;
            Q1623=makeQuery(id+"F3.opExtrude","CAP_EDGE",EDGE,{"disambiguationData":[OSD([sQuery(id+"F2.wireOp",EDGE,"E3.3.22.13")])],"isStart":false});
            var Q1624;
            Q1624=makeQuery(id+"F3.opExtrude","CAP_EDGE",EDGE,{"disambiguationData":[OSD([sQuery(id+"F2.wireOp",EDGE,"E2.16.13.1")])],"isStart":false});
            var Q1625;
            Q1625=makeQuery(id+"F3.opExtrude","CAP_EDGE",EDGE,{"disambiguationData":[OSD([sQuery(id+"F2.wireOp",EDGE,"E3.3.23.13")])],"isStart":false});
            var Q1626;
            Q1626=makeQuery(id+"F3.opExtrude","CAP_EDGE",EDGE,{"disambiguationData":[OSD([sQuery(id+"F2.wireOp",EDGE,"E2.10.13.1")])],"isStart":false});
            var Q1627;
            Q1627=makeQuery(id+"F3.opExtrude","CAP_EDGE",EDGE,{"disambiguationData":[OSD([sQuery(id+"F2.wireOp",EDGE,"E2.17.13.1")])],"isStart":false});
            var Q1628;
            Q1628=makeQuery(id+"F3.opExtrude","CAP_EDGE",EDGE,{"disambiguationData":[OSD([sQuery(id+"F2.wireOp",EDGE,"E2.4.13.1")])],"isStart":false});
            var Q1629;
            Q1629=makeQuery(id+"F3.opExtrude","CAP_EDGE",EDGE,{"disambiguationData":[OSD([sQuery(id+"F2.wireOp",EDGE,"E2.11.13.1")])],"isStart":false});
            var Q1630;
            Q1630=makeQuery(id+"F3.opExtrude","CAP_EDGE",EDGE,{"disambiguationData":[OSD([sQuery(id+"F2.wireOp",EDGE,"E2.5.13.1")])],"isStart":false});
            var Q1631;
            Q1631=makeQuery(id+"F3.opExtrude","CAP_EDGE",EDGE,{"disambiguationData":[OSD([sQuery(id+"F2.wireOp",EDGE,"E3.3.24.13")])],"isStart":false});
            var Q1632;
            Q1632=makeQuery(id+"F3.opExtrude","CAP_EDGE",EDGE,{"disambiguationData":[OSD([sQuery(id+"F2.wireOp",EDGE,"E2.18.13.1")])],"isStart":false});
            var Q1633;
            Q1633=makeQuery(id+"F3.opExtrude","CAP_EDGE",EDGE,{"disambiguationData":[OSD([sQuery(id+"F2.wireOp",EDGE,"E3.3.29.13")])],"isStart":false});
            var Q1634;
            Q1634=makeQuery(id+"F3.opExtrude","CAP_EDGE",EDGE,{"disambiguationData":[OSD([sQuery(id+"F2.wireOp",EDGE,"E2.9.13.1")])],"isStart":false});
            var Q1635;
            Q1635=makeQuery(id+"F3.opExtrude","CAP_EDGE",EDGE,{"disambiguationData":[OSD([sQuery(id+"F2.wireOp",EDGE,"E3.3.28.13")])],"isStart":false});
            var Q1636;
            Q1636=makeQuery(id+"F3.opExtrude","CAP_EDGE",EDGE,{"disambiguationData":[OSD([sQuery(id+"F2.wireOp",EDGE,"E2.2.13.1")])],"isStart":false});
            var Q1637;
            Q1637=makeQuery(id+"F3.opExtrude","CAP_EDGE",EDGE,{"disambiguationData":[OSD([sQuery(id+"F2.wireOp",EDGE,"E3.3.21.13")])],"isStart":false});
            var Q1638;
            Q1638=makeQuery(id+"F3.opExtrude","CAP_EDGE",EDGE,{"disambiguationData":[OSD([sQuery(id+"F2.wireOp",EDGE,"E2.15.13.1")])],"isStart":false});
            var Q1639;
            Q1639=makeQuery(id+"F3.opExtrude","CAP_EDGE",EDGE,{"disambiguationData":[OSD([sQuery(id+"F2.wireOp",EDGE,"E3.3.25.13")])],"isStart":false});
            var Q1640;
            Q1640=makeQuery(id+"F3.opExtrude","CAP_EDGE",EDGE,{"disambiguationData":[OSD([sQuery(id+"F2.wireOp",EDGE,"E2.12.13.1")])],"isStart":false});
            var Q1641;
            Q1641=makeQuery(id+"F3.opExtrude","CAP_EDGE",EDGE,{"disambiguationData":[OSD([sQuery(id+"F2.wireOp",EDGE,"E2.6.13.1")])],"isStart":false});
            var Q1642;
            Q1642=makeQuery(id+"F3.opExtrude","CAP_EDGE",EDGE,{"disambiguationData":[OSD([sQuery(id+"F2.wireOp",EDGE,"E2.19.13.1")])],"isStart":false});
            var Q1643;
            Q1643=makeQuery(id+"F3.opExtrude","CAP_EDGE",EDGE,{"disambiguationData":[OSD([sQuery(id+"F2.wireOp",EDGE,"E3.3.26.13")])],"isStart":false});
            var Q1644;
            Q1644=makeQuery(id+"F3.opExtrude","CAP_EDGE",EDGE,{"disambiguationData":[OSD([sQuery(id+"F2.wireOp",EDGE,"E2.13.13.1")])],"isStart":false});
            var Q1645;
            Q1645=makeQuery(id+"F3.opExtrude","CAP_EDGE",EDGE,{"disambiguationData":[OSD([sQuery(id+"F2.wireOp",EDGE,"E3.3.20.13")])],"isStart":false});
            var Q1646;
            Q1646=makeQuery(id+"F3.opExtrude","CAP_EDGE",EDGE,{"disambiguationData":[OSD([sQuery(id+"F2.wireOp",EDGE,"E2.7.13.1")])],"isStart":false});
            var Q1647;
            Q1647=makeQuery(id+"F3.opExtrude","CAP_EDGE",EDGE,{"disambiguationData":[OSD([sQuery(id+"F2.wireOp",EDGE,"E2.14.13.1")])],"isStart":false});
            var Q1648;
            Q1648=makeQuery(id+"F3.opExtrude","CAP_EDGE",EDGE,{"disambiguationData":[OSD([sQuery(id+"F2.wireOp",EDGE,"E2.1.13.1")])],"isStart":false});
            var Q1649;
            Q1649=makeQuery(id+"F3.opExtrude","CAP_EDGE",EDGE,{"disambiguationData":[OSD([sQuery(id+"F2.wireOp",EDGE,"E2.8.13.1")])],"isStart":false});
            var Q1650;
            Q1650=makeQuery(id+"F3.opExtrude","CAP_EDGE",EDGE,{"disambiguationData":[OSD([sQuery(id+"F2.wireOp",EDGE,"E3.3.27.13")])],"isStart":false});
            var Q1651;
            Q1651=makeQuery(id+"F3.opExtrude","CAP_EDGE",EDGE,{"disambiguationData":[OSD([sQuery(id+"F2.wireOp",EDGE,"E3.9.29.13")])],"isStart":false});
            var Q1652;
            Q1652=makeQuery(id+"F3.opExtrude","CAP_EDGE",EDGE,{"disambiguationData":[OSD([sQuery(id+"F2.wireOp",EDGE,"E2.9.13.3")])],"isStart":false});
            var Q1653;
            Q1653=makeQuery(id+"F3.opExtrude","CAP_EDGE",EDGE,{"disambiguationData":[OSD([sQuery(id+"F2.wireOp",EDGE,"E3.9.28.13")])],"isStart":false});
            var Q1654;
            Q1654=makeQuery(id+"F3.opExtrude","CAP_EDGE",EDGE,{"disambiguationData":[OSD([sQuery(id+"F2.wireOp",EDGE,"E2.3.13.3")])],"isStart":false});
            var Q1655;
            Q1655=makeQuery(id+"F3.opExtrude","CAP_EDGE",EDGE,{"disambiguationData":[OSD([sQuery(id+"F2.wireOp",EDGE,"E3.9.22.13")])],"isStart":false});
            var Q1656;
            Q1656=makeQuery(id+"F3.opExtrude","CAP_EDGE",EDGE,{"disambiguationData":[OSD([sQuery(id+"F2.wireOp",EDGE,"E2.16.13.3")])],"isStart":false});
            var Q1657;
            Q1657=makeQuery(id+"F3.opExtrude","CAP_EDGE",EDGE,{"disambiguationData":[OSD([sQuery(id+"F2.wireOp",EDGE,"E2.19.13.3")])],"isStart":false});
            var Q1658;
            Q1658=makeQuery(id+"F3.opExtrude","CAP_EDGE",EDGE,{"disambiguationData":[OSD([sQuery(id+"F2.wireOp",EDGE,"E3.9.26.13")])],"isStart":false});
            var Q1659;
            Q1659=makeQuery(id+"F3.opExtrude","CAP_EDGE",EDGE,{"disambiguationData":[OSD([sQuery(id+"F2.wireOp",EDGE,"E2.13.13.3")])],"isStart":false});
            var Q1660;
            Q1660=makeQuery(id+"F3.opExtrude","CAP_EDGE",EDGE,{"disambiguationData":[OSD([sQuery(id+"F2.wireOp",EDGE,"E3.9.20.13")])],"isStart":false});
            var Q1661;
            Q1661=makeQuery(id+"F3.opExtrude","CAP_EDGE",EDGE,{"disambiguationData":[OSD([sQuery(id+"F2.wireOp",EDGE,"E2.7.13.3")])],"isStart":false});
            var Q1662;
            Q1662=makeQuery(id+"F3.opExtrude","CAP_EDGE",EDGE,{"disambiguationData":[OSD([sQuery(id+"F2.wireOp",EDGE,"E2.14.13.3")])],"isStart":false});
            var Q1663;
            Q1663=makeQuery(id+"F3.opExtrude","CAP_EDGE",EDGE,{"disambiguationData":[OSD([sQuery(id+"F2.wireOp",EDGE,"E2.1.13.3")])],"isStart":false});
            var Q1664;
            Q1664=makeQuery(id+"F3.opExtrude","CAP_EDGE",EDGE,{"disambiguationData":[OSD([sQuery(id+"F2.wireOp",EDGE,"E2.8.13.3")])],"isStart":false});
            var Q1665;
            Q1665=makeQuery(id+"F3.opExtrude","CAP_EDGE",EDGE,{"disambiguationData":[OSD([sQuery(id+"F2.wireOp",EDGE,"E3.9.27.13")])],"isStart":false});
            var Q1666;
            Q1666=makeQuery(id+"F3.opExtrude","CAP_EDGE",EDGE,{"disambiguationData":[OSD([sQuery(id+"F2.wireOp",EDGE,"E2.2.13.3")])],"isStart":false});
            var Q1667;
            Q1667=makeQuery(id+"F3.opExtrude","CAP_EDGE",EDGE,{"disambiguationData":[OSD([sQuery(id+"F2.wireOp",EDGE,"E3.9.21.13")])],"isStart":false});
            var Q1668;
            Q1668=makeQuery(id+"F3.opExtrude","CAP_EDGE",EDGE,{"disambiguationData":[OSD([sQuery(id+"F2.wireOp",EDGE,"E2.15.13.3")])],"isStart":false});
            var Q1669;
            Q1669=makeQuery(id+"F3.opExtrude","CAP_EDGE",EDGE,{"disambiguationData":[OSD([sQuery(id+"F2.wireOp",EDGE,"E3.9.23.13")])],"isStart":false});
            var Q1670;
            Q1670=makeQuery(id+"F3.opExtrude","CAP_EDGE",EDGE,{"disambiguationData":[OSD([sQuery(id+"F2.wireOp",EDGE,"E2.10.13.3")])],"isStart":false});
            var Q1671;
            Q1671=makeQuery(id+"F3.opExtrude","CAP_EDGE",EDGE,{"disambiguationData":[OSD([sQuery(id+"F2.wireOp",EDGE,"E2.17.13.3")])],"isStart":false});
            var Q1672;
            Q1672=makeQuery(id+"F3.opExtrude","CAP_EDGE",EDGE,{"disambiguationData":[OSD([sQuery(id+"F2.wireOp",EDGE,"E2.4.13.3")])],"isStart":false});
            var Q1673;
            Q1673=makeQuery(id+"F3.opExtrude","CAP_EDGE",EDGE,{"disambiguationData":[OSD([sQuery(id+"F2.wireOp",EDGE,"E2.11.13.3")])],"isStart":false});
            var Q1674;
            Q1674=makeQuery(id+"F3.opExtrude","CAP_EDGE",EDGE,{"disambiguationData":[OSD([sQuery(id+"F2.wireOp",EDGE,"E2.5.13.3")])],"isStart":false});
            var Q1675;
            Q1675=makeQuery(id+"F3.opExtrude","CAP_EDGE",EDGE,{"disambiguationData":[OSD([sQuery(id+"F2.wireOp",EDGE,"E3.9.24.13")])],"isStart":false});
            var Q1676;
            Q1676=makeQuery(id+"F3.opExtrude","CAP_EDGE",EDGE,{"disambiguationData":[OSD([sQuery(id+"F2.wireOp",EDGE,"E2.18.13.3")])],"isStart":false});
            var Q1677;
            Q1677=makeQuery(id+"F3.opExtrude","CAP_EDGE",EDGE,{"disambiguationData":[OSD([sQuery(id+"F2.wireOp",EDGE,"E3.9.25.13")])],"isStart":false});
            var Q1678;
            Q1678=makeQuery(id+"F3.opExtrude","CAP_EDGE",EDGE,{"disambiguationData":[OSD([sQuery(id+"F2.wireOp",EDGE,"E2.12.13.3")])],"isStart":false});
            var Q1679;
            Q1679=makeQuery(id+"F3.opExtrude","CAP_EDGE",EDGE,{"disambiguationData":[OSD([sQuery(id+"F2.wireOp",EDGE,"E2.6.13.3")])],"isStart":false});
            var Q1680;
            Q1680=makeQuery(id+"F3.opExtrude","CAP_EDGE",EDGE,{"disambiguationData":[OSD([sQuery(id+"F2.wireOp",EDGE,"E2.0.14.3")])],"isStart":false});
            var Q1681;
            Q1681=makeQuery(id+"F3.opExtrude","CAP_EDGE",EDGE,{"disambiguationData":[OSD([sQuery(id+"F2.wireOp",EDGE,"E2.0.14.0")])],"isStart":false});
            var Q1682;
            Q1682=makeQuery(id+"F3.opExtrude","CAP_EDGE",EDGE,{"disambiguationData":[OSD([sQuery(id+"F2.wireOp",EDGE,"E2.0.14.2")])],"isStart":false});
            var Q1683;
            Q1683=makeQuery(id+"F3.opExtrude","CAP_EDGE",EDGE,{"disambiguationData":[OSD([sQuery(id+"F2.wireOp",EDGE,"E3.9.29.14")])],"isStart":false});
            var Q1684;
            Q1684=makeQuery(id+"F3.opExtrude","CAP_EDGE",EDGE,{"disambiguationData":[OSD([sQuery(id+"F2.wireOp",EDGE,"E2.9.14.3")])],"isStart":false});
            var Q1685;
            Q1685=makeQuery(id+"F3.opExtrude","CAP_EDGE",EDGE,{"disambiguationData":[OSD([sQuery(id+"F2.wireOp",EDGE,"E3.9.28.14")])],"isStart":false});
            var Q1686;
            Q1686=makeQuery(id+"F3.opExtrude","CAP_EDGE",EDGE,{"disambiguationData":[OSD([sQuery(id+"F2.wireOp",EDGE,"E3.9.25.14")])],"isStart":false});
            var Q1687;
            Q1687=makeQuery(id+"F3.opExtrude","CAP_EDGE",EDGE,{"disambiguationData":[OSD([sQuery(id+"F2.wireOp",EDGE,"E2.12.14.3")])],"isStart":false});
            var Q1688;
            Q1688=makeQuery(id+"F3.opExtrude","CAP_EDGE",EDGE,{"disambiguationData":[OSD([sQuery(id+"F2.wireOp",EDGE,"E2.6.14.3")])],"isStart":false});
            var Q1689;
            Q1689=makeQuery(id+"F3.opExtrude","CAP_EDGE",EDGE,{"disambiguationData":[OSD([sQuery(id+"F2.wireOp",EDGE,"E2.19.14.3")])],"isStart":false});
            var Q1690;
            Q1690=makeQuery(id+"F3.opExtrude","CAP_EDGE",EDGE,{"disambiguationData":[OSD([sQuery(id+"F2.wireOp",EDGE,"E3.9.26.14")])],"isStart":false});
            var Q1691;
            Q1691=makeQuery(id+"F3.opExtrude","CAP_EDGE",EDGE,{"disambiguationData":[OSD([sQuery(id+"F2.wireOp",EDGE,"E2.13.14.3")])],"isStart":false});
            var Q1692;
            Q1692=makeQuery(id+"F3.opExtrude","CAP_EDGE",EDGE,{"disambiguationData":[OSD([sQuery(id+"F2.wireOp",EDGE,"E3.9.20.14")])],"isStart":false});
            var Q1693;
            Q1693=makeQuery(id+"F3.opExtrude","CAP_EDGE",EDGE,{"disambiguationData":[OSD([sQuery(id+"F2.wireOp",EDGE,"E2.7.14.3")])],"isStart":false});
            var Q1694;
            Q1694=makeQuery(id+"F3.opExtrude","CAP_EDGE",EDGE,{"disambiguationData":[OSD([sQuery(id+"F2.wireOp",EDGE,"E2.14.14.3")])],"isStart":false});
            var Q1695;
            Q1695=makeQuery(id+"F3.opExtrude","CAP_EDGE",EDGE,{"disambiguationData":[OSD([sQuery(id+"F2.wireOp",EDGE,"E2.1.14.3")])],"isStart":false});
            var Q1696;
            Q1696=makeQuery(id+"F3.opExtrude","CAP_EDGE",EDGE,{"disambiguationData":[OSD([sQuery(id+"F2.wireOp",EDGE,"E2.8.14.3")])],"isStart":false});
            var Q1697;
            Q1697=makeQuery(id+"F3.opExtrude","CAP_EDGE",EDGE,{"disambiguationData":[OSD([sQuery(id+"F2.wireOp",EDGE,"E3.9.27.14")])],"isStart":false});
            var Q1698;
            Q1698=makeQuery(id+"F3.opExtrude","CAP_EDGE",EDGE,{"disambiguationData":[OSD([sQuery(id+"F2.wireOp",EDGE,"E2.3.14.3")])],"isStart":false});
            var Q1699;
            Q1699=makeQuery(id+"F3.opExtrude","CAP_EDGE",EDGE,{"disambiguationData":[OSD([sQuery(id+"F2.wireOp",EDGE,"E3.9.22.14")])],"isStart":false});
            var Q1700;
            Q1700=makeQuery(id+"F3.opExtrude","CAP_EDGE",EDGE,{"disambiguationData":[OSD([sQuery(id+"F2.wireOp",EDGE,"E2.16.14.3")])],"isStart":false});
            var Q1701;
            Q1701=makeQuery(id+"F3.opExtrude","CAP_EDGE",EDGE,{"disambiguationData":[OSD([sQuery(id+"F2.wireOp",EDGE,"E2.10.14.3")])],"isStart":false});
            var Q1702;
            Q1702=makeQuery(id+"F3.opExtrude","CAP_EDGE",EDGE,{"disambiguationData":[OSD([sQuery(id+"F2.wireOp",EDGE,"E2.4.14.3")])],"isStart":false});
            var Q1703;
            Q1703=makeQuery(id+"F3.opExtrude","CAP_EDGE",EDGE,{"disambiguationData":[OSD([sQuery(id+"F2.wireOp",EDGE,"E3.9.23.14")])],"isStart":false});
            var Q1704;
            Q1704=makeQuery(id+"F3.opExtrude","CAP_EDGE",EDGE,{"disambiguationData":[OSD([sQuery(id+"F2.wireOp",EDGE,"E2.11.14.3")])],"isStart":false});
            var Q1705;
            Q1705=makeQuery(id+"F3.opExtrude","CAP_EDGE",EDGE,{"disambiguationData":[OSD([sQuery(id+"F2.wireOp",EDGE,"E2.17.14.3")])],"isStart":false});
            var Q1706;
            Q1706=makeQuery(id+"F3.opExtrude","CAP_EDGE",EDGE,{"disambiguationData":[OSD([sQuery(id+"F2.wireOp",EDGE,"E2.5.14.3")])],"isStart":false});
            var Q1707;
            Q1707=makeQuery(id+"F3.opExtrude","CAP_EDGE",EDGE,{"disambiguationData":[OSD([sQuery(id+"F2.wireOp",EDGE,"E3.9.24.14")])],"isStart":false});
            var Q1708;
            Q1708=makeQuery(id+"F3.opExtrude","CAP_EDGE",EDGE,{"disambiguationData":[OSD([sQuery(id+"F2.wireOp",EDGE,"E2.18.14.3")])],"isStart":false});
            var Q1709;
            Q1709=makeQuery(id+"F3.opExtrude","CAP_EDGE",EDGE,{"disambiguationData":[OSD([sQuery(id+"F2.wireOp",EDGE,"E3.0.29.14")])],"isStart":false});
            var Q1710;
            Q1710=makeQuery(id+"F3.opExtrude","CAP_EDGE",EDGE,{"disambiguationData":[OSD([sQuery(id+"F2.wireOp",EDGE,"E2.9.14.0")])],"isStart":false});
            var Q1711;
            Q1711=makeQuery(id+"F3.opExtrude","CAP_EDGE",EDGE,{"disambiguationData":[OSD([sQuery(id+"F2.wireOp",EDGE,"E3.0.28.14")])],"isStart":false});
            var Q1712;
            Q1712=makeQuery(id+"F3.opExtrude","CAP_EDGE",EDGE,{"disambiguationData":[OSD([sQuery(id+"F2.wireOp",EDGE,"E2.3.14.0")])],"isStart":false});
            var Q1713;
            Q1713=makeQuery(id+"F3.opExtrude","CAP_EDGE",EDGE,{"disambiguationData":[OSD([sQuery(id+"F2.wireOp",EDGE,"E3.0.22.14")])],"isStart":false});
            var Q1714;
            Q1714=makeQuery(id+"F3.opExtrude","CAP_EDGE",EDGE,{"disambiguationData":[OSD([sQuery(id+"F2.wireOp",EDGE,"E2.2.14.3")])],"isStart":false});
            var Q1715;
            Q1715=makeQuery(id+"F3.opExtrude","CAP_EDGE",EDGE,{"disambiguationData":[OSD([sQuery(id+"F2.wireOp",EDGE,"E3.9.21.14")])],"isStart":false});
            var Q1716;
            Q1716=makeQuery(id+"F3.opExtrude","CAP_EDGE",EDGE,{"disambiguationData":[OSD([sQuery(id+"F2.wireOp",EDGE,"E2.15.14.3")])],"isStart":false});
            var Q1717;
            Q1717=makeQuery(id+"F3.opExtrude","CAP_EDGE",EDGE,{"disambiguationData":[OSD([sQuery(id+"F2.wireOp",EDGE,"E2.6.14.0")])],"isStart":false});
            var Q1718;
            Q1718=makeQuery(id+"F3.opExtrude","CAP_EDGE",EDGE,{"disambiguationData":[OSD([sQuery(id+"F2.wireOp",EDGE,"E2.19.14.0")])],"isStart":false});
            var Q1719;
            Q1719=makeQuery(id+"F3.opExtrude","CAP_EDGE",EDGE,{"disambiguationData":[OSD([sQuery(id+"F2.wireOp",EDGE,"E3.0.26.14")])],"isStart":false});
            var Q1720;
            Q1720=makeQuery(id+"F3.opExtrude","CAP_EDGE",EDGE,{"disambiguationData":[OSD([sQuery(id+"F2.wireOp",EDGE,"E2.13.14.0")])],"isStart":false});
            var Q1721;
            Q1721=makeQuery(id+"F3.opExtrude","CAP_EDGE",EDGE,{"disambiguationData":[OSD([sQuery(id+"F2.wireOp",EDGE,"E3.0.20.14")])],"isStart":false});
            var Q1722;
            Q1722=makeQuery(id+"F3.opExtrude","CAP_EDGE",EDGE,{"disambiguationData":[OSD([sQuery(id+"F2.wireOp",EDGE,"E2.1.14.0")])],"isStart":false});
            var Q1723;
            Q1723=makeQuery(id+"F3.opExtrude","CAP_EDGE",EDGE,{"disambiguationData":[OSD([sQuery(id+"F2.wireOp",EDGE,"E2.7.14.0")])],"isStart":false});
            var Q1724;
            Q1724=makeQuery(id+"F3.opExtrude","CAP_EDGE",EDGE,{"disambiguationData":[OSD([sQuery(id+"F2.wireOp",EDGE,"E3.0.27.14")])],"isStart":false});
            var Q1725;
            Q1725=makeQuery(id+"F3.opExtrude","CAP_EDGE",EDGE,{"disambiguationData":[OSD([sQuery(id+"F2.wireOp",EDGE,"E2.14.14.0")])],"isStart":false});
            var Q1726;
            Q1726=makeQuery(id+"F3.opExtrude","CAP_EDGE",EDGE,{"disambiguationData":[OSD([sQuery(id+"F2.wireOp",EDGE,"E3.0.21.14")])],"isStart":false});
            var Q1727;
            Q1727=makeQuery(id+"F3.opExtrude","CAP_EDGE",EDGE,{"disambiguationData":[OSD([sQuery(id+"F2.wireOp",EDGE,"E2.8.14.0")])],"isStart":false});
            var Q1728;
            Q1728=makeQuery(id+"F3.opExtrude","CAP_EDGE",EDGE,{"disambiguationData":[OSD([sQuery(id+"F2.wireOp",EDGE,"E2.15.14.0")])],"isStart":false});
            var Q1729;
            Q1729=makeQuery(id+"F3.opExtrude","CAP_EDGE",EDGE,{"disambiguationData":[OSD([sQuery(id+"F2.wireOp",EDGE,"E2.2.14.0")])],"isStart":false});
            var Q1730;
            Q1730=makeQuery(id+"F3.opExtrude","CAP_EDGE",EDGE,{"disambiguationData":[OSD([sQuery(id+"F2.wireOp",EDGE,"E2.16.14.0")])],"isStart":false});
            var Q1731;
            Q1731=makeQuery(id+"F3.opExtrude","CAP_EDGE",EDGE,{"disambiguationData":[OSD([sQuery(id+"F2.wireOp",EDGE,"E3.0.23.14")])],"isStart":false});
            var Q1732;
            Q1732=makeQuery(id+"F3.opExtrude","CAP_EDGE",EDGE,{"disambiguationData":[OSD([sQuery(id+"F2.wireOp",EDGE,"E2.10.14.0")])],"isStart":false});
            var Q1733;
            Q1733=makeQuery(id+"F3.opExtrude","CAP_EDGE",EDGE,{"disambiguationData":[OSD([sQuery(id+"F2.wireOp",EDGE,"E2.17.14.0")])],"isStart":false});
            var Q1734;
            Q1734=makeQuery(id+"F3.opExtrude","CAP_EDGE",EDGE,{"disambiguationData":[OSD([sQuery(id+"F2.wireOp",EDGE,"E2.4.14.0")])],"isStart":false});
            var Q1735;
            Q1735=makeQuery(id+"F3.opExtrude","CAP_EDGE",EDGE,{"disambiguationData":[OSD([sQuery(id+"F2.wireOp",EDGE,"E2.11.14.0")])],"isStart":false});
            var Q1736;
            Q1736=makeQuery(id+"F3.opExtrude","CAP_EDGE",EDGE,{"disambiguationData":[OSD([sQuery(id+"F2.wireOp",EDGE,"E2.5.14.0")])],"isStart":false});
            var Q1737;
            Q1737=makeQuery(id+"F3.opExtrude","CAP_EDGE",EDGE,{"disambiguationData":[OSD([sQuery(id+"F2.wireOp",EDGE,"E3.0.24.14")])],"isStart":false});
            var Q1738;
            Q1738=makeQuery(id+"F3.opExtrude","CAP_EDGE",EDGE,{"disambiguationData":[OSD([sQuery(id+"F2.wireOp",EDGE,"E2.18.14.0")])],"isStart":false});
            var Q1739;
            Q1739=makeQuery(id+"F3.opExtrude","CAP_EDGE",EDGE,{"disambiguationData":[OSD([sQuery(id+"F2.wireOp",EDGE,"E3.0.25.14")])],"isStart":false});
            var Q1740;
            Q1740=makeQuery(id+"F3.opExtrude","CAP_EDGE",EDGE,{"disambiguationData":[OSD([sQuery(id+"F2.wireOp",EDGE,"E2.12.14.0")])],"isStart":false});
            var Q1741;
            Q1741=makeQuery(id+"F3.opExtrude","CAP_EDGE",EDGE,{"disambiguationData":[OSD([sQuery(id+"F2.wireOp",EDGE,"E2.0.14.1")])],"isStart":false});
            var Q1742;
            Q1742=makeQuery(id+"F3.opExtrude","CAP_EDGE",EDGE,{"disambiguationData":[OSD([sQuery(id+"F2.wireOp",EDGE,"E2.16.14.2")])],"isStart":false});
            var Q1743;
            Q1743=makeQuery(id+"F3.opExtrude","CAP_EDGE",EDGE,{"disambiguationData":[OSD([sQuery(id+"F2.wireOp",EDGE,"E3.6.23.14")])],"isStart":false});
            var Q1744;
            Q1744=makeQuery(id+"F3.opExtrude","CAP_EDGE",EDGE,{"disambiguationData":[OSD([sQuery(id+"F2.wireOp",EDGE,"E2.10.14.2")])],"isStart":false});
            var Q1745;
            Q1745=makeQuery(id+"F3.opExtrude","CAP_EDGE",EDGE,{"disambiguationData":[OSD([sQuery(id+"F2.wireOp",EDGE,"E2.17.14.2")])],"isStart":false});
            var Q1746;
            Q1746=makeQuery(id+"F3.opExtrude","CAP_EDGE",EDGE,{"disambiguationData":[OSD([sQuery(id+"F2.wireOp",EDGE,"E2.4.14.2")])],"isStart":false});
            var Q1747;
            Q1747=makeQuery(id+"F3.opExtrude","CAP_EDGE",EDGE,{"disambiguationData":[OSD([sQuery(id+"F2.wireOp",EDGE,"E2.11.14.2")])],"isStart":false});
            var Q1748;
            Q1748=makeQuery(id+"F3.opExtrude","CAP_EDGE",EDGE,{"disambiguationData":[OSD([sQuery(id+"F2.wireOp",EDGE,"E2.5.14.2")])],"isStart":false});
            var Q1749;
            Q1749=makeQuery(id+"F3.opExtrude","CAP_EDGE",EDGE,{"disambiguationData":[OSD([sQuery(id+"F2.wireOp",EDGE,"E3.6.24.14")])],"isStart":false});
            var Q1750;
            Q1750=makeQuery(id+"F3.opExtrude","CAP_EDGE",EDGE,{"disambiguationData":[OSD([sQuery(id+"F2.wireOp",EDGE,"E2.18.14.2")])],"isStart":false});
            var Q1751;
            Q1751=makeQuery(id+"F3.opExtrude","CAP_EDGE",EDGE,{"disambiguationData":[OSD([sQuery(id+"F2.wireOp",EDGE,"E3.6.25.14")])],"isStart":false});
            var Q1752;
            Q1752=makeQuery(id+"F3.opExtrude","CAP_EDGE",EDGE,{"disambiguationData":[OSD([sQuery(id+"F2.wireOp",EDGE,"E2.12.14.2")])],"isStart":false});
            var Q1753;
            Q1753=makeQuery(id+"F3.opExtrude","CAP_EDGE",EDGE,{"disambiguationData":[OSD([sQuery(id+"F2.wireOp",EDGE,"E3.6.29.14")])],"isStart":false});
            var Q1754;
            Q1754=makeQuery(id+"F3.opExtrude","CAP_EDGE",EDGE,{"disambiguationData":[OSD([sQuery(id+"F2.wireOp",EDGE,"E2.9.14.2")])],"isStart":false});
            var Q1755;
            Q1755=makeQuery(id+"F3.opExtrude","CAP_EDGE",EDGE,{"disambiguationData":[OSD([sQuery(id+"F2.wireOp",EDGE,"E3.6.28.14")])],"isStart":false});
            var Q1756;
            Q1756=makeQuery(id+"F3.opExtrude","CAP_EDGE",EDGE,{"disambiguationData":[OSD([sQuery(id+"F2.wireOp",EDGE,"E2.3.14.2")])],"isStart":false});
            var Q1757;
            Q1757=makeQuery(id+"F3.opExtrude","CAP_EDGE",EDGE,{"disambiguationData":[OSD([sQuery(id+"F2.wireOp",EDGE,"E3.6.22.14")])],"isStart":false});
            var Q1758;
            Q1758=makeQuery(id+"F3.opExtrude","CAP_EDGE",EDGE,{"disambiguationData":[OSD([sQuery(id+"F2.wireOp",EDGE,"E2.15.14.2")])],"isStart":false});
            var Q1759;
            Q1759=makeQuery(id+"F3.opExtrude","CAP_EDGE",EDGE,{"disambiguationData":[OSD([sQuery(id+"F2.wireOp",EDGE,"E2.6.14.2")])],"isStart":false});
            var Q1760;
            Q1760=makeQuery(id+"F3.opExtrude","CAP_EDGE",EDGE,{"disambiguationData":[OSD([sQuery(id+"F2.wireOp",EDGE,"E2.19.14.2")])],"isStart":false});
            var Q1761;
            Q1761=makeQuery(id+"F3.opExtrude","CAP_EDGE",EDGE,{"disambiguationData":[OSD([sQuery(id+"F2.wireOp",EDGE,"E3.6.26.14")])],"isStart":false});
            var Q1762;
            Q1762=makeQuery(id+"F3.opExtrude","CAP_EDGE",EDGE,{"disambiguationData":[OSD([sQuery(id+"F2.wireOp",EDGE,"E2.13.14.2")])],"isStart":false});
            var Q1763;
            Q1763=makeQuery(id+"F3.opExtrude","CAP_EDGE",EDGE,{"disambiguationData":[OSD([sQuery(id+"F2.wireOp",EDGE,"E3.6.20.14")])],"isStart":false});
            var Q1764;
            Q1764=makeQuery(id+"F3.opExtrude","CAP_EDGE",EDGE,{"disambiguationData":[OSD([sQuery(id+"F2.wireOp",EDGE,"E2.7.14.2")])],"isStart":false});
            var Q1765;
            Q1765=makeQuery(id+"F3.opExtrude","CAP_EDGE",EDGE,{"disambiguationData":[OSD([sQuery(id+"F2.wireOp",EDGE,"E2.14.14.2")])],"isStart":false});
            var Q1766;
            Q1766=makeQuery(id+"F3.opExtrude","CAP_EDGE",EDGE,{"disambiguationData":[OSD([sQuery(id+"F2.wireOp",EDGE,"E2.1.14.2")])],"isStart":false});
            var Q1767;
            Q1767=makeQuery(id+"F3.opExtrude","CAP_EDGE",EDGE,{"disambiguationData":[OSD([sQuery(id+"F2.wireOp",EDGE,"E2.8.14.2")])],"isStart":false});
            var Q1768;
            Q1768=makeQuery(id+"F3.opExtrude","CAP_EDGE",EDGE,{"disambiguationData":[OSD([sQuery(id+"F2.wireOp",EDGE,"E3.6.27.14")])],"isStart":false});
            var Q1769;
            Q1769=makeQuery(id+"F3.opExtrude","CAP_EDGE",EDGE,{"disambiguationData":[OSD([sQuery(id+"F2.wireOp",EDGE,"E2.2.14.2")])],"isStart":false});
            var Q1770;
            Q1770=makeQuery(id+"F3.opExtrude","CAP_EDGE",EDGE,{"disambiguationData":[OSD([sQuery(id+"F2.wireOp",EDGE,"E3.6.21.14")])],"isStart":false});
            var Q1771;
            Q1771=makeQuery(id+"F3.opExtrude","CAP_EDGE",EDGE,{"disambiguationData":[OSD([sQuery(id+"F2.wireOp",EDGE,"E3.3.29.14")])],"isStart":false});
            var Q1772;
            Q1772=makeQuery(id+"F3.opExtrude","CAP_EDGE",EDGE,{"disambiguationData":[OSD([sQuery(id+"F2.wireOp",EDGE,"E2.9.14.1")])],"isStart":false});
            var Q1773;
            Q1773=makeQuery(id+"F3.opExtrude","CAP_EDGE",EDGE,{"disambiguationData":[OSD([sQuery(id+"F2.wireOp",EDGE,"E3.3.28.14")])],"isStart":false});
            var Q1774;
            Q1774=makeQuery(id+"F3.opExtrude","CAP_EDGE",EDGE,{"disambiguationData":[OSD([sQuery(id+"F2.wireOp",EDGE,"E2.3.14.1")])],"isStart":false});
            var Q1775;
            Q1775=makeQuery(id+"F3.opExtrude","CAP_EDGE",EDGE,{"disambiguationData":[OSD([sQuery(id+"F2.wireOp",EDGE,"E3.3.22.14")])],"isStart":false});
            var Q1776;
            Q1776=makeQuery(id+"F3.opExtrude","CAP_EDGE",EDGE,{"disambiguationData":[OSD([sQuery(id+"F2.wireOp",EDGE,"E2.16.14.1")])],"isStart":false});
            var Q1777;
            Q1777=makeQuery(id+"F3.opExtrude","CAP_EDGE",EDGE,{"disambiguationData":[OSD([sQuery(id+"F2.wireOp",EDGE,"E3.3.23.14")])],"isStart":false});
            var Q1778;
            Q1778=makeQuery(id+"F3.opExtrude","CAP_EDGE",EDGE,{"disambiguationData":[OSD([sQuery(id+"F2.wireOp",EDGE,"E2.10.14.1")])],"isStart":false});
            var Q1779;
            Q1779=makeQuery(id+"F3.opExtrude","CAP_EDGE",EDGE,{"disambiguationData":[OSD([sQuery(id+"F2.wireOp",EDGE,"E2.17.14.1")])],"isStart":false});
            var Q1780;
            Q1780=makeQuery(id+"F3.opExtrude","CAP_EDGE",EDGE,{"disambiguationData":[OSD([sQuery(id+"F2.wireOp",EDGE,"E2.4.14.1")])],"isStart":false});
            var Q1781;
            Q1781=makeQuery(id+"F3.opExtrude","CAP_EDGE",EDGE,{"disambiguationData":[OSD([sQuery(id+"F2.wireOp",EDGE,"E3.3.20.14")])],"isStart":false});
            var Q1782;
            Q1782=makeQuery(id+"F3.opExtrude","CAP_EDGE",EDGE,{"disambiguationData":[OSD([sQuery(id+"F2.wireOp",EDGE,"E2.7.14.1")])],"isStart":false});
            var Q1783;
            Q1783=makeQuery(id+"F3.opExtrude","CAP_EDGE",EDGE,{"disambiguationData":[OSD([sQuery(id+"F2.wireOp",EDGE,"E2.14.14.1")])],"isStart":false});
            var Q1784;
            Q1784=makeQuery(id+"F3.opExtrude","CAP_EDGE",EDGE,{"disambiguationData":[OSD([sQuery(id+"F2.wireOp",EDGE,"E2.1.14.1")])],"isStart":false});
            var Q1785;
            Q1785=makeQuery(id+"F3.opExtrude","CAP_EDGE",EDGE,{"disambiguationData":[OSD([sQuery(id+"F2.wireOp",EDGE,"E3.3.21.14")])],"isStart":false});
            var Q1786;
            Q1786=makeQuery(id+"F3.opExtrude","CAP_EDGE",EDGE,{"disambiguationData":[OSD([sQuery(id+"F2.wireOp",EDGE,"E3.3.27.14")])],"isStart":false});
            var Q1787;
            Q1787=makeQuery(id+"F3.opExtrude","CAP_EDGE",EDGE,{"disambiguationData":[OSD([sQuery(id+"F2.wireOp",EDGE,"E2.8.14.1")])],"isStart":false});
            var Q1788;
            Q1788=makeQuery(id+"F3.opExtrude","CAP_EDGE",EDGE,{"disambiguationData":[OSD([sQuery(id+"F2.wireOp",EDGE,"E2.15.14.1")])],"isStart":false});
            var Q1789;
            Q1789=makeQuery(id+"F3.opExtrude","CAP_EDGE",EDGE,{"disambiguationData":[OSD([sQuery(id+"F2.wireOp",EDGE,"E2.2.14.1")])],"isStart":false});
            var Q1790;
            Q1790=makeQuery(id+"F3.opExtrude","CAP_EDGE",EDGE,{"disambiguationData":[OSD([sQuery(id+"F2.wireOp",EDGE,"E2.11.14.1")])],"isStart":false});
            var Q1791;
            Q1791=makeQuery(id+"F3.opExtrude","CAP_EDGE",EDGE,{"disambiguationData":[OSD([sQuery(id+"F2.wireOp",EDGE,"E2.5.14.1")])],"isStart":false});
            var Q1792;
            Q1792=makeQuery(id+"F3.opExtrude","CAP_EDGE",EDGE,{"disambiguationData":[OSD([sQuery(id+"F2.wireOp",EDGE,"E3.3.24.14")])],"isStart":false});
            var Q1793;
            Q1793=makeQuery(id+"F3.opExtrude","CAP_EDGE",EDGE,{"disambiguationData":[OSD([sQuery(id+"F2.wireOp",EDGE,"E2.18.14.1")])],"isStart":false});
            var Q1794;
            Q1794=makeQuery(id+"F3.opExtrude","CAP_EDGE",EDGE,{"disambiguationData":[OSD([sQuery(id+"F2.wireOp",EDGE,"E3.3.25.14")])],"isStart":false});
            var Q1795;
            Q1795=makeQuery(id+"F3.opExtrude","CAP_EDGE",EDGE,{"disambiguationData":[OSD([sQuery(id+"F2.wireOp",EDGE,"E2.12.14.1")])],"isStart":false});
            var Q1796;
            Q1796=makeQuery(id+"F3.opExtrude","CAP_EDGE",EDGE,{"disambiguationData":[OSD([sQuery(id+"F2.wireOp",EDGE,"E2.6.14.1")])],"isStart":false});
            var Q1797;
            Q1797=makeQuery(id+"F3.opExtrude","CAP_EDGE",EDGE,{"disambiguationData":[OSD([sQuery(id+"F2.wireOp",EDGE,"E2.19.14.1")])],"isStart":false});
            var Q1798;
            Q1798=makeQuery(id+"F3.opExtrude","CAP_EDGE",EDGE,{"disambiguationData":[OSD([sQuery(id+"F2.wireOp",EDGE,"E3.3.26.14")])],"isStart":false});
            var Q1799;
            Q1799=makeQuery(id+"F3.opExtrude","CAP_EDGE",EDGE,{"disambiguationData":[OSD([sQuery(id+"F2.wireOp",EDGE,"E2.13.14.1")])],"isStart":false});
            var Q1800;
            Q1800=makeQuery(id+"F3.opExtrude","CAP_EDGE",EDGE,{"disambiguationData":[OSD([sQuery(id+"F2.wireOp",EDGE,"E2.0.15.0")])],"isStart":false});
            var Q1801;
            Q1801=makeQuery(id+"F3.opExtrude","CAP_EDGE",EDGE,{"disambiguationData":[OSD([sQuery(id+"F2.wireOp",EDGE,"E2.0.15.2")])],"isStart":false});
            var Q1802;
            Q1802=makeQuery(id+"F3.opExtrude","CAP_EDGE",EDGE,{"disambiguationData":[OSD([sQuery(id+"F2.wireOp",EDGE,"E3.0.28.15")])],"isStart":false});
            var Q1803;
            Q1803=makeQuery(id+"F3.opExtrude","CAP_EDGE",EDGE,{"disambiguationData":[OSD([sQuery(id+"F2.wireOp",EDGE,"E2.9.15.0")])],"isStart":false});
            var Q1804;
            Q1804=makeQuery(id+"F3.opExtrude","CAP_EDGE",EDGE,{"disambiguationData":[OSD([sQuery(id+"F2.wireOp",EDGE,"E3.0.29.15")])],"isStart":false});
            var Q1805;
            Q1805=makeQuery(id+"F3.opExtrude","CAP_EDGE",EDGE,{"disambiguationData":[OSD([sQuery(id+"F2.wireOp",EDGE,"E2.3.15.0")])],"isStart":false});
            var Q1806;
            Q1806=makeQuery(id+"F3.opExtrude","CAP_EDGE",EDGE,{"disambiguationData":[OSD([sQuery(id+"F2.wireOp",EDGE,"E3.0.22.15")])],"isStart":false});
            var Q1807;
            Q1807=makeQuery(id+"F3.opExtrude","CAP_EDGE",EDGE,{"disambiguationData":[OSD([sQuery(id+"F2.wireOp",EDGE,"E2.16.15.0")])],"isStart":false});
            var Q1808;
            Q1808=makeQuery(id+"F3.opExtrude","CAP_EDGE",EDGE,{"disambiguationData":[OSD([sQuery(id+"F2.wireOp",EDGE,"E2.10.15.0")])],"isStart":false});
            var Q1809;
            Q1809=makeQuery(id+"F3.opExtrude","CAP_EDGE",EDGE,{"disambiguationData":[OSD([sQuery(id+"F2.wireOp",EDGE,"E3.0.26.15")])],"isStart":false});
            var Q1810;
            Q1810=makeQuery(id+"F3.opExtrude","CAP_EDGE",EDGE,{"disambiguationData":[OSD([sQuery(id+"F2.wireOp",EDGE,"E2.13.15.0")])],"isStart":false});
            var Q1811;
            Q1811=makeQuery(id+"F3.opExtrude","CAP_EDGE",EDGE,{"disambiguationData":[OSD([sQuery(id+"F2.wireOp",EDGE,"E3.0.20.15")])],"isStart":false});
            var Q1812;
            Q1812=makeQuery(id+"F3.opExtrude","CAP_EDGE",EDGE,{"disambiguationData":[OSD([sQuery(id+"F2.wireOp",EDGE,"E2.7.15.0")])],"isStart":false});
            var Q1813;
            Q1813=makeQuery(id+"F3.opExtrude","CAP_EDGE",EDGE,{"disambiguationData":[OSD([sQuery(id+"F2.wireOp",EDGE,"E2.14.15.0")])],"isStart":false});
            var Q1814;
            Q1814=makeQuery(id+"F3.opExtrude","CAP_EDGE",EDGE,{"disambiguationData":[OSD([sQuery(id+"F2.wireOp",EDGE,"E2.1.15.0")])],"isStart":false});
            var Q1815;
            Q1815=makeQuery(id+"F3.opExtrude","CAP_EDGE",EDGE,{"disambiguationData":[OSD([sQuery(id+"F2.wireOp",EDGE,"E2.8.15.0")])],"isStart":false});
            var Q1816;
            Q1816=makeQuery(id+"F3.opExtrude","CAP_EDGE",EDGE,{"disambiguationData":[OSD([sQuery(id+"F2.wireOp",EDGE,"E3.0.27.15")])],"isStart":false});
            var Q1817;
            Q1817=makeQuery(id+"F3.opExtrude","CAP_EDGE",EDGE,{"disambiguationData":[OSD([sQuery(id+"F2.wireOp",EDGE,"E2.2.15.0")])],"isStart":false});
            var Q1818;
            Q1818=makeQuery(id+"F3.opExtrude","CAP_EDGE",EDGE,{"disambiguationData":[OSD([sQuery(id+"F2.wireOp",EDGE,"E3.0.21.15")])],"isStart":false});
            var Q1819;
            Q1819=makeQuery(id+"F3.opExtrude","CAP_EDGE",EDGE,{"disambiguationData":[OSD([sQuery(id+"F2.wireOp",EDGE,"E2.15.15.0")])],"isStart":false});
            var Q1820;
            Q1820=makeQuery(id+"F3.opExtrude","CAP_EDGE",EDGE,{"disambiguationData":[OSD([sQuery(id+"F2.wireOp",EDGE,"E2.4.15.0")])],"isStart":false});
            var Q1821;
            Q1821=makeQuery(id+"F3.opExtrude","CAP_EDGE",EDGE,{"disambiguationData":[OSD([sQuery(id+"F2.wireOp",EDGE,"E3.0.23.15")])],"isStart":false});
            var Q1822;
            Q1822=makeQuery(id+"F3.opExtrude","CAP_EDGE",EDGE,{"disambiguationData":[OSD([sQuery(id+"F2.wireOp",EDGE,"E2.17.15.0")])],"isStart":false});
            var Q1823;
            Q1823=makeQuery(id+"F3.opExtrude","CAP_EDGE",EDGE,{"disambiguationData":[OSD([sQuery(id+"F2.wireOp",EDGE,"E3.0.24.15")])],"isStart":false});
            var Q1824;
            Q1824=makeQuery(id+"F3.opExtrude","CAP_EDGE",EDGE,{"disambiguationData":[OSD([sQuery(id+"F2.wireOp",EDGE,"E2.11.15.0")])],"isStart":false});
            var Q1825;
            Q1825=makeQuery(id+"F3.opExtrude","CAP_EDGE",EDGE,{"disambiguationData":[OSD([sQuery(id+"F2.wireOp",EDGE,"E2.18.15.0")])],"isStart":false});
            var Q1826;
            Q1826=makeQuery(id+"F3.opExtrude","CAP_EDGE",EDGE,{"disambiguationData":[OSD([sQuery(id+"F2.wireOp",EDGE,"E2.5.15.0")])],"isStart":false});
            var Q1827;
            Q1827=makeQuery(id+"F3.opExtrude","CAP_EDGE",EDGE,{"disambiguationData":[OSD([sQuery(id+"F2.wireOp",EDGE,"E3.0.25.15")])],"isStart":false});
            var Q1828;
            Q1828=makeQuery(id+"F3.opExtrude","CAP_EDGE",EDGE,{"disambiguationData":[OSD([sQuery(id+"F2.wireOp",EDGE,"E2.12.15.0")])],"isStart":false});
            var Q1829;
            Q1829=makeQuery(id+"F3.opExtrude","CAP_EDGE",EDGE,{"disambiguationData":[OSD([sQuery(id+"F2.wireOp",EDGE,"E2.6.15.0")])],"isStart":false});
            var Q1830;
            Q1830=makeQuery(id+"F3.opExtrude","CAP_EDGE",EDGE,{"disambiguationData":[OSD([sQuery(id+"F2.wireOp",EDGE,"E2.19.15.0")])],"isStart":false});
            var Q1831;
            Q1831=makeQuery(id+"F3.opExtrude","CAP_EDGE",EDGE,{"disambiguationData":[OSD([sQuery(id+"F2.wireOp",EDGE,"E2.18.15.2")])],"isStart":false});
            var Q1832;
            Q1832=makeQuery(id+"F3.opExtrude","CAP_EDGE",EDGE,{"disambiguationData":[OSD([sQuery(id+"F2.wireOp",EDGE,"E2.5.15.2")])],"isStart":false});
            var Q1833;
            Q1833=makeQuery(id+"F3.opExtrude","CAP_EDGE",EDGE,{"disambiguationData":[OSD([sQuery(id+"F2.wireOp",EDGE,"E2.12.15.2")])],"isStart":false});
            var Q1834;
            Q1834=makeQuery(id+"F3.opExtrude","CAP_EDGE",EDGE,{"disambiguationData":[OSD([sQuery(id+"F2.wireOp",EDGE,"E3.6.25.15")])],"isStart":false});
            var Q1835;
            Q1835=makeQuery(id+"F3.opExtrude","CAP_EDGE",EDGE,{"disambiguationData":[OSD([sQuery(id+"F2.wireOp",EDGE,"E2.6.15.2")])],"isStart":false});
            var Q1836;
            Q1836=makeQuery(id+"F3.opExtrude","CAP_EDGE",EDGE,{"disambiguationData":[OSD([sQuery(id+"F2.wireOp",EDGE,"E2.19.15.2")])],"isStart":false});
            var Q1837;
            Q1837=makeQuery(id+"F3.opExtrude","CAP_EDGE",EDGE,{"disambiguationData":[OSD([sQuery(id+"F2.wireOp",EDGE,"E3.6.26.15")])],"isStart":false});
            var Q1838;
            Q1838=makeQuery(id+"F3.opExtrude","CAP_EDGE",EDGE,{"disambiguationData":[OSD([sQuery(id+"F2.wireOp",EDGE,"E2.13.15.2")])],"isStart":false});
            var Q1839;
            Q1839=makeQuery(id+"F3.opExtrude","CAP_EDGE",EDGE,{"disambiguationData":[OSD([sQuery(id+"F2.wireOp",EDGE,"E3.6.20.15")])],"isStart":false});
            var Q1840;
            Q1840=makeQuery(id+"F3.opExtrude","CAP_EDGE",EDGE,{"disambiguationData":[OSD([sQuery(id+"F2.wireOp",EDGE,"E2.7.15.2")])],"isStart":false});
            var Q1841;
            Q1841=makeQuery(id+"F3.opExtrude","CAP_EDGE",EDGE,{"disambiguationData":[OSD([sQuery(id+"F2.wireOp",EDGE,"E2.14.15.2")])],"isStart":false});
            var Q1842;
            Q1842=makeQuery(id+"F3.opExtrude","CAP_EDGE",EDGE,{"disambiguationData":[OSD([sQuery(id+"F2.wireOp",EDGE,"E2.1.15.2")])],"isStart":false});
            var Q1843;
            Q1843=makeQuery(id+"F3.opExtrude","CAP_EDGE",EDGE,{"disambiguationData":[OSD([sQuery(id+"F2.wireOp",EDGE,"E3.6.28.15")])],"isStart":false});
            var Q1844;
            Q1844=makeQuery(id+"F3.opExtrude","CAP_EDGE",EDGE,{"disambiguationData":[OSD([sQuery(id+"F2.wireOp",EDGE,"E3.6.29.15")])],"isStart":false});
            var Q1845;
            Q1845=makeQuery(id+"F3.opExtrude","CAP_EDGE",EDGE,{"disambiguationData":[OSD([sQuery(id+"F2.wireOp",EDGE,"E3.6.22.15")])],"isStart":false});
            var Q1846;
            Q1846=makeQuery(id+"F3.opExtrude","CAP_EDGE",EDGE,{"disambiguationData":[OSD([sQuery(id+"F2.wireOp",EDGE,"E2.3.15.2")])],"isStart":false});
            var Q1847;
            Q1847=makeQuery(id+"F3.opExtrude","CAP_EDGE",EDGE,{"disambiguationData":[OSD([sQuery(id+"F2.wireOp",EDGE,"E2.9.15.2")])],"isStart":false});
            var Q1848;
            Q1848=makeQuery(id+"F3.opExtrude","CAP_EDGE",EDGE,{"disambiguationData":[OSD([sQuery(id+"F2.wireOp",EDGE,"E2.16.15.2")])],"isStart":false});
            var Q1849;
            Q1849=makeQuery(id+"F3.opExtrude","CAP_EDGE",EDGE,{"disambiguationData":[OSD([sQuery(id+"F2.wireOp",EDGE,"E2.0.15.1")])],"isStart":false});
            var Q1850;
            Q1850=makeQuery(id+"F3.opExtrude","CAP_EDGE",EDGE,{"disambiguationData":[OSD([sQuery(id+"F2.wireOp",EDGE,"E2.10.15.2")])],"isStart":false});
            var Q1851;
            Q1851=makeQuery(id+"F3.opExtrude","CAP_EDGE",EDGE,{"disambiguationData":[OSD([sQuery(id+"F2.wireOp",EDGE,"E2.4.15.2")])],"isStart":false});
            var Q1852;
            Q1852=makeQuery(id+"F3.opExtrude","CAP_EDGE",EDGE,{"disambiguationData":[OSD([sQuery(id+"F2.wireOp",EDGE,"E3.6.23.15")])],"isStart":false});
            var Q1853;
            Q1853=makeQuery(id+"F3.opExtrude","CAP_EDGE",EDGE,{"disambiguationData":[OSD([sQuery(id+"F2.wireOp",EDGE,"E2.17.15.2")])],"isStart":false});
            var Q1854;
            Q1854=makeQuery(id+"F3.opExtrude","CAP_EDGE",EDGE,{"disambiguationData":[OSD([sQuery(id+"F2.wireOp",EDGE,"E3.6.24.15")])],"isStart":false});
            var Q1855;
            Q1855=makeQuery(id+"F3.opExtrude","CAP_EDGE",EDGE,{"disambiguationData":[OSD([sQuery(id+"F2.wireOp",EDGE,"E2.11.15.2")])],"isStart":false});
            var Q1856;
            Q1856=makeQuery(id+"F3.opExtrude","CAP_EDGE",EDGE,{"disambiguationData":[OSD([sQuery(id+"F2.wireOp",EDGE,"E2.8.15.2")])],"isStart":false});
            var Q1857;
            Q1857=makeQuery(id+"F3.opExtrude","CAP_EDGE",EDGE,{"disambiguationData":[OSD([sQuery(id+"F2.wireOp",EDGE,"E3.6.27.15")])],"isStart":false});
            var Q1858;
            Q1858=makeQuery(id+"F3.opExtrude","CAP_EDGE",EDGE,{"disambiguationData":[OSD([sQuery(id+"F2.wireOp",EDGE,"E2.2.15.2")])],"isStart":false});
            var Q1859;
            Q1859=makeQuery(id+"F3.opExtrude","CAP_EDGE",EDGE,{"disambiguationData":[OSD([sQuery(id+"F2.wireOp",EDGE,"E3.6.21.15")])],"isStart":false});
            var Q1860;
            Q1860=makeQuery(id+"F3.opExtrude","CAP_EDGE",EDGE,{"disambiguationData":[OSD([sQuery(id+"F2.wireOp",EDGE,"E2.15.15.2")])],"isStart":false});
            var Q1861;
            Q1861=makeQuery(id+"F3.opExtrude","CAP_EDGE",EDGE,{"disambiguationData":[OSD([sQuery(id+"F2.wireOp",EDGE,"E2.0.15.3")])],"isStart":false});
            var Q1862;
            Q1862=makeQuery(id+"F3.opExtrude","CAP_EDGE",EDGE,{"disambiguationData":[OSD([sQuery(id+"F2.wireOp",EDGE,"E3.3.22.15")])],"isStart":false});
            var Q1863;
            Q1863=makeQuery(id+"F3.opExtrude","CAP_EDGE",EDGE,{"disambiguationData":[OSD([sQuery(id+"F2.wireOp",EDGE,"E2.9.15.1")])],"isStart":false});
            var Q1864;
            Q1864=makeQuery(id+"F3.opExtrude","CAP_EDGE",EDGE,{"disambiguationData":[OSD([sQuery(id+"F2.wireOp",EDGE,"E2.16.15.1")])],"isStart":false});
            var Q1865;
            Q1865=makeQuery(id+"F3.opExtrude","CAP_EDGE",EDGE,{"disambiguationData":[OSD([sQuery(id+"F2.wireOp",EDGE,"E2.3.15.1")])],"isStart":false});
            var Q1866;
            Q1866=makeQuery(id+"F3.opExtrude","CAP_EDGE",EDGE,{"disambiguationData":[OSD([sQuery(id+"F2.wireOp",EDGE,"E2.10.15.1")])],"isStart":false});
            var Q1867;
            Q1867=makeQuery(id+"F3.opExtrude","CAP_EDGE",EDGE,{"disambiguationData":[OSD([sQuery(id+"F2.wireOp",EDGE,"E2.4.15.1")])],"isStart":false});
            var Q1868;
            Q1868=makeQuery(id+"F3.opExtrude","CAP_EDGE",EDGE,{"disambiguationData":[OSD([sQuery(id+"F2.wireOp",EDGE,"E3.3.23.15")])],"isStart":false});
            var Q1869;
            Q1869=makeQuery(id+"F3.opExtrude","CAP_EDGE",EDGE,{"disambiguationData":[OSD([sQuery(id+"F2.wireOp",EDGE,"E2.17.15.1")])],"isStart":false});
            var Q1870;
            Q1870=makeQuery(id+"F3.opExtrude","CAP_EDGE",EDGE,{"disambiguationData":[OSD([sQuery(id+"F2.wireOp",EDGE,"E3.3.24.15")])],"isStart":false});
            var Q1871;
            Q1871=makeQuery(id+"F3.opExtrude","CAP_EDGE",EDGE,{"disambiguationData":[OSD([sQuery(id+"F2.wireOp",EDGE,"E2.11.15.1")])],"isStart":false});
            var Q1872;
            Q1872=makeQuery(id+"F3.opExtrude","CAP_EDGE",EDGE,{"disambiguationData":[OSD([sQuery(id+"F2.wireOp",EDGE,"E2.18.15.1")])],"isStart":false});
            var Q1873;
            Q1873=makeQuery(id+"F3.opExtrude","CAP_EDGE",EDGE,{"disambiguationData":[OSD([sQuery(id+"F2.wireOp",EDGE,"E2.5.15.1")])],"isStart":false});
            var Q1874;
            Q1874=makeQuery(id+"F3.opExtrude","CAP_EDGE",EDGE,{"disambiguationData":[OSD([sQuery(id+"F2.wireOp",EDGE,"E3.3.28.15")])],"isStart":false});
            var Q1875;
            Q1875=makeQuery(id+"F3.opExtrude","CAP_EDGE",EDGE,{"disambiguationData":[OSD([sQuery(id+"F2.wireOp",EDGE,"E3.3.29.15")])],"isStart":false});
            var Q1876;
            Q1876=makeQuery(id+"F3.opExtrude","CAP_EDGE",EDGE,{"disambiguationData":[OSD([sQuery(id+"F2.wireOp",EDGE,"E2.2.15.1")])],"isStart":false});
            var Q1877;
            Q1877=makeQuery(id+"F3.opExtrude","CAP_EDGE",EDGE,{"disambiguationData":[OSD([sQuery(id+"F2.wireOp",EDGE,"E3.3.21.15")])],"isStart":false});
            var Q1878;
            Q1878=makeQuery(id+"F3.opExtrude","CAP_EDGE",EDGE,{"disambiguationData":[OSD([sQuery(id+"F2.wireOp",EDGE,"E2.15.15.1")])],"isStart":false});
            var Q1879;
            Q1879=makeQuery(id+"F3.opExtrude","CAP_EDGE",EDGE,{"disambiguationData":[OSD([sQuery(id+"F2.wireOp",EDGE,"E2.12.15.1")])],"isStart":false});
            var Q1880;
            Q1880=makeQuery(id+"F3.opExtrude","CAP_EDGE",EDGE,{"disambiguationData":[OSD([sQuery(id+"F2.wireOp",EDGE,"E3.3.25.15")])],"isStart":false});
            var Q1881;
            Q1881=makeQuery(id+"F3.opExtrude","CAP_EDGE",EDGE,{"disambiguationData":[OSD([sQuery(id+"F2.wireOp",EDGE,"E2.6.15.1")])],"isStart":false});
            var Q1882;
            Q1882=makeQuery(id+"F3.opExtrude","CAP_EDGE",EDGE,{"disambiguationData":[OSD([sQuery(id+"F2.wireOp",EDGE,"E2.19.15.1")])],"isStart":false});
            var Q1883;
            Q1883=makeQuery(id+"F3.opExtrude","CAP_EDGE",EDGE,{"disambiguationData":[OSD([sQuery(id+"F2.wireOp",EDGE,"E3.3.26.15")])],"isStart":false});
            var Q1884;
            Q1884=makeQuery(id+"F3.opExtrude","CAP_EDGE",EDGE,{"disambiguationData":[OSD([sQuery(id+"F2.wireOp",EDGE,"E2.13.15.1")])],"isStart":false});
            var Q1885;
            Q1885=makeQuery(id+"F3.opExtrude","CAP_EDGE",EDGE,{"disambiguationData":[OSD([sQuery(id+"F2.wireOp",EDGE,"E3.3.20.15")])],"isStart":false});
            var Q1886;
            Q1886=makeQuery(id+"F3.opExtrude","CAP_EDGE",EDGE,{"disambiguationData":[OSD([sQuery(id+"F2.wireOp",EDGE,"E2.7.15.1")])],"isStart":false});
            var Q1887;
            Q1887=makeQuery(id+"F3.opExtrude","CAP_EDGE",EDGE,{"disambiguationData":[OSD([sQuery(id+"F2.wireOp",EDGE,"E2.14.15.1")])],"isStart":false});
            var Q1888;
            Q1888=makeQuery(id+"F3.opExtrude","CAP_EDGE",EDGE,{"disambiguationData":[OSD([sQuery(id+"F2.wireOp",EDGE,"E2.1.15.1")])],"isStart":false});
            var Q1889;
            Q1889=makeQuery(id+"F3.opExtrude","CAP_EDGE",EDGE,{"disambiguationData":[OSD([sQuery(id+"F2.wireOp",EDGE,"E2.8.15.1")])],"isStart":false});
            var Q1890;
            Q1890=makeQuery(id+"F3.opExtrude","CAP_EDGE",EDGE,{"disambiguationData":[OSD([sQuery(id+"F2.wireOp",EDGE,"E3.3.27.15")])],"isStart":false});
            var Q1891;
            Q1891=makeQuery(id+"F3.opExtrude","CAP_EDGE",EDGE,{"disambiguationData":[OSD([sQuery(id+"F2.wireOp",EDGE,"E3.9.28.15")])],"isStart":false});
            var Q1892;
            Q1892=makeQuery(id+"F3.opExtrude","CAP_EDGE",EDGE,{"disambiguationData":[OSD([sQuery(id+"F2.wireOp",EDGE,"E3.9.29.15")])],"isStart":false});
            var Q1893;
            Q1893=makeQuery(id+"F3.opExtrude","CAP_EDGE",EDGE,{"disambiguationData":[OSD([sQuery(id+"F2.wireOp",EDGE,"E3.9.22.15")])],"isStart":false});
            var Q1894;
            Q1894=makeQuery(id+"F3.opExtrude","CAP_EDGE",EDGE,{"disambiguationData":[OSD([sQuery(id+"F2.wireOp",EDGE,"E2.9.15.3")])],"isStart":false});
            var Q1895;
            Q1895=makeQuery(id+"F3.opExtrude","CAP_EDGE",EDGE,{"disambiguationData":[OSD([sQuery(id+"F2.wireOp",EDGE,"E2.16.15.3")])],"isStart":false});
            var Q1896;
            Q1896=makeQuery(id+"F3.opExtrude","CAP_EDGE",EDGE,{"disambiguationData":[OSD([sQuery(id+"F2.wireOp",EDGE,"E2.3.15.3")])],"isStart":false});
            var Q1897;
            Q1897=makeQuery(id+"F3.opExtrude","CAP_EDGE",EDGE,{"disambiguationData":[OSD([sQuery(id+"F2.wireOp",EDGE,"E2.19.15.3")])],"isStart":false});
            var Q1898;
            Q1898=makeQuery(id+"F3.opExtrude","CAP_EDGE",EDGE,{"disambiguationData":[OSD([sQuery(id+"F2.wireOp",EDGE,"E3.9.26.15")])],"isStart":false});
            var Q1899;
            Q1899=makeQuery(id+"F3.opExtrude","CAP_EDGE",EDGE,{"disambiguationData":[OSD([sQuery(id+"F2.wireOp",EDGE,"E2.13.15.3")])],"isStart":false});
            var Q1900;
            Q1900=makeQuery(id+"F3.opExtrude","CAP_EDGE",EDGE,{"disambiguationData":[OSD([sQuery(id+"F2.wireOp",EDGE,"E3.9.20.15")])],"isStart":false});
            var Q1901;
            Q1901=makeQuery(id+"F3.opExtrude","CAP_EDGE",EDGE,{"disambiguationData":[OSD([sQuery(id+"F2.wireOp",EDGE,"E2.7.15.3")])],"isStart":false});
            var Q1902;
            Q1902=makeQuery(id+"F3.opExtrude","CAP_EDGE",EDGE,{"disambiguationData":[OSD([sQuery(id+"F2.wireOp",EDGE,"E2.14.15.3")])],"isStart":false});
            var Q1903;
            Q1903=makeQuery(id+"F3.opExtrude","CAP_EDGE",EDGE,{"disambiguationData":[OSD([sQuery(id+"F2.wireOp",EDGE,"E2.1.15.3")])],"isStart":false});
            var Q1904;
            Q1904=makeQuery(id+"F3.opExtrude","CAP_EDGE",EDGE,{"disambiguationData":[OSD([sQuery(id+"F2.wireOp",EDGE,"E2.8.15.3")])],"isStart":false});
            var Q1905;
            Q1905=makeQuery(id+"F3.opExtrude","CAP_EDGE",EDGE,{"disambiguationData":[OSD([sQuery(id+"F2.wireOp",EDGE,"E3.9.27.15")])],"isStart":false});
            var Q1906;
            Q1906=makeQuery(id+"F3.opExtrude","CAP_EDGE",EDGE,{"disambiguationData":[OSD([sQuery(id+"F2.wireOp",EDGE,"E2.2.15.3")])],"isStart":false});
            var Q1907;
            Q1907=makeQuery(id+"F3.opExtrude","CAP_EDGE",EDGE,{"disambiguationData":[OSD([sQuery(id+"F2.wireOp",EDGE,"E3.9.21.15")])],"isStart":false});
            var Q1908;
            Q1908=makeQuery(id+"F3.opExtrude","CAP_EDGE",EDGE,{"disambiguationData":[OSD([sQuery(id+"F2.wireOp",EDGE,"E2.15.15.3")])],"isStart":false});
            var Q1909;
            Q1909=makeQuery(id+"F3.opExtrude","CAP_EDGE",EDGE,{"disambiguationData":[OSD([sQuery(id+"F2.wireOp",EDGE,"E2.10.15.3")])],"isStart":false});
            var Q1910;
            Q1910=makeQuery(id+"F3.opExtrude","CAP_EDGE",EDGE,{"disambiguationData":[OSD([sQuery(id+"F2.wireOp",EDGE,"E2.4.15.3")])],"isStart":false});
            var Q1911;
            Q1911=makeQuery(id+"F3.opExtrude","CAP_EDGE",EDGE,{"disambiguationData":[OSD([sQuery(id+"F2.wireOp",EDGE,"E3.9.23.15")])],"isStart":false});
            var Q1912;
            Q1912=makeQuery(id+"F3.opExtrude","CAP_EDGE",EDGE,{"disambiguationData":[OSD([sQuery(id+"F2.wireOp",EDGE,"E2.17.15.3")])],"isStart":false});
            var Q1913;
            Q1913=makeQuery(id+"F3.opExtrude","CAP_EDGE",EDGE,{"disambiguationData":[OSD([sQuery(id+"F2.wireOp",EDGE,"E3.9.24.15")])],"isStart":false});
            var Q1914;
            Q1914=makeQuery(id+"F3.opExtrude","CAP_EDGE",EDGE,{"disambiguationData":[OSD([sQuery(id+"F2.wireOp",EDGE,"E2.11.15.3")])],"isStart":false});
            var Q1915;
            Q1915=makeQuery(id+"F3.opExtrude","CAP_EDGE",EDGE,{"disambiguationData":[OSD([sQuery(id+"F2.wireOp",EDGE,"E2.18.15.3")])],"isStart":false});
            var Q1916;
            Q1916=makeQuery(id+"F3.opExtrude","CAP_EDGE",EDGE,{"disambiguationData":[OSD([sQuery(id+"F2.wireOp",EDGE,"E2.5.15.3")])],"isStart":false});
            var Q1917;
            Q1917=makeQuery(id+"F3.opExtrude","CAP_EDGE",EDGE,{"disambiguationData":[OSD([sQuery(id+"F2.wireOp",EDGE,"E2.12.15.3")])],"isStart":false});
            var Q1918;
            Q1918=makeQuery(id+"F3.opExtrude","CAP_EDGE",EDGE,{"disambiguationData":[OSD([sQuery(id+"F2.wireOp",EDGE,"E2.6.15.3")])],"isStart":false});
            var Q1919;
            Q1919=makeQuery(id+"F3.opExtrude","CAP_EDGE",EDGE,{"disambiguationData":[OSD([sQuery(id+"F2.wireOp",EDGE,"E3.9.25.15")])],"isStart":false});
            var Q1920;
            Q1920=makeQuery(id+"F3.opExtrude","CAP_EDGE",EDGE,{"disambiguationData":[OSD([sQuery(id+"F2.wireOp",EDGE,"E2.0.16.3")])],"isStart":false});
            var Q1921;
            Q1921=makeQuery(id+"F3.opExtrude","CAP_EDGE",EDGE,{"disambiguationData":[OSD([sQuery(id+"F2.wireOp",EDGE,"E2.0.16.0")])],"isStart":false});
            var Q1922;
            Q1922=makeQuery(id+"F3.opExtrude","CAP_EDGE",EDGE,{"disambiguationData":[OSD([sQuery(id+"F2.wireOp",EDGE,"E2.0.16.2")])],"isStart":false});
            var Q1923;
            Q1923=makeQuery(id+"F3.opExtrude","CAP_EDGE",EDGE,{"disambiguationData":[OSD([sQuery(id+"F2.wireOp",EDGE,"E2.16.16.3")])],"isStart":false});
            var Q1924;
            Q1924=makeQuery(id+"F3.opExtrude","CAP_EDGE",EDGE,{"disambiguationData":[OSD([sQuery(id+"F2.wireOp",EDGE,"E3.9.28.16")])],"isStart":false});
            var Q1925;
            Q1925=makeQuery(id+"F3.opExtrude","CAP_EDGE",EDGE,{"disambiguationData":[OSD([sQuery(id+"F2.wireOp",EDGE,"E2.15.16.3")])],"isStart":false});
            var Q1926;
            Q1926=makeQuery(id+"F3.opExtrude","CAP_EDGE",EDGE,{"disambiguationData":[OSD([sQuery(id+"F2.wireOp",EDGE,"E2.12.16.3")])],"isStart":false});
            var Q1927;
            Q1927=makeQuery(id+"F3.opExtrude","CAP_EDGE",EDGE,{"disambiguationData":[OSD([sQuery(id+"F2.wireOp",EDGE,"E3.9.25.16")])],"isStart":false});
            var Q1928;
            Q1928=makeQuery(id+"F3.opExtrude","CAP_EDGE",EDGE,{"disambiguationData":[OSD([sQuery(id+"F2.wireOp",EDGE,"E2.19.16.3")])],"isStart":false});
            var Q1929;
            Q1929=makeQuery(id+"F3.opExtrude","CAP_EDGE",EDGE,{"disambiguationData":[OSD([sQuery(id+"F2.wireOp",EDGE,"E2.6.16.3")])],"isStart":false});
            var Q1930;
            Q1930=makeQuery(id+"F3.opExtrude","CAP_EDGE",EDGE,{"disambiguationData":[OSD([sQuery(id+"F2.wireOp",EDGE,"E2.13.16.3")])],"isStart":false});
            var Q1931;
            Q1931=makeQuery(id+"F3.opExtrude","CAP_EDGE",EDGE,{"disambiguationData":[OSD([sQuery(id+"F2.wireOp",EDGE,"E3.9.20.16")])],"isStart":false});
            var Q1932;
            Q1932=makeQuery(id+"F3.opExtrude","CAP_EDGE",EDGE,{"disambiguationData":[OSD([sQuery(id+"F2.wireOp",EDGE,"E3.9.26.16")])],"isStart":false});
            var Q1933;
            Q1933=makeQuery(id+"F3.opExtrude","CAP_EDGE",EDGE,{"disambiguationData":[OSD([sQuery(id+"F2.wireOp",EDGE,"E2.7.16.3")])],"isStart":false});
            var Q1934;
            Q1934=makeQuery(id+"F3.opExtrude","CAP_EDGE",EDGE,{"disambiguationData":[OSD([sQuery(id+"F2.wireOp",EDGE,"E2.14.16.3")])],"isStart":false});
            var Q1935;
            Q1935=makeQuery(id+"F3.opExtrude","CAP_EDGE",EDGE,{"disambiguationData":[OSD([sQuery(id+"F2.wireOp",EDGE,"E2.1.16.3")])],"isStart":false});
            var Q1936;
            Q1936=makeQuery(id+"F3.opExtrude","CAP_EDGE",EDGE,{"disambiguationData":[OSD([sQuery(id+"F2.wireOp",EDGE,"E2.8.16.3")])],"isStart":false});
            var Q1937;
            Q1937=makeQuery(id+"F3.opExtrude","CAP_EDGE",EDGE,{"disambiguationData":[OSD([sQuery(id+"F2.wireOp",EDGE,"E3.9.27.16")])],"isStart":false});
            var Q1938;
            Q1938=makeQuery(id+"F3.opExtrude","CAP_EDGE",EDGE,{"disambiguationData":[OSD([sQuery(id+"F2.wireOp",EDGE,"E3.9.22.16")])],"isStart":false});
            var Q1939;
            Q1939=makeQuery(id+"F3.opExtrude","CAP_EDGE",EDGE,{"disambiguationData":[OSD([sQuery(id+"F2.wireOp",EDGE,"E2.9.16.3")])],"isStart":false});
            var Q1940;
            Q1940=makeQuery(id+"F3.opExtrude","CAP_EDGE",EDGE,{"disambiguationData":[OSD([sQuery(id+"F2.wireOp",EDGE,"E2.3.16.3")])],"isStart":false});
            var Q1941;
            Q1941=makeQuery(id+"F3.opExtrude","CAP_EDGE",EDGE,{"disambiguationData":[OSD([sQuery(id+"F2.wireOp",EDGE,"E2.10.16.3")])],"isStart":false});
            var Q1942;
            Q1942=makeQuery(id+"F3.opExtrude","CAP_EDGE",EDGE,{"disambiguationData":[OSD([sQuery(id+"F2.wireOp",EDGE,"E3.9.29.16")])],"isStart":false});
            var Q1943;
            Q1943=makeQuery(id+"F3.opExtrude","CAP_EDGE",EDGE,{"disambiguationData":[OSD([sQuery(id+"F2.wireOp",EDGE,"E2.4.16.3")])],"isStart":false});
            var Q1944;
            Q1944=makeQuery(id+"F3.opExtrude","CAP_EDGE",EDGE,{"disambiguationData":[OSD([sQuery(id+"F2.wireOp",EDGE,"E3.9.23.16")])],"isStart":false});
            var Q1945;
            Q1945=makeQuery(id+"F3.opExtrude","CAP_EDGE",EDGE,{"disambiguationData":[OSD([sQuery(id+"F2.wireOp",EDGE,"E2.17.16.3")])],"isStart":false});
            var Q1946;
            Q1946=makeQuery(id+"F3.opExtrude","CAP_EDGE",EDGE,{"disambiguationData":[OSD([sQuery(id+"F2.wireOp",EDGE,"E3.9.24.16")])],"isStart":false});
            var Q1947;
            Q1947=makeQuery(id+"F3.opExtrude","CAP_EDGE",EDGE,{"disambiguationData":[OSD([sQuery(id+"F2.wireOp",EDGE,"E2.11.16.3")])],"isStart":false});
            var Q1948;
            Q1948=makeQuery(id+"F3.opExtrude","CAP_EDGE",EDGE,{"disambiguationData":[OSD([sQuery(id+"F2.wireOp",EDGE,"E2.18.16.3")])],"isStart":false});
            var Q1949;
            Q1949=makeQuery(id+"F3.opExtrude","CAP_EDGE",EDGE,{"disambiguationData":[OSD([sQuery(id+"F2.wireOp",EDGE,"E2.5.16.3")])],"isStart":false});
            var Q1950;
            Q1950=makeQuery(id+"F3.opExtrude","CAP_EDGE",EDGE,{"disambiguationData":[OSD([sQuery(id+"F2.wireOp",EDGE,"E2.16.16.0")])],"isStart":false});
            var Q1951;
            Q1951=makeQuery(id+"F3.opExtrude","CAP_EDGE",EDGE,{"disambiguationData":[OSD([sQuery(id+"F2.wireOp",EDGE,"E2.15.16.0")])],"isStart":false});
            var Q1952;
            Q1952=makeQuery(id+"F3.opExtrude","CAP_EDGE",EDGE,{"disambiguationData":[OSD([sQuery(id+"F2.wireOp",EDGE,"E2.9.16.0")])],"isStart":false});
            var Q1953;
            Q1953=makeQuery(id+"F3.opExtrude","CAP_EDGE",EDGE,{"disambiguationData":[OSD([sQuery(id+"F2.wireOp",EDGE,"E3.0.28.16")])],"isStart":false});
            var Q1954;
            Q1954=makeQuery(id+"F3.opExtrude","CAP_EDGE",EDGE,{"disambiguationData":[OSD([sQuery(id+"F2.wireOp",EDGE,"E2.3.16.0")])],"isStart":false});
            var Q1955;
            Q1955=makeQuery(id+"F3.opExtrude","CAP_EDGE",EDGE,{"disambiguationData":[OSD([sQuery(id+"F2.wireOp",EDGE,"E3.0.22.16")])],"isStart":false});
            var Q1956;
            Q1956=makeQuery(id+"F3.opExtrude","CAP_EDGE",EDGE,{"disambiguationData":[OSD([sQuery(id+"F2.wireOp",EDGE,"E2.2.16.3")])],"isStart":false});
            var Q1957;
            Q1957=makeQuery(id+"F3.opExtrude","CAP_EDGE",EDGE,{"disambiguationData":[OSD([sQuery(id+"F2.wireOp",EDGE,"E3.9.21.16")])],"isStart":false});
            var Q1958;
            Q1958=makeQuery(id+"F3.opExtrude","CAP_EDGE",EDGE,{"disambiguationData":[OSD([sQuery(id+"F2.wireOp",EDGE,"E2.6.16.0")])],"isStart":false});
            var Q1959;
            Q1959=makeQuery(id+"F3.opExtrude","CAP_EDGE",EDGE,{"disambiguationData":[OSD([sQuery(id+"F2.wireOp",EDGE,"E2.19.16.0")])],"isStart":false});
            var Q1960;
            Q1960=makeQuery(id+"F3.opExtrude","CAP_EDGE",EDGE,{"disambiguationData":[OSD([sQuery(id+"F2.wireOp",EDGE,"E3.0.26.16")])],"isStart":false});
            var Q1961;
            Q1961=makeQuery(id+"F3.opExtrude","CAP_EDGE",EDGE,{"disambiguationData":[OSD([sQuery(id+"F2.wireOp",EDGE,"E2.13.16.0")])],"isStart":false});
            var Q1962;
            Q1962=makeQuery(id+"F3.opExtrude","CAP_EDGE",EDGE,{"disambiguationData":[OSD([sQuery(id+"F2.wireOp",EDGE,"E3.0.20.16")])],"isStart":false});
            var Q1963;
            Q1963=makeQuery(id+"F3.opExtrude","CAP_EDGE",EDGE,{"disambiguationData":[OSD([sQuery(id+"F2.wireOp",EDGE,"E2.7.16.0")])],"isStart":false});
            var Q1964;
            Q1964=makeQuery(id+"F3.opExtrude","CAP_EDGE",EDGE,{"disambiguationData":[OSD([sQuery(id+"F2.wireOp",EDGE,"E2.14.16.0")])],"isStart":false});
            var Q1965;
            Q1965=makeQuery(id+"F3.opExtrude","CAP_EDGE",EDGE,{"disambiguationData":[OSD([sQuery(id+"F2.wireOp",EDGE,"E2.1.16.0")])],"isStart":false});
            var Q1966;
            Q1966=makeQuery(id+"F3.opExtrude","CAP_EDGE",EDGE,{"disambiguationData":[OSD([sQuery(id+"F2.wireOp",EDGE,"E2.8.16.0")])],"isStart":false});
            var Q1967;
            Q1967=makeQuery(id+"F3.opExtrude","CAP_EDGE",EDGE,{"disambiguationData":[OSD([sQuery(id+"F2.wireOp",EDGE,"E3.0.27.16")])],"isStart":false});
            var Q1968;
            Q1968=makeQuery(id+"F3.opExtrude","CAP_EDGE",EDGE,{"disambiguationData":[OSD([sQuery(id+"F2.wireOp",EDGE,"E2.2.16.0")])],"isStart":false});
            var Q1969;
            Q1969=makeQuery(id+"F3.opExtrude","CAP_EDGE",EDGE,{"disambiguationData":[OSD([sQuery(id+"F2.wireOp",EDGE,"E3.0.21.16")])],"isStart":false});
            var Q1970;
            Q1970=makeQuery(id+"F3.opExtrude","CAP_EDGE",EDGE,{"disambiguationData":[OSD([sQuery(id+"F2.wireOp",EDGE,"E2.10.16.0")])],"isStart":false});
            var Q1971;
            Q1971=makeQuery(id+"F3.opExtrude","CAP_EDGE",EDGE,{"disambiguationData":[OSD([sQuery(id+"F2.wireOp",EDGE,"E3.0.29.16")])],"isStart":false});
            var Q1972;
            Q1972=makeQuery(id+"F3.opExtrude","CAP_EDGE",EDGE,{"disambiguationData":[OSD([sQuery(id+"F2.wireOp",EDGE,"E2.4.16.0")])],"isStart":false});
            var Q1973;
            Q1973=makeQuery(id+"F3.opExtrude","CAP_EDGE",EDGE,{"disambiguationData":[OSD([sQuery(id+"F2.wireOp",EDGE,"E3.0.23.16")])],"isStart":false});
            var Q1974;
            Q1974=makeQuery(id+"F3.opExtrude","CAP_EDGE",EDGE,{"disambiguationData":[OSD([sQuery(id+"F2.wireOp",EDGE,"E2.11.16.0")])],"isStart":false});
            var Q1975;
            Q1975=makeQuery(id+"F3.opExtrude","CAP_EDGE",EDGE,{"disambiguationData":[OSD([sQuery(id+"F2.wireOp",EDGE,"E2.17.16.0")])],"isStart":false});
            var Q1976;
            Q1976=makeQuery(id+"F3.opExtrude","CAP_EDGE",EDGE,{"disambiguationData":[OSD([sQuery(id+"F2.wireOp",EDGE,"E2.5.16.0")])],"isStart":false});
            var Q1977;
            Q1977=makeQuery(id+"F3.opExtrude","CAP_EDGE",EDGE,{"disambiguationData":[OSD([sQuery(id+"F2.wireOp",EDGE,"E3.0.24.16")])],"isStart":false});
            var Q1978;
            Q1978=makeQuery(id+"F3.opExtrude","CAP_EDGE",EDGE,{"disambiguationData":[OSD([sQuery(id+"F2.wireOp",EDGE,"E2.18.16.0")])],"isStart":false});
            var Q1979;
            Q1979=makeQuery(id+"F3.opExtrude","CAP_EDGE",EDGE,{"disambiguationData":[OSD([sQuery(id+"F2.wireOp",EDGE,"E3.0.25.16")])],"isStart":false});
            var Q1980;
            Q1980=makeQuery(id+"F3.opExtrude","CAP_EDGE",EDGE,{"disambiguationData":[OSD([sQuery(id+"F2.wireOp",EDGE,"E2.12.16.0")])],"isStart":false});
            var Q1981;
            Q1981=makeQuery(id+"F3.opExtrude","CAP_EDGE",EDGE,{"disambiguationData":[OSD([sQuery(id+"F2.wireOp",EDGE,"E2.0.16.1")])],"isStart":false});
            var Q1982;
            Q1982=makeQuery(id+"F3.opExtrude","CAP_EDGE",EDGE,{"disambiguationData":[OSD([sQuery(id+"F2.wireOp",EDGE,"E2.3.16.2")])],"isStart":false});
            var Q1983;
            Q1983=makeQuery(id+"F3.opExtrude","CAP_EDGE",EDGE,{"disambiguationData":[OSD([sQuery(id+"F2.wireOp",EDGE,"E2.10.16.2")])],"isStart":false});
            var Q1984;
            Q1984=makeQuery(id+"F3.opExtrude","CAP_EDGE",EDGE,{"disambiguationData":[OSD([sQuery(id+"F2.wireOp",EDGE,"E3.6.29.16")])],"isStart":false});
            var Q1985;
            Q1985=makeQuery(id+"F3.opExtrude","CAP_EDGE",EDGE,{"disambiguationData":[OSD([sQuery(id+"F2.wireOp",EDGE,"E2.4.16.2")])],"isStart":false});
            var Q1986;
            Q1986=makeQuery(id+"F3.opExtrude","CAP_EDGE",EDGE,{"disambiguationData":[OSD([sQuery(id+"F2.wireOp",EDGE,"E3.6.23.16")])],"isStart":false});
            var Q1987;
            Q1987=makeQuery(id+"F3.opExtrude","CAP_EDGE",EDGE,{"disambiguationData":[OSD([sQuery(id+"F2.wireOp",EDGE,"E2.17.16.2")])],"isStart":false});
            var Q1988;
            Q1988=makeQuery(id+"F3.opExtrude","CAP_EDGE",EDGE,{"disambiguationData":[OSD([sQuery(id+"F2.wireOp",EDGE,"E3.6.24.16")])],"isStart":false});
            var Q1989;
            Q1989=makeQuery(id+"F3.opExtrude","CAP_EDGE",EDGE,{"disambiguationData":[OSD([sQuery(id+"F2.wireOp",EDGE,"E2.11.16.2")])],"isStart":false});
            var Q1990;
            Q1990=makeQuery(id+"F3.opExtrude","CAP_EDGE",EDGE,{"disambiguationData":[OSD([sQuery(id+"F2.wireOp",EDGE,"E2.18.16.2")])],"isStart":false});
            var Q1991;
            Q1991=makeQuery(id+"F3.opExtrude","CAP_EDGE",EDGE,{"disambiguationData":[OSD([sQuery(id+"F2.wireOp",EDGE,"E2.5.16.2")])],"isStart":false});
            var Q1992;
            Q1992=makeQuery(id+"F3.opExtrude","CAP_EDGE",EDGE,{"disambiguationData":[OSD([sQuery(id+"F2.wireOp",EDGE,"E2.12.16.2")])],"isStart":false});
            var Q1993;
            Q1993=makeQuery(id+"F3.opExtrude","CAP_EDGE",EDGE,{"disambiguationData":[OSD([sQuery(id+"F2.wireOp",EDGE,"E2.16.16.2")])],"isStart":false});
            var Q1994;
            Q1994=makeQuery(id+"F3.opExtrude","CAP_EDGE",EDGE,{"disambiguationData":[OSD([sQuery(id+"F2.wireOp",EDGE,"E3.6.28.16")])],"isStart":false});
            var Q1995;
            Q1995=makeQuery(id+"F3.opExtrude","CAP_EDGE",EDGE,{"disambiguationData":[OSD([sQuery(id+"F2.wireOp",EDGE,"E2.15.16.2")])],"isStart":false});
            var Q1996;
            Q1996=makeQuery(id+"F3.opExtrude","CAP_EDGE",EDGE,{"disambiguationData":[OSD([sQuery(id+"F2.wireOp",EDGE,"E3.6.22.16")])],"isStart":false});
            var Q1997;
            Q1997=makeQuery(id+"F3.opExtrude","CAP_EDGE",EDGE,{"disambiguationData":[OSD([sQuery(id+"F2.wireOp",EDGE,"E2.9.16.2")])],"isStart":false});
            var Q1998;
            Q1998=makeQuery(id+"F3.opExtrude","CAP_EDGE",EDGE,{"disambiguationData":[OSD([sQuery(id+"F2.wireOp",EDGE,"E3.6.25.16")])],"isStart":false});
            var Q1999;
            Q1999=makeQuery(id+"F3.opExtrude","CAP_EDGE",EDGE,{"disambiguationData":[OSD([sQuery(id+"F2.wireOp",EDGE,"E2.6.16.2")])],"isStart":false});
            var Q2000;
            Q2000=makeQuery(id+"F3.opExtrude","CAP_EDGE",EDGE,{"disambiguationData":[OSD([sQuery(id+"F2.wireOp",EDGE,"E2.19.16.2")])],"isStart":false});
            var Q2001;
            Q2001=makeQuery(id+"F3.opExtrude","CAP_EDGE",EDGE,{"disambiguationData":[OSD([sQuery(id+"F2.wireOp",EDGE,"E3.6.26.16")])],"isStart":false});
            var Q2002;
            Q2002=makeQuery(id+"F3.opExtrude","CAP_EDGE",EDGE,{"disambiguationData":[OSD([sQuery(id+"F2.wireOp",EDGE,"E2.13.16.2")])],"isStart":false});
            var Q2003;
            Q2003=makeQuery(id+"F3.opExtrude","CAP_EDGE",EDGE,{"disambiguationData":[OSD([sQuery(id+"F2.wireOp",EDGE,"E3.6.20.16")])],"isStart":false});
            var Q2004;
            Q2004=makeQuery(id+"F3.opExtrude","CAP_EDGE",EDGE,{"disambiguationData":[OSD([sQuery(id+"F2.wireOp",EDGE,"E2.7.16.2")])],"isStart":false});
            var Q2005;
            Q2005=makeQuery(id+"F3.opExtrude","CAP_EDGE",EDGE,{"disambiguationData":[OSD([sQuery(id+"F2.wireOp",EDGE,"E2.14.16.2")])],"isStart":false});
            var Q2006;
            Q2006=makeQuery(id+"F3.opExtrude","CAP_EDGE",EDGE,{"disambiguationData":[OSD([sQuery(id+"F2.wireOp",EDGE,"E2.1.16.2")])],"isStart":false});
            var Q2007;
            Q2007=makeQuery(id+"F3.opExtrude","CAP_EDGE",EDGE,{"disambiguationData":[OSD([sQuery(id+"F2.wireOp",EDGE,"E2.8.16.2")])],"isStart":false});
            var Q2008;
            Q2008=makeQuery(id+"F3.opExtrude","CAP_EDGE",EDGE,{"disambiguationData":[OSD([sQuery(id+"F2.wireOp",EDGE,"E3.6.27.16")])],"isStart":false});
            var Q2009;
            Q2009=makeQuery(id+"F3.opExtrude","CAP_EDGE",EDGE,{"disambiguationData":[OSD([sQuery(id+"F2.wireOp",EDGE,"E2.2.16.2")])],"isStart":false});
            var Q2010;
            Q2010=makeQuery(id+"F3.opExtrude","CAP_EDGE",EDGE,{"disambiguationData":[OSD([sQuery(id+"F2.wireOp",EDGE,"E3.6.21.16")])],"isStart":false});
            var Q2011;
            Q2011=makeQuery(id+"F3.opExtrude","CAP_EDGE",EDGE,{"disambiguationData":[OSD([sQuery(id+"F2.wireOp",EDGE,"E2.16.16.1")])],"isStart":false});
            var Q2012;
            Q2012=makeQuery(id+"F3.opExtrude","CAP_EDGE",EDGE,{"disambiguationData":[OSD([sQuery(id+"F2.wireOp",EDGE,"E3.3.28.16")])],"isStart":false});
            var Q2013;
            Q2013=makeQuery(id+"F3.opExtrude","CAP_EDGE",EDGE,{"disambiguationData":[OSD([sQuery(id+"F2.wireOp",EDGE,"E2.9.16.1")])],"isStart":false});
            var Q2014;
            Q2014=makeQuery(id+"F3.opExtrude","CAP_EDGE",EDGE,{"disambiguationData":[OSD([sQuery(id+"F2.wireOp",EDGE,"E2.15.16.1")])],"isStart":false});
            var Q2015;
            Q2015=makeQuery(id+"F3.opExtrude","CAP_EDGE",EDGE,{"disambiguationData":[OSD([sQuery(id+"F2.wireOp",EDGE,"E2.3.16.1")])],"isStart":false});
            var Q2016;
            Q2016=makeQuery(id+"F3.opExtrude","CAP_EDGE",EDGE,{"disambiguationData":[OSD([sQuery(id+"F2.wireOp",EDGE,"E3.3.22.16")])],"isStart":false});
            var Q2017;
            Q2017=makeQuery(id+"F3.opExtrude","CAP_EDGE",EDGE,{"disambiguationData":[OSD([sQuery(id+"F2.wireOp",EDGE,"E2.10.16.1")])],"isStart":false});
            var Q2018;
            Q2018=makeQuery(id+"F3.opExtrude","CAP_EDGE",EDGE,{"disambiguationData":[OSD([sQuery(id+"F2.wireOp",EDGE,"E3.3.29.16")])],"isStart":false});
            var Q2019;
            Q2019=makeQuery(id+"F3.opExtrude","CAP_EDGE",EDGE,{"disambiguationData":[OSD([sQuery(id+"F2.wireOp",EDGE,"E2.4.16.1")])],"isStart":false});
            var Q2020;
            Q2020=makeQuery(id+"F3.opExtrude","CAP_EDGE",EDGE,{"disambiguationData":[OSD([sQuery(id+"F2.wireOp",EDGE,"E3.3.23.16")])],"isStart":false});
            var Q2021;
            Q2021=makeQuery(id+"F3.opExtrude","CAP_EDGE",EDGE,{"disambiguationData":[OSD([sQuery(id+"F2.wireOp",EDGE,"E3.3.20.16")])],"isStart":false});
            var Q2022;
            Q2022=makeQuery(id+"F3.opExtrude","CAP_EDGE",EDGE,{"disambiguationData":[OSD([sQuery(id+"F2.wireOp",EDGE,"E2.7.16.1")])],"isStart":false});
            var Q2023;
            Q2023=makeQuery(id+"F3.opExtrude","CAP_EDGE",EDGE,{"disambiguationData":[OSD([sQuery(id+"F2.wireOp",EDGE,"E2.14.16.1")])],"isStart":false});
            var Q2024;
            Q2024=makeQuery(id+"F3.opExtrude","CAP_EDGE",EDGE,{"disambiguationData":[OSD([sQuery(id+"F2.wireOp",EDGE,"E2.1.16.1")])],"isStart":false});
            var Q2025;
            Q2025=makeQuery(id+"F3.opExtrude","CAP_EDGE",EDGE,{"disambiguationData":[OSD([sQuery(id+"F2.wireOp",EDGE,"E2.8.16.1")])],"isStart":false});
            var Q2026;
            Q2026=makeQuery(id+"F3.opExtrude","CAP_EDGE",EDGE,{"disambiguationData":[OSD([sQuery(id+"F2.wireOp",EDGE,"E3.3.27.16")])],"isStart":false});
            var Q2027;
            Q2027=makeQuery(id+"F3.opExtrude","CAP_EDGE",EDGE,{"disambiguationData":[OSD([sQuery(id+"F2.wireOp",EDGE,"E2.2.16.1")])],"isStart":false});
            var Q2028;
            Q2028=makeQuery(id+"F3.opExtrude","CAP_EDGE",EDGE,{"disambiguationData":[OSD([sQuery(id+"F2.wireOp",EDGE,"E3.3.21.16")])],"isStart":false});
            var Q2029;
            Q2029=makeQuery(id+"F3.opExtrude","CAP_EDGE",EDGE,{"disambiguationData":[OSD([sQuery(id+"F2.wireOp",EDGE,"E2.17.16.1")])],"isStart":false});
            var Q2030;
            Q2030=makeQuery(id+"F3.opExtrude","CAP_EDGE",EDGE,{"disambiguationData":[OSD([sQuery(id+"F2.wireOp",EDGE,"E3.3.24.16")])],"isStart":false});
            var Q2031;
            Q2031=makeQuery(id+"F3.opExtrude","CAP_EDGE",EDGE,{"disambiguationData":[OSD([sQuery(id+"F2.wireOp",EDGE,"E2.11.16.1")])],"isStart":false});
            var Q2032;
            Q2032=makeQuery(id+"F3.opExtrude","CAP_EDGE",EDGE,{"disambiguationData":[OSD([sQuery(id+"F2.wireOp",EDGE,"E2.18.16.1")])],"isStart":false});
            var Q2033;
            Q2033=makeQuery(id+"F3.opExtrude","CAP_EDGE",EDGE,{"disambiguationData":[OSD([sQuery(id+"F2.wireOp",EDGE,"E2.5.16.1")])],"isStart":false});
            var Q2034;
            Q2034=makeQuery(id+"F3.opExtrude","CAP_EDGE",EDGE,{"disambiguationData":[OSD([sQuery(id+"F2.wireOp",EDGE,"E3.3.25.16")])],"isStart":false});
            var Q2035;
            Q2035=makeQuery(id+"F3.opExtrude","CAP_EDGE",EDGE,{"disambiguationData":[OSD([sQuery(id+"F2.wireOp",EDGE,"E2.12.16.1")])],"isStart":false});
            var Q2036;
            Q2036=makeQuery(id+"F3.opExtrude","CAP_EDGE",EDGE,{"disambiguationData":[OSD([sQuery(id+"F2.wireOp",EDGE,"E2.6.16.1")])],"isStart":false});
            var Q2037;
            Q2037=makeQuery(id+"F3.opExtrude","CAP_EDGE",EDGE,{"disambiguationData":[OSD([sQuery(id+"F2.wireOp",EDGE,"E2.19.16.1")])],"isStart":false});
            var Q2038;
            Q2038=makeQuery(id+"F3.opExtrude","CAP_EDGE",EDGE,{"disambiguationData":[OSD([sQuery(id+"F2.wireOp",EDGE,"E3.3.26.16")])],"isStart":false});
            var Q2039;
            Q2039=makeQuery(id+"F3.opExtrude","CAP_EDGE",EDGE,{"disambiguationData":[OSD([sQuery(id+"F2.wireOp",EDGE,"E2.13.16.1")])],"isStart":false});
            var Q2040;
            Q2040=makeQuery(id+"F3.opExtrude","CAP_EDGE",EDGE,{"disambiguationData":[OSD([sQuery(id+"F2.wireOp",EDGE,"E2.0.17.0")])],"isStart":false});
            var Q2041;
            Q2041=makeQuery(id+"F3.opExtrude","CAP_EDGE",EDGE,{"disambiguationData":[OSD([sQuery(id+"F2.wireOp",EDGE,"E2.0.17.2")])],"isStart":false});
            var Q2042;
            Q2042=makeQuery(id+"F3.opExtrude","CAP_EDGE",EDGE,{"disambiguationData":[OSD([sQuery(id+"F2.wireOp",EDGE,"E2.16.17.0")])],"isStart":false});
            var Q2043;
            Q2043=makeQuery(id+"F3.opExtrude","CAP_EDGE",EDGE,{"disambiguationData":[OSD([sQuery(id+"F2.wireOp",EDGE,"E3.0.28.17")])],"isStart":false});
            var Q2044;
            Q2044=makeQuery(id+"F3.opExtrude","CAP_EDGE",EDGE,{"disambiguationData":[OSD([sQuery(id+"F2.wireOp",EDGE,"E2.15.17.0")])],"isStart":false});
            var Q2045;
            Q2045=makeQuery(id+"F3.opExtrude","CAP_EDGE",EDGE,{"disambiguationData":[OSD([sQuery(id+"F2.wireOp",EDGE,"E3.0.22.17")])],"isStart":false});
            var Q2046;
            Q2046=makeQuery(id+"F3.opExtrude","CAP_EDGE",EDGE,{"disambiguationData":[OSD([sQuery(id+"F2.wireOp",EDGE,"E2.9.17.0")])],"isStart":false});
            var Q2047;
            Q2047=makeQuery(id+"F3.opExtrude","CAP_EDGE",EDGE,{"disambiguationData":[OSD([sQuery(id+"F2.wireOp",EDGE,"E2.3.17.0")])],"isStart":false});
            var Q2048;
            Q2048=makeQuery(id+"F3.opExtrude","CAP_EDGE",EDGE,{"disambiguationData":[OSD([sQuery(id+"F2.wireOp",EDGE,"E2.10.17.0")])],"isStart":false});
            var Q2049;
            Q2049=makeQuery(id+"F3.opExtrude","CAP_EDGE",EDGE,{"disambiguationData":[OSD([sQuery(id+"F2.wireOp",EDGE,"E3.0.29.17")])],"isStart":false});
            var Q2050;
            Q2050=makeQuery(id+"F3.opExtrude","CAP_EDGE",EDGE,{"disambiguationData":[OSD([sQuery(id+"F2.wireOp",EDGE,"E2.13.17.0")])],"isStart":false});
            var Q2051;
            Q2051=makeQuery(id+"F3.opExtrude","CAP_EDGE",EDGE,{"disambiguationData":[OSD([sQuery(id+"F2.wireOp",EDGE,"E2.7.17.0")])],"isStart":false});
            var Q2052;
            Q2052=makeQuery(id+"F3.opExtrude","CAP_EDGE",EDGE,{"disambiguationData":[OSD([sQuery(id+"F2.wireOp",EDGE,"E3.0.26.17")])],"isStart":false});
            var Q2053;
            Q2053=makeQuery(id+"F3.opExtrude","CAP_EDGE",EDGE,{"disambiguationData":[OSD([sQuery(id+"F2.wireOp",EDGE,"E2.1.17.0")])],"isStart":false});
            var Q2054;
            Q2054=makeQuery(id+"F3.opExtrude","CAP_EDGE",EDGE,{"disambiguationData":[OSD([sQuery(id+"F2.wireOp",EDGE,"E3.0.20.17")])],"isStart":false});
            var Q2055;
            Q2055=makeQuery(id+"F3.opExtrude","CAP_EDGE",EDGE,{"disambiguationData":[OSD([sQuery(id+"F2.wireOp",EDGE,"E3.0.27.17")])],"isStart":false});
            var Q2056;
            Q2056=makeQuery(id+"F3.opExtrude","CAP_EDGE",EDGE,{"disambiguationData":[OSD([sQuery(id+"F2.wireOp",EDGE,"E2.8.17.0")])],"isStart":false});
            var Q2057;
            Q2057=makeQuery(id+"F3.opExtrude","CAP_EDGE",EDGE,{"disambiguationData":[OSD([sQuery(id+"F2.wireOp",EDGE,"E2.14.17.0")])],"isStart":false});
            var Q2058;
            Q2058=makeQuery(id+"F3.opExtrude","CAP_EDGE",EDGE,{"disambiguationData":[OSD([sQuery(id+"F2.wireOp",EDGE,"E2.2.17.0")])],"isStart":false});
            var Q2059;
            Q2059=makeQuery(id+"F3.opExtrude","CAP_EDGE",EDGE,{"disambiguationData":[OSD([sQuery(id+"F2.wireOp",EDGE,"E3.0.21.17")])],"isStart":false});
            var Q2060;
            Q2060=makeQuery(id+"F3.opExtrude","CAP_EDGE",EDGE,{"disambiguationData":[OSD([sQuery(id+"F2.wireOp",EDGE,"E2.4.17.0")])],"isStart":false});
            var Q2061;
            Q2061=makeQuery(id+"F3.opExtrude","CAP_EDGE",EDGE,{"disambiguationData":[OSD([sQuery(id+"F2.wireOp",EDGE,"E3.0.23.17")])],"isStart":false});
            var Q2062;
            Q2062=makeQuery(id+"F3.opExtrude","CAP_EDGE",EDGE,{"disambiguationData":[OSD([sQuery(id+"F2.wireOp",EDGE,"E2.17.17.0")])],"isStart":false});
            var Q2063;
            Q2063=makeQuery(id+"F3.opExtrude","CAP_EDGE",EDGE,{"disambiguationData":[OSD([sQuery(id+"F2.wireOp",EDGE,"E3.0.24.17")])],"isStart":false});
            var Q2064;
            Q2064=makeQuery(id+"F3.opExtrude","CAP_EDGE",EDGE,{"disambiguationData":[OSD([sQuery(id+"F2.wireOp",EDGE,"E2.11.17.0")])],"isStart":false});
            var Q2065;
            Q2065=makeQuery(id+"F3.opExtrude","CAP_EDGE",EDGE,{"disambiguationData":[OSD([sQuery(id+"F2.wireOp",EDGE,"E2.18.17.0")])],"isStart":false});
            var Q2066;
            Q2066=makeQuery(id+"F3.opExtrude","CAP_EDGE",EDGE,{"disambiguationData":[OSD([sQuery(id+"F2.wireOp",EDGE,"E2.5.17.0")])],"isStart":false});
            var Q2067;
            Q2067=makeQuery(id+"F3.opExtrude","CAP_EDGE",EDGE,{"disambiguationData":[OSD([sQuery(id+"F2.wireOp",EDGE,"E2.12.17.0")])],"isStart":false});
            var Q2068;
            Q2068=makeQuery(id+"F3.opExtrude","CAP_EDGE",EDGE,{"disambiguationData":[OSD([sQuery(id+"F2.wireOp",EDGE,"E3.0.25.17")])],"isStart":false});
            var Q2069;
            Q2069=makeQuery(id+"F3.opExtrude","CAP_EDGE",EDGE,{"disambiguationData":[OSD([sQuery(id+"F2.wireOp",EDGE,"E2.19.17.0")])],"isStart":false});
            var Q2070;
            Q2070=makeQuery(id+"F3.opExtrude","CAP_EDGE",EDGE,{"disambiguationData":[OSD([sQuery(id+"F2.wireOp",EDGE,"E2.6.17.0")])],"isStart":false});
            var Q2071;
            Q2071=makeQuery(id+"F3.opExtrude","CAP_EDGE",EDGE,{"disambiguationData":[OSD([sQuery(id+"F2.wireOp",EDGE,"E2.16.17.2")])],"isStart":false});
            var Q2072;
            Q2072=makeQuery(id+"F3.opExtrude","CAP_EDGE",EDGE,{"disambiguationData":[OSD([sQuery(id+"F2.wireOp",EDGE,"E2.18.17.2")])],"isStart":false});
            var Q2073;
            Q2073=makeQuery(id+"F3.opExtrude","CAP_EDGE",EDGE,{"disambiguationData":[OSD([sQuery(id+"F2.wireOp",EDGE,"E2.5.17.2")])],"isStart":false});
            var Q2074;
            Q2074=makeQuery(id+"F3.opExtrude","CAP_EDGE",EDGE,{"disambiguationData":[OSD([sQuery(id+"F2.wireOp",EDGE,"E2.12.17.2")])],"isStart":false});
            var Q2075;
            Q2075=makeQuery(id+"F3.opExtrude","CAP_EDGE",EDGE,{"disambiguationData":[OSD([sQuery(id+"F2.wireOp",EDGE,"E3.6.25.17")])],"isStart":false});
            var Q2076;
            Q2076=makeQuery(id+"F3.opExtrude","CAP_EDGE",EDGE,{"disambiguationData":[OSD([sQuery(id+"F2.wireOp",EDGE,"E2.19.17.2")])],"isStart":false});
            var Q2077;
            Q2077=makeQuery(id+"F3.opExtrude","CAP_EDGE",EDGE,{"disambiguationData":[OSD([sQuery(id+"F2.wireOp",EDGE,"E2.6.17.2")])],"isStart":false});
            var Q2078;
            Q2078=makeQuery(id+"F3.opExtrude","CAP_EDGE",EDGE,{"disambiguationData":[OSD([sQuery(id+"F2.wireOp",EDGE,"E2.13.17.2")])],"isStart":false});
            var Q2079;
            Q2079=makeQuery(id+"F3.opExtrude","CAP_EDGE",EDGE,{"disambiguationData":[OSD([sQuery(id+"F2.wireOp",EDGE,"E2.7.17.2")])],"isStart":false});
            var Q2080;
            Q2080=makeQuery(id+"F3.opExtrude","CAP_EDGE",EDGE,{"disambiguationData":[OSD([sQuery(id+"F2.wireOp",EDGE,"E3.6.26.17")])],"isStart":false});
            var Q2081;
            Q2081=makeQuery(id+"F3.opExtrude","CAP_EDGE",EDGE,{"disambiguationData":[OSD([sQuery(id+"F2.wireOp",EDGE,"E2.1.17.2")])],"isStart":false});
            var Q2082;
            Q2082=makeQuery(id+"F3.opExtrude","CAP_EDGE",EDGE,{"disambiguationData":[OSD([sQuery(id+"F2.wireOp",EDGE,"E3.6.20.17")])],"isStart":false});
            var Q2083;
            Q2083=makeQuery(id+"F3.opExtrude","CAP_EDGE",EDGE,{"disambiguationData":[OSD([sQuery(id+"F2.wireOp",EDGE,"E3.6.28.17")])],"isStart":false});
            var Q2084;
            Q2084=makeQuery(id+"F3.opExtrude","CAP_EDGE",EDGE,{"disambiguationData":[OSD([sQuery(id+"F2.wireOp",EDGE,"E2.15.17.2")])],"isStart":false});
            var Q2085;
            Q2085=makeQuery(id+"F3.opExtrude","CAP_EDGE",EDGE,{"disambiguationData":[OSD([sQuery(id+"F2.wireOp",EDGE,"E3.6.22.17")])],"isStart":false});
            var Q2086;
            Q2086=makeQuery(id+"F3.opExtrude","CAP_EDGE",EDGE,{"disambiguationData":[OSD([sQuery(id+"F2.wireOp",EDGE,"E2.9.17.2")])],"isStart":false});
            var Q2087;
            Q2087=makeQuery(id+"F3.opExtrude","CAP_EDGE",EDGE,{"disambiguationData":[OSD([sQuery(id+"F2.wireOp",EDGE,"E2.3.17.2")])],"isStart":false});
            var Q2088;
            Q2088=makeQuery(id+"F3.opExtrude","CAP_EDGE",EDGE,{"disambiguationData":[OSD([sQuery(id+"F2.wireOp",EDGE,"E2.10.17.2")])],"isStart":false});
            var Q2089;
            Q2089=makeQuery(id+"F3.opExtrude","CAP_EDGE",EDGE,{"disambiguationData":[OSD([sQuery(id+"F2.wireOp",EDGE,"E2.0.17.1")])],"isStart":false});
            var Q2090;
            Q2090=makeQuery(id+"F3.opExtrude","CAP_EDGE",EDGE,{"disambiguationData":[OSD([sQuery(id+"F2.wireOp",EDGE,"E3.6.29.17")])],"isStart":false});
            var Q2091;
            Q2091=makeQuery(id+"F3.opExtrude","CAP_EDGE",EDGE,{"disambiguationData":[OSD([sQuery(id+"F2.wireOp",EDGE,"E2.4.17.2")])],"isStart":false});
            var Q2092;
            Q2092=makeQuery(id+"F3.opExtrude","CAP_EDGE",EDGE,{"disambiguationData":[OSD([sQuery(id+"F2.wireOp",EDGE,"E3.6.23.17")])],"isStart":false});
            var Q2093;
            Q2093=makeQuery(id+"F3.opExtrude","CAP_EDGE",EDGE,{"disambiguationData":[OSD([sQuery(id+"F2.wireOp",EDGE,"E2.17.17.2")])],"isStart":false});
            var Q2094;
            Q2094=makeQuery(id+"F3.opExtrude","CAP_EDGE",EDGE,{"disambiguationData":[OSD([sQuery(id+"F2.wireOp",EDGE,"E3.6.24.17")])],"isStart":false});
            var Q2095;
            Q2095=makeQuery(id+"F3.opExtrude","CAP_EDGE",EDGE,{"disambiguationData":[OSD([sQuery(id+"F2.wireOp",EDGE,"E2.11.17.2")])],"isStart":false});
            var Q2096;
            Q2096=makeQuery(id+"F3.opExtrude","CAP_EDGE",EDGE,{"disambiguationData":[OSD([sQuery(id+"F2.wireOp",EDGE,"E3.6.27.17")])],"isStart":false});
            var Q2097;
            Q2097=makeQuery(id+"F3.opExtrude","CAP_EDGE",EDGE,{"disambiguationData":[OSD([sQuery(id+"F2.wireOp",EDGE,"E2.14.17.2")])],"isStart":false});
            var Q2098;
            Q2098=makeQuery(id+"F3.opExtrude","CAP_EDGE",EDGE,{"disambiguationData":[OSD([sQuery(id+"F2.wireOp",EDGE,"E3.6.21.17")])],"isStart":false});
            var Q2099;
            Q2099=makeQuery(id+"F3.opExtrude","CAP_EDGE",EDGE,{"disambiguationData":[OSD([sQuery(id+"F2.wireOp",EDGE,"E2.2.17.2")])],"isStart":false});
            var Q2100;
            Q2100=makeQuery(id+"F3.opExtrude","CAP_EDGE",EDGE,{"disambiguationData":[OSD([sQuery(id+"F2.wireOp",EDGE,"E2.8.17.2")])],"isStart":false});
            var Q2101;
            Q2101=makeQuery(id+"F3.opExtrude","CAP_EDGE",EDGE,{"disambiguationData":[OSD([sQuery(id+"F2.wireOp",EDGE,"E2.0.17.3")])],"isStart":false});
            var Q2102;
            Q2102=makeQuery(id+"F3.opExtrude","CAP_EDGE",EDGE,{"disambiguationData":[OSD([sQuery(id+"F2.wireOp",EDGE,"E3.3.22.17")])],"isStart":false});
            var Q2103;
            Q2103=makeQuery(id+"F3.opExtrude","CAP_EDGE",EDGE,{"disambiguationData":[OSD([sQuery(id+"F2.wireOp",EDGE,"E2.9.17.1")])],"isStart":false});
            var Q2104;
            Q2104=makeQuery(id+"F3.opExtrude","CAP_EDGE",EDGE,{"disambiguationData":[OSD([sQuery(id+"F2.wireOp",EDGE,"E2.3.17.1")])],"isStart":false});
            var Q2105;
            Q2105=makeQuery(id+"F3.opExtrude","CAP_EDGE",EDGE,{"disambiguationData":[OSD([sQuery(id+"F2.wireOp",EDGE,"E2.10.17.1")])],"isStart":false});
            var Q2106;
            Q2106=makeQuery(id+"F3.opExtrude","CAP_EDGE",EDGE,{"disambiguationData":[OSD([sQuery(id+"F2.wireOp",EDGE,"E3.3.29.17")])],"isStart":false});
            var Q2107;
            Q2107=makeQuery(id+"F3.opExtrude","CAP_EDGE",EDGE,{"disambiguationData":[OSD([sQuery(id+"F2.wireOp",EDGE,"E2.4.17.1")])],"isStart":false});
            var Q2108;
            Q2108=makeQuery(id+"F3.opExtrude","CAP_EDGE",EDGE,{"disambiguationData":[OSD([sQuery(id+"F2.wireOp",EDGE,"E3.3.23.17")])],"isStart":false});
            var Q2109;
            Q2109=makeQuery(id+"F3.opExtrude","CAP_EDGE",EDGE,{"disambiguationData":[OSD([sQuery(id+"F2.wireOp",EDGE,"E2.17.17.1")])],"isStart":false});
            var Q2110;
            Q2110=makeQuery(id+"F3.opExtrude","CAP_EDGE",EDGE,{"disambiguationData":[OSD([sQuery(id+"F2.wireOp",EDGE,"E3.3.24.17")])],"isStart":false});
            var Q2111;
            Q2111=makeQuery(id+"F3.opExtrude","CAP_EDGE",EDGE,{"disambiguationData":[OSD([sQuery(id+"F2.wireOp",EDGE,"E2.11.17.1")])],"isStart":false});
            var Q2112;
            Q2112=makeQuery(id+"F3.opExtrude","CAP_EDGE",EDGE,{"disambiguationData":[OSD([sQuery(id+"F2.wireOp",EDGE,"E2.18.17.1")])],"isStart":false});
            var Q2113;
            Q2113=makeQuery(id+"F3.opExtrude","CAP_EDGE",EDGE,{"disambiguationData":[OSD([sQuery(id+"F2.wireOp",EDGE,"E2.5.17.1")])],"isStart":false});
            var Q2114;
            Q2114=makeQuery(id+"F3.opExtrude","CAP_EDGE",EDGE,{"disambiguationData":[OSD([sQuery(id+"F2.wireOp",EDGE,"E2.16.17.1")])],"isStart":false});
            var Q2115;
            Q2115=makeQuery(id+"F3.opExtrude","CAP_EDGE",EDGE,{"disambiguationData":[OSD([sQuery(id+"F2.wireOp",EDGE,"E3.3.28.17")])],"isStart":false});
            var Q2116;
            Q2116=makeQuery(id+"F3.opExtrude","CAP_EDGE",EDGE,{"disambiguationData":[OSD([sQuery(id+"F2.wireOp",EDGE,"E2.15.17.1")])],"isStart":false});
            var Q2117;
            Q2117=makeQuery(id+"F3.opExtrude","CAP_EDGE",EDGE,{"disambiguationData":[OSD([sQuery(id+"F2.wireOp",EDGE,"E3.3.21.17")])],"isStart":false});
            var Q2118;
            Q2118=makeQuery(id+"F3.opExtrude","CAP_EDGE",EDGE,{"disambiguationData":[OSD([sQuery(id+"F2.wireOp",EDGE,"E2.2.17.1")])],"isStart":false});
            var Q2119;
            Q2119=makeQuery(id+"F3.opExtrude","CAP_EDGE",EDGE,{"disambiguationData":[OSD([sQuery(id+"F2.wireOp",EDGE,"E2.8.17.1")])],"isStart":false});
            var Q2120;
            Q2120=makeQuery(id+"F3.opExtrude","CAP_EDGE",EDGE,{"disambiguationData":[OSD([sQuery(id+"F2.wireOp",EDGE,"E2.12.17.1")])],"isStart":false});
            var Q2121;
            Q2121=makeQuery(id+"F3.opExtrude","CAP_EDGE",EDGE,{"disambiguationData":[OSD([sQuery(id+"F2.wireOp",EDGE,"E3.3.25.17")])],"isStart":false});
            var Q2122;
            Q2122=makeQuery(id+"F3.opExtrude","CAP_EDGE",EDGE,{"disambiguationData":[OSD([sQuery(id+"F2.wireOp",EDGE,"E2.19.17.1")])],"isStart":false});
            var Q2123;
            Q2123=makeQuery(id+"F3.opExtrude","CAP_EDGE",EDGE,{"disambiguationData":[OSD([sQuery(id+"F2.wireOp",EDGE,"E2.6.17.1")])],"isStart":false});
            var Q2124;
            Q2124=makeQuery(id+"F3.opExtrude","CAP_EDGE",EDGE,{"disambiguationData":[OSD([sQuery(id+"F2.wireOp",EDGE,"E2.13.17.1")])],"isStart":false});
            var Q2125;
            Q2125=makeQuery(id+"F3.opExtrude","CAP_EDGE",EDGE,{"disambiguationData":[OSD([sQuery(id+"F2.wireOp",EDGE,"E2.7.17.1")])],"isStart":false});
            var Q2126;
            Q2126=makeQuery(id+"F3.opExtrude","CAP_EDGE",EDGE,{"disambiguationData":[OSD([sQuery(id+"F2.wireOp",EDGE,"E3.3.26.17")])],"isStart":false});
            var Q2127;
            Q2127=makeQuery(id+"F3.opExtrude","CAP_EDGE",EDGE,{"disambiguationData":[OSD([sQuery(id+"F2.wireOp",EDGE,"E2.1.17.1")])],"isStart":false});
            var Q2128;
            Q2128=makeQuery(id+"F3.opExtrude","CAP_EDGE",EDGE,{"disambiguationData":[OSD([sQuery(id+"F2.wireOp",EDGE,"E3.3.20.17")])],"isStart":false});
            var Q2129;
            Q2129=makeQuery(id+"F3.opExtrude","CAP_EDGE",EDGE,{"disambiguationData":[OSD([sQuery(id+"F2.wireOp",EDGE,"E3.3.27.17")])],"isStart":false});
            var Q2130;
            Q2130=makeQuery(id+"F3.opExtrude","CAP_EDGE",EDGE,{"disambiguationData":[OSD([sQuery(id+"F2.wireOp",EDGE,"E2.14.17.1")])],"isStart":false});
            var Q2131;
            Q2131=makeQuery(id+"F3.opExtrude","CAP_EDGE",EDGE,{"disambiguationData":[OSD([sQuery(id+"F2.wireOp",EDGE,"E2.16.17.3")])],"isStart":false});
            var Q2132;
            Q2132=makeQuery(id+"F3.opExtrude","CAP_EDGE",EDGE,{"disambiguationData":[OSD([sQuery(id+"F2.wireOp",EDGE,"E3.9.28.17")])],"isStart":false});
            var Q2133;
            Q2133=makeQuery(id+"F3.opExtrude","CAP_EDGE",EDGE,{"disambiguationData":[OSD([sQuery(id+"F2.wireOp",EDGE,"E2.15.17.3")])],"isStart":false});
            var Q2134;
            Q2134=makeQuery(id+"F3.opExtrude","CAP_EDGE",EDGE,{"disambiguationData":[OSD([sQuery(id+"F2.wireOp",EDGE,"E3.9.22.17")])],"isStart":false});
            var Q2135;
            Q2135=makeQuery(id+"F3.opExtrude","CAP_EDGE",EDGE,{"disambiguationData":[OSD([sQuery(id+"F2.wireOp",EDGE,"E2.9.17.3")])],"isStart":false});
            var Q2136;
            Q2136=makeQuery(id+"F3.opExtrude","CAP_EDGE",EDGE,{"disambiguationData":[OSD([sQuery(id+"F2.wireOp",EDGE,"E2.3.17.3")])],"isStart":false});
            var Q2137;
            Q2137=makeQuery(id+"F3.opExtrude","CAP_EDGE",EDGE,{"disambiguationData":[OSD([sQuery(id+"F2.wireOp",EDGE,"E2.19.17.3")])],"isStart":false});
            var Q2138;
            Q2138=makeQuery(id+"F3.opExtrude","CAP_EDGE",EDGE,{"disambiguationData":[OSD([sQuery(id+"F2.wireOp",EDGE,"E2.6.17.3")])],"isStart":false});
            var Q2139;
            Q2139=makeQuery(id+"F3.opExtrude","CAP_EDGE",EDGE,{"disambiguationData":[OSD([sQuery(id+"F2.wireOp",EDGE,"E2.13.17.3")])],"isStart":false});
            var Q2140;
            Q2140=makeQuery(id+"F3.opExtrude","CAP_EDGE",EDGE,{"disambiguationData":[OSD([sQuery(id+"F2.wireOp",EDGE,"E2.7.17.3")])],"isStart":false});
            var Q2141;
            Q2141=makeQuery(id+"F3.opExtrude","CAP_EDGE",EDGE,{"disambiguationData":[OSD([sQuery(id+"F2.wireOp",EDGE,"E3.9.26.17")])],"isStart":false});
            var Q2142;
            Q2142=makeQuery(id+"F3.opExtrude","CAP_EDGE",EDGE,{"disambiguationData":[OSD([sQuery(id+"F2.wireOp",EDGE,"E2.1.17.3")])],"isStart":false});
            var Q2143;
            Q2143=makeQuery(id+"F3.opExtrude","CAP_EDGE",EDGE,{"disambiguationData":[OSD([sQuery(id+"F2.wireOp",EDGE,"E3.9.20.17")])],"isStart":false});
            var Q2144;
            Q2144=makeQuery(id+"F3.opExtrude","CAP_EDGE",EDGE,{"disambiguationData":[OSD([sQuery(id+"F2.wireOp",EDGE,"E3.9.27.17")])],"isStart":false});
            var Q2145;
            Q2145=makeQuery(id+"F3.opExtrude","CAP_EDGE",EDGE,{"disambiguationData":[OSD([sQuery(id+"F2.wireOp",EDGE,"E2.14.17.3")])],"isStart":false});
            var Q2146;
            Q2146=makeQuery(id+"F3.opExtrude","CAP_EDGE",EDGE,{"disambiguationData":[OSD([sQuery(id+"F2.wireOp",EDGE,"E3.9.21.17")])],"isStart":false});
            var Q2147;
            Q2147=makeQuery(id+"F3.opExtrude","CAP_EDGE",EDGE,{"disambiguationData":[OSD([sQuery(id+"F2.wireOp",EDGE,"E2.8.17.3")])],"isStart":false});
            var Q2148;
            Q2148=makeQuery(id+"F3.opExtrude","CAP_EDGE",EDGE,{"disambiguationData":[OSD([sQuery(id+"F2.wireOp",EDGE,"E2.2.17.3")])],"isStart":false});
            var Q2149;
            Q2149=makeQuery(id+"F3.opExtrude","CAP_EDGE",EDGE,{"disambiguationData":[OSD([sQuery(id+"F2.wireOp",EDGE,"E3.9.29.17")])],"isStart":false});
            var Q2150;
            Q2150=makeQuery(id+"F3.opExtrude","CAP_EDGE",EDGE,{"disambiguationData":[OSD([sQuery(id+"F2.wireOp",EDGE,"E2.10.17.3")])],"isStart":false});
            var Q2151;
            Q2151=makeQuery(id+"F3.opExtrude","CAP_EDGE",EDGE,{"disambiguationData":[OSD([sQuery(id+"F2.wireOp",EDGE,"E2.4.17.3")])],"isStart":false});
            var Q2152;
            Q2152=makeQuery(id+"F3.opExtrude","CAP_EDGE",EDGE,{"disambiguationData":[OSD([sQuery(id+"F2.wireOp",EDGE,"E3.9.23.17")])],"isStart":false});
            var Q2153;
            Q2153=makeQuery(id+"F3.opExtrude","CAP_EDGE",EDGE,{"disambiguationData":[OSD([sQuery(id+"F2.wireOp",EDGE,"E2.17.17.3")])],"isStart":false});
            var Q2154;
            Q2154=makeQuery(id+"F3.opExtrude","CAP_EDGE",EDGE,{"disambiguationData":[OSD([sQuery(id+"F2.wireOp",EDGE,"E3.9.24.17")])],"isStart":false});
            var Q2155;
            Q2155=makeQuery(id+"F3.opExtrude","CAP_EDGE",EDGE,{"disambiguationData":[OSD([sQuery(id+"F2.wireOp",EDGE,"E2.11.17.3")])],"isStart":false});
            var Q2156;
            Q2156=makeQuery(id+"F3.opExtrude","CAP_EDGE",EDGE,{"disambiguationData":[OSD([sQuery(id+"F2.wireOp",EDGE,"E2.18.17.3")])],"isStart":false});
            var Q2157;
            Q2157=makeQuery(id+"F3.opExtrude","CAP_EDGE",EDGE,{"disambiguationData":[OSD([sQuery(id+"F2.wireOp",EDGE,"E2.5.17.3")])],"isStart":false});
            var Q2158;
            Q2158=makeQuery(id+"F3.opExtrude","CAP_EDGE",EDGE,{"disambiguationData":[OSD([sQuery(id+"F2.wireOp",EDGE,"E2.12.17.3")])],"isStart":false});
            var Q2159;
            Q2159=makeQuery(id+"F3.opExtrude","CAP_EDGE",EDGE,{"disambiguationData":[OSD([sQuery(id+"F2.wireOp",EDGE,"E3.9.25.17")])],"isStart":false});
            var Q2160;
            Q2160=makeQuery(id+"F3.opExtrude","CAP_EDGE",EDGE,{"disambiguationData":[OSD([sQuery(id+"F2.wireOp",EDGE,"E2.0.18.3")])],"isStart":false});
            var Q2161;
            Q2161=makeQuery(id+"F3.opExtrude","CAP_EDGE",EDGE,{"disambiguationData":[OSD([sQuery(id+"F2.wireOp",EDGE,"E2.0.18.0")])],"isStart":false});
            var Q2162;
            Q2162=makeQuery(id+"F3.opExtrude","CAP_EDGE",EDGE,{"disambiguationData":[OSD([sQuery(id+"F2.wireOp",EDGE,"E2.0.18.2")])],"isStart":false});
            var Q2163;
            Q2163=makeQuery(id+"F3.opExtrude","CAP_EDGE",EDGE,{"disambiguationData":[OSD([sQuery(id+"F2.wireOp",EDGE,"E2.16.18.3")])],"isStart":false});
            var Q2164;
            Q2164=makeQuery(id+"F3.opExtrude","CAP_EDGE",EDGE,{"disambiguationData":[OSD([sQuery(id+"F2.wireOp",EDGE,"E3.9.28.18")])],"isStart":false});
            var Q2165;
            Q2165=makeQuery(id+"F3.opExtrude","CAP_EDGE",EDGE,{"disambiguationData":[OSD([sQuery(id+"F2.wireOp",EDGE,"E2.15.18.3")])],"isStart":false});
            var Q2166;
            Q2166=makeQuery(id+"F3.opExtrude","CAP_EDGE",EDGE,{"disambiguationData":[OSD([sQuery(id+"F2.wireOp",EDGE,"E2.12.18.3")])],"isStart":false});
            var Q2167;
            Q2167=makeQuery(id+"F3.opExtrude","CAP_EDGE",EDGE,{"disambiguationData":[OSD([sQuery(id+"F2.wireOp",EDGE,"E3.9.25.18")])],"isStart":false});
            var Q2168;
            Q2168=makeQuery(id+"F3.opExtrude","CAP_EDGE",EDGE,{"disambiguationData":[OSD([sQuery(id+"F2.wireOp",EDGE,"E2.19.18.3")])],"isStart":false});
            var Q2169;
            Q2169=makeQuery(id+"F3.opExtrude","CAP_EDGE",EDGE,{"disambiguationData":[OSD([sQuery(id+"F2.wireOp",EDGE,"E2.6.18.3")])],"isStart":false});
            var Q2170;
            Q2170=makeQuery(id+"F3.opExtrude","CAP_EDGE",EDGE,{"disambiguationData":[OSD([sQuery(id+"F2.wireOp",EDGE,"E2.13.18.3")])],"isStart":false});
            var Q2171;
            Q2171=makeQuery(id+"F3.opExtrude","CAP_EDGE",EDGE,{"disambiguationData":[OSD([sQuery(id+"F2.wireOp",EDGE,"E2.7.18.3")])],"isStart":false});
            var Q2172;
            Q2172=makeQuery(id+"F3.opExtrude","CAP_EDGE",EDGE,{"disambiguationData":[OSD([sQuery(id+"F2.wireOp",EDGE,"E3.9.26.18")])],"isStart":false});
            var Q2173;
            Q2173=makeQuery(id+"F3.opExtrude","CAP_EDGE",EDGE,{"disambiguationData":[OSD([sQuery(id+"F2.wireOp",EDGE,"E2.1.18.3")])],"isStart":false});
            var Q2174;
            Q2174=makeQuery(id+"F3.opExtrude","CAP_EDGE",EDGE,{"disambiguationData":[OSD([sQuery(id+"F2.wireOp",EDGE,"E3.9.20.18")])],"isStart":false});
            var Q2175;
            Q2175=makeQuery(id+"F3.opExtrude","CAP_EDGE",EDGE,{"disambiguationData":[OSD([sQuery(id+"F2.wireOp",EDGE,"E3.9.27.18")])],"isStart":false});
            var Q2176;
            Q2176=makeQuery(id+"F3.opExtrude","CAP_EDGE",EDGE,{"disambiguationData":[OSD([sQuery(id+"F2.wireOp",EDGE,"E2.14.18.3")])],"isStart":false});
            var Q2177;
            Q2177=makeQuery(id+"F3.opExtrude","CAP_EDGE",EDGE,{"disambiguationData":[OSD([sQuery(id+"F2.wireOp",EDGE,"E3.9.22.18")])],"isStart":false});
            var Q2178;
            Q2178=makeQuery(id+"F3.opExtrude","CAP_EDGE",EDGE,{"disambiguationData":[OSD([sQuery(id+"F2.wireOp",EDGE,"E2.9.18.3")])],"isStart":false});
            var Q2179;
            Q2179=makeQuery(id+"F3.opExtrude","CAP_EDGE",EDGE,{"disambiguationData":[OSD([sQuery(id+"F2.wireOp",EDGE,"E2.3.18.3")])],"isStart":false});
            var Q2180;
            Q2180=makeQuery(id+"F3.opExtrude","CAP_EDGE",EDGE,{"disambiguationData":[OSD([sQuery(id+"F2.wireOp",EDGE,"E3.9.29.18")])],"isStart":false});
            var Q2181;
            Q2181=makeQuery(id+"F3.opExtrude","CAP_EDGE",EDGE,{"disambiguationData":[OSD([sQuery(id+"F2.wireOp",EDGE,"E3.9.23.18")])],"isStart":false});
            var Q2182;
            Q2182=makeQuery(id+"F3.opExtrude","CAP_EDGE",EDGE,{"disambiguationData":[OSD([sQuery(id+"F2.wireOp",EDGE,"E2.10.18.3")])],"isStart":false});
            var Q2183;
            Q2183=makeQuery(id+"F3.opExtrude","CAP_EDGE",EDGE,{"disambiguationData":[OSD([sQuery(id+"F2.wireOp",EDGE,"E2.17.18.3")])],"isStart":false});
            var Q2184;
            Q2184=makeQuery(id+"F3.opExtrude","CAP_EDGE",EDGE,{"disambiguationData":[OSD([sQuery(id+"F2.wireOp",EDGE,"E2.4.18.3")])],"isStart":false});
            var Q2185;
            Q2185=makeQuery(id+"F3.opExtrude","CAP_EDGE",EDGE,{"disambiguationData":[OSD([sQuery(id+"F2.wireOp",EDGE,"E3.9.24.18")])],"isStart":false});
            var Q2186;
            Q2186=makeQuery(id+"F3.opExtrude","CAP_EDGE",EDGE,{"disambiguationData":[OSD([sQuery(id+"F2.wireOp",EDGE,"E2.11.18.3")])],"isStart":false});
            var Q2187;
            Q2187=makeQuery(id+"F3.opExtrude","CAP_EDGE",EDGE,{"disambiguationData":[OSD([sQuery(id+"F2.wireOp",EDGE,"E2.18.18.3")])],"isStart":false});
            var Q2188;
            Q2188=makeQuery(id+"F3.opExtrude","CAP_EDGE",EDGE,{"disambiguationData":[OSD([sQuery(id+"F2.wireOp",EDGE,"E2.5.18.3")])],"isStart":false});
            var Q2189;
            Q2189=makeQuery(id+"F3.opExtrude","CAP_EDGE",EDGE,{"disambiguationData":[OSD([sQuery(id+"F2.wireOp",EDGE,"E2.16.18.0")])],"isStart":false});
            var Q2190;
            Q2190=makeQuery(id+"F3.opExtrude","CAP_EDGE",EDGE,{"disambiguationData":[OSD([sQuery(id+"F2.wireOp",EDGE,"E3.0.28.18")])],"isStart":false});
            var Q2191;
            Q2191=makeQuery(id+"F3.opExtrude","CAP_EDGE",EDGE,{"disambiguationData":[OSD([sQuery(id+"F2.wireOp",EDGE,"E2.15.18.0")])],"isStart":false});
            var Q2192;
            Q2192=makeQuery(id+"F3.opExtrude","CAP_EDGE",EDGE,{"disambiguationData":[OSD([sQuery(id+"F2.wireOp",EDGE,"E3.0.22.18")])],"isStart":false});
            var Q2193;
            Q2193=makeQuery(id+"F3.opExtrude","CAP_EDGE",EDGE,{"disambiguationData":[OSD([sQuery(id+"F2.wireOp",EDGE,"E2.9.18.0")])],"isStart":false});
            var Q2194;
            Q2194=makeQuery(id+"F3.opExtrude","CAP_EDGE",EDGE,{"disambiguationData":[OSD([sQuery(id+"F2.wireOp",EDGE,"E3.9.21.18")])],"isStart":false});
            var Q2195;
            Q2195=makeQuery(id+"F3.opExtrude","CAP_EDGE",EDGE,{"disambiguationData":[OSD([sQuery(id+"F2.wireOp",EDGE,"E2.8.18.3")])],"isStart":false});
            var Q2196;
            Q2196=makeQuery(id+"F3.opExtrude","CAP_EDGE",EDGE,{"disambiguationData":[OSD([sQuery(id+"F2.wireOp",EDGE,"E2.2.18.3")])],"isStart":false});
            var Q2197;
            Q2197=makeQuery(id+"F3.opExtrude","CAP_EDGE",EDGE,{"disambiguationData":[OSD([sQuery(id+"F2.wireOp",EDGE,"E3.0.25.18")])],"isStart":false});
            var Q2198;
            Q2198=makeQuery(id+"F3.opExtrude","CAP_EDGE",EDGE,{"disambiguationData":[OSD([sQuery(id+"F2.wireOp",EDGE,"E2.19.18.0")])],"isStart":false});
            var Q2199;
            Q2199=makeQuery(id+"F3.opExtrude","CAP_EDGE",EDGE,{"disambiguationData":[OSD([sQuery(id+"F2.wireOp",EDGE,"E2.6.18.0")])],"isStart":false});
            var Q2200;
            Q2200=makeQuery(id+"F3.opExtrude","CAP_EDGE",EDGE,{"disambiguationData":[OSD([sQuery(id+"F2.wireOp",EDGE,"E2.13.18.0")])],"isStart":false});
            var Q2201;
            Q2201=makeQuery(id+"F3.opExtrude","CAP_EDGE",EDGE,{"disambiguationData":[OSD([sQuery(id+"F2.wireOp",EDGE,"E3.0.20.18")])],"isStart":false});
            var Q2202;
            Q2202=makeQuery(id+"F3.opExtrude","CAP_EDGE",EDGE,{"disambiguationData":[OSD([sQuery(id+"F2.wireOp",EDGE,"E3.0.26.18")])],"isStart":false});
            var Q2203;
            Q2203=makeQuery(id+"F3.opExtrude","CAP_EDGE",EDGE,{"disambiguationData":[OSD([sQuery(id+"F2.wireOp",EDGE,"E2.7.18.0")])],"isStart":false});
            var Q2204;
            Q2204=makeQuery(id+"F3.opExtrude","CAP_EDGE",EDGE,{"disambiguationData":[OSD([sQuery(id+"F2.wireOp",EDGE,"E2.14.18.0")])],"isStart":false});
            var Q2205;
            Q2205=makeQuery(id+"F3.opExtrude","CAP_EDGE",EDGE,{"disambiguationData":[OSD([sQuery(id+"F2.wireOp",EDGE,"E2.1.18.0")])],"isStart":false});
            var Q2206;
            Q2206=makeQuery(id+"F3.opExtrude","CAP_EDGE",EDGE,{"disambiguationData":[OSD([sQuery(id+"F2.wireOp",EDGE,"E2.8.18.0")])],"isStart":false});
            var Q2207;
            Q2207=makeQuery(id+"F3.opExtrude","CAP_EDGE",EDGE,{"disambiguationData":[OSD([sQuery(id+"F2.wireOp",EDGE,"E3.0.27.18")])],"isStart":false});
            var Q2208;
            Q2208=makeQuery(id+"F3.opExtrude","CAP_EDGE",EDGE,{"disambiguationData":[OSD([sQuery(id+"F2.wireOp",EDGE,"E2.2.18.0")])],"isStart":false});
            var Q2209;
            Q2209=makeQuery(id+"F3.opExtrude","CAP_EDGE",EDGE,{"disambiguationData":[OSD([sQuery(id+"F2.wireOp",EDGE,"E3.0.21.18")])],"isStart":false});
            var Q2210;
            Q2210=makeQuery(id+"F3.opExtrude","CAP_EDGE",EDGE,{"disambiguationData":[OSD([sQuery(id+"F2.wireOp",EDGE,"E2.3.18.0")])],"isStart":false});
            var Q2211;
            Q2211=makeQuery(id+"F3.opExtrude","CAP_EDGE",EDGE,{"disambiguationData":[OSD([sQuery(id+"F2.wireOp",EDGE,"E2.10.18.0")])],"isStart":false});
            var Q2212;
            Q2212=makeQuery(id+"F3.opExtrude","CAP_EDGE",EDGE,{"disambiguationData":[OSD([sQuery(id+"F2.wireOp",EDGE,"E3.0.29.18")])],"isStart":false});
            var Q2213;
            Q2213=makeQuery(id+"F3.opExtrude","CAP_EDGE",EDGE,{"disambiguationData":[OSD([sQuery(id+"F2.wireOp",EDGE,"E2.4.18.0")])],"isStart":false});
            var Q2214;
            Q2214=makeQuery(id+"F3.opExtrude","CAP_EDGE",EDGE,{"disambiguationData":[OSD([sQuery(id+"F2.wireOp",EDGE,"E3.0.23.18")])],"isStart":false});
            var Q2215;
            Q2215=makeQuery(id+"F3.opExtrude","CAP_EDGE",EDGE,{"disambiguationData":[OSD([sQuery(id+"F2.wireOp",EDGE,"E2.17.18.0")])],"isStart":false});
            var Q2216;
            Q2216=makeQuery(id+"F3.opExtrude","CAP_EDGE",EDGE,{"disambiguationData":[OSD([sQuery(id+"F2.wireOp",EDGE,"E3.0.24.18")])],"isStart":false});
            var Q2217;
            Q2217=makeQuery(id+"F3.opExtrude","CAP_EDGE",EDGE,{"disambiguationData":[OSD([sQuery(id+"F2.wireOp",EDGE,"E2.11.18.0")])],"isStart":false});
            var Q2218;
            Q2218=makeQuery(id+"F3.opExtrude","CAP_EDGE",EDGE,{"disambiguationData":[OSD([sQuery(id+"F2.wireOp",EDGE,"E2.18.18.0")])],"isStart":false});
            var Q2219;
            Q2219=makeQuery(id+"F3.opExtrude","CAP_EDGE",EDGE,{"disambiguationData":[OSD([sQuery(id+"F2.wireOp",EDGE,"E2.5.18.0")])],"isStart":false});
            var Q2220;
            Q2220=makeQuery(id+"F3.opExtrude","CAP_EDGE",EDGE,{"disambiguationData":[OSD([sQuery(id+"F2.wireOp",EDGE,"E2.12.18.0")])],"isStart":false});
            var Q2221;
            Q2221=makeQuery(id+"F3.opExtrude","CAP_EDGE",EDGE,{"disambiguationData":[OSD([sQuery(id+"F2.wireOp",EDGE,"E2.0.18.1")])],"isStart":false});
            var Q2222;
            Q2222=makeQuery(id+"F3.opExtrude","CAP_EDGE",EDGE,{"disambiguationData":[OSD([sQuery(id+"F2.wireOp",EDGE,"E2.3.18.2")])],"isStart":false});
            var Q2223;
            Q2223=makeQuery(id+"F3.opExtrude","CAP_EDGE",EDGE,{"disambiguationData":[OSD([sQuery(id+"F2.wireOp",EDGE,"E2.10.18.2")])],"isStart":false});
            var Q2224;
            Q2224=makeQuery(id+"F3.opExtrude","CAP_EDGE",EDGE,{"disambiguationData":[OSD([sQuery(id+"F2.wireOp",EDGE,"E3.6.29.18")])],"isStart":false});
            var Q2225;
            Q2225=makeQuery(id+"F3.opExtrude","CAP_EDGE",EDGE,{"disambiguationData":[OSD([sQuery(id+"F2.wireOp",EDGE,"E2.4.18.2")])],"isStart":false});
            var Q2226;
            Q2226=makeQuery(id+"F3.opExtrude","CAP_EDGE",EDGE,{"disambiguationData":[OSD([sQuery(id+"F2.wireOp",EDGE,"E3.6.23.18")])],"isStart":false});
            var Q2227;
            Q2227=makeQuery(id+"F3.opExtrude","CAP_EDGE",EDGE,{"disambiguationData":[OSD([sQuery(id+"F2.wireOp",EDGE,"E2.17.18.2")])],"isStart":false});
            var Q2228;
            Q2228=makeQuery(id+"F3.opExtrude","CAP_EDGE",EDGE,{"disambiguationData":[OSD([sQuery(id+"F2.wireOp",EDGE,"E3.6.24.18")])],"isStart":false});
            var Q2229;
            Q2229=makeQuery(id+"F3.opExtrude","CAP_EDGE",EDGE,{"disambiguationData":[OSD([sQuery(id+"F2.wireOp",EDGE,"E2.11.18.2")])],"isStart":false});
            var Q2230;
            Q2230=makeQuery(id+"F3.opExtrude","CAP_EDGE",EDGE,{"disambiguationData":[OSD([sQuery(id+"F2.wireOp",EDGE,"E2.18.18.2")])],"isStart":false});
            var Q2231;
            Q2231=makeQuery(id+"F3.opExtrude","CAP_EDGE",EDGE,{"disambiguationData":[OSD([sQuery(id+"F2.wireOp",EDGE,"E2.5.18.2")])],"isStart":false});
            var Q2232;
            Q2232=makeQuery(id+"F3.opExtrude","CAP_EDGE",EDGE,{"disambiguationData":[OSD([sQuery(id+"F2.wireOp",EDGE,"E2.12.18.2")])],"isStart":false});
            var Q2233;
            Q2233=makeQuery(id+"F3.opExtrude","CAP_EDGE",EDGE,{"disambiguationData":[OSD([sQuery(id+"F2.wireOp",EDGE,"E2.16.18.2")])],"isStart":false});
            var Q2234;
            Q2234=makeQuery(id+"F3.opExtrude","CAP_EDGE",EDGE,{"disambiguationData":[OSD([sQuery(id+"F2.wireOp",EDGE,"E3.6.28.18")])],"isStart":false});
            var Q2235;
            Q2235=makeQuery(id+"F3.opExtrude","CAP_EDGE",EDGE,{"disambiguationData":[OSD([sQuery(id+"F2.wireOp",EDGE,"E2.15.18.2")])],"isStart":false});
            var Q2236;
            Q2236=makeQuery(id+"F3.opExtrude","CAP_EDGE",EDGE,{"disambiguationData":[OSD([sQuery(id+"F2.wireOp",EDGE,"E3.6.22.18")])],"isStart":false});
            var Q2237;
            Q2237=makeQuery(id+"F3.opExtrude","CAP_EDGE",EDGE,{"disambiguationData":[OSD([sQuery(id+"F2.wireOp",EDGE,"E2.9.18.2")])],"isStart":false});
            var Q2238;
            Q2238=makeQuery(id+"F3.opExtrude","CAP_EDGE",EDGE,{"disambiguationData":[OSD([sQuery(id+"F2.wireOp",EDGE,"E2.2.18.2")])],"isStart":false});
            var Q2239;
            Q2239=makeQuery(id+"F3.opExtrude","CAP_EDGE",EDGE,{"disambiguationData":[OSD([sQuery(id+"F2.wireOp",EDGE,"E3.6.25.18")])],"isStart":false});
            var Q2240;
            Q2240=makeQuery(id+"F3.opExtrude","CAP_EDGE",EDGE,{"disambiguationData":[OSD([sQuery(id+"F2.wireOp",EDGE,"E2.19.18.2")])],"isStart":false});
            var Q2241;
            Q2241=makeQuery(id+"F3.opExtrude","CAP_EDGE",EDGE,{"disambiguationData":[OSD([sQuery(id+"F2.wireOp",EDGE,"E2.6.18.2")])],"isStart":false});
            var Q2242;
            Q2242=makeQuery(id+"F3.opExtrude","CAP_EDGE",EDGE,{"disambiguationData":[OSD([sQuery(id+"F2.wireOp",EDGE,"E2.13.18.2")])],"isStart":false});
            var Q2243;
            Q2243=makeQuery(id+"F3.opExtrude","CAP_EDGE",EDGE,{"disambiguationData":[OSD([sQuery(id+"F2.wireOp",EDGE,"E2.7.18.2")])],"isStart":false});
            var Q2244;
            Q2244=makeQuery(id+"F3.opExtrude","CAP_EDGE",EDGE,{"disambiguationData":[OSD([sQuery(id+"F2.wireOp",EDGE,"E3.6.26.18")])],"isStart":false});
            var Q2245;
            Q2245=makeQuery(id+"F3.opExtrude","CAP_EDGE",EDGE,{"disambiguationData":[OSD([sQuery(id+"F2.wireOp",EDGE,"E2.1.18.2")])],"isStart":false});
            var Q2246;
            Q2246=makeQuery(id+"F3.opExtrude","CAP_EDGE",EDGE,{"disambiguationData":[OSD([sQuery(id+"F2.wireOp",EDGE,"E3.6.20.18")])],"isStart":false});
            var Q2247;
            Q2247=makeQuery(id+"F3.opExtrude","CAP_EDGE",EDGE,{"disambiguationData":[OSD([sQuery(id+"F2.wireOp",EDGE,"E3.6.27.18")])],"isStart":false});
            var Q2248;
            Q2248=makeQuery(id+"F3.opExtrude","CAP_EDGE",EDGE,{"disambiguationData":[OSD([sQuery(id+"F2.wireOp",EDGE,"E2.14.18.2")])],"isStart":false});
            var Q2249;
            Q2249=makeQuery(id+"F3.opExtrude","CAP_EDGE",EDGE,{"disambiguationData":[OSD([sQuery(id+"F2.wireOp",EDGE,"E3.6.21.18")])],"isStart":false});
            var Q2250;
            Q2250=makeQuery(id+"F3.opExtrude","CAP_EDGE",EDGE,{"disambiguationData":[OSD([sQuery(id+"F2.wireOp",EDGE,"E2.8.18.2")])],"isStart":false});
            var Q2251;
            Q2251=makeQuery(id+"F3.opExtrude","CAP_EDGE",EDGE,{"disambiguationData":[OSD([sQuery(id+"F2.wireOp",EDGE,"E2.16.18.1")])],"isStart":false});
            var Q2252;
            Q2252=makeQuery(id+"F3.opExtrude","CAP_EDGE",EDGE,{"disambiguationData":[OSD([sQuery(id+"F2.wireOp",EDGE,"E3.3.28.18")])],"isStart":false});
            var Q2253;
            Q2253=makeQuery(id+"F3.opExtrude","CAP_EDGE",EDGE,{"disambiguationData":[OSD([sQuery(id+"F2.wireOp",EDGE,"E2.15.18.1")])],"isStart":false});
            var Q2254;
            Q2254=makeQuery(id+"F3.opExtrude","CAP_EDGE",EDGE,{"disambiguationData":[OSD([sQuery(id+"F2.wireOp",EDGE,"E3.3.22.18")])],"isStart":false});
            var Q2255;
            Q2255=makeQuery(id+"F3.opExtrude","CAP_EDGE",EDGE,{"disambiguationData":[OSD([sQuery(id+"F2.wireOp",EDGE,"E2.9.18.1")])],"isStart":false});
            var Q2256;
            Q2256=makeQuery(id+"F3.opExtrude","CAP_EDGE",EDGE,{"disambiguationData":[OSD([sQuery(id+"F2.wireOp",EDGE,"E2.3.18.1")])],"isStart":false});
            var Q2257;
            Q2257=makeQuery(id+"F3.opExtrude","CAP_EDGE",EDGE,{"disambiguationData":[OSD([sQuery(id+"F2.wireOp",EDGE,"E2.10.18.1")])],"isStart":false});
            var Q2258;
            Q2258=makeQuery(id+"F3.opExtrude","CAP_EDGE",EDGE,{"disambiguationData":[OSD([sQuery(id+"F2.wireOp",EDGE,"E3.3.29.18")])],"isStart":false});
            var Q2259;
            Q2259=makeQuery(id+"F3.opExtrude","CAP_EDGE",EDGE,{"disambiguationData":[OSD([sQuery(id+"F2.wireOp",EDGE,"E2.4.18.1")])],"isStart":false});
            var Q2260;
            Q2260=makeQuery(id+"F3.opExtrude","CAP_EDGE",EDGE,{"disambiguationData":[OSD([sQuery(id+"F2.wireOp",EDGE,"E3.3.23.18")])],"isStart":false});
            var Q2261;
            Q2261=makeQuery(id+"F3.opExtrude","CAP_EDGE",EDGE,{"disambiguationData":[OSD([sQuery(id+"F2.wireOp",EDGE,"E2.7.18.1")])],"isStart":false});
            var Q2262;
            Q2262=makeQuery(id+"F3.opExtrude","CAP_EDGE",EDGE,{"disambiguationData":[OSD([sQuery(id+"F2.wireOp",EDGE,"E3.3.26.18")])],"isStart":false});
            var Q2263;
            Q2263=makeQuery(id+"F3.opExtrude","CAP_EDGE",EDGE,{"disambiguationData":[OSD([sQuery(id+"F2.wireOp",EDGE,"E2.1.18.1")])],"isStart":false});
            var Q2264;
            Q2264=makeQuery(id+"F3.opExtrude","CAP_EDGE",EDGE,{"disambiguationData":[OSD([sQuery(id+"F2.wireOp",EDGE,"E3.3.20.18")])],"isStart":false});
            var Q2265;
            Q2265=makeQuery(id+"F3.opExtrude","CAP_EDGE",EDGE,{"disambiguationData":[OSD([sQuery(id+"F2.wireOp",EDGE,"E3.3.27.18")])],"isStart":false});
            var Q2266;
            Q2266=makeQuery(id+"F3.opExtrude","CAP_EDGE",EDGE,{"disambiguationData":[OSD([sQuery(id+"F2.wireOp",EDGE,"E2.8.18.1")])],"isStart":false});
            var Q2267;
            Q2267=makeQuery(id+"F3.opExtrude","CAP_EDGE",EDGE,{"disambiguationData":[OSD([sQuery(id+"F2.wireOp",EDGE,"E2.14.18.1")])],"isStart":false});
            var Q2268;
            Q2268=makeQuery(id+"F3.opExtrude","CAP_EDGE",EDGE,{"disambiguationData":[OSD([sQuery(id+"F2.wireOp",EDGE,"E2.2.18.1")])],"isStart":false});
            var Q2269;
            Q2269=makeQuery(id+"F3.opExtrude","CAP_EDGE",EDGE,{"disambiguationData":[OSD([sQuery(id+"F2.wireOp",EDGE,"E3.3.21.18")])],"isStart":false});
            var Q2270;
            Q2270=makeQuery(id+"F3.opExtrude","CAP_EDGE",EDGE,{"disambiguationData":[OSD([sQuery(id+"F2.wireOp",EDGE,"E2.17.18.1")])],"isStart":false});
            var Q2271;
            Q2271=makeQuery(id+"F3.opExtrude","CAP_EDGE",EDGE,{"disambiguationData":[OSD([sQuery(id+"F2.wireOp",EDGE,"E3.3.24.18")])],"isStart":false});
            var Q2272;
            Q2272=makeQuery(id+"F3.opExtrude","CAP_EDGE",EDGE,{"disambiguationData":[OSD([sQuery(id+"F2.wireOp",EDGE,"E2.11.18.1")])],"isStart":false});
            var Q2273;
            Q2273=makeQuery(id+"F3.opExtrude","CAP_EDGE",EDGE,{"disambiguationData":[OSD([sQuery(id+"F2.wireOp",EDGE,"E2.18.18.1")])],"isStart":false});
            var Q2274;
            Q2274=makeQuery(id+"F3.opExtrude","CAP_EDGE",EDGE,{"disambiguationData":[OSD([sQuery(id+"F2.wireOp",EDGE,"E2.5.18.1")])],"isStart":false});
            var Q2275;
            Q2275=makeQuery(id+"F3.opExtrude","CAP_EDGE",EDGE,{"disambiguationData":[OSD([sQuery(id+"F2.wireOp",EDGE,"E2.12.18.1")])],"isStart":false});
            var Q2276;
            Q2276=makeQuery(id+"F3.opExtrude","CAP_EDGE",EDGE,{"disambiguationData":[OSD([sQuery(id+"F2.wireOp",EDGE,"E3.3.25.18")])],"isStart":false});
            var Q2277;
            Q2277=makeQuery(id+"F3.opExtrude","CAP_EDGE",EDGE,{"disambiguationData":[OSD([sQuery(id+"F2.wireOp",EDGE,"E2.19.18.1")])],"isStart":false});
            var Q2278;
            Q2278=makeQuery(id+"F3.opExtrude","CAP_EDGE",EDGE,{"disambiguationData":[OSD([sQuery(id+"F2.wireOp",EDGE,"E2.6.18.1")])],"isStart":false});
            var Q2279;
            Q2279=makeQuery(id+"F3.opExtrude","CAP_EDGE",EDGE,{"disambiguationData":[OSD([sQuery(id+"F2.wireOp",EDGE,"E2.13.18.1")])],"isStart":false});
            var Q2280;
            Q2280=makeQuery(id+"F3.opExtrude","CAP_EDGE",EDGE,{"disambiguationData":[OSD([sQuery(id+"F2.wireOp",EDGE,"E2.0.19.0")])],"isStart":false});
            var Q2281;
            Q2281=makeQuery(id+"F3.opExtrude","CAP_EDGE",EDGE,{"disambiguationData":[OSD([sQuery(id+"F2.wireOp",EDGE,"E2.0.19.2")])],"isStart":false});
            var Q2282;
            Q2282=makeQuery(id+"F3.opExtrude","CAP_EDGE",EDGE,{"disambiguationData":[OSD([sQuery(id+"F2.wireOp",EDGE,"E2.15.19.0")])],"isStart":false});
            var Q2283;
            Q2283=makeQuery(id+"F3.opExtrude","CAP_EDGE",EDGE,{"disambiguationData":[OSD([sQuery(id+"F2.wireOp",EDGE,"E2.16.19.0")])],"isStart":false});
            var Q2284;
            Q2284=makeQuery(id+"F3.opExtrude","CAP_EDGE",EDGE,{"disambiguationData":[OSD([sQuery(id+"F2.wireOp",EDGE,"E3.0.22.19")])],"isStart":false});
            var Q2285;
            Q2285=makeQuery(id+"F3.opExtrude","CAP_EDGE",EDGE,{"disambiguationData":[OSD([sQuery(id+"F2.wireOp",EDGE,"E3.0.28.19")])],"isStart":false});
            var Q2286;
            Q2286=makeQuery(id+"F3.opExtrude","CAP_EDGE",EDGE,{"disambiguationData":[OSD([sQuery(id+"F2.wireOp",EDGE,"E2.9.19.0")])],"isStart":false});
            var Q2287;
            Q2287=makeQuery(id+"F3.opExtrude","CAP_EDGE",EDGE,{"disambiguationData":[OSD([sQuery(id+"F2.wireOp",EDGE,"E2.3.19.0")])],"isStart":false});
            var Q2288;
            Q2288=makeQuery(id+"F3.opExtrude","CAP_EDGE",EDGE,{"disambiguationData":[OSD([sQuery(id+"F2.wireOp",EDGE,"E3.0.29.19")])],"isStart":false});
            var Q2289;
            Q2289=makeQuery(id+"F3.opExtrude","CAP_EDGE",EDGE,{"disambiguationData":[OSD([sQuery(id+"F2.wireOp",EDGE,"E2.13.19.0")])],"isStart":false});
            var Q2290;
            Q2290=makeQuery(id+"F3.opExtrude","CAP_EDGE",EDGE,{"disambiguationData":[OSD([sQuery(id+"F2.wireOp",EDGE,"E2.7.19.0")])],"isStart":false});
            var Q2291;
            Q2291=makeQuery(id+"F3.opExtrude","CAP_EDGE",EDGE,{"disambiguationData":[OSD([sQuery(id+"F2.wireOp",EDGE,"E3.0.26.19")])],"isStart":false});
            var Q2292;
            Q2292=makeQuery(id+"F3.opExtrude","CAP_EDGE",EDGE,{"disambiguationData":[OSD([sQuery(id+"F2.wireOp",EDGE,"E2.1.19.0")])],"isStart":false});
            var Q2293;
            Q2293=makeQuery(id+"F3.opExtrude","CAP_EDGE",EDGE,{"disambiguationData":[OSD([sQuery(id+"F2.wireOp",EDGE,"E3.0.20.19")])],"isStart":false});
            var Q2294;
            Q2294=makeQuery(id+"F3.opExtrude","CAP_EDGE",EDGE,{"disambiguationData":[OSD([sQuery(id+"F2.wireOp",EDGE,"E3.0.27.19")])],"isStart":false});
            var Q2295;
            Q2295=makeQuery(id+"F3.opExtrude","CAP_EDGE",EDGE,{"disambiguationData":[OSD([sQuery(id+"F2.wireOp",EDGE,"E2.14.19.0")])],"isStart":false});
            var Q2296;
            Q2296=makeQuery(id+"F3.opExtrude","CAP_EDGE",EDGE,{"disambiguationData":[OSD([sQuery(id+"F2.wireOp",EDGE,"E3.0.21.19")])],"isStart":false});
            var Q2297;
            Q2297=makeQuery(id+"F3.opExtrude","CAP_EDGE",EDGE,{"disambiguationData":[OSD([sQuery(id+"F2.wireOp",EDGE,"E2.8.19.0")])],"isStart":false});
            var Q2298;
            Q2298=makeQuery(id+"F3.opExtrude","CAP_EDGE",EDGE,{"disambiguationData":[OSD([sQuery(id+"F2.wireOp",EDGE,"E2.2.19.0")])],"isStart":false});
            var Q2299;
            Q2299=makeQuery(id+"F3.opExtrude","CAP_EDGE",EDGE,{"disambiguationData":[OSD([sQuery(id+"F2.wireOp",EDGE,"E3.0.23.19")])],"isStart":false});
            var Q2300;
            Q2300=makeQuery(id+"F3.opExtrude","CAP_EDGE",EDGE,{"disambiguationData":[OSD([sQuery(id+"F2.wireOp",EDGE,"E2.10.19.0")])],"isStart":false});
            var Q2301;
            Q2301=makeQuery(id+"F3.opExtrude","CAP_EDGE",EDGE,{"disambiguationData":[OSD([sQuery(id+"F2.wireOp",EDGE,"E2.17.19.0")])],"isStart":false});
            var Q2302;
            Q2302=makeQuery(id+"F3.opExtrude","CAP_EDGE",EDGE,{"disambiguationData":[OSD([sQuery(id+"F2.wireOp",EDGE,"E2.4.19.0")])],"isStart":false});
            var Q2303;
            Q2303=makeQuery(id+"F3.opExtrude","CAP_EDGE",EDGE,{"disambiguationData":[OSD([sQuery(id+"F2.wireOp",EDGE,"E2.11.19.0")])],"isStart":false});
            var Q2304;
            Q2304=makeQuery(id+"F3.opExtrude","CAP_EDGE",EDGE,{"disambiguationData":[OSD([sQuery(id+"F2.wireOp",EDGE,"E2.18.19.0")])],"isStart":false});
            var Q2305;
            Q2305=makeQuery(id+"F3.opExtrude","CAP_EDGE",EDGE,{"disambiguationData":[OSD([sQuery(id+"F2.wireOp",EDGE,"E3.0.24.19")])],"isStart":false});
            var Q2306;
            Q2306=makeQuery(id+"F3.opExtrude","CAP_EDGE",EDGE,{"disambiguationData":[OSD([sQuery(id+"F2.wireOp",EDGE,"E2.5.19.0")])],"isStart":false});
            var Q2307;
            Q2307=makeQuery(id+"F3.opExtrude","CAP_EDGE",EDGE,{"disambiguationData":[OSD([sQuery(id+"F2.wireOp",EDGE,"E2.12.19.0")])],"isStart":false});
            var Q2308;
            Q2308=makeQuery(id+"F3.opExtrude","CAP_EDGE",EDGE,{"disambiguationData":[OSD([sQuery(id+"F2.wireOp",EDGE,"E3.0.25.19")])],"isStart":false});
            var Q2309;
            Q2309=makeQuery(id+"F3.opExtrude","CAP_EDGE",EDGE,{"disambiguationData":[OSD([sQuery(id+"F2.wireOp",EDGE,"E2.19.19.0")])],"isStart":false});
            var Q2310;
            Q2310=makeQuery(id+"F3.opExtrude","CAP_EDGE",EDGE,{"disambiguationData":[OSD([sQuery(id+"F2.wireOp",EDGE,"E2.6.19.0")])],"isStart":false});
            var Q2311;
            Q2311=makeQuery(id+"F3.opExtrude","CAP_EDGE",EDGE,{"disambiguationData":[OSD([sQuery(id+"F2.wireOp",EDGE,"E2.5.19.2")])],"isStart":false});
            var Q2312;
            Q2312=makeQuery(id+"F3.opExtrude","CAP_EDGE",EDGE,{"disambiguationData":[OSD([sQuery(id+"F2.wireOp",EDGE,"E3.6.24.19")])],"isStart":false});
            var Q2313;
            Q2313=makeQuery(id+"F3.opExtrude","CAP_EDGE",EDGE,{"disambiguationData":[OSD([sQuery(id+"F2.wireOp",EDGE,"E2.12.19.2")])],"isStart":false});
            var Q2314;
            Q2314=makeQuery(id+"F3.opExtrude","CAP_EDGE",EDGE,{"disambiguationData":[OSD([sQuery(id+"F2.wireOp",EDGE,"E2.18.19.2")])],"isStart":false});
            var Q2315;
            Q2315=makeQuery(id+"F3.opExtrude","CAP_EDGE",EDGE,{"disambiguationData":[OSD([sQuery(id+"F2.wireOp",EDGE,"E3.6.25.19")])],"isStart":false});
            var Q2316;
            Q2316=makeQuery(id+"F3.opExtrude","CAP_EDGE",EDGE,{"disambiguationData":[OSD([sQuery(id+"F2.wireOp",EDGE,"E2.19.19.2")])],"isStart":false});
            var Q2317;
            Q2317=makeQuery(id+"F3.opExtrude","CAP_EDGE",EDGE,{"disambiguationData":[OSD([sQuery(id+"F2.wireOp",EDGE,"E2.6.19.2")])],"isStart":false});
            var Q2318;
            Q2318=makeQuery(id+"F3.opExtrude","CAP_EDGE",EDGE,{"disambiguationData":[OSD([sQuery(id+"F2.wireOp",EDGE,"E2.13.19.2")])],"isStart":false});
            var Q2319;
            Q2319=makeQuery(id+"F3.opExtrude","CAP_EDGE",EDGE,{"disambiguationData":[OSD([sQuery(id+"F2.wireOp",EDGE,"E2.7.19.2")])],"isStart":false});
            var Q2320;
            Q2320=makeQuery(id+"F3.opExtrude","CAP_EDGE",EDGE,{"disambiguationData":[OSD([sQuery(id+"F2.wireOp",EDGE,"E3.6.26.19")])],"isStart":false});
            var Q2321;
            Q2321=makeQuery(id+"F3.opExtrude","CAP_EDGE",EDGE,{"disambiguationData":[OSD([sQuery(id+"F2.wireOp",EDGE,"E2.1.19.2")])],"isStart":false});
            var Q2322;
            Q2322=makeQuery(id+"F3.opExtrude","CAP_EDGE",EDGE,{"disambiguationData":[OSD([sQuery(id+"F2.wireOp",EDGE,"E3.6.20.19")])],"isStart":false});
            var Q2323;
            Q2323=makeQuery(id+"F3.opExtrude","CAP_EDGE",EDGE,{"disambiguationData":[OSD([sQuery(id+"F2.wireOp",EDGE,"E2.15.19.2")])],"isStart":false});
            var Q2324;
            Q2324=makeQuery(id+"F3.opExtrude","CAP_EDGE",EDGE,{"disambiguationData":[OSD([sQuery(id+"F2.wireOp",EDGE,"E2.16.19.2")])],"isStart":false});
            var Q2325;
            Q2325=makeQuery(id+"F3.opExtrude","CAP_EDGE",EDGE,{"disambiguationData":[OSD([sQuery(id+"F2.wireOp",EDGE,"E2.9.19.2")])],"isStart":false});
            var Q2326;
            Q2326=makeQuery(id+"F3.opExtrude","CAP_EDGE",EDGE,{"disambiguationData":[OSD([sQuery(id+"F2.wireOp",EDGE,"E3.6.28.19")])],"isStart":false});
            var Q2327;
            Q2327=makeQuery(id+"F3.opExtrude","CAP_EDGE",EDGE,{"disambiguationData":[OSD([sQuery(id+"F2.wireOp",EDGE,"E3.6.22.19")])],"isStart":false});
            var Q2328;
            Q2328=makeQuery(id+"F3.opExtrude","CAP_EDGE",EDGE,{"disambiguationData":[OSD([sQuery(id+"F2.wireOp",EDGE,"E2.3.19.2")])],"isStart":false});
            var Q2329;
            Q2329=makeQuery(id+"F3.opExtrude","CAP_EDGE",EDGE,{"disambiguationData":[OSD([sQuery(id+"F2.wireOp",EDGE,"E3.6.29.19")])],"isStart":false});
            var Q2330;
            Q2330=makeQuery(id+"F3.opExtrude","CAP_EDGE",EDGE,{"disambiguationData":[OSD([sQuery(id+"F2.wireOp",EDGE,"E2.0.19.1")])],"isStart":false});
            var Q2331;
            Q2331=makeQuery(id+"F3.opExtrude","CAP_EDGE",EDGE,{"disambiguationData":[OSD([sQuery(id+"F2.wireOp",EDGE,"E3.6.23.19")])],"isStart":false});
            var Q2332;
            Q2332=makeQuery(id+"F3.opExtrude","CAP_EDGE",EDGE,{"disambiguationData":[OSD([sQuery(id+"F2.wireOp",EDGE,"E2.10.19.2")])],"isStart":false});
            var Q2333;
            Q2333=makeQuery(id+"F3.opExtrude","CAP_EDGE",EDGE,{"disambiguationData":[OSD([sQuery(id+"F2.wireOp",EDGE,"E2.17.19.2")])],"isStart":false});
            var Q2334;
            Q2334=makeQuery(id+"F3.opExtrude","CAP_EDGE",EDGE,{"disambiguationData":[OSD([sQuery(id+"F2.wireOp",EDGE,"E2.4.19.2")])],"isStart":false});
            var Q2335;
            Q2335=makeQuery(id+"F3.opExtrude","CAP_EDGE",EDGE,{"disambiguationData":[OSD([sQuery(id+"F2.wireOp",EDGE,"E2.11.19.2")])],"isStart":false});
            var Q2336;
            Q2336=makeQuery(id+"F3.opExtrude","CAP_EDGE",EDGE,{"disambiguationData":[OSD([sQuery(id+"F2.wireOp",EDGE,"E3.6.27.19")])],"isStart":false});
            var Q2337;
            Q2337=makeQuery(id+"F3.opExtrude","CAP_EDGE",EDGE,{"disambiguationData":[OSD([sQuery(id+"F2.wireOp",EDGE,"E2.14.19.2")])],"isStart":false});
            var Q2338;
            Q2338=makeQuery(id+"F3.opExtrude","CAP_EDGE",EDGE,{"disambiguationData":[OSD([sQuery(id+"F2.wireOp",EDGE,"E3.6.21.19")])],"isStart":false});
            var Q2339;
            Q2339=makeQuery(id+"F3.opExtrude","CAP_EDGE",EDGE,{"disambiguationData":[OSD([sQuery(id+"F2.wireOp",EDGE,"E2.8.19.2")])],"isStart":false});
            var Q2340;
            Q2340=makeQuery(id+"F3.opExtrude","CAP_EDGE",EDGE,{"disambiguationData":[OSD([sQuery(id+"F2.wireOp",EDGE,"E2.2.19.2")])],"isStart":false});
            var Q2341;
            Q2341=makeQuery(id+"F3.opExtrude","CAP_EDGE",EDGE,{"disambiguationData":[OSD([sQuery(id+"F2.wireOp",EDGE,"E2.0.19.3")])],"isStart":false});
            var Q2342;
            Q2342=makeQuery(id+"F3.opExtrude","CAP_EDGE",EDGE,{"disambiguationData":[OSD([sQuery(id+"F2.wireOp",EDGE,"E2.9.19.1")])],"isStart":false});
            var Q2343;
            Q2343=makeQuery(id+"F3.opExtrude","CAP_EDGE",EDGE,{"disambiguationData":[OSD([sQuery(id+"F2.wireOp",EDGE,"E3.3.28.19")])],"isStart":false});
            var Q2344;
            Q2344=makeQuery(id+"F3.opExtrude","CAP_EDGE",EDGE,{"disambiguationData":[OSD([sQuery(id+"F2.wireOp",EDGE,"E3.3.22.19")])],"isStart":false});
            var Q2345;
            Q2345=makeQuery(id+"F3.opExtrude","CAP_EDGE",EDGE,{"disambiguationData":[OSD([sQuery(id+"F2.wireOp",EDGE,"E2.3.19.1")])],"isStart":false});
            var Q2346;
            Q2346=makeQuery(id+"F3.opExtrude","CAP_EDGE",EDGE,{"disambiguationData":[OSD([sQuery(id+"F2.wireOp",EDGE,"E3.3.29.19")])],"isStart":false});
            var Q2347;
            Q2347=makeQuery(id+"F3.opExtrude","CAP_EDGE",EDGE,{"disambiguationData":[OSD([sQuery(id+"F2.wireOp",EDGE,"E3.3.23.19")])],"isStart":false});
            var Q2348;
            Q2348=makeQuery(id+"F3.opExtrude","CAP_EDGE",EDGE,{"disambiguationData":[OSD([sQuery(id+"F2.wireOp",EDGE,"E2.10.19.1")])],"isStart":false});
            var Q2349;
            Q2349=makeQuery(id+"F3.opExtrude","CAP_EDGE",EDGE,{"disambiguationData":[OSD([sQuery(id+"F2.wireOp",EDGE,"E2.17.19.1")])],"isStart":false});
            var Q2350;
            Q2350=makeQuery(id+"F3.opExtrude","CAP_EDGE",EDGE,{"disambiguationData":[OSD([sQuery(id+"F2.wireOp",EDGE,"E2.4.19.1")])],"isStart":false});
            var Q2351;
            Q2351=makeQuery(id+"F3.opExtrude","CAP_EDGE",EDGE,{"disambiguationData":[OSD([sQuery(id+"F2.wireOp",EDGE,"E2.11.19.1")])],"isStart":false});
            var Q2352;
            Q2352=makeQuery(id+"F3.opExtrude","CAP_EDGE",EDGE,{"disambiguationData":[OSD([sQuery(id+"F2.wireOp",EDGE,"E2.5.19.1")])],"isStart":false});
            var Q2353;
            Q2353=makeQuery(id+"F3.opExtrude","CAP_EDGE",EDGE,{"disambiguationData":[OSD([sQuery(id+"F2.wireOp",EDGE,"E3.3.24.19")])],"isStart":false});
            var Q2354;
            Q2354=makeQuery(id+"F3.opExtrude","CAP_EDGE",EDGE,{"disambiguationData":[OSD([sQuery(id+"F2.wireOp",EDGE,"E2.15.19.1")])],"isStart":false});
            var Q2355;
            Q2355=makeQuery(id+"F3.opExtrude","CAP_EDGE",EDGE,{"disambiguationData":[OSD([sQuery(id+"F2.wireOp",EDGE,"E2.16.19.1")])],"isStart":false});
            var Q2356;
            Q2356=makeQuery(id+"F3.opExtrude","CAP_EDGE",EDGE,{"disambiguationData":[OSD([sQuery(id+"F2.wireOp",EDGE,"E3.3.21.19")])],"isStart":false});
            var Q2357;
            Q2357=makeQuery(id+"F3.opExtrude","CAP_EDGE",EDGE,{"disambiguationData":[OSD([sQuery(id+"F2.wireOp",EDGE,"E2.8.19.1")])],"isStart":false});
            var Q2358;
            Q2358=makeQuery(id+"F3.opExtrude","CAP_EDGE",EDGE,{"disambiguationData":[OSD([sQuery(id+"F2.wireOp",EDGE,"E2.2.19.1")])],"isStart":false});
            var Q2359;
            Q2359=makeQuery(id+"F3.opExtrude","CAP_EDGE",EDGE,{"disambiguationData":[OSD([sQuery(id+"F2.wireOp",EDGE,"E2.18.19.1")])],"isStart":false});
            var Q2360;
            Q2360=makeQuery(id+"F3.opExtrude","CAP_EDGE",EDGE,{"disambiguationData":[OSD([sQuery(id+"F2.wireOp",EDGE,"E3.3.25.19")])],"isStart":false});
            var Q2361;
            Q2361=makeQuery(id+"F3.opExtrude","CAP_EDGE",EDGE,{"disambiguationData":[OSD([sQuery(id+"F2.wireOp",EDGE,"E2.12.19.1")])],"isStart":false});
            var Q2362;
            Q2362=makeQuery(id+"F3.opExtrude","CAP_EDGE",EDGE,{"disambiguationData":[OSD([sQuery(id+"F2.wireOp",EDGE,"E2.19.19.1")])],"isStart":false});
            var Q2363;
            Q2363=makeQuery(id+"F3.opExtrude","CAP_EDGE",EDGE,{"disambiguationData":[OSD([sQuery(id+"F2.wireOp",EDGE,"E2.6.19.1")])],"isStart":false});
            var Q2364;
            Q2364=makeQuery(id+"F3.opExtrude","CAP_EDGE",EDGE,{"disambiguationData":[OSD([sQuery(id+"F2.wireOp",EDGE,"E2.13.19.1")])],"isStart":false});
            var Q2365;
            Q2365=makeQuery(id+"F3.opExtrude","CAP_EDGE",EDGE,{"disambiguationData":[OSD([sQuery(id+"F2.wireOp",EDGE,"E2.7.19.1")])],"isStart":false});
            var Q2366;
            Q2366=makeQuery(id+"F3.opExtrude","CAP_EDGE",EDGE,{"disambiguationData":[OSD([sQuery(id+"F2.wireOp",EDGE,"E3.3.26.19")])],"isStart":false});
            var Q2367;
            Q2367=makeQuery(id+"F3.opExtrude","CAP_EDGE",EDGE,{"disambiguationData":[OSD([sQuery(id+"F2.wireOp",EDGE,"E2.1.19.1")])],"isStart":false});
            var Q2368;
            Q2368=makeQuery(id+"F3.opExtrude","CAP_EDGE",EDGE,{"disambiguationData":[OSD([sQuery(id+"F2.wireOp",EDGE,"E3.3.20.19")])],"isStart":false});
            var Q2369;
            Q2369=makeQuery(id+"F3.opExtrude","CAP_EDGE",EDGE,{"disambiguationData":[OSD([sQuery(id+"F2.wireOp",EDGE,"E3.3.27.19")])],"isStart":false});
            var Q2370;
            Q2370=makeQuery(id+"F3.opExtrude","CAP_EDGE",EDGE,{"disambiguationData":[OSD([sQuery(id+"F2.wireOp",EDGE,"E2.14.19.1")])],"isStart":false});
            var Q2371;
            Q2371=makeQuery(id+"F3.opExtrude","CAP_EDGE",EDGE,{"disambiguationData":[OSD([sQuery(id+"F2.wireOp",EDGE,"E2.15.19.3")])],"isStart":false});
            var Q2372;
            Q2372=makeQuery(id+"F3.opExtrude","CAP_EDGE",EDGE,{"disambiguationData":[OSD([sQuery(id+"F2.wireOp",EDGE,"E2.16.19.3")])],"isStart":false});
            var Q2373;
            Q2373=makeQuery(id+"F3.opExtrude","CAP_EDGE",EDGE,{"disambiguationData":[OSD([sQuery(id+"F2.wireOp",EDGE,"E2.9.19.3")])],"isStart":false});
            var Q2374;
            Q2374=makeQuery(id+"F3.opExtrude","CAP_EDGE",EDGE,{"disambiguationData":[OSD([sQuery(id+"F2.wireOp",EDGE,"E3.9.28.19")])],"isStart":false});
            var Q2375;
            Q2375=makeQuery(id+"F3.opExtrude","CAP_EDGE",EDGE,{"disambiguationData":[OSD([sQuery(id+"F2.wireOp",EDGE,"E2.3.19.3")])],"isStart":false});
            var Q2376;
            Q2376=makeQuery(id+"F3.opExtrude","CAP_EDGE",EDGE,{"disambiguationData":[OSD([sQuery(id+"F2.wireOp",EDGE,"E3.9.22.19")])],"isStart":false});
            var Q2377;
            Q2377=makeQuery(id+"F3.opExtrude","CAP_EDGE",EDGE,{"disambiguationData":[OSD([sQuery(id+"F2.wireOp",EDGE,"E2.19.19.3")])],"isStart":false});
            var Q2378;
            Q2378=makeQuery(id+"F3.opExtrude","CAP_EDGE",EDGE,{"disambiguationData":[OSD([sQuery(id+"F2.wireOp",EDGE,"E2.6.19.3")])],"isStart":false});
            var Q2379;
            Q2379=makeQuery(id+"F3.opExtrude","CAP_EDGE",EDGE,{"disambiguationData":[OSD([sQuery(id+"F2.wireOp",EDGE,"E2.13.19.3")])],"isStart":false});
            var Q2380;
            Q2380=makeQuery(id+"F3.opExtrude","CAP_EDGE",EDGE,{"disambiguationData":[OSD([sQuery(id+"F2.wireOp",EDGE,"E2.7.19.3")])],"isStart":false});
            var Q2381;
            Q2381=makeQuery(id+"F3.opExtrude","CAP_EDGE",EDGE,{"disambiguationData":[OSD([sQuery(id+"F2.wireOp",EDGE,"E3.9.26.19")])],"isStart":false});
            var Q2382;
            Q2382=makeQuery(id+"F3.opExtrude","CAP_EDGE",EDGE,{"disambiguationData":[OSD([sQuery(id+"F2.wireOp",EDGE,"E2.1.19.3")])],"isStart":false});
            var Q2383;
            Q2383=makeQuery(id+"F3.opExtrude","CAP_EDGE",EDGE,{"disambiguationData":[OSD([sQuery(id+"F2.wireOp",EDGE,"E3.9.20.19")])],"isStart":false});
            var Q2384;
            Q2384=makeQuery(id+"F3.opExtrude","CAP_EDGE",EDGE,{"disambiguationData":[OSD([sQuery(id+"F2.wireOp",EDGE,"E3.9.27.19")])],"isStart":false});
            var Q2385;
            Q2385=makeQuery(id+"F3.opExtrude","CAP_EDGE",EDGE,{"disambiguationData":[OSD([sQuery(id+"F2.wireOp",EDGE,"E2.14.19.3")])],"isStart":false});
            var Q2386;
            Q2386=makeQuery(id+"F3.opExtrude","CAP_EDGE",EDGE,{"disambiguationData":[OSD([sQuery(id+"F2.wireOp",EDGE,"E3.9.21.19")])],"isStart":false});
            var Q2387;
            Q2387=makeQuery(id+"F3.opExtrude","CAP_EDGE",EDGE,{"disambiguationData":[OSD([sQuery(id+"F2.wireOp",EDGE,"E2.8.19.3")])],"isStart":false});
            var Q2388;
            Q2388=makeQuery(id+"F3.opExtrude","CAP_EDGE",EDGE,{"disambiguationData":[OSD([sQuery(id+"F2.wireOp",EDGE,"E2.2.19.3")])],"isStart":false});
            var Q2389;
            Q2389=makeQuery(id+"F3.opExtrude","CAP_EDGE",EDGE,{"disambiguationData":[OSD([sQuery(id+"F2.wireOp",EDGE,"E3.9.29.19")])],"isStart":false});
            var Q2390;
            Q2390=makeQuery(id+"F3.opExtrude","CAP_EDGE",EDGE,{"disambiguationData":[OSD([sQuery(id+"F2.wireOp",EDGE,"E3.9.23.19")])],"isStart":false});
            var Q2391;
            Q2391=makeQuery(id+"F3.opExtrude","CAP_EDGE",EDGE,{"disambiguationData":[OSD([sQuery(id+"F2.wireOp",EDGE,"E2.10.19.3")])],"isStart":false});
            var Q2392;
            Q2392=makeQuery(id+"F3.opExtrude","CAP_EDGE",EDGE,{"disambiguationData":[OSD([sQuery(id+"F2.wireOp",EDGE,"E2.17.19.3")])],"isStart":false});
            var Q2393;
            Q2393=makeQuery(id+"F3.opExtrude","CAP_EDGE",EDGE,{"disambiguationData":[OSD([sQuery(id+"F2.wireOp",EDGE,"E2.4.19.3")])],"isStart":false});
            var Q2394;
            Q2394=makeQuery(id+"F3.opExtrude","CAP_EDGE",EDGE,{"disambiguationData":[OSD([sQuery(id+"F2.wireOp",EDGE,"E2.11.19.3")])],"isStart":false});
            var Q2395;
            Q2395=makeQuery(id+"F3.opExtrude","CAP_EDGE",EDGE,{"disambiguationData":[OSD([sQuery(id+"F2.wireOp",EDGE,"E2.5.19.3")])],"isStart":false});
            var Q2396;
            Q2396=makeQuery(id+"F3.opExtrude","CAP_EDGE",EDGE,{"disambiguationData":[OSD([sQuery(id+"F2.wireOp",EDGE,"E3.9.24.19")])],"isStart":false});
            var Q2397;
            Q2397=makeQuery(id+"F3.opExtrude","CAP_EDGE",EDGE,{"disambiguationData":[OSD([sQuery(id+"F2.wireOp",EDGE,"E2.18.19.3")])],"isStart":false});
            var Q2398;
            Q2398=makeQuery(id+"F3.opExtrude","CAP_EDGE",EDGE,{"disambiguationData":[OSD([sQuery(id+"F2.wireOp",EDGE,"E3.9.25.19")])],"isStart":false});
            var Q2399;
            Q2399=makeQuery(id+"F3.opExtrude","CAP_EDGE",EDGE,{"disambiguationData":[OSD([sQuery(id+"F2.wireOp",EDGE,"E2.12.19.3")])],"isStart":false});
            fillet(context, id + "F4", {"entities" : qUnion([Q0, Q1, Q2, Q3, Q4, Q5, Q6, Q7, Q8, Q9, Q10, Q11, Q12, Q13, Q14, Q15, Q16, Q17, Q18, Q19, Q20, Q21, Q22, Q23, Q24, Q25, Q26, Q27, Q28, Q29, Q30, Q31, Q32, Q33, Q34, Q35, Q36, Q37, Q38, Q39, Q40, Q41, Q42, Q43, Q44, Q45, Q46, Q47, Q48, Q49, Q50, Q51, Q52, Q53, Q54, Q55, Q56, Q57, Q58, Q59, Q60, Q61, Q62, Q63, Q64, Q65, Q66, Q67, Q68, Q69, Q70, Q71, Q72, Q73, Q74, Q75, Q76, Q77, Q78, Q79, Q80, Q81, Q82, Q83, Q84, Q85, Q86, Q87, Q88, Q89, Q90, Q91, Q92, Q93, Q94, Q95, Q96, Q97, Q98, Q99, Q100, Q101, Q102, Q103, Q104, Q105, Q106, Q107, Q108, Q109, Q110, Q111, Q112, Q113, Q114, Q115, Q116, Q117, Q118, Q119, Q120, Q121, Q122, Q123, Q124, Q125, Q126, Q127, Q128, Q129, Q130, Q131, Q132, Q133, Q134, Q135, Q136, Q137, Q138, Q139, Q140, Q141, Q142, Q143, Q144, Q145, Q146, Q147, Q148, Q149, Q150, Q151, Q152, Q153, Q154, Q155, Q156, Q157, Q158, Q159, Q160, Q161, Q162, Q163, Q164, Q165, Q166, Q167, Q168, Q169, Q170, Q171, Q172, Q173, Q174, Q175, Q176, Q177, Q178, Q179, Q180, Q181, Q182, Q183, Q184, Q185, Q186, Q187, Q188, Q189, Q190, Q191, Q192, Q193, Q194, Q195, Q196, Q197, Q198, Q199, Q200, Q201, Q202, Q203, Q204, Q205, Q206, Q207, Q208, Q209, Q210, Q211, Q212, Q213, Q214, Q215, Q216, Q217, Q218, Q219, Q220, Q221, Q222, Q223, Q224, Q225, Q226, Q227, Q228, Q229, Q230, Q231, Q232, Q233, Q234, Q235, Q236, Q237, Q238, Q239, Q240, Q241, Q242, Q243, Q244, Q245, Q246, Q247, Q248, Q249, Q250, Q251, Q252, Q253, Q254, Q255, Q256, Q257, Q258, Q259, Q260, Q261, Q262, Q263, Q264, Q265, Q266, Q267, Q268, Q269, Q270, Q271, Q272, Q273, Q274, Q275, Q276, Q277, Q278, Q279, Q280, Q281, Q282, Q283, Q284, Q285, Q286, Q287, Q288, Q289, Q290, Q291, Q292, Q293, Q294, Q295, Q296, Q297, Q298, Q299, Q300, Q301, Q302, Q303, Q304, Q305, Q306, Q307, Q308, Q309, Q310, Q311, Q312, Q313, Q314, Q315, Q316, Q317, Q318, Q319, Q320, Q321, Q322, Q323, Q324, Q325, Q326, Q327, Q328, Q329, Q330, Q331, Q332, Q333, Q334, Q335, Q336, Q337, Q338, Q339, Q340, Q341, Q342, Q343, Q344, Q345, Q346, Q347, Q348, Q349, Q350, Q351, Q352, Q353, Q354, Q355, Q356, Q357, Q358, Q359, Q360, Q361, Q362, Q363, Q364, Q365, Q366, Q367, Q368, Q369, Q370, Q371, Q372, Q373, Q374, Q375, Q376, Q377, Q378, Q379, Q380, Q381, Q382, Q383, Q384, Q385, Q386, Q387, Q388, Q389, Q390, Q391, Q392, Q393, Q394, Q395, Q396, Q397, Q398, Q399, Q400, Q401, Q402, Q403, Q404, Q405, Q406, Q407, Q408, Q409, Q410, Q411, Q412, Q413, Q414, Q415, Q416, Q417, Q418, Q419, Q420, Q421, Q422, Q423, Q424, Q425, Q426, Q427, Q428, Q429, Q430, Q431, Q432, Q433, Q434, Q435, Q436, Q437, Q438, Q439, Q440, Q441, Q442, Q443, Q444, Q445, Q446, Q447, Q448, Q449, Q450, Q451, Q452, Q453, Q454, Q455, Q456, Q457, Q458, Q459, Q460, Q461, Q462, Q463, Q464, Q465, Q466, Q467, Q468, Q469, Q470, Q471, Q472, Q473, Q474, Q475, Q476, Q477, Q478, Q479, Q480, Q481, Q482, Q483, Q484, Q485, Q486, Q487, Q488, Q489, Q490, Q491, Q492, Q493, Q494, Q495, Q496, Q497, Q498, Q499, Q500, Q501, Q502, Q503, Q504, Q505, Q506, Q507, Q508, Q509, Q510, Q511, Q512, Q513, Q514, Q515, Q516, Q517, Q518, Q519, Q520, Q521, Q522, Q523, Q524, Q525, Q526, Q527, Q528, Q529, Q530, Q531, Q532, Q533, Q534, Q535, Q536, Q537, Q538, Q539, Q540, Q541, Q542, Q543, Q544, Q545, Q546, Q547, Q548, Q549, Q550, Q551, Q552, Q553, Q554, Q555, Q556, Q557, Q558, Q559, Q560, Q561, Q562, Q563, Q564, Q565, Q566, Q567, Q568, Q569, Q570, Q571, Q572, Q573, Q574, Q575, Q576, Q577, Q578, Q579, Q580, Q581, Q582, Q583, Q584, Q585, Q586, Q587, Q588, Q589, Q590, Q591, Q592, Q593, Q594, Q595, Q596, Q597, Q598, Q599, Q600, Q601, Q602, Q603, Q604, Q605, Q606, Q607, Q608, Q609, Q610, Q611, Q612, Q613, Q614, Q615, Q616, Q617, Q618, Q619, Q620, Q621, Q622, Q623, Q624, Q625, Q626, Q627, Q628, Q629, Q630, Q631, Q632, Q633, Q634, Q635, Q636, Q637, Q638, Q639, Q640, Q641, Q642, Q643, Q644, Q645, Q646, Q647, Q648, Q649, Q650, Q651, Q652, Q653, Q654, Q655, Q656, Q657, Q658, Q659, Q660, Q661, Q662, Q663, Q664, Q665, Q666, Q667, Q668, Q669, Q670, Q671, Q672, Q673, Q674, Q675, Q676, Q677, Q678, Q679, Q680, Q681, Q682, Q683, Q684, Q685, Q686, Q687, Q688, Q689, Q690, Q691, Q692, Q693, Q694, Q695, Q696, Q697, Q698, Q699, Q700, Q701, Q702, Q703, Q704, Q705, Q706, Q707, Q708, Q709, Q710, Q711, Q712, Q713, Q714, Q715, Q716, Q717, Q718, Q719, Q720, Q721, Q722, Q723, Q724, Q725, Q726, Q727, Q728, Q729, Q730, Q731, Q732, Q733, Q734, Q735, Q736, Q737, Q738, Q739, Q740, Q741, Q742, Q743, Q744, Q745, Q746, Q747, Q748, Q749, Q750, Q751, Q752, Q753, Q754, Q755, Q756, Q757, Q758, Q759, Q760, Q761, Q762, Q763, Q764, Q765, Q766, Q767, Q768, Q769, Q770, Q771, Q772, Q773, Q774, Q775, Q776, Q777, Q778, Q779, Q780, Q781, Q782, Q783, Q784, Q785, Q786, Q787, Q788, Q789, Q790, Q791, Q792, Q793, Q794, Q795, Q796, Q797, Q798, Q799, Q800, Q801, Q802, Q803, Q804, Q805, Q806, Q807, Q808, Q809, Q810, Q811, Q812, Q813, Q814, Q815, Q816, Q817, Q818, Q819, Q820, Q821, Q822, Q823, Q824, Q825, Q826, Q827, Q828, Q829, Q830, Q831, Q832, Q833, Q834, Q835, Q836, Q837, Q838, Q839, Q840, Q841, Q842, Q843, Q844, Q845, Q846, Q847, Q848, Q849, Q850, Q851, Q852, Q853, Q854, Q855, Q856, Q857, Q858, Q859, Q860, Q861, Q862, Q863, Q864, Q865, Q866, Q867, Q868, Q869, Q870, Q871, Q872, Q873, Q874, Q875, Q876, Q877, Q878, Q879, Q880, Q881, Q882, Q883, Q884, Q885, Q886, Q887, Q888, Q889, Q890, Q891, Q892, Q893, Q894, Q895, Q896, Q897, Q898, Q899, Q900, Q901, Q902, Q903, Q904, Q905, Q906, Q907, Q908, Q909, Q910, Q911, Q912, Q913, Q914, Q915, Q916, Q917, Q918, Q919, Q920, Q921, Q922, Q923, Q924, Q925, Q926, Q927, Q928, Q929, Q930, Q931, Q932, Q933, Q934, Q935, Q936, Q937, Q938, Q939, Q940, Q941, Q942, Q943, Q944, Q945, Q946, Q947, Q948, Q949, Q950, Q951, Q952, Q953, Q954, Q955, Q956, Q957, Q958, Q959, Q960, Q961, Q962, Q963, Q964, Q965, Q966, Q967, Q968, Q969, Q970, Q971, Q972, Q973, Q974, Q975, Q976, Q977, Q978, Q979, Q980, Q981, Q982, Q983, Q984, Q985, Q986, Q987, Q988, Q989, Q990, Q991, Q992, Q993, Q994, Q995, Q996, Q997, Q998, Q999, Q1000, Q1001, Q1002, Q1003, Q1004, Q1005, Q1006, Q1007, Q1008, Q1009, Q1010, Q1011, Q1012, Q1013, Q1014, Q1015, Q1016, Q1017, Q1018, Q1019, Q1020, Q1021, Q1022, Q1023, Q1024, Q1025, Q1026, Q1027, Q1028, Q1029, Q1030, Q1031, Q1032, Q1033, Q1034, Q1035, Q1036, Q1037, Q1038, Q1039, Q1040, Q1041, Q1042, Q1043, Q1044, Q1045, Q1046, Q1047, Q1048, Q1049, Q1050, Q1051, Q1052, Q1053, Q1054, Q1055, Q1056, Q1057, Q1058, Q1059, Q1060, Q1061, Q1062, Q1063, Q1064, Q1065, Q1066, Q1067, Q1068, Q1069, Q1070, Q1071, Q1072, Q1073, Q1074, Q1075, Q1076, Q1077, Q1078, Q1079, Q1080, Q1081, Q1082, Q1083, Q1084, Q1085, Q1086, Q1087, Q1088, Q1089, Q1090, Q1091, Q1092, Q1093, Q1094, Q1095, Q1096, Q1097, Q1098, Q1099, Q1100, Q1101, Q1102, Q1103, Q1104, Q1105, Q1106, Q1107, Q1108, Q1109, Q1110, Q1111, Q1112, Q1113, Q1114, Q1115, Q1116, Q1117, Q1118, Q1119, Q1120, Q1121, Q1122, Q1123, Q1124, Q1125, Q1126, Q1127, Q1128, Q1129, Q1130, Q1131, Q1132, Q1133, Q1134, Q1135, Q1136, Q1137, Q1138, Q1139, Q1140, Q1141, Q1142, Q1143, Q1144, Q1145, Q1146, Q1147, Q1148, Q1149, Q1150, Q1151, Q1152, Q1153, Q1154, Q1155, Q1156, Q1157, Q1158, Q1159, Q1160, Q1161, Q1162, Q1163, Q1164, Q1165, Q1166, Q1167, Q1168, Q1169, Q1170, Q1171, Q1172, Q1173, Q1174, Q1175, Q1176, Q1177, Q1178, Q1179, Q1180, Q1181, Q1182, Q1183, Q1184, Q1185, Q1186, Q1187, Q1188, Q1189, Q1190, Q1191, Q1192, Q1193, Q1194, Q1195, Q1196, Q1197, Q1198, Q1199, Q1200, Q1201, Q1202, Q1203, Q1204, Q1205, Q1206, Q1207, Q1208, Q1209, Q1210, Q1211, Q1212, Q1213, Q1214, Q1215, Q1216, Q1217, Q1218, Q1219, Q1220, Q1221, Q1222, Q1223, Q1224, Q1225, Q1226, Q1227, Q1228, Q1229, Q1230, Q1231, Q1232, Q1233, Q1234, Q1235, Q1236, Q1237, Q1238, Q1239, Q1240, Q1241, Q1242, Q1243, Q1244, Q1245, Q1246, Q1247, Q1248, Q1249, Q1250, Q1251, Q1252, Q1253, Q1254, Q1255, Q1256, Q1257, Q1258, Q1259, Q1260, Q1261, Q1262, Q1263, Q1264, Q1265, Q1266, Q1267, Q1268, Q1269, Q1270, Q1271, Q1272, Q1273, Q1274, Q1275, Q1276, Q1277, Q1278, Q1279, Q1280, Q1281, Q1282, Q1283, Q1284, Q1285, Q1286, Q1287, Q1288, Q1289, Q1290, Q1291, Q1292, Q1293, Q1294, Q1295, Q1296, Q1297, Q1298, Q1299, Q1300, Q1301, Q1302, Q1303, Q1304, Q1305, Q1306, Q1307, Q1308, Q1309, Q1310, Q1311, Q1312, Q1313, Q1314, Q1315, Q1316, Q1317, Q1318, Q1319, Q1320, Q1321, Q1322, Q1323, Q1324, Q1325, Q1326, Q1327, Q1328, Q1329, Q1330, Q1331, Q1332, Q1333, Q1334, Q1335, Q1336, Q1337, Q1338, Q1339, Q1340, Q1341, Q1342, Q1343, Q1344, Q1345, Q1346, Q1347, Q1348, Q1349, Q1350, Q1351, Q1352, Q1353, Q1354, Q1355, Q1356, Q1357, Q1358, Q1359, Q1360, Q1361, Q1362, Q1363, Q1364, Q1365, Q1366, Q1367, Q1368, Q1369, Q1370, Q1371, Q1372, Q1373, Q1374, Q1375, Q1376, Q1377, Q1378, Q1379, Q1380, Q1381, Q1382, Q1383, Q1384, Q1385, Q1386, Q1387, Q1388, Q1389, Q1390, Q1391, Q1392, Q1393, Q1394, Q1395, Q1396, Q1397, Q1398, Q1399, Q1400, Q1401, Q1402, Q1403, Q1404, Q1405, Q1406, Q1407, Q1408, Q1409, Q1410, Q1411, Q1412, Q1413, Q1414, Q1415, Q1416, Q1417, Q1418, Q1419, Q1420, Q1421, Q1422, Q1423, Q1424, Q1425, Q1426, Q1427, Q1428, Q1429, Q1430, Q1431, Q1432, Q1433, Q1434, Q1435, Q1436, Q1437, Q1438, Q1439, Q1440, Q1441, Q1442, Q1443, Q1444, Q1445, Q1446, Q1447, Q1448, Q1449, Q1450, Q1451, Q1452, Q1453, Q1454, Q1455, Q1456, Q1457, Q1458, Q1459, Q1460, Q1461, Q1462, Q1463, Q1464, Q1465, Q1466, Q1467, Q1468, Q1469, Q1470, Q1471, Q1472, Q1473, Q1474, Q1475, Q1476, Q1477, Q1478, Q1479, Q1480, Q1481, Q1482, Q1483, Q1484, Q1485, Q1486, Q1487, Q1488, Q1489, Q1490, Q1491, Q1492, Q1493, Q1494, Q1495, Q1496, Q1497, Q1498, Q1499, Q1500, Q1501, Q1502, Q1503, Q1504, Q1505, Q1506, Q1507, Q1508, Q1509, Q1510, Q1511, Q1512, Q1513, Q1514, Q1515, Q1516, Q1517, Q1518, Q1519, Q1520, Q1521, Q1522, Q1523, Q1524, Q1525, Q1526, Q1527, Q1528, Q1529, Q1530, Q1531, Q1532, Q1533, Q1534, Q1535, Q1536, Q1537, Q1538, Q1539, Q1540, Q1541, Q1542, Q1543, Q1544, Q1545, Q1546, Q1547, Q1548, Q1549, Q1550, Q1551, Q1552, Q1553, Q1554, Q1555, Q1556, Q1557, Q1558, Q1559, Q1560, Q1561, Q1562, Q1563, Q1564, Q1565, Q1566, Q1567, Q1568, Q1569, Q1570, Q1571, Q1572, Q1573, Q1574, Q1575, Q1576, Q1577, Q1578, Q1579, Q1580, Q1581, Q1582, Q1583, Q1584, Q1585, Q1586, Q1587, Q1588, Q1589, Q1590, Q1591, Q1592, Q1593, Q1594, Q1595, Q1596, Q1597, Q1598, Q1599, Q1600, Q1601, Q1602, Q1603, Q1604, Q1605, Q1606, Q1607, Q1608, Q1609, Q1610, Q1611, Q1612, Q1613, Q1614, Q1615, Q1616, Q1617, Q1618, Q1619, Q1620, Q1621, Q1622, Q1623, Q1624, Q1625, Q1626, Q1627, Q1628, Q1629, Q1630, Q1631, Q1632, Q1633, Q1634, Q1635, Q1636, Q1637, Q1638, Q1639, Q1640, Q1641, Q1642, Q1643, Q1644, Q1645, Q1646, Q1647, Q1648, Q1649, Q1650, Q1651, Q1652, Q1653, Q1654, Q1655, Q1656, Q1657, Q1658, Q1659, Q1660, Q1661, Q1662, Q1663, Q1664, Q1665, Q1666, Q1667, Q1668, Q1669, Q1670, Q1671, Q1672, Q1673, Q1674, Q1675, Q1676, Q1677, Q1678, Q1679, Q1680, Q1681, Q1682, Q1683, Q1684, Q1685, Q1686, Q1687, Q1688, Q1689, Q1690, Q1691, Q1692, Q1693, Q1694, Q1695, Q1696, Q1697, Q1698, Q1699, Q1700, Q1701, Q1702, Q1703, Q1704, Q1705, Q1706, Q1707, Q1708, Q1709, Q1710, Q1711, Q1712, Q1713, Q1714, Q1715, Q1716, Q1717, Q1718, Q1719, Q1720, Q1721, Q1722, Q1723, Q1724, Q1725, Q1726, Q1727, Q1728, Q1729, Q1730, Q1731, Q1732, Q1733, Q1734, Q1735, Q1736, Q1737, Q1738, Q1739, Q1740, Q1741, Q1742, Q1743, Q1744, Q1745, Q1746, Q1747, Q1748, Q1749, Q1750, Q1751, Q1752, Q1753, Q1754, Q1755, Q1756, Q1757, Q1758, Q1759, Q1760, Q1761, Q1762, Q1763, Q1764, Q1765, Q1766, Q1767, Q1768, Q1769, Q1770, Q1771, Q1772, Q1773, Q1774, Q1775, Q1776, Q1777, Q1778, Q1779, Q1780, Q1781, Q1782, Q1783, Q1784, Q1785, Q1786, Q1787, Q1788, Q1789, Q1790, Q1791, Q1792, Q1793, Q1794, Q1795, Q1796, Q1797, Q1798, Q1799, Q1800, Q1801, Q1802, Q1803, Q1804, Q1805, Q1806, Q1807, Q1808, Q1809, Q1810, Q1811, Q1812, Q1813, Q1814, Q1815, Q1816, Q1817, Q1818, Q1819, Q1820, Q1821, Q1822, Q1823, Q1824, Q1825, Q1826, Q1827, Q1828, Q1829, Q1830, Q1831, Q1832, Q1833, Q1834, Q1835, Q1836, Q1837, Q1838, Q1839, Q1840, Q1841, Q1842, Q1843, Q1844, Q1845, Q1846, Q1847, Q1848, Q1849, Q1850, Q1851, Q1852, Q1853, Q1854, Q1855, Q1856, Q1857, Q1858, Q1859, Q1860, Q1861, Q1862, Q1863, Q1864, Q1865, Q1866, Q1867, Q1868, Q1869, Q1870, Q1871, Q1872, Q1873, Q1874, Q1875, Q1876, Q1877, Q1878, Q1879, Q1880, Q1881, Q1882, Q1883, Q1884, Q1885, Q1886, Q1887, Q1888, Q1889, Q1890, Q1891, Q1892, Q1893, Q1894, Q1895, Q1896, Q1897, Q1898, Q1899, Q1900, Q1901, Q1902, Q1903, Q1904, Q1905, Q1906, Q1907, Q1908, Q1909, Q1910, Q1911, Q1912, Q1913, Q1914, Q1915, Q1916, Q1917, Q1918, Q1919, Q1920, Q1921, Q1922, Q1923, Q1924, Q1925, Q1926, Q1927, Q1928, Q1929, Q1930, Q1931, Q1932, Q1933, Q1934, Q1935, Q1936, Q1937, Q1938, Q1939, Q1940, Q1941, Q1942, Q1943, Q1944, Q1945, Q1946, Q1947, Q1948, Q1949, Q1950, Q1951, Q1952, Q1953, Q1954, Q1955, Q1956, Q1957, Q1958, Q1959, Q1960, Q1961, Q1962, Q1963, Q1964, Q1965, Q1966, Q1967, Q1968, Q1969, Q1970, Q1971, Q1972, Q1973, Q1974, Q1975, Q1976, Q1977, Q1978, Q1979, Q1980, Q1981, Q1982, Q1983, Q1984, Q1985, Q1986, Q1987, Q1988, Q1989, Q1990, Q1991, Q1992, Q1993, Q1994, Q1995, Q1996, Q1997, Q1998, Q1999, Q2000, Q2001, Q2002, Q2003, Q2004, Q2005, Q2006, Q2007, Q2008, Q2009, Q2010, Q2011, Q2012, Q2013, Q2014, Q2015, Q2016, Q2017, Q2018, Q2019, Q2020, Q2021, Q2022, Q2023, Q2024, Q2025, Q2026, Q2027, Q2028, Q2029, Q2030, Q2031, Q2032, Q2033, Q2034, Q2035, Q2036, Q2037, Q2038, Q2039, Q2040, Q2041, Q2042, Q2043, Q2044, Q2045, Q2046, Q2047, Q2048, Q2049, Q2050, Q2051, Q2052, Q2053, Q2054, Q2055, Q2056, Q2057, Q2058, Q2059, Q2060, Q2061, Q2062, Q2063, Q2064, Q2065, Q2066, Q2067, Q2068, Q2069, Q2070, Q2071, Q2072, Q2073, Q2074, Q2075, Q2076, Q2077, Q2078, Q2079, Q2080, Q2081, Q2082, Q2083, Q2084, Q2085, Q2086, Q2087, Q2088, Q2089, Q2090, Q2091, Q2092, Q2093, Q2094, Q2095, Q2096, Q2097, Q2098, Q2099, Q2100, Q2101, Q2102, Q2103, Q2104, Q2105, Q2106, Q2107, Q2108, Q2109, Q2110, Q2111, Q2112, Q2113, Q2114, Q2115, Q2116, Q2117, Q2118, Q2119, Q2120, Q2121, Q2122, Q2123, Q2124, Q2125, Q2126, Q2127, Q2128, Q2129, Q2130, Q2131, Q2132, Q2133, Q2134, Q2135, Q2136, Q2137, Q2138, Q2139, Q2140, Q2141, Q2142, Q2143, Q2144, Q2145, Q2146, Q2147, Q2148, Q2149, Q2150, Q2151, Q2152, Q2153, Q2154, Q2155, Q2156, Q2157, Q2158, Q2159, Q2160, Q2161, Q2162, Q2163, Q2164, Q2165, Q2166, Q2167, Q2168, Q2169, Q2170, Q2171, Q2172, Q2173, Q2174, Q2175, Q2176, Q2177, Q2178, Q2179, Q2180, Q2181, Q2182, Q2183, Q2184, Q2185, Q2186, Q2187, Q2188, Q2189, Q2190, Q2191, Q2192, Q2193, Q2194, Q2195, Q2196, Q2197, Q2198, Q2199, Q2200, Q2201, Q2202, Q2203, Q2204, Q2205, Q2206, Q2207, Q2208, Q2209, Q2210, Q2211, Q2212, Q2213, Q2214, Q2215, Q2216, Q2217, Q2218, Q2219, Q2220, Q2221, Q2222, Q2223, Q2224, Q2225, Q2226, Q2227, Q2228, Q2229, Q2230, Q2231, Q2232, Q2233, Q2234, Q2235, Q2236, Q2237, Q2238, Q2239, Q2240, Q2241, Q2242, Q2243, Q2244, Q2245, Q2246, Q2247, Q2248, Q2249, Q2250, Q2251, Q2252, Q2253, Q2254, Q2255, Q2256, Q2257, Q2258, Q2259, Q2260, Q2261, Q2262, Q2263, Q2264, Q2265, Q2266, Q2267, Q2268, Q2269, Q2270, Q2271, Q2272, Q2273, Q2274, Q2275, Q2276, Q2277, Q2278, Q2279, Q2280, Q2281, Q2282, Q2283, Q2284, Q2285, Q2286, Q2287, Q2288, Q2289, Q2290, Q2291, Q2292, Q2293, Q2294, Q2295, Q2296, Q2297, Q2298, Q2299, Q2300, Q2301, Q2302, Q2303, Q2304, Q2305, Q2306, Q2307, Q2308, Q2309, Q2310, Q2311, Q2312, Q2313, Q2314, Q2315, Q2316, Q2317, Q2318, Q2319, Q2320, Q2321, Q2322, Q2323, Q2324, Q2325, Q2326, Q2327, Q2328, Q2329, Q2330, Q2331, Q2332, Q2333, Q2334, Q2335, Q2336, Q2337, Q2338, Q2339, Q2340, Q2341, Q2342, Q2343, Q2344, Q2345, Q2346, Q2347, Q2348, Q2349, Q2350, Q2351, Q2352, Q2353, Q2354, Q2355, Q2356, Q2357, Q2358, Q2359, Q2360, Q2361, Q2362, Q2363, Q2364, Q2365, Q2366, Q2367, Q2368, Q2369, Q2370, Q2371, Q2372, Q2373, Q2374, Q2375, Q2376, Q2377, Q2378, Q2379, Q2380, Q2381, Q2382, Q2383, Q2384, Q2385, Q2386, Q2387, Q2388, Q2389, Q2390, Q2391, Q2392, Q2393, Q2394, Q2395, Q2396, Q2397, Q2398, Q2399]), "radius" : 5.08 * mm, "tangentPropagation" : true, "allowEdgeOverflow" : false});
        }
        {
            var Q0;
            Q0=makeQuery(id+"F3.opExtrude","CAP_FACE",FACE,{"disambiguationData":[OSD([sQuery(id+"F2.wireOp",EDGE,"E2.13.0.0"),sQuery(id+"F2.wireOp",EDGE,"E2.13.0.1"),sQuery(id+"F2.wireOp",EDGE,"E2.13.0.2"),sQuery(id+"F2.wireOp",EDGE,"E2.13.0.3")])],"isStart":false});
            shell(context, id + "F5", {"entities" : qUnion([Q0]), "thickness" : 2.54 * mm});
        }
    });
